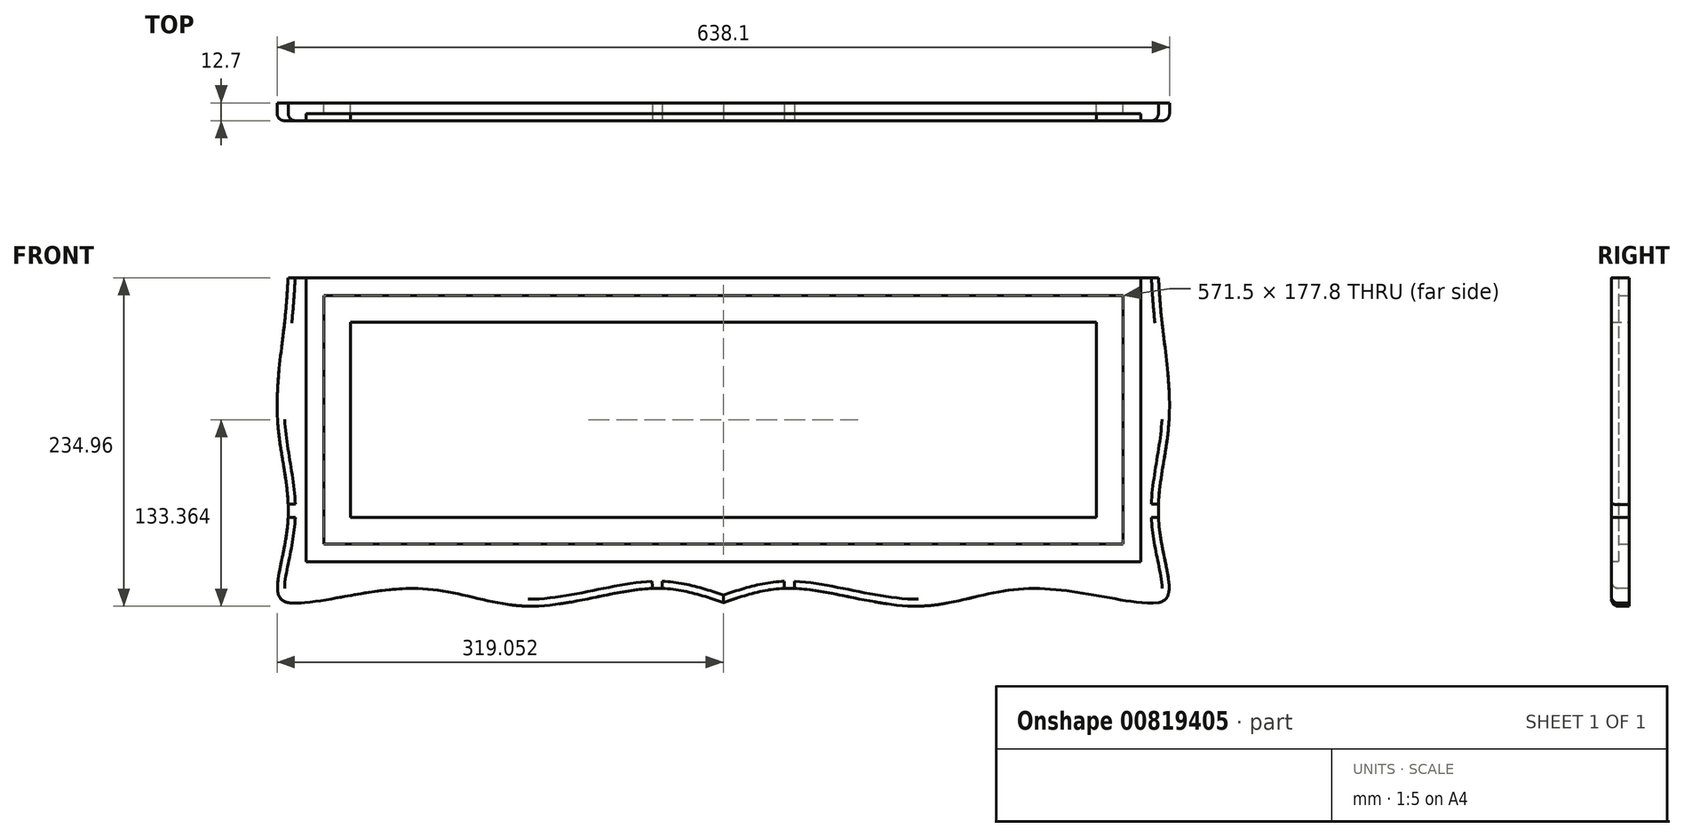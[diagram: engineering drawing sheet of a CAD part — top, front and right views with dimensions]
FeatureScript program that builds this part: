
annotation { "Feature Type Name" : "Feature", "Feature Type Description" : "" }
export const myFeature = defineFeature(function(context is Context, id is Id, definition is map)
    precondition{}
    {
        {
            var Q0;
            Q0=qCreatedBy(makeId("Front.planeOp"),FACE);
            var sketch = newSketch(context, id + "F0", { "sketchPlane" : qUnion([Q0])});
            skLineSegment(sketch, "E0.bottom", {"start": v(-290.57, 108.48) * mm, "end": v(331.73, 108.48) * mm});
            skLineSegment(sketch, "E0.top", {"start": v(-290.57, -113.77) * mm, "end": v(331.73, -113.77) * mm});
            skLineSegment(sketch, "E0.left", {"start": v(-290.57, 108.48) * mm, "end": v(-290.57, -113.77) * mm});
            skLineSegment(sketch, "E0.right", {"start": v(331.73, 108.48) * mm, "end": v(331.73, -113.77) * mm});
            skPoint(sketch, "E1", {"position": v(20.58, 108.48) * mm});
            skLineSegment(sketch, "E2.bottom", {"start": v(-246.12, 76.73) * mm, "end": v(287.28, 76.73) * mm});
            skLineSegment(sketch, "E2.top", {"start": v(-246.12, -62.97) * mm, "end": v(287.28, -62.97) * mm});
            skLineSegment(sketch, "E2.left", {"start": v(-246.12, 76.73) * mm, "end": v(-246.12, -62.97) * mm});
            skLineSegment(sketch, "E2.right", {"start": v(287.28, 76.73) * mm, "end": v(287.28, -62.97) * mm});
            skLineSegment(sketch, "E3.bottom", {"start": v(-265.17, 95.78) * mm, "end": v(306.33, 95.78) * mm});
            skLineSegment(sketch, "E3.top", {"start": v(-265.17, -82.02) * mm, "end": v(306.33, -82.02) * mm});
            skLineSegment(sketch, "E3.left", {"start": v(-265.17, 95.78) * mm, "end": v(-265.17, -82.02) * mm});
            skLineSegment(sketch, "E3.right", {"start": v(306.33, 95.78) * mm, "end": v(306.33, -82.02) * mm});
            skSolve(sketch);
        }
        {
            var Q0;
            Q0=makeQuery(id+"F0.imprint","IMPRINT",FACE,{"disambiguationData":[TD([[makeQuery(id+"F0.imprint","IMPRINT",EDGE,{"derivedFrom":sQuery(id+"F0.wireOp",EDGE,"E0.bottom")}),-1.0]])]});
            var Q1;
            Q1=makeQuery(id+"F0.imprint","IMPRINT",FACE,{"disambiguationData":[TD([[makeQuery(id+"F0.imprint","IMPRINT",EDGE,{"derivedFrom":sQuery(id+"F0.wireOp",EDGE,"E2.bottom")}),-1.0]])]});
            extrude(context, id + "F1", {"entities" : qUnion([Q0, Q1]), "depth" : 12.7 * mm, "offsetDistance" : 25.4 * mm});
        }
        {
            var Q0;
            Q0=makeQuery(id+"F1.opExtrude","CAP_FACE",FACE,{"disambiguationData":[OSD([sQuery(id+"F0.wireOp",EDGE,"E0.bottom"),sQuery(id+"F0.wireOp",EDGE,"E0.top"),sQuery(id+"F0.wireOp",EDGE,"E0.left"),sQuery(id+"F0.wireOp",EDGE,"E0.right")])],"isStart":false});
            var sketch = newSketch(context, id + "F2", { "sketchPlane" : qUnion([Q0])});
            skPoint(sketch, "E4", {"position": v(20.58, 108.48) * mm});
            skSolve(sketch);
        }
        {
            var Q0;
            {var subQ0=sQuery(id+"F0.wireOp",EDGE,"E0.right");var subQ1=sQuery(id+"F0.wireOp",EDGE,"E0.bottom");var subQ2=sQuery(id+"F0.wireOp",EDGE,"E0.left");var subQ3=sQuery(id+"F0.wireOp",EDGE,"E0.top");Q0=makeQuery(id+"FjgwLtvUwF4HY63_1.boolean.opBoolean","SPLIT",FACE,{"disambiguationData":[TD([makeQuery(id+"F1.opExtrude","SWEPT_FACE",FACE,{"disambiguationData":[OSD([subQ1])]})])],"derivedFrom":makeQuery(id+"F1.opExtrude","CAP_FACE",FACE,{"disambiguationData":[OSD([subQ1,subQ3,subQ2,subQ0])],"isStart":false})});}
            var sketch = newSketch(context, id + "F3", { "sketchPlane" : qUnion([Q0])});
            skPoint(sketch, "E5", {"position": v(-290.57, -62.97) * mm});
            skPoint(sketch, "E6", {"position": v(-290.57, 6.88) * mm});
            skPoint(sketch, "E7", {"position": v(-290.57, 76.73) * mm});
            skLineSegment(sketch, "E8", {"start": v(-290.57, 76.73) * mm, "end": v(-293.1, 76.73) * mm});
            skLineSegment(sketch, "E9", {"start": v(-290.57, 6.88) * mm, "end": v(-298.19, 6.88) * mm});
            skLineSegment(sketch, "E10", {"start": v(-290.57, -113.77) * mm, "end": v(-298.19, -113.77) * mm});
            skLineSegment(sketch, "E11", {"start": v(-290.57, -113.77) * mm, "end": v(-290.57, -123.93) * mm});
            skPoint(sketch, "E12", {"position": v(-201.67, -113.77) * mm});
            skPoint(sketch, "E13", {"position": v(20.58, -113.77) * mm});
            skPoint(sketch, "E14", {"position": v(-30.22, -113.77) * mm});
            skPoint(sketch, "E15", {"position": v(-119.12, -113.77) * mm});
            skPoint(sketch, "E16", {"position": v(71.38, -113.77) * mm});
            skPoint(sketch, "E17", {"position": v(160.28, -113.77) * mm});
            skPoint(sketch, "E18", {"position": v(242.83, -113.77) * mm});
            skPoint(sketch, "E19", {"position": v(331.73, -62.97) * mm});
            skPoint(sketch, "E20", {"position": v(331.73, 6.88) * mm});
            skPoint(sketch, "E21", {"position": v(331.73, 76.73) * mm});
            skLineSegment(sketch, "E22", {"start": v(331.73, 76.73) * mm, "end": v(334.27, 76.73) * mm});
            skLineSegment(sketch, "E23", {"start": v(331.73, 6.88) * mm, "end": v(339.35, 6.88) * mm});
            skLineSegment(sketch, "E24", {"start": v(331.73, -113.77) * mm, "end": v(339.35, -113.77) * mm});
            skLineSegment(sketch, "E25", {"start": v(331.73, -113.77) * mm, "end": v(331.73, -123.93) * mm});
            skLineSegment(sketch, "E26", {"start": v(-119.12, -113.77) * mm, "end": v(-119.12, -126.47) * mm});
            skLineSegment(sketch, "E27", {"start": v(20.58, -113.77) * mm, "end": v(20.58, -123.93) * mm});
            skLineSegment(sketch, "E28", {"start": v(160.28, -113.77) * mm, "end": v(160.28, -126.47) * mm});
            skFitSpline(sketch, "E29", {"points": [v(-290.57, 108.48) * mm, v(-293.1, 76.73) * mm, v(-298.19, 6.88) * mm, v(-290.57, -62.97) * mm, v(-298.19, -113.77) * mm, v(-290.57, -123.93) * mm, v(-201.67, -113.77) * mm, v(-119.12, -126.47) * mm, v(-30.22, -113.77) * mm, v(20.58, -123.93) * mm], "startDerivative": vector(-26.2, -341.82) * mm, "endDerivative": vector(438.15, -148.5) * mm});
            skFitSpline(sketch, "E30", {"points": [v(331.73, 108.48) * mm, v(334.27, 76.73) * mm, v(339.35, 6.88) * mm, v(331.73, -62.97) * mm, v(339.35, -113.77) * mm, v(331.73, -123.93) * mm, v(242.83, -113.77) * mm, v(160.28, -126.47) * mm, v(71.38, -113.77) * mm, v(20.58, -123.93) * mm], "startDerivative": vector(26.2, -341.82) * mm, "endDerivative": vector(-438.15, -148.5) * mm});
            skSolve(sketch);
        }
        {
            var Q0;
            {var subQ0=sQuery(id+"F3.wireOp",EDGE,"E27");Q0=makeQuery(id+"F3.imprint","IMPRINT",FACE,{"disambiguationData":[TD([[makeQuery(id+"F3.imprint","IMPRINT",EDGE,{"derivedFrom":subQ0}),-1.0]])]});}
            var Q1;
            {var subQ0=sQuery(id+"F3.wireOp",EDGE,"E27");Q1=makeQuery(id+"F3.imprint","IMPRINT",FACE,{"disambiguationData":[TD([[makeQuery(id+"F3.imprint","IMPRINT",EDGE,{"derivedFrom":subQ0}),1.0]])]});}
            var Q2;
            {var subQ0=sQuery(id+"F3.wireOp",EDGE,"E26");Q2=makeQuery(id+"F3.imprint","IMPRINT",FACE,{"disambiguationData":[TD([[makeQuery(id+"F3.imprint","IMPRINT",EDGE,{"derivedFrom":subQ0}),1.0]])]});}
            var Q3;
            {var subQ0=sQuery(id+"F3.wireOp",EDGE,"E26");Q3=makeQuery(id+"F3.imprint","IMPRINT",FACE,{"disambiguationData":[TD([[makeQuery(id+"F3.imprint","IMPRINT",EDGE,{"derivedFrom":subQ0}),-1.0]])]});}
            var Q4;
            {var subQ0=sQuery(id+"F3.wireOp",EDGE,"E11");Q4=makeQuery(id+"F3.imprint","IMPRINT",FACE,{"disambiguationData":[TD([[makeQuery(id+"F3.imprint","IMPRINT",EDGE,{"derivedFrom":subQ0}),1.0]])]});}
            var Q5;
            {var subQ0=sQuery(id+"F3.wireOp",EDGE,"E10");Q5=makeQuery(id+"F3.imprint","IMPRINT",FACE,{"disambiguationData":[TD([[makeQuery(id+"F3.imprint","IMPRINT",EDGE,{"derivedFrom":subQ0}),1.0]])]});}
            var Q6;
            {var subQ0=sQuery(id+"F3.wireOp",EDGE,"E10");Q6=makeQuery(id+"F3.imprint","IMPRINT",FACE,{"disambiguationData":[TD([[makeQuery(id+"F3.imprint","IMPRINT",EDGE,{"derivedFrom":subQ0}),-1.0]])]});}
            var Q7;
            {var subQ0=sQuery(id+"F3.wireOp",EDGE,"E9");Q7=makeQuery(id+"F3.imprint","IMPRINT",FACE,{"disambiguationData":[TD([[makeQuery(id+"F3.imprint","IMPRINT",EDGE,{"derivedFrom":subQ0}),1.0]])]});}
            var Q8;
            {var subQ0=sQuery(id+"F3.wireOp",EDGE,"E8");Q8=makeQuery(id+"F3.imprint","IMPRINT",FACE,{"disambiguationData":[TD([[makeQuery(id+"F3.imprint","IMPRINT",EDGE,{"derivedFrom":subQ0}),1.0]])]});}
            var Q9;
            {var subQ0=makeQuery(id+"F1.opExtrude","CAP_EDGE",EDGE,{"disambiguationData":[OSD([sQuery(id+"F0.wireOp",EDGE,"E0.bottom")])],"isStart":false});Q9=makeQuery(id+"F3.imprint","IMPRINT",FACE,{"disambiguationData":[TD([[makeQuery(id+"F3.imprint","IMPRINT",EDGE,{"derivedFrom":subQ0}),-1.0]])]});}
            var Q10;
            {var subQ0=sQuery(id+"F3.wireOp",EDGE,"E28");Q10=makeQuery(id+"F3.imprint","IMPRINT",FACE,{"disambiguationData":[TD([[makeQuery(id+"F3.imprint","IMPRINT",EDGE,{"derivedFrom":subQ0}),-1.0]])]});}
            var Q11;
            {var subQ0=sQuery(id+"F3.wireOp",EDGE,"E28");Q11=makeQuery(id+"F3.imprint","IMPRINT",FACE,{"disambiguationData":[TD([[makeQuery(id+"F3.imprint","IMPRINT",EDGE,{"derivedFrom":subQ0}),1.0]])]});}
            var Q12;
            {var subQ0=sQuery(id+"F3.wireOp",EDGE,"E25");Q12=makeQuery(id+"F3.imprint","IMPRINT",FACE,{"disambiguationData":[TD([[makeQuery(id+"F3.imprint","IMPRINT",EDGE,{"derivedFrom":subQ0}),-1.0]])]});}
            var Q13;
            {var subQ0=sQuery(id+"F3.wireOp",EDGE,"E24");Q13=makeQuery(id+"F3.imprint","IMPRINT",FACE,{"disambiguationData":[TD([[makeQuery(id+"F3.imprint","IMPRINT",EDGE,{"derivedFrom":subQ0}),-1.0]])]});}
            var Q14;
            {var subQ0=sQuery(id+"F3.wireOp",EDGE,"E24");Q14=makeQuery(id+"F3.imprint","IMPRINT",FACE,{"disambiguationData":[TD([[makeQuery(id+"F3.imprint","IMPRINT",EDGE,{"derivedFrom":subQ0}),1.0]])]});}
            var Q15;
            {var subQ0=sQuery(id+"F3.wireOp",EDGE,"E23");Q15=makeQuery(id+"F3.imprint","IMPRINT",FACE,{"disambiguationData":[TD([[makeQuery(id+"F3.imprint","IMPRINT",EDGE,{"derivedFrom":subQ0}),-1.0]])]});}
            var Q16;
            {var subQ0=sQuery(id+"F3.wireOp",EDGE,"E22");Q16=makeQuery(id+"F3.imprint","IMPRINT",FACE,{"disambiguationData":[TD([[makeQuery(id+"F3.imprint","IMPRINT",EDGE,{"derivedFrom":subQ0}),-1.0]])]});}
            var Q17;
            {var subQ0=sQuery(id+"F3.wireOp",EDGE,"E22");Q17=makeQuery(id+"F3.imprint","IMPRINT",FACE,{"disambiguationData":[TD([[makeQuery(id+"F3.imprint","IMPRINT",EDGE,{"derivedFrom":subQ0}),1.0]])]});}
            var Q18;
            {var subQ0=sQuery(id+"F3.wireOp",EDGE,"E8");Q18=makeQuery(id+"F3.imprint","IMPRINT",FACE,{"disambiguationData":[TD([[makeQuery(id+"F3.imprint","IMPRINT",EDGE,{"derivedFrom":subQ0}),-1.0]])]});}
            extrude(context, id + "F4", {"entities" : qUnion([Q0, Q1, Q2, Q3, Q4, Q5, Q6, Q7, Q8, Q9, Q10, Q11, Q12, Q13, Q14, Q15, Q16, Q17, Q18]), "operationType" : NewBodyOperationType.ADD, "depth" : -12.7 * mm, "offsetDistance" : 25.4 * mm});
        }
        {
            var Q0;
            {var subQ0=sQuery(id+"F3.wireOp",EDGE,"8007402e-1a4e-4a06-85a5-2af08e553504");var subQ1=sQuery(id+"F0.wireOp",EDGE,"E0.left");var subQ2=sQuery(id+"F0.wireOp",EDGE,"E0.top");var subQ3=sQuery(id+"F0.wireOp",EDGE,"E0.bottom");Q0=makeQuery(id+"F4.boolean.opBoolean","SPLIT",EDGE,{"disambiguationData":[TD([makeQuery(id+"F1.opExtrude","CAP_FACE",FACE,{"disambiguationData":[OSD([subQ3,subQ2,subQ1,sQuery(id+"F0.wireOp",EDGE,"E0.right")])],"isStart":false}),makeQuery(id+"F1.opExtrude","SWEPT_FACE",FACE,{"disambiguationData":[OSD([subQ2])]}),makeQuery(id+"F1.opExtrude","SWEPT_FACE",FACE,{"disambiguationData":[OSD([subQ1])]}),makeQuery(id+"F4.opExtrude","SWEPT_FACE",FACE,{"disambiguationData":[OSD([subQ0])]}),makeQuery(id+"F4.opExtrude","CAP_FACE",FACE,{"disambiguationData":[OSD([subQ3,sQuery(id+"F2.wireOp",EDGE,"fcba4419-a2ee-464f-be9d-58f11bf3418b.sketch_text.stroke-0"),sQuery(id+"F2.wireOp",EDGE,"fcba4419-a2ee-464f-be9d-58f11bf3418b.sketch_text.stroke-1"),sQuery(id+"F2.wireOp",EDGE,"fcba4419-a2ee-464f-be9d-58f11bf3418b.sketch_text.stroke-2"),sQuery(id+"F2.wireOp",EDGE,"fcba4419-a2ee-464f-be9d-58f11bf3418b.sketch_text.stroke-3"),sQuery(id+"F2.wireOp",EDGE,"fcba4419-a2ee-464f-be9d-58f11bf3418b.sketch_text.stroke-4"),sQuery(id+"F2.wireOp",EDGE,"fcba4419-a2ee-464f-be9d-58f11bf3418b.sketch_text.stroke-5"),sQuery(id+"F2.wireOp",EDGE,"fcba4419-a2ee-464f-be9d-58f11bf3418b.sketch_text.stroke-6"),sQuery(id+"F2.wireOp",EDGE,"fcba4419-a2ee-464f-be9d-58f11bf3418b.sketch_text.stroke-7"),sQuery(id+"F2.wireOp",EDGE,"fcba4419-a2ee-464f-be9d-58f11bf3418b.sketch_text.stroke-8"),sQuery(id+"F2.wireOp",EDGE,"fcba4419-a2ee-464f-be9d-58f11bf3418b.sketch_text.stroke-9"),sQuery(id+"F2.wireOp",EDGE,"fcba4419-a2ee-464f-be9d-58f11bf3418b.sketch_text.stroke-10"),sQuery(id+"F2.wireOp",EDGE,"fcba4419-a2ee-464f-be9d-58f11bf3418b.sketch_text.stroke-11"),sQuery(id+"F2.wireOp",EDGE,"fcba4419-a2ee-464f-be9d-58f11bf3418b.sketch_text.stroke-12"),sQuery(id+"F2.wireOp",EDGE,"fcba4419-a2ee-464f-be9d-58f11bf3418b.sketch_text.stroke-13"),sQuery(id+"F2.wireOp",EDGE,"fcba4419-a2ee-464f-be9d-58f11bf3418b.sketch_text.stroke-14"),sQuery(id+"F2.wireOp",EDGE,"fcba4419-a2ee-464f-be9d-58f11bf3418b.sketch_text.stroke-15"),sQuery(id+"F2.wireOp",EDGE,"fcba4419-a2ee-464f-be9d-58f11bf3418b.sketch_text.stroke-16"),sQuery(id+"F2.wireOp",EDGE,"fcba4419-a2ee-464f-be9d-58f11bf3418b.sketch_text.stroke-17"),sQuery(id+"F2.wireOp",EDGE,"fcba4419-a2ee-464f-be9d-58f11bf3418b.sketch_text.stroke-18"),sQuery(id+"F2.wireOp",EDGE,"fcba4419-a2ee-464f-be9d-58f11bf3418b.sketch_text.stroke-19"),sQuery(id+"F2.wireOp",EDGE,"fcba4419-a2ee-464f-be9d-58f11bf3418b.sketch_text.stroke-20"),sQuery(id+"F2.wireOp",EDGE,"fcba4419-a2ee-464f-be9d-58f11bf3418b.sketch_text.stroke-21"),sQuery(id+"F2.wireOp",EDGE,"fcba4419-a2ee-464f-be9d-58f11bf3418b.sketch_text.stroke-22"),sQuery(id+"F2.wireOp",EDGE,"fcba4419-a2ee-464f-be9d-58f11bf3418b.sketch_text.stroke-23"),sQuery(id+"F2.wireOp",EDGE,"fcba4419-a2ee-464f-be9d-58f11bf3418b.sketch_text.stroke-24"),sQuery(id+"F2.wireOp",EDGE,"fcba4419-a2ee-464f-be9d-58f11bf3418b.sketch_text.stroke-25"),sQuery(id+"F2.wireOp",EDGE,"fcba4419-a2ee-464f-be9d-58f11bf3418b.sketch_text.stroke-26"),sQuery(id+"F2.wireOp",EDGE,"fcba4419-a2ee-464f-be9d-58f11bf3418b.sketch_text.stroke-27"),sQuery(id+"F2.wireOp",EDGE,"fcba4419-a2ee-464f-be9d-58f11bf3418b.sketch_text.stroke-28"),sQuery(id+"F2.wireOp",EDGE,"fcba4419-a2ee-464f-be9d-58f11bf3418b.sketch_text.stroke-29"),sQuery(id+"F2.wireOp",EDGE,"fcba4419-a2ee-464f-be9d-58f11bf3418b.sketch_text.stroke-30"),sQuery(id+"F2.wireOp",EDGE,"fcba4419-a2ee-464f-be9d-58f11bf3418b.sketch_text.stroke-31"),sQuery(id+"F2.wireOp",EDGE,"fcba4419-a2ee-464f-be9d-58f11bf3418b.sketch_text.stroke-32"),sQuery(id+"F2.wireOp",EDGE,"fcba4419-a2ee-464f-be9d-58f11bf3418b.sketch_text.stroke-33"),sQuery(id+"F2.wireOp",EDGE,"fcba4419-a2ee-464f-be9d-58f11bf3418b.sketch_text.stroke-34"),sQuery(id+"F2.wireOp",EDGE,"fcba4419-a2ee-464f-be9d-58f11bf3418b.sketch_text.stroke-35"),sQuery(id+"F2.wireOp",EDGE,"fcba4419-a2ee-464f-be9d-58f11bf3418b.sketch_text.stroke-36"),sQuery(id+"F2.wireOp",EDGE,"fcba4419-a2ee-464f-be9d-58f11bf3418b.sketch_text.stroke-37"),sQuery(id+"F2.wireOp",EDGE,"fcba4419-a2ee-464f-be9d-58f11bf3418b.sketch_text.stroke-38"),sQuery(id+"F2.wireOp",EDGE,"fcba4419-a2ee-464f-be9d-58f11bf3418b.sketch_text.stroke-39"),sQuery(id+"F2.wireOp",EDGE,"fcba4419-a2ee-464f-be9d-58f11bf3418b.sketch_text.stroke-40"),sQuery(id+"F2.wireOp",EDGE,"fcba4419-a2ee-464f-be9d-58f11bf3418b.sketch_text.stroke-41"),sQuery(id+"F2.wireOp",EDGE,"fcba4419-a2ee-464f-be9d-58f11bf3418b.sketch_text.stroke-42"),sQuery(id+"F2.wireOp",EDGE,"fcba4419-a2ee-464f-be9d-58f11bf3418b.sketch_text.stroke-43"),sQuery(id+"F2.wireOp",EDGE,"fcba4419-a2ee-464f-be9d-58f11bf3418b.sketch_text.stroke-44"),sQuery(id+"F2.wireOp",EDGE,"fcba4419-a2ee-464f-be9d-58f11bf3418b.sketch_text.stroke-45"),sQuery(id+"F2.wireOp",EDGE,"fcba4419-a2ee-464f-be9d-58f11bf3418b.sketch_text.stroke-46"),sQuery(id+"F2.wireOp",EDGE,"fcba4419-a2ee-464f-be9d-58f11bf3418b.sketch_text.stroke-47"),sQuery(id+"F2.wireOp",EDGE,"fcba4419-a2ee-464f-be9d-58f11bf3418b.sketch_text.stroke-48"),sQuery(id+"F2.wireOp",EDGE,"fcba4419-a2ee-464f-be9d-58f11bf3418b.sketch_text.stroke-49"),sQuery(id+"F2.wireOp",EDGE,"fcba4419-a2ee-464f-be9d-58f11bf3418b.sketch_text.stroke-50"),sQuery(id+"F2.wireOp",EDGE,"fcba4419-a2ee-464f-be9d-58f11bf3418b.sketch_text.stroke-51"),sQuery(id+"F2.wireOp",EDGE,"fcba4419-a2ee-464f-be9d-58f11bf3418b.sketch_text.stroke-52"),sQuery(id+"F2.wireOp",EDGE,"fcba4419-a2ee-464f-be9d-58f11bf3418b.sketch_text.stroke-53"),sQuery(id+"F2.wireOp",EDGE,"fcba4419-a2ee-464f-be9d-58f11bf3418b.sketch_text.stroke-54"),sQuery(id+"F2.wireOp",EDGE,"fcba4419-a2ee-464f-be9d-58f11bf3418b.sketch_text.stroke-55"),sQuery(id+"F2.wireOp",EDGE,"fcba4419-a2ee-464f-be9d-58f11bf3418b.sketch_text.stroke-56"),sQuery(id+"F2.wireOp",EDGE,"fcba4419-a2ee-464f-be9d-58f11bf3418b.sketch_text.stroke-57"),sQuery(id+"F2.wireOp",EDGE,"fcba4419-a2ee-464f-be9d-58f11bf3418b.sketch_text.stroke-58"),sQuery(id+"F2.wireOp",EDGE,"fcba4419-a2ee-464f-be9d-58f11bf3418b.sketch_text.stroke-59"),sQuery(id+"F2.wireOp",EDGE,"fcba4419-a2ee-464f-be9d-58f11bf3418b.sketch_text.stroke-60"),sQuery(id+"F2.wireOp",EDGE,"fcba4419-a2ee-464f-be9d-58f11bf3418b.sketch_text.stroke-61"),sQuery(id+"F2.wireOp",EDGE,"fcba4419-a2ee-464f-be9d-58f11bf3418b.sketch_text.stroke-62"),sQuery(id+"F2.wireOp",EDGE,"fcba4419-a2ee-464f-be9d-58f11bf3418b.sketch_text.stroke-63"),sQuery(id+"F2.wireOp",EDGE,"fcba4419-a2ee-464f-be9d-58f11bf3418b.sketch_text.stroke-64"),sQuery(id+"F2.wireOp",EDGE,"fcba4419-a2ee-464f-be9d-58f11bf3418b.sketch_text.stroke-65"),sQuery(id+"F2.wireOp",EDGE,"fcba4419-a2ee-464f-be9d-58f11bf3418b.sketch_text.stroke-66"),sQuery(id+"F2.wireOp",EDGE,"fcba4419-a2ee-464f-be9d-58f11bf3418b.sketch_text.stroke-67"),sQuery(id+"F2.wireOp",EDGE,"fcba4419-a2ee-464f-be9d-58f11bf3418b.sketch_text.stroke-68"),sQuery(id+"F2.wireOp",EDGE,"fcba4419-a2ee-464f-be9d-58f11bf3418b.sketch_text.stroke-69"),sQuery(id+"F2.wireOp",EDGE,"fcba4419-a2ee-464f-be9d-58f11bf3418b.sketch_text.stroke-70"),sQuery(id+"F2.wireOp",EDGE,"fcba4419-a2ee-464f-be9d-58f11bf3418b.sketch_text.stroke-71"),sQuery(id+"F2.wireOp",EDGE,"fcba4419-a2ee-464f-be9d-58f11bf3418b.sketch_text.stroke-72"),sQuery(id+"F2.wireOp",EDGE,"fcba4419-a2ee-464f-be9d-58f11bf3418b.sketch_text.stroke-73"),sQuery(id+"F2.wireOp",EDGE,"fcba4419-a2ee-464f-be9d-58f11bf3418b.sketch_text.stroke-74"),sQuery(id+"F2.wireOp",EDGE,"fcba4419-a2ee-464f-be9d-58f11bf3418b.sketch_text.stroke-75"),sQuery(id+"F2.wireOp",EDGE,"fcba4419-a2ee-464f-be9d-58f11bf3418b.sketch_text.stroke-76"),sQuery(id+"F2.wireOp",EDGE,"fcba4419-a2ee-464f-be9d-58f11bf3418b.sketch_text.stroke-77"),sQuery(id+"F2.wireOp",EDGE,"fcba4419-a2ee-464f-be9d-58f11bf3418b.sketch_text.stroke-78"),sQuery(id+"F2.wireOp",EDGE,"fcba4419-a2ee-464f-be9d-58f11bf3418b.sketch_text.stroke-79"),sQuery(id+"F2.wireOp",EDGE,"fcba4419-a2ee-464f-be9d-58f11bf3418b.sketch_text.stroke-80"),sQuery(id+"F2.wireOp",EDGE,"fcba4419-a2ee-464f-be9d-58f11bf3418b.sketch_text.stroke-81"),sQuery(id+"F2.wireOp",EDGE,"fcba4419-a2ee-464f-be9d-58f11bf3418b.sketch_text.stroke-82"),sQuery(id+"F2.wireOp",EDGE,"fcba4419-a2ee-464f-be9d-58f11bf3418b.sketch_text.stroke-83"),sQuery(id+"F2.wireOp",EDGE,"fcba4419-a2ee-464f-be9d-58f11bf3418b.sketch_text.stroke-84"),sQuery(id+"F2.wireOp",EDGE,"fcba4419-a2ee-464f-be9d-58f11bf3418b.sketch_text.stroke-85"),sQuery(id+"F2.wireOp",EDGE,"fcba4419-a2ee-464f-be9d-58f11bf3418b.sketch_text.stroke-86"),sQuery(id+"F2.wireOp",EDGE,"fcba4419-a2ee-464f-be9d-58f11bf3418b.sketch_text.stroke-87"),sQuery(id+"F2.wireOp",EDGE,"fcba4419-a2ee-464f-be9d-58f11bf3418b.sketch_text.stroke-88"),sQuery(id+"F2.wireOp",EDGE,"fcba4419-a2ee-464f-be9d-58f11bf3418b.sketch_text.stroke-89"),sQuery(id+"F2.wireOp",EDGE,"fcba4419-a2ee-464f-be9d-58f11bf3418b.sketch_text.stroke-90"),sQuery(id+"F2.wireOp",EDGE,"fcba4419-a2ee-464f-be9d-58f11bf3418b.sketch_text.stroke-91"),sQuery(id+"F2.wireOp",EDGE,"fcba4419-a2ee-464f-be9d-58f11bf3418b.sketch_text.stroke-92"),sQuery(id+"F2.wireOp",EDGE,"fcba4419-a2ee-464f-be9d-58f11bf3418b.sketch_text.stroke-93"),sQuery(id+"F2.wireOp",EDGE,"fcba4419-a2ee-464f-be9d-58f11bf3418b.sketch_text.stroke-94"),sQuery(id+"F2.wireOp",EDGE,"fcba4419-a2ee-464f-be9d-58f11bf3418b.sketch_text.stroke-95"),sQuery(id+"F2.wireOp",EDGE,"fcba4419-a2ee-464f-be9d-58f11bf3418b.sketch_text.stroke-96"),sQuery(id+"F2.wireOp",EDGE,"fcba4419-a2ee-464f-be9d-58f11bf3418b.sketch_text.stroke-97"),sQuery(id+"F2.wireOp",EDGE,"fcba4419-a2ee-464f-be9d-58f11bf3418b.sketch_text.stroke-98"),sQuery(id+"F2.wireOp",EDGE,"fcba4419-a2ee-464f-be9d-58f11bf3418b.sketch_text.stroke-99"),sQuery(id+"F2.wireOp",EDGE,"fcba4419-a2ee-464f-be9d-58f11bf3418b.sketch_text.stroke-100"),sQuery(id+"F2.wireOp",EDGE,"fcba4419-a2ee-464f-be9d-58f11bf3418b.sketch_text.stroke-101"),sQuery(id+"F2.wireOp",EDGE,"fcba4419-a2ee-464f-be9d-58f11bf3418b.sketch_text.stroke-102"),sQuery(id+"F2.wireOp",EDGE,"fcba4419-a2ee-464f-be9d-58f11bf3418b.sketch_text.stroke-103"),sQuery(id+"F2.wireOp",EDGE,"fcba4419-a2ee-464f-be9d-58f11bf3418b.sketch_text.stroke-104"),sQuery(id+"F2.wireOp",EDGE,"fcba4419-a2ee-464f-be9d-58f11bf3418b.sketch_text.stroke-105"),sQuery(id+"F2.wireOp",EDGE,"fcba4419-a2ee-464f-be9d-58f11bf3418b.sketch_text.stroke-106"),sQuery(id+"F2.wireOp",EDGE,"fcba4419-a2ee-464f-be9d-58f11bf3418b.sketch_text.stroke-107"),sQuery(id+"F2.wireOp",EDGE,"fcba4419-a2ee-464f-be9d-58f11bf3418b.sketch_text.stroke-108"),sQuery(id+"F2.wireOp",EDGE,"fcba4419-a2ee-464f-be9d-58f11bf3418b.sketch_text.stroke-109"),sQuery(id+"F2.wireOp",EDGE,"fcba4419-a2ee-464f-be9d-58f11bf3418b.sketch_text.stroke-110"),sQuery(id+"F2.wireOp",EDGE,"fcba4419-a2ee-464f-be9d-58f11bf3418b.sketch_text.stroke-111"),sQuery(id+"F2.wireOp",EDGE,"fcba4419-a2ee-464f-be9d-58f11bf3418b.sketch_text.stroke-112"),sQuery(id+"F2.wireOp",EDGE,"fcba4419-a2ee-464f-be9d-58f11bf3418b.sketch_text.stroke-113"),sQuery(id+"F2.wireOp",EDGE,"fcba4419-a2ee-464f-be9d-58f11bf3418b.sketch_text.stroke-114"),sQuery(id+"F2.wireOp",EDGE,"fcba4419-a2ee-464f-be9d-58f11bf3418b.sketch_text.stroke-115"),sQuery(id+"F2.wireOp",EDGE,"fcba4419-a2ee-464f-be9d-58f11bf3418b.sketch_text.stroke-116"),sQuery(id+"F2.wireOp",EDGE,"fcba4419-a2ee-464f-be9d-58f11bf3418b.sketch_text.stroke-117"),sQuery(id+"F2.wireOp",EDGE,"fcba4419-a2ee-464f-be9d-58f11bf3418b.sketch_text.stroke-118"),sQuery(id+"F2.wireOp",EDGE,"fcba4419-a2ee-464f-be9d-58f11bf3418b.sketch_text.stroke-119"),sQuery(id+"F2.wireOp",EDGE,"fcba4419-a2ee-464f-be9d-58f11bf3418b.sketch_text.stroke-120"),sQuery(id+"F2.wireOp",EDGE,"fcba4419-a2ee-464f-be9d-58f11bf3418b.sketch_text.stroke-121"),sQuery(id+"F2.wireOp",EDGE,"fcba4419-a2ee-464f-be9d-58f11bf3418b.sketch_text.stroke-122"),sQuery(id+"F2.wireOp",EDGE,"fcba4419-a2ee-464f-be9d-58f11bf3418b.sketch_text.stroke-123"),sQuery(id+"F2.wireOp",EDGE,"fcba4419-a2ee-464f-be9d-58f11bf3418b.sketch_text.stroke-124"),sQuery(id+"F2.wireOp",EDGE,"fcba4419-a2ee-464f-be9d-58f11bf3418b.sketch_text.stroke-125"),sQuery(id+"F2.wireOp",EDGE,"fcba4419-a2ee-464f-be9d-58f11bf3418b.sketch_text.stroke-126"),sQuery(id+"F2.wireOp",EDGE,"fcba4419-a2ee-464f-be9d-58f11bf3418b.sketch_text.stroke-127"),sQuery(id+"F2.wireOp",EDGE,"fcba4419-a2ee-464f-be9d-58f11bf3418b.sketch_text.stroke-128"),sQuery(id+"F2.wireOp",EDGE,"fcba4419-a2ee-464f-be9d-58f11bf3418b.sketch_text.stroke-129"),sQuery(id+"F2.wireOp",EDGE,"fcba4419-a2ee-464f-be9d-58f11bf3418b.sketch_text.stroke-130"),sQuery(id+"F2.wireOp",EDGE,"fcba4419-a2ee-464f-be9d-58f11bf3418b.sketch_text.stroke-131"),sQuery(id+"F2.wireOp",EDGE,"fcba4419-a2ee-464f-be9d-58f11bf3418b.sketch_text.stroke-132"),sQuery(id+"F2.wireOp",EDGE,"fcba4419-a2ee-464f-be9d-58f11bf3418b.sketch_text.stroke-133"),sQuery(id+"F2.wireOp",EDGE,"fcba4419-a2ee-464f-be9d-58f11bf3418b.sketch_text.stroke-134"),sQuery(id+"F2.wireOp",EDGE,"fcba4419-a2ee-464f-be9d-58f11bf3418b.sketch_text.stroke-135"),sQuery(id+"F2.wireOp",EDGE,"fcba4419-a2ee-464f-be9d-58f11bf3418b.sketch_text.stroke-136"),sQuery(id+"F2.wireOp",EDGE,"fcba4419-a2ee-464f-be9d-58f11bf3418b.sketch_text.stroke-137"),sQuery(id+"F2.wireOp",EDGE,"fcba4419-a2ee-464f-be9d-58f11bf3418b.sketch_text.stroke-138"),sQuery(id+"F2.wireOp",EDGE,"fcba4419-a2ee-464f-be9d-58f11bf3418b.sketch_text.stroke-139"),sQuery(id+"F2.wireOp",EDGE,"fcba4419-a2ee-464f-be9d-58f11bf3418b.sketch_text.stroke-140"),sQuery(id+"F2.wireOp",EDGE,"fcba4419-a2ee-464f-be9d-58f11bf3418b.sketch_text.stroke-141"),sQuery(id+"F2.wireOp",EDGE,"fcba4419-a2ee-464f-be9d-58f11bf3418b.sketch_text.stroke-142"),sQuery(id+"F2.wireOp",EDGE,"fcba4419-a2ee-464f-be9d-58f11bf3418b.sketch_text.stroke-143"),sQuery(id+"F2.wireOp",EDGE,"fcba4419-a2ee-464f-be9d-58f11bf3418b.sketch_text.stroke-144"),sQuery(id+"F2.wireOp",EDGE,"fcba4419-a2ee-464f-be9d-58f11bf3418b.sketch_text.stroke-145"),sQuery(id+"F2.wireOp",EDGE,"fcba4419-a2ee-464f-be9d-58f11bf3418b.sketch_text.stroke-146"),sQuery(id+"F2.wireOp",EDGE,"fcba4419-a2ee-464f-be9d-58f11bf3418b.sketch_text.stroke-147"),sQuery(id+"F2.wireOp",EDGE,"fcba4419-a2ee-464f-be9d-58f11bf3418b.sketch_text.stroke-148"),sQuery(id+"F2.wireOp",EDGE,"fcba4419-a2ee-464f-be9d-58f11bf3418b.sketch_text.stroke-149"),sQuery(id+"F2.wireOp",EDGE,"fcba4419-a2ee-464f-be9d-58f11bf3418b.sketch_text.stroke-150"),sQuery(id+"F2.wireOp",EDGE,"fcba4419-a2ee-464f-be9d-58f11bf3418b.sketch_text.stroke-151"),sQuery(id+"F2.wireOp",EDGE,"fcba4419-a2ee-464f-be9d-58f11bf3418b.sketch_text.stroke-152"),sQuery(id+"F2.wireOp",EDGE,"fcba4419-a2ee-464f-be9d-58f11bf3418b.sketch_text.stroke-153"),sQuery(id+"F2.wireOp",EDGE,"fcba4419-a2ee-464f-be9d-58f11bf3418b.sketch_text.stroke-154"),sQuery(id+"F2.wireOp",EDGE,"fcba4419-a2ee-464f-be9d-58f11bf3418b.sketch_text.stroke-155"),sQuery(id+"F2.wireOp",EDGE,"fcba4419-a2ee-464f-be9d-58f11bf3418b.sketch_text.stroke-156"),sQuery(id+"F2.wireOp",EDGE,"fcba4419-a2ee-464f-be9d-58f11bf3418b.sketch_text.stroke-157"),sQuery(id+"F2.wireOp",EDGE,"fcba4419-a2ee-464f-be9d-58f11bf3418b.sketch_text.stroke-158"),sQuery(id+"F2.wireOp",EDGE,"fcba4419-a2ee-464f-be9d-58f11bf3418b.sketch_text.stroke-159"),sQuery(id+"F2.wireOp",EDGE,"fcba4419-a2ee-464f-be9d-58f11bf3418b.sketch_text.stroke-160"),sQuery(id+"F2.wireOp",EDGE,"fcba4419-a2ee-464f-be9d-58f11bf3418b.sketch_text.stroke-161"),sQuery(id+"F2.wireOp",EDGE,"fcba4419-a2ee-464f-be9d-58f11bf3418b.sketch_text.stroke-162"),sQuery(id+"F2.wireOp",EDGE,"fcba4419-a2ee-464f-be9d-58f11bf3418b.sketch_text.stroke-163"),sQuery(id+"F2.wireOp",EDGE,"fcba4419-a2ee-464f-be9d-58f11bf3418b.sketch_text.stroke-164"),sQuery(id+"F2.wireOp",EDGE,"fcba4419-a2ee-464f-be9d-58f11bf3418b.sketch_text.stroke-165"),sQuery(id+"F2.wireOp",EDGE,"fcba4419-a2ee-464f-be9d-58f11bf3418b.sketch_text.stroke-166"),sQuery(id+"F2.wireOp",EDGE,"fcba4419-a2ee-464f-be9d-58f11bf3418b.sketch_text.stroke-167"),sQuery(id+"F2.wireOp",EDGE,"fcba4419-a2ee-464f-be9d-58f11bf3418b.sketch_text.stroke-168"),sQuery(id+"F2.wireOp",EDGE,"fcba4419-a2ee-464f-be9d-58f11bf3418b.sketch_text.stroke-169"),sQuery(id+"F2.wireOp",EDGE,"fcba4419-a2ee-464f-be9d-58f11bf3418b.sketch_text.stroke-170"),sQuery(id+"F2.wireOp",EDGE,"fcba4419-a2ee-464f-be9d-58f11bf3418b.sketch_text.stroke-171"),sQuery(id+"F2.wireOp",EDGE,"fcba4419-a2ee-464f-be9d-58f11bf3418b.sketch_text.stroke-172"),sQuery(id+"F2.wireOp",EDGE,"fcba4419-a2ee-464f-be9d-58f11bf3418b.sketch_text.stroke-173"),sQuery(id+"FHMxAyK4CFUKdhS_1.wireOp",EDGE,"1cb9c079-ea9b-4899-8069-e0e3048e911d.sketch_text.stroke-0"),sQuery(id+"FHMxAyK4CFUKdhS_1.wireOp",EDGE,"1cb9c079-ea9b-4899-8069-e0e3048e911d.sketch_text.stroke-1"),sQuery(id+"FHMxAyK4CFUKdhS_1.wireOp",EDGE,"1cb9c079-ea9b-4899-8069-e0e3048e911d.sketch_text.stroke-2"),sQuery(id+"FHMxAyK4CFUKdhS_1.wireOp",EDGE,"1cb9c079-ea9b-4899-8069-e0e3048e911d.sketch_text.stroke-3"),sQuery(id+"FHMxAyK4CFUKdhS_1.wireOp",EDGE,"1cb9c079-ea9b-4899-8069-e0e3048e911d.sketch_text.stroke-4"),sQuery(id+"FHMxAyK4CFUKdhS_1.wireOp",EDGE,"1cb9c079-ea9b-4899-8069-e0e3048e911d.sketch_text.stroke-5"),sQuery(id+"FHMxAyK4CFUKdhS_1.wireOp",EDGE,"1cb9c079-ea9b-4899-8069-e0e3048e911d.sketch_text.stroke-6"),sQuery(id+"FHMxAyK4CFUKdhS_1.wireOp",EDGE,"1cb9c079-ea9b-4899-8069-e0e3048e911d.sketch_text.stroke-7"),sQuery(id+"FHMxAyK4CFUKdhS_1.wireOp",EDGE,"1cb9c079-ea9b-4899-8069-e0e3048e911d.sketch_text.stroke-8"),sQuery(id+"FHMxAyK4CFUKdhS_1.wireOp",EDGE,"1cb9c079-ea9b-4899-8069-e0e3048e911d.sketch_text.stroke-9"),sQuery(id+"FHMxAyK4CFUKdhS_1.wireOp",EDGE,"1cb9c079-ea9b-4899-8069-e0e3048e911d.sketch_text.stroke-10"),sQuery(id+"FHMxAyK4CFUKdhS_1.wireOp",EDGE,"1cb9c079-ea9b-4899-8069-e0e3048e911d.sketch_text.stroke-11"),sQuery(id+"FHMxAyK4CFUKdhS_1.wireOp",EDGE,"1cb9c079-ea9b-4899-8069-e0e3048e911d.sketch_text.stroke-12"),sQuery(id+"FHMxAyK4CFUKdhS_1.wireOp",EDGE,"1cb9c079-ea9b-4899-8069-e0e3048e911d.sketch_text.stroke-13"),sQuery(id+"FHMxAyK4CFUKdhS_1.wireOp",EDGE,"1cb9c079-ea9b-4899-8069-e0e3048e911d.sketch_text.stroke-14"),sQuery(id+"FHMxAyK4CFUKdhS_1.wireOp",EDGE,"1cb9c079-ea9b-4899-8069-e0e3048e911d.sketch_text.stroke-15"),sQuery(id+"FHMxAyK4CFUKdhS_1.wireOp",EDGE,"1cb9c079-ea9b-4899-8069-e0e3048e911d.sketch_text.stroke-16"),sQuery(id+"FHMxAyK4CFUKdhS_1.wireOp",EDGE,"1cb9c079-ea9b-4899-8069-e0e3048e911d.sketch_text.stroke-17"),sQuery(id+"FHMxAyK4CFUKdhS_1.wireOp",EDGE,"1cb9c079-ea9b-4899-8069-e0e3048e911d.sketch_text.stroke-18"),sQuery(id+"FHMxAyK4CFUKdhS_1.wireOp",EDGE,"1cb9c079-ea9b-4899-8069-e0e3048e911d.sketch_text.stroke-19"),sQuery(id+"FHMxAyK4CFUKdhS_1.wireOp",EDGE,"1cb9c079-ea9b-4899-8069-e0e3048e911d.sketch_text.stroke-20"),sQuery(id+"FHMxAyK4CFUKdhS_1.wireOp",EDGE,"1cb9c079-ea9b-4899-8069-e0e3048e911d.sketch_text.stroke-21"),sQuery(id+"FHMxAyK4CFUKdhS_1.wireOp",EDGE,"1cb9c079-ea9b-4899-8069-e0e3048e911d.sketch_text.stroke-22"),sQuery(id+"FHMxAyK4CFUKdhS_1.wireOp",EDGE,"1cb9c079-ea9b-4899-8069-e0e3048e911d.sketch_text.stroke-23"),sQuery(id+"FHMxAyK4CFUKdhS_1.wireOp",EDGE,"1cb9c079-ea9b-4899-8069-e0e3048e911d.sketch_text.stroke-24"),sQuery(id+"FHMxAyK4CFUKdhS_1.wireOp",EDGE,"1cb9c079-ea9b-4899-8069-e0e3048e911d.sketch_text.stroke-25"),sQuery(id+"FHMxAyK4CFUKdhS_1.wireOp",EDGE,"1cb9c079-ea9b-4899-8069-e0e3048e911d.sketch_text.stroke-26"),sQuery(id+"FHMxAyK4CFUKdhS_1.wireOp",EDGE,"1cb9c079-ea9b-4899-8069-e0e3048e911d.sketch_text.stroke-27"),sQuery(id+"FHMxAyK4CFUKdhS_1.wireOp",EDGE,"1cb9c079-ea9b-4899-8069-e0e3048e911d.sketch_text.stroke-28"),sQuery(id+"FHMxAyK4CFUKdhS_1.wireOp",EDGE,"1cb9c079-ea9b-4899-8069-e0e3048e911d.sketch_text.stroke-29"),sQuery(id+"FHMxAyK4CFUKdhS_1.wireOp",EDGE,"1cb9c079-ea9b-4899-8069-e0e3048e911d.sketch_text.stroke-30"),sQuery(id+"FHMxAyK4CFUKdhS_1.wireOp",EDGE,"1cb9c079-ea9b-4899-8069-e0e3048e911d.sketch_text.stroke-31"),sQuery(id+"FHMxAyK4CFUKdhS_1.wireOp",EDGE,"1cb9c079-ea9b-4899-8069-e0e3048e911d.sketch_text.stroke-32"),sQuery(id+"FHMxAyK4CFUKdhS_1.wireOp",EDGE,"1cb9c079-ea9b-4899-8069-e0e3048e911d.sketch_text.stroke-33"),sQuery(id+"FHMxAyK4CFUKdhS_1.wireOp",EDGE,"1cb9c079-ea9b-4899-8069-e0e3048e911d.sketch_text.stroke-34"),sQuery(id+"FHMxAyK4CFUKdhS_1.wireOp",EDGE,"1cb9c079-ea9b-4899-8069-e0e3048e911d.sketch_text.stroke-35"),sQuery(id+"FHMxAyK4CFUKdhS_1.wireOp",EDGE,"1cb9c079-ea9b-4899-8069-e0e3048e911d.sketch_text.stroke-36"),sQuery(id+"FHMxAyK4CFUKdhS_1.wireOp",EDGE,"1cb9c079-ea9b-4899-8069-e0e3048e911d.sketch_text.stroke-37"),sQuery(id+"FHMxAyK4CFUKdhS_1.wireOp",EDGE,"1cb9c079-ea9b-4899-8069-e0e3048e911d.sketch_text.stroke-38"),sQuery(id+"FHMxAyK4CFUKdhS_1.wireOp",EDGE,"1cb9c079-ea9b-4899-8069-e0e3048e911d.sketch_text.stroke-39"),sQuery(id+"FHMxAyK4CFUKdhS_1.wireOp",EDGE,"1cb9c079-ea9b-4899-8069-e0e3048e911d.sketch_text.stroke-40"),sQuery(id+"FHMxAyK4CFUKdhS_1.wireOp",EDGE,"1cb9c079-ea9b-4899-8069-e0e3048e911d.sketch_text.stroke-41"),sQuery(id+"FHMxAyK4CFUKdhS_1.wireOp",EDGE,"1cb9c079-ea9b-4899-8069-e0e3048e911d.sketch_text.stroke-42"),sQuery(id+"FHMxAyK4CFUKdhS_1.wireOp",EDGE,"1cb9c079-ea9b-4899-8069-e0e3048e911d.sketch_text.stroke-43"),sQuery(id+"FHMxAyK4CFUKdhS_1.wireOp",EDGE,"1cb9c079-ea9b-4899-8069-e0e3048e911d.sketch_text.stroke-44"),sQuery(id+"FHMxAyK4CFUKdhS_1.wireOp",EDGE,"1cb9c079-ea9b-4899-8069-e0e3048e911d.sketch_text.stroke-45"),sQuery(id+"FHMxAyK4CFUKdhS_1.wireOp",EDGE,"1cb9c079-ea9b-4899-8069-e0e3048e911d.sketch_text.stroke-46"),sQuery(id+"FHMxAyK4CFUKdhS_1.wireOp",EDGE,"1cb9c079-ea9b-4899-8069-e0e3048e911d.sketch_text.stroke-47"),sQuery(id+"FHMxAyK4CFUKdhS_1.wireOp",EDGE,"1cb9c079-ea9b-4899-8069-e0e3048e911d.sketch_text.stroke-48"),sQuery(id+"FHMxAyK4CFUKdhS_1.wireOp",EDGE,"1cb9c079-ea9b-4899-8069-e0e3048e911d.sketch_text.stroke-49"),sQuery(id+"FHMxAyK4CFUKdhS_1.wireOp",EDGE,"1cb9c079-ea9b-4899-8069-e0e3048e911d.sketch_text.stroke-50"),sQuery(id+"FHMxAyK4CFUKdhS_1.wireOp",EDGE,"1cb9c079-ea9b-4899-8069-e0e3048e911d.sketch_text.stroke-51"),sQuery(id+"FHMxAyK4CFUKdhS_1.wireOp",EDGE,"1cb9c079-ea9b-4899-8069-e0e3048e911d.sketch_text.stroke-52"),sQuery(id+"FHMxAyK4CFUKdhS_1.wireOp",EDGE,"1cb9c079-ea9b-4899-8069-e0e3048e911d.sketch_text.stroke-53"),sQuery(id+"FHMxAyK4CFUKdhS_1.wireOp",EDGE,"1cb9c079-ea9b-4899-8069-e0e3048e911d.sketch_text.stroke-54"),sQuery(id+"FHMxAyK4CFUKdhS_1.wireOp",EDGE,"1cb9c079-ea9b-4899-8069-e0e3048e911d.sketch_text.stroke-55"),sQuery(id+"FHMxAyK4CFUKdhS_1.wireOp",EDGE,"1cb9c079-ea9b-4899-8069-e0e3048e911d.sketch_text.stroke-56"),sQuery(id+"FHMxAyK4CFUKdhS_1.wireOp",EDGE,"1cb9c079-ea9b-4899-8069-e0e3048e911d.sketch_text.stroke-57"),sQuery(id+"FHMxAyK4CFUKdhS_1.wireOp",EDGE,"1cb9c079-ea9b-4899-8069-e0e3048e911d.sketch_text.stroke-58"),sQuery(id+"FHMxAyK4CFUKdhS_1.wireOp",EDGE,"1cb9c079-ea9b-4899-8069-e0e3048e911d.sketch_text.stroke-59"),sQuery(id+"FHMxAyK4CFUKdhS_1.wireOp",EDGE,"1cb9c079-ea9b-4899-8069-e0e3048e911d.sketch_text.stroke-60"),sQuery(id+"FHMxAyK4CFUKdhS_1.wireOp",EDGE,"1cb9c079-ea9b-4899-8069-e0e3048e911d.sketch_text.stroke-61"),sQuery(id+"FHMxAyK4CFUKdhS_1.wireOp",EDGE,"1cb9c079-ea9b-4899-8069-e0e3048e911d.sketch_text.stroke-62"),sQuery(id+"FHMxAyK4CFUKdhS_1.wireOp",EDGE,"1cb9c079-ea9b-4899-8069-e0e3048e911d.sketch_text.stroke-71"),sQuery(id+"FHMxAyK4CFUKdhS_1.wireOp",EDGE,"1cb9c079-ea9b-4899-8069-e0e3048e911d.sketch_text.stroke-72"),sQuery(id+"FHMxAyK4CFUKdhS_1.wireOp",EDGE,"1cb9c079-ea9b-4899-8069-e0e3048e911d.sketch_text.stroke-73"),sQuery(id+"FHMxAyK4CFUKdhS_1.wireOp",EDGE,"1cb9c079-ea9b-4899-8069-e0e3048e911d.sketch_text.stroke-74"),sQuery(id+"FHMxAyK4CFUKdhS_1.wireOp",EDGE,"1cb9c079-ea9b-4899-8069-e0e3048e911d.sketch_text.stroke-75"),sQuery(id+"FHMxAyK4CFUKdhS_1.wireOp",EDGE,"1cb9c079-ea9b-4899-8069-e0e3048e911d.sketch_text.stroke-76"),sQuery(id+"FHMxAyK4CFUKdhS_1.wireOp",EDGE,"1cb9c079-ea9b-4899-8069-e0e3048e911d.sketch_text.stroke-77"),sQuery(id+"FHMxAyK4CFUKdhS_1.wireOp",EDGE,"1cb9c079-ea9b-4899-8069-e0e3048e911d.sketch_text.stroke-78"),sQuery(id+"FHMxAyK4CFUKdhS_1.wireOp",EDGE,"1cb9c079-ea9b-4899-8069-e0e3048e911d.sketch_text.stroke-79"),sQuery(id+"FHMxAyK4CFUKdhS_1.wireOp",EDGE,"1cb9c079-ea9b-4899-8069-e0e3048e911d.sketch_text.stroke-80"),sQuery(id+"FHMxAyK4CFUKdhS_1.wireOp",EDGE,"1cb9c079-ea9b-4899-8069-e0e3048e911d.sketch_text.stroke-81"),sQuery(id+"FHMxAyK4CFUKdhS_1.wireOp",EDGE,"1cb9c079-ea9b-4899-8069-e0e3048e911d.sketch_text.stroke-82"),sQuery(id+"FHMxAyK4CFUKdhS_1.wireOp",EDGE,"1cb9c079-ea9b-4899-8069-e0e3048e911d.sketch_text.stroke-83"),sQuery(id+"FHMxAyK4CFUKdhS_1.wireOp",EDGE,"1cb9c079-ea9b-4899-8069-e0e3048e911d.sketch_text.stroke-84"),sQuery(id+"FHMxAyK4CFUKdhS_1.wireOp",EDGE,"1cb9c079-ea9b-4899-8069-e0e3048e911d.sketch_text.stroke-85"),sQuery(id+"FHMxAyK4CFUKdhS_1.wireOp",EDGE,"1cb9c079-ea9b-4899-8069-e0e3048e911d.sketch_text.stroke-86"),sQuery(id+"FHMxAyK4CFUKdhS_1.wireOp",EDGE,"1cb9c079-ea9b-4899-8069-e0e3048e911d.sketch_text.stroke-87"),sQuery(id+"FHMxAyK4CFUKdhS_1.wireOp",EDGE,"1cb9c079-ea9b-4899-8069-e0e3048e911d.sketch_text.stroke-88"),sQuery(id+"FHMxAyK4CFUKdhS_1.wireOp",EDGE,"1cb9c079-ea9b-4899-8069-e0e3048e911d.sketch_text.stroke-89"),sQuery(id+"FHMxAyK4CFUKdhS_1.wireOp",EDGE,"1cb9c079-ea9b-4899-8069-e0e3048e911d.sketch_text.stroke-90"),sQuery(id+"FHMxAyK4CFUKdhS_1.wireOp",EDGE,"1cb9c079-ea9b-4899-8069-e0e3048e911d.sketch_text.stroke-91"),sQuery(id+"FHMxAyK4CFUKdhS_1.wireOp",EDGE,"1cb9c079-ea9b-4899-8069-e0e3048e911d.sketch_text.stroke-92"),sQuery(id+"FHMxAyK4CFUKdhS_1.wireOp",EDGE,"1cb9c079-ea9b-4899-8069-e0e3048e911d.sketch_text.stroke-93"),sQuery(id+"FHMxAyK4CFUKdhS_1.wireOp",EDGE,"1cb9c079-ea9b-4899-8069-e0e3048e911d.sketch_text.stroke-94"),sQuery(id+"FHMxAyK4CFUKdhS_1.wireOp",EDGE,"1cb9c079-ea9b-4899-8069-e0e3048e911d.sketch_text.stroke-95"),sQuery(id+"FHMxAyK4CFUKdhS_1.wireOp",EDGE,"1cb9c079-ea9b-4899-8069-e0e3048e911d.sketch_text.stroke-96"),sQuery(id+"FHMxAyK4CFUKdhS_1.wireOp",EDGE,"1cb9c079-ea9b-4899-8069-e0e3048e911d.sketch_text.stroke-97"),sQuery(id+"FHMxAyK4CFUKdhS_1.wireOp",EDGE,"1cb9c079-ea9b-4899-8069-e0e3048e911d.sketch_text.stroke-103"),sQuery(id+"FHMxAyK4CFUKdhS_1.wireOp",EDGE,"1cb9c079-ea9b-4899-8069-e0e3048e911d.sketch_text.stroke-104"),sQuery(id+"FHMxAyK4CFUKdhS_1.wireOp",EDGE,"1cb9c079-ea9b-4899-8069-e0e3048e911d.sketch_text.stroke-105"),sQuery(id+"FHMxAyK4CFUKdhS_1.wireOp",EDGE,"1cb9c079-ea9b-4899-8069-e0e3048e911d.sketch_text.stroke-106"),sQuery(id+"FHMxAyK4CFUKdhS_1.wireOp",EDGE,"1cb9c079-ea9b-4899-8069-e0e3048e911d.sketch_text.stroke-107"),sQuery(id+"FHMxAyK4CFUKdhS_1.wireOp",EDGE,"1cb9c079-ea9b-4899-8069-e0e3048e911d.sketch_text.stroke-108"),sQuery(id+"FHMxAyK4CFUKdhS_1.wireOp",EDGE,"1cb9c079-ea9b-4899-8069-e0e3048e911d.sketch_text.stroke-109"),sQuery(id+"FHMxAyK4CFUKdhS_1.wireOp",EDGE,"1cb9c079-ea9b-4899-8069-e0e3048e911d.sketch_text.stroke-110"),sQuery(id+"FHMxAyK4CFUKdhS_1.wireOp",EDGE,"1cb9c079-ea9b-4899-8069-e0e3048e911d.sketch_text.stroke-111"),sQuery(id+"FHMxAyK4CFUKdhS_1.wireOp",EDGE,"1cb9c079-ea9b-4899-8069-e0e3048e911d.sketch_text.stroke-112"),sQuery(id+"FHMxAyK4CFUKdhS_1.wireOp",EDGE,"1cb9c079-ea9b-4899-8069-e0e3048e911d.sketch_text.stroke-113"),sQuery(id+"FHMxAyK4CFUKdhS_1.wireOp",EDGE,"1cb9c079-ea9b-4899-8069-e0e3048e911d.sketch_text.stroke-114"),sQuery(id+"FHMxAyK4CFUKdhS_1.wireOp",EDGE,"1cb9c079-ea9b-4899-8069-e0e3048e911d.sketch_text.stroke-115"),sQuery(id+"FHMxAyK4CFUKdhS_1.wireOp",EDGE,"1cb9c079-ea9b-4899-8069-e0e3048e911d.sketch_text.stroke-116"),sQuery(id+"FHMxAyK4CFUKdhS_1.wireOp",EDGE,"1cb9c079-ea9b-4899-8069-e0e3048e911d.sketch_text.stroke-117"),sQuery(id+"FHMxAyK4CFUKdhS_1.wireOp",EDGE,"1cb9c079-ea9b-4899-8069-e0e3048e911d.sketch_text.stroke-118"),sQuery(id+"FHMxAyK4CFUKdhS_1.wireOp",EDGE,"1cb9c079-ea9b-4899-8069-e0e3048e911d.sketch_text.stroke-119"),sQuery(id+"FHMxAyK4CFUKdhS_1.wireOp",EDGE,"1cb9c079-ea9b-4899-8069-e0e3048e911d.sketch_text.stroke-120"),sQuery(id+"FHMxAyK4CFUKdhS_1.wireOp",EDGE,"1cb9c079-ea9b-4899-8069-e0e3048e911d.sketch_text.stroke-121"),sQuery(id+"FHMxAyK4CFUKdhS_1.wireOp",EDGE,"1cb9c079-ea9b-4899-8069-e0e3048e911d.sketch_text.stroke-122"),sQuery(id+"FHMxAyK4CFUKdhS_1.wireOp",EDGE,"1cb9c079-ea9b-4899-8069-e0e3048e911d.sketch_text.stroke-123"),sQuery(id+"FHMxAyK4CFUKdhS_1.wireOp",EDGE,"1cb9c079-ea9b-4899-8069-e0e3048e911d.sketch_text.stroke-124"),sQuery(id+"FHMxAyK4CFUKdhS_1.wireOp",EDGE,"1cb9c079-ea9b-4899-8069-e0e3048e911d.sketch_text.stroke-125"),sQuery(id+"FHMxAyK4CFUKdhS_1.wireOp",EDGE,"1cb9c079-ea9b-4899-8069-e0e3048e911d.sketch_text.stroke-126"),sQuery(id+"FHMxAyK4CFUKdhS_1.wireOp",EDGE,"1cb9c079-ea9b-4899-8069-e0e3048e911d.sketch_text.stroke-127"),sQuery(id+"FHMxAyK4CFUKdhS_1.wireOp",EDGE,"1cb9c079-ea9b-4899-8069-e0e3048e911d.sketch_text.stroke-128"),sQuery(id+"FHMxAyK4CFUKdhS_1.wireOp",EDGE,"1cb9c079-ea9b-4899-8069-e0e3048e911d.sketch_text.stroke-129"),sQuery(id+"FHMxAyK4CFUKdhS_1.wireOp",EDGE,"1cb9c079-ea9b-4899-8069-e0e3048e911d.sketch_text.stroke-130"),sQuery(id+"FHMxAyK4CFUKdhS_1.wireOp",EDGE,"1cb9c079-ea9b-4899-8069-e0e3048e911d.sketch_text.stroke-131"),sQuery(id+"FHMxAyK4CFUKdhS_1.wireOp",EDGE,"1cb9c079-ea9b-4899-8069-e0e3048e911d.sketch_text.stroke-132"),sQuery(id+"FHMxAyK4CFUKdhS_1.wireOp",EDGE,"1cb9c079-ea9b-4899-8069-e0e3048e911d.sketch_text.stroke-133"),sQuery(id+"FHMxAyK4CFUKdhS_1.wireOp",EDGE,"1cb9c079-ea9b-4899-8069-e0e3048e911d.sketch_text.stroke-134"),sQuery(id+"FHMxAyK4CFUKdhS_1.wireOp",EDGE,"1cb9c079-ea9b-4899-8069-e0e3048e911d.sketch_text.stroke-135"),sQuery(id+"FHMxAyK4CFUKdhS_1.wireOp",EDGE,"1cb9c079-ea9b-4899-8069-e0e3048e911d.sketch_text.stroke-136"),sQuery(id+"FHMxAyK4CFUKdhS_1.wireOp",EDGE,"1cb9c079-ea9b-4899-8069-e0e3048e911d.sketch_text.stroke-137"),sQuery(id+"FHMxAyK4CFUKdhS_1.wireOp",EDGE,"1cb9c079-ea9b-4899-8069-e0e3048e911d.sketch_text.stroke-138"),sQuery(id+"FHMxAyK4CFUKdhS_1.wireOp",EDGE,"1cb9c079-ea9b-4899-8069-e0e3048e911d.sketch_text.stroke-139"),sQuery(id+"FHMxAyK4CFUKdhS_1.wireOp",EDGE,"1cb9c079-ea9b-4899-8069-e0e3048e911d.sketch_text.stroke-140"),sQuery(id+"FHMxAyK4CFUKdhS_1.wireOp",EDGE,"1cb9c079-ea9b-4899-8069-e0e3048e911d.sketch_text.stroke-141"),sQuery(id+"FHMxAyK4CFUKdhS_1.wireOp",EDGE,"1cb9c079-ea9b-4899-8069-e0e3048e911d.sketch_text.stroke-142"),sQuery(id+"FHMxAyK4CFUKdhS_1.wireOp",EDGE,"1cb9c079-ea9b-4899-8069-e0e3048e911d.sketch_text.stroke-143"),sQuery(id+"FHMxAyK4CFUKdhS_1.wireOp",EDGE,"1cb9c079-ea9b-4899-8069-e0e3048e911d.sketch_text.stroke-144"),sQuery(id+"FHMxAyK4CFUKdhS_1.wireOp",EDGE,"1cb9c079-ea9b-4899-8069-e0e3048e911d.sketch_text.stroke-145"),sQuery(id+"FHMxAyK4CFUKdhS_1.wireOp",EDGE,"1cb9c079-ea9b-4899-8069-e0e3048e911d.sketch_text.stroke-146"),sQuery(id+"FHMxAyK4CFUKdhS_1.wireOp",EDGE,"1cb9c079-ea9b-4899-8069-e0e3048e911d.sketch_text.stroke-147"),sQuery(id+"FHMxAyK4CFUKdhS_1.wireOp",EDGE,"1cb9c079-ea9b-4899-8069-e0e3048e911d.sketch_text.stroke-148"),sQuery(id+"FHMxAyK4CFUKdhS_1.wireOp",EDGE,"1cb9c079-ea9b-4899-8069-e0e3048e911d.sketch_text.stroke-149"),sQuery(id+"FHMxAyK4CFUKdhS_1.wireOp",EDGE,"1cb9c079-ea9b-4899-8069-e0e3048e911d.sketch_text.stroke-150"),sQuery(id+"FHMxAyK4CFUKdhS_1.wireOp",EDGE,"1cb9c079-ea9b-4899-8069-e0e3048e911d.sketch_text.stroke-151"),sQuery(id+"FHMxAyK4CFUKdhS_1.wireOp",EDGE,"1cb9c079-ea9b-4899-8069-e0e3048e911d.sketch_text.stroke-152"),sQuery(id+"FHMxAyK4CFUKdhS_1.wireOp",EDGE,"1cb9c079-ea9b-4899-8069-e0e3048e911d.sketch_text.stroke-153"),sQuery(id+"FHMxAyK4CFUKdhS_1.wireOp",EDGE,"1cb9c079-ea9b-4899-8069-e0e3048e911d.sketch_text.stroke-159"),sQuery(id+"FHMxAyK4CFUKdhS_1.wireOp",EDGE,"1cb9c079-ea9b-4899-8069-e0e3048e911d.sketch_text.stroke-160"),sQuery(id+"FHMxAyK4CFUKdhS_1.wireOp",EDGE,"1cb9c079-ea9b-4899-8069-e0e3048e911d.sketch_text.stroke-161"),sQuery(id+"FHMxAyK4CFUKdhS_1.wireOp",EDGE,"1cb9c079-ea9b-4899-8069-e0e3048e911d.sketch_text.stroke-162"),sQuery(id+"FHMxAyK4CFUKdhS_1.wireOp",EDGE,"1cb9c079-ea9b-4899-8069-e0e3048e911d.sketch_text.stroke-163"),sQuery(id+"FHMxAyK4CFUKdhS_1.wireOp",EDGE,"1cb9c079-ea9b-4899-8069-e0e3048e911d.sketch_text.stroke-164"),sQuery(id+"FHMxAyK4CFUKdhS_1.wireOp",EDGE,"1cb9c079-ea9b-4899-8069-e0e3048e911d.sketch_text.stroke-165"),sQuery(id+"FHMxAyK4CFUKdhS_1.wireOp",EDGE,"1cb9c079-ea9b-4899-8069-e0e3048e911d.sketch_text.stroke-166"),sQuery(id+"FHMxAyK4CFUKdhS_1.wireOp",EDGE,"1cb9c079-ea9b-4899-8069-e0e3048e911d.sketch_text.stroke-167"),sQuery(id+"FHMxAyK4CFUKdhS_1.wireOp",EDGE,"1cb9c079-ea9b-4899-8069-e0e3048e911d.sketch_text.stroke-168"),sQuery(id+"FHMxAyK4CFUKdhS_1.wireOp",EDGE,"1cb9c079-ea9b-4899-8069-e0e3048e911d.sketch_text.stroke-169"),sQuery(id+"FHMxAyK4CFUKdhS_1.wireOp",EDGE,"1cb9c079-ea9b-4899-8069-e0e3048e911d.sketch_text.stroke-170"),sQuery(id+"FHMxAyK4CFUKdhS_1.wireOp",EDGE,"1cb9c079-ea9b-4899-8069-e0e3048e911d.sketch_text.stroke-171"),sQuery(id+"FHMxAyK4CFUKdhS_1.wireOp",EDGE,"1cb9c079-ea9b-4899-8069-e0e3048e911d.sketch_text.stroke-172"),sQuery(id+"FHMxAyK4CFUKdhS_1.wireOp",EDGE,"1cb9c079-ea9b-4899-8069-e0e3048e911d.sketch_text.stroke-173"),sQuery(id+"FHMxAyK4CFUKdhS_1.wireOp",EDGE,"1cb9c079-ea9b-4899-8069-e0e3048e911d.sketch_text.stroke-174"),sQuery(id+"FHMxAyK4CFUKdhS_1.wireOp",EDGE,"1cb9c079-ea9b-4899-8069-e0e3048e911d.sketch_text.stroke-175"),sQuery(id+"FHMxAyK4CFUKdhS_1.wireOp",EDGE,"1cb9c079-ea9b-4899-8069-e0e3048e911d.sketch_text.stroke-176"),sQuery(id+"FHMxAyK4CFUKdhS_1.wireOp",EDGE,"1cb9c079-ea9b-4899-8069-e0e3048e911d.sketch_text.stroke-177"),sQuery(id+"FHMxAyK4CFUKdhS_1.wireOp",EDGE,"1cb9c079-ea9b-4899-8069-e0e3048e911d.sketch_text.stroke-178"),sQuery(id+"FHMxAyK4CFUKdhS_1.wireOp",EDGE,"1cb9c079-ea9b-4899-8069-e0e3048e911d.sketch_text.stroke-179"),sQuery(id+"FHMxAyK4CFUKdhS_1.wireOp",EDGE,"1cb9c079-ea9b-4899-8069-e0e3048e911d.sketch_text.stroke-180"),subQ0,sQuery(id+"F3.wireOp",EDGE,"6ee83ff3-586e-4dbe-aaea-af71240543bd")])],"isStart":true})])],"derivedFrom":makeQuery(id+"F4.opExtrude","CAP_EDGE",EDGE,{"disambiguationData":[OSD([subQ0])],"isStart":true})});}
            var Q1;
            Q1=makeQuery(id+"F1.opExtrude","CAP_EDGE",EDGE,{"disambiguationData":[OSD([sQuery(id+"F0.wireOp",EDGE,"E0.left")])],"isStart":false});
            var Q2;
            {var subQ0=sQuery(id+"F0.wireOp",EDGE,"E0.top");var subQ1=sQuery(id+"F0.wireOp",EDGE,"E0.bottom");var subQ2=sQuery(id+"F3.wireOp",EDGE,"8007402e-1a4e-4a06-85a5-2af08e553504");Q2=makeQuery(id+"F4.boolean.opBoolean","SPLIT",EDGE,{"disambiguationData":[TD([makeQuery(id+"F1.opExtrude","CAP_FACE",FACE,{"disambiguationData":[OSD([subQ1,subQ0,sQuery(id+"F0.wireOp",EDGE,"E0.left"),sQuery(id+"F0.wireOp",EDGE,"E0.right")])],"isStart":false}),makeQuery(id+"F1.opExtrude","SWEPT_FACE",FACE,{"disambiguationData":[OSD([subQ0])]}),makeQuery(id+"F4.opExtrude","SWEPT_FACE",FACE,{"disambiguationData":[OSD([subQ2])]}),makeQuery(id+"F4.opExtrude","CAP_FACE",FACE,{"disambiguationData":[OSD([subQ1,sQuery(id+"F2.wireOp",EDGE,"fcba4419-a2ee-464f-be9d-58f11bf3418b.sketch_text.stroke-0"),sQuery(id+"F2.wireOp",EDGE,"fcba4419-a2ee-464f-be9d-58f11bf3418b.sketch_text.stroke-1"),sQuery(id+"F2.wireOp",EDGE,"fcba4419-a2ee-464f-be9d-58f11bf3418b.sketch_text.stroke-2"),sQuery(id+"F2.wireOp",EDGE,"fcba4419-a2ee-464f-be9d-58f11bf3418b.sketch_text.stroke-3"),sQuery(id+"F2.wireOp",EDGE,"fcba4419-a2ee-464f-be9d-58f11bf3418b.sketch_text.stroke-4"),sQuery(id+"F2.wireOp",EDGE,"fcba4419-a2ee-464f-be9d-58f11bf3418b.sketch_text.stroke-5"),sQuery(id+"F2.wireOp",EDGE,"fcba4419-a2ee-464f-be9d-58f11bf3418b.sketch_text.stroke-6"),sQuery(id+"F2.wireOp",EDGE,"fcba4419-a2ee-464f-be9d-58f11bf3418b.sketch_text.stroke-7"),sQuery(id+"F2.wireOp",EDGE,"fcba4419-a2ee-464f-be9d-58f11bf3418b.sketch_text.stroke-8"),sQuery(id+"F2.wireOp",EDGE,"fcba4419-a2ee-464f-be9d-58f11bf3418b.sketch_text.stroke-9"),sQuery(id+"F2.wireOp",EDGE,"fcba4419-a2ee-464f-be9d-58f11bf3418b.sketch_text.stroke-10"),sQuery(id+"F2.wireOp",EDGE,"fcba4419-a2ee-464f-be9d-58f11bf3418b.sketch_text.stroke-11"),sQuery(id+"F2.wireOp",EDGE,"fcba4419-a2ee-464f-be9d-58f11bf3418b.sketch_text.stroke-12"),sQuery(id+"F2.wireOp",EDGE,"fcba4419-a2ee-464f-be9d-58f11bf3418b.sketch_text.stroke-13"),sQuery(id+"F2.wireOp",EDGE,"fcba4419-a2ee-464f-be9d-58f11bf3418b.sketch_text.stroke-14"),sQuery(id+"F2.wireOp",EDGE,"fcba4419-a2ee-464f-be9d-58f11bf3418b.sketch_text.stroke-15"),sQuery(id+"F2.wireOp",EDGE,"fcba4419-a2ee-464f-be9d-58f11bf3418b.sketch_text.stroke-16"),sQuery(id+"F2.wireOp",EDGE,"fcba4419-a2ee-464f-be9d-58f11bf3418b.sketch_text.stroke-17"),sQuery(id+"F2.wireOp",EDGE,"fcba4419-a2ee-464f-be9d-58f11bf3418b.sketch_text.stroke-18"),sQuery(id+"F2.wireOp",EDGE,"fcba4419-a2ee-464f-be9d-58f11bf3418b.sketch_text.stroke-19"),sQuery(id+"F2.wireOp",EDGE,"fcba4419-a2ee-464f-be9d-58f11bf3418b.sketch_text.stroke-20"),sQuery(id+"F2.wireOp",EDGE,"fcba4419-a2ee-464f-be9d-58f11bf3418b.sketch_text.stroke-21"),sQuery(id+"F2.wireOp",EDGE,"fcba4419-a2ee-464f-be9d-58f11bf3418b.sketch_text.stroke-22"),sQuery(id+"F2.wireOp",EDGE,"fcba4419-a2ee-464f-be9d-58f11bf3418b.sketch_text.stroke-23"),sQuery(id+"F2.wireOp",EDGE,"fcba4419-a2ee-464f-be9d-58f11bf3418b.sketch_text.stroke-24"),sQuery(id+"F2.wireOp",EDGE,"fcba4419-a2ee-464f-be9d-58f11bf3418b.sketch_text.stroke-25"),sQuery(id+"F2.wireOp",EDGE,"fcba4419-a2ee-464f-be9d-58f11bf3418b.sketch_text.stroke-26"),sQuery(id+"F2.wireOp",EDGE,"fcba4419-a2ee-464f-be9d-58f11bf3418b.sketch_text.stroke-27"),sQuery(id+"F2.wireOp",EDGE,"fcba4419-a2ee-464f-be9d-58f11bf3418b.sketch_text.stroke-28"),sQuery(id+"F2.wireOp",EDGE,"fcba4419-a2ee-464f-be9d-58f11bf3418b.sketch_text.stroke-29"),sQuery(id+"F2.wireOp",EDGE,"fcba4419-a2ee-464f-be9d-58f11bf3418b.sketch_text.stroke-30"),sQuery(id+"F2.wireOp",EDGE,"fcba4419-a2ee-464f-be9d-58f11bf3418b.sketch_text.stroke-31"),sQuery(id+"F2.wireOp",EDGE,"fcba4419-a2ee-464f-be9d-58f11bf3418b.sketch_text.stroke-32"),sQuery(id+"F2.wireOp",EDGE,"fcba4419-a2ee-464f-be9d-58f11bf3418b.sketch_text.stroke-33"),sQuery(id+"F2.wireOp",EDGE,"fcba4419-a2ee-464f-be9d-58f11bf3418b.sketch_text.stroke-34"),sQuery(id+"F2.wireOp",EDGE,"fcba4419-a2ee-464f-be9d-58f11bf3418b.sketch_text.stroke-35"),sQuery(id+"F2.wireOp",EDGE,"fcba4419-a2ee-464f-be9d-58f11bf3418b.sketch_text.stroke-36"),sQuery(id+"F2.wireOp",EDGE,"fcba4419-a2ee-464f-be9d-58f11bf3418b.sketch_text.stroke-37"),sQuery(id+"F2.wireOp",EDGE,"fcba4419-a2ee-464f-be9d-58f11bf3418b.sketch_text.stroke-38"),sQuery(id+"F2.wireOp",EDGE,"fcba4419-a2ee-464f-be9d-58f11bf3418b.sketch_text.stroke-39"),sQuery(id+"F2.wireOp",EDGE,"fcba4419-a2ee-464f-be9d-58f11bf3418b.sketch_text.stroke-40"),sQuery(id+"F2.wireOp",EDGE,"fcba4419-a2ee-464f-be9d-58f11bf3418b.sketch_text.stroke-41"),sQuery(id+"F2.wireOp",EDGE,"fcba4419-a2ee-464f-be9d-58f11bf3418b.sketch_text.stroke-42"),sQuery(id+"F2.wireOp",EDGE,"fcba4419-a2ee-464f-be9d-58f11bf3418b.sketch_text.stroke-43"),sQuery(id+"F2.wireOp",EDGE,"fcba4419-a2ee-464f-be9d-58f11bf3418b.sketch_text.stroke-44"),sQuery(id+"F2.wireOp",EDGE,"fcba4419-a2ee-464f-be9d-58f11bf3418b.sketch_text.stroke-45"),sQuery(id+"F2.wireOp",EDGE,"fcba4419-a2ee-464f-be9d-58f11bf3418b.sketch_text.stroke-46"),sQuery(id+"F2.wireOp",EDGE,"fcba4419-a2ee-464f-be9d-58f11bf3418b.sketch_text.stroke-47"),sQuery(id+"F2.wireOp",EDGE,"fcba4419-a2ee-464f-be9d-58f11bf3418b.sketch_text.stroke-48"),sQuery(id+"F2.wireOp",EDGE,"fcba4419-a2ee-464f-be9d-58f11bf3418b.sketch_text.stroke-49"),sQuery(id+"F2.wireOp",EDGE,"fcba4419-a2ee-464f-be9d-58f11bf3418b.sketch_text.stroke-50"),sQuery(id+"F2.wireOp",EDGE,"fcba4419-a2ee-464f-be9d-58f11bf3418b.sketch_text.stroke-51"),sQuery(id+"F2.wireOp",EDGE,"fcba4419-a2ee-464f-be9d-58f11bf3418b.sketch_text.stroke-52"),sQuery(id+"F2.wireOp",EDGE,"fcba4419-a2ee-464f-be9d-58f11bf3418b.sketch_text.stroke-53"),sQuery(id+"F2.wireOp",EDGE,"fcba4419-a2ee-464f-be9d-58f11bf3418b.sketch_text.stroke-54"),sQuery(id+"F2.wireOp",EDGE,"fcba4419-a2ee-464f-be9d-58f11bf3418b.sketch_text.stroke-55"),sQuery(id+"F2.wireOp",EDGE,"fcba4419-a2ee-464f-be9d-58f11bf3418b.sketch_text.stroke-56"),sQuery(id+"F2.wireOp",EDGE,"fcba4419-a2ee-464f-be9d-58f11bf3418b.sketch_text.stroke-57"),sQuery(id+"F2.wireOp",EDGE,"fcba4419-a2ee-464f-be9d-58f11bf3418b.sketch_text.stroke-58"),sQuery(id+"F2.wireOp",EDGE,"fcba4419-a2ee-464f-be9d-58f11bf3418b.sketch_text.stroke-59"),sQuery(id+"F2.wireOp",EDGE,"fcba4419-a2ee-464f-be9d-58f11bf3418b.sketch_text.stroke-60"),sQuery(id+"F2.wireOp",EDGE,"fcba4419-a2ee-464f-be9d-58f11bf3418b.sketch_text.stroke-61"),sQuery(id+"F2.wireOp",EDGE,"fcba4419-a2ee-464f-be9d-58f11bf3418b.sketch_text.stroke-62"),sQuery(id+"F2.wireOp",EDGE,"fcba4419-a2ee-464f-be9d-58f11bf3418b.sketch_text.stroke-63"),sQuery(id+"F2.wireOp",EDGE,"fcba4419-a2ee-464f-be9d-58f11bf3418b.sketch_text.stroke-64"),sQuery(id+"F2.wireOp",EDGE,"fcba4419-a2ee-464f-be9d-58f11bf3418b.sketch_text.stroke-65"),sQuery(id+"F2.wireOp",EDGE,"fcba4419-a2ee-464f-be9d-58f11bf3418b.sketch_text.stroke-66"),sQuery(id+"F2.wireOp",EDGE,"fcba4419-a2ee-464f-be9d-58f11bf3418b.sketch_text.stroke-67"),sQuery(id+"F2.wireOp",EDGE,"fcba4419-a2ee-464f-be9d-58f11bf3418b.sketch_text.stroke-68"),sQuery(id+"F2.wireOp",EDGE,"fcba4419-a2ee-464f-be9d-58f11bf3418b.sketch_text.stroke-69"),sQuery(id+"F2.wireOp",EDGE,"fcba4419-a2ee-464f-be9d-58f11bf3418b.sketch_text.stroke-70"),sQuery(id+"F2.wireOp",EDGE,"fcba4419-a2ee-464f-be9d-58f11bf3418b.sketch_text.stroke-71"),sQuery(id+"F2.wireOp",EDGE,"fcba4419-a2ee-464f-be9d-58f11bf3418b.sketch_text.stroke-72"),sQuery(id+"F2.wireOp",EDGE,"fcba4419-a2ee-464f-be9d-58f11bf3418b.sketch_text.stroke-73"),sQuery(id+"F2.wireOp",EDGE,"fcba4419-a2ee-464f-be9d-58f11bf3418b.sketch_text.stroke-74"),sQuery(id+"F2.wireOp",EDGE,"fcba4419-a2ee-464f-be9d-58f11bf3418b.sketch_text.stroke-75"),sQuery(id+"F2.wireOp",EDGE,"fcba4419-a2ee-464f-be9d-58f11bf3418b.sketch_text.stroke-76"),sQuery(id+"F2.wireOp",EDGE,"fcba4419-a2ee-464f-be9d-58f11bf3418b.sketch_text.stroke-77"),sQuery(id+"F2.wireOp",EDGE,"fcba4419-a2ee-464f-be9d-58f11bf3418b.sketch_text.stroke-78"),sQuery(id+"F2.wireOp",EDGE,"fcba4419-a2ee-464f-be9d-58f11bf3418b.sketch_text.stroke-79"),sQuery(id+"F2.wireOp",EDGE,"fcba4419-a2ee-464f-be9d-58f11bf3418b.sketch_text.stroke-80"),sQuery(id+"F2.wireOp",EDGE,"fcba4419-a2ee-464f-be9d-58f11bf3418b.sketch_text.stroke-81"),sQuery(id+"F2.wireOp",EDGE,"fcba4419-a2ee-464f-be9d-58f11bf3418b.sketch_text.stroke-82"),sQuery(id+"F2.wireOp",EDGE,"fcba4419-a2ee-464f-be9d-58f11bf3418b.sketch_text.stroke-83"),sQuery(id+"F2.wireOp",EDGE,"fcba4419-a2ee-464f-be9d-58f11bf3418b.sketch_text.stroke-84"),sQuery(id+"F2.wireOp",EDGE,"fcba4419-a2ee-464f-be9d-58f11bf3418b.sketch_text.stroke-85"),sQuery(id+"F2.wireOp",EDGE,"fcba4419-a2ee-464f-be9d-58f11bf3418b.sketch_text.stroke-86"),sQuery(id+"F2.wireOp",EDGE,"fcba4419-a2ee-464f-be9d-58f11bf3418b.sketch_text.stroke-87"),sQuery(id+"F2.wireOp",EDGE,"fcba4419-a2ee-464f-be9d-58f11bf3418b.sketch_text.stroke-88"),sQuery(id+"F2.wireOp",EDGE,"fcba4419-a2ee-464f-be9d-58f11bf3418b.sketch_text.stroke-89"),sQuery(id+"F2.wireOp",EDGE,"fcba4419-a2ee-464f-be9d-58f11bf3418b.sketch_text.stroke-90"),sQuery(id+"F2.wireOp",EDGE,"fcba4419-a2ee-464f-be9d-58f11bf3418b.sketch_text.stroke-91"),sQuery(id+"F2.wireOp",EDGE,"fcba4419-a2ee-464f-be9d-58f11bf3418b.sketch_text.stroke-92"),sQuery(id+"F2.wireOp",EDGE,"fcba4419-a2ee-464f-be9d-58f11bf3418b.sketch_text.stroke-93"),sQuery(id+"F2.wireOp",EDGE,"fcba4419-a2ee-464f-be9d-58f11bf3418b.sketch_text.stroke-94"),sQuery(id+"F2.wireOp",EDGE,"fcba4419-a2ee-464f-be9d-58f11bf3418b.sketch_text.stroke-95"),sQuery(id+"F2.wireOp",EDGE,"fcba4419-a2ee-464f-be9d-58f11bf3418b.sketch_text.stroke-96"),sQuery(id+"F2.wireOp",EDGE,"fcba4419-a2ee-464f-be9d-58f11bf3418b.sketch_text.stroke-97"),sQuery(id+"F2.wireOp",EDGE,"fcba4419-a2ee-464f-be9d-58f11bf3418b.sketch_text.stroke-98"),sQuery(id+"F2.wireOp",EDGE,"fcba4419-a2ee-464f-be9d-58f11bf3418b.sketch_text.stroke-99"),sQuery(id+"F2.wireOp",EDGE,"fcba4419-a2ee-464f-be9d-58f11bf3418b.sketch_text.stroke-100"),sQuery(id+"F2.wireOp",EDGE,"fcba4419-a2ee-464f-be9d-58f11bf3418b.sketch_text.stroke-101"),sQuery(id+"F2.wireOp",EDGE,"fcba4419-a2ee-464f-be9d-58f11bf3418b.sketch_text.stroke-102"),sQuery(id+"F2.wireOp",EDGE,"fcba4419-a2ee-464f-be9d-58f11bf3418b.sketch_text.stroke-103"),sQuery(id+"F2.wireOp",EDGE,"fcba4419-a2ee-464f-be9d-58f11bf3418b.sketch_text.stroke-104"),sQuery(id+"F2.wireOp",EDGE,"fcba4419-a2ee-464f-be9d-58f11bf3418b.sketch_text.stroke-105"),sQuery(id+"F2.wireOp",EDGE,"fcba4419-a2ee-464f-be9d-58f11bf3418b.sketch_text.stroke-106"),sQuery(id+"F2.wireOp",EDGE,"fcba4419-a2ee-464f-be9d-58f11bf3418b.sketch_text.stroke-107"),sQuery(id+"F2.wireOp",EDGE,"fcba4419-a2ee-464f-be9d-58f11bf3418b.sketch_text.stroke-108"),sQuery(id+"F2.wireOp",EDGE,"fcba4419-a2ee-464f-be9d-58f11bf3418b.sketch_text.stroke-109"),sQuery(id+"F2.wireOp",EDGE,"fcba4419-a2ee-464f-be9d-58f11bf3418b.sketch_text.stroke-110"),sQuery(id+"F2.wireOp",EDGE,"fcba4419-a2ee-464f-be9d-58f11bf3418b.sketch_text.stroke-111"),sQuery(id+"F2.wireOp",EDGE,"fcba4419-a2ee-464f-be9d-58f11bf3418b.sketch_text.stroke-112"),sQuery(id+"F2.wireOp",EDGE,"fcba4419-a2ee-464f-be9d-58f11bf3418b.sketch_text.stroke-113"),sQuery(id+"F2.wireOp",EDGE,"fcba4419-a2ee-464f-be9d-58f11bf3418b.sketch_text.stroke-114"),sQuery(id+"F2.wireOp",EDGE,"fcba4419-a2ee-464f-be9d-58f11bf3418b.sketch_text.stroke-115"),sQuery(id+"F2.wireOp",EDGE,"fcba4419-a2ee-464f-be9d-58f11bf3418b.sketch_text.stroke-116"),sQuery(id+"F2.wireOp",EDGE,"fcba4419-a2ee-464f-be9d-58f11bf3418b.sketch_text.stroke-117"),sQuery(id+"F2.wireOp",EDGE,"fcba4419-a2ee-464f-be9d-58f11bf3418b.sketch_text.stroke-118"),sQuery(id+"F2.wireOp",EDGE,"fcba4419-a2ee-464f-be9d-58f11bf3418b.sketch_text.stroke-119"),sQuery(id+"F2.wireOp",EDGE,"fcba4419-a2ee-464f-be9d-58f11bf3418b.sketch_text.stroke-120"),sQuery(id+"F2.wireOp",EDGE,"fcba4419-a2ee-464f-be9d-58f11bf3418b.sketch_text.stroke-121"),sQuery(id+"F2.wireOp",EDGE,"fcba4419-a2ee-464f-be9d-58f11bf3418b.sketch_text.stroke-122"),sQuery(id+"F2.wireOp",EDGE,"fcba4419-a2ee-464f-be9d-58f11bf3418b.sketch_text.stroke-123"),sQuery(id+"F2.wireOp",EDGE,"fcba4419-a2ee-464f-be9d-58f11bf3418b.sketch_text.stroke-124"),sQuery(id+"F2.wireOp",EDGE,"fcba4419-a2ee-464f-be9d-58f11bf3418b.sketch_text.stroke-125"),sQuery(id+"F2.wireOp",EDGE,"fcba4419-a2ee-464f-be9d-58f11bf3418b.sketch_text.stroke-126"),sQuery(id+"F2.wireOp",EDGE,"fcba4419-a2ee-464f-be9d-58f11bf3418b.sketch_text.stroke-127"),sQuery(id+"F2.wireOp",EDGE,"fcba4419-a2ee-464f-be9d-58f11bf3418b.sketch_text.stroke-128"),sQuery(id+"F2.wireOp",EDGE,"fcba4419-a2ee-464f-be9d-58f11bf3418b.sketch_text.stroke-129"),sQuery(id+"F2.wireOp",EDGE,"fcba4419-a2ee-464f-be9d-58f11bf3418b.sketch_text.stroke-130"),sQuery(id+"F2.wireOp",EDGE,"fcba4419-a2ee-464f-be9d-58f11bf3418b.sketch_text.stroke-131"),sQuery(id+"F2.wireOp",EDGE,"fcba4419-a2ee-464f-be9d-58f11bf3418b.sketch_text.stroke-132"),sQuery(id+"F2.wireOp",EDGE,"fcba4419-a2ee-464f-be9d-58f11bf3418b.sketch_text.stroke-133"),sQuery(id+"F2.wireOp",EDGE,"fcba4419-a2ee-464f-be9d-58f11bf3418b.sketch_text.stroke-134"),sQuery(id+"F2.wireOp",EDGE,"fcba4419-a2ee-464f-be9d-58f11bf3418b.sketch_text.stroke-135"),sQuery(id+"F2.wireOp",EDGE,"fcba4419-a2ee-464f-be9d-58f11bf3418b.sketch_text.stroke-136"),sQuery(id+"F2.wireOp",EDGE,"fcba4419-a2ee-464f-be9d-58f11bf3418b.sketch_text.stroke-137"),sQuery(id+"F2.wireOp",EDGE,"fcba4419-a2ee-464f-be9d-58f11bf3418b.sketch_text.stroke-138"),sQuery(id+"F2.wireOp",EDGE,"fcba4419-a2ee-464f-be9d-58f11bf3418b.sketch_text.stroke-139"),sQuery(id+"F2.wireOp",EDGE,"fcba4419-a2ee-464f-be9d-58f11bf3418b.sketch_text.stroke-140"),sQuery(id+"F2.wireOp",EDGE,"fcba4419-a2ee-464f-be9d-58f11bf3418b.sketch_text.stroke-141"),sQuery(id+"F2.wireOp",EDGE,"fcba4419-a2ee-464f-be9d-58f11bf3418b.sketch_text.stroke-142"),sQuery(id+"F2.wireOp",EDGE,"fcba4419-a2ee-464f-be9d-58f11bf3418b.sketch_text.stroke-143"),sQuery(id+"F2.wireOp",EDGE,"fcba4419-a2ee-464f-be9d-58f11bf3418b.sketch_text.stroke-144"),sQuery(id+"F2.wireOp",EDGE,"fcba4419-a2ee-464f-be9d-58f11bf3418b.sketch_text.stroke-145"),sQuery(id+"F2.wireOp",EDGE,"fcba4419-a2ee-464f-be9d-58f11bf3418b.sketch_text.stroke-146"),sQuery(id+"F2.wireOp",EDGE,"fcba4419-a2ee-464f-be9d-58f11bf3418b.sketch_text.stroke-147"),sQuery(id+"F2.wireOp",EDGE,"fcba4419-a2ee-464f-be9d-58f11bf3418b.sketch_text.stroke-148"),sQuery(id+"F2.wireOp",EDGE,"fcba4419-a2ee-464f-be9d-58f11bf3418b.sketch_text.stroke-149"),sQuery(id+"F2.wireOp",EDGE,"fcba4419-a2ee-464f-be9d-58f11bf3418b.sketch_text.stroke-150"),sQuery(id+"F2.wireOp",EDGE,"fcba4419-a2ee-464f-be9d-58f11bf3418b.sketch_text.stroke-151"),sQuery(id+"F2.wireOp",EDGE,"fcba4419-a2ee-464f-be9d-58f11bf3418b.sketch_text.stroke-152"),sQuery(id+"F2.wireOp",EDGE,"fcba4419-a2ee-464f-be9d-58f11bf3418b.sketch_text.stroke-153"),sQuery(id+"F2.wireOp",EDGE,"fcba4419-a2ee-464f-be9d-58f11bf3418b.sketch_text.stroke-154"),sQuery(id+"F2.wireOp",EDGE,"fcba4419-a2ee-464f-be9d-58f11bf3418b.sketch_text.stroke-155"),sQuery(id+"F2.wireOp",EDGE,"fcba4419-a2ee-464f-be9d-58f11bf3418b.sketch_text.stroke-156"),sQuery(id+"F2.wireOp",EDGE,"fcba4419-a2ee-464f-be9d-58f11bf3418b.sketch_text.stroke-157"),sQuery(id+"F2.wireOp",EDGE,"fcba4419-a2ee-464f-be9d-58f11bf3418b.sketch_text.stroke-158"),sQuery(id+"F2.wireOp",EDGE,"fcba4419-a2ee-464f-be9d-58f11bf3418b.sketch_text.stroke-159"),sQuery(id+"F2.wireOp",EDGE,"fcba4419-a2ee-464f-be9d-58f11bf3418b.sketch_text.stroke-160"),sQuery(id+"F2.wireOp",EDGE,"fcba4419-a2ee-464f-be9d-58f11bf3418b.sketch_text.stroke-161"),sQuery(id+"F2.wireOp",EDGE,"fcba4419-a2ee-464f-be9d-58f11bf3418b.sketch_text.stroke-162"),sQuery(id+"F2.wireOp",EDGE,"fcba4419-a2ee-464f-be9d-58f11bf3418b.sketch_text.stroke-163"),sQuery(id+"F2.wireOp",EDGE,"fcba4419-a2ee-464f-be9d-58f11bf3418b.sketch_text.stroke-164"),sQuery(id+"F2.wireOp",EDGE,"fcba4419-a2ee-464f-be9d-58f11bf3418b.sketch_text.stroke-165"),sQuery(id+"F2.wireOp",EDGE,"fcba4419-a2ee-464f-be9d-58f11bf3418b.sketch_text.stroke-166"),sQuery(id+"F2.wireOp",EDGE,"fcba4419-a2ee-464f-be9d-58f11bf3418b.sketch_text.stroke-167"),sQuery(id+"F2.wireOp",EDGE,"fcba4419-a2ee-464f-be9d-58f11bf3418b.sketch_text.stroke-168"),sQuery(id+"F2.wireOp",EDGE,"fcba4419-a2ee-464f-be9d-58f11bf3418b.sketch_text.stroke-169"),sQuery(id+"F2.wireOp",EDGE,"fcba4419-a2ee-464f-be9d-58f11bf3418b.sketch_text.stroke-170"),sQuery(id+"F2.wireOp",EDGE,"fcba4419-a2ee-464f-be9d-58f11bf3418b.sketch_text.stroke-171"),sQuery(id+"F2.wireOp",EDGE,"fcba4419-a2ee-464f-be9d-58f11bf3418b.sketch_text.stroke-172"),sQuery(id+"F2.wireOp",EDGE,"fcba4419-a2ee-464f-be9d-58f11bf3418b.sketch_text.stroke-173"),sQuery(id+"FHMxAyK4CFUKdhS_1.wireOp",EDGE,"1cb9c079-ea9b-4899-8069-e0e3048e911d.sketch_text.stroke-0"),sQuery(id+"FHMxAyK4CFUKdhS_1.wireOp",EDGE,"1cb9c079-ea9b-4899-8069-e0e3048e911d.sketch_text.stroke-1"),sQuery(id+"FHMxAyK4CFUKdhS_1.wireOp",EDGE,"1cb9c079-ea9b-4899-8069-e0e3048e911d.sketch_text.stroke-2"),sQuery(id+"FHMxAyK4CFUKdhS_1.wireOp",EDGE,"1cb9c079-ea9b-4899-8069-e0e3048e911d.sketch_text.stroke-3"),sQuery(id+"FHMxAyK4CFUKdhS_1.wireOp",EDGE,"1cb9c079-ea9b-4899-8069-e0e3048e911d.sketch_text.stroke-4"),sQuery(id+"FHMxAyK4CFUKdhS_1.wireOp",EDGE,"1cb9c079-ea9b-4899-8069-e0e3048e911d.sketch_text.stroke-5"),sQuery(id+"FHMxAyK4CFUKdhS_1.wireOp",EDGE,"1cb9c079-ea9b-4899-8069-e0e3048e911d.sketch_text.stroke-6"),sQuery(id+"FHMxAyK4CFUKdhS_1.wireOp",EDGE,"1cb9c079-ea9b-4899-8069-e0e3048e911d.sketch_text.stroke-7"),sQuery(id+"FHMxAyK4CFUKdhS_1.wireOp",EDGE,"1cb9c079-ea9b-4899-8069-e0e3048e911d.sketch_text.stroke-8"),sQuery(id+"FHMxAyK4CFUKdhS_1.wireOp",EDGE,"1cb9c079-ea9b-4899-8069-e0e3048e911d.sketch_text.stroke-9"),sQuery(id+"FHMxAyK4CFUKdhS_1.wireOp",EDGE,"1cb9c079-ea9b-4899-8069-e0e3048e911d.sketch_text.stroke-10"),sQuery(id+"FHMxAyK4CFUKdhS_1.wireOp",EDGE,"1cb9c079-ea9b-4899-8069-e0e3048e911d.sketch_text.stroke-11"),sQuery(id+"FHMxAyK4CFUKdhS_1.wireOp",EDGE,"1cb9c079-ea9b-4899-8069-e0e3048e911d.sketch_text.stroke-12"),sQuery(id+"FHMxAyK4CFUKdhS_1.wireOp",EDGE,"1cb9c079-ea9b-4899-8069-e0e3048e911d.sketch_text.stroke-13"),sQuery(id+"FHMxAyK4CFUKdhS_1.wireOp",EDGE,"1cb9c079-ea9b-4899-8069-e0e3048e911d.sketch_text.stroke-14"),sQuery(id+"FHMxAyK4CFUKdhS_1.wireOp",EDGE,"1cb9c079-ea9b-4899-8069-e0e3048e911d.sketch_text.stroke-15"),sQuery(id+"FHMxAyK4CFUKdhS_1.wireOp",EDGE,"1cb9c079-ea9b-4899-8069-e0e3048e911d.sketch_text.stroke-16"),sQuery(id+"FHMxAyK4CFUKdhS_1.wireOp",EDGE,"1cb9c079-ea9b-4899-8069-e0e3048e911d.sketch_text.stroke-17"),sQuery(id+"FHMxAyK4CFUKdhS_1.wireOp",EDGE,"1cb9c079-ea9b-4899-8069-e0e3048e911d.sketch_text.stroke-18"),sQuery(id+"FHMxAyK4CFUKdhS_1.wireOp",EDGE,"1cb9c079-ea9b-4899-8069-e0e3048e911d.sketch_text.stroke-19"),sQuery(id+"FHMxAyK4CFUKdhS_1.wireOp",EDGE,"1cb9c079-ea9b-4899-8069-e0e3048e911d.sketch_text.stroke-20"),sQuery(id+"FHMxAyK4CFUKdhS_1.wireOp",EDGE,"1cb9c079-ea9b-4899-8069-e0e3048e911d.sketch_text.stroke-21"),sQuery(id+"FHMxAyK4CFUKdhS_1.wireOp",EDGE,"1cb9c079-ea9b-4899-8069-e0e3048e911d.sketch_text.stroke-22"),sQuery(id+"FHMxAyK4CFUKdhS_1.wireOp",EDGE,"1cb9c079-ea9b-4899-8069-e0e3048e911d.sketch_text.stroke-23"),sQuery(id+"FHMxAyK4CFUKdhS_1.wireOp",EDGE,"1cb9c079-ea9b-4899-8069-e0e3048e911d.sketch_text.stroke-24"),sQuery(id+"FHMxAyK4CFUKdhS_1.wireOp",EDGE,"1cb9c079-ea9b-4899-8069-e0e3048e911d.sketch_text.stroke-25"),sQuery(id+"FHMxAyK4CFUKdhS_1.wireOp",EDGE,"1cb9c079-ea9b-4899-8069-e0e3048e911d.sketch_text.stroke-26"),sQuery(id+"FHMxAyK4CFUKdhS_1.wireOp",EDGE,"1cb9c079-ea9b-4899-8069-e0e3048e911d.sketch_text.stroke-27"),sQuery(id+"FHMxAyK4CFUKdhS_1.wireOp",EDGE,"1cb9c079-ea9b-4899-8069-e0e3048e911d.sketch_text.stroke-28"),sQuery(id+"FHMxAyK4CFUKdhS_1.wireOp",EDGE,"1cb9c079-ea9b-4899-8069-e0e3048e911d.sketch_text.stroke-29"),sQuery(id+"FHMxAyK4CFUKdhS_1.wireOp",EDGE,"1cb9c079-ea9b-4899-8069-e0e3048e911d.sketch_text.stroke-30"),sQuery(id+"FHMxAyK4CFUKdhS_1.wireOp",EDGE,"1cb9c079-ea9b-4899-8069-e0e3048e911d.sketch_text.stroke-31"),sQuery(id+"FHMxAyK4CFUKdhS_1.wireOp",EDGE,"1cb9c079-ea9b-4899-8069-e0e3048e911d.sketch_text.stroke-32"),sQuery(id+"FHMxAyK4CFUKdhS_1.wireOp",EDGE,"1cb9c079-ea9b-4899-8069-e0e3048e911d.sketch_text.stroke-33"),sQuery(id+"FHMxAyK4CFUKdhS_1.wireOp",EDGE,"1cb9c079-ea9b-4899-8069-e0e3048e911d.sketch_text.stroke-34"),sQuery(id+"FHMxAyK4CFUKdhS_1.wireOp",EDGE,"1cb9c079-ea9b-4899-8069-e0e3048e911d.sketch_text.stroke-35"),sQuery(id+"FHMxAyK4CFUKdhS_1.wireOp",EDGE,"1cb9c079-ea9b-4899-8069-e0e3048e911d.sketch_text.stroke-36"),sQuery(id+"FHMxAyK4CFUKdhS_1.wireOp",EDGE,"1cb9c079-ea9b-4899-8069-e0e3048e911d.sketch_text.stroke-37"),sQuery(id+"FHMxAyK4CFUKdhS_1.wireOp",EDGE,"1cb9c079-ea9b-4899-8069-e0e3048e911d.sketch_text.stroke-38"),sQuery(id+"FHMxAyK4CFUKdhS_1.wireOp",EDGE,"1cb9c079-ea9b-4899-8069-e0e3048e911d.sketch_text.stroke-39"),sQuery(id+"FHMxAyK4CFUKdhS_1.wireOp",EDGE,"1cb9c079-ea9b-4899-8069-e0e3048e911d.sketch_text.stroke-40"),sQuery(id+"FHMxAyK4CFUKdhS_1.wireOp",EDGE,"1cb9c079-ea9b-4899-8069-e0e3048e911d.sketch_text.stroke-41"),sQuery(id+"FHMxAyK4CFUKdhS_1.wireOp",EDGE,"1cb9c079-ea9b-4899-8069-e0e3048e911d.sketch_text.stroke-42"),sQuery(id+"FHMxAyK4CFUKdhS_1.wireOp",EDGE,"1cb9c079-ea9b-4899-8069-e0e3048e911d.sketch_text.stroke-43"),sQuery(id+"FHMxAyK4CFUKdhS_1.wireOp",EDGE,"1cb9c079-ea9b-4899-8069-e0e3048e911d.sketch_text.stroke-44"),sQuery(id+"FHMxAyK4CFUKdhS_1.wireOp",EDGE,"1cb9c079-ea9b-4899-8069-e0e3048e911d.sketch_text.stroke-45"),sQuery(id+"FHMxAyK4CFUKdhS_1.wireOp",EDGE,"1cb9c079-ea9b-4899-8069-e0e3048e911d.sketch_text.stroke-46"),sQuery(id+"FHMxAyK4CFUKdhS_1.wireOp",EDGE,"1cb9c079-ea9b-4899-8069-e0e3048e911d.sketch_text.stroke-47"),sQuery(id+"FHMxAyK4CFUKdhS_1.wireOp",EDGE,"1cb9c079-ea9b-4899-8069-e0e3048e911d.sketch_text.stroke-48"),sQuery(id+"FHMxAyK4CFUKdhS_1.wireOp",EDGE,"1cb9c079-ea9b-4899-8069-e0e3048e911d.sketch_text.stroke-49"),sQuery(id+"FHMxAyK4CFUKdhS_1.wireOp",EDGE,"1cb9c079-ea9b-4899-8069-e0e3048e911d.sketch_text.stroke-50"),sQuery(id+"FHMxAyK4CFUKdhS_1.wireOp",EDGE,"1cb9c079-ea9b-4899-8069-e0e3048e911d.sketch_text.stroke-51"),sQuery(id+"FHMxAyK4CFUKdhS_1.wireOp",EDGE,"1cb9c079-ea9b-4899-8069-e0e3048e911d.sketch_text.stroke-52"),sQuery(id+"FHMxAyK4CFUKdhS_1.wireOp",EDGE,"1cb9c079-ea9b-4899-8069-e0e3048e911d.sketch_text.stroke-53"),sQuery(id+"FHMxAyK4CFUKdhS_1.wireOp",EDGE,"1cb9c079-ea9b-4899-8069-e0e3048e911d.sketch_text.stroke-54"),sQuery(id+"FHMxAyK4CFUKdhS_1.wireOp",EDGE,"1cb9c079-ea9b-4899-8069-e0e3048e911d.sketch_text.stroke-55"),sQuery(id+"FHMxAyK4CFUKdhS_1.wireOp",EDGE,"1cb9c079-ea9b-4899-8069-e0e3048e911d.sketch_text.stroke-56"),sQuery(id+"FHMxAyK4CFUKdhS_1.wireOp",EDGE,"1cb9c079-ea9b-4899-8069-e0e3048e911d.sketch_text.stroke-57"),sQuery(id+"FHMxAyK4CFUKdhS_1.wireOp",EDGE,"1cb9c079-ea9b-4899-8069-e0e3048e911d.sketch_text.stroke-58"),sQuery(id+"FHMxAyK4CFUKdhS_1.wireOp",EDGE,"1cb9c079-ea9b-4899-8069-e0e3048e911d.sketch_text.stroke-59"),sQuery(id+"FHMxAyK4CFUKdhS_1.wireOp",EDGE,"1cb9c079-ea9b-4899-8069-e0e3048e911d.sketch_text.stroke-60"),sQuery(id+"FHMxAyK4CFUKdhS_1.wireOp",EDGE,"1cb9c079-ea9b-4899-8069-e0e3048e911d.sketch_text.stroke-61"),sQuery(id+"FHMxAyK4CFUKdhS_1.wireOp",EDGE,"1cb9c079-ea9b-4899-8069-e0e3048e911d.sketch_text.stroke-62"),sQuery(id+"FHMxAyK4CFUKdhS_1.wireOp",EDGE,"1cb9c079-ea9b-4899-8069-e0e3048e911d.sketch_text.stroke-71"),sQuery(id+"FHMxAyK4CFUKdhS_1.wireOp",EDGE,"1cb9c079-ea9b-4899-8069-e0e3048e911d.sketch_text.stroke-72"),sQuery(id+"FHMxAyK4CFUKdhS_1.wireOp",EDGE,"1cb9c079-ea9b-4899-8069-e0e3048e911d.sketch_text.stroke-73"),sQuery(id+"FHMxAyK4CFUKdhS_1.wireOp",EDGE,"1cb9c079-ea9b-4899-8069-e0e3048e911d.sketch_text.stroke-74"),sQuery(id+"FHMxAyK4CFUKdhS_1.wireOp",EDGE,"1cb9c079-ea9b-4899-8069-e0e3048e911d.sketch_text.stroke-75"),sQuery(id+"FHMxAyK4CFUKdhS_1.wireOp",EDGE,"1cb9c079-ea9b-4899-8069-e0e3048e911d.sketch_text.stroke-76"),sQuery(id+"FHMxAyK4CFUKdhS_1.wireOp",EDGE,"1cb9c079-ea9b-4899-8069-e0e3048e911d.sketch_text.stroke-77"),sQuery(id+"FHMxAyK4CFUKdhS_1.wireOp",EDGE,"1cb9c079-ea9b-4899-8069-e0e3048e911d.sketch_text.stroke-78"),sQuery(id+"FHMxAyK4CFUKdhS_1.wireOp",EDGE,"1cb9c079-ea9b-4899-8069-e0e3048e911d.sketch_text.stroke-79"),sQuery(id+"FHMxAyK4CFUKdhS_1.wireOp",EDGE,"1cb9c079-ea9b-4899-8069-e0e3048e911d.sketch_text.stroke-80"),sQuery(id+"FHMxAyK4CFUKdhS_1.wireOp",EDGE,"1cb9c079-ea9b-4899-8069-e0e3048e911d.sketch_text.stroke-81"),sQuery(id+"FHMxAyK4CFUKdhS_1.wireOp",EDGE,"1cb9c079-ea9b-4899-8069-e0e3048e911d.sketch_text.stroke-82"),sQuery(id+"FHMxAyK4CFUKdhS_1.wireOp",EDGE,"1cb9c079-ea9b-4899-8069-e0e3048e911d.sketch_text.stroke-83"),sQuery(id+"FHMxAyK4CFUKdhS_1.wireOp",EDGE,"1cb9c079-ea9b-4899-8069-e0e3048e911d.sketch_text.stroke-84"),sQuery(id+"FHMxAyK4CFUKdhS_1.wireOp",EDGE,"1cb9c079-ea9b-4899-8069-e0e3048e911d.sketch_text.stroke-85"),sQuery(id+"FHMxAyK4CFUKdhS_1.wireOp",EDGE,"1cb9c079-ea9b-4899-8069-e0e3048e911d.sketch_text.stroke-86"),sQuery(id+"FHMxAyK4CFUKdhS_1.wireOp",EDGE,"1cb9c079-ea9b-4899-8069-e0e3048e911d.sketch_text.stroke-87"),sQuery(id+"FHMxAyK4CFUKdhS_1.wireOp",EDGE,"1cb9c079-ea9b-4899-8069-e0e3048e911d.sketch_text.stroke-88"),sQuery(id+"FHMxAyK4CFUKdhS_1.wireOp",EDGE,"1cb9c079-ea9b-4899-8069-e0e3048e911d.sketch_text.stroke-89"),sQuery(id+"FHMxAyK4CFUKdhS_1.wireOp",EDGE,"1cb9c079-ea9b-4899-8069-e0e3048e911d.sketch_text.stroke-90"),sQuery(id+"FHMxAyK4CFUKdhS_1.wireOp",EDGE,"1cb9c079-ea9b-4899-8069-e0e3048e911d.sketch_text.stroke-91"),sQuery(id+"FHMxAyK4CFUKdhS_1.wireOp",EDGE,"1cb9c079-ea9b-4899-8069-e0e3048e911d.sketch_text.stroke-92"),sQuery(id+"FHMxAyK4CFUKdhS_1.wireOp",EDGE,"1cb9c079-ea9b-4899-8069-e0e3048e911d.sketch_text.stroke-93"),sQuery(id+"FHMxAyK4CFUKdhS_1.wireOp",EDGE,"1cb9c079-ea9b-4899-8069-e0e3048e911d.sketch_text.stroke-94"),sQuery(id+"FHMxAyK4CFUKdhS_1.wireOp",EDGE,"1cb9c079-ea9b-4899-8069-e0e3048e911d.sketch_text.stroke-95"),sQuery(id+"FHMxAyK4CFUKdhS_1.wireOp",EDGE,"1cb9c079-ea9b-4899-8069-e0e3048e911d.sketch_text.stroke-96"),sQuery(id+"FHMxAyK4CFUKdhS_1.wireOp",EDGE,"1cb9c079-ea9b-4899-8069-e0e3048e911d.sketch_text.stroke-97"),sQuery(id+"FHMxAyK4CFUKdhS_1.wireOp",EDGE,"1cb9c079-ea9b-4899-8069-e0e3048e911d.sketch_text.stroke-103"),sQuery(id+"FHMxAyK4CFUKdhS_1.wireOp",EDGE,"1cb9c079-ea9b-4899-8069-e0e3048e911d.sketch_text.stroke-104"),sQuery(id+"FHMxAyK4CFUKdhS_1.wireOp",EDGE,"1cb9c079-ea9b-4899-8069-e0e3048e911d.sketch_text.stroke-105"),sQuery(id+"FHMxAyK4CFUKdhS_1.wireOp",EDGE,"1cb9c079-ea9b-4899-8069-e0e3048e911d.sketch_text.stroke-106"),sQuery(id+"FHMxAyK4CFUKdhS_1.wireOp",EDGE,"1cb9c079-ea9b-4899-8069-e0e3048e911d.sketch_text.stroke-107"),sQuery(id+"FHMxAyK4CFUKdhS_1.wireOp",EDGE,"1cb9c079-ea9b-4899-8069-e0e3048e911d.sketch_text.stroke-108"),sQuery(id+"FHMxAyK4CFUKdhS_1.wireOp",EDGE,"1cb9c079-ea9b-4899-8069-e0e3048e911d.sketch_text.stroke-109"),sQuery(id+"FHMxAyK4CFUKdhS_1.wireOp",EDGE,"1cb9c079-ea9b-4899-8069-e0e3048e911d.sketch_text.stroke-110"),sQuery(id+"FHMxAyK4CFUKdhS_1.wireOp",EDGE,"1cb9c079-ea9b-4899-8069-e0e3048e911d.sketch_text.stroke-111"),sQuery(id+"FHMxAyK4CFUKdhS_1.wireOp",EDGE,"1cb9c079-ea9b-4899-8069-e0e3048e911d.sketch_text.stroke-112"),sQuery(id+"FHMxAyK4CFUKdhS_1.wireOp",EDGE,"1cb9c079-ea9b-4899-8069-e0e3048e911d.sketch_text.stroke-113"),sQuery(id+"FHMxAyK4CFUKdhS_1.wireOp",EDGE,"1cb9c079-ea9b-4899-8069-e0e3048e911d.sketch_text.stroke-114"),sQuery(id+"FHMxAyK4CFUKdhS_1.wireOp",EDGE,"1cb9c079-ea9b-4899-8069-e0e3048e911d.sketch_text.stroke-115"),sQuery(id+"FHMxAyK4CFUKdhS_1.wireOp",EDGE,"1cb9c079-ea9b-4899-8069-e0e3048e911d.sketch_text.stroke-116"),sQuery(id+"FHMxAyK4CFUKdhS_1.wireOp",EDGE,"1cb9c079-ea9b-4899-8069-e0e3048e911d.sketch_text.stroke-117"),sQuery(id+"FHMxAyK4CFUKdhS_1.wireOp",EDGE,"1cb9c079-ea9b-4899-8069-e0e3048e911d.sketch_text.stroke-118"),sQuery(id+"FHMxAyK4CFUKdhS_1.wireOp",EDGE,"1cb9c079-ea9b-4899-8069-e0e3048e911d.sketch_text.stroke-119"),sQuery(id+"FHMxAyK4CFUKdhS_1.wireOp",EDGE,"1cb9c079-ea9b-4899-8069-e0e3048e911d.sketch_text.stroke-120"),sQuery(id+"FHMxAyK4CFUKdhS_1.wireOp",EDGE,"1cb9c079-ea9b-4899-8069-e0e3048e911d.sketch_text.stroke-121"),sQuery(id+"FHMxAyK4CFUKdhS_1.wireOp",EDGE,"1cb9c079-ea9b-4899-8069-e0e3048e911d.sketch_text.stroke-122"),sQuery(id+"FHMxAyK4CFUKdhS_1.wireOp",EDGE,"1cb9c079-ea9b-4899-8069-e0e3048e911d.sketch_text.stroke-123"),sQuery(id+"FHMxAyK4CFUKdhS_1.wireOp",EDGE,"1cb9c079-ea9b-4899-8069-e0e3048e911d.sketch_text.stroke-124"),sQuery(id+"FHMxAyK4CFUKdhS_1.wireOp",EDGE,"1cb9c079-ea9b-4899-8069-e0e3048e911d.sketch_text.stroke-125"),sQuery(id+"FHMxAyK4CFUKdhS_1.wireOp",EDGE,"1cb9c079-ea9b-4899-8069-e0e3048e911d.sketch_text.stroke-126"),sQuery(id+"FHMxAyK4CFUKdhS_1.wireOp",EDGE,"1cb9c079-ea9b-4899-8069-e0e3048e911d.sketch_text.stroke-127"),sQuery(id+"FHMxAyK4CFUKdhS_1.wireOp",EDGE,"1cb9c079-ea9b-4899-8069-e0e3048e911d.sketch_text.stroke-128"),sQuery(id+"FHMxAyK4CFUKdhS_1.wireOp",EDGE,"1cb9c079-ea9b-4899-8069-e0e3048e911d.sketch_text.stroke-129"),sQuery(id+"FHMxAyK4CFUKdhS_1.wireOp",EDGE,"1cb9c079-ea9b-4899-8069-e0e3048e911d.sketch_text.stroke-130"),sQuery(id+"FHMxAyK4CFUKdhS_1.wireOp",EDGE,"1cb9c079-ea9b-4899-8069-e0e3048e911d.sketch_text.stroke-131"),sQuery(id+"FHMxAyK4CFUKdhS_1.wireOp",EDGE,"1cb9c079-ea9b-4899-8069-e0e3048e911d.sketch_text.stroke-132"),sQuery(id+"FHMxAyK4CFUKdhS_1.wireOp",EDGE,"1cb9c079-ea9b-4899-8069-e0e3048e911d.sketch_text.stroke-133"),sQuery(id+"FHMxAyK4CFUKdhS_1.wireOp",EDGE,"1cb9c079-ea9b-4899-8069-e0e3048e911d.sketch_text.stroke-134"),sQuery(id+"FHMxAyK4CFUKdhS_1.wireOp",EDGE,"1cb9c079-ea9b-4899-8069-e0e3048e911d.sketch_text.stroke-135"),sQuery(id+"FHMxAyK4CFUKdhS_1.wireOp",EDGE,"1cb9c079-ea9b-4899-8069-e0e3048e911d.sketch_text.stroke-136"),sQuery(id+"FHMxAyK4CFUKdhS_1.wireOp",EDGE,"1cb9c079-ea9b-4899-8069-e0e3048e911d.sketch_text.stroke-137"),sQuery(id+"FHMxAyK4CFUKdhS_1.wireOp",EDGE,"1cb9c079-ea9b-4899-8069-e0e3048e911d.sketch_text.stroke-138"),sQuery(id+"FHMxAyK4CFUKdhS_1.wireOp",EDGE,"1cb9c079-ea9b-4899-8069-e0e3048e911d.sketch_text.stroke-139"),sQuery(id+"FHMxAyK4CFUKdhS_1.wireOp",EDGE,"1cb9c079-ea9b-4899-8069-e0e3048e911d.sketch_text.stroke-140"),sQuery(id+"FHMxAyK4CFUKdhS_1.wireOp",EDGE,"1cb9c079-ea9b-4899-8069-e0e3048e911d.sketch_text.stroke-141"),sQuery(id+"FHMxAyK4CFUKdhS_1.wireOp",EDGE,"1cb9c079-ea9b-4899-8069-e0e3048e911d.sketch_text.stroke-142"),sQuery(id+"FHMxAyK4CFUKdhS_1.wireOp",EDGE,"1cb9c079-ea9b-4899-8069-e0e3048e911d.sketch_text.stroke-143"),sQuery(id+"FHMxAyK4CFUKdhS_1.wireOp",EDGE,"1cb9c079-ea9b-4899-8069-e0e3048e911d.sketch_text.stroke-144"),sQuery(id+"FHMxAyK4CFUKdhS_1.wireOp",EDGE,"1cb9c079-ea9b-4899-8069-e0e3048e911d.sketch_text.stroke-145"),sQuery(id+"FHMxAyK4CFUKdhS_1.wireOp",EDGE,"1cb9c079-ea9b-4899-8069-e0e3048e911d.sketch_text.stroke-146"),sQuery(id+"FHMxAyK4CFUKdhS_1.wireOp",EDGE,"1cb9c079-ea9b-4899-8069-e0e3048e911d.sketch_text.stroke-147"),sQuery(id+"FHMxAyK4CFUKdhS_1.wireOp",EDGE,"1cb9c079-ea9b-4899-8069-e0e3048e911d.sketch_text.stroke-148"),sQuery(id+"FHMxAyK4CFUKdhS_1.wireOp",EDGE,"1cb9c079-ea9b-4899-8069-e0e3048e911d.sketch_text.stroke-149"),sQuery(id+"FHMxAyK4CFUKdhS_1.wireOp",EDGE,"1cb9c079-ea9b-4899-8069-e0e3048e911d.sketch_text.stroke-150"),sQuery(id+"FHMxAyK4CFUKdhS_1.wireOp",EDGE,"1cb9c079-ea9b-4899-8069-e0e3048e911d.sketch_text.stroke-151"),sQuery(id+"FHMxAyK4CFUKdhS_1.wireOp",EDGE,"1cb9c079-ea9b-4899-8069-e0e3048e911d.sketch_text.stroke-152"),sQuery(id+"FHMxAyK4CFUKdhS_1.wireOp",EDGE,"1cb9c079-ea9b-4899-8069-e0e3048e911d.sketch_text.stroke-153"),sQuery(id+"FHMxAyK4CFUKdhS_1.wireOp",EDGE,"1cb9c079-ea9b-4899-8069-e0e3048e911d.sketch_text.stroke-159"),sQuery(id+"FHMxAyK4CFUKdhS_1.wireOp",EDGE,"1cb9c079-ea9b-4899-8069-e0e3048e911d.sketch_text.stroke-160"),sQuery(id+"FHMxAyK4CFUKdhS_1.wireOp",EDGE,"1cb9c079-ea9b-4899-8069-e0e3048e911d.sketch_text.stroke-161"),sQuery(id+"FHMxAyK4CFUKdhS_1.wireOp",EDGE,"1cb9c079-ea9b-4899-8069-e0e3048e911d.sketch_text.stroke-162"),sQuery(id+"FHMxAyK4CFUKdhS_1.wireOp",EDGE,"1cb9c079-ea9b-4899-8069-e0e3048e911d.sketch_text.stroke-163"),sQuery(id+"FHMxAyK4CFUKdhS_1.wireOp",EDGE,"1cb9c079-ea9b-4899-8069-e0e3048e911d.sketch_text.stroke-164"),sQuery(id+"FHMxAyK4CFUKdhS_1.wireOp",EDGE,"1cb9c079-ea9b-4899-8069-e0e3048e911d.sketch_text.stroke-165"),sQuery(id+"FHMxAyK4CFUKdhS_1.wireOp",EDGE,"1cb9c079-ea9b-4899-8069-e0e3048e911d.sketch_text.stroke-166"),sQuery(id+"FHMxAyK4CFUKdhS_1.wireOp",EDGE,"1cb9c079-ea9b-4899-8069-e0e3048e911d.sketch_text.stroke-167"),sQuery(id+"FHMxAyK4CFUKdhS_1.wireOp",EDGE,"1cb9c079-ea9b-4899-8069-e0e3048e911d.sketch_text.stroke-168"),sQuery(id+"FHMxAyK4CFUKdhS_1.wireOp",EDGE,"1cb9c079-ea9b-4899-8069-e0e3048e911d.sketch_text.stroke-169"),sQuery(id+"FHMxAyK4CFUKdhS_1.wireOp",EDGE,"1cb9c079-ea9b-4899-8069-e0e3048e911d.sketch_text.stroke-170"),sQuery(id+"FHMxAyK4CFUKdhS_1.wireOp",EDGE,"1cb9c079-ea9b-4899-8069-e0e3048e911d.sketch_text.stroke-171"),sQuery(id+"FHMxAyK4CFUKdhS_1.wireOp",EDGE,"1cb9c079-ea9b-4899-8069-e0e3048e911d.sketch_text.stroke-172"),sQuery(id+"FHMxAyK4CFUKdhS_1.wireOp",EDGE,"1cb9c079-ea9b-4899-8069-e0e3048e911d.sketch_text.stroke-173"),sQuery(id+"FHMxAyK4CFUKdhS_1.wireOp",EDGE,"1cb9c079-ea9b-4899-8069-e0e3048e911d.sketch_text.stroke-174"),sQuery(id+"FHMxAyK4CFUKdhS_1.wireOp",EDGE,"1cb9c079-ea9b-4899-8069-e0e3048e911d.sketch_text.stroke-175"),sQuery(id+"FHMxAyK4CFUKdhS_1.wireOp",EDGE,"1cb9c079-ea9b-4899-8069-e0e3048e911d.sketch_text.stroke-176"),sQuery(id+"FHMxAyK4CFUKdhS_1.wireOp",EDGE,"1cb9c079-ea9b-4899-8069-e0e3048e911d.sketch_text.stroke-177"),sQuery(id+"FHMxAyK4CFUKdhS_1.wireOp",EDGE,"1cb9c079-ea9b-4899-8069-e0e3048e911d.sketch_text.stroke-178"),sQuery(id+"FHMxAyK4CFUKdhS_1.wireOp",EDGE,"1cb9c079-ea9b-4899-8069-e0e3048e911d.sketch_text.stroke-179"),sQuery(id+"FHMxAyK4CFUKdhS_1.wireOp",EDGE,"1cb9c079-ea9b-4899-8069-e0e3048e911d.sketch_text.stroke-180"),subQ2,sQuery(id+"F3.wireOp",EDGE,"6ee83ff3-586e-4dbe-aaea-af71240543bd")])],"isStart":true})])],"derivedFrom":makeQuery(id+"F4.opExtrude","CAP_EDGE",EDGE,{"disambiguationData":[OSD([subQ2])],"isStart":true})});}
            var Q3;
            {var subQ0=sQuery(id+"F3.wireOp",EDGE,"8007402e-1a4e-4a06-85a5-2af08e553504");var subQ1=sQuery(id+"F0.wireOp",EDGE,"E0.top");var subQ2=sQuery(id+"F3.wireOp",EDGE,"6ee83ff3-586e-4dbe-aaea-af71240543bd");var subQ3=sQuery(id+"F0.wireOp",EDGE,"E0.bottom");Q3=makeQuery(id+"F4.boolean.opBoolean","SPLIT",EDGE,{"disambiguationData":[TD([makeQuery(id+"F1.opExtrude","CAP_FACE",FACE,{"disambiguationData":[OSD([subQ3,subQ1,sQuery(id+"F0.wireOp",EDGE,"E0.left"),sQuery(id+"F0.wireOp",EDGE,"E0.right")])],"isStart":false}),makeQuery(id+"F1.opExtrude","SWEPT_FACE",FACE,{"disambiguationData":[OSD([subQ1])]}),makeQuery(id+"F4.opExtrude","SWEPT_FACE",FACE,{"disambiguationData":[OSD([subQ0])]}),makeQuery(id+"F4.opExtrude","CAP_FACE",FACE,{"disambiguationData":[OSD([subQ3,sQuery(id+"F2.wireOp",EDGE,"fcba4419-a2ee-464f-be9d-58f11bf3418b.sketch_text.stroke-0"),sQuery(id+"F2.wireOp",EDGE,"fcba4419-a2ee-464f-be9d-58f11bf3418b.sketch_text.stroke-1"),sQuery(id+"F2.wireOp",EDGE,"fcba4419-a2ee-464f-be9d-58f11bf3418b.sketch_text.stroke-2"),sQuery(id+"F2.wireOp",EDGE,"fcba4419-a2ee-464f-be9d-58f11bf3418b.sketch_text.stroke-3"),sQuery(id+"F2.wireOp",EDGE,"fcba4419-a2ee-464f-be9d-58f11bf3418b.sketch_text.stroke-4"),sQuery(id+"F2.wireOp",EDGE,"fcba4419-a2ee-464f-be9d-58f11bf3418b.sketch_text.stroke-5"),sQuery(id+"F2.wireOp",EDGE,"fcba4419-a2ee-464f-be9d-58f11bf3418b.sketch_text.stroke-6"),sQuery(id+"F2.wireOp",EDGE,"fcba4419-a2ee-464f-be9d-58f11bf3418b.sketch_text.stroke-7"),sQuery(id+"F2.wireOp",EDGE,"fcba4419-a2ee-464f-be9d-58f11bf3418b.sketch_text.stroke-8"),sQuery(id+"F2.wireOp",EDGE,"fcba4419-a2ee-464f-be9d-58f11bf3418b.sketch_text.stroke-9"),sQuery(id+"F2.wireOp",EDGE,"fcba4419-a2ee-464f-be9d-58f11bf3418b.sketch_text.stroke-10"),sQuery(id+"F2.wireOp",EDGE,"fcba4419-a2ee-464f-be9d-58f11bf3418b.sketch_text.stroke-11"),sQuery(id+"F2.wireOp",EDGE,"fcba4419-a2ee-464f-be9d-58f11bf3418b.sketch_text.stroke-12"),sQuery(id+"F2.wireOp",EDGE,"fcba4419-a2ee-464f-be9d-58f11bf3418b.sketch_text.stroke-13"),sQuery(id+"F2.wireOp",EDGE,"fcba4419-a2ee-464f-be9d-58f11bf3418b.sketch_text.stroke-14"),sQuery(id+"F2.wireOp",EDGE,"fcba4419-a2ee-464f-be9d-58f11bf3418b.sketch_text.stroke-15"),sQuery(id+"F2.wireOp",EDGE,"fcba4419-a2ee-464f-be9d-58f11bf3418b.sketch_text.stroke-16"),sQuery(id+"F2.wireOp",EDGE,"fcba4419-a2ee-464f-be9d-58f11bf3418b.sketch_text.stroke-17"),sQuery(id+"F2.wireOp",EDGE,"fcba4419-a2ee-464f-be9d-58f11bf3418b.sketch_text.stroke-18"),sQuery(id+"F2.wireOp",EDGE,"fcba4419-a2ee-464f-be9d-58f11bf3418b.sketch_text.stroke-19"),sQuery(id+"F2.wireOp",EDGE,"fcba4419-a2ee-464f-be9d-58f11bf3418b.sketch_text.stroke-20"),sQuery(id+"F2.wireOp",EDGE,"fcba4419-a2ee-464f-be9d-58f11bf3418b.sketch_text.stroke-21"),sQuery(id+"F2.wireOp",EDGE,"fcba4419-a2ee-464f-be9d-58f11bf3418b.sketch_text.stroke-22"),sQuery(id+"F2.wireOp",EDGE,"fcba4419-a2ee-464f-be9d-58f11bf3418b.sketch_text.stroke-23"),sQuery(id+"F2.wireOp",EDGE,"fcba4419-a2ee-464f-be9d-58f11bf3418b.sketch_text.stroke-24"),sQuery(id+"F2.wireOp",EDGE,"fcba4419-a2ee-464f-be9d-58f11bf3418b.sketch_text.stroke-25"),sQuery(id+"F2.wireOp",EDGE,"fcba4419-a2ee-464f-be9d-58f11bf3418b.sketch_text.stroke-26"),sQuery(id+"F2.wireOp",EDGE,"fcba4419-a2ee-464f-be9d-58f11bf3418b.sketch_text.stroke-27"),sQuery(id+"F2.wireOp",EDGE,"fcba4419-a2ee-464f-be9d-58f11bf3418b.sketch_text.stroke-28"),sQuery(id+"F2.wireOp",EDGE,"fcba4419-a2ee-464f-be9d-58f11bf3418b.sketch_text.stroke-29"),sQuery(id+"F2.wireOp",EDGE,"fcba4419-a2ee-464f-be9d-58f11bf3418b.sketch_text.stroke-30"),sQuery(id+"F2.wireOp",EDGE,"fcba4419-a2ee-464f-be9d-58f11bf3418b.sketch_text.stroke-31"),sQuery(id+"F2.wireOp",EDGE,"fcba4419-a2ee-464f-be9d-58f11bf3418b.sketch_text.stroke-32"),sQuery(id+"F2.wireOp",EDGE,"fcba4419-a2ee-464f-be9d-58f11bf3418b.sketch_text.stroke-33"),sQuery(id+"F2.wireOp",EDGE,"fcba4419-a2ee-464f-be9d-58f11bf3418b.sketch_text.stroke-34"),sQuery(id+"F2.wireOp",EDGE,"fcba4419-a2ee-464f-be9d-58f11bf3418b.sketch_text.stroke-35"),sQuery(id+"F2.wireOp",EDGE,"fcba4419-a2ee-464f-be9d-58f11bf3418b.sketch_text.stroke-36"),sQuery(id+"F2.wireOp",EDGE,"fcba4419-a2ee-464f-be9d-58f11bf3418b.sketch_text.stroke-37"),sQuery(id+"F2.wireOp",EDGE,"fcba4419-a2ee-464f-be9d-58f11bf3418b.sketch_text.stroke-38"),sQuery(id+"F2.wireOp",EDGE,"fcba4419-a2ee-464f-be9d-58f11bf3418b.sketch_text.stroke-39"),sQuery(id+"F2.wireOp",EDGE,"fcba4419-a2ee-464f-be9d-58f11bf3418b.sketch_text.stroke-40"),sQuery(id+"F2.wireOp",EDGE,"fcba4419-a2ee-464f-be9d-58f11bf3418b.sketch_text.stroke-41"),sQuery(id+"F2.wireOp",EDGE,"fcba4419-a2ee-464f-be9d-58f11bf3418b.sketch_text.stroke-42"),sQuery(id+"F2.wireOp",EDGE,"fcba4419-a2ee-464f-be9d-58f11bf3418b.sketch_text.stroke-43"),sQuery(id+"F2.wireOp",EDGE,"fcba4419-a2ee-464f-be9d-58f11bf3418b.sketch_text.stroke-44"),sQuery(id+"F2.wireOp",EDGE,"fcba4419-a2ee-464f-be9d-58f11bf3418b.sketch_text.stroke-45"),sQuery(id+"F2.wireOp",EDGE,"fcba4419-a2ee-464f-be9d-58f11bf3418b.sketch_text.stroke-46"),sQuery(id+"F2.wireOp",EDGE,"fcba4419-a2ee-464f-be9d-58f11bf3418b.sketch_text.stroke-47"),sQuery(id+"F2.wireOp",EDGE,"fcba4419-a2ee-464f-be9d-58f11bf3418b.sketch_text.stroke-48"),sQuery(id+"F2.wireOp",EDGE,"fcba4419-a2ee-464f-be9d-58f11bf3418b.sketch_text.stroke-49"),sQuery(id+"F2.wireOp",EDGE,"fcba4419-a2ee-464f-be9d-58f11bf3418b.sketch_text.stroke-50"),sQuery(id+"F2.wireOp",EDGE,"fcba4419-a2ee-464f-be9d-58f11bf3418b.sketch_text.stroke-51"),sQuery(id+"F2.wireOp",EDGE,"fcba4419-a2ee-464f-be9d-58f11bf3418b.sketch_text.stroke-52"),sQuery(id+"F2.wireOp",EDGE,"fcba4419-a2ee-464f-be9d-58f11bf3418b.sketch_text.stroke-53"),sQuery(id+"F2.wireOp",EDGE,"fcba4419-a2ee-464f-be9d-58f11bf3418b.sketch_text.stroke-54"),sQuery(id+"F2.wireOp",EDGE,"fcba4419-a2ee-464f-be9d-58f11bf3418b.sketch_text.stroke-55"),sQuery(id+"F2.wireOp",EDGE,"fcba4419-a2ee-464f-be9d-58f11bf3418b.sketch_text.stroke-56"),sQuery(id+"F2.wireOp",EDGE,"fcba4419-a2ee-464f-be9d-58f11bf3418b.sketch_text.stroke-57"),sQuery(id+"F2.wireOp",EDGE,"fcba4419-a2ee-464f-be9d-58f11bf3418b.sketch_text.stroke-58"),sQuery(id+"F2.wireOp",EDGE,"fcba4419-a2ee-464f-be9d-58f11bf3418b.sketch_text.stroke-59"),sQuery(id+"F2.wireOp",EDGE,"fcba4419-a2ee-464f-be9d-58f11bf3418b.sketch_text.stroke-60"),sQuery(id+"F2.wireOp",EDGE,"fcba4419-a2ee-464f-be9d-58f11bf3418b.sketch_text.stroke-61"),sQuery(id+"F2.wireOp",EDGE,"fcba4419-a2ee-464f-be9d-58f11bf3418b.sketch_text.stroke-62"),sQuery(id+"F2.wireOp",EDGE,"fcba4419-a2ee-464f-be9d-58f11bf3418b.sketch_text.stroke-63"),sQuery(id+"F2.wireOp",EDGE,"fcba4419-a2ee-464f-be9d-58f11bf3418b.sketch_text.stroke-64"),sQuery(id+"F2.wireOp",EDGE,"fcba4419-a2ee-464f-be9d-58f11bf3418b.sketch_text.stroke-65"),sQuery(id+"F2.wireOp",EDGE,"fcba4419-a2ee-464f-be9d-58f11bf3418b.sketch_text.stroke-66"),sQuery(id+"F2.wireOp",EDGE,"fcba4419-a2ee-464f-be9d-58f11bf3418b.sketch_text.stroke-67"),sQuery(id+"F2.wireOp",EDGE,"fcba4419-a2ee-464f-be9d-58f11bf3418b.sketch_text.stroke-68"),sQuery(id+"F2.wireOp",EDGE,"fcba4419-a2ee-464f-be9d-58f11bf3418b.sketch_text.stroke-69"),sQuery(id+"F2.wireOp",EDGE,"fcba4419-a2ee-464f-be9d-58f11bf3418b.sketch_text.stroke-70"),sQuery(id+"F2.wireOp",EDGE,"fcba4419-a2ee-464f-be9d-58f11bf3418b.sketch_text.stroke-71"),sQuery(id+"F2.wireOp",EDGE,"fcba4419-a2ee-464f-be9d-58f11bf3418b.sketch_text.stroke-72"),sQuery(id+"F2.wireOp",EDGE,"fcba4419-a2ee-464f-be9d-58f11bf3418b.sketch_text.stroke-73"),sQuery(id+"F2.wireOp",EDGE,"fcba4419-a2ee-464f-be9d-58f11bf3418b.sketch_text.stroke-74"),sQuery(id+"F2.wireOp",EDGE,"fcba4419-a2ee-464f-be9d-58f11bf3418b.sketch_text.stroke-75"),sQuery(id+"F2.wireOp",EDGE,"fcba4419-a2ee-464f-be9d-58f11bf3418b.sketch_text.stroke-76"),sQuery(id+"F2.wireOp",EDGE,"fcba4419-a2ee-464f-be9d-58f11bf3418b.sketch_text.stroke-77"),sQuery(id+"F2.wireOp",EDGE,"fcba4419-a2ee-464f-be9d-58f11bf3418b.sketch_text.stroke-78"),sQuery(id+"F2.wireOp",EDGE,"fcba4419-a2ee-464f-be9d-58f11bf3418b.sketch_text.stroke-79"),sQuery(id+"F2.wireOp",EDGE,"fcba4419-a2ee-464f-be9d-58f11bf3418b.sketch_text.stroke-80"),sQuery(id+"F2.wireOp",EDGE,"fcba4419-a2ee-464f-be9d-58f11bf3418b.sketch_text.stroke-81"),sQuery(id+"F2.wireOp",EDGE,"fcba4419-a2ee-464f-be9d-58f11bf3418b.sketch_text.stroke-82"),sQuery(id+"F2.wireOp",EDGE,"fcba4419-a2ee-464f-be9d-58f11bf3418b.sketch_text.stroke-83"),sQuery(id+"F2.wireOp",EDGE,"fcba4419-a2ee-464f-be9d-58f11bf3418b.sketch_text.stroke-84"),sQuery(id+"F2.wireOp",EDGE,"fcba4419-a2ee-464f-be9d-58f11bf3418b.sketch_text.stroke-85"),sQuery(id+"F2.wireOp",EDGE,"fcba4419-a2ee-464f-be9d-58f11bf3418b.sketch_text.stroke-86"),sQuery(id+"F2.wireOp",EDGE,"fcba4419-a2ee-464f-be9d-58f11bf3418b.sketch_text.stroke-87"),sQuery(id+"F2.wireOp",EDGE,"fcba4419-a2ee-464f-be9d-58f11bf3418b.sketch_text.stroke-88"),sQuery(id+"F2.wireOp",EDGE,"fcba4419-a2ee-464f-be9d-58f11bf3418b.sketch_text.stroke-89"),sQuery(id+"F2.wireOp",EDGE,"fcba4419-a2ee-464f-be9d-58f11bf3418b.sketch_text.stroke-90"),sQuery(id+"F2.wireOp",EDGE,"fcba4419-a2ee-464f-be9d-58f11bf3418b.sketch_text.stroke-91"),sQuery(id+"F2.wireOp",EDGE,"fcba4419-a2ee-464f-be9d-58f11bf3418b.sketch_text.stroke-92"),sQuery(id+"F2.wireOp",EDGE,"fcba4419-a2ee-464f-be9d-58f11bf3418b.sketch_text.stroke-93"),sQuery(id+"F2.wireOp",EDGE,"fcba4419-a2ee-464f-be9d-58f11bf3418b.sketch_text.stroke-94"),sQuery(id+"F2.wireOp",EDGE,"fcba4419-a2ee-464f-be9d-58f11bf3418b.sketch_text.stroke-95"),sQuery(id+"F2.wireOp",EDGE,"fcba4419-a2ee-464f-be9d-58f11bf3418b.sketch_text.stroke-96"),sQuery(id+"F2.wireOp",EDGE,"fcba4419-a2ee-464f-be9d-58f11bf3418b.sketch_text.stroke-97"),sQuery(id+"F2.wireOp",EDGE,"fcba4419-a2ee-464f-be9d-58f11bf3418b.sketch_text.stroke-98"),sQuery(id+"F2.wireOp",EDGE,"fcba4419-a2ee-464f-be9d-58f11bf3418b.sketch_text.stroke-99"),sQuery(id+"F2.wireOp",EDGE,"fcba4419-a2ee-464f-be9d-58f11bf3418b.sketch_text.stroke-100"),sQuery(id+"F2.wireOp",EDGE,"fcba4419-a2ee-464f-be9d-58f11bf3418b.sketch_text.stroke-101"),sQuery(id+"F2.wireOp",EDGE,"fcba4419-a2ee-464f-be9d-58f11bf3418b.sketch_text.stroke-102"),sQuery(id+"F2.wireOp",EDGE,"fcba4419-a2ee-464f-be9d-58f11bf3418b.sketch_text.stroke-103"),sQuery(id+"F2.wireOp",EDGE,"fcba4419-a2ee-464f-be9d-58f11bf3418b.sketch_text.stroke-104"),sQuery(id+"F2.wireOp",EDGE,"fcba4419-a2ee-464f-be9d-58f11bf3418b.sketch_text.stroke-105"),sQuery(id+"F2.wireOp",EDGE,"fcba4419-a2ee-464f-be9d-58f11bf3418b.sketch_text.stroke-106"),sQuery(id+"F2.wireOp",EDGE,"fcba4419-a2ee-464f-be9d-58f11bf3418b.sketch_text.stroke-107"),sQuery(id+"F2.wireOp",EDGE,"fcba4419-a2ee-464f-be9d-58f11bf3418b.sketch_text.stroke-108"),sQuery(id+"F2.wireOp",EDGE,"fcba4419-a2ee-464f-be9d-58f11bf3418b.sketch_text.stroke-109"),sQuery(id+"F2.wireOp",EDGE,"fcba4419-a2ee-464f-be9d-58f11bf3418b.sketch_text.stroke-110"),sQuery(id+"F2.wireOp",EDGE,"fcba4419-a2ee-464f-be9d-58f11bf3418b.sketch_text.stroke-111"),sQuery(id+"F2.wireOp",EDGE,"fcba4419-a2ee-464f-be9d-58f11bf3418b.sketch_text.stroke-112"),sQuery(id+"F2.wireOp",EDGE,"fcba4419-a2ee-464f-be9d-58f11bf3418b.sketch_text.stroke-113"),sQuery(id+"F2.wireOp",EDGE,"fcba4419-a2ee-464f-be9d-58f11bf3418b.sketch_text.stroke-114"),sQuery(id+"F2.wireOp",EDGE,"fcba4419-a2ee-464f-be9d-58f11bf3418b.sketch_text.stroke-115"),sQuery(id+"F2.wireOp",EDGE,"fcba4419-a2ee-464f-be9d-58f11bf3418b.sketch_text.stroke-116"),sQuery(id+"F2.wireOp",EDGE,"fcba4419-a2ee-464f-be9d-58f11bf3418b.sketch_text.stroke-117"),sQuery(id+"F2.wireOp",EDGE,"fcba4419-a2ee-464f-be9d-58f11bf3418b.sketch_text.stroke-118"),sQuery(id+"F2.wireOp",EDGE,"fcba4419-a2ee-464f-be9d-58f11bf3418b.sketch_text.stroke-119"),sQuery(id+"F2.wireOp",EDGE,"fcba4419-a2ee-464f-be9d-58f11bf3418b.sketch_text.stroke-120"),sQuery(id+"F2.wireOp",EDGE,"fcba4419-a2ee-464f-be9d-58f11bf3418b.sketch_text.stroke-121"),sQuery(id+"F2.wireOp",EDGE,"fcba4419-a2ee-464f-be9d-58f11bf3418b.sketch_text.stroke-122"),sQuery(id+"F2.wireOp",EDGE,"fcba4419-a2ee-464f-be9d-58f11bf3418b.sketch_text.stroke-123"),sQuery(id+"F2.wireOp",EDGE,"fcba4419-a2ee-464f-be9d-58f11bf3418b.sketch_text.stroke-124"),sQuery(id+"F2.wireOp",EDGE,"fcba4419-a2ee-464f-be9d-58f11bf3418b.sketch_text.stroke-125"),sQuery(id+"F2.wireOp",EDGE,"fcba4419-a2ee-464f-be9d-58f11bf3418b.sketch_text.stroke-126"),sQuery(id+"F2.wireOp",EDGE,"fcba4419-a2ee-464f-be9d-58f11bf3418b.sketch_text.stroke-127"),sQuery(id+"F2.wireOp",EDGE,"fcba4419-a2ee-464f-be9d-58f11bf3418b.sketch_text.stroke-128"),sQuery(id+"F2.wireOp",EDGE,"fcba4419-a2ee-464f-be9d-58f11bf3418b.sketch_text.stroke-129"),sQuery(id+"F2.wireOp",EDGE,"fcba4419-a2ee-464f-be9d-58f11bf3418b.sketch_text.stroke-130"),sQuery(id+"F2.wireOp",EDGE,"fcba4419-a2ee-464f-be9d-58f11bf3418b.sketch_text.stroke-131"),sQuery(id+"F2.wireOp",EDGE,"fcba4419-a2ee-464f-be9d-58f11bf3418b.sketch_text.stroke-132"),sQuery(id+"F2.wireOp",EDGE,"fcba4419-a2ee-464f-be9d-58f11bf3418b.sketch_text.stroke-133"),sQuery(id+"F2.wireOp",EDGE,"fcba4419-a2ee-464f-be9d-58f11bf3418b.sketch_text.stroke-134"),sQuery(id+"F2.wireOp",EDGE,"fcba4419-a2ee-464f-be9d-58f11bf3418b.sketch_text.stroke-135"),sQuery(id+"F2.wireOp",EDGE,"fcba4419-a2ee-464f-be9d-58f11bf3418b.sketch_text.stroke-136"),sQuery(id+"F2.wireOp",EDGE,"fcba4419-a2ee-464f-be9d-58f11bf3418b.sketch_text.stroke-137"),sQuery(id+"F2.wireOp",EDGE,"fcba4419-a2ee-464f-be9d-58f11bf3418b.sketch_text.stroke-138"),sQuery(id+"F2.wireOp",EDGE,"fcba4419-a2ee-464f-be9d-58f11bf3418b.sketch_text.stroke-139"),sQuery(id+"F2.wireOp",EDGE,"fcba4419-a2ee-464f-be9d-58f11bf3418b.sketch_text.stroke-140"),sQuery(id+"F2.wireOp",EDGE,"fcba4419-a2ee-464f-be9d-58f11bf3418b.sketch_text.stroke-141"),sQuery(id+"F2.wireOp",EDGE,"fcba4419-a2ee-464f-be9d-58f11bf3418b.sketch_text.stroke-142"),sQuery(id+"F2.wireOp",EDGE,"fcba4419-a2ee-464f-be9d-58f11bf3418b.sketch_text.stroke-143"),sQuery(id+"F2.wireOp",EDGE,"fcba4419-a2ee-464f-be9d-58f11bf3418b.sketch_text.stroke-144"),sQuery(id+"F2.wireOp",EDGE,"fcba4419-a2ee-464f-be9d-58f11bf3418b.sketch_text.stroke-145"),sQuery(id+"F2.wireOp",EDGE,"fcba4419-a2ee-464f-be9d-58f11bf3418b.sketch_text.stroke-146"),sQuery(id+"F2.wireOp",EDGE,"fcba4419-a2ee-464f-be9d-58f11bf3418b.sketch_text.stroke-147"),sQuery(id+"F2.wireOp",EDGE,"fcba4419-a2ee-464f-be9d-58f11bf3418b.sketch_text.stroke-148"),sQuery(id+"F2.wireOp",EDGE,"fcba4419-a2ee-464f-be9d-58f11bf3418b.sketch_text.stroke-149"),sQuery(id+"F2.wireOp",EDGE,"fcba4419-a2ee-464f-be9d-58f11bf3418b.sketch_text.stroke-150"),sQuery(id+"F2.wireOp",EDGE,"fcba4419-a2ee-464f-be9d-58f11bf3418b.sketch_text.stroke-151"),sQuery(id+"F2.wireOp",EDGE,"fcba4419-a2ee-464f-be9d-58f11bf3418b.sketch_text.stroke-152"),sQuery(id+"F2.wireOp",EDGE,"fcba4419-a2ee-464f-be9d-58f11bf3418b.sketch_text.stroke-153"),sQuery(id+"F2.wireOp",EDGE,"fcba4419-a2ee-464f-be9d-58f11bf3418b.sketch_text.stroke-154"),sQuery(id+"F2.wireOp",EDGE,"fcba4419-a2ee-464f-be9d-58f11bf3418b.sketch_text.stroke-155"),sQuery(id+"F2.wireOp",EDGE,"fcba4419-a2ee-464f-be9d-58f11bf3418b.sketch_text.stroke-156"),sQuery(id+"F2.wireOp",EDGE,"fcba4419-a2ee-464f-be9d-58f11bf3418b.sketch_text.stroke-157"),sQuery(id+"F2.wireOp",EDGE,"fcba4419-a2ee-464f-be9d-58f11bf3418b.sketch_text.stroke-158"),sQuery(id+"F2.wireOp",EDGE,"fcba4419-a2ee-464f-be9d-58f11bf3418b.sketch_text.stroke-159"),sQuery(id+"F2.wireOp",EDGE,"fcba4419-a2ee-464f-be9d-58f11bf3418b.sketch_text.stroke-160"),sQuery(id+"F2.wireOp",EDGE,"fcba4419-a2ee-464f-be9d-58f11bf3418b.sketch_text.stroke-161"),sQuery(id+"F2.wireOp",EDGE,"fcba4419-a2ee-464f-be9d-58f11bf3418b.sketch_text.stroke-162"),sQuery(id+"F2.wireOp",EDGE,"fcba4419-a2ee-464f-be9d-58f11bf3418b.sketch_text.stroke-163"),sQuery(id+"F2.wireOp",EDGE,"fcba4419-a2ee-464f-be9d-58f11bf3418b.sketch_text.stroke-164"),sQuery(id+"F2.wireOp",EDGE,"fcba4419-a2ee-464f-be9d-58f11bf3418b.sketch_text.stroke-165"),sQuery(id+"F2.wireOp",EDGE,"fcba4419-a2ee-464f-be9d-58f11bf3418b.sketch_text.stroke-166"),sQuery(id+"F2.wireOp",EDGE,"fcba4419-a2ee-464f-be9d-58f11bf3418b.sketch_text.stroke-167"),sQuery(id+"F2.wireOp",EDGE,"fcba4419-a2ee-464f-be9d-58f11bf3418b.sketch_text.stroke-168"),sQuery(id+"F2.wireOp",EDGE,"fcba4419-a2ee-464f-be9d-58f11bf3418b.sketch_text.stroke-169"),sQuery(id+"F2.wireOp",EDGE,"fcba4419-a2ee-464f-be9d-58f11bf3418b.sketch_text.stroke-170"),sQuery(id+"F2.wireOp",EDGE,"fcba4419-a2ee-464f-be9d-58f11bf3418b.sketch_text.stroke-171"),sQuery(id+"F2.wireOp",EDGE,"fcba4419-a2ee-464f-be9d-58f11bf3418b.sketch_text.stroke-172"),sQuery(id+"F2.wireOp",EDGE,"fcba4419-a2ee-464f-be9d-58f11bf3418b.sketch_text.stroke-173"),sQuery(id+"FHMxAyK4CFUKdhS_1.wireOp",EDGE,"1cb9c079-ea9b-4899-8069-e0e3048e911d.sketch_text.stroke-0"),sQuery(id+"FHMxAyK4CFUKdhS_1.wireOp",EDGE,"1cb9c079-ea9b-4899-8069-e0e3048e911d.sketch_text.stroke-1"),sQuery(id+"FHMxAyK4CFUKdhS_1.wireOp",EDGE,"1cb9c079-ea9b-4899-8069-e0e3048e911d.sketch_text.stroke-2"),sQuery(id+"FHMxAyK4CFUKdhS_1.wireOp",EDGE,"1cb9c079-ea9b-4899-8069-e0e3048e911d.sketch_text.stroke-3"),sQuery(id+"FHMxAyK4CFUKdhS_1.wireOp",EDGE,"1cb9c079-ea9b-4899-8069-e0e3048e911d.sketch_text.stroke-4"),sQuery(id+"FHMxAyK4CFUKdhS_1.wireOp",EDGE,"1cb9c079-ea9b-4899-8069-e0e3048e911d.sketch_text.stroke-5"),sQuery(id+"FHMxAyK4CFUKdhS_1.wireOp",EDGE,"1cb9c079-ea9b-4899-8069-e0e3048e911d.sketch_text.stroke-6"),sQuery(id+"FHMxAyK4CFUKdhS_1.wireOp",EDGE,"1cb9c079-ea9b-4899-8069-e0e3048e911d.sketch_text.stroke-7"),sQuery(id+"FHMxAyK4CFUKdhS_1.wireOp",EDGE,"1cb9c079-ea9b-4899-8069-e0e3048e911d.sketch_text.stroke-8"),sQuery(id+"FHMxAyK4CFUKdhS_1.wireOp",EDGE,"1cb9c079-ea9b-4899-8069-e0e3048e911d.sketch_text.stroke-9"),sQuery(id+"FHMxAyK4CFUKdhS_1.wireOp",EDGE,"1cb9c079-ea9b-4899-8069-e0e3048e911d.sketch_text.stroke-10"),sQuery(id+"FHMxAyK4CFUKdhS_1.wireOp",EDGE,"1cb9c079-ea9b-4899-8069-e0e3048e911d.sketch_text.stroke-11"),sQuery(id+"FHMxAyK4CFUKdhS_1.wireOp",EDGE,"1cb9c079-ea9b-4899-8069-e0e3048e911d.sketch_text.stroke-12"),sQuery(id+"FHMxAyK4CFUKdhS_1.wireOp",EDGE,"1cb9c079-ea9b-4899-8069-e0e3048e911d.sketch_text.stroke-13"),sQuery(id+"FHMxAyK4CFUKdhS_1.wireOp",EDGE,"1cb9c079-ea9b-4899-8069-e0e3048e911d.sketch_text.stroke-14"),sQuery(id+"FHMxAyK4CFUKdhS_1.wireOp",EDGE,"1cb9c079-ea9b-4899-8069-e0e3048e911d.sketch_text.stroke-15"),sQuery(id+"FHMxAyK4CFUKdhS_1.wireOp",EDGE,"1cb9c079-ea9b-4899-8069-e0e3048e911d.sketch_text.stroke-16"),sQuery(id+"FHMxAyK4CFUKdhS_1.wireOp",EDGE,"1cb9c079-ea9b-4899-8069-e0e3048e911d.sketch_text.stroke-17"),sQuery(id+"FHMxAyK4CFUKdhS_1.wireOp",EDGE,"1cb9c079-ea9b-4899-8069-e0e3048e911d.sketch_text.stroke-18"),sQuery(id+"FHMxAyK4CFUKdhS_1.wireOp",EDGE,"1cb9c079-ea9b-4899-8069-e0e3048e911d.sketch_text.stroke-19"),sQuery(id+"FHMxAyK4CFUKdhS_1.wireOp",EDGE,"1cb9c079-ea9b-4899-8069-e0e3048e911d.sketch_text.stroke-20"),sQuery(id+"FHMxAyK4CFUKdhS_1.wireOp",EDGE,"1cb9c079-ea9b-4899-8069-e0e3048e911d.sketch_text.stroke-21"),sQuery(id+"FHMxAyK4CFUKdhS_1.wireOp",EDGE,"1cb9c079-ea9b-4899-8069-e0e3048e911d.sketch_text.stroke-22"),sQuery(id+"FHMxAyK4CFUKdhS_1.wireOp",EDGE,"1cb9c079-ea9b-4899-8069-e0e3048e911d.sketch_text.stroke-23"),sQuery(id+"FHMxAyK4CFUKdhS_1.wireOp",EDGE,"1cb9c079-ea9b-4899-8069-e0e3048e911d.sketch_text.stroke-24"),sQuery(id+"FHMxAyK4CFUKdhS_1.wireOp",EDGE,"1cb9c079-ea9b-4899-8069-e0e3048e911d.sketch_text.stroke-25"),sQuery(id+"FHMxAyK4CFUKdhS_1.wireOp",EDGE,"1cb9c079-ea9b-4899-8069-e0e3048e911d.sketch_text.stroke-26"),sQuery(id+"FHMxAyK4CFUKdhS_1.wireOp",EDGE,"1cb9c079-ea9b-4899-8069-e0e3048e911d.sketch_text.stroke-27"),sQuery(id+"FHMxAyK4CFUKdhS_1.wireOp",EDGE,"1cb9c079-ea9b-4899-8069-e0e3048e911d.sketch_text.stroke-28"),sQuery(id+"FHMxAyK4CFUKdhS_1.wireOp",EDGE,"1cb9c079-ea9b-4899-8069-e0e3048e911d.sketch_text.stroke-29"),sQuery(id+"FHMxAyK4CFUKdhS_1.wireOp",EDGE,"1cb9c079-ea9b-4899-8069-e0e3048e911d.sketch_text.stroke-30"),sQuery(id+"FHMxAyK4CFUKdhS_1.wireOp",EDGE,"1cb9c079-ea9b-4899-8069-e0e3048e911d.sketch_text.stroke-31"),sQuery(id+"FHMxAyK4CFUKdhS_1.wireOp",EDGE,"1cb9c079-ea9b-4899-8069-e0e3048e911d.sketch_text.stroke-32"),sQuery(id+"FHMxAyK4CFUKdhS_1.wireOp",EDGE,"1cb9c079-ea9b-4899-8069-e0e3048e911d.sketch_text.stroke-33"),sQuery(id+"FHMxAyK4CFUKdhS_1.wireOp",EDGE,"1cb9c079-ea9b-4899-8069-e0e3048e911d.sketch_text.stroke-34"),sQuery(id+"FHMxAyK4CFUKdhS_1.wireOp",EDGE,"1cb9c079-ea9b-4899-8069-e0e3048e911d.sketch_text.stroke-35"),sQuery(id+"FHMxAyK4CFUKdhS_1.wireOp",EDGE,"1cb9c079-ea9b-4899-8069-e0e3048e911d.sketch_text.stroke-36"),sQuery(id+"FHMxAyK4CFUKdhS_1.wireOp",EDGE,"1cb9c079-ea9b-4899-8069-e0e3048e911d.sketch_text.stroke-37"),sQuery(id+"FHMxAyK4CFUKdhS_1.wireOp",EDGE,"1cb9c079-ea9b-4899-8069-e0e3048e911d.sketch_text.stroke-38"),sQuery(id+"FHMxAyK4CFUKdhS_1.wireOp",EDGE,"1cb9c079-ea9b-4899-8069-e0e3048e911d.sketch_text.stroke-39"),sQuery(id+"FHMxAyK4CFUKdhS_1.wireOp",EDGE,"1cb9c079-ea9b-4899-8069-e0e3048e911d.sketch_text.stroke-40"),sQuery(id+"FHMxAyK4CFUKdhS_1.wireOp",EDGE,"1cb9c079-ea9b-4899-8069-e0e3048e911d.sketch_text.stroke-41"),sQuery(id+"FHMxAyK4CFUKdhS_1.wireOp",EDGE,"1cb9c079-ea9b-4899-8069-e0e3048e911d.sketch_text.stroke-42"),sQuery(id+"FHMxAyK4CFUKdhS_1.wireOp",EDGE,"1cb9c079-ea9b-4899-8069-e0e3048e911d.sketch_text.stroke-43"),sQuery(id+"FHMxAyK4CFUKdhS_1.wireOp",EDGE,"1cb9c079-ea9b-4899-8069-e0e3048e911d.sketch_text.stroke-44"),sQuery(id+"FHMxAyK4CFUKdhS_1.wireOp",EDGE,"1cb9c079-ea9b-4899-8069-e0e3048e911d.sketch_text.stroke-45"),sQuery(id+"FHMxAyK4CFUKdhS_1.wireOp",EDGE,"1cb9c079-ea9b-4899-8069-e0e3048e911d.sketch_text.stroke-46"),sQuery(id+"FHMxAyK4CFUKdhS_1.wireOp",EDGE,"1cb9c079-ea9b-4899-8069-e0e3048e911d.sketch_text.stroke-47"),sQuery(id+"FHMxAyK4CFUKdhS_1.wireOp",EDGE,"1cb9c079-ea9b-4899-8069-e0e3048e911d.sketch_text.stroke-48"),sQuery(id+"FHMxAyK4CFUKdhS_1.wireOp",EDGE,"1cb9c079-ea9b-4899-8069-e0e3048e911d.sketch_text.stroke-49"),sQuery(id+"FHMxAyK4CFUKdhS_1.wireOp",EDGE,"1cb9c079-ea9b-4899-8069-e0e3048e911d.sketch_text.stroke-50"),sQuery(id+"FHMxAyK4CFUKdhS_1.wireOp",EDGE,"1cb9c079-ea9b-4899-8069-e0e3048e911d.sketch_text.stroke-51"),sQuery(id+"FHMxAyK4CFUKdhS_1.wireOp",EDGE,"1cb9c079-ea9b-4899-8069-e0e3048e911d.sketch_text.stroke-52"),sQuery(id+"FHMxAyK4CFUKdhS_1.wireOp",EDGE,"1cb9c079-ea9b-4899-8069-e0e3048e911d.sketch_text.stroke-53"),sQuery(id+"FHMxAyK4CFUKdhS_1.wireOp",EDGE,"1cb9c079-ea9b-4899-8069-e0e3048e911d.sketch_text.stroke-54"),sQuery(id+"FHMxAyK4CFUKdhS_1.wireOp",EDGE,"1cb9c079-ea9b-4899-8069-e0e3048e911d.sketch_text.stroke-55"),sQuery(id+"FHMxAyK4CFUKdhS_1.wireOp",EDGE,"1cb9c079-ea9b-4899-8069-e0e3048e911d.sketch_text.stroke-56"),sQuery(id+"FHMxAyK4CFUKdhS_1.wireOp",EDGE,"1cb9c079-ea9b-4899-8069-e0e3048e911d.sketch_text.stroke-57"),sQuery(id+"FHMxAyK4CFUKdhS_1.wireOp",EDGE,"1cb9c079-ea9b-4899-8069-e0e3048e911d.sketch_text.stroke-58"),sQuery(id+"FHMxAyK4CFUKdhS_1.wireOp",EDGE,"1cb9c079-ea9b-4899-8069-e0e3048e911d.sketch_text.stroke-59"),sQuery(id+"FHMxAyK4CFUKdhS_1.wireOp",EDGE,"1cb9c079-ea9b-4899-8069-e0e3048e911d.sketch_text.stroke-60"),sQuery(id+"FHMxAyK4CFUKdhS_1.wireOp",EDGE,"1cb9c079-ea9b-4899-8069-e0e3048e911d.sketch_text.stroke-61"),sQuery(id+"FHMxAyK4CFUKdhS_1.wireOp",EDGE,"1cb9c079-ea9b-4899-8069-e0e3048e911d.sketch_text.stroke-62"),sQuery(id+"FHMxAyK4CFUKdhS_1.wireOp",EDGE,"1cb9c079-ea9b-4899-8069-e0e3048e911d.sketch_text.stroke-71"),sQuery(id+"FHMxAyK4CFUKdhS_1.wireOp",EDGE,"1cb9c079-ea9b-4899-8069-e0e3048e911d.sketch_text.stroke-72"),sQuery(id+"FHMxAyK4CFUKdhS_1.wireOp",EDGE,"1cb9c079-ea9b-4899-8069-e0e3048e911d.sketch_text.stroke-73"),sQuery(id+"FHMxAyK4CFUKdhS_1.wireOp",EDGE,"1cb9c079-ea9b-4899-8069-e0e3048e911d.sketch_text.stroke-74"),sQuery(id+"FHMxAyK4CFUKdhS_1.wireOp",EDGE,"1cb9c079-ea9b-4899-8069-e0e3048e911d.sketch_text.stroke-75"),sQuery(id+"FHMxAyK4CFUKdhS_1.wireOp",EDGE,"1cb9c079-ea9b-4899-8069-e0e3048e911d.sketch_text.stroke-76"),sQuery(id+"FHMxAyK4CFUKdhS_1.wireOp",EDGE,"1cb9c079-ea9b-4899-8069-e0e3048e911d.sketch_text.stroke-77"),sQuery(id+"FHMxAyK4CFUKdhS_1.wireOp",EDGE,"1cb9c079-ea9b-4899-8069-e0e3048e911d.sketch_text.stroke-78"),sQuery(id+"FHMxAyK4CFUKdhS_1.wireOp",EDGE,"1cb9c079-ea9b-4899-8069-e0e3048e911d.sketch_text.stroke-79"),sQuery(id+"FHMxAyK4CFUKdhS_1.wireOp",EDGE,"1cb9c079-ea9b-4899-8069-e0e3048e911d.sketch_text.stroke-80"),sQuery(id+"FHMxAyK4CFUKdhS_1.wireOp",EDGE,"1cb9c079-ea9b-4899-8069-e0e3048e911d.sketch_text.stroke-81"),sQuery(id+"FHMxAyK4CFUKdhS_1.wireOp",EDGE,"1cb9c079-ea9b-4899-8069-e0e3048e911d.sketch_text.stroke-82"),sQuery(id+"FHMxAyK4CFUKdhS_1.wireOp",EDGE,"1cb9c079-ea9b-4899-8069-e0e3048e911d.sketch_text.stroke-83"),sQuery(id+"FHMxAyK4CFUKdhS_1.wireOp",EDGE,"1cb9c079-ea9b-4899-8069-e0e3048e911d.sketch_text.stroke-84"),sQuery(id+"FHMxAyK4CFUKdhS_1.wireOp",EDGE,"1cb9c079-ea9b-4899-8069-e0e3048e911d.sketch_text.stroke-85"),sQuery(id+"FHMxAyK4CFUKdhS_1.wireOp",EDGE,"1cb9c079-ea9b-4899-8069-e0e3048e911d.sketch_text.stroke-86"),sQuery(id+"FHMxAyK4CFUKdhS_1.wireOp",EDGE,"1cb9c079-ea9b-4899-8069-e0e3048e911d.sketch_text.stroke-87"),sQuery(id+"FHMxAyK4CFUKdhS_1.wireOp",EDGE,"1cb9c079-ea9b-4899-8069-e0e3048e911d.sketch_text.stroke-88"),sQuery(id+"FHMxAyK4CFUKdhS_1.wireOp",EDGE,"1cb9c079-ea9b-4899-8069-e0e3048e911d.sketch_text.stroke-89"),sQuery(id+"FHMxAyK4CFUKdhS_1.wireOp",EDGE,"1cb9c079-ea9b-4899-8069-e0e3048e911d.sketch_text.stroke-90"),sQuery(id+"FHMxAyK4CFUKdhS_1.wireOp",EDGE,"1cb9c079-ea9b-4899-8069-e0e3048e911d.sketch_text.stroke-91"),sQuery(id+"FHMxAyK4CFUKdhS_1.wireOp",EDGE,"1cb9c079-ea9b-4899-8069-e0e3048e911d.sketch_text.stroke-92"),sQuery(id+"FHMxAyK4CFUKdhS_1.wireOp",EDGE,"1cb9c079-ea9b-4899-8069-e0e3048e911d.sketch_text.stroke-93"),sQuery(id+"FHMxAyK4CFUKdhS_1.wireOp",EDGE,"1cb9c079-ea9b-4899-8069-e0e3048e911d.sketch_text.stroke-94"),sQuery(id+"FHMxAyK4CFUKdhS_1.wireOp",EDGE,"1cb9c079-ea9b-4899-8069-e0e3048e911d.sketch_text.stroke-95"),sQuery(id+"FHMxAyK4CFUKdhS_1.wireOp",EDGE,"1cb9c079-ea9b-4899-8069-e0e3048e911d.sketch_text.stroke-96"),sQuery(id+"FHMxAyK4CFUKdhS_1.wireOp",EDGE,"1cb9c079-ea9b-4899-8069-e0e3048e911d.sketch_text.stroke-97"),sQuery(id+"FHMxAyK4CFUKdhS_1.wireOp",EDGE,"1cb9c079-ea9b-4899-8069-e0e3048e911d.sketch_text.stroke-103"),sQuery(id+"FHMxAyK4CFUKdhS_1.wireOp",EDGE,"1cb9c079-ea9b-4899-8069-e0e3048e911d.sketch_text.stroke-104"),sQuery(id+"FHMxAyK4CFUKdhS_1.wireOp",EDGE,"1cb9c079-ea9b-4899-8069-e0e3048e911d.sketch_text.stroke-105"),sQuery(id+"FHMxAyK4CFUKdhS_1.wireOp",EDGE,"1cb9c079-ea9b-4899-8069-e0e3048e911d.sketch_text.stroke-106"),sQuery(id+"FHMxAyK4CFUKdhS_1.wireOp",EDGE,"1cb9c079-ea9b-4899-8069-e0e3048e911d.sketch_text.stroke-107"),sQuery(id+"FHMxAyK4CFUKdhS_1.wireOp",EDGE,"1cb9c079-ea9b-4899-8069-e0e3048e911d.sketch_text.stroke-108"),sQuery(id+"FHMxAyK4CFUKdhS_1.wireOp",EDGE,"1cb9c079-ea9b-4899-8069-e0e3048e911d.sketch_text.stroke-109"),sQuery(id+"FHMxAyK4CFUKdhS_1.wireOp",EDGE,"1cb9c079-ea9b-4899-8069-e0e3048e911d.sketch_text.stroke-110"),sQuery(id+"FHMxAyK4CFUKdhS_1.wireOp",EDGE,"1cb9c079-ea9b-4899-8069-e0e3048e911d.sketch_text.stroke-111"),sQuery(id+"FHMxAyK4CFUKdhS_1.wireOp",EDGE,"1cb9c079-ea9b-4899-8069-e0e3048e911d.sketch_text.stroke-112"),sQuery(id+"FHMxAyK4CFUKdhS_1.wireOp",EDGE,"1cb9c079-ea9b-4899-8069-e0e3048e911d.sketch_text.stroke-113"),sQuery(id+"FHMxAyK4CFUKdhS_1.wireOp",EDGE,"1cb9c079-ea9b-4899-8069-e0e3048e911d.sketch_text.stroke-114"),sQuery(id+"FHMxAyK4CFUKdhS_1.wireOp",EDGE,"1cb9c079-ea9b-4899-8069-e0e3048e911d.sketch_text.stroke-115"),sQuery(id+"FHMxAyK4CFUKdhS_1.wireOp",EDGE,"1cb9c079-ea9b-4899-8069-e0e3048e911d.sketch_text.stroke-116"),sQuery(id+"FHMxAyK4CFUKdhS_1.wireOp",EDGE,"1cb9c079-ea9b-4899-8069-e0e3048e911d.sketch_text.stroke-117"),sQuery(id+"FHMxAyK4CFUKdhS_1.wireOp",EDGE,"1cb9c079-ea9b-4899-8069-e0e3048e911d.sketch_text.stroke-118"),sQuery(id+"FHMxAyK4CFUKdhS_1.wireOp",EDGE,"1cb9c079-ea9b-4899-8069-e0e3048e911d.sketch_text.stroke-119"),sQuery(id+"FHMxAyK4CFUKdhS_1.wireOp",EDGE,"1cb9c079-ea9b-4899-8069-e0e3048e911d.sketch_text.stroke-120"),sQuery(id+"FHMxAyK4CFUKdhS_1.wireOp",EDGE,"1cb9c079-ea9b-4899-8069-e0e3048e911d.sketch_text.stroke-121"),sQuery(id+"FHMxAyK4CFUKdhS_1.wireOp",EDGE,"1cb9c079-ea9b-4899-8069-e0e3048e911d.sketch_text.stroke-122"),sQuery(id+"FHMxAyK4CFUKdhS_1.wireOp",EDGE,"1cb9c079-ea9b-4899-8069-e0e3048e911d.sketch_text.stroke-123"),sQuery(id+"FHMxAyK4CFUKdhS_1.wireOp",EDGE,"1cb9c079-ea9b-4899-8069-e0e3048e911d.sketch_text.stroke-124"),sQuery(id+"FHMxAyK4CFUKdhS_1.wireOp",EDGE,"1cb9c079-ea9b-4899-8069-e0e3048e911d.sketch_text.stroke-125"),sQuery(id+"FHMxAyK4CFUKdhS_1.wireOp",EDGE,"1cb9c079-ea9b-4899-8069-e0e3048e911d.sketch_text.stroke-126"),sQuery(id+"FHMxAyK4CFUKdhS_1.wireOp",EDGE,"1cb9c079-ea9b-4899-8069-e0e3048e911d.sketch_text.stroke-127"),sQuery(id+"FHMxAyK4CFUKdhS_1.wireOp",EDGE,"1cb9c079-ea9b-4899-8069-e0e3048e911d.sketch_text.stroke-128"),sQuery(id+"FHMxAyK4CFUKdhS_1.wireOp",EDGE,"1cb9c079-ea9b-4899-8069-e0e3048e911d.sketch_text.stroke-129"),sQuery(id+"FHMxAyK4CFUKdhS_1.wireOp",EDGE,"1cb9c079-ea9b-4899-8069-e0e3048e911d.sketch_text.stroke-130"),sQuery(id+"FHMxAyK4CFUKdhS_1.wireOp",EDGE,"1cb9c079-ea9b-4899-8069-e0e3048e911d.sketch_text.stroke-131"),sQuery(id+"FHMxAyK4CFUKdhS_1.wireOp",EDGE,"1cb9c079-ea9b-4899-8069-e0e3048e911d.sketch_text.stroke-132"),sQuery(id+"FHMxAyK4CFUKdhS_1.wireOp",EDGE,"1cb9c079-ea9b-4899-8069-e0e3048e911d.sketch_text.stroke-133"),sQuery(id+"FHMxAyK4CFUKdhS_1.wireOp",EDGE,"1cb9c079-ea9b-4899-8069-e0e3048e911d.sketch_text.stroke-134"),sQuery(id+"FHMxAyK4CFUKdhS_1.wireOp",EDGE,"1cb9c079-ea9b-4899-8069-e0e3048e911d.sketch_text.stroke-135"),sQuery(id+"FHMxAyK4CFUKdhS_1.wireOp",EDGE,"1cb9c079-ea9b-4899-8069-e0e3048e911d.sketch_text.stroke-136"),sQuery(id+"FHMxAyK4CFUKdhS_1.wireOp",EDGE,"1cb9c079-ea9b-4899-8069-e0e3048e911d.sketch_text.stroke-137"),sQuery(id+"FHMxAyK4CFUKdhS_1.wireOp",EDGE,"1cb9c079-ea9b-4899-8069-e0e3048e911d.sketch_text.stroke-138"),sQuery(id+"FHMxAyK4CFUKdhS_1.wireOp",EDGE,"1cb9c079-ea9b-4899-8069-e0e3048e911d.sketch_text.stroke-139"),sQuery(id+"FHMxAyK4CFUKdhS_1.wireOp",EDGE,"1cb9c079-ea9b-4899-8069-e0e3048e911d.sketch_text.stroke-140"),sQuery(id+"FHMxAyK4CFUKdhS_1.wireOp",EDGE,"1cb9c079-ea9b-4899-8069-e0e3048e911d.sketch_text.stroke-141"),sQuery(id+"FHMxAyK4CFUKdhS_1.wireOp",EDGE,"1cb9c079-ea9b-4899-8069-e0e3048e911d.sketch_text.stroke-142"),sQuery(id+"FHMxAyK4CFUKdhS_1.wireOp",EDGE,"1cb9c079-ea9b-4899-8069-e0e3048e911d.sketch_text.stroke-143"),sQuery(id+"FHMxAyK4CFUKdhS_1.wireOp",EDGE,"1cb9c079-ea9b-4899-8069-e0e3048e911d.sketch_text.stroke-144"),sQuery(id+"FHMxAyK4CFUKdhS_1.wireOp",EDGE,"1cb9c079-ea9b-4899-8069-e0e3048e911d.sketch_text.stroke-145"),sQuery(id+"FHMxAyK4CFUKdhS_1.wireOp",EDGE,"1cb9c079-ea9b-4899-8069-e0e3048e911d.sketch_text.stroke-146"),sQuery(id+"FHMxAyK4CFUKdhS_1.wireOp",EDGE,"1cb9c079-ea9b-4899-8069-e0e3048e911d.sketch_text.stroke-147"),sQuery(id+"FHMxAyK4CFUKdhS_1.wireOp",EDGE,"1cb9c079-ea9b-4899-8069-e0e3048e911d.sketch_text.stroke-148"),sQuery(id+"FHMxAyK4CFUKdhS_1.wireOp",EDGE,"1cb9c079-ea9b-4899-8069-e0e3048e911d.sketch_text.stroke-149"),sQuery(id+"FHMxAyK4CFUKdhS_1.wireOp",EDGE,"1cb9c079-ea9b-4899-8069-e0e3048e911d.sketch_text.stroke-150"),sQuery(id+"FHMxAyK4CFUKdhS_1.wireOp",EDGE,"1cb9c079-ea9b-4899-8069-e0e3048e911d.sketch_text.stroke-151"),sQuery(id+"FHMxAyK4CFUKdhS_1.wireOp",EDGE,"1cb9c079-ea9b-4899-8069-e0e3048e911d.sketch_text.stroke-152"),sQuery(id+"FHMxAyK4CFUKdhS_1.wireOp",EDGE,"1cb9c079-ea9b-4899-8069-e0e3048e911d.sketch_text.stroke-153"),sQuery(id+"FHMxAyK4CFUKdhS_1.wireOp",EDGE,"1cb9c079-ea9b-4899-8069-e0e3048e911d.sketch_text.stroke-159"),sQuery(id+"FHMxAyK4CFUKdhS_1.wireOp",EDGE,"1cb9c079-ea9b-4899-8069-e0e3048e911d.sketch_text.stroke-160"),sQuery(id+"FHMxAyK4CFUKdhS_1.wireOp",EDGE,"1cb9c079-ea9b-4899-8069-e0e3048e911d.sketch_text.stroke-161"),sQuery(id+"FHMxAyK4CFUKdhS_1.wireOp",EDGE,"1cb9c079-ea9b-4899-8069-e0e3048e911d.sketch_text.stroke-162"),sQuery(id+"FHMxAyK4CFUKdhS_1.wireOp",EDGE,"1cb9c079-ea9b-4899-8069-e0e3048e911d.sketch_text.stroke-163"),sQuery(id+"FHMxAyK4CFUKdhS_1.wireOp",EDGE,"1cb9c079-ea9b-4899-8069-e0e3048e911d.sketch_text.stroke-164"),sQuery(id+"FHMxAyK4CFUKdhS_1.wireOp",EDGE,"1cb9c079-ea9b-4899-8069-e0e3048e911d.sketch_text.stroke-165"),sQuery(id+"FHMxAyK4CFUKdhS_1.wireOp",EDGE,"1cb9c079-ea9b-4899-8069-e0e3048e911d.sketch_text.stroke-166"),sQuery(id+"FHMxAyK4CFUKdhS_1.wireOp",EDGE,"1cb9c079-ea9b-4899-8069-e0e3048e911d.sketch_text.stroke-167"),sQuery(id+"FHMxAyK4CFUKdhS_1.wireOp",EDGE,"1cb9c079-ea9b-4899-8069-e0e3048e911d.sketch_text.stroke-168"),sQuery(id+"FHMxAyK4CFUKdhS_1.wireOp",EDGE,"1cb9c079-ea9b-4899-8069-e0e3048e911d.sketch_text.stroke-169"),sQuery(id+"FHMxAyK4CFUKdhS_1.wireOp",EDGE,"1cb9c079-ea9b-4899-8069-e0e3048e911d.sketch_text.stroke-170"),sQuery(id+"FHMxAyK4CFUKdhS_1.wireOp",EDGE,"1cb9c079-ea9b-4899-8069-e0e3048e911d.sketch_text.stroke-171"),sQuery(id+"FHMxAyK4CFUKdhS_1.wireOp",EDGE,"1cb9c079-ea9b-4899-8069-e0e3048e911d.sketch_text.stroke-172"),sQuery(id+"FHMxAyK4CFUKdhS_1.wireOp",EDGE,"1cb9c079-ea9b-4899-8069-e0e3048e911d.sketch_text.stroke-173"),sQuery(id+"FHMxAyK4CFUKdhS_1.wireOp",EDGE,"1cb9c079-ea9b-4899-8069-e0e3048e911d.sketch_text.stroke-174"),sQuery(id+"FHMxAyK4CFUKdhS_1.wireOp",EDGE,"1cb9c079-ea9b-4899-8069-e0e3048e911d.sketch_text.stroke-175"),sQuery(id+"FHMxAyK4CFUKdhS_1.wireOp",EDGE,"1cb9c079-ea9b-4899-8069-e0e3048e911d.sketch_text.stroke-176"),sQuery(id+"FHMxAyK4CFUKdhS_1.wireOp",EDGE,"1cb9c079-ea9b-4899-8069-e0e3048e911d.sketch_text.stroke-177"),sQuery(id+"FHMxAyK4CFUKdhS_1.wireOp",EDGE,"1cb9c079-ea9b-4899-8069-e0e3048e911d.sketch_text.stroke-178"),sQuery(id+"FHMxAyK4CFUKdhS_1.wireOp",EDGE,"1cb9c079-ea9b-4899-8069-e0e3048e911d.sketch_text.stroke-179"),sQuery(id+"FHMxAyK4CFUKdhS_1.wireOp",EDGE,"1cb9c079-ea9b-4899-8069-e0e3048e911d.sketch_text.stroke-180"),subQ0,subQ2])],"isStart":true}),makeQuery(id+"F4.opExtrude","SWEPT_FACE",FACE,{"disambiguationData":[OSD([subQ2])]})])],"derivedFrom":makeQuery(id+"F4.opExtrude","CAP_EDGE",EDGE,{"disambiguationData":[OSD([subQ0])],"isStart":true})});}
            var Q4;
            {var subQ0=sQuery(id+"F0.wireOp",EDGE,"E0.top");var subQ1=sQuery(id+"F0.wireOp",EDGE,"E0.bottom");var subQ2=sQuery(id+"F3.wireOp",EDGE,"8007402e-1a4e-4a06-85a5-2af08e553504");Q4=makeQuery(id+"F4.boolean.opBoolean","SPLIT",EDGE,{"disambiguationData":[TD([makeQuery(id+"F1.opExtrude","CAP_FACE",FACE,{"disambiguationData":[OSD([subQ1,subQ0,sQuery(id+"F0.wireOp",EDGE,"E0.left"),sQuery(id+"F0.wireOp",EDGE,"E0.right")])],"isStart":false}),makeQuery(id+"F1.opExtrude","SWEPT_FACE",FACE,{"disambiguationData":[OSD([subQ0])]}),makeQuery(id+"F4.opExtrude","SWEPT_FACE",FACE,{"disambiguationData":[OSD([subQ2])]}),makeQuery(id+"F4.opExtrude","CAP_FACE",FACE,{"disambiguationData":[OSD([subQ1,sQuery(id+"F2.wireOp",EDGE,"fcba4419-a2ee-464f-be9d-58f11bf3418b.sketch_text.stroke-0"),sQuery(id+"F2.wireOp",EDGE,"fcba4419-a2ee-464f-be9d-58f11bf3418b.sketch_text.stroke-1"),sQuery(id+"F2.wireOp",EDGE,"fcba4419-a2ee-464f-be9d-58f11bf3418b.sketch_text.stroke-2"),sQuery(id+"F2.wireOp",EDGE,"fcba4419-a2ee-464f-be9d-58f11bf3418b.sketch_text.stroke-3"),sQuery(id+"F2.wireOp",EDGE,"fcba4419-a2ee-464f-be9d-58f11bf3418b.sketch_text.stroke-4"),sQuery(id+"F2.wireOp",EDGE,"fcba4419-a2ee-464f-be9d-58f11bf3418b.sketch_text.stroke-5"),sQuery(id+"F2.wireOp",EDGE,"fcba4419-a2ee-464f-be9d-58f11bf3418b.sketch_text.stroke-6"),sQuery(id+"F2.wireOp",EDGE,"fcba4419-a2ee-464f-be9d-58f11bf3418b.sketch_text.stroke-7"),sQuery(id+"F2.wireOp",EDGE,"fcba4419-a2ee-464f-be9d-58f11bf3418b.sketch_text.stroke-8"),sQuery(id+"F2.wireOp",EDGE,"fcba4419-a2ee-464f-be9d-58f11bf3418b.sketch_text.stroke-9"),sQuery(id+"F2.wireOp",EDGE,"fcba4419-a2ee-464f-be9d-58f11bf3418b.sketch_text.stroke-10"),sQuery(id+"F2.wireOp",EDGE,"fcba4419-a2ee-464f-be9d-58f11bf3418b.sketch_text.stroke-11"),sQuery(id+"F2.wireOp",EDGE,"fcba4419-a2ee-464f-be9d-58f11bf3418b.sketch_text.stroke-12"),sQuery(id+"F2.wireOp",EDGE,"fcba4419-a2ee-464f-be9d-58f11bf3418b.sketch_text.stroke-13"),sQuery(id+"F2.wireOp",EDGE,"fcba4419-a2ee-464f-be9d-58f11bf3418b.sketch_text.stroke-14"),sQuery(id+"F2.wireOp",EDGE,"fcba4419-a2ee-464f-be9d-58f11bf3418b.sketch_text.stroke-15"),sQuery(id+"F2.wireOp",EDGE,"fcba4419-a2ee-464f-be9d-58f11bf3418b.sketch_text.stroke-16"),sQuery(id+"F2.wireOp",EDGE,"fcba4419-a2ee-464f-be9d-58f11bf3418b.sketch_text.stroke-17"),sQuery(id+"F2.wireOp",EDGE,"fcba4419-a2ee-464f-be9d-58f11bf3418b.sketch_text.stroke-18"),sQuery(id+"F2.wireOp",EDGE,"fcba4419-a2ee-464f-be9d-58f11bf3418b.sketch_text.stroke-19"),sQuery(id+"F2.wireOp",EDGE,"fcba4419-a2ee-464f-be9d-58f11bf3418b.sketch_text.stroke-20"),sQuery(id+"F2.wireOp",EDGE,"fcba4419-a2ee-464f-be9d-58f11bf3418b.sketch_text.stroke-21"),sQuery(id+"F2.wireOp",EDGE,"fcba4419-a2ee-464f-be9d-58f11bf3418b.sketch_text.stroke-22"),sQuery(id+"F2.wireOp",EDGE,"fcba4419-a2ee-464f-be9d-58f11bf3418b.sketch_text.stroke-23"),sQuery(id+"F2.wireOp",EDGE,"fcba4419-a2ee-464f-be9d-58f11bf3418b.sketch_text.stroke-24"),sQuery(id+"F2.wireOp",EDGE,"fcba4419-a2ee-464f-be9d-58f11bf3418b.sketch_text.stroke-25"),sQuery(id+"F2.wireOp",EDGE,"fcba4419-a2ee-464f-be9d-58f11bf3418b.sketch_text.stroke-26"),sQuery(id+"F2.wireOp",EDGE,"fcba4419-a2ee-464f-be9d-58f11bf3418b.sketch_text.stroke-27"),sQuery(id+"F2.wireOp",EDGE,"fcba4419-a2ee-464f-be9d-58f11bf3418b.sketch_text.stroke-28"),sQuery(id+"F2.wireOp",EDGE,"fcba4419-a2ee-464f-be9d-58f11bf3418b.sketch_text.stroke-29"),sQuery(id+"F2.wireOp",EDGE,"fcba4419-a2ee-464f-be9d-58f11bf3418b.sketch_text.stroke-30"),sQuery(id+"F2.wireOp",EDGE,"fcba4419-a2ee-464f-be9d-58f11bf3418b.sketch_text.stroke-31"),sQuery(id+"F2.wireOp",EDGE,"fcba4419-a2ee-464f-be9d-58f11bf3418b.sketch_text.stroke-32"),sQuery(id+"F2.wireOp",EDGE,"fcba4419-a2ee-464f-be9d-58f11bf3418b.sketch_text.stroke-33"),sQuery(id+"F2.wireOp",EDGE,"fcba4419-a2ee-464f-be9d-58f11bf3418b.sketch_text.stroke-34"),sQuery(id+"F2.wireOp",EDGE,"fcba4419-a2ee-464f-be9d-58f11bf3418b.sketch_text.stroke-35"),sQuery(id+"F2.wireOp",EDGE,"fcba4419-a2ee-464f-be9d-58f11bf3418b.sketch_text.stroke-36"),sQuery(id+"F2.wireOp",EDGE,"fcba4419-a2ee-464f-be9d-58f11bf3418b.sketch_text.stroke-37"),sQuery(id+"F2.wireOp",EDGE,"fcba4419-a2ee-464f-be9d-58f11bf3418b.sketch_text.stroke-38"),sQuery(id+"F2.wireOp",EDGE,"fcba4419-a2ee-464f-be9d-58f11bf3418b.sketch_text.stroke-39"),sQuery(id+"F2.wireOp",EDGE,"fcba4419-a2ee-464f-be9d-58f11bf3418b.sketch_text.stroke-40"),sQuery(id+"F2.wireOp",EDGE,"fcba4419-a2ee-464f-be9d-58f11bf3418b.sketch_text.stroke-41"),sQuery(id+"F2.wireOp",EDGE,"fcba4419-a2ee-464f-be9d-58f11bf3418b.sketch_text.stroke-42"),sQuery(id+"F2.wireOp",EDGE,"fcba4419-a2ee-464f-be9d-58f11bf3418b.sketch_text.stroke-43"),sQuery(id+"F2.wireOp",EDGE,"fcba4419-a2ee-464f-be9d-58f11bf3418b.sketch_text.stroke-44"),sQuery(id+"F2.wireOp",EDGE,"fcba4419-a2ee-464f-be9d-58f11bf3418b.sketch_text.stroke-45"),sQuery(id+"F2.wireOp",EDGE,"fcba4419-a2ee-464f-be9d-58f11bf3418b.sketch_text.stroke-46"),sQuery(id+"F2.wireOp",EDGE,"fcba4419-a2ee-464f-be9d-58f11bf3418b.sketch_text.stroke-47"),sQuery(id+"F2.wireOp",EDGE,"fcba4419-a2ee-464f-be9d-58f11bf3418b.sketch_text.stroke-48"),sQuery(id+"F2.wireOp",EDGE,"fcba4419-a2ee-464f-be9d-58f11bf3418b.sketch_text.stroke-49"),sQuery(id+"F2.wireOp",EDGE,"fcba4419-a2ee-464f-be9d-58f11bf3418b.sketch_text.stroke-50"),sQuery(id+"F2.wireOp",EDGE,"fcba4419-a2ee-464f-be9d-58f11bf3418b.sketch_text.stroke-51"),sQuery(id+"F2.wireOp",EDGE,"fcba4419-a2ee-464f-be9d-58f11bf3418b.sketch_text.stroke-52"),sQuery(id+"F2.wireOp",EDGE,"fcba4419-a2ee-464f-be9d-58f11bf3418b.sketch_text.stroke-53"),sQuery(id+"F2.wireOp",EDGE,"fcba4419-a2ee-464f-be9d-58f11bf3418b.sketch_text.stroke-54"),sQuery(id+"F2.wireOp",EDGE,"fcba4419-a2ee-464f-be9d-58f11bf3418b.sketch_text.stroke-55"),sQuery(id+"F2.wireOp",EDGE,"fcba4419-a2ee-464f-be9d-58f11bf3418b.sketch_text.stroke-56"),sQuery(id+"F2.wireOp",EDGE,"fcba4419-a2ee-464f-be9d-58f11bf3418b.sketch_text.stroke-57"),sQuery(id+"F2.wireOp",EDGE,"fcba4419-a2ee-464f-be9d-58f11bf3418b.sketch_text.stroke-58"),sQuery(id+"F2.wireOp",EDGE,"fcba4419-a2ee-464f-be9d-58f11bf3418b.sketch_text.stroke-59"),sQuery(id+"F2.wireOp",EDGE,"fcba4419-a2ee-464f-be9d-58f11bf3418b.sketch_text.stroke-60"),sQuery(id+"F2.wireOp",EDGE,"fcba4419-a2ee-464f-be9d-58f11bf3418b.sketch_text.stroke-61"),sQuery(id+"F2.wireOp",EDGE,"fcba4419-a2ee-464f-be9d-58f11bf3418b.sketch_text.stroke-62"),sQuery(id+"F2.wireOp",EDGE,"fcba4419-a2ee-464f-be9d-58f11bf3418b.sketch_text.stroke-63"),sQuery(id+"F2.wireOp",EDGE,"fcba4419-a2ee-464f-be9d-58f11bf3418b.sketch_text.stroke-64"),sQuery(id+"F2.wireOp",EDGE,"fcba4419-a2ee-464f-be9d-58f11bf3418b.sketch_text.stroke-65"),sQuery(id+"F2.wireOp",EDGE,"fcba4419-a2ee-464f-be9d-58f11bf3418b.sketch_text.stroke-66"),sQuery(id+"F2.wireOp",EDGE,"fcba4419-a2ee-464f-be9d-58f11bf3418b.sketch_text.stroke-67"),sQuery(id+"F2.wireOp",EDGE,"fcba4419-a2ee-464f-be9d-58f11bf3418b.sketch_text.stroke-68"),sQuery(id+"F2.wireOp",EDGE,"fcba4419-a2ee-464f-be9d-58f11bf3418b.sketch_text.stroke-69"),sQuery(id+"F2.wireOp",EDGE,"fcba4419-a2ee-464f-be9d-58f11bf3418b.sketch_text.stroke-70"),sQuery(id+"F2.wireOp",EDGE,"fcba4419-a2ee-464f-be9d-58f11bf3418b.sketch_text.stroke-71"),sQuery(id+"F2.wireOp",EDGE,"fcba4419-a2ee-464f-be9d-58f11bf3418b.sketch_text.stroke-72"),sQuery(id+"F2.wireOp",EDGE,"fcba4419-a2ee-464f-be9d-58f11bf3418b.sketch_text.stroke-73"),sQuery(id+"F2.wireOp",EDGE,"fcba4419-a2ee-464f-be9d-58f11bf3418b.sketch_text.stroke-74"),sQuery(id+"F2.wireOp",EDGE,"fcba4419-a2ee-464f-be9d-58f11bf3418b.sketch_text.stroke-75"),sQuery(id+"F2.wireOp",EDGE,"fcba4419-a2ee-464f-be9d-58f11bf3418b.sketch_text.stroke-76"),sQuery(id+"F2.wireOp",EDGE,"fcba4419-a2ee-464f-be9d-58f11bf3418b.sketch_text.stroke-77"),sQuery(id+"F2.wireOp",EDGE,"fcba4419-a2ee-464f-be9d-58f11bf3418b.sketch_text.stroke-78"),sQuery(id+"F2.wireOp",EDGE,"fcba4419-a2ee-464f-be9d-58f11bf3418b.sketch_text.stroke-79"),sQuery(id+"F2.wireOp",EDGE,"fcba4419-a2ee-464f-be9d-58f11bf3418b.sketch_text.stroke-80"),sQuery(id+"F2.wireOp",EDGE,"fcba4419-a2ee-464f-be9d-58f11bf3418b.sketch_text.stroke-81"),sQuery(id+"F2.wireOp",EDGE,"fcba4419-a2ee-464f-be9d-58f11bf3418b.sketch_text.stroke-82"),sQuery(id+"F2.wireOp",EDGE,"fcba4419-a2ee-464f-be9d-58f11bf3418b.sketch_text.stroke-83"),sQuery(id+"F2.wireOp",EDGE,"fcba4419-a2ee-464f-be9d-58f11bf3418b.sketch_text.stroke-84"),sQuery(id+"F2.wireOp",EDGE,"fcba4419-a2ee-464f-be9d-58f11bf3418b.sketch_text.stroke-85"),sQuery(id+"F2.wireOp",EDGE,"fcba4419-a2ee-464f-be9d-58f11bf3418b.sketch_text.stroke-86"),sQuery(id+"F2.wireOp",EDGE,"fcba4419-a2ee-464f-be9d-58f11bf3418b.sketch_text.stroke-87"),sQuery(id+"F2.wireOp",EDGE,"fcba4419-a2ee-464f-be9d-58f11bf3418b.sketch_text.stroke-88"),sQuery(id+"F2.wireOp",EDGE,"fcba4419-a2ee-464f-be9d-58f11bf3418b.sketch_text.stroke-89"),sQuery(id+"F2.wireOp",EDGE,"fcba4419-a2ee-464f-be9d-58f11bf3418b.sketch_text.stroke-90"),sQuery(id+"F2.wireOp",EDGE,"fcba4419-a2ee-464f-be9d-58f11bf3418b.sketch_text.stroke-91"),sQuery(id+"F2.wireOp",EDGE,"fcba4419-a2ee-464f-be9d-58f11bf3418b.sketch_text.stroke-92"),sQuery(id+"F2.wireOp",EDGE,"fcba4419-a2ee-464f-be9d-58f11bf3418b.sketch_text.stroke-93"),sQuery(id+"F2.wireOp",EDGE,"fcba4419-a2ee-464f-be9d-58f11bf3418b.sketch_text.stroke-94"),sQuery(id+"F2.wireOp",EDGE,"fcba4419-a2ee-464f-be9d-58f11bf3418b.sketch_text.stroke-95"),sQuery(id+"F2.wireOp",EDGE,"fcba4419-a2ee-464f-be9d-58f11bf3418b.sketch_text.stroke-96"),sQuery(id+"F2.wireOp",EDGE,"fcba4419-a2ee-464f-be9d-58f11bf3418b.sketch_text.stroke-97"),sQuery(id+"F2.wireOp",EDGE,"fcba4419-a2ee-464f-be9d-58f11bf3418b.sketch_text.stroke-98"),sQuery(id+"F2.wireOp",EDGE,"fcba4419-a2ee-464f-be9d-58f11bf3418b.sketch_text.stroke-99"),sQuery(id+"F2.wireOp",EDGE,"fcba4419-a2ee-464f-be9d-58f11bf3418b.sketch_text.stroke-100"),sQuery(id+"F2.wireOp",EDGE,"fcba4419-a2ee-464f-be9d-58f11bf3418b.sketch_text.stroke-101"),sQuery(id+"F2.wireOp",EDGE,"fcba4419-a2ee-464f-be9d-58f11bf3418b.sketch_text.stroke-102"),sQuery(id+"F2.wireOp",EDGE,"fcba4419-a2ee-464f-be9d-58f11bf3418b.sketch_text.stroke-103"),sQuery(id+"F2.wireOp",EDGE,"fcba4419-a2ee-464f-be9d-58f11bf3418b.sketch_text.stroke-104"),sQuery(id+"F2.wireOp",EDGE,"fcba4419-a2ee-464f-be9d-58f11bf3418b.sketch_text.stroke-105"),sQuery(id+"F2.wireOp",EDGE,"fcba4419-a2ee-464f-be9d-58f11bf3418b.sketch_text.stroke-106"),sQuery(id+"F2.wireOp",EDGE,"fcba4419-a2ee-464f-be9d-58f11bf3418b.sketch_text.stroke-107"),sQuery(id+"F2.wireOp",EDGE,"fcba4419-a2ee-464f-be9d-58f11bf3418b.sketch_text.stroke-108"),sQuery(id+"F2.wireOp",EDGE,"fcba4419-a2ee-464f-be9d-58f11bf3418b.sketch_text.stroke-109"),sQuery(id+"F2.wireOp",EDGE,"fcba4419-a2ee-464f-be9d-58f11bf3418b.sketch_text.stroke-110"),sQuery(id+"F2.wireOp",EDGE,"fcba4419-a2ee-464f-be9d-58f11bf3418b.sketch_text.stroke-111"),sQuery(id+"F2.wireOp",EDGE,"fcba4419-a2ee-464f-be9d-58f11bf3418b.sketch_text.stroke-112"),sQuery(id+"F2.wireOp",EDGE,"fcba4419-a2ee-464f-be9d-58f11bf3418b.sketch_text.stroke-113"),sQuery(id+"F2.wireOp",EDGE,"fcba4419-a2ee-464f-be9d-58f11bf3418b.sketch_text.stroke-114"),sQuery(id+"F2.wireOp",EDGE,"fcba4419-a2ee-464f-be9d-58f11bf3418b.sketch_text.stroke-115"),sQuery(id+"F2.wireOp",EDGE,"fcba4419-a2ee-464f-be9d-58f11bf3418b.sketch_text.stroke-116"),sQuery(id+"F2.wireOp",EDGE,"fcba4419-a2ee-464f-be9d-58f11bf3418b.sketch_text.stroke-117"),sQuery(id+"F2.wireOp",EDGE,"fcba4419-a2ee-464f-be9d-58f11bf3418b.sketch_text.stroke-118"),sQuery(id+"F2.wireOp",EDGE,"fcba4419-a2ee-464f-be9d-58f11bf3418b.sketch_text.stroke-119"),sQuery(id+"F2.wireOp",EDGE,"fcba4419-a2ee-464f-be9d-58f11bf3418b.sketch_text.stroke-120"),sQuery(id+"F2.wireOp",EDGE,"fcba4419-a2ee-464f-be9d-58f11bf3418b.sketch_text.stroke-121"),sQuery(id+"F2.wireOp",EDGE,"fcba4419-a2ee-464f-be9d-58f11bf3418b.sketch_text.stroke-122"),sQuery(id+"F2.wireOp",EDGE,"fcba4419-a2ee-464f-be9d-58f11bf3418b.sketch_text.stroke-123"),sQuery(id+"F2.wireOp",EDGE,"fcba4419-a2ee-464f-be9d-58f11bf3418b.sketch_text.stroke-124"),sQuery(id+"F2.wireOp",EDGE,"fcba4419-a2ee-464f-be9d-58f11bf3418b.sketch_text.stroke-125"),sQuery(id+"F2.wireOp",EDGE,"fcba4419-a2ee-464f-be9d-58f11bf3418b.sketch_text.stroke-126"),sQuery(id+"F2.wireOp",EDGE,"fcba4419-a2ee-464f-be9d-58f11bf3418b.sketch_text.stroke-127"),sQuery(id+"F2.wireOp",EDGE,"fcba4419-a2ee-464f-be9d-58f11bf3418b.sketch_text.stroke-128"),sQuery(id+"F2.wireOp",EDGE,"fcba4419-a2ee-464f-be9d-58f11bf3418b.sketch_text.stroke-129"),sQuery(id+"F2.wireOp",EDGE,"fcba4419-a2ee-464f-be9d-58f11bf3418b.sketch_text.stroke-130"),sQuery(id+"F2.wireOp",EDGE,"fcba4419-a2ee-464f-be9d-58f11bf3418b.sketch_text.stroke-131"),sQuery(id+"F2.wireOp",EDGE,"fcba4419-a2ee-464f-be9d-58f11bf3418b.sketch_text.stroke-132"),sQuery(id+"F2.wireOp",EDGE,"fcba4419-a2ee-464f-be9d-58f11bf3418b.sketch_text.stroke-133"),sQuery(id+"F2.wireOp",EDGE,"fcba4419-a2ee-464f-be9d-58f11bf3418b.sketch_text.stroke-134"),sQuery(id+"F2.wireOp",EDGE,"fcba4419-a2ee-464f-be9d-58f11bf3418b.sketch_text.stroke-135"),sQuery(id+"F2.wireOp",EDGE,"fcba4419-a2ee-464f-be9d-58f11bf3418b.sketch_text.stroke-136"),sQuery(id+"F2.wireOp",EDGE,"fcba4419-a2ee-464f-be9d-58f11bf3418b.sketch_text.stroke-137"),sQuery(id+"F2.wireOp",EDGE,"fcba4419-a2ee-464f-be9d-58f11bf3418b.sketch_text.stroke-138"),sQuery(id+"F2.wireOp",EDGE,"fcba4419-a2ee-464f-be9d-58f11bf3418b.sketch_text.stroke-139"),sQuery(id+"F2.wireOp",EDGE,"fcba4419-a2ee-464f-be9d-58f11bf3418b.sketch_text.stroke-140"),sQuery(id+"F2.wireOp",EDGE,"fcba4419-a2ee-464f-be9d-58f11bf3418b.sketch_text.stroke-141"),sQuery(id+"F2.wireOp",EDGE,"fcba4419-a2ee-464f-be9d-58f11bf3418b.sketch_text.stroke-142"),sQuery(id+"F2.wireOp",EDGE,"fcba4419-a2ee-464f-be9d-58f11bf3418b.sketch_text.stroke-143"),sQuery(id+"F2.wireOp",EDGE,"fcba4419-a2ee-464f-be9d-58f11bf3418b.sketch_text.stroke-144"),sQuery(id+"F2.wireOp",EDGE,"fcba4419-a2ee-464f-be9d-58f11bf3418b.sketch_text.stroke-145"),sQuery(id+"F2.wireOp",EDGE,"fcba4419-a2ee-464f-be9d-58f11bf3418b.sketch_text.stroke-146"),sQuery(id+"F2.wireOp",EDGE,"fcba4419-a2ee-464f-be9d-58f11bf3418b.sketch_text.stroke-147"),sQuery(id+"F2.wireOp",EDGE,"fcba4419-a2ee-464f-be9d-58f11bf3418b.sketch_text.stroke-148"),sQuery(id+"F2.wireOp",EDGE,"fcba4419-a2ee-464f-be9d-58f11bf3418b.sketch_text.stroke-149"),sQuery(id+"F2.wireOp",EDGE,"fcba4419-a2ee-464f-be9d-58f11bf3418b.sketch_text.stroke-150"),sQuery(id+"F2.wireOp",EDGE,"fcba4419-a2ee-464f-be9d-58f11bf3418b.sketch_text.stroke-151"),sQuery(id+"F2.wireOp",EDGE,"fcba4419-a2ee-464f-be9d-58f11bf3418b.sketch_text.stroke-152"),sQuery(id+"F2.wireOp",EDGE,"fcba4419-a2ee-464f-be9d-58f11bf3418b.sketch_text.stroke-153"),sQuery(id+"F2.wireOp",EDGE,"fcba4419-a2ee-464f-be9d-58f11bf3418b.sketch_text.stroke-154"),sQuery(id+"F2.wireOp",EDGE,"fcba4419-a2ee-464f-be9d-58f11bf3418b.sketch_text.stroke-155"),sQuery(id+"F2.wireOp",EDGE,"fcba4419-a2ee-464f-be9d-58f11bf3418b.sketch_text.stroke-156"),sQuery(id+"F2.wireOp",EDGE,"fcba4419-a2ee-464f-be9d-58f11bf3418b.sketch_text.stroke-157"),sQuery(id+"F2.wireOp",EDGE,"fcba4419-a2ee-464f-be9d-58f11bf3418b.sketch_text.stroke-158"),sQuery(id+"F2.wireOp",EDGE,"fcba4419-a2ee-464f-be9d-58f11bf3418b.sketch_text.stroke-159"),sQuery(id+"F2.wireOp",EDGE,"fcba4419-a2ee-464f-be9d-58f11bf3418b.sketch_text.stroke-160"),sQuery(id+"F2.wireOp",EDGE,"fcba4419-a2ee-464f-be9d-58f11bf3418b.sketch_text.stroke-161"),sQuery(id+"F2.wireOp",EDGE,"fcba4419-a2ee-464f-be9d-58f11bf3418b.sketch_text.stroke-162"),sQuery(id+"F2.wireOp",EDGE,"fcba4419-a2ee-464f-be9d-58f11bf3418b.sketch_text.stroke-163"),sQuery(id+"F2.wireOp",EDGE,"fcba4419-a2ee-464f-be9d-58f11bf3418b.sketch_text.stroke-164"),sQuery(id+"F2.wireOp",EDGE,"fcba4419-a2ee-464f-be9d-58f11bf3418b.sketch_text.stroke-165"),sQuery(id+"F2.wireOp",EDGE,"fcba4419-a2ee-464f-be9d-58f11bf3418b.sketch_text.stroke-166"),sQuery(id+"F2.wireOp",EDGE,"fcba4419-a2ee-464f-be9d-58f11bf3418b.sketch_text.stroke-167"),sQuery(id+"F2.wireOp",EDGE,"fcba4419-a2ee-464f-be9d-58f11bf3418b.sketch_text.stroke-168"),sQuery(id+"F2.wireOp",EDGE,"fcba4419-a2ee-464f-be9d-58f11bf3418b.sketch_text.stroke-169"),sQuery(id+"F2.wireOp",EDGE,"fcba4419-a2ee-464f-be9d-58f11bf3418b.sketch_text.stroke-170"),sQuery(id+"F2.wireOp",EDGE,"fcba4419-a2ee-464f-be9d-58f11bf3418b.sketch_text.stroke-171"),sQuery(id+"F2.wireOp",EDGE,"fcba4419-a2ee-464f-be9d-58f11bf3418b.sketch_text.stroke-172"),sQuery(id+"F2.wireOp",EDGE,"fcba4419-a2ee-464f-be9d-58f11bf3418b.sketch_text.stroke-173"),sQuery(id+"FHMxAyK4CFUKdhS_1.wireOp",EDGE,"1cb9c079-ea9b-4899-8069-e0e3048e911d.sketch_text.stroke-0"),sQuery(id+"FHMxAyK4CFUKdhS_1.wireOp",EDGE,"1cb9c079-ea9b-4899-8069-e0e3048e911d.sketch_text.stroke-1"),sQuery(id+"FHMxAyK4CFUKdhS_1.wireOp",EDGE,"1cb9c079-ea9b-4899-8069-e0e3048e911d.sketch_text.stroke-2"),sQuery(id+"FHMxAyK4CFUKdhS_1.wireOp",EDGE,"1cb9c079-ea9b-4899-8069-e0e3048e911d.sketch_text.stroke-3"),sQuery(id+"FHMxAyK4CFUKdhS_1.wireOp",EDGE,"1cb9c079-ea9b-4899-8069-e0e3048e911d.sketch_text.stroke-4"),sQuery(id+"FHMxAyK4CFUKdhS_1.wireOp",EDGE,"1cb9c079-ea9b-4899-8069-e0e3048e911d.sketch_text.stroke-5"),sQuery(id+"FHMxAyK4CFUKdhS_1.wireOp",EDGE,"1cb9c079-ea9b-4899-8069-e0e3048e911d.sketch_text.stroke-6"),sQuery(id+"FHMxAyK4CFUKdhS_1.wireOp",EDGE,"1cb9c079-ea9b-4899-8069-e0e3048e911d.sketch_text.stroke-7"),sQuery(id+"FHMxAyK4CFUKdhS_1.wireOp",EDGE,"1cb9c079-ea9b-4899-8069-e0e3048e911d.sketch_text.stroke-8"),sQuery(id+"FHMxAyK4CFUKdhS_1.wireOp",EDGE,"1cb9c079-ea9b-4899-8069-e0e3048e911d.sketch_text.stroke-9"),sQuery(id+"FHMxAyK4CFUKdhS_1.wireOp",EDGE,"1cb9c079-ea9b-4899-8069-e0e3048e911d.sketch_text.stroke-10"),sQuery(id+"FHMxAyK4CFUKdhS_1.wireOp",EDGE,"1cb9c079-ea9b-4899-8069-e0e3048e911d.sketch_text.stroke-11"),sQuery(id+"FHMxAyK4CFUKdhS_1.wireOp",EDGE,"1cb9c079-ea9b-4899-8069-e0e3048e911d.sketch_text.stroke-12"),sQuery(id+"FHMxAyK4CFUKdhS_1.wireOp",EDGE,"1cb9c079-ea9b-4899-8069-e0e3048e911d.sketch_text.stroke-13"),sQuery(id+"FHMxAyK4CFUKdhS_1.wireOp",EDGE,"1cb9c079-ea9b-4899-8069-e0e3048e911d.sketch_text.stroke-14"),sQuery(id+"FHMxAyK4CFUKdhS_1.wireOp",EDGE,"1cb9c079-ea9b-4899-8069-e0e3048e911d.sketch_text.stroke-15"),sQuery(id+"FHMxAyK4CFUKdhS_1.wireOp",EDGE,"1cb9c079-ea9b-4899-8069-e0e3048e911d.sketch_text.stroke-16"),sQuery(id+"FHMxAyK4CFUKdhS_1.wireOp",EDGE,"1cb9c079-ea9b-4899-8069-e0e3048e911d.sketch_text.stroke-17"),sQuery(id+"FHMxAyK4CFUKdhS_1.wireOp",EDGE,"1cb9c079-ea9b-4899-8069-e0e3048e911d.sketch_text.stroke-18"),sQuery(id+"FHMxAyK4CFUKdhS_1.wireOp",EDGE,"1cb9c079-ea9b-4899-8069-e0e3048e911d.sketch_text.stroke-19"),sQuery(id+"FHMxAyK4CFUKdhS_1.wireOp",EDGE,"1cb9c079-ea9b-4899-8069-e0e3048e911d.sketch_text.stroke-20"),sQuery(id+"FHMxAyK4CFUKdhS_1.wireOp",EDGE,"1cb9c079-ea9b-4899-8069-e0e3048e911d.sketch_text.stroke-21"),sQuery(id+"FHMxAyK4CFUKdhS_1.wireOp",EDGE,"1cb9c079-ea9b-4899-8069-e0e3048e911d.sketch_text.stroke-22"),sQuery(id+"FHMxAyK4CFUKdhS_1.wireOp",EDGE,"1cb9c079-ea9b-4899-8069-e0e3048e911d.sketch_text.stroke-23"),sQuery(id+"FHMxAyK4CFUKdhS_1.wireOp",EDGE,"1cb9c079-ea9b-4899-8069-e0e3048e911d.sketch_text.stroke-24"),sQuery(id+"FHMxAyK4CFUKdhS_1.wireOp",EDGE,"1cb9c079-ea9b-4899-8069-e0e3048e911d.sketch_text.stroke-25"),sQuery(id+"FHMxAyK4CFUKdhS_1.wireOp",EDGE,"1cb9c079-ea9b-4899-8069-e0e3048e911d.sketch_text.stroke-26"),sQuery(id+"FHMxAyK4CFUKdhS_1.wireOp",EDGE,"1cb9c079-ea9b-4899-8069-e0e3048e911d.sketch_text.stroke-27"),sQuery(id+"FHMxAyK4CFUKdhS_1.wireOp",EDGE,"1cb9c079-ea9b-4899-8069-e0e3048e911d.sketch_text.stroke-28"),sQuery(id+"FHMxAyK4CFUKdhS_1.wireOp",EDGE,"1cb9c079-ea9b-4899-8069-e0e3048e911d.sketch_text.stroke-29"),sQuery(id+"FHMxAyK4CFUKdhS_1.wireOp",EDGE,"1cb9c079-ea9b-4899-8069-e0e3048e911d.sketch_text.stroke-30"),sQuery(id+"FHMxAyK4CFUKdhS_1.wireOp",EDGE,"1cb9c079-ea9b-4899-8069-e0e3048e911d.sketch_text.stroke-31"),sQuery(id+"FHMxAyK4CFUKdhS_1.wireOp",EDGE,"1cb9c079-ea9b-4899-8069-e0e3048e911d.sketch_text.stroke-32"),sQuery(id+"FHMxAyK4CFUKdhS_1.wireOp",EDGE,"1cb9c079-ea9b-4899-8069-e0e3048e911d.sketch_text.stroke-33"),sQuery(id+"FHMxAyK4CFUKdhS_1.wireOp",EDGE,"1cb9c079-ea9b-4899-8069-e0e3048e911d.sketch_text.stroke-34"),sQuery(id+"FHMxAyK4CFUKdhS_1.wireOp",EDGE,"1cb9c079-ea9b-4899-8069-e0e3048e911d.sketch_text.stroke-35"),sQuery(id+"FHMxAyK4CFUKdhS_1.wireOp",EDGE,"1cb9c079-ea9b-4899-8069-e0e3048e911d.sketch_text.stroke-36"),sQuery(id+"FHMxAyK4CFUKdhS_1.wireOp",EDGE,"1cb9c079-ea9b-4899-8069-e0e3048e911d.sketch_text.stroke-37"),sQuery(id+"FHMxAyK4CFUKdhS_1.wireOp",EDGE,"1cb9c079-ea9b-4899-8069-e0e3048e911d.sketch_text.stroke-38"),sQuery(id+"FHMxAyK4CFUKdhS_1.wireOp",EDGE,"1cb9c079-ea9b-4899-8069-e0e3048e911d.sketch_text.stroke-39"),sQuery(id+"FHMxAyK4CFUKdhS_1.wireOp",EDGE,"1cb9c079-ea9b-4899-8069-e0e3048e911d.sketch_text.stroke-40"),sQuery(id+"FHMxAyK4CFUKdhS_1.wireOp",EDGE,"1cb9c079-ea9b-4899-8069-e0e3048e911d.sketch_text.stroke-41"),sQuery(id+"FHMxAyK4CFUKdhS_1.wireOp",EDGE,"1cb9c079-ea9b-4899-8069-e0e3048e911d.sketch_text.stroke-42"),sQuery(id+"FHMxAyK4CFUKdhS_1.wireOp",EDGE,"1cb9c079-ea9b-4899-8069-e0e3048e911d.sketch_text.stroke-43"),sQuery(id+"FHMxAyK4CFUKdhS_1.wireOp",EDGE,"1cb9c079-ea9b-4899-8069-e0e3048e911d.sketch_text.stroke-44"),sQuery(id+"FHMxAyK4CFUKdhS_1.wireOp",EDGE,"1cb9c079-ea9b-4899-8069-e0e3048e911d.sketch_text.stroke-45"),sQuery(id+"FHMxAyK4CFUKdhS_1.wireOp",EDGE,"1cb9c079-ea9b-4899-8069-e0e3048e911d.sketch_text.stroke-46"),sQuery(id+"FHMxAyK4CFUKdhS_1.wireOp",EDGE,"1cb9c079-ea9b-4899-8069-e0e3048e911d.sketch_text.stroke-47"),sQuery(id+"FHMxAyK4CFUKdhS_1.wireOp",EDGE,"1cb9c079-ea9b-4899-8069-e0e3048e911d.sketch_text.stroke-48"),sQuery(id+"FHMxAyK4CFUKdhS_1.wireOp",EDGE,"1cb9c079-ea9b-4899-8069-e0e3048e911d.sketch_text.stroke-49"),sQuery(id+"FHMxAyK4CFUKdhS_1.wireOp",EDGE,"1cb9c079-ea9b-4899-8069-e0e3048e911d.sketch_text.stroke-50"),sQuery(id+"FHMxAyK4CFUKdhS_1.wireOp",EDGE,"1cb9c079-ea9b-4899-8069-e0e3048e911d.sketch_text.stroke-51"),sQuery(id+"FHMxAyK4CFUKdhS_1.wireOp",EDGE,"1cb9c079-ea9b-4899-8069-e0e3048e911d.sketch_text.stroke-52"),sQuery(id+"FHMxAyK4CFUKdhS_1.wireOp",EDGE,"1cb9c079-ea9b-4899-8069-e0e3048e911d.sketch_text.stroke-53"),sQuery(id+"FHMxAyK4CFUKdhS_1.wireOp",EDGE,"1cb9c079-ea9b-4899-8069-e0e3048e911d.sketch_text.stroke-54"),sQuery(id+"FHMxAyK4CFUKdhS_1.wireOp",EDGE,"1cb9c079-ea9b-4899-8069-e0e3048e911d.sketch_text.stroke-55"),sQuery(id+"FHMxAyK4CFUKdhS_1.wireOp",EDGE,"1cb9c079-ea9b-4899-8069-e0e3048e911d.sketch_text.stroke-56"),sQuery(id+"FHMxAyK4CFUKdhS_1.wireOp",EDGE,"1cb9c079-ea9b-4899-8069-e0e3048e911d.sketch_text.stroke-57"),sQuery(id+"FHMxAyK4CFUKdhS_1.wireOp",EDGE,"1cb9c079-ea9b-4899-8069-e0e3048e911d.sketch_text.stroke-58"),sQuery(id+"FHMxAyK4CFUKdhS_1.wireOp",EDGE,"1cb9c079-ea9b-4899-8069-e0e3048e911d.sketch_text.stroke-59"),sQuery(id+"FHMxAyK4CFUKdhS_1.wireOp",EDGE,"1cb9c079-ea9b-4899-8069-e0e3048e911d.sketch_text.stroke-60"),sQuery(id+"FHMxAyK4CFUKdhS_1.wireOp",EDGE,"1cb9c079-ea9b-4899-8069-e0e3048e911d.sketch_text.stroke-61"),sQuery(id+"FHMxAyK4CFUKdhS_1.wireOp",EDGE,"1cb9c079-ea9b-4899-8069-e0e3048e911d.sketch_text.stroke-62"),sQuery(id+"FHMxAyK4CFUKdhS_1.wireOp",EDGE,"1cb9c079-ea9b-4899-8069-e0e3048e911d.sketch_text.stroke-71"),sQuery(id+"FHMxAyK4CFUKdhS_1.wireOp",EDGE,"1cb9c079-ea9b-4899-8069-e0e3048e911d.sketch_text.stroke-72"),sQuery(id+"FHMxAyK4CFUKdhS_1.wireOp",EDGE,"1cb9c079-ea9b-4899-8069-e0e3048e911d.sketch_text.stroke-73"),sQuery(id+"FHMxAyK4CFUKdhS_1.wireOp",EDGE,"1cb9c079-ea9b-4899-8069-e0e3048e911d.sketch_text.stroke-74"),sQuery(id+"FHMxAyK4CFUKdhS_1.wireOp",EDGE,"1cb9c079-ea9b-4899-8069-e0e3048e911d.sketch_text.stroke-75"),sQuery(id+"FHMxAyK4CFUKdhS_1.wireOp",EDGE,"1cb9c079-ea9b-4899-8069-e0e3048e911d.sketch_text.stroke-76"),sQuery(id+"FHMxAyK4CFUKdhS_1.wireOp",EDGE,"1cb9c079-ea9b-4899-8069-e0e3048e911d.sketch_text.stroke-77"),sQuery(id+"FHMxAyK4CFUKdhS_1.wireOp",EDGE,"1cb9c079-ea9b-4899-8069-e0e3048e911d.sketch_text.stroke-78"),sQuery(id+"FHMxAyK4CFUKdhS_1.wireOp",EDGE,"1cb9c079-ea9b-4899-8069-e0e3048e911d.sketch_text.stroke-79"),sQuery(id+"FHMxAyK4CFUKdhS_1.wireOp",EDGE,"1cb9c079-ea9b-4899-8069-e0e3048e911d.sketch_text.stroke-80"),sQuery(id+"FHMxAyK4CFUKdhS_1.wireOp",EDGE,"1cb9c079-ea9b-4899-8069-e0e3048e911d.sketch_text.stroke-81"),sQuery(id+"FHMxAyK4CFUKdhS_1.wireOp",EDGE,"1cb9c079-ea9b-4899-8069-e0e3048e911d.sketch_text.stroke-82"),sQuery(id+"FHMxAyK4CFUKdhS_1.wireOp",EDGE,"1cb9c079-ea9b-4899-8069-e0e3048e911d.sketch_text.stroke-83"),sQuery(id+"FHMxAyK4CFUKdhS_1.wireOp",EDGE,"1cb9c079-ea9b-4899-8069-e0e3048e911d.sketch_text.stroke-84"),sQuery(id+"FHMxAyK4CFUKdhS_1.wireOp",EDGE,"1cb9c079-ea9b-4899-8069-e0e3048e911d.sketch_text.stroke-85"),sQuery(id+"FHMxAyK4CFUKdhS_1.wireOp",EDGE,"1cb9c079-ea9b-4899-8069-e0e3048e911d.sketch_text.stroke-86"),sQuery(id+"FHMxAyK4CFUKdhS_1.wireOp",EDGE,"1cb9c079-ea9b-4899-8069-e0e3048e911d.sketch_text.stroke-87"),sQuery(id+"FHMxAyK4CFUKdhS_1.wireOp",EDGE,"1cb9c079-ea9b-4899-8069-e0e3048e911d.sketch_text.stroke-88"),sQuery(id+"FHMxAyK4CFUKdhS_1.wireOp",EDGE,"1cb9c079-ea9b-4899-8069-e0e3048e911d.sketch_text.stroke-89"),sQuery(id+"FHMxAyK4CFUKdhS_1.wireOp",EDGE,"1cb9c079-ea9b-4899-8069-e0e3048e911d.sketch_text.stroke-90"),sQuery(id+"FHMxAyK4CFUKdhS_1.wireOp",EDGE,"1cb9c079-ea9b-4899-8069-e0e3048e911d.sketch_text.stroke-91"),sQuery(id+"FHMxAyK4CFUKdhS_1.wireOp",EDGE,"1cb9c079-ea9b-4899-8069-e0e3048e911d.sketch_text.stroke-92"),sQuery(id+"FHMxAyK4CFUKdhS_1.wireOp",EDGE,"1cb9c079-ea9b-4899-8069-e0e3048e911d.sketch_text.stroke-93"),sQuery(id+"FHMxAyK4CFUKdhS_1.wireOp",EDGE,"1cb9c079-ea9b-4899-8069-e0e3048e911d.sketch_text.stroke-94"),sQuery(id+"FHMxAyK4CFUKdhS_1.wireOp",EDGE,"1cb9c079-ea9b-4899-8069-e0e3048e911d.sketch_text.stroke-95"),sQuery(id+"FHMxAyK4CFUKdhS_1.wireOp",EDGE,"1cb9c079-ea9b-4899-8069-e0e3048e911d.sketch_text.stroke-96"),sQuery(id+"FHMxAyK4CFUKdhS_1.wireOp",EDGE,"1cb9c079-ea9b-4899-8069-e0e3048e911d.sketch_text.stroke-97"),sQuery(id+"FHMxAyK4CFUKdhS_1.wireOp",EDGE,"1cb9c079-ea9b-4899-8069-e0e3048e911d.sketch_text.stroke-103"),sQuery(id+"FHMxAyK4CFUKdhS_1.wireOp",EDGE,"1cb9c079-ea9b-4899-8069-e0e3048e911d.sketch_text.stroke-104"),sQuery(id+"FHMxAyK4CFUKdhS_1.wireOp",EDGE,"1cb9c079-ea9b-4899-8069-e0e3048e911d.sketch_text.stroke-105"),sQuery(id+"FHMxAyK4CFUKdhS_1.wireOp",EDGE,"1cb9c079-ea9b-4899-8069-e0e3048e911d.sketch_text.stroke-106"),sQuery(id+"FHMxAyK4CFUKdhS_1.wireOp",EDGE,"1cb9c079-ea9b-4899-8069-e0e3048e911d.sketch_text.stroke-107"),sQuery(id+"FHMxAyK4CFUKdhS_1.wireOp",EDGE,"1cb9c079-ea9b-4899-8069-e0e3048e911d.sketch_text.stroke-108"),sQuery(id+"FHMxAyK4CFUKdhS_1.wireOp",EDGE,"1cb9c079-ea9b-4899-8069-e0e3048e911d.sketch_text.stroke-109"),sQuery(id+"FHMxAyK4CFUKdhS_1.wireOp",EDGE,"1cb9c079-ea9b-4899-8069-e0e3048e911d.sketch_text.stroke-110"),sQuery(id+"FHMxAyK4CFUKdhS_1.wireOp",EDGE,"1cb9c079-ea9b-4899-8069-e0e3048e911d.sketch_text.stroke-111"),sQuery(id+"FHMxAyK4CFUKdhS_1.wireOp",EDGE,"1cb9c079-ea9b-4899-8069-e0e3048e911d.sketch_text.stroke-112"),sQuery(id+"FHMxAyK4CFUKdhS_1.wireOp",EDGE,"1cb9c079-ea9b-4899-8069-e0e3048e911d.sketch_text.stroke-113"),sQuery(id+"FHMxAyK4CFUKdhS_1.wireOp",EDGE,"1cb9c079-ea9b-4899-8069-e0e3048e911d.sketch_text.stroke-114"),sQuery(id+"FHMxAyK4CFUKdhS_1.wireOp",EDGE,"1cb9c079-ea9b-4899-8069-e0e3048e911d.sketch_text.stroke-115"),sQuery(id+"FHMxAyK4CFUKdhS_1.wireOp",EDGE,"1cb9c079-ea9b-4899-8069-e0e3048e911d.sketch_text.stroke-116"),sQuery(id+"FHMxAyK4CFUKdhS_1.wireOp",EDGE,"1cb9c079-ea9b-4899-8069-e0e3048e911d.sketch_text.stroke-117"),sQuery(id+"FHMxAyK4CFUKdhS_1.wireOp",EDGE,"1cb9c079-ea9b-4899-8069-e0e3048e911d.sketch_text.stroke-118"),sQuery(id+"FHMxAyK4CFUKdhS_1.wireOp",EDGE,"1cb9c079-ea9b-4899-8069-e0e3048e911d.sketch_text.stroke-119"),sQuery(id+"FHMxAyK4CFUKdhS_1.wireOp",EDGE,"1cb9c079-ea9b-4899-8069-e0e3048e911d.sketch_text.stroke-120"),sQuery(id+"FHMxAyK4CFUKdhS_1.wireOp",EDGE,"1cb9c079-ea9b-4899-8069-e0e3048e911d.sketch_text.stroke-121"),sQuery(id+"FHMxAyK4CFUKdhS_1.wireOp",EDGE,"1cb9c079-ea9b-4899-8069-e0e3048e911d.sketch_text.stroke-122"),sQuery(id+"FHMxAyK4CFUKdhS_1.wireOp",EDGE,"1cb9c079-ea9b-4899-8069-e0e3048e911d.sketch_text.stroke-123"),sQuery(id+"FHMxAyK4CFUKdhS_1.wireOp",EDGE,"1cb9c079-ea9b-4899-8069-e0e3048e911d.sketch_text.stroke-124"),sQuery(id+"FHMxAyK4CFUKdhS_1.wireOp",EDGE,"1cb9c079-ea9b-4899-8069-e0e3048e911d.sketch_text.stroke-125"),sQuery(id+"FHMxAyK4CFUKdhS_1.wireOp",EDGE,"1cb9c079-ea9b-4899-8069-e0e3048e911d.sketch_text.stroke-126"),sQuery(id+"FHMxAyK4CFUKdhS_1.wireOp",EDGE,"1cb9c079-ea9b-4899-8069-e0e3048e911d.sketch_text.stroke-127"),sQuery(id+"FHMxAyK4CFUKdhS_1.wireOp",EDGE,"1cb9c079-ea9b-4899-8069-e0e3048e911d.sketch_text.stroke-128"),sQuery(id+"FHMxAyK4CFUKdhS_1.wireOp",EDGE,"1cb9c079-ea9b-4899-8069-e0e3048e911d.sketch_text.stroke-129"),sQuery(id+"FHMxAyK4CFUKdhS_1.wireOp",EDGE,"1cb9c079-ea9b-4899-8069-e0e3048e911d.sketch_text.stroke-130"),sQuery(id+"FHMxAyK4CFUKdhS_1.wireOp",EDGE,"1cb9c079-ea9b-4899-8069-e0e3048e911d.sketch_text.stroke-131"),sQuery(id+"FHMxAyK4CFUKdhS_1.wireOp",EDGE,"1cb9c079-ea9b-4899-8069-e0e3048e911d.sketch_text.stroke-132"),sQuery(id+"FHMxAyK4CFUKdhS_1.wireOp",EDGE,"1cb9c079-ea9b-4899-8069-e0e3048e911d.sketch_text.stroke-133"),sQuery(id+"FHMxAyK4CFUKdhS_1.wireOp",EDGE,"1cb9c079-ea9b-4899-8069-e0e3048e911d.sketch_text.stroke-134"),sQuery(id+"FHMxAyK4CFUKdhS_1.wireOp",EDGE,"1cb9c079-ea9b-4899-8069-e0e3048e911d.sketch_text.stroke-135"),sQuery(id+"FHMxAyK4CFUKdhS_1.wireOp",EDGE,"1cb9c079-ea9b-4899-8069-e0e3048e911d.sketch_text.stroke-136"),sQuery(id+"FHMxAyK4CFUKdhS_1.wireOp",EDGE,"1cb9c079-ea9b-4899-8069-e0e3048e911d.sketch_text.stroke-137"),sQuery(id+"FHMxAyK4CFUKdhS_1.wireOp",EDGE,"1cb9c079-ea9b-4899-8069-e0e3048e911d.sketch_text.stroke-138"),sQuery(id+"FHMxAyK4CFUKdhS_1.wireOp",EDGE,"1cb9c079-ea9b-4899-8069-e0e3048e911d.sketch_text.stroke-139"),sQuery(id+"FHMxAyK4CFUKdhS_1.wireOp",EDGE,"1cb9c079-ea9b-4899-8069-e0e3048e911d.sketch_text.stroke-140"),sQuery(id+"FHMxAyK4CFUKdhS_1.wireOp",EDGE,"1cb9c079-ea9b-4899-8069-e0e3048e911d.sketch_text.stroke-141"),sQuery(id+"FHMxAyK4CFUKdhS_1.wireOp",EDGE,"1cb9c079-ea9b-4899-8069-e0e3048e911d.sketch_text.stroke-142"),sQuery(id+"FHMxAyK4CFUKdhS_1.wireOp",EDGE,"1cb9c079-ea9b-4899-8069-e0e3048e911d.sketch_text.stroke-143"),sQuery(id+"FHMxAyK4CFUKdhS_1.wireOp",EDGE,"1cb9c079-ea9b-4899-8069-e0e3048e911d.sketch_text.stroke-144"),sQuery(id+"FHMxAyK4CFUKdhS_1.wireOp",EDGE,"1cb9c079-ea9b-4899-8069-e0e3048e911d.sketch_text.stroke-145"),sQuery(id+"FHMxAyK4CFUKdhS_1.wireOp",EDGE,"1cb9c079-ea9b-4899-8069-e0e3048e911d.sketch_text.stroke-146"),sQuery(id+"FHMxAyK4CFUKdhS_1.wireOp",EDGE,"1cb9c079-ea9b-4899-8069-e0e3048e911d.sketch_text.stroke-147"),sQuery(id+"FHMxAyK4CFUKdhS_1.wireOp",EDGE,"1cb9c079-ea9b-4899-8069-e0e3048e911d.sketch_text.stroke-148"),sQuery(id+"FHMxAyK4CFUKdhS_1.wireOp",EDGE,"1cb9c079-ea9b-4899-8069-e0e3048e911d.sketch_text.stroke-149"),sQuery(id+"FHMxAyK4CFUKdhS_1.wireOp",EDGE,"1cb9c079-ea9b-4899-8069-e0e3048e911d.sketch_text.stroke-150"),sQuery(id+"FHMxAyK4CFUKdhS_1.wireOp",EDGE,"1cb9c079-ea9b-4899-8069-e0e3048e911d.sketch_text.stroke-151"),sQuery(id+"FHMxAyK4CFUKdhS_1.wireOp",EDGE,"1cb9c079-ea9b-4899-8069-e0e3048e911d.sketch_text.stroke-152"),sQuery(id+"FHMxAyK4CFUKdhS_1.wireOp",EDGE,"1cb9c079-ea9b-4899-8069-e0e3048e911d.sketch_text.stroke-153"),sQuery(id+"FHMxAyK4CFUKdhS_1.wireOp",EDGE,"1cb9c079-ea9b-4899-8069-e0e3048e911d.sketch_text.stroke-159"),sQuery(id+"FHMxAyK4CFUKdhS_1.wireOp",EDGE,"1cb9c079-ea9b-4899-8069-e0e3048e911d.sketch_text.stroke-160"),sQuery(id+"FHMxAyK4CFUKdhS_1.wireOp",EDGE,"1cb9c079-ea9b-4899-8069-e0e3048e911d.sketch_text.stroke-161"),sQuery(id+"FHMxAyK4CFUKdhS_1.wireOp",EDGE,"1cb9c079-ea9b-4899-8069-e0e3048e911d.sketch_text.stroke-162"),sQuery(id+"FHMxAyK4CFUKdhS_1.wireOp",EDGE,"1cb9c079-ea9b-4899-8069-e0e3048e911d.sketch_text.stroke-163"),sQuery(id+"FHMxAyK4CFUKdhS_1.wireOp",EDGE,"1cb9c079-ea9b-4899-8069-e0e3048e911d.sketch_text.stroke-164"),sQuery(id+"FHMxAyK4CFUKdhS_1.wireOp",EDGE,"1cb9c079-ea9b-4899-8069-e0e3048e911d.sketch_text.stroke-165"),sQuery(id+"FHMxAyK4CFUKdhS_1.wireOp",EDGE,"1cb9c079-ea9b-4899-8069-e0e3048e911d.sketch_text.stroke-166"),sQuery(id+"FHMxAyK4CFUKdhS_1.wireOp",EDGE,"1cb9c079-ea9b-4899-8069-e0e3048e911d.sketch_text.stroke-167"),sQuery(id+"FHMxAyK4CFUKdhS_1.wireOp",EDGE,"1cb9c079-ea9b-4899-8069-e0e3048e911d.sketch_text.stroke-168"),sQuery(id+"FHMxAyK4CFUKdhS_1.wireOp",EDGE,"1cb9c079-ea9b-4899-8069-e0e3048e911d.sketch_text.stroke-169"),sQuery(id+"FHMxAyK4CFUKdhS_1.wireOp",EDGE,"1cb9c079-ea9b-4899-8069-e0e3048e911d.sketch_text.stroke-170"),sQuery(id+"FHMxAyK4CFUKdhS_1.wireOp",EDGE,"1cb9c079-ea9b-4899-8069-e0e3048e911d.sketch_text.stroke-171"),sQuery(id+"FHMxAyK4CFUKdhS_1.wireOp",EDGE,"1cb9c079-ea9b-4899-8069-e0e3048e911d.sketch_text.stroke-172"),sQuery(id+"FHMxAyK4CFUKdhS_1.wireOp",EDGE,"1cb9c079-ea9b-4899-8069-e0e3048e911d.sketch_text.stroke-173"),sQuery(id+"FHMxAyK4CFUKdhS_1.wireOp",EDGE,"1cb9c079-ea9b-4899-8069-e0e3048e911d.sketch_text.stroke-174"),sQuery(id+"FHMxAyK4CFUKdhS_1.wireOp",EDGE,"1cb9c079-ea9b-4899-8069-e0e3048e911d.sketch_text.stroke-175"),sQuery(id+"FHMxAyK4CFUKdhS_1.wireOp",EDGE,"1cb9c079-ea9b-4899-8069-e0e3048e911d.sketch_text.stroke-176"),sQuery(id+"FHMxAyK4CFUKdhS_1.wireOp",EDGE,"1cb9c079-ea9b-4899-8069-e0e3048e911d.sketch_text.stroke-177"),sQuery(id+"FHMxAyK4CFUKdhS_1.wireOp",EDGE,"1cb9c079-ea9b-4899-8069-e0e3048e911d.sketch_text.stroke-178"),sQuery(id+"FHMxAyK4CFUKdhS_1.wireOp",EDGE,"1cb9c079-ea9b-4899-8069-e0e3048e911d.sketch_text.stroke-179"),sQuery(id+"FHMxAyK4CFUKdhS_1.wireOp",EDGE,"1cb9c079-ea9b-4899-8069-e0e3048e911d.sketch_text.stroke-180"),subQ2,sQuery(id+"F3.wireOp",EDGE,"6ee83ff3-586e-4dbe-aaea-af71240543bd")])],"isStart":true})]),OD(1.0)],"derivedFrom":makeQuery(id+"F1.opExtrude","CAP_EDGE",EDGE,{"disambiguationData":[OSD([subQ0])],"isStart":false})});}
            var Q5;
            {var subQ0=sQuery(id+"F0.wireOp",EDGE,"E0.top");var subQ1=sQuery(id+"F0.wireOp",EDGE,"E0.bottom");var subQ2=sQuery(id+"F3.wireOp",EDGE,"8007402e-1a4e-4a06-85a5-2af08e553504");Q5=makeQuery(id+"F4.boolean.opBoolean","SPLIT",EDGE,{"disambiguationData":[TD([makeQuery(id+"F1.opExtrude","CAP_FACE",FACE,{"disambiguationData":[OSD([subQ1,subQ0,sQuery(id+"F0.wireOp",EDGE,"E0.left"),sQuery(id+"F0.wireOp",EDGE,"E0.right")])],"isStart":false}),makeQuery(id+"F1.opExtrude","SWEPT_FACE",FACE,{"disambiguationData":[OSD([subQ0])]}),makeQuery(id+"F4.opExtrude","SWEPT_FACE",FACE,{"disambiguationData":[OSD([subQ2])]}),makeQuery(id+"F4.opExtrude","CAP_FACE",FACE,{"disambiguationData":[OSD([subQ1,sQuery(id+"F2.wireOp",EDGE,"fcba4419-a2ee-464f-be9d-58f11bf3418b.sketch_text.stroke-0"),sQuery(id+"F2.wireOp",EDGE,"fcba4419-a2ee-464f-be9d-58f11bf3418b.sketch_text.stroke-1"),sQuery(id+"F2.wireOp",EDGE,"fcba4419-a2ee-464f-be9d-58f11bf3418b.sketch_text.stroke-2"),sQuery(id+"F2.wireOp",EDGE,"fcba4419-a2ee-464f-be9d-58f11bf3418b.sketch_text.stroke-3"),sQuery(id+"F2.wireOp",EDGE,"fcba4419-a2ee-464f-be9d-58f11bf3418b.sketch_text.stroke-4"),sQuery(id+"F2.wireOp",EDGE,"fcba4419-a2ee-464f-be9d-58f11bf3418b.sketch_text.stroke-5"),sQuery(id+"F2.wireOp",EDGE,"fcba4419-a2ee-464f-be9d-58f11bf3418b.sketch_text.stroke-6"),sQuery(id+"F2.wireOp",EDGE,"fcba4419-a2ee-464f-be9d-58f11bf3418b.sketch_text.stroke-7"),sQuery(id+"F2.wireOp",EDGE,"fcba4419-a2ee-464f-be9d-58f11bf3418b.sketch_text.stroke-8"),sQuery(id+"F2.wireOp",EDGE,"fcba4419-a2ee-464f-be9d-58f11bf3418b.sketch_text.stroke-9"),sQuery(id+"F2.wireOp",EDGE,"fcba4419-a2ee-464f-be9d-58f11bf3418b.sketch_text.stroke-10"),sQuery(id+"F2.wireOp",EDGE,"fcba4419-a2ee-464f-be9d-58f11bf3418b.sketch_text.stroke-11"),sQuery(id+"F2.wireOp",EDGE,"fcba4419-a2ee-464f-be9d-58f11bf3418b.sketch_text.stroke-12"),sQuery(id+"F2.wireOp",EDGE,"fcba4419-a2ee-464f-be9d-58f11bf3418b.sketch_text.stroke-13"),sQuery(id+"F2.wireOp",EDGE,"fcba4419-a2ee-464f-be9d-58f11bf3418b.sketch_text.stroke-14"),sQuery(id+"F2.wireOp",EDGE,"fcba4419-a2ee-464f-be9d-58f11bf3418b.sketch_text.stroke-15"),sQuery(id+"F2.wireOp",EDGE,"fcba4419-a2ee-464f-be9d-58f11bf3418b.sketch_text.stroke-16"),sQuery(id+"F2.wireOp",EDGE,"fcba4419-a2ee-464f-be9d-58f11bf3418b.sketch_text.stroke-17"),sQuery(id+"F2.wireOp",EDGE,"fcba4419-a2ee-464f-be9d-58f11bf3418b.sketch_text.stroke-18"),sQuery(id+"F2.wireOp",EDGE,"fcba4419-a2ee-464f-be9d-58f11bf3418b.sketch_text.stroke-19"),sQuery(id+"F2.wireOp",EDGE,"fcba4419-a2ee-464f-be9d-58f11bf3418b.sketch_text.stroke-20"),sQuery(id+"F2.wireOp",EDGE,"fcba4419-a2ee-464f-be9d-58f11bf3418b.sketch_text.stroke-21"),sQuery(id+"F2.wireOp",EDGE,"fcba4419-a2ee-464f-be9d-58f11bf3418b.sketch_text.stroke-22"),sQuery(id+"F2.wireOp",EDGE,"fcba4419-a2ee-464f-be9d-58f11bf3418b.sketch_text.stroke-23"),sQuery(id+"F2.wireOp",EDGE,"fcba4419-a2ee-464f-be9d-58f11bf3418b.sketch_text.stroke-24"),sQuery(id+"F2.wireOp",EDGE,"fcba4419-a2ee-464f-be9d-58f11bf3418b.sketch_text.stroke-25"),sQuery(id+"F2.wireOp",EDGE,"fcba4419-a2ee-464f-be9d-58f11bf3418b.sketch_text.stroke-26"),sQuery(id+"F2.wireOp",EDGE,"fcba4419-a2ee-464f-be9d-58f11bf3418b.sketch_text.stroke-27"),sQuery(id+"F2.wireOp",EDGE,"fcba4419-a2ee-464f-be9d-58f11bf3418b.sketch_text.stroke-28"),sQuery(id+"F2.wireOp",EDGE,"fcba4419-a2ee-464f-be9d-58f11bf3418b.sketch_text.stroke-29"),sQuery(id+"F2.wireOp",EDGE,"fcba4419-a2ee-464f-be9d-58f11bf3418b.sketch_text.stroke-30"),sQuery(id+"F2.wireOp",EDGE,"fcba4419-a2ee-464f-be9d-58f11bf3418b.sketch_text.stroke-31"),sQuery(id+"F2.wireOp",EDGE,"fcba4419-a2ee-464f-be9d-58f11bf3418b.sketch_text.stroke-32"),sQuery(id+"F2.wireOp",EDGE,"fcba4419-a2ee-464f-be9d-58f11bf3418b.sketch_text.stroke-33"),sQuery(id+"F2.wireOp",EDGE,"fcba4419-a2ee-464f-be9d-58f11bf3418b.sketch_text.stroke-34"),sQuery(id+"F2.wireOp",EDGE,"fcba4419-a2ee-464f-be9d-58f11bf3418b.sketch_text.stroke-35"),sQuery(id+"F2.wireOp",EDGE,"fcba4419-a2ee-464f-be9d-58f11bf3418b.sketch_text.stroke-36"),sQuery(id+"F2.wireOp",EDGE,"fcba4419-a2ee-464f-be9d-58f11bf3418b.sketch_text.stroke-37"),sQuery(id+"F2.wireOp",EDGE,"fcba4419-a2ee-464f-be9d-58f11bf3418b.sketch_text.stroke-38"),sQuery(id+"F2.wireOp",EDGE,"fcba4419-a2ee-464f-be9d-58f11bf3418b.sketch_text.stroke-39"),sQuery(id+"F2.wireOp",EDGE,"fcba4419-a2ee-464f-be9d-58f11bf3418b.sketch_text.stroke-40"),sQuery(id+"F2.wireOp",EDGE,"fcba4419-a2ee-464f-be9d-58f11bf3418b.sketch_text.stroke-41"),sQuery(id+"F2.wireOp",EDGE,"fcba4419-a2ee-464f-be9d-58f11bf3418b.sketch_text.stroke-42"),sQuery(id+"F2.wireOp",EDGE,"fcba4419-a2ee-464f-be9d-58f11bf3418b.sketch_text.stroke-43"),sQuery(id+"F2.wireOp",EDGE,"fcba4419-a2ee-464f-be9d-58f11bf3418b.sketch_text.stroke-44"),sQuery(id+"F2.wireOp",EDGE,"fcba4419-a2ee-464f-be9d-58f11bf3418b.sketch_text.stroke-45"),sQuery(id+"F2.wireOp",EDGE,"fcba4419-a2ee-464f-be9d-58f11bf3418b.sketch_text.stroke-46"),sQuery(id+"F2.wireOp",EDGE,"fcba4419-a2ee-464f-be9d-58f11bf3418b.sketch_text.stroke-47"),sQuery(id+"F2.wireOp",EDGE,"fcba4419-a2ee-464f-be9d-58f11bf3418b.sketch_text.stroke-48"),sQuery(id+"F2.wireOp",EDGE,"fcba4419-a2ee-464f-be9d-58f11bf3418b.sketch_text.stroke-49"),sQuery(id+"F2.wireOp",EDGE,"fcba4419-a2ee-464f-be9d-58f11bf3418b.sketch_text.stroke-50"),sQuery(id+"F2.wireOp",EDGE,"fcba4419-a2ee-464f-be9d-58f11bf3418b.sketch_text.stroke-51"),sQuery(id+"F2.wireOp",EDGE,"fcba4419-a2ee-464f-be9d-58f11bf3418b.sketch_text.stroke-52"),sQuery(id+"F2.wireOp",EDGE,"fcba4419-a2ee-464f-be9d-58f11bf3418b.sketch_text.stroke-53"),sQuery(id+"F2.wireOp",EDGE,"fcba4419-a2ee-464f-be9d-58f11bf3418b.sketch_text.stroke-54"),sQuery(id+"F2.wireOp",EDGE,"fcba4419-a2ee-464f-be9d-58f11bf3418b.sketch_text.stroke-55"),sQuery(id+"F2.wireOp",EDGE,"fcba4419-a2ee-464f-be9d-58f11bf3418b.sketch_text.stroke-56"),sQuery(id+"F2.wireOp",EDGE,"fcba4419-a2ee-464f-be9d-58f11bf3418b.sketch_text.stroke-57"),sQuery(id+"F2.wireOp",EDGE,"fcba4419-a2ee-464f-be9d-58f11bf3418b.sketch_text.stroke-58"),sQuery(id+"F2.wireOp",EDGE,"fcba4419-a2ee-464f-be9d-58f11bf3418b.sketch_text.stroke-59"),sQuery(id+"F2.wireOp",EDGE,"fcba4419-a2ee-464f-be9d-58f11bf3418b.sketch_text.stroke-60"),sQuery(id+"F2.wireOp",EDGE,"fcba4419-a2ee-464f-be9d-58f11bf3418b.sketch_text.stroke-61"),sQuery(id+"F2.wireOp",EDGE,"fcba4419-a2ee-464f-be9d-58f11bf3418b.sketch_text.stroke-62"),sQuery(id+"F2.wireOp",EDGE,"fcba4419-a2ee-464f-be9d-58f11bf3418b.sketch_text.stroke-63"),sQuery(id+"F2.wireOp",EDGE,"fcba4419-a2ee-464f-be9d-58f11bf3418b.sketch_text.stroke-64"),sQuery(id+"F2.wireOp",EDGE,"fcba4419-a2ee-464f-be9d-58f11bf3418b.sketch_text.stroke-65"),sQuery(id+"F2.wireOp",EDGE,"fcba4419-a2ee-464f-be9d-58f11bf3418b.sketch_text.stroke-66"),sQuery(id+"F2.wireOp",EDGE,"fcba4419-a2ee-464f-be9d-58f11bf3418b.sketch_text.stroke-67"),sQuery(id+"F2.wireOp",EDGE,"fcba4419-a2ee-464f-be9d-58f11bf3418b.sketch_text.stroke-68"),sQuery(id+"F2.wireOp",EDGE,"fcba4419-a2ee-464f-be9d-58f11bf3418b.sketch_text.stroke-69"),sQuery(id+"F2.wireOp",EDGE,"fcba4419-a2ee-464f-be9d-58f11bf3418b.sketch_text.stroke-70"),sQuery(id+"F2.wireOp",EDGE,"fcba4419-a2ee-464f-be9d-58f11bf3418b.sketch_text.stroke-71"),sQuery(id+"F2.wireOp",EDGE,"fcba4419-a2ee-464f-be9d-58f11bf3418b.sketch_text.stroke-72"),sQuery(id+"F2.wireOp",EDGE,"fcba4419-a2ee-464f-be9d-58f11bf3418b.sketch_text.stroke-73"),sQuery(id+"F2.wireOp",EDGE,"fcba4419-a2ee-464f-be9d-58f11bf3418b.sketch_text.stroke-74"),sQuery(id+"F2.wireOp",EDGE,"fcba4419-a2ee-464f-be9d-58f11bf3418b.sketch_text.stroke-75"),sQuery(id+"F2.wireOp",EDGE,"fcba4419-a2ee-464f-be9d-58f11bf3418b.sketch_text.stroke-76"),sQuery(id+"F2.wireOp",EDGE,"fcba4419-a2ee-464f-be9d-58f11bf3418b.sketch_text.stroke-77"),sQuery(id+"F2.wireOp",EDGE,"fcba4419-a2ee-464f-be9d-58f11bf3418b.sketch_text.stroke-78"),sQuery(id+"F2.wireOp",EDGE,"fcba4419-a2ee-464f-be9d-58f11bf3418b.sketch_text.stroke-79"),sQuery(id+"F2.wireOp",EDGE,"fcba4419-a2ee-464f-be9d-58f11bf3418b.sketch_text.stroke-80"),sQuery(id+"F2.wireOp",EDGE,"fcba4419-a2ee-464f-be9d-58f11bf3418b.sketch_text.stroke-81"),sQuery(id+"F2.wireOp",EDGE,"fcba4419-a2ee-464f-be9d-58f11bf3418b.sketch_text.stroke-82"),sQuery(id+"F2.wireOp",EDGE,"fcba4419-a2ee-464f-be9d-58f11bf3418b.sketch_text.stroke-83"),sQuery(id+"F2.wireOp",EDGE,"fcba4419-a2ee-464f-be9d-58f11bf3418b.sketch_text.stroke-84"),sQuery(id+"F2.wireOp",EDGE,"fcba4419-a2ee-464f-be9d-58f11bf3418b.sketch_text.stroke-85"),sQuery(id+"F2.wireOp",EDGE,"fcba4419-a2ee-464f-be9d-58f11bf3418b.sketch_text.stroke-86"),sQuery(id+"F2.wireOp",EDGE,"fcba4419-a2ee-464f-be9d-58f11bf3418b.sketch_text.stroke-87"),sQuery(id+"F2.wireOp",EDGE,"fcba4419-a2ee-464f-be9d-58f11bf3418b.sketch_text.stroke-88"),sQuery(id+"F2.wireOp",EDGE,"fcba4419-a2ee-464f-be9d-58f11bf3418b.sketch_text.stroke-89"),sQuery(id+"F2.wireOp",EDGE,"fcba4419-a2ee-464f-be9d-58f11bf3418b.sketch_text.stroke-90"),sQuery(id+"F2.wireOp",EDGE,"fcba4419-a2ee-464f-be9d-58f11bf3418b.sketch_text.stroke-91"),sQuery(id+"F2.wireOp",EDGE,"fcba4419-a2ee-464f-be9d-58f11bf3418b.sketch_text.stroke-92"),sQuery(id+"F2.wireOp",EDGE,"fcba4419-a2ee-464f-be9d-58f11bf3418b.sketch_text.stroke-93"),sQuery(id+"F2.wireOp",EDGE,"fcba4419-a2ee-464f-be9d-58f11bf3418b.sketch_text.stroke-94"),sQuery(id+"F2.wireOp",EDGE,"fcba4419-a2ee-464f-be9d-58f11bf3418b.sketch_text.stroke-95"),sQuery(id+"F2.wireOp",EDGE,"fcba4419-a2ee-464f-be9d-58f11bf3418b.sketch_text.stroke-96"),sQuery(id+"F2.wireOp",EDGE,"fcba4419-a2ee-464f-be9d-58f11bf3418b.sketch_text.stroke-97"),sQuery(id+"F2.wireOp",EDGE,"fcba4419-a2ee-464f-be9d-58f11bf3418b.sketch_text.stroke-98"),sQuery(id+"F2.wireOp",EDGE,"fcba4419-a2ee-464f-be9d-58f11bf3418b.sketch_text.stroke-99"),sQuery(id+"F2.wireOp",EDGE,"fcba4419-a2ee-464f-be9d-58f11bf3418b.sketch_text.stroke-100"),sQuery(id+"F2.wireOp",EDGE,"fcba4419-a2ee-464f-be9d-58f11bf3418b.sketch_text.stroke-101"),sQuery(id+"F2.wireOp",EDGE,"fcba4419-a2ee-464f-be9d-58f11bf3418b.sketch_text.stroke-102"),sQuery(id+"F2.wireOp",EDGE,"fcba4419-a2ee-464f-be9d-58f11bf3418b.sketch_text.stroke-103"),sQuery(id+"F2.wireOp",EDGE,"fcba4419-a2ee-464f-be9d-58f11bf3418b.sketch_text.stroke-104"),sQuery(id+"F2.wireOp",EDGE,"fcba4419-a2ee-464f-be9d-58f11bf3418b.sketch_text.stroke-105"),sQuery(id+"F2.wireOp",EDGE,"fcba4419-a2ee-464f-be9d-58f11bf3418b.sketch_text.stroke-106"),sQuery(id+"F2.wireOp",EDGE,"fcba4419-a2ee-464f-be9d-58f11bf3418b.sketch_text.stroke-107"),sQuery(id+"F2.wireOp",EDGE,"fcba4419-a2ee-464f-be9d-58f11bf3418b.sketch_text.stroke-108"),sQuery(id+"F2.wireOp",EDGE,"fcba4419-a2ee-464f-be9d-58f11bf3418b.sketch_text.stroke-109"),sQuery(id+"F2.wireOp",EDGE,"fcba4419-a2ee-464f-be9d-58f11bf3418b.sketch_text.stroke-110"),sQuery(id+"F2.wireOp",EDGE,"fcba4419-a2ee-464f-be9d-58f11bf3418b.sketch_text.stroke-111"),sQuery(id+"F2.wireOp",EDGE,"fcba4419-a2ee-464f-be9d-58f11bf3418b.sketch_text.stroke-112"),sQuery(id+"F2.wireOp",EDGE,"fcba4419-a2ee-464f-be9d-58f11bf3418b.sketch_text.stroke-113"),sQuery(id+"F2.wireOp",EDGE,"fcba4419-a2ee-464f-be9d-58f11bf3418b.sketch_text.stroke-114"),sQuery(id+"F2.wireOp",EDGE,"fcba4419-a2ee-464f-be9d-58f11bf3418b.sketch_text.stroke-115"),sQuery(id+"F2.wireOp",EDGE,"fcba4419-a2ee-464f-be9d-58f11bf3418b.sketch_text.stroke-116"),sQuery(id+"F2.wireOp",EDGE,"fcba4419-a2ee-464f-be9d-58f11bf3418b.sketch_text.stroke-117"),sQuery(id+"F2.wireOp",EDGE,"fcba4419-a2ee-464f-be9d-58f11bf3418b.sketch_text.stroke-118"),sQuery(id+"F2.wireOp",EDGE,"fcba4419-a2ee-464f-be9d-58f11bf3418b.sketch_text.stroke-119"),sQuery(id+"F2.wireOp",EDGE,"fcba4419-a2ee-464f-be9d-58f11bf3418b.sketch_text.stroke-120"),sQuery(id+"F2.wireOp",EDGE,"fcba4419-a2ee-464f-be9d-58f11bf3418b.sketch_text.stroke-121"),sQuery(id+"F2.wireOp",EDGE,"fcba4419-a2ee-464f-be9d-58f11bf3418b.sketch_text.stroke-122"),sQuery(id+"F2.wireOp",EDGE,"fcba4419-a2ee-464f-be9d-58f11bf3418b.sketch_text.stroke-123"),sQuery(id+"F2.wireOp",EDGE,"fcba4419-a2ee-464f-be9d-58f11bf3418b.sketch_text.stroke-124"),sQuery(id+"F2.wireOp",EDGE,"fcba4419-a2ee-464f-be9d-58f11bf3418b.sketch_text.stroke-125"),sQuery(id+"F2.wireOp",EDGE,"fcba4419-a2ee-464f-be9d-58f11bf3418b.sketch_text.stroke-126"),sQuery(id+"F2.wireOp",EDGE,"fcba4419-a2ee-464f-be9d-58f11bf3418b.sketch_text.stroke-127"),sQuery(id+"F2.wireOp",EDGE,"fcba4419-a2ee-464f-be9d-58f11bf3418b.sketch_text.stroke-128"),sQuery(id+"F2.wireOp",EDGE,"fcba4419-a2ee-464f-be9d-58f11bf3418b.sketch_text.stroke-129"),sQuery(id+"F2.wireOp",EDGE,"fcba4419-a2ee-464f-be9d-58f11bf3418b.sketch_text.stroke-130"),sQuery(id+"F2.wireOp",EDGE,"fcba4419-a2ee-464f-be9d-58f11bf3418b.sketch_text.stroke-131"),sQuery(id+"F2.wireOp",EDGE,"fcba4419-a2ee-464f-be9d-58f11bf3418b.sketch_text.stroke-132"),sQuery(id+"F2.wireOp",EDGE,"fcba4419-a2ee-464f-be9d-58f11bf3418b.sketch_text.stroke-133"),sQuery(id+"F2.wireOp",EDGE,"fcba4419-a2ee-464f-be9d-58f11bf3418b.sketch_text.stroke-134"),sQuery(id+"F2.wireOp",EDGE,"fcba4419-a2ee-464f-be9d-58f11bf3418b.sketch_text.stroke-135"),sQuery(id+"F2.wireOp",EDGE,"fcba4419-a2ee-464f-be9d-58f11bf3418b.sketch_text.stroke-136"),sQuery(id+"F2.wireOp",EDGE,"fcba4419-a2ee-464f-be9d-58f11bf3418b.sketch_text.stroke-137"),sQuery(id+"F2.wireOp",EDGE,"fcba4419-a2ee-464f-be9d-58f11bf3418b.sketch_text.stroke-138"),sQuery(id+"F2.wireOp",EDGE,"fcba4419-a2ee-464f-be9d-58f11bf3418b.sketch_text.stroke-139"),sQuery(id+"F2.wireOp",EDGE,"fcba4419-a2ee-464f-be9d-58f11bf3418b.sketch_text.stroke-140"),sQuery(id+"F2.wireOp",EDGE,"fcba4419-a2ee-464f-be9d-58f11bf3418b.sketch_text.stroke-141"),sQuery(id+"F2.wireOp",EDGE,"fcba4419-a2ee-464f-be9d-58f11bf3418b.sketch_text.stroke-142"),sQuery(id+"F2.wireOp",EDGE,"fcba4419-a2ee-464f-be9d-58f11bf3418b.sketch_text.stroke-143"),sQuery(id+"F2.wireOp",EDGE,"fcba4419-a2ee-464f-be9d-58f11bf3418b.sketch_text.stroke-144"),sQuery(id+"F2.wireOp",EDGE,"fcba4419-a2ee-464f-be9d-58f11bf3418b.sketch_text.stroke-145"),sQuery(id+"F2.wireOp",EDGE,"fcba4419-a2ee-464f-be9d-58f11bf3418b.sketch_text.stroke-146"),sQuery(id+"F2.wireOp",EDGE,"fcba4419-a2ee-464f-be9d-58f11bf3418b.sketch_text.stroke-147"),sQuery(id+"F2.wireOp",EDGE,"fcba4419-a2ee-464f-be9d-58f11bf3418b.sketch_text.stroke-148"),sQuery(id+"F2.wireOp",EDGE,"fcba4419-a2ee-464f-be9d-58f11bf3418b.sketch_text.stroke-149"),sQuery(id+"F2.wireOp",EDGE,"fcba4419-a2ee-464f-be9d-58f11bf3418b.sketch_text.stroke-150"),sQuery(id+"F2.wireOp",EDGE,"fcba4419-a2ee-464f-be9d-58f11bf3418b.sketch_text.stroke-151"),sQuery(id+"F2.wireOp",EDGE,"fcba4419-a2ee-464f-be9d-58f11bf3418b.sketch_text.stroke-152"),sQuery(id+"F2.wireOp",EDGE,"fcba4419-a2ee-464f-be9d-58f11bf3418b.sketch_text.stroke-153"),sQuery(id+"F2.wireOp",EDGE,"fcba4419-a2ee-464f-be9d-58f11bf3418b.sketch_text.stroke-154"),sQuery(id+"F2.wireOp",EDGE,"fcba4419-a2ee-464f-be9d-58f11bf3418b.sketch_text.stroke-155"),sQuery(id+"F2.wireOp",EDGE,"fcba4419-a2ee-464f-be9d-58f11bf3418b.sketch_text.stroke-156"),sQuery(id+"F2.wireOp",EDGE,"fcba4419-a2ee-464f-be9d-58f11bf3418b.sketch_text.stroke-157"),sQuery(id+"F2.wireOp",EDGE,"fcba4419-a2ee-464f-be9d-58f11bf3418b.sketch_text.stroke-158"),sQuery(id+"F2.wireOp",EDGE,"fcba4419-a2ee-464f-be9d-58f11bf3418b.sketch_text.stroke-159"),sQuery(id+"F2.wireOp",EDGE,"fcba4419-a2ee-464f-be9d-58f11bf3418b.sketch_text.stroke-160"),sQuery(id+"F2.wireOp",EDGE,"fcba4419-a2ee-464f-be9d-58f11bf3418b.sketch_text.stroke-161"),sQuery(id+"F2.wireOp",EDGE,"fcba4419-a2ee-464f-be9d-58f11bf3418b.sketch_text.stroke-162"),sQuery(id+"F2.wireOp",EDGE,"fcba4419-a2ee-464f-be9d-58f11bf3418b.sketch_text.stroke-163"),sQuery(id+"F2.wireOp",EDGE,"fcba4419-a2ee-464f-be9d-58f11bf3418b.sketch_text.stroke-164"),sQuery(id+"F2.wireOp",EDGE,"fcba4419-a2ee-464f-be9d-58f11bf3418b.sketch_text.stroke-165"),sQuery(id+"F2.wireOp",EDGE,"fcba4419-a2ee-464f-be9d-58f11bf3418b.sketch_text.stroke-166"),sQuery(id+"F2.wireOp",EDGE,"fcba4419-a2ee-464f-be9d-58f11bf3418b.sketch_text.stroke-167"),sQuery(id+"F2.wireOp",EDGE,"fcba4419-a2ee-464f-be9d-58f11bf3418b.sketch_text.stroke-168"),sQuery(id+"F2.wireOp",EDGE,"fcba4419-a2ee-464f-be9d-58f11bf3418b.sketch_text.stroke-169"),sQuery(id+"F2.wireOp",EDGE,"fcba4419-a2ee-464f-be9d-58f11bf3418b.sketch_text.stroke-170"),sQuery(id+"F2.wireOp",EDGE,"fcba4419-a2ee-464f-be9d-58f11bf3418b.sketch_text.stroke-171"),sQuery(id+"F2.wireOp",EDGE,"fcba4419-a2ee-464f-be9d-58f11bf3418b.sketch_text.stroke-172"),sQuery(id+"F2.wireOp",EDGE,"fcba4419-a2ee-464f-be9d-58f11bf3418b.sketch_text.stroke-173"),sQuery(id+"FHMxAyK4CFUKdhS_1.wireOp",EDGE,"1cb9c079-ea9b-4899-8069-e0e3048e911d.sketch_text.stroke-0"),sQuery(id+"FHMxAyK4CFUKdhS_1.wireOp",EDGE,"1cb9c079-ea9b-4899-8069-e0e3048e911d.sketch_text.stroke-1"),sQuery(id+"FHMxAyK4CFUKdhS_1.wireOp",EDGE,"1cb9c079-ea9b-4899-8069-e0e3048e911d.sketch_text.stroke-2"),sQuery(id+"FHMxAyK4CFUKdhS_1.wireOp",EDGE,"1cb9c079-ea9b-4899-8069-e0e3048e911d.sketch_text.stroke-3"),sQuery(id+"FHMxAyK4CFUKdhS_1.wireOp",EDGE,"1cb9c079-ea9b-4899-8069-e0e3048e911d.sketch_text.stroke-4"),sQuery(id+"FHMxAyK4CFUKdhS_1.wireOp",EDGE,"1cb9c079-ea9b-4899-8069-e0e3048e911d.sketch_text.stroke-5"),sQuery(id+"FHMxAyK4CFUKdhS_1.wireOp",EDGE,"1cb9c079-ea9b-4899-8069-e0e3048e911d.sketch_text.stroke-6"),sQuery(id+"FHMxAyK4CFUKdhS_1.wireOp",EDGE,"1cb9c079-ea9b-4899-8069-e0e3048e911d.sketch_text.stroke-7"),sQuery(id+"FHMxAyK4CFUKdhS_1.wireOp",EDGE,"1cb9c079-ea9b-4899-8069-e0e3048e911d.sketch_text.stroke-8"),sQuery(id+"FHMxAyK4CFUKdhS_1.wireOp",EDGE,"1cb9c079-ea9b-4899-8069-e0e3048e911d.sketch_text.stroke-9"),sQuery(id+"FHMxAyK4CFUKdhS_1.wireOp",EDGE,"1cb9c079-ea9b-4899-8069-e0e3048e911d.sketch_text.stroke-10"),sQuery(id+"FHMxAyK4CFUKdhS_1.wireOp",EDGE,"1cb9c079-ea9b-4899-8069-e0e3048e911d.sketch_text.stroke-11"),sQuery(id+"FHMxAyK4CFUKdhS_1.wireOp",EDGE,"1cb9c079-ea9b-4899-8069-e0e3048e911d.sketch_text.stroke-12"),sQuery(id+"FHMxAyK4CFUKdhS_1.wireOp",EDGE,"1cb9c079-ea9b-4899-8069-e0e3048e911d.sketch_text.stroke-13"),sQuery(id+"FHMxAyK4CFUKdhS_1.wireOp",EDGE,"1cb9c079-ea9b-4899-8069-e0e3048e911d.sketch_text.stroke-14"),sQuery(id+"FHMxAyK4CFUKdhS_1.wireOp",EDGE,"1cb9c079-ea9b-4899-8069-e0e3048e911d.sketch_text.stroke-15"),sQuery(id+"FHMxAyK4CFUKdhS_1.wireOp",EDGE,"1cb9c079-ea9b-4899-8069-e0e3048e911d.sketch_text.stroke-16"),sQuery(id+"FHMxAyK4CFUKdhS_1.wireOp",EDGE,"1cb9c079-ea9b-4899-8069-e0e3048e911d.sketch_text.stroke-17"),sQuery(id+"FHMxAyK4CFUKdhS_1.wireOp",EDGE,"1cb9c079-ea9b-4899-8069-e0e3048e911d.sketch_text.stroke-18"),sQuery(id+"FHMxAyK4CFUKdhS_1.wireOp",EDGE,"1cb9c079-ea9b-4899-8069-e0e3048e911d.sketch_text.stroke-19"),sQuery(id+"FHMxAyK4CFUKdhS_1.wireOp",EDGE,"1cb9c079-ea9b-4899-8069-e0e3048e911d.sketch_text.stroke-20"),sQuery(id+"FHMxAyK4CFUKdhS_1.wireOp",EDGE,"1cb9c079-ea9b-4899-8069-e0e3048e911d.sketch_text.stroke-21"),sQuery(id+"FHMxAyK4CFUKdhS_1.wireOp",EDGE,"1cb9c079-ea9b-4899-8069-e0e3048e911d.sketch_text.stroke-22"),sQuery(id+"FHMxAyK4CFUKdhS_1.wireOp",EDGE,"1cb9c079-ea9b-4899-8069-e0e3048e911d.sketch_text.stroke-23"),sQuery(id+"FHMxAyK4CFUKdhS_1.wireOp",EDGE,"1cb9c079-ea9b-4899-8069-e0e3048e911d.sketch_text.stroke-24"),sQuery(id+"FHMxAyK4CFUKdhS_1.wireOp",EDGE,"1cb9c079-ea9b-4899-8069-e0e3048e911d.sketch_text.stroke-25"),sQuery(id+"FHMxAyK4CFUKdhS_1.wireOp",EDGE,"1cb9c079-ea9b-4899-8069-e0e3048e911d.sketch_text.stroke-26"),sQuery(id+"FHMxAyK4CFUKdhS_1.wireOp",EDGE,"1cb9c079-ea9b-4899-8069-e0e3048e911d.sketch_text.stroke-27"),sQuery(id+"FHMxAyK4CFUKdhS_1.wireOp",EDGE,"1cb9c079-ea9b-4899-8069-e0e3048e911d.sketch_text.stroke-28"),sQuery(id+"FHMxAyK4CFUKdhS_1.wireOp",EDGE,"1cb9c079-ea9b-4899-8069-e0e3048e911d.sketch_text.stroke-29"),sQuery(id+"FHMxAyK4CFUKdhS_1.wireOp",EDGE,"1cb9c079-ea9b-4899-8069-e0e3048e911d.sketch_text.stroke-30"),sQuery(id+"FHMxAyK4CFUKdhS_1.wireOp",EDGE,"1cb9c079-ea9b-4899-8069-e0e3048e911d.sketch_text.stroke-31"),sQuery(id+"FHMxAyK4CFUKdhS_1.wireOp",EDGE,"1cb9c079-ea9b-4899-8069-e0e3048e911d.sketch_text.stroke-32"),sQuery(id+"FHMxAyK4CFUKdhS_1.wireOp",EDGE,"1cb9c079-ea9b-4899-8069-e0e3048e911d.sketch_text.stroke-33"),sQuery(id+"FHMxAyK4CFUKdhS_1.wireOp",EDGE,"1cb9c079-ea9b-4899-8069-e0e3048e911d.sketch_text.stroke-34"),sQuery(id+"FHMxAyK4CFUKdhS_1.wireOp",EDGE,"1cb9c079-ea9b-4899-8069-e0e3048e911d.sketch_text.stroke-35"),sQuery(id+"FHMxAyK4CFUKdhS_1.wireOp",EDGE,"1cb9c079-ea9b-4899-8069-e0e3048e911d.sketch_text.stroke-36"),sQuery(id+"FHMxAyK4CFUKdhS_1.wireOp",EDGE,"1cb9c079-ea9b-4899-8069-e0e3048e911d.sketch_text.stroke-37"),sQuery(id+"FHMxAyK4CFUKdhS_1.wireOp",EDGE,"1cb9c079-ea9b-4899-8069-e0e3048e911d.sketch_text.stroke-38"),sQuery(id+"FHMxAyK4CFUKdhS_1.wireOp",EDGE,"1cb9c079-ea9b-4899-8069-e0e3048e911d.sketch_text.stroke-39"),sQuery(id+"FHMxAyK4CFUKdhS_1.wireOp",EDGE,"1cb9c079-ea9b-4899-8069-e0e3048e911d.sketch_text.stroke-40"),sQuery(id+"FHMxAyK4CFUKdhS_1.wireOp",EDGE,"1cb9c079-ea9b-4899-8069-e0e3048e911d.sketch_text.stroke-41"),sQuery(id+"FHMxAyK4CFUKdhS_1.wireOp",EDGE,"1cb9c079-ea9b-4899-8069-e0e3048e911d.sketch_text.stroke-42"),sQuery(id+"FHMxAyK4CFUKdhS_1.wireOp",EDGE,"1cb9c079-ea9b-4899-8069-e0e3048e911d.sketch_text.stroke-43"),sQuery(id+"FHMxAyK4CFUKdhS_1.wireOp",EDGE,"1cb9c079-ea9b-4899-8069-e0e3048e911d.sketch_text.stroke-44"),sQuery(id+"FHMxAyK4CFUKdhS_1.wireOp",EDGE,"1cb9c079-ea9b-4899-8069-e0e3048e911d.sketch_text.stroke-45"),sQuery(id+"FHMxAyK4CFUKdhS_1.wireOp",EDGE,"1cb9c079-ea9b-4899-8069-e0e3048e911d.sketch_text.stroke-46"),sQuery(id+"FHMxAyK4CFUKdhS_1.wireOp",EDGE,"1cb9c079-ea9b-4899-8069-e0e3048e911d.sketch_text.stroke-47"),sQuery(id+"FHMxAyK4CFUKdhS_1.wireOp",EDGE,"1cb9c079-ea9b-4899-8069-e0e3048e911d.sketch_text.stroke-48"),sQuery(id+"FHMxAyK4CFUKdhS_1.wireOp",EDGE,"1cb9c079-ea9b-4899-8069-e0e3048e911d.sketch_text.stroke-49"),sQuery(id+"FHMxAyK4CFUKdhS_1.wireOp",EDGE,"1cb9c079-ea9b-4899-8069-e0e3048e911d.sketch_text.stroke-50"),sQuery(id+"FHMxAyK4CFUKdhS_1.wireOp",EDGE,"1cb9c079-ea9b-4899-8069-e0e3048e911d.sketch_text.stroke-51"),sQuery(id+"FHMxAyK4CFUKdhS_1.wireOp",EDGE,"1cb9c079-ea9b-4899-8069-e0e3048e911d.sketch_text.stroke-52"),sQuery(id+"FHMxAyK4CFUKdhS_1.wireOp",EDGE,"1cb9c079-ea9b-4899-8069-e0e3048e911d.sketch_text.stroke-53"),sQuery(id+"FHMxAyK4CFUKdhS_1.wireOp",EDGE,"1cb9c079-ea9b-4899-8069-e0e3048e911d.sketch_text.stroke-54"),sQuery(id+"FHMxAyK4CFUKdhS_1.wireOp",EDGE,"1cb9c079-ea9b-4899-8069-e0e3048e911d.sketch_text.stroke-55"),sQuery(id+"FHMxAyK4CFUKdhS_1.wireOp",EDGE,"1cb9c079-ea9b-4899-8069-e0e3048e911d.sketch_text.stroke-56"),sQuery(id+"FHMxAyK4CFUKdhS_1.wireOp",EDGE,"1cb9c079-ea9b-4899-8069-e0e3048e911d.sketch_text.stroke-57"),sQuery(id+"FHMxAyK4CFUKdhS_1.wireOp",EDGE,"1cb9c079-ea9b-4899-8069-e0e3048e911d.sketch_text.stroke-58"),sQuery(id+"FHMxAyK4CFUKdhS_1.wireOp",EDGE,"1cb9c079-ea9b-4899-8069-e0e3048e911d.sketch_text.stroke-59"),sQuery(id+"FHMxAyK4CFUKdhS_1.wireOp",EDGE,"1cb9c079-ea9b-4899-8069-e0e3048e911d.sketch_text.stroke-60"),sQuery(id+"FHMxAyK4CFUKdhS_1.wireOp",EDGE,"1cb9c079-ea9b-4899-8069-e0e3048e911d.sketch_text.stroke-61"),sQuery(id+"FHMxAyK4CFUKdhS_1.wireOp",EDGE,"1cb9c079-ea9b-4899-8069-e0e3048e911d.sketch_text.stroke-62"),sQuery(id+"FHMxAyK4CFUKdhS_1.wireOp",EDGE,"1cb9c079-ea9b-4899-8069-e0e3048e911d.sketch_text.stroke-71"),sQuery(id+"FHMxAyK4CFUKdhS_1.wireOp",EDGE,"1cb9c079-ea9b-4899-8069-e0e3048e911d.sketch_text.stroke-72"),sQuery(id+"FHMxAyK4CFUKdhS_1.wireOp",EDGE,"1cb9c079-ea9b-4899-8069-e0e3048e911d.sketch_text.stroke-73"),sQuery(id+"FHMxAyK4CFUKdhS_1.wireOp",EDGE,"1cb9c079-ea9b-4899-8069-e0e3048e911d.sketch_text.stroke-74"),sQuery(id+"FHMxAyK4CFUKdhS_1.wireOp",EDGE,"1cb9c079-ea9b-4899-8069-e0e3048e911d.sketch_text.stroke-75"),sQuery(id+"FHMxAyK4CFUKdhS_1.wireOp",EDGE,"1cb9c079-ea9b-4899-8069-e0e3048e911d.sketch_text.stroke-76"),sQuery(id+"FHMxAyK4CFUKdhS_1.wireOp",EDGE,"1cb9c079-ea9b-4899-8069-e0e3048e911d.sketch_text.stroke-77"),sQuery(id+"FHMxAyK4CFUKdhS_1.wireOp",EDGE,"1cb9c079-ea9b-4899-8069-e0e3048e911d.sketch_text.stroke-78"),sQuery(id+"FHMxAyK4CFUKdhS_1.wireOp",EDGE,"1cb9c079-ea9b-4899-8069-e0e3048e911d.sketch_text.stroke-79"),sQuery(id+"FHMxAyK4CFUKdhS_1.wireOp",EDGE,"1cb9c079-ea9b-4899-8069-e0e3048e911d.sketch_text.stroke-80"),sQuery(id+"FHMxAyK4CFUKdhS_1.wireOp",EDGE,"1cb9c079-ea9b-4899-8069-e0e3048e911d.sketch_text.stroke-81"),sQuery(id+"FHMxAyK4CFUKdhS_1.wireOp",EDGE,"1cb9c079-ea9b-4899-8069-e0e3048e911d.sketch_text.stroke-82"),sQuery(id+"FHMxAyK4CFUKdhS_1.wireOp",EDGE,"1cb9c079-ea9b-4899-8069-e0e3048e911d.sketch_text.stroke-83"),sQuery(id+"FHMxAyK4CFUKdhS_1.wireOp",EDGE,"1cb9c079-ea9b-4899-8069-e0e3048e911d.sketch_text.stroke-84"),sQuery(id+"FHMxAyK4CFUKdhS_1.wireOp",EDGE,"1cb9c079-ea9b-4899-8069-e0e3048e911d.sketch_text.stroke-85"),sQuery(id+"FHMxAyK4CFUKdhS_1.wireOp",EDGE,"1cb9c079-ea9b-4899-8069-e0e3048e911d.sketch_text.stroke-86"),sQuery(id+"FHMxAyK4CFUKdhS_1.wireOp",EDGE,"1cb9c079-ea9b-4899-8069-e0e3048e911d.sketch_text.stroke-87"),sQuery(id+"FHMxAyK4CFUKdhS_1.wireOp",EDGE,"1cb9c079-ea9b-4899-8069-e0e3048e911d.sketch_text.stroke-88"),sQuery(id+"FHMxAyK4CFUKdhS_1.wireOp",EDGE,"1cb9c079-ea9b-4899-8069-e0e3048e911d.sketch_text.stroke-89"),sQuery(id+"FHMxAyK4CFUKdhS_1.wireOp",EDGE,"1cb9c079-ea9b-4899-8069-e0e3048e911d.sketch_text.stroke-90"),sQuery(id+"FHMxAyK4CFUKdhS_1.wireOp",EDGE,"1cb9c079-ea9b-4899-8069-e0e3048e911d.sketch_text.stroke-91"),sQuery(id+"FHMxAyK4CFUKdhS_1.wireOp",EDGE,"1cb9c079-ea9b-4899-8069-e0e3048e911d.sketch_text.stroke-92"),sQuery(id+"FHMxAyK4CFUKdhS_1.wireOp",EDGE,"1cb9c079-ea9b-4899-8069-e0e3048e911d.sketch_text.stroke-93"),sQuery(id+"FHMxAyK4CFUKdhS_1.wireOp",EDGE,"1cb9c079-ea9b-4899-8069-e0e3048e911d.sketch_text.stroke-94"),sQuery(id+"FHMxAyK4CFUKdhS_1.wireOp",EDGE,"1cb9c079-ea9b-4899-8069-e0e3048e911d.sketch_text.stroke-95"),sQuery(id+"FHMxAyK4CFUKdhS_1.wireOp",EDGE,"1cb9c079-ea9b-4899-8069-e0e3048e911d.sketch_text.stroke-96"),sQuery(id+"FHMxAyK4CFUKdhS_1.wireOp",EDGE,"1cb9c079-ea9b-4899-8069-e0e3048e911d.sketch_text.stroke-97"),sQuery(id+"FHMxAyK4CFUKdhS_1.wireOp",EDGE,"1cb9c079-ea9b-4899-8069-e0e3048e911d.sketch_text.stroke-103"),sQuery(id+"FHMxAyK4CFUKdhS_1.wireOp",EDGE,"1cb9c079-ea9b-4899-8069-e0e3048e911d.sketch_text.stroke-104"),sQuery(id+"FHMxAyK4CFUKdhS_1.wireOp",EDGE,"1cb9c079-ea9b-4899-8069-e0e3048e911d.sketch_text.stroke-105"),sQuery(id+"FHMxAyK4CFUKdhS_1.wireOp",EDGE,"1cb9c079-ea9b-4899-8069-e0e3048e911d.sketch_text.stroke-106"),sQuery(id+"FHMxAyK4CFUKdhS_1.wireOp",EDGE,"1cb9c079-ea9b-4899-8069-e0e3048e911d.sketch_text.stroke-107"),sQuery(id+"FHMxAyK4CFUKdhS_1.wireOp",EDGE,"1cb9c079-ea9b-4899-8069-e0e3048e911d.sketch_text.stroke-108"),sQuery(id+"FHMxAyK4CFUKdhS_1.wireOp",EDGE,"1cb9c079-ea9b-4899-8069-e0e3048e911d.sketch_text.stroke-109"),sQuery(id+"FHMxAyK4CFUKdhS_1.wireOp",EDGE,"1cb9c079-ea9b-4899-8069-e0e3048e911d.sketch_text.stroke-110"),sQuery(id+"FHMxAyK4CFUKdhS_1.wireOp",EDGE,"1cb9c079-ea9b-4899-8069-e0e3048e911d.sketch_text.stroke-111"),sQuery(id+"FHMxAyK4CFUKdhS_1.wireOp",EDGE,"1cb9c079-ea9b-4899-8069-e0e3048e911d.sketch_text.stroke-112"),sQuery(id+"FHMxAyK4CFUKdhS_1.wireOp",EDGE,"1cb9c079-ea9b-4899-8069-e0e3048e911d.sketch_text.stroke-113"),sQuery(id+"FHMxAyK4CFUKdhS_1.wireOp",EDGE,"1cb9c079-ea9b-4899-8069-e0e3048e911d.sketch_text.stroke-114"),sQuery(id+"FHMxAyK4CFUKdhS_1.wireOp",EDGE,"1cb9c079-ea9b-4899-8069-e0e3048e911d.sketch_text.stroke-115"),sQuery(id+"FHMxAyK4CFUKdhS_1.wireOp",EDGE,"1cb9c079-ea9b-4899-8069-e0e3048e911d.sketch_text.stroke-116"),sQuery(id+"FHMxAyK4CFUKdhS_1.wireOp",EDGE,"1cb9c079-ea9b-4899-8069-e0e3048e911d.sketch_text.stroke-117"),sQuery(id+"FHMxAyK4CFUKdhS_1.wireOp",EDGE,"1cb9c079-ea9b-4899-8069-e0e3048e911d.sketch_text.stroke-118"),sQuery(id+"FHMxAyK4CFUKdhS_1.wireOp",EDGE,"1cb9c079-ea9b-4899-8069-e0e3048e911d.sketch_text.stroke-119"),sQuery(id+"FHMxAyK4CFUKdhS_1.wireOp",EDGE,"1cb9c079-ea9b-4899-8069-e0e3048e911d.sketch_text.stroke-120"),sQuery(id+"FHMxAyK4CFUKdhS_1.wireOp",EDGE,"1cb9c079-ea9b-4899-8069-e0e3048e911d.sketch_text.stroke-121"),sQuery(id+"FHMxAyK4CFUKdhS_1.wireOp",EDGE,"1cb9c079-ea9b-4899-8069-e0e3048e911d.sketch_text.stroke-122"),sQuery(id+"FHMxAyK4CFUKdhS_1.wireOp",EDGE,"1cb9c079-ea9b-4899-8069-e0e3048e911d.sketch_text.stroke-123"),sQuery(id+"FHMxAyK4CFUKdhS_1.wireOp",EDGE,"1cb9c079-ea9b-4899-8069-e0e3048e911d.sketch_text.stroke-124"),sQuery(id+"FHMxAyK4CFUKdhS_1.wireOp",EDGE,"1cb9c079-ea9b-4899-8069-e0e3048e911d.sketch_text.stroke-125"),sQuery(id+"FHMxAyK4CFUKdhS_1.wireOp",EDGE,"1cb9c079-ea9b-4899-8069-e0e3048e911d.sketch_text.stroke-126"),sQuery(id+"FHMxAyK4CFUKdhS_1.wireOp",EDGE,"1cb9c079-ea9b-4899-8069-e0e3048e911d.sketch_text.stroke-127"),sQuery(id+"FHMxAyK4CFUKdhS_1.wireOp",EDGE,"1cb9c079-ea9b-4899-8069-e0e3048e911d.sketch_text.stroke-128"),sQuery(id+"FHMxAyK4CFUKdhS_1.wireOp",EDGE,"1cb9c079-ea9b-4899-8069-e0e3048e911d.sketch_text.stroke-129"),sQuery(id+"FHMxAyK4CFUKdhS_1.wireOp",EDGE,"1cb9c079-ea9b-4899-8069-e0e3048e911d.sketch_text.stroke-130"),sQuery(id+"FHMxAyK4CFUKdhS_1.wireOp",EDGE,"1cb9c079-ea9b-4899-8069-e0e3048e911d.sketch_text.stroke-131"),sQuery(id+"FHMxAyK4CFUKdhS_1.wireOp",EDGE,"1cb9c079-ea9b-4899-8069-e0e3048e911d.sketch_text.stroke-132"),sQuery(id+"FHMxAyK4CFUKdhS_1.wireOp",EDGE,"1cb9c079-ea9b-4899-8069-e0e3048e911d.sketch_text.stroke-133"),sQuery(id+"FHMxAyK4CFUKdhS_1.wireOp",EDGE,"1cb9c079-ea9b-4899-8069-e0e3048e911d.sketch_text.stroke-134"),sQuery(id+"FHMxAyK4CFUKdhS_1.wireOp",EDGE,"1cb9c079-ea9b-4899-8069-e0e3048e911d.sketch_text.stroke-135"),sQuery(id+"FHMxAyK4CFUKdhS_1.wireOp",EDGE,"1cb9c079-ea9b-4899-8069-e0e3048e911d.sketch_text.stroke-136"),sQuery(id+"FHMxAyK4CFUKdhS_1.wireOp",EDGE,"1cb9c079-ea9b-4899-8069-e0e3048e911d.sketch_text.stroke-137"),sQuery(id+"FHMxAyK4CFUKdhS_1.wireOp",EDGE,"1cb9c079-ea9b-4899-8069-e0e3048e911d.sketch_text.stroke-138"),sQuery(id+"FHMxAyK4CFUKdhS_1.wireOp",EDGE,"1cb9c079-ea9b-4899-8069-e0e3048e911d.sketch_text.stroke-139"),sQuery(id+"FHMxAyK4CFUKdhS_1.wireOp",EDGE,"1cb9c079-ea9b-4899-8069-e0e3048e911d.sketch_text.stroke-140"),sQuery(id+"FHMxAyK4CFUKdhS_1.wireOp",EDGE,"1cb9c079-ea9b-4899-8069-e0e3048e911d.sketch_text.stroke-141"),sQuery(id+"FHMxAyK4CFUKdhS_1.wireOp",EDGE,"1cb9c079-ea9b-4899-8069-e0e3048e911d.sketch_text.stroke-142"),sQuery(id+"FHMxAyK4CFUKdhS_1.wireOp",EDGE,"1cb9c079-ea9b-4899-8069-e0e3048e911d.sketch_text.stroke-143"),sQuery(id+"FHMxAyK4CFUKdhS_1.wireOp",EDGE,"1cb9c079-ea9b-4899-8069-e0e3048e911d.sketch_text.stroke-144"),sQuery(id+"FHMxAyK4CFUKdhS_1.wireOp",EDGE,"1cb9c079-ea9b-4899-8069-e0e3048e911d.sketch_text.stroke-145"),sQuery(id+"FHMxAyK4CFUKdhS_1.wireOp",EDGE,"1cb9c079-ea9b-4899-8069-e0e3048e911d.sketch_text.stroke-146"),sQuery(id+"FHMxAyK4CFUKdhS_1.wireOp",EDGE,"1cb9c079-ea9b-4899-8069-e0e3048e911d.sketch_text.stroke-147"),sQuery(id+"FHMxAyK4CFUKdhS_1.wireOp",EDGE,"1cb9c079-ea9b-4899-8069-e0e3048e911d.sketch_text.stroke-148"),sQuery(id+"FHMxAyK4CFUKdhS_1.wireOp",EDGE,"1cb9c079-ea9b-4899-8069-e0e3048e911d.sketch_text.stroke-149"),sQuery(id+"FHMxAyK4CFUKdhS_1.wireOp",EDGE,"1cb9c079-ea9b-4899-8069-e0e3048e911d.sketch_text.stroke-150"),sQuery(id+"FHMxAyK4CFUKdhS_1.wireOp",EDGE,"1cb9c079-ea9b-4899-8069-e0e3048e911d.sketch_text.stroke-151"),sQuery(id+"FHMxAyK4CFUKdhS_1.wireOp",EDGE,"1cb9c079-ea9b-4899-8069-e0e3048e911d.sketch_text.stroke-152"),sQuery(id+"FHMxAyK4CFUKdhS_1.wireOp",EDGE,"1cb9c079-ea9b-4899-8069-e0e3048e911d.sketch_text.stroke-153"),sQuery(id+"FHMxAyK4CFUKdhS_1.wireOp",EDGE,"1cb9c079-ea9b-4899-8069-e0e3048e911d.sketch_text.stroke-159"),sQuery(id+"FHMxAyK4CFUKdhS_1.wireOp",EDGE,"1cb9c079-ea9b-4899-8069-e0e3048e911d.sketch_text.stroke-160"),sQuery(id+"FHMxAyK4CFUKdhS_1.wireOp",EDGE,"1cb9c079-ea9b-4899-8069-e0e3048e911d.sketch_text.stroke-161"),sQuery(id+"FHMxAyK4CFUKdhS_1.wireOp",EDGE,"1cb9c079-ea9b-4899-8069-e0e3048e911d.sketch_text.stroke-162"),sQuery(id+"FHMxAyK4CFUKdhS_1.wireOp",EDGE,"1cb9c079-ea9b-4899-8069-e0e3048e911d.sketch_text.stroke-163"),sQuery(id+"FHMxAyK4CFUKdhS_1.wireOp",EDGE,"1cb9c079-ea9b-4899-8069-e0e3048e911d.sketch_text.stroke-164"),sQuery(id+"FHMxAyK4CFUKdhS_1.wireOp",EDGE,"1cb9c079-ea9b-4899-8069-e0e3048e911d.sketch_text.stroke-165"),sQuery(id+"FHMxAyK4CFUKdhS_1.wireOp",EDGE,"1cb9c079-ea9b-4899-8069-e0e3048e911d.sketch_text.stroke-166"),sQuery(id+"FHMxAyK4CFUKdhS_1.wireOp",EDGE,"1cb9c079-ea9b-4899-8069-e0e3048e911d.sketch_text.stroke-167"),sQuery(id+"FHMxAyK4CFUKdhS_1.wireOp",EDGE,"1cb9c079-ea9b-4899-8069-e0e3048e911d.sketch_text.stroke-168"),sQuery(id+"FHMxAyK4CFUKdhS_1.wireOp",EDGE,"1cb9c079-ea9b-4899-8069-e0e3048e911d.sketch_text.stroke-169"),sQuery(id+"FHMxAyK4CFUKdhS_1.wireOp",EDGE,"1cb9c079-ea9b-4899-8069-e0e3048e911d.sketch_text.stroke-170"),sQuery(id+"FHMxAyK4CFUKdhS_1.wireOp",EDGE,"1cb9c079-ea9b-4899-8069-e0e3048e911d.sketch_text.stroke-171"),sQuery(id+"FHMxAyK4CFUKdhS_1.wireOp",EDGE,"1cb9c079-ea9b-4899-8069-e0e3048e911d.sketch_text.stroke-172"),sQuery(id+"FHMxAyK4CFUKdhS_1.wireOp",EDGE,"1cb9c079-ea9b-4899-8069-e0e3048e911d.sketch_text.stroke-173"),sQuery(id+"FHMxAyK4CFUKdhS_1.wireOp",EDGE,"1cb9c079-ea9b-4899-8069-e0e3048e911d.sketch_text.stroke-174"),sQuery(id+"FHMxAyK4CFUKdhS_1.wireOp",EDGE,"1cb9c079-ea9b-4899-8069-e0e3048e911d.sketch_text.stroke-175"),sQuery(id+"FHMxAyK4CFUKdhS_1.wireOp",EDGE,"1cb9c079-ea9b-4899-8069-e0e3048e911d.sketch_text.stroke-176"),sQuery(id+"FHMxAyK4CFUKdhS_1.wireOp",EDGE,"1cb9c079-ea9b-4899-8069-e0e3048e911d.sketch_text.stroke-177"),sQuery(id+"FHMxAyK4CFUKdhS_1.wireOp",EDGE,"1cb9c079-ea9b-4899-8069-e0e3048e911d.sketch_text.stroke-178"),sQuery(id+"FHMxAyK4CFUKdhS_1.wireOp",EDGE,"1cb9c079-ea9b-4899-8069-e0e3048e911d.sketch_text.stroke-179"),sQuery(id+"FHMxAyK4CFUKdhS_1.wireOp",EDGE,"1cb9c079-ea9b-4899-8069-e0e3048e911d.sketch_text.stroke-180"),subQ2,sQuery(id+"F3.wireOp",EDGE,"6ee83ff3-586e-4dbe-aaea-af71240543bd")])],"isStart":true})]),OD(0.0)],"derivedFrom":makeQuery(id+"F1.opExtrude","CAP_EDGE",EDGE,{"disambiguationData":[OSD([subQ0])],"isStart":false})});}
            var Q6;
            {var subQ0=sQuery(id+"F3.wireOp",EDGE,"6ee83ff3-586e-4dbe-aaea-af71240543bd");var subQ1=sQuery(id+"F0.wireOp",EDGE,"E0.bottom");var subQ2=sQuery(id+"F0.wireOp",EDGE,"E0.right");Q6=makeQuery(id+"F4.boolean.opBoolean","SPLIT",EDGE,{"disambiguationData":[TD([makeQuery(id+"F1.opExtrude","SWEPT_FACE",FACE,{"disambiguationData":[OSD([subQ1])]}),makeQuery(id+"F1.opExtrude","CAP_FACE",FACE,{"disambiguationData":[OSD([subQ1,sQuery(id+"F0.wireOp",EDGE,"E0.top"),sQuery(id+"F0.wireOp",EDGE,"E0.left"),subQ2])],"isStart":false}),makeQuery(id+"F1.opExtrude","SWEPT_FACE",FACE,{"disambiguationData":[OSD([subQ2])]}),makeQuery(id+"F4.opExtrude","CAP_FACE",FACE,{"disambiguationData":[OSD([subQ1,sQuery(id+"F2.wireOp",EDGE,"fcba4419-a2ee-464f-be9d-58f11bf3418b.sketch_text.stroke-0"),sQuery(id+"F2.wireOp",EDGE,"fcba4419-a2ee-464f-be9d-58f11bf3418b.sketch_text.stroke-1"),sQuery(id+"F2.wireOp",EDGE,"fcba4419-a2ee-464f-be9d-58f11bf3418b.sketch_text.stroke-2"),sQuery(id+"F2.wireOp",EDGE,"fcba4419-a2ee-464f-be9d-58f11bf3418b.sketch_text.stroke-3"),sQuery(id+"F2.wireOp",EDGE,"fcba4419-a2ee-464f-be9d-58f11bf3418b.sketch_text.stroke-4"),sQuery(id+"F2.wireOp",EDGE,"fcba4419-a2ee-464f-be9d-58f11bf3418b.sketch_text.stroke-5"),sQuery(id+"F2.wireOp",EDGE,"fcba4419-a2ee-464f-be9d-58f11bf3418b.sketch_text.stroke-6"),sQuery(id+"F2.wireOp",EDGE,"fcba4419-a2ee-464f-be9d-58f11bf3418b.sketch_text.stroke-7"),sQuery(id+"F2.wireOp",EDGE,"fcba4419-a2ee-464f-be9d-58f11bf3418b.sketch_text.stroke-8"),sQuery(id+"F2.wireOp",EDGE,"fcba4419-a2ee-464f-be9d-58f11bf3418b.sketch_text.stroke-9"),sQuery(id+"F2.wireOp",EDGE,"fcba4419-a2ee-464f-be9d-58f11bf3418b.sketch_text.stroke-10"),sQuery(id+"F2.wireOp",EDGE,"fcba4419-a2ee-464f-be9d-58f11bf3418b.sketch_text.stroke-11"),sQuery(id+"F2.wireOp",EDGE,"fcba4419-a2ee-464f-be9d-58f11bf3418b.sketch_text.stroke-12"),sQuery(id+"F2.wireOp",EDGE,"fcba4419-a2ee-464f-be9d-58f11bf3418b.sketch_text.stroke-13"),sQuery(id+"F2.wireOp",EDGE,"fcba4419-a2ee-464f-be9d-58f11bf3418b.sketch_text.stroke-14"),sQuery(id+"F2.wireOp",EDGE,"fcba4419-a2ee-464f-be9d-58f11bf3418b.sketch_text.stroke-15"),sQuery(id+"F2.wireOp",EDGE,"fcba4419-a2ee-464f-be9d-58f11bf3418b.sketch_text.stroke-16"),sQuery(id+"F2.wireOp",EDGE,"fcba4419-a2ee-464f-be9d-58f11bf3418b.sketch_text.stroke-17"),sQuery(id+"F2.wireOp",EDGE,"fcba4419-a2ee-464f-be9d-58f11bf3418b.sketch_text.stroke-18"),sQuery(id+"F2.wireOp",EDGE,"fcba4419-a2ee-464f-be9d-58f11bf3418b.sketch_text.stroke-19"),sQuery(id+"F2.wireOp",EDGE,"fcba4419-a2ee-464f-be9d-58f11bf3418b.sketch_text.stroke-20"),sQuery(id+"F2.wireOp",EDGE,"fcba4419-a2ee-464f-be9d-58f11bf3418b.sketch_text.stroke-21"),sQuery(id+"F2.wireOp",EDGE,"fcba4419-a2ee-464f-be9d-58f11bf3418b.sketch_text.stroke-22"),sQuery(id+"F2.wireOp",EDGE,"fcba4419-a2ee-464f-be9d-58f11bf3418b.sketch_text.stroke-23"),sQuery(id+"F2.wireOp",EDGE,"fcba4419-a2ee-464f-be9d-58f11bf3418b.sketch_text.stroke-24"),sQuery(id+"F2.wireOp",EDGE,"fcba4419-a2ee-464f-be9d-58f11bf3418b.sketch_text.stroke-25"),sQuery(id+"F2.wireOp",EDGE,"fcba4419-a2ee-464f-be9d-58f11bf3418b.sketch_text.stroke-26"),sQuery(id+"F2.wireOp",EDGE,"fcba4419-a2ee-464f-be9d-58f11bf3418b.sketch_text.stroke-27"),sQuery(id+"F2.wireOp",EDGE,"fcba4419-a2ee-464f-be9d-58f11bf3418b.sketch_text.stroke-28"),sQuery(id+"F2.wireOp",EDGE,"fcba4419-a2ee-464f-be9d-58f11bf3418b.sketch_text.stroke-29"),sQuery(id+"F2.wireOp",EDGE,"fcba4419-a2ee-464f-be9d-58f11bf3418b.sketch_text.stroke-30"),sQuery(id+"F2.wireOp",EDGE,"fcba4419-a2ee-464f-be9d-58f11bf3418b.sketch_text.stroke-31"),sQuery(id+"F2.wireOp",EDGE,"fcba4419-a2ee-464f-be9d-58f11bf3418b.sketch_text.stroke-32"),sQuery(id+"F2.wireOp",EDGE,"fcba4419-a2ee-464f-be9d-58f11bf3418b.sketch_text.stroke-33"),sQuery(id+"F2.wireOp",EDGE,"fcba4419-a2ee-464f-be9d-58f11bf3418b.sketch_text.stroke-34"),sQuery(id+"F2.wireOp",EDGE,"fcba4419-a2ee-464f-be9d-58f11bf3418b.sketch_text.stroke-35"),sQuery(id+"F2.wireOp",EDGE,"fcba4419-a2ee-464f-be9d-58f11bf3418b.sketch_text.stroke-36"),sQuery(id+"F2.wireOp",EDGE,"fcba4419-a2ee-464f-be9d-58f11bf3418b.sketch_text.stroke-37"),sQuery(id+"F2.wireOp",EDGE,"fcba4419-a2ee-464f-be9d-58f11bf3418b.sketch_text.stroke-38"),sQuery(id+"F2.wireOp",EDGE,"fcba4419-a2ee-464f-be9d-58f11bf3418b.sketch_text.stroke-39"),sQuery(id+"F2.wireOp",EDGE,"fcba4419-a2ee-464f-be9d-58f11bf3418b.sketch_text.stroke-40"),sQuery(id+"F2.wireOp",EDGE,"fcba4419-a2ee-464f-be9d-58f11bf3418b.sketch_text.stroke-41"),sQuery(id+"F2.wireOp",EDGE,"fcba4419-a2ee-464f-be9d-58f11bf3418b.sketch_text.stroke-42"),sQuery(id+"F2.wireOp",EDGE,"fcba4419-a2ee-464f-be9d-58f11bf3418b.sketch_text.stroke-43"),sQuery(id+"F2.wireOp",EDGE,"fcba4419-a2ee-464f-be9d-58f11bf3418b.sketch_text.stroke-44"),sQuery(id+"F2.wireOp",EDGE,"fcba4419-a2ee-464f-be9d-58f11bf3418b.sketch_text.stroke-45"),sQuery(id+"F2.wireOp",EDGE,"fcba4419-a2ee-464f-be9d-58f11bf3418b.sketch_text.stroke-46"),sQuery(id+"F2.wireOp",EDGE,"fcba4419-a2ee-464f-be9d-58f11bf3418b.sketch_text.stroke-47"),sQuery(id+"F2.wireOp",EDGE,"fcba4419-a2ee-464f-be9d-58f11bf3418b.sketch_text.stroke-48"),sQuery(id+"F2.wireOp",EDGE,"fcba4419-a2ee-464f-be9d-58f11bf3418b.sketch_text.stroke-49"),sQuery(id+"F2.wireOp",EDGE,"fcba4419-a2ee-464f-be9d-58f11bf3418b.sketch_text.stroke-50"),sQuery(id+"F2.wireOp",EDGE,"fcba4419-a2ee-464f-be9d-58f11bf3418b.sketch_text.stroke-51"),sQuery(id+"F2.wireOp",EDGE,"fcba4419-a2ee-464f-be9d-58f11bf3418b.sketch_text.stroke-52"),sQuery(id+"F2.wireOp",EDGE,"fcba4419-a2ee-464f-be9d-58f11bf3418b.sketch_text.stroke-53"),sQuery(id+"F2.wireOp",EDGE,"fcba4419-a2ee-464f-be9d-58f11bf3418b.sketch_text.stroke-54"),sQuery(id+"F2.wireOp",EDGE,"fcba4419-a2ee-464f-be9d-58f11bf3418b.sketch_text.stroke-55"),sQuery(id+"F2.wireOp",EDGE,"fcba4419-a2ee-464f-be9d-58f11bf3418b.sketch_text.stroke-56"),sQuery(id+"F2.wireOp",EDGE,"fcba4419-a2ee-464f-be9d-58f11bf3418b.sketch_text.stroke-57"),sQuery(id+"F2.wireOp",EDGE,"fcba4419-a2ee-464f-be9d-58f11bf3418b.sketch_text.stroke-58"),sQuery(id+"F2.wireOp",EDGE,"fcba4419-a2ee-464f-be9d-58f11bf3418b.sketch_text.stroke-59"),sQuery(id+"F2.wireOp",EDGE,"fcba4419-a2ee-464f-be9d-58f11bf3418b.sketch_text.stroke-60"),sQuery(id+"F2.wireOp",EDGE,"fcba4419-a2ee-464f-be9d-58f11bf3418b.sketch_text.stroke-61"),sQuery(id+"F2.wireOp",EDGE,"fcba4419-a2ee-464f-be9d-58f11bf3418b.sketch_text.stroke-62"),sQuery(id+"F2.wireOp",EDGE,"fcba4419-a2ee-464f-be9d-58f11bf3418b.sketch_text.stroke-63"),sQuery(id+"F2.wireOp",EDGE,"fcba4419-a2ee-464f-be9d-58f11bf3418b.sketch_text.stroke-64"),sQuery(id+"F2.wireOp",EDGE,"fcba4419-a2ee-464f-be9d-58f11bf3418b.sketch_text.stroke-65"),sQuery(id+"F2.wireOp",EDGE,"fcba4419-a2ee-464f-be9d-58f11bf3418b.sketch_text.stroke-66"),sQuery(id+"F2.wireOp",EDGE,"fcba4419-a2ee-464f-be9d-58f11bf3418b.sketch_text.stroke-67"),sQuery(id+"F2.wireOp",EDGE,"fcba4419-a2ee-464f-be9d-58f11bf3418b.sketch_text.stroke-68"),sQuery(id+"F2.wireOp",EDGE,"fcba4419-a2ee-464f-be9d-58f11bf3418b.sketch_text.stroke-69"),sQuery(id+"F2.wireOp",EDGE,"fcba4419-a2ee-464f-be9d-58f11bf3418b.sketch_text.stroke-70"),sQuery(id+"F2.wireOp",EDGE,"fcba4419-a2ee-464f-be9d-58f11bf3418b.sketch_text.stroke-71"),sQuery(id+"F2.wireOp",EDGE,"fcba4419-a2ee-464f-be9d-58f11bf3418b.sketch_text.stroke-72"),sQuery(id+"F2.wireOp",EDGE,"fcba4419-a2ee-464f-be9d-58f11bf3418b.sketch_text.stroke-73"),sQuery(id+"F2.wireOp",EDGE,"fcba4419-a2ee-464f-be9d-58f11bf3418b.sketch_text.stroke-74"),sQuery(id+"F2.wireOp",EDGE,"fcba4419-a2ee-464f-be9d-58f11bf3418b.sketch_text.stroke-75"),sQuery(id+"F2.wireOp",EDGE,"fcba4419-a2ee-464f-be9d-58f11bf3418b.sketch_text.stroke-76"),sQuery(id+"F2.wireOp",EDGE,"fcba4419-a2ee-464f-be9d-58f11bf3418b.sketch_text.stroke-77"),sQuery(id+"F2.wireOp",EDGE,"fcba4419-a2ee-464f-be9d-58f11bf3418b.sketch_text.stroke-78"),sQuery(id+"F2.wireOp",EDGE,"fcba4419-a2ee-464f-be9d-58f11bf3418b.sketch_text.stroke-79"),sQuery(id+"F2.wireOp",EDGE,"fcba4419-a2ee-464f-be9d-58f11bf3418b.sketch_text.stroke-80"),sQuery(id+"F2.wireOp",EDGE,"fcba4419-a2ee-464f-be9d-58f11bf3418b.sketch_text.stroke-81"),sQuery(id+"F2.wireOp",EDGE,"fcba4419-a2ee-464f-be9d-58f11bf3418b.sketch_text.stroke-82"),sQuery(id+"F2.wireOp",EDGE,"fcba4419-a2ee-464f-be9d-58f11bf3418b.sketch_text.stroke-83"),sQuery(id+"F2.wireOp",EDGE,"fcba4419-a2ee-464f-be9d-58f11bf3418b.sketch_text.stroke-84"),sQuery(id+"F2.wireOp",EDGE,"fcba4419-a2ee-464f-be9d-58f11bf3418b.sketch_text.stroke-85"),sQuery(id+"F2.wireOp",EDGE,"fcba4419-a2ee-464f-be9d-58f11bf3418b.sketch_text.stroke-86"),sQuery(id+"F2.wireOp",EDGE,"fcba4419-a2ee-464f-be9d-58f11bf3418b.sketch_text.stroke-87"),sQuery(id+"F2.wireOp",EDGE,"fcba4419-a2ee-464f-be9d-58f11bf3418b.sketch_text.stroke-88"),sQuery(id+"F2.wireOp",EDGE,"fcba4419-a2ee-464f-be9d-58f11bf3418b.sketch_text.stroke-89"),sQuery(id+"F2.wireOp",EDGE,"fcba4419-a2ee-464f-be9d-58f11bf3418b.sketch_text.stroke-90"),sQuery(id+"F2.wireOp",EDGE,"fcba4419-a2ee-464f-be9d-58f11bf3418b.sketch_text.stroke-91"),sQuery(id+"F2.wireOp",EDGE,"fcba4419-a2ee-464f-be9d-58f11bf3418b.sketch_text.stroke-92"),sQuery(id+"F2.wireOp",EDGE,"fcba4419-a2ee-464f-be9d-58f11bf3418b.sketch_text.stroke-93"),sQuery(id+"F2.wireOp",EDGE,"fcba4419-a2ee-464f-be9d-58f11bf3418b.sketch_text.stroke-94"),sQuery(id+"F2.wireOp",EDGE,"fcba4419-a2ee-464f-be9d-58f11bf3418b.sketch_text.stroke-95"),sQuery(id+"F2.wireOp",EDGE,"fcba4419-a2ee-464f-be9d-58f11bf3418b.sketch_text.stroke-96"),sQuery(id+"F2.wireOp",EDGE,"fcba4419-a2ee-464f-be9d-58f11bf3418b.sketch_text.stroke-97"),sQuery(id+"F2.wireOp",EDGE,"fcba4419-a2ee-464f-be9d-58f11bf3418b.sketch_text.stroke-98"),sQuery(id+"F2.wireOp",EDGE,"fcba4419-a2ee-464f-be9d-58f11bf3418b.sketch_text.stroke-99"),sQuery(id+"F2.wireOp",EDGE,"fcba4419-a2ee-464f-be9d-58f11bf3418b.sketch_text.stroke-100"),sQuery(id+"F2.wireOp",EDGE,"fcba4419-a2ee-464f-be9d-58f11bf3418b.sketch_text.stroke-101"),sQuery(id+"F2.wireOp",EDGE,"fcba4419-a2ee-464f-be9d-58f11bf3418b.sketch_text.stroke-102"),sQuery(id+"F2.wireOp",EDGE,"fcba4419-a2ee-464f-be9d-58f11bf3418b.sketch_text.stroke-103"),sQuery(id+"F2.wireOp",EDGE,"fcba4419-a2ee-464f-be9d-58f11bf3418b.sketch_text.stroke-104"),sQuery(id+"F2.wireOp",EDGE,"fcba4419-a2ee-464f-be9d-58f11bf3418b.sketch_text.stroke-105"),sQuery(id+"F2.wireOp",EDGE,"fcba4419-a2ee-464f-be9d-58f11bf3418b.sketch_text.stroke-106"),sQuery(id+"F2.wireOp",EDGE,"fcba4419-a2ee-464f-be9d-58f11bf3418b.sketch_text.stroke-107"),sQuery(id+"F2.wireOp",EDGE,"fcba4419-a2ee-464f-be9d-58f11bf3418b.sketch_text.stroke-108"),sQuery(id+"F2.wireOp",EDGE,"fcba4419-a2ee-464f-be9d-58f11bf3418b.sketch_text.stroke-109"),sQuery(id+"F2.wireOp",EDGE,"fcba4419-a2ee-464f-be9d-58f11bf3418b.sketch_text.stroke-110"),sQuery(id+"F2.wireOp",EDGE,"fcba4419-a2ee-464f-be9d-58f11bf3418b.sketch_text.stroke-111"),sQuery(id+"F2.wireOp",EDGE,"fcba4419-a2ee-464f-be9d-58f11bf3418b.sketch_text.stroke-112"),sQuery(id+"F2.wireOp",EDGE,"fcba4419-a2ee-464f-be9d-58f11bf3418b.sketch_text.stroke-113"),sQuery(id+"F2.wireOp",EDGE,"fcba4419-a2ee-464f-be9d-58f11bf3418b.sketch_text.stroke-114"),sQuery(id+"F2.wireOp",EDGE,"fcba4419-a2ee-464f-be9d-58f11bf3418b.sketch_text.stroke-115"),sQuery(id+"F2.wireOp",EDGE,"fcba4419-a2ee-464f-be9d-58f11bf3418b.sketch_text.stroke-116"),sQuery(id+"F2.wireOp",EDGE,"fcba4419-a2ee-464f-be9d-58f11bf3418b.sketch_text.stroke-117"),sQuery(id+"F2.wireOp",EDGE,"fcba4419-a2ee-464f-be9d-58f11bf3418b.sketch_text.stroke-118"),sQuery(id+"F2.wireOp",EDGE,"fcba4419-a2ee-464f-be9d-58f11bf3418b.sketch_text.stroke-119"),sQuery(id+"F2.wireOp",EDGE,"fcba4419-a2ee-464f-be9d-58f11bf3418b.sketch_text.stroke-120"),sQuery(id+"F2.wireOp",EDGE,"fcba4419-a2ee-464f-be9d-58f11bf3418b.sketch_text.stroke-121"),sQuery(id+"F2.wireOp",EDGE,"fcba4419-a2ee-464f-be9d-58f11bf3418b.sketch_text.stroke-122"),sQuery(id+"F2.wireOp",EDGE,"fcba4419-a2ee-464f-be9d-58f11bf3418b.sketch_text.stroke-123"),sQuery(id+"F2.wireOp",EDGE,"fcba4419-a2ee-464f-be9d-58f11bf3418b.sketch_text.stroke-124"),sQuery(id+"F2.wireOp",EDGE,"fcba4419-a2ee-464f-be9d-58f11bf3418b.sketch_text.stroke-125"),sQuery(id+"F2.wireOp",EDGE,"fcba4419-a2ee-464f-be9d-58f11bf3418b.sketch_text.stroke-126"),sQuery(id+"F2.wireOp",EDGE,"fcba4419-a2ee-464f-be9d-58f11bf3418b.sketch_text.stroke-127"),sQuery(id+"F2.wireOp",EDGE,"fcba4419-a2ee-464f-be9d-58f11bf3418b.sketch_text.stroke-128"),sQuery(id+"F2.wireOp",EDGE,"fcba4419-a2ee-464f-be9d-58f11bf3418b.sketch_text.stroke-129"),sQuery(id+"F2.wireOp",EDGE,"fcba4419-a2ee-464f-be9d-58f11bf3418b.sketch_text.stroke-130"),sQuery(id+"F2.wireOp",EDGE,"fcba4419-a2ee-464f-be9d-58f11bf3418b.sketch_text.stroke-131"),sQuery(id+"F2.wireOp",EDGE,"fcba4419-a2ee-464f-be9d-58f11bf3418b.sketch_text.stroke-132"),sQuery(id+"F2.wireOp",EDGE,"fcba4419-a2ee-464f-be9d-58f11bf3418b.sketch_text.stroke-133"),sQuery(id+"F2.wireOp",EDGE,"fcba4419-a2ee-464f-be9d-58f11bf3418b.sketch_text.stroke-134"),sQuery(id+"F2.wireOp",EDGE,"fcba4419-a2ee-464f-be9d-58f11bf3418b.sketch_text.stroke-135"),sQuery(id+"F2.wireOp",EDGE,"fcba4419-a2ee-464f-be9d-58f11bf3418b.sketch_text.stroke-136"),sQuery(id+"F2.wireOp",EDGE,"fcba4419-a2ee-464f-be9d-58f11bf3418b.sketch_text.stroke-137"),sQuery(id+"F2.wireOp",EDGE,"fcba4419-a2ee-464f-be9d-58f11bf3418b.sketch_text.stroke-138"),sQuery(id+"F2.wireOp",EDGE,"fcba4419-a2ee-464f-be9d-58f11bf3418b.sketch_text.stroke-139"),sQuery(id+"F2.wireOp",EDGE,"fcba4419-a2ee-464f-be9d-58f11bf3418b.sketch_text.stroke-140"),sQuery(id+"F2.wireOp",EDGE,"fcba4419-a2ee-464f-be9d-58f11bf3418b.sketch_text.stroke-141"),sQuery(id+"F2.wireOp",EDGE,"fcba4419-a2ee-464f-be9d-58f11bf3418b.sketch_text.stroke-142"),sQuery(id+"F2.wireOp",EDGE,"fcba4419-a2ee-464f-be9d-58f11bf3418b.sketch_text.stroke-143"),sQuery(id+"F2.wireOp",EDGE,"fcba4419-a2ee-464f-be9d-58f11bf3418b.sketch_text.stroke-144"),sQuery(id+"F2.wireOp",EDGE,"fcba4419-a2ee-464f-be9d-58f11bf3418b.sketch_text.stroke-145"),sQuery(id+"F2.wireOp",EDGE,"fcba4419-a2ee-464f-be9d-58f11bf3418b.sketch_text.stroke-146"),sQuery(id+"F2.wireOp",EDGE,"fcba4419-a2ee-464f-be9d-58f11bf3418b.sketch_text.stroke-147"),sQuery(id+"F2.wireOp",EDGE,"fcba4419-a2ee-464f-be9d-58f11bf3418b.sketch_text.stroke-148"),sQuery(id+"F2.wireOp",EDGE,"fcba4419-a2ee-464f-be9d-58f11bf3418b.sketch_text.stroke-149"),sQuery(id+"F2.wireOp",EDGE,"fcba4419-a2ee-464f-be9d-58f11bf3418b.sketch_text.stroke-150"),sQuery(id+"F2.wireOp",EDGE,"fcba4419-a2ee-464f-be9d-58f11bf3418b.sketch_text.stroke-151"),sQuery(id+"F2.wireOp",EDGE,"fcba4419-a2ee-464f-be9d-58f11bf3418b.sketch_text.stroke-152"),sQuery(id+"F2.wireOp",EDGE,"fcba4419-a2ee-464f-be9d-58f11bf3418b.sketch_text.stroke-153"),sQuery(id+"F2.wireOp",EDGE,"fcba4419-a2ee-464f-be9d-58f11bf3418b.sketch_text.stroke-154"),sQuery(id+"F2.wireOp",EDGE,"fcba4419-a2ee-464f-be9d-58f11bf3418b.sketch_text.stroke-155"),sQuery(id+"F2.wireOp",EDGE,"fcba4419-a2ee-464f-be9d-58f11bf3418b.sketch_text.stroke-156"),sQuery(id+"F2.wireOp",EDGE,"fcba4419-a2ee-464f-be9d-58f11bf3418b.sketch_text.stroke-157"),sQuery(id+"F2.wireOp",EDGE,"fcba4419-a2ee-464f-be9d-58f11bf3418b.sketch_text.stroke-158"),sQuery(id+"F2.wireOp",EDGE,"fcba4419-a2ee-464f-be9d-58f11bf3418b.sketch_text.stroke-159"),sQuery(id+"F2.wireOp",EDGE,"fcba4419-a2ee-464f-be9d-58f11bf3418b.sketch_text.stroke-160"),sQuery(id+"F2.wireOp",EDGE,"fcba4419-a2ee-464f-be9d-58f11bf3418b.sketch_text.stroke-161"),sQuery(id+"F2.wireOp",EDGE,"fcba4419-a2ee-464f-be9d-58f11bf3418b.sketch_text.stroke-162"),sQuery(id+"F2.wireOp",EDGE,"fcba4419-a2ee-464f-be9d-58f11bf3418b.sketch_text.stroke-163"),sQuery(id+"F2.wireOp",EDGE,"fcba4419-a2ee-464f-be9d-58f11bf3418b.sketch_text.stroke-164"),sQuery(id+"F2.wireOp",EDGE,"fcba4419-a2ee-464f-be9d-58f11bf3418b.sketch_text.stroke-165"),sQuery(id+"F2.wireOp",EDGE,"fcba4419-a2ee-464f-be9d-58f11bf3418b.sketch_text.stroke-166"),sQuery(id+"F2.wireOp",EDGE,"fcba4419-a2ee-464f-be9d-58f11bf3418b.sketch_text.stroke-167"),sQuery(id+"F2.wireOp",EDGE,"fcba4419-a2ee-464f-be9d-58f11bf3418b.sketch_text.stroke-168"),sQuery(id+"F2.wireOp",EDGE,"fcba4419-a2ee-464f-be9d-58f11bf3418b.sketch_text.stroke-169"),sQuery(id+"F2.wireOp",EDGE,"fcba4419-a2ee-464f-be9d-58f11bf3418b.sketch_text.stroke-170"),sQuery(id+"F2.wireOp",EDGE,"fcba4419-a2ee-464f-be9d-58f11bf3418b.sketch_text.stroke-171"),sQuery(id+"F2.wireOp",EDGE,"fcba4419-a2ee-464f-be9d-58f11bf3418b.sketch_text.stroke-172"),sQuery(id+"F2.wireOp",EDGE,"fcba4419-a2ee-464f-be9d-58f11bf3418b.sketch_text.stroke-173"),sQuery(id+"FHMxAyK4CFUKdhS_1.wireOp",EDGE,"1cb9c079-ea9b-4899-8069-e0e3048e911d.sketch_text.stroke-0"),sQuery(id+"FHMxAyK4CFUKdhS_1.wireOp",EDGE,"1cb9c079-ea9b-4899-8069-e0e3048e911d.sketch_text.stroke-1"),sQuery(id+"FHMxAyK4CFUKdhS_1.wireOp",EDGE,"1cb9c079-ea9b-4899-8069-e0e3048e911d.sketch_text.stroke-2"),sQuery(id+"FHMxAyK4CFUKdhS_1.wireOp",EDGE,"1cb9c079-ea9b-4899-8069-e0e3048e911d.sketch_text.stroke-3"),sQuery(id+"FHMxAyK4CFUKdhS_1.wireOp",EDGE,"1cb9c079-ea9b-4899-8069-e0e3048e911d.sketch_text.stroke-4"),sQuery(id+"FHMxAyK4CFUKdhS_1.wireOp",EDGE,"1cb9c079-ea9b-4899-8069-e0e3048e911d.sketch_text.stroke-5"),sQuery(id+"FHMxAyK4CFUKdhS_1.wireOp",EDGE,"1cb9c079-ea9b-4899-8069-e0e3048e911d.sketch_text.stroke-6"),sQuery(id+"FHMxAyK4CFUKdhS_1.wireOp",EDGE,"1cb9c079-ea9b-4899-8069-e0e3048e911d.sketch_text.stroke-7"),sQuery(id+"FHMxAyK4CFUKdhS_1.wireOp",EDGE,"1cb9c079-ea9b-4899-8069-e0e3048e911d.sketch_text.stroke-8"),sQuery(id+"FHMxAyK4CFUKdhS_1.wireOp",EDGE,"1cb9c079-ea9b-4899-8069-e0e3048e911d.sketch_text.stroke-9"),sQuery(id+"FHMxAyK4CFUKdhS_1.wireOp",EDGE,"1cb9c079-ea9b-4899-8069-e0e3048e911d.sketch_text.stroke-10"),sQuery(id+"FHMxAyK4CFUKdhS_1.wireOp",EDGE,"1cb9c079-ea9b-4899-8069-e0e3048e911d.sketch_text.stroke-11"),sQuery(id+"FHMxAyK4CFUKdhS_1.wireOp",EDGE,"1cb9c079-ea9b-4899-8069-e0e3048e911d.sketch_text.stroke-12"),sQuery(id+"FHMxAyK4CFUKdhS_1.wireOp",EDGE,"1cb9c079-ea9b-4899-8069-e0e3048e911d.sketch_text.stroke-13"),sQuery(id+"FHMxAyK4CFUKdhS_1.wireOp",EDGE,"1cb9c079-ea9b-4899-8069-e0e3048e911d.sketch_text.stroke-14"),sQuery(id+"FHMxAyK4CFUKdhS_1.wireOp",EDGE,"1cb9c079-ea9b-4899-8069-e0e3048e911d.sketch_text.stroke-15"),sQuery(id+"FHMxAyK4CFUKdhS_1.wireOp",EDGE,"1cb9c079-ea9b-4899-8069-e0e3048e911d.sketch_text.stroke-16"),sQuery(id+"FHMxAyK4CFUKdhS_1.wireOp",EDGE,"1cb9c079-ea9b-4899-8069-e0e3048e911d.sketch_text.stroke-17"),sQuery(id+"FHMxAyK4CFUKdhS_1.wireOp",EDGE,"1cb9c079-ea9b-4899-8069-e0e3048e911d.sketch_text.stroke-18"),sQuery(id+"FHMxAyK4CFUKdhS_1.wireOp",EDGE,"1cb9c079-ea9b-4899-8069-e0e3048e911d.sketch_text.stroke-19"),sQuery(id+"FHMxAyK4CFUKdhS_1.wireOp",EDGE,"1cb9c079-ea9b-4899-8069-e0e3048e911d.sketch_text.stroke-20"),sQuery(id+"FHMxAyK4CFUKdhS_1.wireOp",EDGE,"1cb9c079-ea9b-4899-8069-e0e3048e911d.sketch_text.stroke-21"),sQuery(id+"FHMxAyK4CFUKdhS_1.wireOp",EDGE,"1cb9c079-ea9b-4899-8069-e0e3048e911d.sketch_text.stroke-22"),sQuery(id+"FHMxAyK4CFUKdhS_1.wireOp",EDGE,"1cb9c079-ea9b-4899-8069-e0e3048e911d.sketch_text.stroke-23"),sQuery(id+"FHMxAyK4CFUKdhS_1.wireOp",EDGE,"1cb9c079-ea9b-4899-8069-e0e3048e911d.sketch_text.stroke-24"),sQuery(id+"FHMxAyK4CFUKdhS_1.wireOp",EDGE,"1cb9c079-ea9b-4899-8069-e0e3048e911d.sketch_text.stroke-25"),sQuery(id+"FHMxAyK4CFUKdhS_1.wireOp",EDGE,"1cb9c079-ea9b-4899-8069-e0e3048e911d.sketch_text.stroke-26"),sQuery(id+"FHMxAyK4CFUKdhS_1.wireOp",EDGE,"1cb9c079-ea9b-4899-8069-e0e3048e911d.sketch_text.stroke-27"),sQuery(id+"FHMxAyK4CFUKdhS_1.wireOp",EDGE,"1cb9c079-ea9b-4899-8069-e0e3048e911d.sketch_text.stroke-28"),sQuery(id+"FHMxAyK4CFUKdhS_1.wireOp",EDGE,"1cb9c079-ea9b-4899-8069-e0e3048e911d.sketch_text.stroke-29"),sQuery(id+"FHMxAyK4CFUKdhS_1.wireOp",EDGE,"1cb9c079-ea9b-4899-8069-e0e3048e911d.sketch_text.stroke-30"),sQuery(id+"FHMxAyK4CFUKdhS_1.wireOp",EDGE,"1cb9c079-ea9b-4899-8069-e0e3048e911d.sketch_text.stroke-31"),sQuery(id+"FHMxAyK4CFUKdhS_1.wireOp",EDGE,"1cb9c079-ea9b-4899-8069-e0e3048e911d.sketch_text.stroke-32"),sQuery(id+"FHMxAyK4CFUKdhS_1.wireOp",EDGE,"1cb9c079-ea9b-4899-8069-e0e3048e911d.sketch_text.stroke-33"),sQuery(id+"FHMxAyK4CFUKdhS_1.wireOp",EDGE,"1cb9c079-ea9b-4899-8069-e0e3048e911d.sketch_text.stroke-34"),sQuery(id+"FHMxAyK4CFUKdhS_1.wireOp",EDGE,"1cb9c079-ea9b-4899-8069-e0e3048e911d.sketch_text.stroke-35"),sQuery(id+"FHMxAyK4CFUKdhS_1.wireOp",EDGE,"1cb9c079-ea9b-4899-8069-e0e3048e911d.sketch_text.stroke-36"),sQuery(id+"FHMxAyK4CFUKdhS_1.wireOp",EDGE,"1cb9c079-ea9b-4899-8069-e0e3048e911d.sketch_text.stroke-37"),sQuery(id+"FHMxAyK4CFUKdhS_1.wireOp",EDGE,"1cb9c079-ea9b-4899-8069-e0e3048e911d.sketch_text.stroke-38"),sQuery(id+"FHMxAyK4CFUKdhS_1.wireOp",EDGE,"1cb9c079-ea9b-4899-8069-e0e3048e911d.sketch_text.stroke-39"),sQuery(id+"FHMxAyK4CFUKdhS_1.wireOp",EDGE,"1cb9c079-ea9b-4899-8069-e0e3048e911d.sketch_text.stroke-40"),sQuery(id+"FHMxAyK4CFUKdhS_1.wireOp",EDGE,"1cb9c079-ea9b-4899-8069-e0e3048e911d.sketch_text.stroke-41"),sQuery(id+"FHMxAyK4CFUKdhS_1.wireOp",EDGE,"1cb9c079-ea9b-4899-8069-e0e3048e911d.sketch_text.stroke-42"),sQuery(id+"FHMxAyK4CFUKdhS_1.wireOp",EDGE,"1cb9c079-ea9b-4899-8069-e0e3048e911d.sketch_text.stroke-43"),sQuery(id+"FHMxAyK4CFUKdhS_1.wireOp",EDGE,"1cb9c079-ea9b-4899-8069-e0e3048e911d.sketch_text.stroke-44"),sQuery(id+"FHMxAyK4CFUKdhS_1.wireOp",EDGE,"1cb9c079-ea9b-4899-8069-e0e3048e911d.sketch_text.stroke-45"),sQuery(id+"FHMxAyK4CFUKdhS_1.wireOp",EDGE,"1cb9c079-ea9b-4899-8069-e0e3048e911d.sketch_text.stroke-46"),sQuery(id+"FHMxAyK4CFUKdhS_1.wireOp",EDGE,"1cb9c079-ea9b-4899-8069-e0e3048e911d.sketch_text.stroke-47"),sQuery(id+"FHMxAyK4CFUKdhS_1.wireOp",EDGE,"1cb9c079-ea9b-4899-8069-e0e3048e911d.sketch_text.stroke-48"),sQuery(id+"FHMxAyK4CFUKdhS_1.wireOp",EDGE,"1cb9c079-ea9b-4899-8069-e0e3048e911d.sketch_text.stroke-49"),sQuery(id+"FHMxAyK4CFUKdhS_1.wireOp",EDGE,"1cb9c079-ea9b-4899-8069-e0e3048e911d.sketch_text.stroke-50"),sQuery(id+"FHMxAyK4CFUKdhS_1.wireOp",EDGE,"1cb9c079-ea9b-4899-8069-e0e3048e911d.sketch_text.stroke-51"),sQuery(id+"FHMxAyK4CFUKdhS_1.wireOp",EDGE,"1cb9c079-ea9b-4899-8069-e0e3048e911d.sketch_text.stroke-52"),sQuery(id+"FHMxAyK4CFUKdhS_1.wireOp",EDGE,"1cb9c079-ea9b-4899-8069-e0e3048e911d.sketch_text.stroke-53"),sQuery(id+"FHMxAyK4CFUKdhS_1.wireOp",EDGE,"1cb9c079-ea9b-4899-8069-e0e3048e911d.sketch_text.stroke-54"),sQuery(id+"FHMxAyK4CFUKdhS_1.wireOp",EDGE,"1cb9c079-ea9b-4899-8069-e0e3048e911d.sketch_text.stroke-55"),sQuery(id+"FHMxAyK4CFUKdhS_1.wireOp",EDGE,"1cb9c079-ea9b-4899-8069-e0e3048e911d.sketch_text.stroke-56"),sQuery(id+"FHMxAyK4CFUKdhS_1.wireOp",EDGE,"1cb9c079-ea9b-4899-8069-e0e3048e911d.sketch_text.stroke-57"),sQuery(id+"FHMxAyK4CFUKdhS_1.wireOp",EDGE,"1cb9c079-ea9b-4899-8069-e0e3048e911d.sketch_text.stroke-58"),sQuery(id+"FHMxAyK4CFUKdhS_1.wireOp",EDGE,"1cb9c079-ea9b-4899-8069-e0e3048e911d.sketch_text.stroke-59"),sQuery(id+"FHMxAyK4CFUKdhS_1.wireOp",EDGE,"1cb9c079-ea9b-4899-8069-e0e3048e911d.sketch_text.stroke-60"),sQuery(id+"FHMxAyK4CFUKdhS_1.wireOp",EDGE,"1cb9c079-ea9b-4899-8069-e0e3048e911d.sketch_text.stroke-61"),sQuery(id+"FHMxAyK4CFUKdhS_1.wireOp",EDGE,"1cb9c079-ea9b-4899-8069-e0e3048e911d.sketch_text.stroke-62"),sQuery(id+"FHMxAyK4CFUKdhS_1.wireOp",EDGE,"1cb9c079-ea9b-4899-8069-e0e3048e911d.sketch_text.stroke-71"),sQuery(id+"FHMxAyK4CFUKdhS_1.wireOp",EDGE,"1cb9c079-ea9b-4899-8069-e0e3048e911d.sketch_text.stroke-72"),sQuery(id+"FHMxAyK4CFUKdhS_1.wireOp",EDGE,"1cb9c079-ea9b-4899-8069-e0e3048e911d.sketch_text.stroke-73"),sQuery(id+"FHMxAyK4CFUKdhS_1.wireOp",EDGE,"1cb9c079-ea9b-4899-8069-e0e3048e911d.sketch_text.stroke-74"),sQuery(id+"FHMxAyK4CFUKdhS_1.wireOp",EDGE,"1cb9c079-ea9b-4899-8069-e0e3048e911d.sketch_text.stroke-75"),sQuery(id+"FHMxAyK4CFUKdhS_1.wireOp",EDGE,"1cb9c079-ea9b-4899-8069-e0e3048e911d.sketch_text.stroke-76"),sQuery(id+"FHMxAyK4CFUKdhS_1.wireOp",EDGE,"1cb9c079-ea9b-4899-8069-e0e3048e911d.sketch_text.stroke-77"),sQuery(id+"FHMxAyK4CFUKdhS_1.wireOp",EDGE,"1cb9c079-ea9b-4899-8069-e0e3048e911d.sketch_text.stroke-78"),sQuery(id+"FHMxAyK4CFUKdhS_1.wireOp",EDGE,"1cb9c079-ea9b-4899-8069-e0e3048e911d.sketch_text.stroke-79"),sQuery(id+"FHMxAyK4CFUKdhS_1.wireOp",EDGE,"1cb9c079-ea9b-4899-8069-e0e3048e911d.sketch_text.stroke-80"),sQuery(id+"FHMxAyK4CFUKdhS_1.wireOp",EDGE,"1cb9c079-ea9b-4899-8069-e0e3048e911d.sketch_text.stroke-81"),sQuery(id+"FHMxAyK4CFUKdhS_1.wireOp",EDGE,"1cb9c079-ea9b-4899-8069-e0e3048e911d.sketch_text.stroke-82"),sQuery(id+"FHMxAyK4CFUKdhS_1.wireOp",EDGE,"1cb9c079-ea9b-4899-8069-e0e3048e911d.sketch_text.stroke-83"),sQuery(id+"FHMxAyK4CFUKdhS_1.wireOp",EDGE,"1cb9c079-ea9b-4899-8069-e0e3048e911d.sketch_text.stroke-84"),sQuery(id+"FHMxAyK4CFUKdhS_1.wireOp",EDGE,"1cb9c079-ea9b-4899-8069-e0e3048e911d.sketch_text.stroke-85"),sQuery(id+"FHMxAyK4CFUKdhS_1.wireOp",EDGE,"1cb9c079-ea9b-4899-8069-e0e3048e911d.sketch_text.stroke-86"),sQuery(id+"FHMxAyK4CFUKdhS_1.wireOp",EDGE,"1cb9c079-ea9b-4899-8069-e0e3048e911d.sketch_text.stroke-87"),sQuery(id+"FHMxAyK4CFUKdhS_1.wireOp",EDGE,"1cb9c079-ea9b-4899-8069-e0e3048e911d.sketch_text.stroke-88"),sQuery(id+"FHMxAyK4CFUKdhS_1.wireOp",EDGE,"1cb9c079-ea9b-4899-8069-e0e3048e911d.sketch_text.stroke-89"),sQuery(id+"FHMxAyK4CFUKdhS_1.wireOp",EDGE,"1cb9c079-ea9b-4899-8069-e0e3048e911d.sketch_text.stroke-90"),sQuery(id+"FHMxAyK4CFUKdhS_1.wireOp",EDGE,"1cb9c079-ea9b-4899-8069-e0e3048e911d.sketch_text.stroke-91"),sQuery(id+"FHMxAyK4CFUKdhS_1.wireOp",EDGE,"1cb9c079-ea9b-4899-8069-e0e3048e911d.sketch_text.stroke-92"),sQuery(id+"FHMxAyK4CFUKdhS_1.wireOp",EDGE,"1cb9c079-ea9b-4899-8069-e0e3048e911d.sketch_text.stroke-93"),sQuery(id+"FHMxAyK4CFUKdhS_1.wireOp",EDGE,"1cb9c079-ea9b-4899-8069-e0e3048e911d.sketch_text.stroke-94"),sQuery(id+"FHMxAyK4CFUKdhS_1.wireOp",EDGE,"1cb9c079-ea9b-4899-8069-e0e3048e911d.sketch_text.stroke-95"),sQuery(id+"FHMxAyK4CFUKdhS_1.wireOp",EDGE,"1cb9c079-ea9b-4899-8069-e0e3048e911d.sketch_text.stroke-96"),sQuery(id+"FHMxAyK4CFUKdhS_1.wireOp",EDGE,"1cb9c079-ea9b-4899-8069-e0e3048e911d.sketch_text.stroke-97"),sQuery(id+"FHMxAyK4CFUKdhS_1.wireOp",EDGE,"1cb9c079-ea9b-4899-8069-e0e3048e911d.sketch_text.stroke-103"),sQuery(id+"FHMxAyK4CFUKdhS_1.wireOp",EDGE,"1cb9c079-ea9b-4899-8069-e0e3048e911d.sketch_text.stroke-104"),sQuery(id+"FHMxAyK4CFUKdhS_1.wireOp",EDGE,"1cb9c079-ea9b-4899-8069-e0e3048e911d.sketch_text.stroke-105"),sQuery(id+"FHMxAyK4CFUKdhS_1.wireOp",EDGE,"1cb9c079-ea9b-4899-8069-e0e3048e911d.sketch_text.stroke-106"),sQuery(id+"FHMxAyK4CFUKdhS_1.wireOp",EDGE,"1cb9c079-ea9b-4899-8069-e0e3048e911d.sketch_text.stroke-107"),sQuery(id+"FHMxAyK4CFUKdhS_1.wireOp",EDGE,"1cb9c079-ea9b-4899-8069-e0e3048e911d.sketch_text.stroke-108"),sQuery(id+"FHMxAyK4CFUKdhS_1.wireOp",EDGE,"1cb9c079-ea9b-4899-8069-e0e3048e911d.sketch_text.stroke-109"),sQuery(id+"FHMxAyK4CFUKdhS_1.wireOp",EDGE,"1cb9c079-ea9b-4899-8069-e0e3048e911d.sketch_text.stroke-110"),sQuery(id+"FHMxAyK4CFUKdhS_1.wireOp",EDGE,"1cb9c079-ea9b-4899-8069-e0e3048e911d.sketch_text.stroke-111"),sQuery(id+"FHMxAyK4CFUKdhS_1.wireOp",EDGE,"1cb9c079-ea9b-4899-8069-e0e3048e911d.sketch_text.stroke-112"),sQuery(id+"FHMxAyK4CFUKdhS_1.wireOp",EDGE,"1cb9c079-ea9b-4899-8069-e0e3048e911d.sketch_text.stroke-113"),sQuery(id+"FHMxAyK4CFUKdhS_1.wireOp",EDGE,"1cb9c079-ea9b-4899-8069-e0e3048e911d.sketch_text.stroke-114"),sQuery(id+"FHMxAyK4CFUKdhS_1.wireOp",EDGE,"1cb9c079-ea9b-4899-8069-e0e3048e911d.sketch_text.stroke-115"),sQuery(id+"FHMxAyK4CFUKdhS_1.wireOp",EDGE,"1cb9c079-ea9b-4899-8069-e0e3048e911d.sketch_text.stroke-116"),sQuery(id+"FHMxAyK4CFUKdhS_1.wireOp",EDGE,"1cb9c079-ea9b-4899-8069-e0e3048e911d.sketch_text.stroke-117"),sQuery(id+"FHMxAyK4CFUKdhS_1.wireOp",EDGE,"1cb9c079-ea9b-4899-8069-e0e3048e911d.sketch_text.stroke-118"),sQuery(id+"FHMxAyK4CFUKdhS_1.wireOp",EDGE,"1cb9c079-ea9b-4899-8069-e0e3048e911d.sketch_text.stroke-119"),sQuery(id+"FHMxAyK4CFUKdhS_1.wireOp",EDGE,"1cb9c079-ea9b-4899-8069-e0e3048e911d.sketch_text.stroke-120"),sQuery(id+"FHMxAyK4CFUKdhS_1.wireOp",EDGE,"1cb9c079-ea9b-4899-8069-e0e3048e911d.sketch_text.stroke-121"),sQuery(id+"FHMxAyK4CFUKdhS_1.wireOp",EDGE,"1cb9c079-ea9b-4899-8069-e0e3048e911d.sketch_text.stroke-122"),sQuery(id+"FHMxAyK4CFUKdhS_1.wireOp",EDGE,"1cb9c079-ea9b-4899-8069-e0e3048e911d.sketch_text.stroke-123"),sQuery(id+"FHMxAyK4CFUKdhS_1.wireOp",EDGE,"1cb9c079-ea9b-4899-8069-e0e3048e911d.sketch_text.stroke-124"),sQuery(id+"FHMxAyK4CFUKdhS_1.wireOp",EDGE,"1cb9c079-ea9b-4899-8069-e0e3048e911d.sketch_text.stroke-125"),sQuery(id+"FHMxAyK4CFUKdhS_1.wireOp",EDGE,"1cb9c079-ea9b-4899-8069-e0e3048e911d.sketch_text.stroke-126"),sQuery(id+"FHMxAyK4CFUKdhS_1.wireOp",EDGE,"1cb9c079-ea9b-4899-8069-e0e3048e911d.sketch_text.stroke-127"),sQuery(id+"FHMxAyK4CFUKdhS_1.wireOp",EDGE,"1cb9c079-ea9b-4899-8069-e0e3048e911d.sketch_text.stroke-128"),sQuery(id+"FHMxAyK4CFUKdhS_1.wireOp",EDGE,"1cb9c079-ea9b-4899-8069-e0e3048e911d.sketch_text.stroke-129"),sQuery(id+"FHMxAyK4CFUKdhS_1.wireOp",EDGE,"1cb9c079-ea9b-4899-8069-e0e3048e911d.sketch_text.stroke-130"),sQuery(id+"FHMxAyK4CFUKdhS_1.wireOp",EDGE,"1cb9c079-ea9b-4899-8069-e0e3048e911d.sketch_text.stroke-131"),sQuery(id+"FHMxAyK4CFUKdhS_1.wireOp",EDGE,"1cb9c079-ea9b-4899-8069-e0e3048e911d.sketch_text.stroke-132"),sQuery(id+"FHMxAyK4CFUKdhS_1.wireOp",EDGE,"1cb9c079-ea9b-4899-8069-e0e3048e911d.sketch_text.stroke-133"),sQuery(id+"FHMxAyK4CFUKdhS_1.wireOp",EDGE,"1cb9c079-ea9b-4899-8069-e0e3048e911d.sketch_text.stroke-134"),sQuery(id+"FHMxAyK4CFUKdhS_1.wireOp",EDGE,"1cb9c079-ea9b-4899-8069-e0e3048e911d.sketch_text.stroke-135"),sQuery(id+"FHMxAyK4CFUKdhS_1.wireOp",EDGE,"1cb9c079-ea9b-4899-8069-e0e3048e911d.sketch_text.stroke-136"),sQuery(id+"FHMxAyK4CFUKdhS_1.wireOp",EDGE,"1cb9c079-ea9b-4899-8069-e0e3048e911d.sketch_text.stroke-137"),sQuery(id+"FHMxAyK4CFUKdhS_1.wireOp",EDGE,"1cb9c079-ea9b-4899-8069-e0e3048e911d.sketch_text.stroke-138"),sQuery(id+"FHMxAyK4CFUKdhS_1.wireOp",EDGE,"1cb9c079-ea9b-4899-8069-e0e3048e911d.sketch_text.stroke-139"),sQuery(id+"FHMxAyK4CFUKdhS_1.wireOp",EDGE,"1cb9c079-ea9b-4899-8069-e0e3048e911d.sketch_text.stroke-140"),sQuery(id+"FHMxAyK4CFUKdhS_1.wireOp",EDGE,"1cb9c079-ea9b-4899-8069-e0e3048e911d.sketch_text.stroke-141"),sQuery(id+"FHMxAyK4CFUKdhS_1.wireOp",EDGE,"1cb9c079-ea9b-4899-8069-e0e3048e911d.sketch_text.stroke-142"),sQuery(id+"FHMxAyK4CFUKdhS_1.wireOp",EDGE,"1cb9c079-ea9b-4899-8069-e0e3048e911d.sketch_text.stroke-143"),sQuery(id+"FHMxAyK4CFUKdhS_1.wireOp",EDGE,"1cb9c079-ea9b-4899-8069-e0e3048e911d.sketch_text.stroke-144"),sQuery(id+"FHMxAyK4CFUKdhS_1.wireOp",EDGE,"1cb9c079-ea9b-4899-8069-e0e3048e911d.sketch_text.stroke-145"),sQuery(id+"FHMxAyK4CFUKdhS_1.wireOp",EDGE,"1cb9c079-ea9b-4899-8069-e0e3048e911d.sketch_text.stroke-146"),sQuery(id+"FHMxAyK4CFUKdhS_1.wireOp",EDGE,"1cb9c079-ea9b-4899-8069-e0e3048e911d.sketch_text.stroke-147"),sQuery(id+"FHMxAyK4CFUKdhS_1.wireOp",EDGE,"1cb9c079-ea9b-4899-8069-e0e3048e911d.sketch_text.stroke-148"),sQuery(id+"FHMxAyK4CFUKdhS_1.wireOp",EDGE,"1cb9c079-ea9b-4899-8069-e0e3048e911d.sketch_text.stroke-149"),sQuery(id+"FHMxAyK4CFUKdhS_1.wireOp",EDGE,"1cb9c079-ea9b-4899-8069-e0e3048e911d.sketch_text.stroke-150"),sQuery(id+"FHMxAyK4CFUKdhS_1.wireOp",EDGE,"1cb9c079-ea9b-4899-8069-e0e3048e911d.sketch_text.stroke-151"),sQuery(id+"FHMxAyK4CFUKdhS_1.wireOp",EDGE,"1cb9c079-ea9b-4899-8069-e0e3048e911d.sketch_text.stroke-152"),sQuery(id+"FHMxAyK4CFUKdhS_1.wireOp",EDGE,"1cb9c079-ea9b-4899-8069-e0e3048e911d.sketch_text.stroke-153"),sQuery(id+"FHMxAyK4CFUKdhS_1.wireOp",EDGE,"1cb9c079-ea9b-4899-8069-e0e3048e911d.sketch_text.stroke-159"),sQuery(id+"FHMxAyK4CFUKdhS_1.wireOp",EDGE,"1cb9c079-ea9b-4899-8069-e0e3048e911d.sketch_text.stroke-160"),sQuery(id+"FHMxAyK4CFUKdhS_1.wireOp",EDGE,"1cb9c079-ea9b-4899-8069-e0e3048e911d.sketch_text.stroke-161"),sQuery(id+"FHMxAyK4CFUKdhS_1.wireOp",EDGE,"1cb9c079-ea9b-4899-8069-e0e3048e911d.sketch_text.stroke-162"),sQuery(id+"FHMxAyK4CFUKdhS_1.wireOp",EDGE,"1cb9c079-ea9b-4899-8069-e0e3048e911d.sketch_text.stroke-163"),sQuery(id+"FHMxAyK4CFUKdhS_1.wireOp",EDGE,"1cb9c079-ea9b-4899-8069-e0e3048e911d.sketch_text.stroke-164"),sQuery(id+"FHMxAyK4CFUKdhS_1.wireOp",EDGE,"1cb9c079-ea9b-4899-8069-e0e3048e911d.sketch_text.stroke-165"),sQuery(id+"FHMxAyK4CFUKdhS_1.wireOp",EDGE,"1cb9c079-ea9b-4899-8069-e0e3048e911d.sketch_text.stroke-166"),sQuery(id+"FHMxAyK4CFUKdhS_1.wireOp",EDGE,"1cb9c079-ea9b-4899-8069-e0e3048e911d.sketch_text.stroke-167"),sQuery(id+"FHMxAyK4CFUKdhS_1.wireOp",EDGE,"1cb9c079-ea9b-4899-8069-e0e3048e911d.sketch_text.stroke-168"),sQuery(id+"FHMxAyK4CFUKdhS_1.wireOp",EDGE,"1cb9c079-ea9b-4899-8069-e0e3048e911d.sketch_text.stroke-169"),sQuery(id+"FHMxAyK4CFUKdhS_1.wireOp",EDGE,"1cb9c079-ea9b-4899-8069-e0e3048e911d.sketch_text.stroke-170"),sQuery(id+"FHMxAyK4CFUKdhS_1.wireOp",EDGE,"1cb9c079-ea9b-4899-8069-e0e3048e911d.sketch_text.stroke-171"),sQuery(id+"FHMxAyK4CFUKdhS_1.wireOp",EDGE,"1cb9c079-ea9b-4899-8069-e0e3048e911d.sketch_text.stroke-172"),sQuery(id+"FHMxAyK4CFUKdhS_1.wireOp",EDGE,"1cb9c079-ea9b-4899-8069-e0e3048e911d.sketch_text.stroke-173"),sQuery(id+"FHMxAyK4CFUKdhS_1.wireOp",EDGE,"1cb9c079-ea9b-4899-8069-e0e3048e911d.sketch_text.stroke-174"),sQuery(id+"FHMxAyK4CFUKdhS_1.wireOp",EDGE,"1cb9c079-ea9b-4899-8069-e0e3048e911d.sketch_text.stroke-175"),sQuery(id+"FHMxAyK4CFUKdhS_1.wireOp",EDGE,"1cb9c079-ea9b-4899-8069-e0e3048e911d.sketch_text.stroke-176"),sQuery(id+"FHMxAyK4CFUKdhS_1.wireOp",EDGE,"1cb9c079-ea9b-4899-8069-e0e3048e911d.sketch_text.stroke-177"),sQuery(id+"FHMxAyK4CFUKdhS_1.wireOp",EDGE,"1cb9c079-ea9b-4899-8069-e0e3048e911d.sketch_text.stroke-178"),sQuery(id+"FHMxAyK4CFUKdhS_1.wireOp",EDGE,"1cb9c079-ea9b-4899-8069-e0e3048e911d.sketch_text.stroke-179"),sQuery(id+"FHMxAyK4CFUKdhS_1.wireOp",EDGE,"1cb9c079-ea9b-4899-8069-e0e3048e911d.sketch_text.stroke-180"),sQuery(id+"F3.wireOp",EDGE,"8007402e-1a4e-4a06-85a5-2af08e553504"),subQ0])],"isStart":true}),makeQuery(id+"F4.opExtrude","SWEPT_FACE",FACE,{"disambiguationData":[OSD([subQ0])]})])],"derivedFrom":makeQuery(id+"F4.opExtrude","CAP_EDGE",EDGE,{"disambiguationData":[OSD([subQ0])],"isStart":true})});}
            var Q7;
            {var subQ0=sQuery(id+"F0.wireOp",EDGE,"E0.right");var subQ1=sQuery(id+"F0.wireOp",EDGE,"E0.top");var subQ2=sQuery(id+"F3.wireOp",EDGE,"6ee83ff3-586e-4dbe-aaea-af71240543bd");var subQ3=sQuery(id+"F0.wireOp",EDGE,"E0.bottom");Q7=makeQuery(id+"F4.boolean.opBoolean","SPLIT",EDGE,{"disambiguationData":[TD([makeQuery(id+"F1.opExtrude","CAP_FACE",FACE,{"disambiguationData":[OSD([subQ3,subQ1,sQuery(id+"F0.wireOp",EDGE,"E0.left"),subQ0])],"isStart":false}),makeQuery(id+"F1.opExtrude","SWEPT_FACE",FACE,{"disambiguationData":[OSD([subQ1])]}),makeQuery(id+"F1.opExtrude","SWEPT_FACE",FACE,{"disambiguationData":[OSD([subQ0])]}),makeQuery(id+"F4.opExtrude","CAP_FACE",FACE,{"disambiguationData":[OSD([subQ3,sQuery(id+"F2.wireOp",EDGE,"fcba4419-a2ee-464f-be9d-58f11bf3418b.sketch_text.stroke-0"),sQuery(id+"F2.wireOp",EDGE,"fcba4419-a2ee-464f-be9d-58f11bf3418b.sketch_text.stroke-1"),sQuery(id+"F2.wireOp",EDGE,"fcba4419-a2ee-464f-be9d-58f11bf3418b.sketch_text.stroke-2"),sQuery(id+"F2.wireOp",EDGE,"fcba4419-a2ee-464f-be9d-58f11bf3418b.sketch_text.stroke-3"),sQuery(id+"F2.wireOp",EDGE,"fcba4419-a2ee-464f-be9d-58f11bf3418b.sketch_text.stroke-4"),sQuery(id+"F2.wireOp",EDGE,"fcba4419-a2ee-464f-be9d-58f11bf3418b.sketch_text.stroke-5"),sQuery(id+"F2.wireOp",EDGE,"fcba4419-a2ee-464f-be9d-58f11bf3418b.sketch_text.stroke-6"),sQuery(id+"F2.wireOp",EDGE,"fcba4419-a2ee-464f-be9d-58f11bf3418b.sketch_text.stroke-7"),sQuery(id+"F2.wireOp",EDGE,"fcba4419-a2ee-464f-be9d-58f11bf3418b.sketch_text.stroke-8"),sQuery(id+"F2.wireOp",EDGE,"fcba4419-a2ee-464f-be9d-58f11bf3418b.sketch_text.stroke-9"),sQuery(id+"F2.wireOp",EDGE,"fcba4419-a2ee-464f-be9d-58f11bf3418b.sketch_text.stroke-10"),sQuery(id+"F2.wireOp",EDGE,"fcba4419-a2ee-464f-be9d-58f11bf3418b.sketch_text.stroke-11"),sQuery(id+"F2.wireOp",EDGE,"fcba4419-a2ee-464f-be9d-58f11bf3418b.sketch_text.stroke-12"),sQuery(id+"F2.wireOp",EDGE,"fcba4419-a2ee-464f-be9d-58f11bf3418b.sketch_text.stroke-13"),sQuery(id+"F2.wireOp",EDGE,"fcba4419-a2ee-464f-be9d-58f11bf3418b.sketch_text.stroke-14"),sQuery(id+"F2.wireOp",EDGE,"fcba4419-a2ee-464f-be9d-58f11bf3418b.sketch_text.stroke-15"),sQuery(id+"F2.wireOp",EDGE,"fcba4419-a2ee-464f-be9d-58f11bf3418b.sketch_text.stroke-16"),sQuery(id+"F2.wireOp",EDGE,"fcba4419-a2ee-464f-be9d-58f11bf3418b.sketch_text.stroke-17"),sQuery(id+"F2.wireOp",EDGE,"fcba4419-a2ee-464f-be9d-58f11bf3418b.sketch_text.stroke-18"),sQuery(id+"F2.wireOp",EDGE,"fcba4419-a2ee-464f-be9d-58f11bf3418b.sketch_text.stroke-19"),sQuery(id+"F2.wireOp",EDGE,"fcba4419-a2ee-464f-be9d-58f11bf3418b.sketch_text.stroke-20"),sQuery(id+"F2.wireOp",EDGE,"fcba4419-a2ee-464f-be9d-58f11bf3418b.sketch_text.stroke-21"),sQuery(id+"F2.wireOp",EDGE,"fcba4419-a2ee-464f-be9d-58f11bf3418b.sketch_text.stroke-22"),sQuery(id+"F2.wireOp",EDGE,"fcba4419-a2ee-464f-be9d-58f11bf3418b.sketch_text.stroke-23"),sQuery(id+"F2.wireOp",EDGE,"fcba4419-a2ee-464f-be9d-58f11bf3418b.sketch_text.stroke-24"),sQuery(id+"F2.wireOp",EDGE,"fcba4419-a2ee-464f-be9d-58f11bf3418b.sketch_text.stroke-25"),sQuery(id+"F2.wireOp",EDGE,"fcba4419-a2ee-464f-be9d-58f11bf3418b.sketch_text.stroke-26"),sQuery(id+"F2.wireOp",EDGE,"fcba4419-a2ee-464f-be9d-58f11bf3418b.sketch_text.stroke-27"),sQuery(id+"F2.wireOp",EDGE,"fcba4419-a2ee-464f-be9d-58f11bf3418b.sketch_text.stroke-28"),sQuery(id+"F2.wireOp",EDGE,"fcba4419-a2ee-464f-be9d-58f11bf3418b.sketch_text.stroke-29"),sQuery(id+"F2.wireOp",EDGE,"fcba4419-a2ee-464f-be9d-58f11bf3418b.sketch_text.stroke-30"),sQuery(id+"F2.wireOp",EDGE,"fcba4419-a2ee-464f-be9d-58f11bf3418b.sketch_text.stroke-31"),sQuery(id+"F2.wireOp",EDGE,"fcba4419-a2ee-464f-be9d-58f11bf3418b.sketch_text.stroke-32"),sQuery(id+"F2.wireOp",EDGE,"fcba4419-a2ee-464f-be9d-58f11bf3418b.sketch_text.stroke-33"),sQuery(id+"F2.wireOp",EDGE,"fcba4419-a2ee-464f-be9d-58f11bf3418b.sketch_text.stroke-34"),sQuery(id+"F2.wireOp",EDGE,"fcba4419-a2ee-464f-be9d-58f11bf3418b.sketch_text.stroke-35"),sQuery(id+"F2.wireOp",EDGE,"fcba4419-a2ee-464f-be9d-58f11bf3418b.sketch_text.stroke-36"),sQuery(id+"F2.wireOp",EDGE,"fcba4419-a2ee-464f-be9d-58f11bf3418b.sketch_text.stroke-37"),sQuery(id+"F2.wireOp",EDGE,"fcba4419-a2ee-464f-be9d-58f11bf3418b.sketch_text.stroke-38"),sQuery(id+"F2.wireOp",EDGE,"fcba4419-a2ee-464f-be9d-58f11bf3418b.sketch_text.stroke-39"),sQuery(id+"F2.wireOp",EDGE,"fcba4419-a2ee-464f-be9d-58f11bf3418b.sketch_text.stroke-40"),sQuery(id+"F2.wireOp",EDGE,"fcba4419-a2ee-464f-be9d-58f11bf3418b.sketch_text.stroke-41"),sQuery(id+"F2.wireOp",EDGE,"fcba4419-a2ee-464f-be9d-58f11bf3418b.sketch_text.stroke-42"),sQuery(id+"F2.wireOp",EDGE,"fcba4419-a2ee-464f-be9d-58f11bf3418b.sketch_text.stroke-43"),sQuery(id+"F2.wireOp",EDGE,"fcba4419-a2ee-464f-be9d-58f11bf3418b.sketch_text.stroke-44"),sQuery(id+"F2.wireOp",EDGE,"fcba4419-a2ee-464f-be9d-58f11bf3418b.sketch_text.stroke-45"),sQuery(id+"F2.wireOp",EDGE,"fcba4419-a2ee-464f-be9d-58f11bf3418b.sketch_text.stroke-46"),sQuery(id+"F2.wireOp",EDGE,"fcba4419-a2ee-464f-be9d-58f11bf3418b.sketch_text.stroke-47"),sQuery(id+"F2.wireOp",EDGE,"fcba4419-a2ee-464f-be9d-58f11bf3418b.sketch_text.stroke-48"),sQuery(id+"F2.wireOp",EDGE,"fcba4419-a2ee-464f-be9d-58f11bf3418b.sketch_text.stroke-49"),sQuery(id+"F2.wireOp",EDGE,"fcba4419-a2ee-464f-be9d-58f11bf3418b.sketch_text.stroke-50"),sQuery(id+"F2.wireOp",EDGE,"fcba4419-a2ee-464f-be9d-58f11bf3418b.sketch_text.stroke-51"),sQuery(id+"F2.wireOp",EDGE,"fcba4419-a2ee-464f-be9d-58f11bf3418b.sketch_text.stroke-52"),sQuery(id+"F2.wireOp",EDGE,"fcba4419-a2ee-464f-be9d-58f11bf3418b.sketch_text.stroke-53"),sQuery(id+"F2.wireOp",EDGE,"fcba4419-a2ee-464f-be9d-58f11bf3418b.sketch_text.stroke-54"),sQuery(id+"F2.wireOp",EDGE,"fcba4419-a2ee-464f-be9d-58f11bf3418b.sketch_text.stroke-55"),sQuery(id+"F2.wireOp",EDGE,"fcba4419-a2ee-464f-be9d-58f11bf3418b.sketch_text.stroke-56"),sQuery(id+"F2.wireOp",EDGE,"fcba4419-a2ee-464f-be9d-58f11bf3418b.sketch_text.stroke-57"),sQuery(id+"F2.wireOp",EDGE,"fcba4419-a2ee-464f-be9d-58f11bf3418b.sketch_text.stroke-58"),sQuery(id+"F2.wireOp",EDGE,"fcba4419-a2ee-464f-be9d-58f11bf3418b.sketch_text.stroke-59"),sQuery(id+"F2.wireOp",EDGE,"fcba4419-a2ee-464f-be9d-58f11bf3418b.sketch_text.stroke-60"),sQuery(id+"F2.wireOp",EDGE,"fcba4419-a2ee-464f-be9d-58f11bf3418b.sketch_text.stroke-61"),sQuery(id+"F2.wireOp",EDGE,"fcba4419-a2ee-464f-be9d-58f11bf3418b.sketch_text.stroke-62"),sQuery(id+"F2.wireOp",EDGE,"fcba4419-a2ee-464f-be9d-58f11bf3418b.sketch_text.stroke-63"),sQuery(id+"F2.wireOp",EDGE,"fcba4419-a2ee-464f-be9d-58f11bf3418b.sketch_text.stroke-64"),sQuery(id+"F2.wireOp",EDGE,"fcba4419-a2ee-464f-be9d-58f11bf3418b.sketch_text.stroke-65"),sQuery(id+"F2.wireOp",EDGE,"fcba4419-a2ee-464f-be9d-58f11bf3418b.sketch_text.stroke-66"),sQuery(id+"F2.wireOp",EDGE,"fcba4419-a2ee-464f-be9d-58f11bf3418b.sketch_text.stroke-67"),sQuery(id+"F2.wireOp",EDGE,"fcba4419-a2ee-464f-be9d-58f11bf3418b.sketch_text.stroke-68"),sQuery(id+"F2.wireOp",EDGE,"fcba4419-a2ee-464f-be9d-58f11bf3418b.sketch_text.stroke-69"),sQuery(id+"F2.wireOp",EDGE,"fcba4419-a2ee-464f-be9d-58f11bf3418b.sketch_text.stroke-70"),sQuery(id+"F2.wireOp",EDGE,"fcba4419-a2ee-464f-be9d-58f11bf3418b.sketch_text.stroke-71"),sQuery(id+"F2.wireOp",EDGE,"fcba4419-a2ee-464f-be9d-58f11bf3418b.sketch_text.stroke-72"),sQuery(id+"F2.wireOp",EDGE,"fcba4419-a2ee-464f-be9d-58f11bf3418b.sketch_text.stroke-73"),sQuery(id+"F2.wireOp",EDGE,"fcba4419-a2ee-464f-be9d-58f11bf3418b.sketch_text.stroke-74"),sQuery(id+"F2.wireOp",EDGE,"fcba4419-a2ee-464f-be9d-58f11bf3418b.sketch_text.stroke-75"),sQuery(id+"F2.wireOp",EDGE,"fcba4419-a2ee-464f-be9d-58f11bf3418b.sketch_text.stroke-76"),sQuery(id+"F2.wireOp",EDGE,"fcba4419-a2ee-464f-be9d-58f11bf3418b.sketch_text.stroke-77"),sQuery(id+"F2.wireOp",EDGE,"fcba4419-a2ee-464f-be9d-58f11bf3418b.sketch_text.stroke-78"),sQuery(id+"F2.wireOp",EDGE,"fcba4419-a2ee-464f-be9d-58f11bf3418b.sketch_text.stroke-79"),sQuery(id+"F2.wireOp",EDGE,"fcba4419-a2ee-464f-be9d-58f11bf3418b.sketch_text.stroke-80"),sQuery(id+"F2.wireOp",EDGE,"fcba4419-a2ee-464f-be9d-58f11bf3418b.sketch_text.stroke-81"),sQuery(id+"F2.wireOp",EDGE,"fcba4419-a2ee-464f-be9d-58f11bf3418b.sketch_text.stroke-82"),sQuery(id+"F2.wireOp",EDGE,"fcba4419-a2ee-464f-be9d-58f11bf3418b.sketch_text.stroke-83"),sQuery(id+"F2.wireOp",EDGE,"fcba4419-a2ee-464f-be9d-58f11bf3418b.sketch_text.stroke-84"),sQuery(id+"F2.wireOp",EDGE,"fcba4419-a2ee-464f-be9d-58f11bf3418b.sketch_text.stroke-85"),sQuery(id+"F2.wireOp",EDGE,"fcba4419-a2ee-464f-be9d-58f11bf3418b.sketch_text.stroke-86"),sQuery(id+"F2.wireOp",EDGE,"fcba4419-a2ee-464f-be9d-58f11bf3418b.sketch_text.stroke-87"),sQuery(id+"F2.wireOp",EDGE,"fcba4419-a2ee-464f-be9d-58f11bf3418b.sketch_text.stroke-88"),sQuery(id+"F2.wireOp",EDGE,"fcba4419-a2ee-464f-be9d-58f11bf3418b.sketch_text.stroke-89"),sQuery(id+"F2.wireOp",EDGE,"fcba4419-a2ee-464f-be9d-58f11bf3418b.sketch_text.stroke-90"),sQuery(id+"F2.wireOp",EDGE,"fcba4419-a2ee-464f-be9d-58f11bf3418b.sketch_text.stroke-91"),sQuery(id+"F2.wireOp",EDGE,"fcba4419-a2ee-464f-be9d-58f11bf3418b.sketch_text.stroke-92"),sQuery(id+"F2.wireOp",EDGE,"fcba4419-a2ee-464f-be9d-58f11bf3418b.sketch_text.stroke-93"),sQuery(id+"F2.wireOp",EDGE,"fcba4419-a2ee-464f-be9d-58f11bf3418b.sketch_text.stroke-94"),sQuery(id+"F2.wireOp",EDGE,"fcba4419-a2ee-464f-be9d-58f11bf3418b.sketch_text.stroke-95"),sQuery(id+"F2.wireOp",EDGE,"fcba4419-a2ee-464f-be9d-58f11bf3418b.sketch_text.stroke-96"),sQuery(id+"F2.wireOp",EDGE,"fcba4419-a2ee-464f-be9d-58f11bf3418b.sketch_text.stroke-97"),sQuery(id+"F2.wireOp",EDGE,"fcba4419-a2ee-464f-be9d-58f11bf3418b.sketch_text.stroke-98"),sQuery(id+"F2.wireOp",EDGE,"fcba4419-a2ee-464f-be9d-58f11bf3418b.sketch_text.stroke-99"),sQuery(id+"F2.wireOp",EDGE,"fcba4419-a2ee-464f-be9d-58f11bf3418b.sketch_text.stroke-100"),sQuery(id+"F2.wireOp",EDGE,"fcba4419-a2ee-464f-be9d-58f11bf3418b.sketch_text.stroke-101"),sQuery(id+"F2.wireOp",EDGE,"fcba4419-a2ee-464f-be9d-58f11bf3418b.sketch_text.stroke-102"),sQuery(id+"F2.wireOp",EDGE,"fcba4419-a2ee-464f-be9d-58f11bf3418b.sketch_text.stroke-103"),sQuery(id+"F2.wireOp",EDGE,"fcba4419-a2ee-464f-be9d-58f11bf3418b.sketch_text.stroke-104"),sQuery(id+"F2.wireOp",EDGE,"fcba4419-a2ee-464f-be9d-58f11bf3418b.sketch_text.stroke-105"),sQuery(id+"F2.wireOp",EDGE,"fcba4419-a2ee-464f-be9d-58f11bf3418b.sketch_text.stroke-106"),sQuery(id+"F2.wireOp",EDGE,"fcba4419-a2ee-464f-be9d-58f11bf3418b.sketch_text.stroke-107"),sQuery(id+"F2.wireOp",EDGE,"fcba4419-a2ee-464f-be9d-58f11bf3418b.sketch_text.stroke-108"),sQuery(id+"F2.wireOp",EDGE,"fcba4419-a2ee-464f-be9d-58f11bf3418b.sketch_text.stroke-109"),sQuery(id+"F2.wireOp",EDGE,"fcba4419-a2ee-464f-be9d-58f11bf3418b.sketch_text.stroke-110"),sQuery(id+"F2.wireOp",EDGE,"fcba4419-a2ee-464f-be9d-58f11bf3418b.sketch_text.stroke-111"),sQuery(id+"F2.wireOp",EDGE,"fcba4419-a2ee-464f-be9d-58f11bf3418b.sketch_text.stroke-112"),sQuery(id+"F2.wireOp",EDGE,"fcba4419-a2ee-464f-be9d-58f11bf3418b.sketch_text.stroke-113"),sQuery(id+"F2.wireOp",EDGE,"fcba4419-a2ee-464f-be9d-58f11bf3418b.sketch_text.stroke-114"),sQuery(id+"F2.wireOp",EDGE,"fcba4419-a2ee-464f-be9d-58f11bf3418b.sketch_text.stroke-115"),sQuery(id+"F2.wireOp",EDGE,"fcba4419-a2ee-464f-be9d-58f11bf3418b.sketch_text.stroke-116"),sQuery(id+"F2.wireOp",EDGE,"fcba4419-a2ee-464f-be9d-58f11bf3418b.sketch_text.stroke-117"),sQuery(id+"F2.wireOp",EDGE,"fcba4419-a2ee-464f-be9d-58f11bf3418b.sketch_text.stroke-118"),sQuery(id+"F2.wireOp",EDGE,"fcba4419-a2ee-464f-be9d-58f11bf3418b.sketch_text.stroke-119"),sQuery(id+"F2.wireOp",EDGE,"fcba4419-a2ee-464f-be9d-58f11bf3418b.sketch_text.stroke-120"),sQuery(id+"F2.wireOp",EDGE,"fcba4419-a2ee-464f-be9d-58f11bf3418b.sketch_text.stroke-121"),sQuery(id+"F2.wireOp",EDGE,"fcba4419-a2ee-464f-be9d-58f11bf3418b.sketch_text.stroke-122"),sQuery(id+"F2.wireOp",EDGE,"fcba4419-a2ee-464f-be9d-58f11bf3418b.sketch_text.stroke-123"),sQuery(id+"F2.wireOp",EDGE,"fcba4419-a2ee-464f-be9d-58f11bf3418b.sketch_text.stroke-124"),sQuery(id+"F2.wireOp",EDGE,"fcba4419-a2ee-464f-be9d-58f11bf3418b.sketch_text.stroke-125"),sQuery(id+"F2.wireOp",EDGE,"fcba4419-a2ee-464f-be9d-58f11bf3418b.sketch_text.stroke-126"),sQuery(id+"F2.wireOp",EDGE,"fcba4419-a2ee-464f-be9d-58f11bf3418b.sketch_text.stroke-127"),sQuery(id+"F2.wireOp",EDGE,"fcba4419-a2ee-464f-be9d-58f11bf3418b.sketch_text.stroke-128"),sQuery(id+"F2.wireOp",EDGE,"fcba4419-a2ee-464f-be9d-58f11bf3418b.sketch_text.stroke-129"),sQuery(id+"F2.wireOp",EDGE,"fcba4419-a2ee-464f-be9d-58f11bf3418b.sketch_text.stroke-130"),sQuery(id+"F2.wireOp",EDGE,"fcba4419-a2ee-464f-be9d-58f11bf3418b.sketch_text.stroke-131"),sQuery(id+"F2.wireOp",EDGE,"fcba4419-a2ee-464f-be9d-58f11bf3418b.sketch_text.stroke-132"),sQuery(id+"F2.wireOp",EDGE,"fcba4419-a2ee-464f-be9d-58f11bf3418b.sketch_text.stroke-133"),sQuery(id+"F2.wireOp",EDGE,"fcba4419-a2ee-464f-be9d-58f11bf3418b.sketch_text.stroke-134"),sQuery(id+"F2.wireOp",EDGE,"fcba4419-a2ee-464f-be9d-58f11bf3418b.sketch_text.stroke-135"),sQuery(id+"F2.wireOp",EDGE,"fcba4419-a2ee-464f-be9d-58f11bf3418b.sketch_text.stroke-136"),sQuery(id+"F2.wireOp",EDGE,"fcba4419-a2ee-464f-be9d-58f11bf3418b.sketch_text.stroke-137"),sQuery(id+"F2.wireOp",EDGE,"fcba4419-a2ee-464f-be9d-58f11bf3418b.sketch_text.stroke-138"),sQuery(id+"F2.wireOp",EDGE,"fcba4419-a2ee-464f-be9d-58f11bf3418b.sketch_text.stroke-139"),sQuery(id+"F2.wireOp",EDGE,"fcba4419-a2ee-464f-be9d-58f11bf3418b.sketch_text.stroke-140"),sQuery(id+"F2.wireOp",EDGE,"fcba4419-a2ee-464f-be9d-58f11bf3418b.sketch_text.stroke-141"),sQuery(id+"F2.wireOp",EDGE,"fcba4419-a2ee-464f-be9d-58f11bf3418b.sketch_text.stroke-142"),sQuery(id+"F2.wireOp",EDGE,"fcba4419-a2ee-464f-be9d-58f11bf3418b.sketch_text.stroke-143"),sQuery(id+"F2.wireOp",EDGE,"fcba4419-a2ee-464f-be9d-58f11bf3418b.sketch_text.stroke-144"),sQuery(id+"F2.wireOp",EDGE,"fcba4419-a2ee-464f-be9d-58f11bf3418b.sketch_text.stroke-145"),sQuery(id+"F2.wireOp",EDGE,"fcba4419-a2ee-464f-be9d-58f11bf3418b.sketch_text.stroke-146"),sQuery(id+"F2.wireOp",EDGE,"fcba4419-a2ee-464f-be9d-58f11bf3418b.sketch_text.stroke-147"),sQuery(id+"F2.wireOp",EDGE,"fcba4419-a2ee-464f-be9d-58f11bf3418b.sketch_text.stroke-148"),sQuery(id+"F2.wireOp",EDGE,"fcba4419-a2ee-464f-be9d-58f11bf3418b.sketch_text.stroke-149"),sQuery(id+"F2.wireOp",EDGE,"fcba4419-a2ee-464f-be9d-58f11bf3418b.sketch_text.stroke-150"),sQuery(id+"F2.wireOp",EDGE,"fcba4419-a2ee-464f-be9d-58f11bf3418b.sketch_text.stroke-151"),sQuery(id+"F2.wireOp",EDGE,"fcba4419-a2ee-464f-be9d-58f11bf3418b.sketch_text.stroke-152"),sQuery(id+"F2.wireOp",EDGE,"fcba4419-a2ee-464f-be9d-58f11bf3418b.sketch_text.stroke-153"),sQuery(id+"F2.wireOp",EDGE,"fcba4419-a2ee-464f-be9d-58f11bf3418b.sketch_text.stroke-154"),sQuery(id+"F2.wireOp",EDGE,"fcba4419-a2ee-464f-be9d-58f11bf3418b.sketch_text.stroke-155"),sQuery(id+"F2.wireOp",EDGE,"fcba4419-a2ee-464f-be9d-58f11bf3418b.sketch_text.stroke-156"),sQuery(id+"F2.wireOp",EDGE,"fcba4419-a2ee-464f-be9d-58f11bf3418b.sketch_text.stroke-157"),sQuery(id+"F2.wireOp",EDGE,"fcba4419-a2ee-464f-be9d-58f11bf3418b.sketch_text.stroke-158"),sQuery(id+"F2.wireOp",EDGE,"fcba4419-a2ee-464f-be9d-58f11bf3418b.sketch_text.stroke-159"),sQuery(id+"F2.wireOp",EDGE,"fcba4419-a2ee-464f-be9d-58f11bf3418b.sketch_text.stroke-160"),sQuery(id+"F2.wireOp",EDGE,"fcba4419-a2ee-464f-be9d-58f11bf3418b.sketch_text.stroke-161"),sQuery(id+"F2.wireOp",EDGE,"fcba4419-a2ee-464f-be9d-58f11bf3418b.sketch_text.stroke-162"),sQuery(id+"F2.wireOp",EDGE,"fcba4419-a2ee-464f-be9d-58f11bf3418b.sketch_text.stroke-163"),sQuery(id+"F2.wireOp",EDGE,"fcba4419-a2ee-464f-be9d-58f11bf3418b.sketch_text.stroke-164"),sQuery(id+"F2.wireOp",EDGE,"fcba4419-a2ee-464f-be9d-58f11bf3418b.sketch_text.stroke-165"),sQuery(id+"F2.wireOp",EDGE,"fcba4419-a2ee-464f-be9d-58f11bf3418b.sketch_text.stroke-166"),sQuery(id+"F2.wireOp",EDGE,"fcba4419-a2ee-464f-be9d-58f11bf3418b.sketch_text.stroke-167"),sQuery(id+"F2.wireOp",EDGE,"fcba4419-a2ee-464f-be9d-58f11bf3418b.sketch_text.stroke-168"),sQuery(id+"F2.wireOp",EDGE,"fcba4419-a2ee-464f-be9d-58f11bf3418b.sketch_text.stroke-169"),sQuery(id+"F2.wireOp",EDGE,"fcba4419-a2ee-464f-be9d-58f11bf3418b.sketch_text.stroke-170"),sQuery(id+"F2.wireOp",EDGE,"fcba4419-a2ee-464f-be9d-58f11bf3418b.sketch_text.stroke-171"),sQuery(id+"F2.wireOp",EDGE,"fcba4419-a2ee-464f-be9d-58f11bf3418b.sketch_text.stroke-172"),sQuery(id+"F2.wireOp",EDGE,"fcba4419-a2ee-464f-be9d-58f11bf3418b.sketch_text.stroke-173"),sQuery(id+"FHMxAyK4CFUKdhS_1.wireOp",EDGE,"1cb9c079-ea9b-4899-8069-e0e3048e911d.sketch_text.stroke-0"),sQuery(id+"FHMxAyK4CFUKdhS_1.wireOp",EDGE,"1cb9c079-ea9b-4899-8069-e0e3048e911d.sketch_text.stroke-1"),sQuery(id+"FHMxAyK4CFUKdhS_1.wireOp",EDGE,"1cb9c079-ea9b-4899-8069-e0e3048e911d.sketch_text.stroke-2"),sQuery(id+"FHMxAyK4CFUKdhS_1.wireOp",EDGE,"1cb9c079-ea9b-4899-8069-e0e3048e911d.sketch_text.stroke-3"),sQuery(id+"FHMxAyK4CFUKdhS_1.wireOp",EDGE,"1cb9c079-ea9b-4899-8069-e0e3048e911d.sketch_text.stroke-4"),sQuery(id+"FHMxAyK4CFUKdhS_1.wireOp",EDGE,"1cb9c079-ea9b-4899-8069-e0e3048e911d.sketch_text.stroke-5"),sQuery(id+"FHMxAyK4CFUKdhS_1.wireOp",EDGE,"1cb9c079-ea9b-4899-8069-e0e3048e911d.sketch_text.stroke-6"),sQuery(id+"FHMxAyK4CFUKdhS_1.wireOp",EDGE,"1cb9c079-ea9b-4899-8069-e0e3048e911d.sketch_text.stroke-7"),sQuery(id+"FHMxAyK4CFUKdhS_1.wireOp",EDGE,"1cb9c079-ea9b-4899-8069-e0e3048e911d.sketch_text.stroke-8"),sQuery(id+"FHMxAyK4CFUKdhS_1.wireOp",EDGE,"1cb9c079-ea9b-4899-8069-e0e3048e911d.sketch_text.stroke-9"),sQuery(id+"FHMxAyK4CFUKdhS_1.wireOp",EDGE,"1cb9c079-ea9b-4899-8069-e0e3048e911d.sketch_text.stroke-10"),sQuery(id+"FHMxAyK4CFUKdhS_1.wireOp",EDGE,"1cb9c079-ea9b-4899-8069-e0e3048e911d.sketch_text.stroke-11"),sQuery(id+"FHMxAyK4CFUKdhS_1.wireOp",EDGE,"1cb9c079-ea9b-4899-8069-e0e3048e911d.sketch_text.stroke-12"),sQuery(id+"FHMxAyK4CFUKdhS_1.wireOp",EDGE,"1cb9c079-ea9b-4899-8069-e0e3048e911d.sketch_text.stroke-13"),sQuery(id+"FHMxAyK4CFUKdhS_1.wireOp",EDGE,"1cb9c079-ea9b-4899-8069-e0e3048e911d.sketch_text.stroke-14"),sQuery(id+"FHMxAyK4CFUKdhS_1.wireOp",EDGE,"1cb9c079-ea9b-4899-8069-e0e3048e911d.sketch_text.stroke-15"),sQuery(id+"FHMxAyK4CFUKdhS_1.wireOp",EDGE,"1cb9c079-ea9b-4899-8069-e0e3048e911d.sketch_text.stroke-16"),sQuery(id+"FHMxAyK4CFUKdhS_1.wireOp",EDGE,"1cb9c079-ea9b-4899-8069-e0e3048e911d.sketch_text.stroke-17"),sQuery(id+"FHMxAyK4CFUKdhS_1.wireOp",EDGE,"1cb9c079-ea9b-4899-8069-e0e3048e911d.sketch_text.stroke-18"),sQuery(id+"FHMxAyK4CFUKdhS_1.wireOp",EDGE,"1cb9c079-ea9b-4899-8069-e0e3048e911d.sketch_text.stroke-19"),sQuery(id+"FHMxAyK4CFUKdhS_1.wireOp",EDGE,"1cb9c079-ea9b-4899-8069-e0e3048e911d.sketch_text.stroke-20"),sQuery(id+"FHMxAyK4CFUKdhS_1.wireOp",EDGE,"1cb9c079-ea9b-4899-8069-e0e3048e911d.sketch_text.stroke-21"),sQuery(id+"FHMxAyK4CFUKdhS_1.wireOp",EDGE,"1cb9c079-ea9b-4899-8069-e0e3048e911d.sketch_text.stroke-22"),sQuery(id+"FHMxAyK4CFUKdhS_1.wireOp",EDGE,"1cb9c079-ea9b-4899-8069-e0e3048e911d.sketch_text.stroke-23"),sQuery(id+"FHMxAyK4CFUKdhS_1.wireOp",EDGE,"1cb9c079-ea9b-4899-8069-e0e3048e911d.sketch_text.stroke-24"),sQuery(id+"FHMxAyK4CFUKdhS_1.wireOp",EDGE,"1cb9c079-ea9b-4899-8069-e0e3048e911d.sketch_text.stroke-25"),sQuery(id+"FHMxAyK4CFUKdhS_1.wireOp",EDGE,"1cb9c079-ea9b-4899-8069-e0e3048e911d.sketch_text.stroke-26"),sQuery(id+"FHMxAyK4CFUKdhS_1.wireOp",EDGE,"1cb9c079-ea9b-4899-8069-e0e3048e911d.sketch_text.stroke-27"),sQuery(id+"FHMxAyK4CFUKdhS_1.wireOp",EDGE,"1cb9c079-ea9b-4899-8069-e0e3048e911d.sketch_text.stroke-28"),sQuery(id+"FHMxAyK4CFUKdhS_1.wireOp",EDGE,"1cb9c079-ea9b-4899-8069-e0e3048e911d.sketch_text.stroke-29"),sQuery(id+"FHMxAyK4CFUKdhS_1.wireOp",EDGE,"1cb9c079-ea9b-4899-8069-e0e3048e911d.sketch_text.stroke-30"),sQuery(id+"FHMxAyK4CFUKdhS_1.wireOp",EDGE,"1cb9c079-ea9b-4899-8069-e0e3048e911d.sketch_text.stroke-31"),sQuery(id+"FHMxAyK4CFUKdhS_1.wireOp",EDGE,"1cb9c079-ea9b-4899-8069-e0e3048e911d.sketch_text.stroke-32"),sQuery(id+"FHMxAyK4CFUKdhS_1.wireOp",EDGE,"1cb9c079-ea9b-4899-8069-e0e3048e911d.sketch_text.stroke-33"),sQuery(id+"FHMxAyK4CFUKdhS_1.wireOp",EDGE,"1cb9c079-ea9b-4899-8069-e0e3048e911d.sketch_text.stroke-34"),sQuery(id+"FHMxAyK4CFUKdhS_1.wireOp",EDGE,"1cb9c079-ea9b-4899-8069-e0e3048e911d.sketch_text.stroke-35"),sQuery(id+"FHMxAyK4CFUKdhS_1.wireOp",EDGE,"1cb9c079-ea9b-4899-8069-e0e3048e911d.sketch_text.stroke-36"),sQuery(id+"FHMxAyK4CFUKdhS_1.wireOp",EDGE,"1cb9c079-ea9b-4899-8069-e0e3048e911d.sketch_text.stroke-37"),sQuery(id+"FHMxAyK4CFUKdhS_1.wireOp",EDGE,"1cb9c079-ea9b-4899-8069-e0e3048e911d.sketch_text.stroke-38"),sQuery(id+"FHMxAyK4CFUKdhS_1.wireOp",EDGE,"1cb9c079-ea9b-4899-8069-e0e3048e911d.sketch_text.stroke-39"),sQuery(id+"FHMxAyK4CFUKdhS_1.wireOp",EDGE,"1cb9c079-ea9b-4899-8069-e0e3048e911d.sketch_text.stroke-40"),sQuery(id+"FHMxAyK4CFUKdhS_1.wireOp",EDGE,"1cb9c079-ea9b-4899-8069-e0e3048e911d.sketch_text.stroke-41"),sQuery(id+"FHMxAyK4CFUKdhS_1.wireOp",EDGE,"1cb9c079-ea9b-4899-8069-e0e3048e911d.sketch_text.stroke-42"),sQuery(id+"FHMxAyK4CFUKdhS_1.wireOp",EDGE,"1cb9c079-ea9b-4899-8069-e0e3048e911d.sketch_text.stroke-43"),sQuery(id+"FHMxAyK4CFUKdhS_1.wireOp",EDGE,"1cb9c079-ea9b-4899-8069-e0e3048e911d.sketch_text.stroke-44"),sQuery(id+"FHMxAyK4CFUKdhS_1.wireOp",EDGE,"1cb9c079-ea9b-4899-8069-e0e3048e911d.sketch_text.stroke-45"),sQuery(id+"FHMxAyK4CFUKdhS_1.wireOp",EDGE,"1cb9c079-ea9b-4899-8069-e0e3048e911d.sketch_text.stroke-46"),sQuery(id+"FHMxAyK4CFUKdhS_1.wireOp",EDGE,"1cb9c079-ea9b-4899-8069-e0e3048e911d.sketch_text.stroke-47"),sQuery(id+"FHMxAyK4CFUKdhS_1.wireOp",EDGE,"1cb9c079-ea9b-4899-8069-e0e3048e911d.sketch_text.stroke-48"),sQuery(id+"FHMxAyK4CFUKdhS_1.wireOp",EDGE,"1cb9c079-ea9b-4899-8069-e0e3048e911d.sketch_text.stroke-49"),sQuery(id+"FHMxAyK4CFUKdhS_1.wireOp",EDGE,"1cb9c079-ea9b-4899-8069-e0e3048e911d.sketch_text.stroke-50"),sQuery(id+"FHMxAyK4CFUKdhS_1.wireOp",EDGE,"1cb9c079-ea9b-4899-8069-e0e3048e911d.sketch_text.stroke-51"),sQuery(id+"FHMxAyK4CFUKdhS_1.wireOp",EDGE,"1cb9c079-ea9b-4899-8069-e0e3048e911d.sketch_text.stroke-52"),sQuery(id+"FHMxAyK4CFUKdhS_1.wireOp",EDGE,"1cb9c079-ea9b-4899-8069-e0e3048e911d.sketch_text.stroke-53"),sQuery(id+"FHMxAyK4CFUKdhS_1.wireOp",EDGE,"1cb9c079-ea9b-4899-8069-e0e3048e911d.sketch_text.stroke-54"),sQuery(id+"FHMxAyK4CFUKdhS_1.wireOp",EDGE,"1cb9c079-ea9b-4899-8069-e0e3048e911d.sketch_text.stroke-55"),sQuery(id+"FHMxAyK4CFUKdhS_1.wireOp",EDGE,"1cb9c079-ea9b-4899-8069-e0e3048e911d.sketch_text.stroke-56"),sQuery(id+"FHMxAyK4CFUKdhS_1.wireOp",EDGE,"1cb9c079-ea9b-4899-8069-e0e3048e911d.sketch_text.stroke-57"),sQuery(id+"FHMxAyK4CFUKdhS_1.wireOp",EDGE,"1cb9c079-ea9b-4899-8069-e0e3048e911d.sketch_text.stroke-58"),sQuery(id+"FHMxAyK4CFUKdhS_1.wireOp",EDGE,"1cb9c079-ea9b-4899-8069-e0e3048e911d.sketch_text.stroke-59"),sQuery(id+"FHMxAyK4CFUKdhS_1.wireOp",EDGE,"1cb9c079-ea9b-4899-8069-e0e3048e911d.sketch_text.stroke-60"),sQuery(id+"FHMxAyK4CFUKdhS_1.wireOp",EDGE,"1cb9c079-ea9b-4899-8069-e0e3048e911d.sketch_text.stroke-61"),sQuery(id+"FHMxAyK4CFUKdhS_1.wireOp",EDGE,"1cb9c079-ea9b-4899-8069-e0e3048e911d.sketch_text.stroke-62"),sQuery(id+"FHMxAyK4CFUKdhS_1.wireOp",EDGE,"1cb9c079-ea9b-4899-8069-e0e3048e911d.sketch_text.stroke-71"),sQuery(id+"FHMxAyK4CFUKdhS_1.wireOp",EDGE,"1cb9c079-ea9b-4899-8069-e0e3048e911d.sketch_text.stroke-72"),sQuery(id+"FHMxAyK4CFUKdhS_1.wireOp",EDGE,"1cb9c079-ea9b-4899-8069-e0e3048e911d.sketch_text.stroke-73"),sQuery(id+"FHMxAyK4CFUKdhS_1.wireOp",EDGE,"1cb9c079-ea9b-4899-8069-e0e3048e911d.sketch_text.stroke-74"),sQuery(id+"FHMxAyK4CFUKdhS_1.wireOp",EDGE,"1cb9c079-ea9b-4899-8069-e0e3048e911d.sketch_text.stroke-75"),sQuery(id+"FHMxAyK4CFUKdhS_1.wireOp",EDGE,"1cb9c079-ea9b-4899-8069-e0e3048e911d.sketch_text.stroke-76"),sQuery(id+"FHMxAyK4CFUKdhS_1.wireOp",EDGE,"1cb9c079-ea9b-4899-8069-e0e3048e911d.sketch_text.stroke-77"),sQuery(id+"FHMxAyK4CFUKdhS_1.wireOp",EDGE,"1cb9c079-ea9b-4899-8069-e0e3048e911d.sketch_text.stroke-78"),sQuery(id+"FHMxAyK4CFUKdhS_1.wireOp",EDGE,"1cb9c079-ea9b-4899-8069-e0e3048e911d.sketch_text.stroke-79"),sQuery(id+"FHMxAyK4CFUKdhS_1.wireOp",EDGE,"1cb9c079-ea9b-4899-8069-e0e3048e911d.sketch_text.stroke-80"),sQuery(id+"FHMxAyK4CFUKdhS_1.wireOp",EDGE,"1cb9c079-ea9b-4899-8069-e0e3048e911d.sketch_text.stroke-81"),sQuery(id+"FHMxAyK4CFUKdhS_1.wireOp",EDGE,"1cb9c079-ea9b-4899-8069-e0e3048e911d.sketch_text.stroke-82"),sQuery(id+"FHMxAyK4CFUKdhS_1.wireOp",EDGE,"1cb9c079-ea9b-4899-8069-e0e3048e911d.sketch_text.stroke-83"),sQuery(id+"FHMxAyK4CFUKdhS_1.wireOp",EDGE,"1cb9c079-ea9b-4899-8069-e0e3048e911d.sketch_text.stroke-84"),sQuery(id+"FHMxAyK4CFUKdhS_1.wireOp",EDGE,"1cb9c079-ea9b-4899-8069-e0e3048e911d.sketch_text.stroke-85"),sQuery(id+"FHMxAyK4CFUKdhS_1.wireOp",EDGE,"1cb9c079-ea9b-4899-8069-e0e3048e911d.sketch_text.stroke-86"),sQuery(id+"FHMxAyK4CFUKdhS_1.wireOp",EDGE,"1cb9c079-ea9b-4899-8069-e0e3048e911d.sketch_text.stroke-87"),sQuery(id+"FHMxAyK4CFUKdhS_1.wireOp",EDGE,"1cb9c079-ea9b-4899-8069-e0e3048e911d.sketch_text.stroke-88"),sQuery(id+"FHMxAyK4CFUKdhS_1.wireOp",EDGE,"1cb9c079-ea9b-4899-8069-e0e3048e911d.sketch_text.stroke-89"),sQuery(id+"FHMxAyK4CFUKdhS_1.wireOp",EDGE,"1cb9c079-ea9b-4899-8069-e0e3048e911d.sketch_text.stroke-90"),sQuery(id+"FHMxAyK4CFUKdhS_1.wireOp",EDGE,"1cb9c079-ea9b-4899-8069-e0e3048e911d.sketch_text.stroke-91"),sQuery(id+"FHMxAyK4CFUKdhS_1.wireOp",EDGE,"1cb9c079-ea9b-4899-8069-e0e3048e911d.sketch_text.stroke-92"),sQuery(id+"FHMxAyK4CFUKdhS_1.wireOp",EDGE,"1cb9c079-ea9b-4899-8069-e0e3048e911d.sketch_text.stroke-93"),sQuery(id+"FHMxAyK4CFUKdhS_1.wireOp",EDGE,"1cb9c079-ea9b-4899-8069-e0e3048e911d.sketch_text.stroke-94"),sQuery(id+"FHMxAyK4CFUKdhS_1.wireOp",EDGE,"1cb9c079-ea9b-4899-8069-e0e3048e911d.sketch_text.stroke-95"),sQuery(id+"FHMxAyK4CFUKdhS_1.wireOp",EDGE,"1cb9c079-ea9b-4899-8069-e0e3048e911d.sketch_text.stroke-96"),sQuery(id+"FHMxAyK4CFUKdhS_1.wireOp",EDGE,"1cb9c079-ea9b-4899-8069-e0e3048e911d.sketch_text.stroke-97"),sQuery(id+"FHMxAyK4CFUKdhS_1.wireOp",EDGE,"1cb9c079-ea9b-4899-8069-e0e3048e911d.sketch_text.stroke-103"),sQuery(id+"FHMxAyK4CFUKdhS_1.wireOp",EDGE,"1cb9c079-ea9b-4899-8069-e0e3048e911d.sketch_text.stroke-104"),sQuery(id+"FHMxAyK4CFUKdhS_1.wireOp",EDGE,"1cb9c079-ea9b-4899-8069-e0e3048e911d.sketch_text.stroke-105"),sQuery(id+"FHMxAyK4CFUKdhS_1.wireOp",EDGE,"1cb9c079-ea9b-4899-8069-e0e3048e911d.sketch_text.stroke-106"),sQuery(id+"FHMxAyK4CFUKdhS_1.wireOp",EDGE,"1cb9c079-ea9b-4899-8069-e0e3048e911d.sketch_text.stroke-107"),sQuery(id+"FHMxAyK4CFUKdhS_1.wireOp",EDGE,"1cb9c079-ea9b-4899-8069-e0e3048e911d.sketch_text.stroke-108"),sQuery(id+"FHMxAyK4CFUKdhS_1.wireOp",EDGE,"1cb9c079-ea9b-4899-8069-e0e3048e911d.sketch_text.stroke-109"),sQuery(id+"FHMxAyK4CFUKdhS_1.wireOp",EDGE,"1cb9c079-ea9b-4899-8069-e0e3048e911d.sketch_text.stroke-110"),sQuery(id+"FHMxAyK4CFUKdhS_1.wireOp",EDGE,"1cb9c079-ea9b-4899-8069-e0e3048e911d.sketch_text.stroke-111"),sQuery(id+"FHMxAyK4CFUKdhS_1.wireOp",EDGE,"1cb9c079-ea9b-4899-8069-e0e3048e911d.sketch_text.stroke-112"),sQuery(id+"FHMxAyK4CFUKdhS_1.wireOp",EDGE,"1cb9c079-ea9b-4899-8069-e0e3048e911d.sketch_text.stroke-113"),sQuery(id+"FHMxAyK4CFUKdhS_1.wireOp",EDGE,"1cb9c079-ea9b-4899-8069-e0e3048e911d.sketch_text.stroke-114"),sQuery(id+"FHMxAyK4CFUKdhS_1.wireOp",EDGE,"1cb9c079-ea9b-4899-8069-e0e3048e911d.sketch_text.stroke-115"),sQuery(id+"FHMxAyK4CFUKdhS_1.wireOp",EDGE,"1cb9c079-ea9b-4899-8069-e0e3048e911d.sketch_text.stroke-116"),sQuery(id+"FHMxAyK4CFUKdhS_1.wireOp",EDGE,"1cb9c079-ea9b-4899-8069-e0e3048e911d.sketch_text.stroke-117"),sQuery(id+"FHMxAyK4CFUKdhS_1.wireOp",EDGE,"1cb9c079-ea9b-4899-8069-e0e3048e911d.sketch_text.stroke-118"),sQuery(id+"FHMxAyK4CFUKdhS_1.wireOp",EDGE,"1cb9c079-ea9b-4899-8069-e0e3048e911d.sketch_text.stroke-119"),sQuery(id+"FHMxAyK4CFUKdhS_1.wireOp",EDGE,"1cb9c079-ea9b-4899-8069-e0e3048e911d.sketch_text.stroke-120"),sQuery(id+"FHMxAyK4CFUKdhS_1.wireOp",EDGE,"1cb9c079-ea9b-4899-8069-e0e3048e911d.sketch_text.stroke-121"),sQuery(id+"FHMxAyK4CFUKdhS_1.wireOp",EDGE,"1cb9c079-ea9b-4899-8069-e0e3048e911d.sketch_text.stroke-122"),sQuery(id+"FHMxAyK4CFUKdhS_1.wireOp",EDGE,"1cb9c079-ea9b-4899-8069-e0e3048e911d.sketch_text.stroke-123"),sQuery(id+"FHMxAyK4CFUKdhS_1.wireOp",EDGE,"1cb9c079-ea9b-4899-8069-e0e3048e911d.sketch_text.stroke-124"),sQuery(id+"FHMxAyK4CFUKdhS_1.wireOp",EDGE,"1cb9c079-ea9b-4899-8069-e0e3048e911d.sketch_text.stroke-125"),sQuery(id+"FHMxAyK4CFUKdhS_1.wireOp",EDGE,"1cb9c079-ea9b-4899-8069-e0e3048e911d.sketch_text.stroke-126"),sQuery(id+"FHMxAyK4CFUKdhS_1.wireOp",EDGE,"1cb9c079-ea9b-4899-8069-e0e3048e911d.sketch_text.stroke-127"),sQuery(id+"FHMxAyK4CFUKdhS_1.wireOp",EDGE,"1cb9c079-ea9b-4899-8069-e0e3048e911d.sketch_text.stroke-128"),sQuery(id+"FHMxAyK4CFUKdhS_1.wireOp",EDGE,"1cb9c079-ea9b-4899-8069-e0e3048e911d.sketch_text.stroke-129"),sQuery(id+"FHMxAyK4CFUKdhS_1.wireOp",EDGE,"1cb9c079-ea9b-4899-8069-e0e3048e911d.sketch_text.stroke-130"),sQuery(id+"FHMxAyK4CFUKdhS_1.wireOp",EDGE,"1cb9c079-ea9b-4899-8069-e0e3048e911d.sketch_text.stroke-131"),sQuery(id+"FHMxAyK4CFUKdhS_1.wireOp",EDGE,"1cb9c079-ea9b-4899-8069-e0e3048e911d.sketch_text.stroke-132"),sQuery(id+"FHMxAyK4CFUKdhS_1.wireOp",EDGE,"1cb9c079-ea9b-4899-8069-e0e3048e911d.sketch_text.stroke-133"),sQuery(id+"FHMxAyK4CFUKdhS_1.wireOp",EDGE,"1cb9c079-ea9b-4899-8069-e0e3048e911d.sketch_text.stroke-134"),sQuery(id+"FHMxAyK4CFUKdhS_1.wireOp",EDGE,"1cb9c079-ea9b-4899-8069-e0e3048e911d.sketch_text.stroke-135"),sQuery(id+"FHMxAyK4CFUKdhS_1.wireOp",EDGE,"1cb9c079-ea9b-4899-8069-e0e3048e911d.sketch_text.stroke-136"),sQuery(id+"FHMxAyK4CFUKdhS_1.wireOp",EDGE,"1cb9c079-ea9b-4899-8069-e0e3048e911d.sketch_text.stroke-137"),sQuery(id+"FHMxAyK4CFUKdhS_1.wireOp",EDGE,"1cb9c079-ea9b-4899-8069-e0e3048e911d.sketch_text.stroke-138"),sQuery(id+"FHMxAyK4CFUKdhS_1.wireOp",EDGE,"1cb9c079-ea9b-4899-8069-e0e3048e911d.sketch_text.stroke-139"),sQuery(id+"FHMxAyK4CFUKdhS_1.wireOp",EDGE,"1cb9c079-ea9b-4899-8069-e0e3048e911d.sketch_text.stroke-140"),sQuery(id+"FHMxAyK4CFUKdhS_1.wireOp",EDGE,"1cb9c079-ea9b-4899-8069-e0e3048e911d.sketch_text.stroke-141"),sQuery(id+"FHMxAyK4CFUKdhS_1.wireOp",EDGE,"1cb9c079-ea9b-4899-8069-e0e3048e911d.sketch_text.stroke-142"),sQuery(id+"FHMxAyK4CFUKdhS_1.wireOp",EDGE,"1cb9c079-ea9b-4899-8069-e0e3048e911d.sketch_text.stroke-143"),sQuery(id+"FHMxAyK4CFUKdhS_1.wireOp",EDGE,"1cb9c079-ea9b-4899-8069-e0e3048e911d.sketch_text.stroke-144"),sQuery(id+"FHMxAyK4CFUKdhS_1.wireOp",EDGE,"1cb9c079-ea9b-4899-8069-e0e3048e911d.sketch_text.stroke-145"),sQuery(id+"FHMxAyK4CFUKdhS_1.wireOp",EDGE,"1cb9c079-ea9b-4899-8069-e0e3048e911d.sketch_text.stroke-146"),sQuery(id+"FHMxAyK4CFUKdhS_1.wireOp",EDGE,"1cb9c079-ea9b-4899-8069-e0e3048e911d.sketch_text.stroke-147"),sQuery(id+"FHMxAyK4CFUKdhS_1.wireOp",EDGE,"1cb9c079-ea9b-4899-8069-e0e3048e911d.sketch_text.stroke-148"),sQuery(id+"FHMxAyK4CFUKdhS_1.wireOp",EDGE,"1cb9c079-ea9b-4899-8069-e0e3048e911d.sketch_text.stroke-149"),sQuery(id+"FHMxAyK4CFUKdhS_1.wireOp",EDGE,"1cb9c079-ea9b-4899-8069-e0e3048e911d.sketch_text.stroke-150"),sQuery(id+"FHMxAyK4CFUKdhS_1.wireOp",EDGE,"1cb9c079-ea9b-4899-8069-e0e3048e911d.sketch_text.stroke-151"),sQuery(id+"FHMxAyK4CFUKdhS_1.wireOp",EDGE,"1cb9c079-ea9b-4899-8069-e0e3048e911d.sketch_text.stroke-152"),sQuery(id+"FHMxAyK4CFUKdhS_1.wireOp",EDGE,"1cb9c079-ea9b-4899-8069-e0e3048e911d.sketch_text.stroke-153"),sQuery(id+"FHMxAyK4CFUKdhS_1.wireOp",EDGE,"1cb9c079-ea9b-4899-8069-e0e3048e911d.sketch_text.stroke-159"),sQuery(id+"FHMxAyK4CFUKdhS_1.wireOp",EDGE,"1cb9c079-ea9b-4899-8069-e0e3048e911d.sketch_text.stroke-160"),sQuery(id+"FHMxAyK4CFUKdhS_1.wireOp",EDGE,"1cb9c079-ea9b-4899-8069-e0e3048e911d.sketch_text.stroke-161"),sQuery(id+"FHMxAyK4CFUKdhS_1.wireOp",EDGE,"1cb9c079-ea9b-4899-8069-e0e3048e911d.sketch_text.stroke-162"),sQuery(id+"FHMxAyK4CFUKdhS_1.wireOp",EDGE,"1cb9c079-ea9b-4899-8069-e0e3048e911d.sketch_text.stroke-163"),sQuery(id+"FHMxAyK4CFUKdhS_1.wireOp",EDGE,"1cb9c079-ea9b-4899-8069-e0e3048e911d.sketch_text.stroke-164"),sQuery(id+"FHMxAyK4CFUKdhS_1.wireOp",EDGE,"1cb9c079-ea9b-4899-8069-e0e3048e911d.sketch_text.stroke-165"),sQuery(id+"FHMxAyK4CFUKdhS_1.wireOp",EDGE,"1cb9c079-ea9b-4899-8069-e0e3048e911d.sketch_text.stroke-166"),sQuery(id+"FHMxAyK4CFUKdhS_1.wireOp",EDGE,"1cb9c079-ea9b-4899-8069-e0e3048e911d.sketch_text.stroke-167"),sQuery(id+"FHMxAyK4CFUKdhS_1.wireOp",EDGE,"1cb9c079-ea9b-4899-8069-e0e3048e911d.sketch_text.stroke-168"),sQuery(id+"FHMxAyK4CFUKdhS_1.wireOp",EDGE,"1cb9c079-ea9b-4899-8069-e0e3048e911d.sketch_text.stroke-169"),sQuery(id+"FHMxAyK4CFUKdhS_1.wireOp",EDGE,"1cb9c079-ea9b-4899-8069-e0e3048e911d.sketch_text.stroke-170"),sQuery(id+"FHMxAyK4CFUKdhS_1.wireOp",EDGE,"1cb9c079-ea9b-4899-8069-e0e3048e911d.sketch_text.stroke-171"),sQuery(id+"FHMxAyK4CFUKdhS_1.wireOp",EDGE,"1cb9c079-ea9b-4899-8069-e0e3048e911d.sketch_text.stroke-172"),sQuery(id+"FHMxAyK4CFUKdhS_1.wireOp",EDGE,"1cb9c079-ea9b-4899-8069-e0e3048e911d.sketch_text.stroke-173"),sQuery(id+"FHMxAyK4CFUKdhS_1.wireOp",EDGE,"1cb9c079-ea9b-4899-8069-e0e3048e911d.sketch_text.stroke-174"),sQuery(id+"FHMxAyK4CFUKdhS_1.wireOp",EDGE,"1cb9c079-ea9b-4899-8069-e0e3048e911d.sketch_text.stroke-175"),sQuery(id+"FHMxAyK4CFUKdhS_1.wireOp",EDGE,"1cb9c079-ea9b-4899-8069-e0e3048e911d.sketch_text.stroke-176"),sQuery(id+"FHMxAyK4CFUKdhS_1.wireOp",EDGE,"1cb9c079-ea9b-4899-8069-e0e3048e911d.sketch_text.stroke-177"),sQuery(id+"FHMxAyK4CFUKdhS_1.wireOp",EDGE,"1cb9c079-ea9b-4899-8069-e0e3048e911d.sketch_text.stroke-178"),sQuery(id+"FHMxAyK4CFUKdhS_1.wireOp",EDGE,"1cb9c079-ea9b-4899-8069-e0e3048e911d.sketch_text.stroke-179"),sQuery(id+"FHMxAyK4CFUKdhS_1.wireOp",EDGE,"1cb9c079-ea9b-4899-8069-e0e3048e911d.sketch_text.stroke-180"),sQuery(id+"F3.wireOp",EDGE,"8007402e-1a4e-4a06-85a5-2af08e553504"),subQ2])],"isStart":true}),makeQuery(id+"F4.opExtrude","SWEPT_FACE",FACE,{"disambiguationData":[OSD([subQ2])]})])],"derivedFrom":makeQuery(id+"F4.opExtrude","CAP_EDGE",EDGE,{"disambiguationData":[OSD([subQ2])],"isStart":true})});}
            var Q8;
            Q8=makeQuery(id+"F1.opExtrude","CAP_EDGE",EDGE,{"disambiguationData":[OSD([sQuery(id+"F0.wireOp",EDGE,"E0.right")])],"isStart":false});
            var Q9;
            {var subQ0=sQuery(id+"F0.wireOp",EDGE,"E0.top");var subQ1=sQuery(id+"F0.wireOp",EDGE,"E0.bottom");var subQ2=sQuery(id+"F3.wireOp",EDGE,"6ee83ff3-586e-4dbe-aaea-af71240543bd");Q9=makeQuery(id+"F4.boolean.opBoolean","SPLIT",EDGE,{"disambiguationData":[TD([makeQuery(id+"F1.opExtrude","CAP_FACE",FACE,{"disambiguationData":[OSD([subQ1,subQ0,sQuery(id+"F0.wireOp",EDGE,"E0.left"),sQuery(id+"F0.wireOp",EDGE,"E0.right")])],"isStart":false}),makeQuery(id+"F1.opExtrude","SWEPT_FACE",FACE,{"disambiguationData":[OSD([subQ0])]}),makeQuery(id+"F4.opExtrude","CAP_FACE",FACE,{"disambiguationData":[OSD([subQ1,sQuery(id+"F2.wireOp",EDGE,"fcba4419-a2ee-464f-be9d-58f11bf3418b.sketch_text.stroke-0"),sQuery(id+"F2.wireOp",EDGE,"fcba4419-a2ee-464f-be9d-58f11bf3418b.sketch_text.stroke-1"),sQuery(id+"F2.wireOp",EDGE,"fcba4419-a2ee-464f-be9d-58f11bf3418b.sketch_text.stroke-2"),sQuery(id+"F2.wireOp",EDGE,"fcba4419-a2ee-464f-be9d-58f11bf3418b.sketch_text.stroke-3"),sQuery(id+"F2.wireOp",EDGE,"fcba4419-a2ee-464f-be9d-58f11bf3418b.sketch_text.stroke-4"),sQuery(id+"F2.wireOp",EDGE,"fcba4419-a2ee-464f-be9d-58f11bf3418b.sketch_text.stroke-5"),sQuery(id+"F2.wireOp",EDGE,"fcba4419-a2ee-464f-be9d-58f11bf3418b.sketch_text.stroke-6"),sQuery(id+"F2.wireOp",EDGE,"fcba4419-a2ee-464f-be9d-58f11bf3418b.sketch_text.stroke-7"),sQuery(id+"F2.wireOp",EDGE,"fcba4419-a2ee-464f-be9d-58f11bf3418b.sketch_text.stroke-8"),sQuery(id+"F2.wireOp",EDGE,"fcba4419-a2ee-464f-be9d-58f11bf3418b.sketch_text.stroke-9"),sQuery(id+"F2.wireOp",EDGE,"fcba4419-a2ee-464f-be9d-58f11bf3418b.sketch_text.stroke-10"),sQuery(id+"F2.wireOp",EDGE,"fcba4419-a2ee-464f-be9d-58f11bf3418b.sketch_text.stroke-11"),sQuery(id+"F2.wireOp",EDGE,"fcba4419-a2ee-464f-be9d-58f11bf3418b.sketch_text.stroke-12"),sQuery(id+"F2.wireOp",EDGE,"fcba4419-a2ee-464f-be9d-58f11bf3418b.sketch_text.stroke-13"),sQuery(id+"F2.wireOp",EDGE,"fcba4419-a2ee-464f-be9d-58f11bf3418b.sketch_text.stroke-14"),sQuery(id+"F2.wireOp",EDGE,"fcba4419-a2ee-464f-be9d-58f11bf3418b.sketch_text.stroke-15"),sQuery(id+"F2.wireOp",EDGE,"fcba4419-a2ee-464f-be9d-58f11bf3418b.sketch_text.stroke-16"),sQuery(id+"F2.wireOp",EDGE,"fcba4419-a2ee-464f-be9d-58f11bf3418b.sketch_text.stroke-17"),sQuery(id+"F2.wireOp",EDGE,"fcba4419-a2ee-464f-be9d-58f11bf3418b.sketch_text.stroke-18"),sQuery(id+"F2.wireOp",EDGE,"fcba4419-a2ee-464f-be9d-58f11bf3418b.sketch_text.stroke-19"),sQuery(id+"F2.wireOp",EDGE,"fcba4419-a2ee-464f-be9d-58f11bf3418b.sketch_text.stroke-20"),sQuery(id+"F2.wireOp",EDGE,"fcba4419-a2ee-464f-be9d-58f11bf3418b.sketch_text.stroke-21"),sQuery(id+"F2.wireOp",EDGE,"fcba4419-a2ee-464f-be9d-58f11bf3418b.sketch_text.stroke-22"),sQuery(id+"F2.wireOp",EDGE,"fcba4419-a2ee-464f-be9d-58f11bf3418b.sketch_text.stroke-23"),sQuery(id+"F2.wireOp",EDGE,"fcba4419-a2ee-464f-be9d-58f11bf3418b.sketch_text.stroke-24"),sQuery(id+"F2.wireOp",EDGE,"fcba4419-a2ee-464f-be9d-58f11bf3418b.sketch_text.stroke-25"),sQuery(id+"F2.wireOp",EDGE,"fcba4419-a2ee-464f-be9d-58f11bf3418b.sketch_text.stroke-26"),sQuery(id+"F2.wireOp",EDGE,"fcba4419-a2ee-464f-be9d-58f11bf3418b.sketch_text.stroke-27"),sQuery(id+"F2.wireOp",EDGE,"fcba4419-a2ee-464f-be9d-58f11bf3418b.sketch_text.stroke-28"),sQuery(id+"F2.wireOp",EDGE,"fcba4419-a2ee-464f-be9d-58f11bf3418b.sketch_text.stroke-29"),sQuery(id+"F2.wireOp",EDGE,"fcba4419-a2ee-464f-be9d-58f11bf3418b.sketch_text.stroke-30"),sQuery(id+"F2.wireOp",EDGE,"fcba4419-a2ee-464f-be9d-58f11bf3418b.sketch_text.stroke-31"),sQuery(id+"F2.wireOp",EDGE,"fcba4419-a2ee-464f-be9d-58f11bf3418b.sketch_text.stroke-32"),sQuery(id+"F2.wireOp",EDGE,"fcba4419-a2ee-464f-be9d-58f11bf3418b.sketch_text.stroke-33"),sQuery(id+"F2.wireOp",EDGE,"fcba4419-a2ee-464f-be9d-58f11bf3418b.sketch_text.stroke-34"),sQuery(id+"F2.wireOp",EDGE,"fcba4419-a2ee-464f-be9d-58f11bf3418b.sketch_text.stroke-35"),sQuery(id+"F2.wireOp",EDGE,"fcba4419-a2ee-464f-be9d-58f11bf3418b.sketch_text.stroke-36"),sQuery(id+"F2.wireOp",EDGE,"fcba4419-a2ee-464f-be9d-58f11bf3418b.sketch_text.stroke-37"),sQuery(id+"F2.wireOp",EDGE,"fcba4419-a2ee-464f-be9d-58f11bf3418b.sketch_text.stroke-38"),sQuery(id+"F2.wireOp",EDGE,"fcba4419-a2ee-464f-be9d-58f11bf3418b.sketch_text.stroke-39"),sQuery(id+"F2.wireOp",EDGE,"fcba4419-a2ee-464f-be9d-58f11bf3418b.sketch_text.stroke-40"),sQuery(id+"F2.wireOp",EDGE,"fcba4419-a2ee-464f-be9d-58f11bf3418b.sketch_text.stroke-41"),sQuery(id+"F2.wireOp",EDGE,"fcba4419-a2ee-464f-be9d-58f11bf3418b.sketch_text.stroke-42"),sQuery(id+"F2.wireOp",EDGE,"fcba4419-a2ee-464f-be9d-58f11bf3418b.sketch_text.stroke-43"),sQuery(id+"F2.wireOp",EDGE,"fcba4419-a2ee-464f-be9d-58f11bf3418b.sketch_text.stroke-44"),sQuery(id+"F2.wireOp",EDGE,"fcba4419-a2ee-464f-be9d-58f11bf3418b.sketch_text.stroke-45"),sQuery(id+"F2.wireOp",EDGE,"fcba4419-a2ee-464f-be9d-58f11bf3418b.sketch_text.stroke-46"),sQuery(id+"F2.wireOp",EDGE,"fcba4419-a2ee-464f-be9d-58f11bf3418b.sketch_text.stroke-47"),sQuery(id+"F2.wireOp",EDGE,"fcba4419-a2ee-464f-be9d-58f11bf3418b.sketch_text.stroke-48"),sQuery(id+"F2.wireOp",EDGE,"fcba4419-a2ee-464f-be9d-58f11bf3418b.sketch_text.stroke-49"),sQuery(id+"F2.wireOp",EDGE,"fcba4419-a2ee-464f-be9d-58f11bf3418b.sketch_text.stroke-50"),sQuery(id+"F2.wireOp",EDGE,"fcba4419-a2ee-464f-be9d-58f11bf3418b.sketch_text.stroke-51"),sQuery(id+"F2.wireOp",EDGE,"fcba4419-a2ee-464f-be9d-58f11bf3418b.sketch_text.stroke-52"),sQuery(id+"F2.wireOp",EDGE,"fcba4419-a2ee-464f-be9d-58f11bf3418b.sketch_text.stroke-53"),sQuery(id+"F2.wireOp",EDGE,"fcba4419-a2ee-464f-be9d-58f11bf3418b.sketch_text.stroke-54"),sQuery(id+"F2.wireOp",EDGE,"fcba4419-a2ee-464f-be9d-58f11bf3418b.sketch_text.stroke-55"),sQuery(id+"F2.wireOp",EDGE,"fcba4419-a2ee-464f-be9d-58f11bf3418b.sketch_text.stroke-56"),sQuery(id+"F2.wireOp",EDGE,"fcba4419-a2ee-464f-be9d-58f11bf3418b.sketch_text.stroke-57"),sQuery(id+"F2.wireOp",EDGE,"fcba4419-a2ee-464f-be9d-58f11bf3418b.sketch_text.stroke-58"),sQuery(id+"F2.wireOp",EDGE,"fcba4419-a2ee-464f-be9d-58f11bf3418b.sketch_text.stroke-59"),sQuery(id+"F2.wireOp",EDGE,"fcba4419-a2ee-464f-be9d-58f11bf3418b.sketch_text.stroke-60"),sQuery(id+"F2.wireOp",EDGE,"fcba4419-a2ee-464f-be9d-58f11bf3418b.sketch_text.stroke-61"),sQuery(id+"F2.wireOp",EDGE,"fcba4419-a2ee-464f-be9d-58f11bf3418b.sketch_text.stroke-62"),sQuery(id+"F2.wireOp",EDGE,"fcba4419-a2ee-464f-be9d-58f11bf3418b.sketch_text.stroke-63"),sQuery(id+"F2.wireOp",EDGE,"fcba4419-a2ee-464f-be9d-58f11bf3418b.sketch_text.stroke-64"),sQuery(id+"F2.wireOp",EDGE,"fcba4419-a2ee-464f-be9d-58f11bf3418b.sketch_text.stroke-65"),sQuery(id+"F2.wireOp",EDGE,"fcba4419-a2ee-464f-be9d-58f11bf3418b.sketch_text.stroke-66"),sQuery(id+"F2.wireOp",EDGE,"fcba4419-a2ee-464f-be9d-58f11bf3418b.sketch_text.stroke-67"),sQuery(id+"F2.wireOp",EDGE,"fcba4419-a2ee-464f-be9d-58f11bf3418b.sketch_text.stroke-68"),sQuery(id+"F2.wireOp",EDGE,"fcba4419-a2ee-464f-be9d-58f11bf3418b.sketch_text.stroke-69"),sQuery(id+"F2.wireOp",EDGE,"fcba4419-a2ee-464f-be9d-58f11bf3418b.sketch_text.stroke-70"),sQuery(id+"F2.wireOp",EDGE,"fcba4419-a2ee-464f-be9d-58f11bf3418b.sketch_text.stroke-71"),sQuery(id+"F2.wireOp",EDGE,"fcba4419-a2ee-464f-be9d-58f11bf3418b.sketch_text.stroke-72"),sQuery(id+"F2.wireOp",EDGE,"fcba4419-a2ee-464f-be9d-58f11bf3418b.sketch_text.stroke-73"),sQuery(id+"F2.wireOp",EDGE,"fcba4419-a2ee-464f-be9d-58f11bf3418b.sketch_text.stroke-74"),sQuery(id+"F2.wireOp",EDGE,"fcba4419-a2ee-464f-be9d-58f11bf3418b.sketch_text.stroke-75"),sQuery(id+"F2.wireOp",EDGE,"fcba4419-a2ee-464f-be9d-58f11bf3418b.sketch_text.stroke-76"),sQuery(id+"F2.wireOp",EDGE,"fcba4419-a2ee-464f-be9d-58f11bf3418b.sketch_text.stroke-77"),sQuery(id+"F2.wireOp",EDGE,"fcba4419-a2ee-464f-be9d-58f11bf3418b.sketch_text.stroke-78"),sQuery(id+"F2.wireOp",EDGE,"fcba4419-a2ee-464f-be9d-58f11bf3418b.sketch_text.stroke-79"),sQuery(id+"F2.wireOp",EDGE,"fcba4419-a2ee-464f-be9d-58f11bf3418b.sketch_text.stroke-80"),sQuery(id+"F2.wireOp",EDGE,"fcba4419-a2ee-464f-be9d-58f11bf3418b.sketch_text.stroke-81"),sQuery(id+"F2.wireOp",EDGE,"fcba4419-a2ee-464f-be9d-58f11bf3418b.sketch_text.stroke-82"),sQuery(id+"F2.wireOp",EDGE,"fcba4419-a2ee-464f-be9d-58f11bf3418b.sketch_text.stroke-83"),sQuery(id+"F2.wireOp",EDGE,"fcba4419-a2ee-464f-be9d-58f11bf3418b.sketch_text.stroke-84"),sQuery(id+"F2.wireOp",EDGE,"fcba4419-a2ee-464f-be9d-58f11bf3418b.sketch_text.stroke-85"),sQuery(id+"F2.wireOp",EDGE,"fcba4419-a2ee-464f-be9d-58f11bf3418b.sketch_text.stroke-86"),sQuery(id+"F2.wireOp",EDGE,"fcba4419-a2ee-464f-be9d-58f11bf3418b.sketch_text.stroke-87"),sQuery(id+"F2.wireOp",EDGE,"fcba4419-a2ee-464f-be9d-58f11bf3418b.sketch_text.stroke-88"),sQuery(id+"F2.wireOp",EDGE,"fcba4419-a2ee-464f-be9d-58f11bf3418b.sketch_text.stroke-89"),sQuery(id+"F2.wireOp",EDGE,"fcba4419-a2ee-464f-be9d-58f11bf3418b.sketch_text.stroke-90"),sQuery(id+"F2.wireOp",EDGE,"fcba4419-a2ee-464f-be9d-58f11bf3418b.sketch_text.stroke-91"),sQuery(id+"F2.wireOp",EDGE,"fcba4419-a2ee-464f-be9d-58f11bf3418b.sketch_text.stroke-92"),sQuery(id+"F2.wireOp",EDGE,"fcba4419-a2ee-464f-be9d-58f11bf3418b.sketch_text.stroke-93"),sQuery(id+"F2.wireOp",EDGE,"fcba4419-a2ee-464f-be9d-58f11bf3418b.sketch_text.stroke-94"),sQuery(id+"F2.wireOp",EDGE,"fcba4419-a2ee-464f-be9d-58f11bf3418b.sketch_text.stroke-95"),sQuery(id+"F2.wireOp",EDGE,"fcba4419-a2ee-464f-be9d-58f11bf3418b.sketch_text.stroke-96"),sQuery(id+"F2.wireOp",EDGE,"fcba4419-a2ee-464f-be9d-58f11bf3418b.sketch_text.stroke-97"),sQuery(id+"F2.wireOp",EDGE,"fcba4419-a2ee-464f-be9d-58f11bf3418b.sketch_text.stroke-98"),sQuery(id+"F2.wireOp",EDGE,"fcba4419-a2ee-464f-be9d-58f11bf3418b.sketch_text.stroke-99"),sQuery(id+"F2.wireOp",EDGE,"fcba4419-a2ee-464f-be9d-58f11bf3418b.sketch_text.stroke-100"),sQuery(id+"F2.wireOp",EDGE,"fcba4419-a2ee-464f-be9d-58f11bf3418b.sketch_text.stroke-101"),sQuery(id+"F2.wireOp",EDGE,"fcba4419-a2ee-464f-be9d-58f11bf3418b.sketch_text.stroke-102"),sQuery(id+"F2.wireOp",EDGE,"fcba4419-a2ee-464f-be9d-58f11bf3418b.sketch_text.stroke-103"),sQuery(id+"F2.wireOp",EDGE,"fcba4419-a2ee-464f-be9d-58f11bf3418b.sketch_text.stroke-104"),sQuery(id+"F2.wireOp",EDGE,"fcba4419-a2ee-464f-be9d-58f11bf3418b.sketch_text.stroke-105"),sQuery(id+"F2.wireOp",EDGE,"fcba4419-a2ee-464f-be9d-58f11bf3418b.sketch_text.stroke-106"),sQuery(id+"F2.wireOp",EDGE,"fcba4419-a2ee-464f-be9d-58f11bf3418b.sketch_text.stroke-107"),sQuery(id+"F2.wireOp",EDGE,"fcba4419-a2ee-464f-be9d-58f11bf3418b.sketch_text.stroke-108"),sQuery(id+"F2.wireOp",EDGE,"fcba4419-a2ee-464f-be9d-58f11bf3418b.sketch_text.stroke-109"),sQuery(id+"F2.wireOp",EDGE,"fcba4419-a2ee-464f-be9d-58f11bf3418b.sketch_text.stroke-110"),sQuery(id+"F2.wireOp",EDGE,"fcba4419-a2ee-464f-be9d-58f11bf3418b.sketch_text.stroke-111"),sQuery(id+"F2.wireOp",EDGE,"fcba4419-a2ee-464f-be9d-58f11bf3418b.sketch_text.stroke-112"),sQuery(id+"F2.wireOp",EDGE,"fcba4419-a2ee-464f-be9d-58f11bf3418b.sketch_text.stroke-113"),sQuery(id+"F2.wireOp",EDGE,"fcba4419-a2ee-464f-be9d-58f11bf3418b.sketch_text.stroke-114"),sQuery(id+"F2.wireOp",EDGE,"fcba4419-a2ee-464f-be9d-58f11bf3418b.sketch_text.stroke-115"),sQuery(id+"F2.wireOp",EDGE,"fcba4419-a2ee-464f-be9d-58f11bf3418b.sketch_text.stroke-116"),sQuery(id+"F2.wireOp",EDGE,"fcba4419-a2ee-464f-be9d-58f11bf3418b.sketch_text.stroke-117"),sQuery(id+"F2.wireOp",EDGE,"fcba4419-a2ee-464f-be9d-58f11bf3418b.sketch_text.stroke-118"),sQuery(id+"F2.wireOp",EDGE,"fcba4419-a2ee-464f-be9d-58f11bf3418b.sketch_text.stroke-119"),sQuery(id+"F2.wireOp",EDGE,"fcba4419-a2ee-464f-be9d-58f11bf3418b.sketch_text.stroke-120"),sQuery(id+"F2.wireOp",EDGE,"fcba4419-a2ee-464f-be9d-58f11bf3418b.sketch_text.stroke-121"),sQuery(id+"F2.wireOp",EDGE,"fcba4419-a2ee-464f-be9d-58f11bf3418b.sketch_text.stroke-122"),sQuery(id+"F2.wireOp",EDGE,"fcba4419-a2ee-464f-be9d-58f11bf3418b.sketch_text.stroke-123"),sQuery(id+"F2.wireOp",EDGE,"fcba4419-a2ee-464f-be9d-58f11bf3418b.sketch_text.stroke-124"),sQuery(id+"F2.wireOp",EDGE,"fcba4419-a2ee-464f-be9d-58f11bf3418b.sketch_text.stroke-125"),sQuery(id+"F2.wireOp",EDGE,"fcba4419-a2ee-464f-be9d-58f11bf3418b.sketch_text.stroke-126"),sQuery(id+"F2.wireOp",EDGE,"fcba4419-a2ee-464f-be9d-58f11bf3418b.sketch_text.stroke-127"),sQuery(id+"F2.wireOp",EDGE,"fcba4419-a2ee-464f-be9d-58f11bf3418b.sketch_text.stroke-128"),sQuery(id+"F2.wireOp",EDGE,"fcba4419-a2ee-464f-be9d-58f11bf3418b.sketch_text.stroke-129"),sQuery(id+"F2.wireOp",EDGE,"fcba4419-a2ee-464f-be9d-58f11bf3418b.sketch_text.stroke-130"),sQuery(id+"F2.wireOp",EDGE,"fcba4419-a2ee-464f-be9d-58f11bf3418b.sketch_text.stroke-131"),sQuery(id+"F2.wireOp",EDGE,"fcba4419-a2ee-464f-be9d-58f11bf3418b.sketch_text.stroke-132"),sQuery(id+"F2.wireOp",EDGE,"fcba4419-a2ee-464f-be9d-58f11bf3418b.sketch_text.stroke-133"),sQuery(id+"F2.wireOp",EDGE,"fcba4419-a2ee-464f-be9d-58f11bf3418b.sketch_text.stroke-134"),sQuery(id+"F2.wireOp",EDGE,"fcba4419-a2ee-464f-be9d-58f11bf3418b.sketch_text.stroke-135"),sQuery(id+"F2.wireOp",EDGE,"fcba4419-a2ee-464f-be9d-58f11bf3418b.sketch_text.stroke-136"),sQuery(id+"F2.wireOp",EDGE,"fcba4419-a2ee-464f-be9d-58f11bf3418b.sketch_text.stroke-137"),sQuery(id+"F2.wireOp",EDGE,"fcba4419-a2ee-464f-be9d-58f11bf3418b.sketch_text.stroke-138"),sQuery(id+"F2.wireOp",EDGE,"fcba4419-a2ee-464f-be9d-58f11bf3418b.sketch_text.stroke-139"),sQuery(id+"F2.wireOp",EDGE,"fcba4419-a2ee-464f-be9d-58f11bf3418b.sketch_text.stroke-140"),sQuery(id+"F2.wireOp",EDGE,"fcba4419-a2ee-464f-be9d-58f11bf3418b.sketch_text.stroke-141"),sQuery(id+"F2.wireOp",EDGE,"fcba4419-a2ee-464f-be9d-58f11bf3418b.sketch_text.stroke-142"),sQuery(id+"F2.wireOp",EDGE,"fcba4419-a2ee-464f-be9d-58f11bf3418b.sketch_text.stroke-143"),sQuery(id+"F2.wireOp",EDGE,"fcba4419-a2ee-464f-be9d-58f11bf3418b.sketch_text.stroke-144"),sQuery(id+"F2.wireOp",EDGE,"fcba4419-a2ee-464f-be9d-58f11bf3418b.sketch_text.stroke-145"),sQuery(id+"F2.wireOp",EDGE,"fcba4419-a2ee-464f-be9d-58f11bf3418b.sketch_text.stroke-146"),sQuery(id+"F2.wireOp",EDGE,"fcba4419-a2ee-464f-be9d-58f11bf3418b.sketch_text.stroke-147"),sQuery(id+"F2.wireOp",EDGE,"fcba4419-a2ee-464f-be9d-58f11bf3418b.sketch_text.stroke-148"),sQuery(id+"F2.wireOp",EDGE,"fcba4419-a2ee-464f-be9d-58f11bf3418b.sketch_text.stroke-149"),sQuery(id+"F2.wireOp",EDGE,"fcba4419-a2ee-464f-be9d-58f11bf3418b.sketch_text.stroke-150"),sQuery(id+"F2.wireOp",EDGE,"fcba4419-a2ee-464f-be9d-58f11bf3418b.sketch_text.stroke-151"),sQuery(id+"F2.wireOp",EDGE,"fcba4419-a2ee-464f-be9d-58f11bf3418b.sketch_text.stroke-152"),sQuery(id+"F2.wireOp",EDGE,"fcba4419-a2ee-464f-be9d-58f11bf3418b.sketch_text.stroke-153"),sQuery(id+"F2.wireOp",EDGE,"fcba4419-a2ee-464f-be9d-58f11bf3418b.sketch_text.stroke-154"),sQuery(id+"F2.wireOp",EDGE,"fcba4419-a2ee-464f-be9d-58f11bf3418b.sketch_text.stroke-155"),sQuery(id+"F2.wireOp",EDGE,"fcba4419-a2ee-464f-be9d-58f11bf3418b.sketch_text.stroke-156"),sQuery(id+"F2.wireOp",EDGE,"fcba4419-a2ee-464f-be9d-58f11bf3418b.sketch_text.stroke-157"),sQuery(id+"F2.wireOp",EDGE,"fcba4419-a2ee-464f-be9d-58f11bf3418b.sketch_text.stroke-158"),sQuery(id+"F2.wireOp",EDGE,"fcba4419-a2ee-464f-be9d-58f11bf3418b.sketch_text.stroke-159"),sQuery(id+"F2.wireOp",EDGE,"fcba4419-a2ee-464f-be9d-58f11bf3418b.sketch_text.stroke-160"),sQuery(id+"F2.wireOp",EDGE,"fcba4419-a2ee-464f-be9d-58f11bf3418b.sketch_text.stroke-161"),sQuery(id+"F2.wireOp",EDGE,"fcba4419-a2ee-464f-be9d-58f11bf3418b.sketch_text.stroke-162"),sQuery(id+"F2.wireOp",EDGE,"fcba4419-a2ee-464f-be9d-58f11bf3418b.sketch_text.stroke-163"),sQuery(id+"F2.wireOp",EDGE,"fcba4419-a2ee-464f-be9d-58f11bf3418b.sketch_text.stroke-164"),sQuery(id+"F2.wireOp",EDGE,"fcba4419-a2ee-464f-be9d-58f11bf3418b.sketch_text.stroke-165"),sQuery(id+"F2.wireOp",EDGE,"fcba4419-a2ee-464f-be9d-58f11bf3418b.sketch_text.stroke-166"),sQuery(id+"F2.wireOp",EDGE,"fcba4419-a2ee-464f-be9d-58f11bf3418b.sketch_text.stroke-167"),sQuery(id+"F2.wireOp",EDGE,"fcba4419-a2ee-464f-be9d-58f11bf3418b.sketch_text.stroke-168"),sQuery(id+"F2.wireOp",EDGE,"fcba4419-a2ee-464f-be9d-58f11bf3418b.sketch_text.stroke-169"),sQuery(id+"F2.wireOp",EDGE,"fcba4419-a2ee-464f-be9d-58f11bf3418b.sketch_text.stroke-170"),sQuery(id+"F2.wireOp",EDGE,"fcba4419-a2ee-464f-be9d-58f11bf3418b.sketch_text.stroke-171"),sQuery(id+"F2.wireOp",EDGE,"fcba4419-a2ee-464f-be9d-58f11bf3418b.sketch_text.stroke-172"),sQuery(id+"F2.wireOp",EDGE,"fcba4419-a2ee-464f-be9d-58f11bf3418b.sketch_text.stroke-173"),sQuery(id+"FHMxAyK4CFUKdhS_1.wireOp",EDGE,"1cb9c079-ea9b-4899-8069-e0e3048e911d.sketch_text.stroke-0"),sQuery(id+"FHMxAyK4CFUKdhS_1.wireOp",EDGE,"1cb9c079-ea9b-4899-8069-e0e3048e911d.sketch_text.stroke-1"),sQuery(id+"FHMxAyK4CFUKdhS_1.wireOp",EDGE,"1cb9c079-ea9b-4899-8069-e0e3048e911d.sketch_text.stroke-2"),sQuery(id+"FHMxAyK4CFUKdhS_1.wireOp",EDGE,"1cb9c079-ea9b-4899-8069-e0e3048e911d.sketch_text.stroke-3"),sQuery(id+"FHMxAyK4CFUKdhS_1.wireOp",EDGE,"1cb9c079-ea9b-4899-8069-e0e3048e911d.sketch_text.stroke-4"),sQuery(id+"FHMxAyK4CFUKdhS_1.wireOp",EDGE,"1cb9c079-ea9b-4899-8069-e0e3048e911d.sketch_text.stroke-5"),sQuery(id+"FHMxAyK4CFUKdhS_1.wireOp",EDGE,"1cb9c079-ea9b-4899-8069-e0e3048e911d.sketch_text.stroke-6"),sQuery(id+"FHMxAyK4CFUKdhS_1.wireOp",EDGE,"1cb9c079-ea9b-4899-8069-e0e3048e911d.sketch_text.stroke-7"),sQuery(id+"FHMxAyK4CFUKdhS_1.wireOp",EDGE,"1cb9c079-ea9b-4899-8069-e0e3048e911d.sketch_text.stroke-8"),sQuery(id+"FHMxAyK4CFUKdhS_1.wireOp",EDGE,"1cb9c079-ea9b-4899-8069-e0e3048e911d.sketch_text.stroke-9"),sQuery(id+"FHMxAyK4CFUKdhS_1.wireOp",EDGE,"1cb9c079-ea9b-4899-8069-e0e3048e911d.sketch_text.stroke-10"),sQuery(id+"FHMxAyK4CFUKdhS_1.wireOp",EDGE,"1cb9c079-ea9b-4899-8069-e0e3048e911d.sketch_text.stroke-11"),sQuery(id+"FHMxAyK4CFUKdhS_1.wireOp",EDGE,"1cb9c079-ea9b-4899-8069-e0e3048e911d.sketch_text.stroke-12"),sQuery(id+"FHMxAyK4CFUKdhS_1.wireOp",EDGE,"1cb9c079-ea9b-4899-8069-e0e3048e911d.sketch_text.stroke-13"),sQuery(id+"FHMxAyK4CFUKdhS_1.wireOp",EDGE,"1cb9c079-ea9b-4899-8069-e0e3048e911d.sketch_text.stroke-14"),sQuery(id+"FHMxAyK4CFUKdhS_1.wireOp",EDGE,"1cb9c079-ea9b-4899-8069-e0e3048e911d.sketch_text.stroke-15"),sQuery(id+"FHMxAyK4CFUKdhS_1.wireOp",EDGE,"1cb9c079-ea9b-4899-8069-e0e3048e911d.sketch_text.stroke-16"),sQuery(id+"FHMxAyK4CFUKdhS_1.wireOp",EDGE,"1cb9c079-ea9b-4899-8069-e0e3048e911d.sketch_text.stroke-17"),sQuery(id+"FHMxAyK4CFUKdhS_1.wireOp",EDGE,"1cb9c079-ea9b-4899-8069-e0e3048e911d.sketch_text.stroke-18"),sQuery(id+"FHMxAyK4CFUKdhS_1.wireOp",EDGE,"1cb9c079-ea9b-4899-8069-e0e3048e911d.sketch_text.stroke-19"),sQuery(id+"FHMxAyK4CFUKdhS_1.wireOp",EDGE,"1cb9c079-ea9b-4899-8069-e0e3048e911d.sketch_text.stroke-20"),sQuery(id+"FHMxAyK4CFUKdhS_1.wireOp",EDGE,"1cb9c079-ea9b-4899-8069-e0e3048e911d.sketch_text.stroke-21"),sQuery(id+"FHMxAyK4CFUKdhS_1.wireOp",EDGE,"1cb9c079-ea9b-4899-8069-e0e3048e911d.sketch_text.stroke-22"),sQuery(id+"FHMxAyK4CFUKdhS_1.wireOp",EDGE,"1cb9c079-ea9b-4899-8069-e0e3048e911d.sketch_text.stroke-23"),sQuery(id+"FHMxAyK4CFUKdhS_1.wireOp",EDGE,"1cb9c079-ea9b-4899-8069-e0e3048e911d.sketch_text.stroke-24"),sQuery(id+"FHMxAyK4CFUKdhS_1.wireOp",EDGE,"1cb9c079-ea9b-4899-8069-e0e3048e911d.sketch_text.stroke-25"),sQuery(id+"FHMxAyK4CFUKdhS_1.wireOp",EDGE,"1cb9c079-ea9b-4899-8069-e0e3048e911d.sketch_text.stroke-26"),sQuery(id+"FHMxAyK4CFUKdhS_1.wireOp",EDGE,"1cb9c079-ea9b-4899-8069-e0e3048e911d.sketch_text.stroke-27"),sQuery(id+"FHMxAyK4CFUKdhS_1.wireOp",EDGE,"1cb9c079-ea9b-4899-8069-e0e3048e911d.sketch_text.stroke-28"),sQuery(id+"FHMxAyK4CFUKdhS_1.wireOp",EDGE,"1cb9c079-ea9b-4899-8069-e0e3048e911d.sketch_text.stroke-29"),sQuery(id+"FHMxAyK4CFUKdhS_1.wireOp",EDGE,"1cb9c079-ea9b-4899-8069-e0e3048e911d.sketch_text.stroke-30"),sQuery(id+"FHMxAyK4CFUKdhS_1.wireOp",EDGE,"1cb9c079-ea9b-4899-8069-e0e3048e911d.sketch_text.stroke-31"),sQuery(id+"FHMxAyK4CFUKdhS_1.wireOp",EDGE,"1cb9c079-ea9b-4899-8069-e0e3048e911d.sketch_text.stroke-32"),sQuery(id+"FHMxAyK4CFUKdhS_1.wireOp",EDGE,"1cb9c079-ea9b-4899-8069-e0e3048e911d.sketch_text.stroke-33"),sQuery(id+"FHMxAyK4CFUKdhS_1.wireOp",EDGE,"1cb9c079-ea9b-4899-8069-e0e3048e911d.sketch_text.stroke-34"),sQuery(id+"FHMxAyK4CFUKdhS_1.wireOp",EDGE,"1cb9c079-ea9b-4899-8069-e0e3048e911d.sketch_text.stroke-35"),sQuery(id+"FHMxAyK4CFUKdhS_1.wireOp",EDGE,"1cb9c079-ea9b-4899-8069-e0e3048e911d.sketch_text.stroke-36"),sQuery(id+"FHMxAyK4CFUKdhS_1.wireOp",EDGE,"1cb9c079-ea9b-4899-8069-e0e3048e911d.sketch_text.stroke-37"),sQuery(id+"FHMxAyK4CFUKdhS_1.wireOp",EDGE,"1cb9c079-ea9b-4899-8069-e0e3048e911d.sketch_text.stroke-38"),sQuery(id+"FHMxAyK4CFUKdhS_1.wireOp",EDGE,"1cb9c079-ea9b-4899-8069-e0e3048e911d.sketch_text.stroke-39"),sQuery(id+"FHMxAyK4CFUKdhS_1.wireOp",EDGE,"1cb9c079-ea9b-4899-8069-e0e3048e911d.sketch_text.stroke-40"),sQuery(id+"FHMxAyK4CFUKdhS_1.wireOp",EDGE,"1cb9c079-ea9b-4899-8069-e0e3048e911d.sketch_text.stroke-41"),sQuery(id+"FHMxAyK4CFUKdhS_1.wireOp",EDGE,"1cb9c079-ea9b-4899-8069-e0e3048e911d.sketch_text.stroke-42"),sQuery(id+"FHMxAyK4CFUKdhS_1.wireOp",EDGE,"1cb9c079-ea9b-4899-8069-e0e3048e911d.sketch_text.stroke-43"),sQuery(id+"FHMxAyK4CFUKdhS_1.wireOp",EDGE,"1cb9c079-ea9b-4899-8069-e0e3048e911d.sketch_text.stroke-44"),sQuery(id+"FHMxAyK4CFUKdhS_1.wireOp",EDGE,"1cb9c079-ea9b-4899-8069-e0e3048e911d.sketch_text.stroke-45"),sQuery(id+"FHMxAyK4CFUKdhS_1.wireOp",EDGE,"1cb9c079-ea9b-4899-8069-e0e3048e911d.sketch_text.stroke-46"),sQuery(id+"FHMxAyK4CFUKdhS_1.wireOp",EDGE,"1cb9c079-ea9b-4899-8069-e0e3048e911d.sketch_text.stroke-47"),sQuery(id+"FHMxAyK4CFUKdhS_1.wireOp",EDGE,"1cb9c079-ea9b-4899-8069-e0e3048e911d.sketch_text.stroke-48"),sQuery(id+"FHMxAyK4CFUKdhS_1.wireOp",EDGE,"1cb9c079-ea9b-4899-8069-e0e3048e911d.sketch_text.stroke-49"),sQuery(id+"FHMxAyK4CFUKdhS_1.wireOp",EDGE,"1cb9c079-ea9b-4899-8069-e0e3048e911d.sketch_text.stroke-50"),sQuery(id+"FHMxAyK4CFUKdhS_1.wireOp",EDGE,"1cb9c079-ea9b-4899-8069-e0e3048e911d.sketch_text.stroke-51"),sQuery(id+"FHMxAyK4CFUKdhS_1.wireOp",EDGE,"1cb9c079-ea9b-4899-8069-e0e3048e911d.sketch_text.stroke-52"),sQuery(id+"FHMxAyK4CFUKdhS_1.wireOp",EDGE,"1cb9c079-ea9b-4899-8069-e0e3048e911d.sketch_text.stroke-53"),sQuery(id+"FHMxAyK4CFUKdhS_1.wireOp",EDGE,"1cb9c079-ea9b-4899-8069-e0e3048e911d.sketch_text.stroke-54"),sQuery(id+"FHMxAyK4CFUKdhS_1.wireOp",EDGE,"1cb9c079-ea9b-4899-8069-e0e3048e911d.sketch_text.stroke-55"),sQuery(id+"FHMxAyK4CFUKdhS_1.wireOp",EDGE,"1cb9c079-ea9b-4899-8069-e0e3048e911d.sketch_text.stroke-56"),sQuery(id+"FHMxAyK4CFUKdhS_1.wireOp",EDGE,"1cb9c079-ea9b-4899-8069-e0e3048e911d.sketch_text.stroke-57"),sQuery(id+"FHMxAyK4CFUKdhS_1.wireOp",EDGE,"1cb9c079-ea9b-4899-8069-e0e3048e911d.sketch_text.stroke-58"),sQuery(id+"FHMxAyK4CFUKdhS_1.wireOp",EDGE,"1cb9c079-ea9b-4899-8069-e0e3048e911d.sketch_text.stroke-59"),sQuery(id+"FHMxAyK4CFUKdhS_1.wireOp",EDGE,"1cb9c079-ea9b-4899-8069-e0e3048e911d.sketch_text.stroke-60"),sQuery(id+"FHMxAyK4CFUKdhS_1.wireOp",EDGE,"1cb9c079-ea9b-4899-8069-e0e3048e911d.sketch_text.stroke-61"),sQuery(id+"FHMxAyK4CFUKdhS_1.wireOp",EDGE,"1cb9c079-ea9b-4899-8069-e0e3048e911d.sketch_text.stroke-62"),sQuery(id+"FHMxAyK4CFUKdhS_1.wireOp",EDGE,"1cb9c079-ea9b-4899-8069-e0e3048e911d.sketch_text.stroke-71"),sQuery(id+"FHMxAyK4CFUKdhS_1.wireOp",EDGE,"1cb9c079-ea9b-4899-8069-e0e3048e911d.sketch_text.stroke-72"),sQuery(id+"FHMxAyK4CFUKdhS_1.wireOp",EDGE,"1cb9c079-ea9b-4899-8069-e0e3048e911d.sketch_text.stroke-73"),sQuery(id+"FHMxAyK4CFUKdhS_1.wireOp",EDGE,"1cb9c079-ea9b-4899-8069-e0e3048e911d.sketch_text.stroke-74"),sQuery(id+"FHMxAyK4CFUKdhS_1.wireOp",EDGE,"1cb9c079-ea9b-4899-8069-e0e3048e911d.sketch_text.stroke-75"),sQuery(id+"FHMxAyK4CFUKdhS_1.wireOp",EDGE,"1cb9c079-ea9b-4899-8069-e0e3048e911d.sketch_text.stroke-76"),sQuery(id+"FHMxAyK4CFUKdhS_1.wireOp",EDGE,"1cb9c079-ea9b-4899-8069-e0e3048e911d.sketch_text.stroke-77"),sQuery(id+"FHMxAyK4CFUKdhS_1.wireOp",EDGE,"1cb9c079-ea9b-4899-8069-e0e3048e911d.sketch_text.stroke-78"),sQuery(id+"FHMxAyK4CFUKdhS_1.wireOp",EDGE,"1cb9c079-ea9b-4899-8069-e0e3048e911d.sketch_text.stroke-79"),sQuery(id+"FHMxAyK4CFUKdhS_1.wireOp",EDGE,"1cb9c079-ea9b-4899-8069-e0e3048e911d.sketch_text.stroke-80"),sQuery(id+"FHMxAyK4CFUKdhS_1.wireOp",EDGE,"1cb9c079-ea9b-4899-8069-e0e3048e911d.sketch_text.stroke-81"),sQuery(id+"FHMxAyK4CFUKdhS_1.wireOp",EDGE,"1cb9c079-ea9b-4899-8069-e0e3048e911d.sketch_text.stroke-82"),sQuery(id+"FHMxAyK4CFUKdhS_1.wireOp",EDGE,"1cb9c079-ea9b-4899-8069-e0e3048e911d.sketch_text.stroke-83"),sQuery(id+"FHMxAyK4CFUKdhS_1.wireOp",EDGE,"1cb9c079-ea9b-4899-8069-e0e3048e911d.sketch_text.stroke-84"),sQuery(id+"FHMxAyK4CFUKdhS_1.wireOp",EDGE,"1cb9c079-ea9b-4899-8069-e0e3048e911d.sketch_text.stroke-85"),sQuery(id+"FHMxAyK4CFUKdhS_1.wireOp",EDGE,"1cb9c079-ea9b-4899-8069-e0e3048e911d.sketch_text.stroke-86"),sQuery(id+"FHMxAyK4CFUKdhS_1.wireOp",EDGE,"1cb9c079-ea9b-4899-8069-e0e3048e911d.sketch_text.stroke-87"),sQuery(id+"FHMxAyK4CFUKdhS_1.wireOp",EDGE,"1cb9c079-ea9b-4899-8069-e0e3048e911d.sketch_text.stroke-88"),sQuery(id+"FHMxAyK4CFUKdhS_1.wireOp",EDGE,"1cb9c079-ea9b-4899-8069-e0e3048e911d.sketch_text.stroke-89"),sQuery(id+"FHMxAyK4CFUKdhS_1.wireOp",EDGE,"1cb9c079-ea9b-4899-8069-e0e3048e911d.sketch_text.stroke-90"),sQuery(id+"FHMxAyK4CFUKdhS_1.wireOp",EDGE,"1cb9c079-ea9b-4899-8069-e0e3048e911d.sketch_text.stroke-91"),sQuery(id+"FHMxAyK4CFUKdhS_1.wireOp",EDGE,"1cb9c079-ea9b-4899-8069-e0e3048e911d.sketch_text.stroke-92"),sQuery(id+"FHMxAyK4CFUKdhS_1.wireOp",EDGE,"1cb9c079-ea9b-4899-8069-e0e3048e911d.sketch_text.stroke-93"),sQuery(id+"FHMxAyK4CFUKdhS_1.wireOp",EDGE,"1cb9c079-ea9b-4899-8069-e0e3048e911d.sketch_text.stroke-94"),sQuery(id+"FHMxAyK4CFUKdhS_1.wireOp",EDGE,"1cb9c079-ea9b-4899-8069-e0e3048e911d.sketch_text.stroke-95"),sQuery(id+"FHMxAyK4CFUKdhS_1.wireOp",EDGE,"1cb9c079-ea9b-4899-8069-e0e3048e911d.sketch_text.stroke-96"),sQuery(id+"FHMxAyK4CFUKdhS_1.wireOp",EDGE,"1cb9c079-ea9b-4899-8069-e0e3048e911d.sketch_text.stroke-97"),sQuery(id+"FHMxAyK4CFUKdhS_1.wireOp",EDGE,"1cb9c079-ea9b-4899-8069-e0e3048e911d.sketch_text.stroke-103"),sQuery(id+"FHMxAyK4CFUKdhS_1.wireOp",EDGE,"1cb9c079-ea9b-4899-8069-e0e3048e911d.sketch_text.stroke-104"),sQuery(id+"FHMxAyK4CFUKdhS_1.wireOp",EDGE,"1cb9c079-ea9b-4899-8069-e0e3048e911d.sketch_text.stroke-105"),sQuery(id+"FHMxAyK4CFUKdhS_1.wireOp",EDGE,"1cb9c079-ea9b-4899-8069-e0e3048e911d.sketch_text.stroke-106"),sQuery(id+"FHMxAyK4CFUKdhS_1.wireOp",EDGE,"1cb9c079-ea9b-4899-8069-e0e3048e911d.sketch_text.stroke-107"),sQuery(id+"FHMxAyK4CFUKdhS_1.wireOp",EDGE,"1cb9c079-ea9b-4899-8069-e0e3048e911d.sketch_text.stroke-108"),sQuery(id+"FHMxAyK4CFUKdhS_1.wireOp",EDGE,"1cb9c079-ea9b-4899-8069-e0e3048e911d.sketch_text.stroke-109"),sQuery(id+"FHMxAyK4CFUKdhS_1.wireOp",EDGE,"1cb9c079-ea9b-4899-8069-e0e3048e911d.sketch_text.stroke-110"),sQuery(id+"FHMxAyK4CFUKdhS_1.wireOp",EDGE,"1cb9c079-ea9b-4899-8069-e0e3048e911d.sketch_text.stroke-111"),sQuery(id+"FHMxAyK4CFUKdhS_1.wireOp",EDGE,"1cb9c079-ea9b-4899-8069-e0e3048e911d.sketch_text.stroke-112"),sQuery(id+"FHMxAyK4CFUKdhS_1.wireOp",EDGE,"1cb9c079-ea9b-4899-8069-e0e3048e911d.sketch_text.stroke-113"),sQuery(id+"FHMxAyK4CFUKdhS_1.wireOp",EDGE,"1cb9c079-ea9b-4899-8069-e0e3048e911d.sketch_text.stroke-114"),sQuery(id+"FHMxAyK4CFUKdhS_1.wireOp",EDGE,"1cb9c079-ea9b-4899-8069-e0e3048e911d.sketch_text.stroke-115"),sQuery(id+"FHMxAyK4CFUKdhS_1.wireOp",EDGE,"1cb9c079-ea9b-4899-8069-e0e3048e911d.sketch_text.stroke-116"),sQuery(id+"FHMxAyK4CFUKdhS_1.wireOp",EDGE,"1cb9c079-ea9b-4899-8069-e0e3048e911d.sketch_text.stroke-117"),sQuery(id+"FHMxAyK4CFUKdhS_1.wireOp",EDGE,"1cb9c079-ea9b-4899-8069-e0e3048e911d.sketch_text.stroke-118"),sQuery(id+"FHMxAyK4CFUKdhS_1.wireOp",EDGE,"1cb9c079-ea9b-4899-8069-e0e3048e911d.sketch_text.stroke-119"),sQuery(id+"FHMxAyK4CFUKdhS_1.wireOp",EDGE,"1cb9c079-ea9b-4899-8069-e0e3048e911d.sketch_text.stroke-120"),sQuery(id+"FHMxAyK4CFUKdhS_1.wireOp",EDGE,"1cb9c079-ea9b-4899-8069-e0e3048e911d.sketch_text.stroke-121"),sQuery(id+"FHMxAyK4CFUKdhS_1.wireOp",EDGE,"1cb9c079-ea9b-4899-8069-e0e3048e911d.sketch_text.stroke-122"),sQuery(id+"FHMxAyK4CFUKdhS_1.wireOp",EDGE,"1cb9c079-ea9b-4899-8069-e0e3048e911d.sketch_text.stroke-123"),sQuery(id+"FHMxAyK4CFUKdhS_1.wireOp",EDGE,"1cb9c079-ea9b-4899-8069-e0e3048e911d.sketch_text.stroke-124"),sQuery(id+"FHMxAyK4CFUKdhS_1.wireOp",EDGE,"1cb9c079-ea9b-4899-8069-e0e3048e911d.sketch_text.stroke-125"),sQuery(id+"FHMxAyK4CFUKdhS_1.wireOp",EDGE,"1cb9c079-ea9b-4899-8069-e0e3048e911d.sketch_text.stroke-126"),sQuery(id+"FHMxAyK4CFUKdhS_1.wireOp",EDGE,"1cb9c079-ea9b-4899-8069-e0e3048e911d.sketch_text.stroke-127"),sQuery(id+"FHMxAyK4CFUKdhS_1.wireOp",EDGE,"1cb9c079-ea9b-4899-8069-e0e3048e911d.sketch_text.stroke-128"),sQuery(id+"FHMxAyK4CFUKdhS_1.wireOp",EDGE,"1cb9c079-ea9b-4899-8069-e0e3048e911d.sketch_text.stroke-129"),sQuery(id+"FHMxAyK4CFUKdhS_1.wireOp",EDGE,"1cb9c079-ea9b-4899-8069-e0e3048e911d.sketch_text.stroke-130"),sQuery(id+"FHMxAyK4CFUKdhS_1.wireOp",EDGE,"1cb9c079-ea9b-4899-8069-e0e3048e911d.sketch_text.stroke-131"),sQuery(id+"FHMxAyK4CFUKdhS_1.wireOp",EDGE,"1cb9c079-ea9b-4899-8069-e0e3048e911d.sketch_text.stroke-132"),sQuery(id+"FHMxAyK4CFUKdhS_1.wireOp",EDGE,"1cb9c079-ea9b-4899-8069-e0e3048e911d.sketch_text.stroke-133"),sQuery(id+"FHMxAyK4CFUKdhS_1.wireOp",EDGE,"1cb9c079-ea9b-4899-8069-e0e3048e911d.sketch_text.stroke-134"),sQuery(id+"FHMxAyK4CFUKdhS_1.wireOp",EDGE,"1cb9c079-ea9b-4899-8069-e0e3048e911d.sketch_text.stroke-135"),sQuery(id+"FHMxAyK4CFUKdhS_1.wireOp",EDGE,"1cb9c079-ea9b-4899-8069-e0e3048e911d.sketch_text.stroke-136"),sQuery(id+"FHMxAyK4CFUKdhS_1.wireOp",EDGE,"1cb9c079-ea9b-4899-8069-e0e3048e911d.sketch_text.stroke-137"),sQuery(id+"FHMxAyK4CFUKdhS_1.wireOp",EDGE,"1cb9c079-ea9b-4899-8069-e0e3048e911d.sketch_text.stroke-138"),sQuery(id+"FHMxAyK4CFUKdhS_1.wireOp",EDGE,"1cb9c079-ea9b-4899-8069-e0e3048e911d.sketch_text.stroke-139"),sQuery(id+"FHMxAyK4CFUKdhS_1.wireOp",EDGE,"1cb9c079-ea9b-4899-8069-e0e3048e911d.sketch_text.stroke-140"),sQuery(id+"FHMxAyK4CFUKdhS_1.wireOp",EDGE,"1cb9c079-ea9b-4899-8069-e0e3048e911d.sketch_text.stroke-141"),sQuery(id+"FHMxAyK4CFUKdhS_1.wireOp",EDGE,"1cb9c079-ea9b-4899-8069-e0e3048e911d.sketch_text.stroke-142"),sQuery(id+"FHMxAyK4CFUKdhS_1.wireOp",EDGE,"1cb9c079-ea9b-4899-8069-e0e3048e911d.sketch_text.stroke-143"),sQuery(id+"FHMxAyK4CFUKdhS_1.wireOp",EDGE,"1cb9c079-ea9b-4899-8069-e0e3048e911d.sketch_text.stroke-144"),sQuery(id+"FHMxAyK4CFUKdhS_1.wireOp",EDGE,"1cb9c079-ea9b-4899-8069-e0e3048e911d.sketch_text.stroke-145"),sQuery(id+"FHMxAyK4CFUKdhS_1.wireOp",EDGE,"1cb9c079-ea9b-4899-8069-e0e3048e911d.sketch_text.stroke-146"),sQuery(id+"FHMxAyK4CFUKdhS_1.wireOp",EDGE,"1cb9c079-ea9b-4899-8069-e0e3048e911d.sketch_text.stroke-147"),sQuery(id+"FHMxAyK4CFUKdhS_1.wireOp",EDGE,"1cb9c079-ea9b-4899-8069-e0e3048e911d.sketch_text.stroke-148"),sQuery(id+"FHMxAyK4CFUKdhS_1.wireOp",EDGE,"1cb9c079-ea9b-4899-8069-e0e3048e911d.sketch_text.stroke-149"),sQuery(id+"FHMxAyK4CFUKdhS_1.wireOp",EDGE,"1cb9c079-ea9b-4899-8069-e0e3048e911d.sketch_text.stroke-150"),sQuery(id+"FHMxAyK4CFUKdhS_1.wireOp",EDGE,"1cb9c079-ea9b-4899-8069-e0e3048e911d.sketch_text.stroke-151"),sQuery(id+"FHMxAyK4CFUKdhS_1.wireOp",EDGE,"1cb9c079-ea9b-4899-8069-e0e3048e911d.sketch_text.stroke-152"),sQuery(id+"FHMxAyK4CFUKdhS_1.wireOp",EDGE,"1cb9c079-ea9b-4899-8069-e0e3048e911d.sketch_text.stroke-153"),sQuery(id+"FHMxAyK4CFUKdhS_1.wireOp",EDGE,"1cb9c079-ea9b-4899-8069-e0e3048e911d.sketch_text.stroke-159"),sQuery(id+"FHMxAyK4CFUKdhS_1.wireOp",EDGE,"1cb9c079-ea9b-4899-8069-e0e3048e911d.sketch_text.stroke-160"),sQuery(id+"FHMxAyK4CFUKdhS_1.wireOp",EDGE,"1cb9c079-ea9b-4899-8069-e0e3048e911d.sketch_text.stroke-161"),sQuery(id+"FHMxAyK4CFUKdhS_1.wireOp",EDGE,"1cb9c079-ea9b-4899-8069-e0e3048e911d.sketch_text.stroke-162"),sQuery(id+"FHMxAyK4CFUKdhS_1.wireOp",EDGE,"1cb9c079-ea9b-4899-8069-e0e3048e911d.sketch_text.stroke-163"),sQuery(id+"FHMxAyK4CFUKdhS_1.wireOp",EDGE,"1cb9c079-ea9b-4899-8069-e0e3048e911d.sketch_text.stroke-164"),sQuery(id+"FHMxAyK4CFUKdhS_1.wireOp",EDGE,"1cb9c079-ea9b-4899-8069-e0e3048e911d.sketch_text.stroke-165"),sQuery(id+"FHMxAyK4CFUKdhS_1.wireOp",EDGE,"1cb9c079-ea9b-4899-8069-e0e3048e911d.sketch_text.stroke-166"),sQuery(id+"FHMxAyK4CFUKdhS_1.wireOp",EDGE,"1cb9c079-ea9b-4899-8069-e0e3048e911d.sketch_text.stroke-167"),sQuery(id+"FHMxAyK4CFUKdhS_1.wireOp",EDGE,"1cb9c079-ea9b-4899-8069-e0e3048e911d.sketch_text.stroke-168"),sQuery(id+"FHMxAyK4CFUKdhS_1.wireOp",EDGE,"1cb9c079-ea9b-4899-8069-e0e3048e911d.sketch_text.stroke-169"),sQuery(id+"FHMxAyK4CFUKdhS_1.wireOp",EDGE,"1cb9c079-ea9b-4899-8069-e0e3048e911d.sketch_text.stroke-170"),sQuery(id+"FHMxAyK4CFUKdhS_1.wireOp",EDGE,"1cb9c079-ea9b-4899-8069-e0e3048e911d.sketch_text.stroke-171"),sQuery(id+"FHMxAyK4CFUKdhS_1.wireOp",EDGE,"1cb9c079-ea9b-4899-8069-e0e3048e911d.sketch_text.stroke-172"),sQuery(id+"FHMxAyK4CFUKdhS_1.wireOp",EDGE,"1cb9c079-ea9b-4899-8069-e0e3048e911d.sketch_text.stroke-173"),sQuery(id+"FHMxAyK4CFUKdhS_1.wireOp",EDGE,"1cb9c079-ea9b-4899-8069-e0e3048e911d.sketch_text.stroke-174"),sQuery(id+"FHMxAyK4CFUKdhS_1.wireOp",EDGE,"1cb9c079-ea9b-4899-8069-e0e3048e911d.sketch_text.stroke-175"),sQuery(id+"FHMxAyK4CFUKdhS_1.wireOp",EDGE,"1cb9c079-ea9b-4899-8069-e0e3048e911d.sketch_text.stroke-176"),sQuery(id+"FHMxAyK4CFUKdhS_1.wireOp",EDGE,"1cb9c079-ea9b-4899-8069-e0e3048e911d.sketch_text.stroke-177"),sQuery(id+"FHMxAyK4CFUKdhS_1.wireOp",EDGE,"1cb9c079-ea9b-4899-8069-e0e3048e911d.sketch_text.stroke-178"),sQuery(id+"FHMxAyK4CFUKdhS_1.wireOp",EDGE,"1cb9c079-ea9b-4899-8069-e0e3048e911d.sketch_text.stroke-179"),sQuery(id+"FHMxAyK4CFUKdhS_1.wireOp",EDGE,"1cb9c079-ea9b-4899-8069-e0e3048e911d.sketch_text.stroke-180"),sQuery(id+"F3.wireOp",EDGE,"8007402e-1a4e-4a06-85a5-2af08e553504"),subQ2])],"isStart":true}),makeQuery(id+"F4.opExtrude","SWEPT_FACE",FACE,{"disambiguationData":[OSD([subQ2])]})])],"derivedFrom":makeQuery(id+"F4.opExtrude","CAP_EDGE",EDGE,{"disambiguationData":[OSD([subQ2])],"isStart":true})});}
            var Q10;
            {var subQ0=sQuery(id+"F3.wireOp",EDGE,"8007402e-1a4e-4a06-85a5-2af08e553504");var subQ1=sQuery(id+"F0.wireOp",EDGE,"E0.top");var subQ2=sQuery(id+"F3.wireOp",EDGE,"6ee83ff3-586e-4dbe-aaea-af71240543bd");var subQ3=sQuery(id+"F0.wireOp",EDGE,"E0.bottom");Q10=makeQuery(id+"F4.boolean.opBoolean","SPLIT",EDGE,{"disambiguationData":[TD([makeQuery(id+"F1.opExtrude","CAP_FACE",FACE,{"disambiguationData":[OSD([subQ3,subQ1,sQuery(id+"F0.wireOp",EDGE,"E0.left"),sQuery(id+"F0.wireOp",EDGE,"E0.right")])],"isStart":false}),makeQuery(id+"F1.opExtrude","SWEPT_FACE",FACE,{"disambiguationData":[OSD([subQ1])]}),makeQuery(id+"F4.opExtrude","SWEPT_FACE",FACE,{"disambiguationData":[OSD([subQ0])]}),makeQuery(id+"F4.opExtrude","CAP_FACE",FACE,{"disambiguationData":[OSD([subQ3,sQuery(id+"F2.wireOp",EDGE,"fcba4419-a2ee-464f-be9d-58f11bf3418b.sketch_text.stroke-0"),sQuery(id+"F2.wireOp",EDGE,"fcba4419-a2ee-464f-be9d-58f11bf3418b.sketch_text.stroke-1"),sQuery(id+"F2.wireOp",EDGE,"fcba4419-a2ee-464f-be9d-58f11bf3418b.sketch_text.stroke-2"),sQuery(id+"F2.wireOp",EDGE,"fcba4419-a2ee-464f-be9d-58f11bf3418b.sketch_text.stroke-3"),sQuery(id+"F2.wireOp",EDGE,"fcba4419-a2ee-464f-be9d-58f11bf3418b.sketch_text.stroke-4"),sQuery(id+"F2.wireOp",EDGE,"fcba4419-a2ee-464f-be9d-58f11bf3418b.sketch_text.stroke-5"),sQuery(id+"F2.wireOp",EDGE,"fcba4419-a2ee-464f-be9d-58f11bf3418b.sketch_text.stroke-6"),sQuery(id+"F2.wireOp",EDGE,"fcba4419-a2ee-464f-be9d-58f11bf3418b.sketch_text.stroke-7"),sQuery(id+"F2.wireOp",EDGE,"fcba4419-a2ee-464f-be9d-58f11bf3418b.sketch_text.stroke-8"),sQuery(id+"F2.wireOp",EDGE,"fcba4419-a2ee-464f-be9d-58f11bf3418b.sketch_text.stroke-9"),sQuery(id+"F2.wireOp",EDGE,"fcba4419-a2ee-464f-be9d-58f11bf3418b.sketch_text.stroke-10"),sQuery(id+"F2.wireOp",EDGE,"fcba4419-a2ee-464f-be9d-58f11bf3418b.sketch_text.stroke-11"),sQuery(id+"F2.wireOp",EDGE,"fcba4419-a2ee-464f-be9d-58f11bf3418b.sketch_text.stroke-12"),sQuery(id+"F2.wireOp",EDGE,"fcba4419-a2ee-464f-be9d-58f11bf3418b.sketch_text.stroke-13"),sQuery(id+"F2.wireOp",EDGE,"fcba4419-a2ee-464f-be9d-58f11bf3418b.sketch_text.stroke-14"),sQuery(id+"F2.wireOp",EDGE,"fcba4419-a2ee-464f-be9d-58f11bf3418b.sketch_text.stroke-15"),sQuery(id+"F2.wireOp",EDGE,"fcba4419-a2ee-464f-be9d-58f11bf3418b.sketch_text.stroke-16"),sQuery(id+"F2.wireOp",EDGE,"fcba4419-a2ee-464f-be9d-58f11bf3418b.sketch_text.stroke-17"),sQuery(id+"F2.wireOp",EDGE,"fcba4419-a2ee-464f-be9d-58f11bf3418b.sketch_text.stroke-18"),sQuery(id+"F2.wireOp",EDGE,"fcba4419-a2ee-464f-be9d-58f11bf3418b.sketch_text.stroke-19"),sQuery(id+"F2.wireOp",EDGE,"fcba4419-a2ee-464f-be9d-58f11bf3418b.sketch_text.stroke-20"),sQuery(id+"F2.wireOp",EDGE,"fcba4419-a2ee-464f-be9d-58f11bf3418b.sketch_text.stroke-21"),sQuery(id+"F2.wireOp",EDGE,"fcba4419-a2ee-464f-be9d-58f11bf3418b.sketch_text.stroke-22"),sQuery(id+"F2.wireOp",EDGE,"fcba4419-a2ee-464f-be9d-58f11bf3418b.sketch_text.stroke-23"),sQuery(id+"F2.wireOp",EDGE,"fcba4419-a2ee-464f-be9d-58f11bf3418b.sketch_text.stroke-24"),sQuery(id+"F2.wireOp",EDGE,"fcba4419-a2ee-464f-be9d-58f11bf3418b.sketch_text.stroke-25"),sQuery(id+"F2.wireOp",EDGE,"fcba4419-a2ee-464f-be9d-58f11bf3418b.sketch_text.stroke-26"),sQuery(id+"F2.wireOp",EDGE,"fcba4419-a2ee-464f-be9d-58f11bf3418b.sketch_text.stroke-27"),sQuery(id+"F2.wireOp",EDGE,"fcba4419-a2ee-464f-be9d-58f11bf3418b.sketch_text.stroke-28"),sQuery(id+"F2.wireOp",EDGE,"fcba4419-a2ee-464f-be9d-58f11bf3418b.sketch_text.stroke-29"),sQuery(id+"F2.wireOp",EDGE,"fcba4419-a2ee-464f-be9d-58f11bf3418b.sketch_text.stroke-30"),sQuery(id+"F2.wireOp",EDGE,"fcba4419-a2ee-464f-be9d-58f11bf3418b.sketch_text.stroke-31"),sQuery(id+"F2.wireOp",EDGE,"fcba4419-a2ee-464f-be9d-58f11bf3418b.sketch_text.stroke-32"),sQuery(id+"F2.wireOp",EDGE,"fcba4419-a2ee-464f-be9d-58f11bf3418b.sketch_text.stroke-33"),sQuery(id+"F2.wireOp",EDGE,"fcba4419-a2ee-464f-be9d-58f11bf3418b.sketch_text.stroke-34"),sQuery(id+"F2.wireOp",EDGE,"fcba4419-a2ee-464f-be9d-58f11bf3418b.sketch_text.stroke-35"),sQuery(id+"F2.wireOp",EDGE,"fcba4419-a2ee-464f-be9d-58f11bf3418b.sketch_text.stroke-36"),sQuery(id+"F2.wireOp",EDGE,"fcba4419-a2ee-464f-be9d-58f11bf3418b.sketch_text.stroke-37"),sQuery(id+"F2.wireOp",EDGE,"fcba4419-a2ee-464f-be9d-58f11bf3418b.sketch_text.stroke-38"),sQuery(id+"F2.wireOp",EDGE,"fcba4419-a2ee-464f-be9d-58f11bf3418b.sketch_text.stroke-39"),sQuery(id+"F2.wireOp",EDGE,"fcba4419-a2ee-464f-be9d-58f11bf3418b.sketch_text.stroke-40"),sQuery(id+"F2.wireOp",EDGE,"fcba4419-a2ee-464f-be9d-58f11bf3418b.sketch_text.stroke-41"),sQuery(id+"F2.wireOp",EDGE,"fcba4419-a2ee-464f-be9d-58f11bf3418b.sketch_text.stroke-42"),sQuery(id+"F2.wireOp",EDGE,"fcba4419-a2ee-464f-be9d-58f11bf3418b.sketch_text.stroke-43"),sQuery(id+"F2.wireOp",EDGE,"fcba4419-a2ee-464f-be9d-58f11bf3418b.sketch_text.stroke-44"),sQuery(id+"F2.wireOp",EDGE,"fcba4419-a2ee-464f-be9d-58f11bf3418b.sketch_text.stroke-45"),sQuery(id+"F2.wireOp",EDGE,"fcba4419-a2ee-464f-be9d-58f11bf3418b.sketch_text.stroke-46"),sQuery(id+"F2.wireOp",EDGE,"fcba4419-a2ee-464f-be9d-58f11bf3418b.sketch_text.stroke-47"),sQuery(id+"F2.wireOp",EDGE,"fcba4419-a2ee-464f-be9d-58f11bf3418b.sketch_text.stroke-48"),sQuery(id+"F2.wireOp",EDGE,"fcba4419-a2ee-464f-be9d-58f11bf3418b.sketch_text.stroke-49"),sQuery(id+"F2.wireOp",EDGE,"fcba4419-a2ee-464f-be9d-58f11bf3418b.sketch_text.stroke-50"),sQuery(id+"F2.wireOp",EDGE,"fcba4419-a2ee-464f-be9d-58f11bf3418b.sketch_text.stroke-51"),sQuery(id+"F2.wireOp",EDGE,"fcba4419-a2ee-464f-be9d-58f11bf3418b.sketch_text.stroke-52"),sQuery(id+"F2.wireOp",EDGE,"fcba4419-a2ee-464f-be9d-58f11bf3418b.sketch_text.stroke-53"),sQuery(id+"F2.wireOp",EDGE,"fcba4419-a2ee-464f-be9d-58f11bf3418b.sketch_text.stroke-54"),sQuery(id+"F2.wireOp",EDGE,"fcba4419-a2ee-464f-be9d-58f11bf3418b.sketch_text.stroke-55"),sQuery(id+"F2.wireOp",EDGE,"fcba4419-a2ee-464f-be9d-58f11bf3418b.sketch_text.stroke-56"),sQuery(id+"F2.wireOp",EDGE,"fcba4419-a2ee-464f-be9d-58f11bf3418b.sketch_text.stroke-57"),sQuery(id+"F2.wireOp",EDGE,"fcba4419-a2ee-464f-be9d-58f11bf3418b.sketch_text.stroke-58"),sQuery(id+"F2.wireOp",EDGE,"fcba4419-a2ee-464f-be9d-58f11bf3418b.sketch_text.stroke-59"),sQuery(id+"F2.wireOp",EDGE,"fcba4419-a2ee-464f-be9d-58f11bf3418b.sketch_text.stroke-60"),sQuery(id+"F2.wireOp",EDGE,"fcba4419-a2ee-464f-be9d-58f11bf3418b.sketch_text.stroke-61"),sQuery(id+"F2.wireOp",EDGE,"fcba4419-a2ee-464f-be9d-58f11bf3418b.sketch_text.stroke-62"),sQuery(id+"F2.wireOp",EDGE,"fcba4419-a2ee-464f-be9d-58f11bf3418b.sketch_text.stroke-63"),sQuery(id+"F2.wireOp",EDGE,"fcba4419-a2ee-464f-be9d-58f11bf3418b.sketch_text.stroke-64"),sQuery(id+"F2.wireOp",EDGE,"fcba4419-a2ee-464f-be9d-58f11bf3418b.sketch_text.stroke-65"),sQuery(id+"F2.wireOp",EDGE,"fcba4419-a2ee-464f-be9d-58f11bf3418b.sketch_text.stroke-66"),sQuery(id+"F2.wireOp",EDGE,"fcba4419-a2ee-464f-be9d-58f11bf3418b.sketch_text.stroke-67"),sQuery(id+"F2.wireOp",EDGE,"fcba4419-a2ee-464f-be9d-58f11bf3418b.sketch_text.stroke-68"),sQuery(id+"F2.wireOp",EDGE,"fcba4419-a2ee-464f-be9d-58f11bf3418b.sketch_text.stroke-69"),sQuery(id+"F2.wireOp",EDGE,"fcba4419-a2ee-464f-be9d-58f11bf3418b.sketch_text.stroke-70"),sQuery(id+"F2.wireOp",EDGE,"fcba4419-a2ee-464f-be9d-58f11bf3418b.sketch_text.stroke-71"),sQuery(id+"F2.wireOp",EDGE,"fcba4419-a2ee-464f-be9d-58f11bf3418b.sketch_text.stroke-72"),sQuery(id+"F2.wireOp",EDGE,"fcba4419-a2ee-464f-be9d-58f11bf3418b.sketch_text.stroke-73"),sQuery(id+"F2.wireOp",EDGE,"fcba4419-a2ee-464f-be9d-58f11bf3418b.sketch_text.stroke-74"),sQuery(id+"F2.wireOp",EDGE,"fcba4419-a2ee-464f-be9d-58f11bf3418b.sketch_text.stroke-75"),sQuery(id+"F2.wireOp",EDGE,"fcba4419-a2ee-464f-be9d-58f11bf3418b.sketch_text.stroke-76"),sQuery(id+"F2.wireOp",EDGE,"fcba4419-a2ee-464f-be9d-58f11bf3418b.sketch_text.stroke-77"),sQuery(id+"F2.wireOp",EDGE,"fcba4419-a2ee-464f-be9d-58f11bf3418b.sketch_text.stroke-78"),sQuery(id+"F2.wireOp",EDGE,"fcba4419-a2ee-464f-be9d-58f11bf3418b.sketch_text.stroke-79"),sQuery(id+"F2.wireOp",EDGE,"fcba4419-a2ee-464f-be9d-58f11bf3418b.sketch_text.stroke-80"),sQuery(id+"F2.wireOp",EDGE,"fcba4419-a2ee-464f-be9d-58f11bf3418b.sketch_text.stroke-81"),sQuery(id+"F2.wireOp",EDGE,"fcba4419-a2ee-464f-be9d-58f11bf3418b.sketch_text.stroke-82"),sQuery(id+"F2.wireOp",EDGE,"fcba4419-a2ee-464f-be9d-58f11bf3418b.sketch_text.stroke-83"),sQuery(id+"F2.wireOp",EDGE,"fcba4419-a2ee-464f-be9d-58f11bf3418b.sketch_text.stroke-84"),sQuery(id+"F2.wireOp",EDGE,"fcba4419-a2ee-464f-be9d-58f11bf3418b.sketch_text.stroke-85"),sQuery(id+"F2.wireOp",EDGE,"fcba4419-a2ee-464f-be9d-58f11bf3418b.sketch_text.stroke-86"),sQuery(id+"F2.wireOp",EDGE,"fcba4419-a2ee-464f-be9d-58f11bf3418b.sketch_text.stroke-87"),sQuery(id+"F2.wireOp",EDGE,"fcba4419-a2ee-464f-be9d-58f11bf3418b.sketch_text.stroke-88"),sQuery(id+"F2.wireOp",EDGE,"fcba4419-a2ee-464f-be9d-58f11bf3418b.sketch_text.stroke-89"),sQuery(id+"F2.wireOp",EDGE,"fcba4419-a2ee-464f-be9d-58f11bf3418b.sketch_text.stroke-90"),sQuery(id+"F2.wireOp",EDGE,"fcba4419-a2ee-464f-be9d-58f11bf3418b.sketch_text.stroke-91"),sQuery(id+"F2.wireOp",EDGE,"fcba4419-a2ee-464f-be9d-58f11bf3418b.sketch_text.stroke-92"),sQuery(id+"F2.wireOp",EDGE,"fcba4419-a2ee-464f-be9d-58f11bf3418b.sketch_text.stroke-93"),sQuery(id+"F2.wireOp",EDGE,"fcba4419-a2ee-464f-be9d-58f11bf3418b.sketch_text.stroke-94"),sQuery(id+"F2.wireOp",EDGE,"fcba4419-a2ee-464f-be9d-58f11bf3418b.sketch_text.stroke-95"),sQuery(id+"F2.wireOp",EDGE,"fcba4419-a2ee-464f-be9d-58f11bf3418b.sketch_text.stroke-96"),sQuery(id+"F2.wireOp",EDGE,"fcba4419-a2ee-464f-be9d-58f11bf3418b.sketch_text.stroke-97"),sQuery(id+"F2.wireOp",EDGE,"fcba4419-a2ee-464f-be9d-58f11bf3418b.sketch_text.stroke-98"),sQuery(id+"F2.wireOp",EDGE,"fcba4419-a2ee-464f-be9d-58f11bf3418b.sketch_text.stroke-99"),sQuery(id+"F2.wireOp",EDGE,"fcba4419-a2ee-464f-be9d-58f11bf3418b.sketch_text.stroke-100"),sQuery(id+"F2.wireOp",EDGE,"fcba4419-a2ee-464f-be9d-58f11bf3418b.sketch_text.stroke-101"),sQuery(id+"F2.wireOp",EDGE,"fcba4419-a2ee-464f-be9d-58f11bf3418b.sketch_text.stroke-102"),sQuery(id+"F2.wireOp",EDGE,"fcba4419-a2ee-464f-be9d-58f11bf3418b.sketch_text.stroke-103"),sQuery(id+"F2.wireOp",EDGE,"fcba4419-a2ee-464f-be9d-58f11bf3418b.sketch_text.stroke-104"),sQuery(id+"F2.wireOp",EDGE,"fcba4419-a2ee-464f-be9d-58f11bf3418b.sketch_text.stroke-105"),sQuery(id+"F2.wireOp",EDGE,"fcba4419-a2ee-464f-be9d-58f11bf3418b.sketch_text.stroke-106"),sQuery(id+"F2.wireOp",EDGE,"fcba4419-a2ee-464f-be9d-58f11bf3418b.sketch_text.stroke-107"),sQuery(id+"F2.wireOp",EDGE,"fcba4419-a2ee-464f-be9d-58f11bf3418b.sketch_text.stroke-108"),sQuery(id+"F2.wireOp",EDGE,"fcba4419-a2ee-464f-be9d-58f11bf3418b.sketch_text.stroke-109"),sQuery(id+"F2.wireOp",EDGE,"fcba4419-a2ee-464f-be9d-58f11bf3418b.sketch_text.stroke-110"),sQuery(id+"F2.wireOp",EDGE,"fcba4419-a2ee-464f-be9d-58f11bf3418b.sketch_text.stroke-111"),sQuery(id+"F2.wireOp",EDGE,"fcba4419-a2ee-464f-be9d-58f11bf3418b.sketch_text.stroke-112"),sQuery(id+"F2.wireOp",EDGE,"fcba4419-a2ee-464f-be9d-58f11bf3418b.sketch_text.stroke-113"),sQuery(id+"F2.wireOp",EDGE,"fcba4419-a2ee-464f-be9d-58f11bf3418b.sketch_text.stroke-114"),sQuery(id+"F2.wireOp",EDGE,"fcba4419-a2ee-464f-be9d-58f11bf3418b.sketch_text.stroke-115"),sQuery(id+"F2.wireOp",EDGE,"fcba4419-a2ee-464f-be9d-58f11bf3418b.sketch_text.stroke-116"),sQuery(id+"F2.wireOp",EDGE,"fcba4419-a2ee-464f-be9d-58f11bf3418b.sketch_text.stroke-117"),sQuery(id+"F2.wireOp",EDGE,"fcba4419-a2ee-464f-be9d-58f11bf3418b.sketch_text.stroke-118"),sQuery(id+"F2.wireOp",EDGE,"fcba4419-a2ee-464f-be9d-58f11bf3418b.sketch_text.stroke-119"),sQuery(id+"F2.wireOp",EDGE,"fcba4419-a2ee-464f-be9d-58f11bf3418b.sketch_text.stroke-120"),sQuery(id+"F2.wireOp",EDGE,"fcba4419-a2ee-464f-be9d-58f11bf3418b.sketch_text.stroke-121"),sQuery(id+"F2.wireOp",EDGE,"fcba4419-a2ee-464f-be9d-58f11bf3418b.sketch_text.stroke-122"),sQuery(id+"F2.wireOp",EDGE,"fcba4419-a2ee-464f-be9d-58f11bf3418b.sketch_text.stroke-123"),sQuery(id+"F2.wireOp",EDGE,"fcba4419-a2ee-464f-be9d-58f11bf3418b.sketch_text.stroke-124"),sQuery(id+"F2.wireOp",EDGE,"fcba4419-a2ee-464f-be9d-58f11bf3418b.sketch_text.stroke-125"),sQuery(id+"F2.wireOp",EDGE,"fcba4419-a2ee-464f-be9d-58f11bf3418b.sketch_text.stroke-126"),sQuery(id+"F2.wireOp",EDGE,"fcba4419-a2ee-464f-be9d-58f11bf3418b.sketch_text.stroke-127"),sQuery(id+"F2.wireOp",EDGE,"fcba4419-a2ee-464f-be9d-58f11bf3418b.sketch_text.stroke-128"),sQuery(id+"F2.wireOp",EDGE,"fcba4419-a2ee-464f-be9d-58f11bf3418b.sketch_text.stroke-129"),sQuery(id+"F2.wireOp",EDGE,"fcba4419-a2ee-464f-be9d-58f11bf3418b.sketch_text.stroke-130"),sQuery(id+"F2.wireOp",EDGE,"fcba4419-a2ee-464f-be9d-58f11bf3418b.sketch_text.stroke-131"),sQuery(id+"F2.wireOp",EDGE,"fcba4419-a2ee-464f-be9d-58f11bf3418b.sketch_text.stroke-132"),sQuery(id+"F2.wireOp",EDGE,"fcba4419-a2ee-464f-be9d-58f11bf3418b.sketch_text.stroke-133"),sQuery(id+"F2.wireOp",EDGE,"fcba4419-a2ee-464f-be9d-58f11bf3418b.sketch_text.stroke-134"),sQuery(id+"F2.wireOp",EDGE,"fcba4419-a2ee-464f-be9d-58f11bf3418b.sketch_text.stroke-135"),sQuery(id+"F2.wireOp",EDGE,"fcba4419-a2ee-464f-be9d-58f11bf3418b.sketch_text.stroke-136"),sQuery(id+"F2.wireOp",EDGE,"fcba4419-a2ee-464f-be9d-58f11bf3418b.sketch_text.stroke-137"),sQuery(id+"F2.wireOp",EDGE,"fcba4419-a2ee-464f-be9d-58f11bf3418b.sketch_text.stroke-138"),sQuery(id+"F2.wireOp",EDGE,"fcba4419-a2ee-464f-be9d-58f11bf3418b.sketch_text.stroke-139"),sQuery(id+"F2.wireOp",EDGE,"fcba4419-a2ee-464f-be9d-58f11bf3418b.sketch_text.stroke-140"),sQuery(id+"F2.wireOp",EDGE,"fcba4419-a2ee-464f-be9d-58f11bf3418b.sketch_text.stroke-141"),sQuery(id+"F2.wireOp",EDGE,"fcba4419-a2ee-464f-be9d-58f11bf3418b.sketch_text.stroke-142"),sQuery(id+"F2.wireOp",EDGE,"fcba4419-a2ee-464f-be9d-58f11bf3418b.sketch_text.stroke-143"),sQuery(id+"F2.wireOp",EDGE,"fcba4419-a2ee-464f-be9d-58f11bf3418b.sketch_text.stroke-144"),sQuery(id+"F2.wireOp",EDGE,"fcba4419-a2ee-464f-be9d-58f11bf3418b.sketch_text.stroke-145"),sQuery(id+"F2.wireOp",EDGE,"fcba4419-a2ee-464f-be9d-58f11bf3418b.sketch_text.stroke-146"),sQuery(id+"F2.wireOp",EDGE,"fcba4419-a2ee-464f-be9d-58f11bf3418b.sketch_text.stroke-147"),sQuery(id+"F2.wireOp",EDGE,"fcba4419-a2ee-464f-be9d-58f11bf3418b.sketch_text.stroke-148"),sQuery(id+"F2.wireOp",EDGE,"fcba4419-a2ee-464f-be9d-58f11bf3418b.sketch_text.stroke-149"),sQuery(id+"F2.wireOp",EDGE,"fcba4419-a2ee-464f-be9d-58f11bf3418b.sketch_text.stroke-150"),sQuery(id+"F2.wireOp",EDGE,"fcba4419-a2ee-464f-be9d-58f11bf3418b.sketch_text.stroke-151"),sQuery(id+"F2.wireOp",EDGE,"fcba4419-a2ee-464f-be9d-58f11bf3418b.sketch_text.stroke-152"),sQuery(id+"F2.wireOp",EDGE,"fcba4419-a2ee-464f-be9d-58f11bf3418b.sketch_text.stroke-153"),sQuery(id+"F2.wireOp",EDGE,"fcba4419-a2ee-464f-be9d-58f11bf3418b.sketch_text.stroke-154"),sQuery(id+"F2.wireOp",EDGE,"fcba4419-a2ee-464f-be9d-58f11bf3418b.sketch_text.stroke-155"),sQuery(id+"F2.wireOp",EDGE,"fcba4419-a2ee-464f-be9d-58f11bf3418b.sketch_text.stroke-156"),sQuery(id+"F2.wireOp",EDGE,"fcba4419-a2ee-464f-be9d-58f11bf3418b.sketch_text.stroke-157"),sQuery(id+"F2.wireOp",EDGE,"fcba4419-a2ee-464f-be9d-58f11bf3418b.sketch_text.stroke-158"),sQuery(id+"F2.wireOp",EDGE,"fcba4419-a2ee-464f-be9d-58f11bf3418b.sketch_text.stroke-159"),sQuery(id+"F2.wireOp",EDGE,"fcba4419-a2ee-464f-be9d-58f11bf3418b.sketch_text.stroke-160"),sQuery(id+"F2.wireOp",EDGE,"fcba4419-a2ee-464f-be9d-58f11bf3418b.sketch_text.stroke-161"),sQuery(id+"F2.wireOp",EDGE,"fcba4419-a2ee-464f-be9d-58f11bf3418b.sketch_text.stroke-162"),sQuery(id+"F2.wireOp",EDGE,"fcba4419-a2ee-464f-be9d-58f11bf3418b.sketch_text.stroke-163"),sQuery(id+"F2.wireOp",EDGE,"fcba4419-a2ee-464f-be9d-58f11bf3418b.sketch_text.stroke-164"),sQuery(id+"F2.wireOp",EDGE,"fcba4419-a2ee-464f-be9d-58f11bf3418b.sketch_text.stroke-165"),sQuery(id+"F2.wireOp",EDGE,"fcba4419-a2ee-464f-be9d-58f11bf3418b.sketch_text.stroke-166"),sQuery(id+"F2.wireOp",EDGE,"fcba4419-a2ee-464f-be9d-58f11bf3418b.sketch_text.stroke-167"),sQuery(id+"F2.wireOp",EDGE,"fcba4419-a2ee-464f-be9d-58f11bf3418b.sketch_text.stroke-168"),sQuery(id+"F2.wireOp",EDGE,"fcba4419-a2ee-464f-be9d-58f11bf3418b.sketch_text.stroke-169"),sQuery(id+"F2.wireOp",EDGE,"fcba4419-a2ee-464f-be9d-58f11bf3418b.sketch_text.stroke-170"),sQuery(id+"F2.wireOp",EDGE,"fcba4419-a2ee-464f-be9d-58f11bf3418b.sketch_text.stroke-171"),sQuery(id+"F2.wireOp",EDGE,"fcba4419-a2ee-464f-be9d-58f11bf3418b.sketch_text.stroke-172"),sQuery(id+"F2.wireOp",EDGE,"fcba4419-a2ee-464f-be9d-58f11bf3418b.sketch_text.stroke-173"),sQuery(id+"FHMxAyK4CFUKdhS_1.wireOp",EDGE,"1cb9c079-ea9b-4899-8069-e0e3048e911d.sketch_text.stroke-0"),sQuery(id+"FHMxAyK4CFUKdhS_1.wireOp",EDGE,"1cb9c079-ea9b-4899-8069-e0e3048e911d.sketch_text.stroke-1"),sQuery(id+"FHMxAyK4CFUKdhS_1.wireOp",EDGE,"1cb9c079-ea9b-4899-8069-e0e3048e911d.sketch_text.stroke-2"),sQuery(id+"FHMxAyK4CFUKdhS_1.wireOp",EDGE,"1cb9c079-ea9b-4899-8069-e0e3048e911d.sketch_text.stroke-3"),sQuery(id+"FHMxAyK4CFUKdhS_1.wireOp",EDGE,"1cb9c079-ea9b-4899-8069-e0e3048e911d.sketch_text.stroke-4"),sQuery(id+"FHMxAyK4CFUKdhS_1.wireOp",EDGE,"1cb9c079-ea9b-4899-8069-e0e3048e911d.sketch_text.stroke-5"),sQuery(id+"FHMxAyK4CFUKdhS_1.wireOp",EDGE,"1cb9c079-ea9b-4899-8069-e0e3048e911d.sketch_text.stroke-6"),sQuery(id+"FHMxAyK4CFUKdhS_1.wireOp",EDGE,"1cb9c079-ea9b-4899-8069-e0e3048e911d.sketch_text.stroke-7"),sQuery(id+"FHMxAyK4CFUKdhS_1.wireOp",EDGE,"1cb9c079-ea9b-4899-8069-e0e3048e911d.sketch_text.stroke-8"),sQuery(id+"FHMxAyK4CFUKdhS_1.wireOp",EDGE,"1cb9c079-ea9b-4899-8069-e0e3048e911d.sketch_text.stroke-9"),sQuery(id+"FHMxAyK4CFUKdhS_1.wireOp",EDGE,"1cb9c079-ea9b-4899-8069-e0e3048e911d.sketch_text.stroke-10"),sQuery(id+"FHMxAyK4CFUKdhS_1.wireOp",EDGE,"1cb9c079-ea9b-4899-8069-e0e3048e911d.sketch_text.stroke-11"),sQuery(id+"FHMxAyK4CFUKdhS_1.wireOp",EDGE,"1cb9c079-ea9b-4899-8069-e0e3048e911d.sketch_text.stroke-12"),sQuery(id+"FHMxAyK4CFUKdhS_1.wireOp",EDGE,"1cb9c079-ea9b-4899-8069-e0e3048e911d.sketch_text.stroke-13"),sQuery(id+"FHMxAyK4CFUKdhS_1.wireOp",EDGE,"1cb9c079-ea9b-4899-8069-e0e3048e911d.sketch_text.stroke-14"),sQuery(id+"FHMxAyK4CFUKdhS_1.wireOp",EDGE,"1cb9c079-ea9b-4899-8069-e0e3048e911d.sketch_text.stroke-15"),sQuery(id+"FHMxAyK4CFUKdhS_1.wireOp",EDGE,"1cb9c079-ea9b-4899-8069-e0e3048e911d.sketch_text.stroke-16"),sQuery(id+"FHMxAyK4CFUKdhS_1.wireOp",EDGE,"1cb9c079-ea9b-4899-8069-e0e3048e911d.sketch_text.stroke-17"),sQuery(id+"FHMxAyK4CFUKdhS_1.wireOp",EDGE,"1cb9c079-ea9b-4899-8069-e0e3048e911d.sketch_text.stroke-18"),sQuery(id+"FHMxAyK4CFUKdhS_1.wireOp",EDGE,"1cb9c079-ea9b-4899-8069-e0e3048e911d.sketch_text.stroke-19"),sQuery(id+"FHMxAyK4CFUKdhS_1.wireOp",EDGE,"1cb9c079-ea9b-4899-8069-e0e3048e911d.sketch_text.stroke-20"),sQuery(id+"FHMxAyK4CFUKdhS_1.wireOp",EDGE,"1cb9c079-ea9b-4899-8069-e0e3048e911d.sketch_text.stroke-21"),sQuery(id+"FHMxAyK4CFUKdhS_1.wireOp",EDGE,"1cb9c079-ea9b-4899-8069-e0e3048e911d.sketch_text.stroke-22"),sQuery(id+"FHMxAyK4CFUKdhS_1.wireOp",EDGE,"1cb9c079-ea9b-4899-8069-e0e3048e911d.sketch_text.stroke-23"),sQuery(id+"FHMxAyK4CFUKdhS_1.wireOp",EDGE,"1cb9c079-ea9b-4899-8069-e0e3048e911d.sketch_text.stroke-24"),sQuery(id+"FHMxAyK4CFUKdhS_1.wireOp",EDGE,"1cb9c079-ea9b-4899-8069-e0e3048e911d.sketch_text.stroke-25"),sQuery(id+"FHMxAyK4CFUKdhS_1.wireOp",EDGE,"1cb9c079-ea9b-4899-8069-e0e3048e911d.sketch_text.stroke-26"),sQuery(id+"FHMxAyK4CFUKdhS_1.wireOp",EDGE,"1cb9c079-ea9b-4899-8069-e0e3048e911d.sketch_text.stroke-27"),sQuery(id+"FHMxAyK4CFUKdhS_1.wireOp",EDGE,"1cb9c079-ea9b-4899-8069-e0e3048e911d.sketch_text.stroke-28"),sQuery(id+"FHMxAyK4CFUKdhS_1.wireOp",EDGE,"1cb9c079-ea9b-4899-8069-e0e3048e911d.sketch_text.stroke-29"),sQuery(id+"FHMxAyK4CFUKdhS_1.wireOp",EDGE,"1cb9c079-ea9b-4899-8069-e0e3048e911d.sketch_text.stroke-30"),sQuery(id+"FHMxAyK4CFUKdhS_1.wireOp",EDGE,"1cb9c079-ea9b-4899-8069-e0e3048e911d.sketch_text.stroke-31"),sQuery(id+"FHMxAyK4CFUKdhS_1.wireOp",EDGE,"1cb9c079-ea9b-4899-8069-e0e3048e911d.sketch_text.stroke-32"),sQuery(id+"FHMxAyK4CFUKdhS_1.wireOp",EDGE,"1cb9c079-ea9b-4899-8069-e0e3048e911d.sketch_text.stroke-33"),sQuery(id+"FHMxAyK4CFUKdhS_1.wireOp",EDGE,"1cb9c079-ea9b-4899-8069-e0e3048e911d.sketch_text.stroke-34"),sQuery(id+"FHMxAyK4CFUKdhS_1.wireOp",EDGE,"1cb9c079-ea9b-4899-8069-e0e3048e911d.sketch_text.stroke-35"),sQuery(id+"FHMxAyK4CFUKdhS_1.wireOp",EDGE,"1cb9c079-ea9b-4899-8069-e0e3048e911d.sketch_text.stroke-36"),sQuery(id+"FHMxAyK4CFUKdhS_1.wireOp",EDGE,"1cb9c079-ea9b-4899-8069-e0e3048e911d.sketch_text.stroke-37"),sQuery(id+"FHMxAyK4CFUKdhS_1.wireOp",EDGE,"1cb9c079-ea9b-4899-8069-e0e3048e911d.sketch_text.stroke-38"),sQuery(id+"FHMxAyK4CFUKdhS_1.wireOp",EDGE,"1cb9c079-ea9b-4899-8069-e0e3048e911d.sketch_text.stroke-39"),sQuery(id+"FHMxAyK4CFUKdhS_1.wireOp",EDGE,"1cb9c079-ea9b-4899-8069-e0e3048e911d.sketch_text.stroke-40"),sQuery(id+"FHMxAyK4CFUKdhS_1.wireOp",EDGE,"1cb9c079-ea9b-4899-8069-e0e3048e911d.sketch_text.stroke-41"),sQuery(id+"FHMxAyK4CFUKdhS_1.wireOp",EDGE,"1cb9c079-ea9b-4899-8069-e0e3048e911d.sketch_text.stroke-42"),sQuery(id+"FHMxAyK4CFUKdhS_1.wireOp",EDGE,"1cb9c079-ea9b-4899-8069-e0e3048e911d.sketch_text.stroke-43"),sQuery(id+"FHMxAyK4CFUKdhS_1.wireOp",EDGE,"1cb9c079-ea9b-4899-8069-e0e3048e911d.sketch_text.stroke-44"),sQuery(id+"FHMxAyK4CFUKdhS_1.wireOp",EDGE,"1cb9c079-ea9b-4899-8069-e0e3048e911d.sketch_text.stroke-45"),sQuery(id+"FHMxAyK4CFUKdhS_1.wireOp",EDGE,"1cb9c079-ea9b-4899-8069-e0e3048e911d.sketch_text.stroke-46"),sQuery(id+"FHMxAyK4CFUKdhS_1.wireOp",EDGE,"1cb9c079-ea9b-4899-8069-e0e3048e911d.sketch_text.stroke-47"),sQuery(id+"FHMxAyK4CFUKdhS_1.wireOp",EDGE,"1cb9c079-ea9b-4899-8069-e0e3048e911d.sketch_text.stroke-48"),sQuery(id+"FHMxAyK4CFUKdhS_1.wireOp",EDGE,"1cb9c079-ea9b-4899-8069-e0e3048e911d.sketch_text.stroke-49"),sQuery(id+"FHMxAyK4CFUKdhS_1.wireOp",EDGE,"1cb9c079-ea9b-4899-8069-e0e3048e911d.sketch_text.stroke-50"),sQuery(id+"FHMxAyK4CFUKdhS_1.wireOp",EDGE,"1cb9c079-ea9b-4899-8069-e0e3048e911d.sketch_text.stroke-51"),sQuery(id+"FHMxAyK4CFUKdhS_1.wireOp",EDGE,"1cb9c079-ea9b-4899-8069-e0e3048e911d.sketch_text.stroke-52"),sQuery(id+"FHMxAyK4CFUKdhS_1.wireOp",EDGE,"1cb9c079-ea9b-4899-8069-e0e3048e911d.sketch_text.stroke-53"),sQuery(id+"FHMxAyK4CFUKdhS_1.wireOp",EDGE,"1cb9c079-ea9b-4899-8069-e0e3048e911d.sketch_text.stroke-54"),sQuery(id+"FHMxAyK4CFUKdhS_1.wireOp",EDGE,"1cb9c079-ea9b-4899-8069-e0e3048e911d.sketch_text.stroke-55"),sQuery(id+"FHMxAyK4CFUKdhS_1.wireOp",EDGE,"1cb9c079-ea9b-4899-8069-e0e3048e911d.sketch_text.stroke-56"),sQuery(id+"FHMxAyK4CFUKdhS_1.wireOp",EDGE,"1cb9c079-ea9b-4899-8069-e0e3048e911d.sketch_text.stroke-57"),sQuery(id+"FHMxAyK4CFUKdhS_1.wireOp",EDGE,"1cb9c079-ea9b-4899-8069-e0e3048e911d.sketch_text.stroke-58"),sQuery(id+"FHMxAyK4CFUKdhS_1.wireOp",EDGE,"1cb9c079-ea9b-4899-8069-e0e3048e911d.sketch_text.stroke-59"),sQuery(id+"FHMxAyK4CFUKdhS_1.wireOp",EDGE,"1cb9c079-ea9b-4899-8069-e0e3048e911d.sketch_text.stroke-60"),sQuery(id+"FHMxAyK4CFUKdhS_1.wireOp",EDGE,"1cb9c079-ea9b-4899-8069-e0e3048e911d.sketch_text.stroke-61"),sQuery(id+"FHMxAyK4CFUKdhS_1.wireOp",EDGE,"1cb9c079-ea9b-4899-8069-e0e3048e911d.sketch_text.stroke-62"),sQuery(id+"FHMxAyK4CFUKdhS_1.wireOp",EDGE,"1cb9c079-ea9b-4899-8069-e0e3048e911d.sketch_text.stroke-71"),sQuery(id+"FHMxAyK4CFUKdhS_1.wireOp",EDGE,"1cb9c079-ea9b-4899-8069-e0e3048e911d.sketch_text.stroke-72"),sQuery(id+"FHMxAyK4CFUKdhS_1.wireOp",EDGE,"1cb9c079-ea9b-4899-8069-e0e3048e911d.sketch_text.stroke-73"),sQuery(id+"FHMxAyK4CFUKdhS_1.wireOp",EDGE,"1cb9c079-ea9b-4899-8069-e0e3048e911d.sketch_text.stroke-74"),sQuery(id+"FHMxAyK4CFUKdhS_1.wireOp",EDGE,"1cb9c079-ea9b-4899-8069-e0e3048e911d.sketch_text.stroke-75"),sQuery(id+"FHMxAyK4CFUKdhS_1.wireOp",EDGE,"1cb9c079-ea9b-4899-8069-e0e3048e911d.sketch_text.stroke-76"),sQuery(id+"FHMxAyK4CFUKdhS_1.wireOp",EDGE,"1cb9c079-ea9b-4899-8069-e0e3048e911d.sketch_text.stroke-77"),sQuery(id+"FHMxAyK4CFUKdhS_1.wireOp",EDGE,"1cb9c079-ea9b-4899-8069-e0e3048e911d.sketch_text.stroke-78"),sQuery(id+"FHMxAyK4CFUKdhS_1.wireOp",EDGE,"1cb9c079-ea9b-4899-8069-e0e3048e911d.sketch_text.stroke-79"),sQuery(id+"FHMxAyK4CFUKdhS_1.wireOp",EDGE,"1cb9c079-ea9b-4899-8069-e0e3048e911d.sketch_text.stroke-80"),sQuery(id+"FHMxAyK4CFUKdhS_1.wireOp",EDGE,"1cb9c079-ea9b-4899-8069-e0e3048e911d.sketch_text.stroke-81"),sQuery(id+"FHMxAyK4CFUKdhS_1.wireOp",EDGE,"1cb9c079-ea9b-4899-8069-e0e3048e911d.sketch_text.stroke-82"),sQuery(id+"FHMxAyK4CFUKdhS_1.wireOp",EDGE,"1cb9c079-ea9b-4899-8069-e0e3048e911d.sketch_text.stroke-83"),sQuery(id+"FHMxAyK4CFUKdhS_1.wireOp",EDGE,"1cb9c079-ea9b-4899-8069-e0e3048e911d.sketch_text.stroke-84"),sQuery(id+"FHMxAyK4CFUKdhS_1.wireOp",EDGE,"1cb9c079-ea9b-4899-8069-e0e3048e911d.sketch_text.stroke-85"),sQuery(id+"FHMxAyK4CFUKdhS_1.wireOp",EDGE,"1cb9c079-ea9b-4899-8069-e0e3048e911d.sketch_text.stroke-86"),sQuery(id+"FHMxAyK4CFUKdhS_1.wireOp",EDGE,"1cb9c079-ea9b-4899-8069-e0e3048e911d.sketch_text.stroke-87"),sQuery(id+"FHMxAyK4CFUKdhS_1.wireOp",EDGE,"1cb9c079-ea9b-4899-8069-e0e3048e911d.sketch_text.stroke-88"),sQuery(id+"FHMxAyK4CFUKdhS_1.wireOp",EDGE,"1cb9c079-ea9b-4899-8069-e0e3048e911d.sketch_text.stroke-89"),sQuery(id+"FHMxAyK4CFUKdhS_1.wireOp",EDGE,"1cb9c079-ea9b-4899-8069-e0e3048e911d.sketch_text.stroke-90"),sQuery(id+"FHMxAyK4CFUKdhS_1.wireOp",EDGE,"1cb9c079-ea9b-4899-8069-e0e3048e911d.sketch_text.stroke-91"),sQuery(id+"FHMxAyK4CFUKdhS_1.wireOp",EDGE,"1cb9c079-ea9b-4899-8069-e0e3048e911d.sketch_text.stroke-92"),sQuery(id+"FHMxAyK4CFUKdhS_1.wireOp",EDGE,"1cb9c079-ea9b-4899-8069-e0e3048e911d.sketch_text.stroke-93"),sQuery(id+"FHMxAyK4CFUKdhS_1.wireOp",EDGE,"1cb9c079-ea9b-4899-8069-e0e3048e911d.sketch_text.stroke-94"),sQuery(id+"FHMxAyK4CFUKdhS_1.wireOp",EDGE,"1cb9c079-ea9b-4899-8069-e0e3048e911d.sketch_text.stroke-95"),sQuery(id+"FHMxAyK4CFUKdhS_1.wireOp",EDGE,"1cb9c079-ea9b-4899-8069-e0e3048e911d.sketch_text.stroke-96"),sQuery(id+"FHMxAyK4CFUKdhS_1.wireOp",EDGE,"1cb9c079-ea9b-4899-8069-e0e3048e911d.sketch_text.stroke-97"),sQuery(id+"FHMxAyK4CFUKdhS_1.wireOp",EDGE,"1cb9c079-ea9b-4899-8069-e0e3048e911d.sketch_text.stroke-103"),sQuery(id+"FHMxAyK4CFUKdhS_1.wireOp",EDGE,"1cb9c079-ea9b-4899-8069-e0e3048e911d.sketch_text.stroke-104"),sQuery(id+"FHMxAyK4CFUKdhS_1.wireOp",EDGE,"1cb9c079-ea9b-4899-8069-e0e3048e911d.sketch_text.stroke-105"),sQuery(id+"FHMxAyK4CFUKdhS_1.wireOp",EDGE,"1cb9c079-ea9b-4899-8069-e0e3048e911d.sketch_text.stroke-106"),sQuery(id+"FHMxAyK4CFUKdhS_1.wireOp",EDGE,"1cb9c079-ea9b-4899-8069-e0e3048e911d.sketch_text.stroke-107"),sQuery(id+"FHMxAyK4CFUKdhS_1.wireOp",EDGE,"1cb9c079-ea9b-4899-8069-e0e3048e911d.sketch_text.stroke-108"),sQuery(id+"FHMxAyK4CFUKdhS_1.wireOp",EDGE,"1cb9c079-ea9b-4899-8069-e0e3048e911d.sketch_text.stroke-109"),sQuery(id+"FHMxAyK4CFUKdhS_1.wireOp",EDGE,"1cb9c079-ea9b-4899-8069-e0e3048e911d.sketch_text.stroke-110"),sQuery(id+"FHMxAyK4CFUKdhS_1.wireOp",EDGE,"1cb9c079-ea9b-4899-8069-e0e3048e911d.sketch_text.stroke-111"),sQuery(id+"FHMxAyK4CFUKdhS_1.wireOp",EDGE,"1cb9c079-ea9b-4899-8069-e0e3048e911d.sketch_text.stroke-112"),sQuery(id+"FHMxAyK4CFUKdhS_1.wireOp",EDGE,"1cb9c079-ea9b-4899-8069-e0e3048e911d.sketch_text.stroke-113"),sQuery(id+"FHMxAyK4CFUKdhS_1.wireOp",EDGE,"1cb9c079-ea9b-4899-8069-e0e3048e911d.sketch_text.stroke-114"),sQuery(id+"FHMxAyK4CFUKdhS_1.wireOp",EDGE,"1cb9c079-ea9b-4899-8069-e0e3048e911d.sketch_text.stroke-115"),sQuery(id+"FHMxAyK4CFUKdhS_1.wireOp",EDGE,"1cb9c079-ea9b-4899-8069-e0e3048e911d.sketch_text.stroke-116"),sQuery(id+"FHMxAyK4CFUKdhS_1.wireOp",EDGE,"1cb9c079-ea9b-4899-8069-e0e3048e911d.sketch_text.stroke-117"),sQuery(id+"FHMxAyK4CFUKdhS_1.wireOp",EDGE,"1cb9c079-ea9b-4899-8069-e0e3048e911d.sketch_text.stroke-118"),sQuery(id+"FHMxAyK4CFUKdhS_1.wireOp",EDGE,"1cb9c079-ea9b-4899-8069-e0e3048e911d.sketch_text.stroke-119"),sQuery(id+"FHMxAyK4CFUKdhS_1.wireOp",EDGE,"1cb9c079-ea9b-4899-8069-e0e3048e911d.sketch_text.stroke-120"),sQuery(id+"FHMxAyK4CFUKdhS_1.wireOp",EDGE,"1cb9c079-ea9b-4899-8069-e0e3048e911d.sketch_text.stroke-121"),sQuery(id+"FHMxAyK4CFUKdhS_1.wireOp",EDGE,"1cb9c079-ea9b-4899-8069-e0e3048e911d.sketch_text.stroke-122"),sQuery(id+"FHMxAyK4CFUKdhS_1.wireOp",EDGE,"1cb9c079-ea9b-4899-8069-e0e3048e911d.sketch_text.stroke-123"),sQuery(id+"FHMxAyK4CFUKdhS_1.wireOp",EDGE,"1cb9c079-ea9b-4899-8069-e0e3048e911d.sketch_text.stroke-124"),sQuery(id+"FHMxAyK4CFUKdhS_1.wireOp",EDGE,"1cb9c079-ea9b-4899-8069-e0e3048e911d.sketch_text.stroke-125"),sQuery(id+"FHMxAyK4CFUKdhS_1.wireOp",EDGE,"1cb9c079-ea9b-4899-8069-e0e3048e911d.sketch_text.stroke-126"),sQuery(id+"FHMxAyK4CFUKdhS_1.wireOp",EDGE,"1cb9c079-ea9b-4899-8069-e0e3048e911d.sketch_text.stroke-127"),sQuery(id+"FHMxAyK4CFUKdhS_1.wireOp",EDGE,"1cb9c079-ea9b-4899-8069-e0e3048e911d.sketch_text.stroke-128"),sQuery(id+"FHMxAyK4CFUKdhS_1.wireOp",EDGE,"1cb9c079-ea9b-4899-8069-e0e3048e911d.sketch_text.stroke-129"),sQuery(id+"FHMxAyK4CFUKdhS_1.wireOp",EDGE,"1cb9c079-ea9b-4899-8069-e0e3048e911d.sketch_text.stroke-130"),sQuery(id+"FHMxAyK4CFUKdhS_1.wireOp",EDGE,"1cb9c079-ea9b-4899-8069-e0e3048e911d.sketch_text.stroke-131"),sQuery(id+"FHMxAyK4CFUKdhS_1.wireOp",EDGE,"1cb9c079-ea9b-4899-8069-e0e3048e911d.sketch_text.stroke-132"),sQuery(id+"FHMxAyK4CFUKdhS_1.wireOp",EDGE,"1cb9c079-ea9b-4899-8069-e0e3048e911d.sketch_text.stroke-133"),sQuery(id+"FHMxAyK4CFUKdhS_1.wireOp",EDGE,"1cb9c079-ea9b-4899-8069-e0e3048e911d.sketch_text.stroke-134"),sQuery(id+"FHMxAyK4CFUKdhS_1.wireOp",EDGE,"1cb9c079-ea9b-4899-8069-e0e3048e911d.sketch_text.stroke-135"),sQuery(id+"FHMxAyK4CFUKdhS_1.wireOp",EDGE,"1cb9c079-ea9b-4899-8069-e0e3048e911d.sketch_text.stroke-136"),sQuery(id+"FHMxAyK4CFUKdhS_1.wireOp",EDGE,"1cb9c079-ea9b-4899-8069-e0e3048e911d.sketch_text.stroke-137"),sQuery(id+"FHMxAyK4CFUKdhS_1.wireOp",EDGE,"1cb9c079-ea9b-4899-8069-e0e3048e911d.sketch_text.stroke-138"),sQuery(id+"FHMxAyK4CFUKdhS_1.wireOp",EDGE,"1cb9c079-ea9b-4899-8069-e0e3048e911d.sketch_text.stroke-139"),sQuery(id+"FHMxAyK4CFUKdhS_1.wireOp",EDGE,"1cb9c079-ea9b-4899-8069-e0e3048e911d.sketch_text.stroke-140"),sQuery(id+"FHMxAyK4CFUKdhS_1.wireOp",EDGE,"1cb9c079-ea9b-4899-8069-e0e3048e911d.sketch_text.stroke-141"),sQuery(id+"FHMxAyK4CFUKdhS_1.wireOp",EDGE,"1cb9c079-ea9b-4899-8069-e0e3048e911d.sketch_text.stroke-142"),sQuery(id+"FHMxAyK4CFUKdhS_1.wireOp",EDGE,"1cb9c079-ea9b-4899-8069-e0e3048e911d.sketch_text.stroke-143"),sQuery(id+"FHMxAyK4CFUKdhS_1.wireOp",EDGE,"1cb9c079-ea9b-4899-8069-e0e3048e911d.sketch_text.stroke-144"),sQuery(id+"FHMxAyK4CFUKdhS_1.wireOp",EDGE,"1cb9c079-ea9b-4899-8069-e0e3048e911d.sketch_text.stroke-145"),sQuery(id+"FHMxAyK4CFUKdhS_1.wireOp",EDGE,"1cb9c079-ea9b-4899-8069-e0e3048e911d.sketch_text.stroke-146"),sQuery(id+"FHMxAyK4CFUKdhS_1.wireOp",EDGE,"1cb9c079-ea9b-4899-8069-e0e3048e911d.sketch_text.stroke-147"),sQuery(id+"FHMxAyK4CFUKdhS_1.wireOp",EDGE,"1cb9c079-ea9b-4899-8069-e0e3048e911d.sketch_text.stroke-148"),sQuery(id+"FHMxAyK4CFUKdhS_1.wireOp",EDGE,"1cb9c079-ea9b-4899-8069-e0e3048e911d.sketch_text.stroke-149"),sQuery(id+"FHMxAyK4CFUKdhS_1.wireOp",EDGE,"1cb9c079-ea9b-4899-8069-e0e3048e911d.sketch_text.stroke-150"),sQuery(id+"FHMxAyK4CFUKdhS_1.wireOp",EDGE,"1cb9c079-ea9b-4899-8069-e0e3048e911d.sketch_text.stroke-151"),sQuery(id+"FHMxAyK4CFUKdhS_1.wireOp",EDGE,"1cb9c079-ea9b-4899-8069-e0e3048e911d.sketch_text.stroke-152"),sQuery(id+"FHMxAyK4CFUKdhS_1.wireOp",EDGE,"1cb9c079-ea9b-4899-8069-e0e3048e911d.sketch_text.stroke-153"),sQuery(id+"FHMxAyK4CFUKdhS_1.wireOp",EDGE,"1cb9c079-ea9b-4899-8069-e0e3048e911d.sketch_text.stroke-159"),sQuery(id+"FHMxAyK4CFUKdhS_1.wireOp",EDGE,"1cb9c079-ea9b-4899-8069-e0e3048e911d.sketch_text.stroke-160"),sQuery(id+"FHMxAyK4CFUKdhS_1.wireOp",EDGE,"1cb9c079-ea9b-4899-8069-e0e3048e911d.sketch_text.stroke-161"),sQuery(id+"FHMxAyK4CFUKdhS_1.wireOp",EDGE,"1cb9c079-ea9b-4899-8069-e0e3048e911d.sketch_text.stroke-162"),sQuery(id+"FHMxAyK4CFUKdhS_1.wireOp",EDGE,"1cb9c079-ea9b-4899-8069-e0e3048e911d.sketch_text.stroke-163"),sQuery(id+"FHMxAyK4CFUKdhS_1.wireOp",EDGE,"1cb9c079-ea9b-4899-8069-e0e3048e911d.sketch_text.stroke-164"),sQuery(id+"FHMxAyK4CFUKdhS_1.wireOp",EDGE,"1cb9c079-ea9b-4899-8069-e0e3048e911d.sketch_text.stroke-165"),sQuery(id+"FHMxAyK4CFUKdhS_1.wireOp",EDGE,"1cb9c079-ea9b-4899-8069-e0e3048e911d.sketch_text.stroke-166"),sQuery(id+"FHMxAyK4CFUKdhS_1.wireOp",EDGE,"1cb9c079-ea9b-4899-8069-e0e3048e911d.sketch_text.stroke-167"),sQuery(id+"FHMxAyK4CFUKdhS_1.wireOp",EDGE,"1cb9c079-ea9b-4899-8069-e0e3048e911d.sketch_text.stroke-168"),sQuery(id+"FHMxAyK4CFUKdhS_1.wireOp",EDGE,"1cb9c079-ea9b-4899-8069-e0e3048e911d.sketch_text.stroke-169"),sQuery(id+"FHMxAyK4CFUKdhS_1.wireOp",EDGE,"1cb9c079-ea9b-4899-8069-e0e3048e911d.sketch_text.stroke-170"),sQuery(id+"FHMxAyK4CFUKdhS_1.wireOp",EDGE,"1cb9c079-ea9b-4899-8069-e0e3048e911d.sketch_text.stroke-171"),sQuery(id+"FHMxAyK4CFUKdhS_1.wireOp",EDGE,"1cb9c079-ea9b-4899-8069-e0e3048e911d.sketch_text.stroke-172"),sQuery(id+"FHMxAyK4CFUKdhS_1.wireOp",EDGE,"1cb9c079-ea9b-4899-8069-e0e3048e911d.sketch_text.stroke-173"),sQuery(id+"FHMxAyK4CFUKdhS_1.wireOp",EDGE,"1cb9c079-ea9b-4899-8069-e0e3048e911d.sketch_text.stroke-174"),sQuery(id+"FHMxAyK4CFUKdhS_1.wireOp",EDGE,"1cb9c079-ea9b-4899-8069-e0e3048e911d.sketch_text.stroke-175"),sQuery(id+"FHMxAyK4CFUKdhS_1.wireOp",EDGE,"1cb9c079-ea9b-4899-8069-e0e3048e911d.sketch_text.stroke-176"),sQuery(id+"FHMxAyK4CFUKdhS_1.wireOp",EDGE,"1cb9c079-ea9b-4899-8069-e0e3048e911d.sketch_text.stroke-177"),sQuery(id+"FHMxAyK4CFUKdhS_1.wireOp",EDGE,"1cb9c079-ea9b-4899-8069-e0e3048e911d.sketch_text.stroke-178"),sQuery(id+"FHMxAyK4CFUKdhS_1.wireOp",EDGE,"1cb9c079-ea9b-4899-8069-e0e3048e911d.sketch_text.stroke-179"),sQuery(id+"FHMxAyK4CFUKdhS_1.wireOp",EDGE,"1cb9c079-ea9b-4899-8069-e0e3048e911d.sketch_text.stroke-180"),subQ0,subQ2])],"isStart":true}),makeQuery(id+"F4.opExtrude","SWEPT_FACE",FACE,{"disambiguationData":[OSD([subQ2])]})])],"derivedFrom":makeQuery(id+"F4.opExtrude","CAP_EDGE",EDGE,{"disambiguationData":[OSD([subQ2])],"isStart":true})});}
            var Q11;
            {var subQ0=sQuery(id+"F0.wireOp",EDGE,"E0.top");var subQ1=sQuery(id+"F0.wireOp",EDGE,"E0.bottom");var subQ2=sQuery(id+"F3.wireOp",EDGE,"6ee83ff3-586e-4dbe-aaea-af71240543bd");Q11=makeQuery(id+"F4.boolean.opBoolean","SPLIT",EDGE,{"disambiguationData":[TD([makeQuery(id+"F1.opExtrude","CAP_FACE",FACE,{"disambiguationData":[OSD([subQ1,subQ0,sQuery(id+"F0.wireOp",EDGE,"E0.left"),sQuery(id+"F0.wireOp",EDGE,"E0.right")])],"isStart":false}),makeQuery(id+"F1.opExtrude","SWEPT_FACE",FACE,{"disambiguationData":[OSD([subQ0])]}),makeQuery(id+"F4.opExtrude","CAP_FACE",FACE,{"disambiguationData":[OSD([subQ1,sQuery(id+"F2.wireOp",EDGE,"fcba4419-a2ee-464f-be9d-58f11bf3418b.sketch_text.stroke-0"),sQuery(id+"F2.wireOp",EDGE,"fcba4419-a2ee-464f-be9d-58f11bf3418b.sketch_text.stroke-1"),sQuery(id+"F2.wireOp",EDGE,"fcba4419-a2ee-464f-be9d-58f11bf3418b.sketch_text.stroke-2"),sQuery(id+"F2.wireOp",EDGE,"fcba4419-a2ee-464f-be9d-58f11bf3418b.sketch_text.stroke-3"),sQuery(id+"F2.wireOp",EDGE,"fcba4419-a2ee-464f-be9d-58f11bf3418b.sketch_text.stroke-4"),sQuery(id+"F2.wireOp",EDGE,"fcba4419-a2ee-464f-be9d-58f11bf3418b.sketch_text.stroke-5"),sQuery(id+"F2.wireOp",EDGE,"fcba4419-a2ee-464f-be9d-58f11bf3418b.sketch_text.stroke-6"),sQuery(id+"F2.wireOp",EDGE,"fcba4419-a2ee-464f-be9d-58f11bf3418b.sketch_text.stroke-7"),sQuery(id+"F2.wireOp",EDGE,"fcba4419-a2ee-464f-be9d-58f11bf3418b.sketch_text.stroke-8"),sQuery(id+"F2.wireOp",EDGE,"fcba4419-a2ee-464f-be9d-58f11bf3418b.sketch_text.stroke-9"),sQuery(id+"F2.wireOp",EDGE,"fcba4419-a2ee-464f-be9d-58f11bf3418b.sketch_text.stroke-10"),sQuery(id+"F2.wireOp",EDGE,"fcba4419-a2ee-464f-be9d-58f11bf3418b.sketch_text.stroke-11"),sQuery(id+"F2.wireOp",EDGE,"fcba4419-a2ee-464f-be9d-58f11bf3418b.sketch_text.stroke-12"),sQuery(id+"F2.wireOp",EDGE,"fcba4419-a2ee-464f-be9d-58f11bf3418b.sketch_text.stroke-13"),sQuery(id+"F2.wireOp",EDGE,"fcba4419-a2ee-464f-be9d-58f11bf3418b.sketch_text.stroke-14"),sQuery(id+"F2.wireOp",EDGE,"fcba4419-a2ee-464f-be9d-58f11bf3418b.sketch_text.stroke-15"),sQuery(id+"F2.wireOp",EDGE,"fcba4419-a2ee-464f-be9d-58f11bf3418b.sketch_text.stroke-16"),sQuery(id+"F2.wireOp",EDGE,"fcba4419-a2ee-464f-be9d-58f11bf3418b.sketch_text.stroke-17"),sQuery(id+"F2.wireOp",EDGE,"fcba4419-a2ee-464f-be9d-58f11bf3418b.sketch_text.stroke-18"),sQuery(id+"F2.wireOp",EDGE,"fcba4419-a2ee-464f-be9d-58f11bf3418b.sketch_text.stroke-19"),sQuery(id+"F2.wireOp",EDGE,"fcba4419-a2ee-464f-be9d-58f11bf3418b.sketch_text.stroke-20"),sQuery(id+"F2.wireOp",EDGE,"fcba4419-a2ee-464f-be9d-58f11bf3418b.sketch_text.stroke-21"),sQuery(id+"F2.wireOp",EDGE,"fcba4419-a2ee-464f-be9d-58f11bf3418b.sketch_text.stroke-22"),sQuery(id+"F2.wireOp",EDGE,"fcba4419-a2ee-464f-be9d-58f11bf3418b.sketch_text.stroke-23"),sQuery(id+"F2.wireOp",EDGE,"fcba4419-a2ee-464f-be9d-58f11bf3418b.sketch_text.stroke-24"),sQuery(id+"F2.wireOp",EDGE,"fcba4419-a2ee-464f-be9d-58f11bf3418b.sketch_text.stroke-25"),sQuery(id+"F2.wireOp",EDGE,"fcba4419-a2ee-464f-be9d-58f11bf3418b.sketch_text.stroke-26"),sQuery(id+"F2.wireOp",EDGE,"fcba4419-a2ee-464f-be9d-58f11bf3418b.sketch_text.stroke-27"),sQuery(id+"F2.wireOp",EDGE,"fcba4419-a2ee-464f-be9d-58f11bf3418b.sketch_text.stroke-28"),sQuery(id+"F2.wireOp",EDGE,"fcba4419-a2ee-464f-be9d-58f11bf3418b.sketch_text.stroke-29"),sQuery(id+"F2.wireOp",EDGE,"fcba4419-a2ee-464f-be9d-58f11bf3418b.sketch_text.stroke-30"),sQuery(id+"F2.wireOp",EDGE,"fcba4419-a2ee-464f-be9d-58f11bf3418b.sketch_text.stroke-31"),sQuery(id+"F2.wireOp",EDGE,"fcba4419-a2ee-464f-be9d-58f11bf3418b.sketch_text.stroke-32"),sQuery(id+"F2.wireOp",EDGE,"fcba4419-a2ee-464f-be9d-58f11bf3418b.sketch_text.stroke-33"),sQuery(id+"F2.wireOp",EDGE,"fcba4419-a2ee-464f-be9d-58f11bf3418b.sketch_text.stroke-34"),sQuery(id+"F2.wireOp",EDGE,"fcba4419-a2ee-464f-be9d-58f11bf3418b.sketch_text.stroke-35"),sQuery(id+"F2.wireOp",EDGE,"fcba4419-a2ee-464f-be9d-58f11bf3418b.sketch_text.stroke-36"),sQuery(id+"F2.wireOp",EDGE,"fcba4419-a2ee-464f-be9d-58f11bf3418b.sketch_text.stroke-37"),sQuery(id+"F2.wireOp",EDGE,"fcba4419-a2ee-464f-be9d-58f11bf3418b.sketch_text.stroke-38"),sQuery(id+"F2.wireOp",EDGE,"fcba4419-a2ee-464f-be9d-58f11bf3418b.sketch_text.stroke-39"),sQuery(id+"F2.wireOp",EDGE,"fcba4419-a2ee-464f-be9d-58f11bf3418b.sketch_text.stroke-40"),sQuery(id+"F2.wireOp",EDGE,"fcba4419-a2ee-464f-be9d-58f11bf3418b.sketch_text.stroke-41"),sQuery(id+"F2.wireOp",EDGE,"fcba4419-a2ee-464f-be9d-58f11bf3418b.sketch_text.stroke-42"),sQuery(id+"F2.wireOp",EDGE,"fcba4419-a2ee-464f-be9d-58f11bf3418b.sketch_text.stroke-43"),sQuery(id+"F2.wireOp",EDGE,"fcba4419-a2ee-464f-be9d-58f11bf3418b.sketch_text.stroke-44"),sQuery(id+"F2.wireOp",EDGE,"fcba4419-a2ee-464f-be9d-58f11bf3418b.sketch_text.stroke-45"),sQuery(id+"F2.wireOp",EDGE,"fcba4419-a2ee-464f-be9d-58f11bf3418b.sketch_text.stroke-46"),sQuery(id+"F2.wireOp",EDGE,"fcba4419-a2ee-464f-be9d-58f11bf3418b.sketch_text.stroke-47"),sQuery(id+"F2.wireOp",EDGE,"fcba4419-a2ee-464f-be9d-58f11bf3418b.sketch_text.stroke-48"),sQuery(id+"F2.wireOp",EDGE,"fcba4419-a2ee-464f-be9d-58f11bf3418b.sketch_text.stroke-49"),sQuery(id+"F2.wireOp",EDGE,"fcba4419-a2ee-464f-be9d-58f11bf3418b.sketch_text.stroke-50"),sQuery(id+"F2.wireOp",EDGE,"fcba4419-a2ee-464f-be9d-58f11bf3418b.sketch_text.stroke-51"),sQuery(id+"F2.wireOp",EDGE,"fcba4419-a2ee-464f-be9d-58f11bf3418b.sketch_text.stroke-52"),sQuery(id+"F2.wireOp",EDGE,"fcba4419-a2ee-464f-be9d-58f11bf3418b.sketch_text.stroke-53"),sQuery(id+"F2.wireOp",EDGE,"fcba4419-a2ee-464f-be9d-58f11bf3418b.sketch_text.stroke-54"),sQuery(id+"F2.wireOp",EDGE,"fcba4419-a2ee-464f-be9d-58f11bf3418b.sketch_text.stroke-55"),sQuery(id+"F2.wireOp",EDGE,"fcba4419-a2ee-464f-be9d-58f11bf3418b.sketch_text.stroke-56"),sQuery(id+"F2.wireOp",EDGE,"fcba4419-a2ee-464f-be9d-58f11bf3418b.sketch_text.stroke-57"),sQuery(id+"F2.wireOp",EDGE,"fcba4419-a2ee-464f-be9d-58f11bf3418b.sketch_text.stroke-58"),sQuery(id+"F2.wireOp",EDGE,"fcba4419-a2ee-464f-be9d-58f11bf3418b.sketch_text.stroke-59"),sQuery(id+"F2.wireOp",EDGE,"fcba4419-a2ee-464f-be9d-58f11bf3418b.sketch_text.stroke-60"),sQuery(id+"F2.wireOp",EDGE,"fcba4419-a2ee-464f-be9d-58f11bf3418b.sketch_text.stroke-61"),sQuery(id+"F2.wireOp",EDGE,"fcba4419-a2ee-464f-be9d-58f11bf3418b.sketch_text.stroke-62"),sQuery(id+"F2.wireOp",EDGE,"fcba4419-a2ee-464f-be9d-58f11bf3418b.sketch_text.stroke-63"),sQuery(id+"F2.wireOp",EDGE,"fcba4419-a2ee-464f-be9d-58f11bf3418b.sketch_text.stroke-64"),sQuery(id+"F2.wireOp",EDGE,"fcba4419-a2ee-464f-be9d-58f11bf3418b.sketch_text.stroke-65"),sQuery(id+"F2.wireOp",EDGE,"fcba4419-a2ee-464f-be9d-58f11bf3418b.sketch_text.stroke-66"),sQuery(id+"F2.wireOp",EDGE,"fcba4419-a2ee-464f-be9d-58f11bf3418b.sketch_text.stroke-67"),sQuery(id+"F2.wireOp",EDGE,"fcba4419-a2ee-464f-be9d-58f11bf3418b.sketch_text.stroke-68"),sQuery(id+"F2.wireOp",EDGE,"fcba4419-a2ee-464f-be9d-58f11bf3418b.sketch_text.stroke-69"),sQuery(id+"F2.wireOp",EDGE,"fcba4419-a2ee-464f-be9d-58f11bf3418b.sketch_text.stroke-70"),sQuery(id+"F2.wireOp",EDGE,"fcba4419-a2ee-464f-be9d-58f11bf3418b.sketch_text.stroke-71"),sQuery(id+"F2.wireOp",EDGE,"fcba4419-a2ee-464f-be9d-58f11bf3418b.sketch_text.stroke-72"),sQuery(id+"F2.wireOp",EDGE,"fcba4419-a2ee-464f-be9d-58f11bf3418b.sketch_text.stroke-73"),sQuery(id+"F2.wireOp",EDGE,"fcba4419-a2ee-464f-be9d-58f11bf3418b.sketch_text.stroke-74"),sQuery(id+"F2.wireOp",EDGE,"fcba4419-a2ee-464f-be9d-58f11bf3418b.sketch_text.stroke-75"),sQuery(id+"F2.wireOp",EDGE,"fcba4419-a2ee-464f-be9d-58f11bf3418b.sketch_text.stroke-76"),sQuery(id+"F2.wireOp",EDGE,"fcba4419-a2ee-464f-be9d-58f11bf3418b.sketch_text.stroke-77"),sQuery(id+"F2.wireOp",EDGE,"fcba4419-a2ee-464f-be9d-58f11bf3418b.sketch_text.stroke-78"),sQuery(id+"F2.wireOp",EDGE,"fcba4419-a2ee-464f-be9d-58f11bf3418b.sketch_text.stroke-79"),sQuery(id+"F2.wireOp",EDGE,"fcba4419-a2ee-464f-be9d-58f11bf3418b.sketch_text.stroke-80"),sQuery(id+"F2.wireOp",EDGE,"fcba4419-a2ee-464f-be9d-58f11bf3418b.sketch_text.stroke-81"),sQuery(id+"F2.wireOp",EDGE,"fcba4419-a2ee-464f-be9d-58f11bf3418b.sketch_text.stroke-82"),sQuery(id+"F2.wireOp",EDGE,"fcba4419-a2ee-464f-be9d-58f11bf3418b.sketch_text.stroke-83"),sQuery(id+"F2.wireOp",EDGE,"fcba4419-a2ee-464f-be9d-58f11bf3418b.sketch_text.stroke-84"),sQuery(id+"F2.wireOp",EDGE,"fcba4419-a2ee-464f-be9d-58f11bf3418b.sketch_text.stroke-85"),sQuery(id+"F2.wireOp",EDGE,"fcba4419-a2ee-464f-be9d-58f11bf3418b.sketch_text.stroke-86"),sQuery(id+"F2.wireOp",EDGE,"fcba4419-a2ee-464f-be9d-58f11bf3418b.sketch_text.stroke-87"),sQuery(id+"F2.wireOp",EDGE,"fcba4419-a2ee-464f-be9d-58f11bf3418b.sketch_text.stroke-88"),sQuery(id+"F2.wireOp",EDGE,"fcba4419-a2ee-464f-be9d-58f11bf3418b.sketch_text.stroke-89"),sQuery(id+"F2.wireOp",EDGE,"fcba4419-a2ee-464f-be9d-58f11bf3418b.sketch_text.stroke-90"),sQuery(id+"F2.wireOp",EDGE,"fcba4419-a2ee-464f-be9d-58f11bf3418b.sketch_text.stroke-91"),sQuery(id+"F2.wireOp",EDGE,"fcba4419-a2ee-464f-be9d-58f11bf3418b.sketch_text.stroke-92"),sQuery(id+"F2.wireOp",EDGE,"fcba4419-a2ee-464f-be9d-58f11bf3418b.sketch_text.stroke-93"),sQuery(id+"F2.wireOp",EDGE,"fcba4419-a2ee-464f-be9d-58f11bf3418b.sketch_text.stroke-94"),sQuery(id+"F2.wireOp",EDGE,"fcba4419-a2ee-464f-be9d-58f11bf3418b.sketch_text.stroke-95"),sQuery(id+"F2.wireOp",EDGE,"fcba4419-a2ee-464f-be9d-58f11bf3418b.sketch_text.stroke-96"),sQuery(id+"F2.wireOp",EDGE,"fcba4419-a2ee-464f-be9d-58f11bf3418b.sketch_text.stroke-97"),sQuery(id+"F2.wireOp",EDGE,"fcba4419-a2ee-464f-be9d-58f11bf3418b.sketch_text.stroke-98"),sQuery(id+"F2.wireOp",EDGE,"fcba4419-a2ee-464f-be9d-58f11bf3418b.sketch_text.stroke-99"),sQuery(id+"F2.wireOp",EDGE,"fcba4419-a2ee-464f-be9d-58f11bf3418b.sketch_text.stroke-100"),sQuery(id+"F2.wireOp",EDGE,"fcba4419-a2ee-464f-be9d-58f11bf3418b.sketch_text.stroke-101"),sQuery(id+"F2.wireOp",EDGE,"fcba4419-a2ee-464f-be9d-58f11bf3418b.sketch_text.stroke-102"),sQuery(id+"F2.wireOp",EDGE,"fcba4419-a2ee-464f-be9d-58f11bf3418b.sketch_text.stroke-103"),sQuery(id+"F2.wireOp",EDGE,"fcba4419-a2ee-464f-be9d-58f11bf3418b.sketch_text.stroke-104"),sQuery(id+"F2.wireOp",EDGE,"fcba4419-a2ee-464f-be9d-58f11bf3418b.sketch_text.stroke-105"),sQuery(id+"F2.wireOp",EDGE,"fcba4419-a2ee-464f-be9d-58f11bf3418b.sketch_text.stroke-106"),sQuery(id+"F2.wireOp",EDGE,"fcba4419-a2ee-464f-be9d-58f11bf3418b.sketch_text.stroke-107"),sQuery(id+"F2.wireOp",EDGE,"fcba4419-a2ee-464f-be9d-58f11bf3418b.sketch_text.stroke-108"),sQuery(id+"F2.wireOp",EDGE,"fcba4419-a2ee-464f-be9d-58f11bf3418b.sketch_text.stroke-109"),sQuery(id+"F2.wireOp",EDGE,"fcba4419-a2ee-464f-be9d-58f11bf3418b.sketch_text.stroke-110"),sQuery(id+"F2.wireOp",EDGE,"fcba4419-a2ee-464f-be9d-58f11bf3418b.sketch_text.stroke-111"),sQuery(id+"F2.wireOp",EDGE,"fcba4419-a2ee-464f-be9d-58f11bf3418b.sketch_text.stroke-112"),sQuery(id+"F2.wireOp",EDGE,"fcba4419-a2ee-464f-be9d-58f11bf3418b.sketch_text.stroke-113"),sQuery(id+"F2.wireOp",EDGE,"fcba4419-a2ee-464f-be9d-58f11bf3418b.sketch_text.stroke-114"),sQuery(id+"F2.wireOp",EDGE,"fcba4419-a2ee-464f-be9d-58f11bf3418b.sketch_text.stroke-115"),sQuery(id+"F2.wireOp",EDGE,"fcba4419-a2ee-464f-be9d-58f11bf3418b.sketch_text.stroke-116"),sQuery(id+"F2.wireOp",EDGE,"fcba4419-a2ee-464f-be9d-58f11bf3418b.sketch_text.stroke-117"),sQuery(id+"F2.wireOp",EDGE,"fcba4419-a2ee-464f-be9d-58f11bf3418b.sketch_text.stroke-118"),sQuery(id+"F2.wireOp",EDGE,"fcba4419-a2ee-464f-be9d-58f11bf3418b.sketch_text.stroke-119"),sQuery(id+"F2.wireOp",EDGE,"fcba4419-a2ee-464f-be9d-58f11bf3418b.sketch_text.stroke-120"),sQuery(id+"F2.wireOp",EDGE,"fcba4419-a2ee-464f-be9d-58f11bf3418b.sketch_text.stroke-121"),sQuery(id+"F2.wireOp",EDGE,"fcba4419-a2ee-464f-be9d-58f11bf3418b.sketch_text.stroke-122"),sQuery(id+"F2.wireOp",EDGE,"fcba4419-a2ee-464f-be9d-58f11bf3418b.sketch_text.stroke-123"),sQuery(id+"F2.wireOp",EDGE,"fcba4419-a2ee-464f-be9d-58f11bf3418b.sketch_text.stroke-124"),sQuery(id+"F2.wireOp",EDGE,"fcba4419-a2ee-464f-be9d-58f11bf3418b.sketch_text.stroke-125"),sQuery(id+"F2.wireOp",EDGE,"fcba4419-a2ee-464f-be9d-58f11bf3418b.sketch_text.stroke-126"),sQuery(id+"F2.wireOp",EDGE,"fcba4419-a2ee-464f-be9d-58f11bf3418b.sketch_text.stroke-127"),sQuery(id+"F2.wireOp",EDGE,"fcba4419-a2ee-464f-be9d-58f11bf3418b.sketch_text.stroke-128"),sQuery(id+"F2.wireOp",EDGE,"fcba4419-a2ee-464f-be9d-58f11bf3418b.sketch_text.stroke-129"),sQuery(id+"F2.wireOp",EDGE,"fcba4419-a2ee-464f-be9d-58f11bf3418b.sketch_text.stroke-130"),sQuery(id+"F2.wireOp",EDGE,"fcba4419-a2ee-464f-be9d-58f11bf3418b.sketch_text.stroke-131"),sQuery(id+"F2.wireOp",EDGE,"fcba4419-a2ee-464f-be9d-58f11bf3418b.sketch_text.stroke-132"),sQuery(id+"F2.wireOp",EDGE,"fcba4419-a2ee-464f-be9d-58f11bf3418b.sketch_text.stroke-133"),sQuery(id+"F2.wireOp",EDGE,"fcba4419-a2ee-464f-be9d-58f11bf3418b.sketch_text.stroke-134"),sQuery(id+"F2.wireOp",EDGE,"fcba4419-a2ee-464f-be9d-58f11bf3418b.sketch_text.stroke-135"),sQuery(id+"F2.wireOp",EDGE,"fcba4419-a2ee-464f-be9d-58f11bf3418b.sketch_text.stroke-136"),sQuery(id+"F2.wireOp",EDGE,"fcba4419-a2ee-464f-be9d-58f11bf3418b.sketch_text.stroke-137"),sQuery(id+"F2.wireOp",EDGE,"fcba4419-a2ee-464f-be9d-58f11bf3418b.sketch_text.stroke-138"),sQuery(id+"F2.wireOp",EDGE,"fcba4419-a2ee-464f-be9d-58f11bf3418b.sketch_text.stroke-139"),sQuery(id+"F2.wireOp",EDGE,"fcba4419-a2ee-464f-be9d-58f11bf3418b.sketch_text.stroke-140"),sQuery(id+"F2.wireOp",EDGE,"fcba4419-a2ee-464f-be9d-58f11bf3418b.sketch_text.stroke-141"),sQuery(id+"F2.wireOp",EDGE,"fcba4419-a2ee-464f-be9d-58f11bf3418b.sketch_text.stroke-142"),sQuery(id+"F2.wireOp",EDGE,"fcba4419-a2ee-464f-be9d-58f11bf3418b.sketch_text.stroke-143"),sQuery(id+"F2.wireOp",EDGE,"fcba4419-a2ee-464f-be9d-58f11bf3418b.sketch_text.stroke-144"),sQuery(id+"F2.wireOp",EDGE,"fcba4419-a2ee-464f-be9d-58f11bf3418b.sketch_text.stroke-145"),sQuery(id+"F2.wireOp",EDGE,"fcba4419-a2ee-464f-be9d-58f11bf3418b.sketch_text.stroke-146"),sQuery(id+"F2.wireOp",EDGE,"fcba4419-a2ee-464f-be9d-58f11bf3418b.sketch_text.stroke-147"),sQuery(id+"F2.wireOp",EDGE,"fcba4419-a2ee-464f-be9d-58f11bf3418b.sketch_text.stroke-148"),sQuery(id+"F2.wireOp",EDGE,"fcba4419-a2ee-464f-be9d-58f11bf3418b.sketch_text.stroke-149"),sQuery(id+"F2.wireOp",EDGE,"fcba4419-a2ee-464f-be9d-58f11bf3418b.sketch_text.stroke-150"),sQuery(id+"F2.wireOp",EDGE,"fcba4419-a2ee-464f-be9d-58f11bf3418b.sketch_text.stroke-151"),sQuery(id+"F2.wireOp",EDGE,"fcba4419-a2ee-464f-be9d-58f11bf3418b.sketch_text.stroke-152"),sQuery(id+"F2.wireOp",EDGE,"fcba4419-a2ee-464f-be9d-58f11bf3418b.sketch_text.stroke-153"),sQuery(id+"F2.wireOp",EDGE,"fcba4419-a2ee-464f-be9d-58f11bf3418b.sketch_text.stroke-154"),sQuery(id+"F2.wireOp",EDGE,"fcba4419-a2ee-464f-be9d-58f11bf3418b.sketch_text.stroke-155"),sQuery(id+"F2.wireOp",EDGE,"fcba4419-a2ee-464f-be9d-58f11bf3418b.sketch_text.stroke-156"),sQuery(id+"F2.wireOp",EDGE,"fcba4419-a2ee-464f-be9d-58f11bf3418b.sketch_text.stroke-157"),sQuery(id+"F2.wireOp",EDGE,"fcba4419-a2ee-464f-be9d-58f11bf3418b.sketch_text.stroke-158"),sQuery(id+"F2.wireOp",EDGE,"fcba4419-a2ee-464f-be9d-58f11bf3418b.sketch_text.stroke-159"),sQuery(id+"F2.wireOp",EDGE,"fcba4419-a2ee-464f-be9d-58f11bf3418b.sketch_text.stroke-160"),sQuery(id+"F2.wireOp",EDGE,"fcba4419-a2ee-464f-be9d-58f11bf3418b.sketch_text.stroke-161"),sQuery(id+"F2.wireOp",EDGE,"fcba4419-a2ee-464f-be9d-58f11bf3418b.sketch_text.stroke-162"),sQuery(id+"F2.wireOp",EDGE,"fcba4419-a2ee-464f-be9d-58f11bf3418b.sketch_text.stroke-163"),sQuery(id+"F2.wireOp",EDGE,"fcba4419-a2ee-464f-be9d-58f11bf3418b.sketch_text.stroke-164"),sQuery(id+"F2.wireOp",EDGE,"fcba4419-a2ee-464f-be9d-58f11bf3418b.sketch_text.stroke-165"),sQuery(id+"F2.wireOp",EDGE,"fcba4419-a2ee-464f-be9d-58f11bf3418b.sketch_text.stroke-166"),sQuery(id+"F2.wireOp",EDGE,"fcba4419-a2ee-464f-be9d-58f11bf3418b.sketch_text.stroke-167"),sQuery(id+"F2.wireOp",EDGE,"fcba4419-a2ee-464f-be9d-58f11bf3418b.sketch_text.stroke-168"),sQuery(id+"F2.wireOp",EDGE,"fcba4419-a2ee-464f-be9d-58f11bf3418b.sketch_text.stroke-169"),sQuery(id+"F2.wireOp",EDGE,"fcba4419-a2ee-464f-be9d-58f11bf3418b.sketch_text.stroke-170"),sQuery(id+"F2.wireOp",EDGE,"fcba4419-a2ee-464f-be9d-58f11bf3418b.sketch_text.stroke-171"),sQuery(id+"F2.wireOp",EDGE,"fcba4419-a2ee-464f-be9d-58f11bf3418b.sketch_text.stroke-172"),sQuery(id+"F2.wireOp",EDGE,"fcba4419-a2ee-464f-be9d-58f11bf3418b.sketch_text.stroke-173"),sQuery(id+"FHMxAyK4CFUKdhS_1.wireOp",EDGE,"1cb9c079-ea9b-4899-8069-e0e3048e911d.sketch_text.stroke-0"),sQuery(id+"FHMxAyK4CFUKdhS_1.wireOp",EDGE,"1cb9c079-ea9b-4899-8069-e0e3048e911d.sketch_text.stroke-1"),sQuery(id+"FHMxAyK4CFUKdhS_1.wireOp",EDGE,"1cb9c079-ea9b-4899-8069-e0e3048e911d.sketch_text.stroke-2"),sQuery(id+"FHMxAyK4CFUKdhS_1.wireOp",EDGE,"1cb9c079-ea9b-4899-8069-e0e3048e911d.sketch_text.stroke-3"),sQuery(id+"FHMxAyK4CFUKdhS_1.wireOp",EDGE,"1cb9c079-ea9b-4899-8069-e0e3048e911d.sketch_text.stroke-4"),sQuery(id+"FHMxAyK4CFUKdhS_1.wireOp",EDGE,"1cb9c079-ea9b-4899-8069-e0e3048e911d.sketch_text.stroke-5"),sQuery(id+"FHMxAyK4CFUKdhS_1.wireOp",EDGE,"1cb9c079-ea9b-4899-8069-e0e3048e911d.sketch_text.stroke-6"),sQuery(id+"FHMxAyK4CFUKdhS_1.wireOp",EDGE,"1cb9c079-ea9b-4899-8069-e0e3048e911d.sketch_text.stroke-7"),sQuery(id+"FHMxAyK4CFUKdhS_1.wireOp",EDGE,"1cb9c079-ea9b-4899-8069-e0e3048e911d.sketch_text.stroke-8"),sQuery(id+"FHMxAyK4CFUKdhS_1.wireOp",EDGE,"1cb9c079-ea9b-4899-8069-e0e3048e911d.sketch_text.stroke-9"),sQuery(id+"FHMxAyK4CFUKdhS_1.wireOp",EDGE,"1cb9c079-ea9b-4899-8069-e0e3048e911d.sketch_text.stroke-10"),sQuery(id+"FHMxAyK4CFUKdhS_1.wireOp",EDGE,"1cb9c079-ea9b-4899-8069-e0e3048e911d.sketch_text.stroke-11"),sQuery(id+"FHMxAyK4CFUKdhS_1.wireOp",EDGE,"1cb9c079-ea9b-4899-8069-e0e3048e911d.sketch_text.stroke-12"),sQuery(id+"FHMxAyK4CFUKdhS_1.wireOp",EDGE,"1cb9c079-ea9b-4899-8069-e0e3048e911d.sketch_text.stroke-13"),sQuery(id+"FHMxAyK4CFUKdhS_1.wireOp",EDGE,"1cb9c079-ea9b-4899-8069-e0e3048e911d.sketch_text.stroke-14"),sQuery(id+"FHMxAyK4CFUKdhS_1.wireOp",EDGE,"1cb9c079-ea9b-4899-8069-e0e3048e911d.sketch_text.stroke-15"),sQuery(id+"FHMxAyK4CFUKdhS_1.wireOp",EDGE,"1cb9c079-ea9b-4899-8069-e0e3048e911d.sketch_text.stroke-16"),sQuery(id+"FHMxAyK4CFUKdhS_1.wireOp",EDGE,"1cb9c079-ea9b-4899-8069-e0e3048e911d.sketch_text.stroke-17"),sQuery(id+"FHMxAyK4CFUKdhS_1.wireOp",EDGE,"1cb9c079-ea9b-4899-8069-e0e3048e911d.sketch_text.stroke-18"),sQuery(id+"FHMxAyK4CFUKdhS_1.wireOp",EDGE,"1cb9c079-ea9b-4899-8069-e0e3048e911d.sketch_text.stroke-19"),sQuery(id+"FHMxAyK4CFUKdhS_1.wireOp",EDGE,"1cb9c079-ea9b-4899-8069-e0e3048e911d.sketch_text.stroke-20"),sQuery(id+"FHMxAyK4CFUKdhS_1.wireOp",EDGE,"1cb9c079-ea9b-4899-8069-e0e3048e911d.sketch_text.stroke-21"),sQuery(id+"FHMxAyK4CFUKdhS_1.wireOp",EDGE,"1cb9c079-ea9b-4899-8069-e0e3048e911d.sketch_text.stroke-22"),sQuery(id+"FHMxAyK4CFUKdhS_1.wireOp",EDGE,"1cb9c079-ea9b-4899-8069-e0e3048e911d.sketch_text.stroke-23"),sQuery(id+"FHMxAyK4CFUKdhS_1.wireOp",EDGE,"1cb9c079-ea9b-4899-8069-e0e3048e911d.sketch_text.stroke-24"),sQuery(id+"FHMxAyK4CFUKdhS_1.wireOp",EDGE,"1cb9c079-ea9b-4899-8069-e0e3048e911d.sketch_text.stroke-25"),sQuery(id+"FHMxAyK4CFUKdhS_1.wireOp",EDGE,"1cb9c079-ea9b-4899-8069-e0e3048e911d.sketch_text.stroke-26"),sQuery(id+"FHMxAyK4CFUKdhS_1.wireOp",EDGE,"1cb9c079-ea9b-4899-8069-e0e3048e911d.sketch_text.stroke-27"),sQuery(id+"FHMxAyK4CFUKdhS_1.wireOp",EDGE,"1cb9c079-ea9b-4899-8069-e0e3048e911d.sketch_text.stroke-28"),sQuery(id+"FHMxAyK4CFUKdhS_1.wireOp",EDGE,"1cb9c079-ea9b-4899-8069-e0e3048e911d.sketch_text.stroke-29"),sQuery(id+"FHMxAyK4CFUKdhS_1.wireOp",EDGE,"1cb9c079-ea9b-4899-8069-e0e3048e911d.sketch_text.stroke-30"),sQuery(id+"FHMxAyK4CFUKdhS_1.wireOp",EDGE,"1cb9c079-ea9b-4899-8069-e0e3048e911d.sketch_text.stroke-31"),sQuery(id+"FHMxAyK4CFUKdhS_1.wireOp",EDGE,"1cb9c079-ea9b-4899-8069-e0e3048e911d.sketch_text.stroke-32"),sQuery(id+"FHMxAyK4CFUKdhS_1.wireOp",EDGE,"1cb9c079-ea9b-4899-8069-e0e3048e911d.sketch_text.stroke-33"),sQuery(id+"FHMxAyK4CFUKdhS_1.wireOp",EDGE,"1cb9c079-ea9b-4899-8069-e0e3048e911d.sketch_text.stroke-34"),sQuery(id+"FHMxAyK4CFUKdhS_1.wireOp",EDGE,"1cb9c079-ea9b-4899-8069-e0e3048e911d.sketch_text.stroke-35"),sQuery(id+"FHMxAyK4CFUKdhS_1.wireOp",EDGE,"1cb9c079-ea9b-4899-8069-e0e3048e911d.sketch_text.stroke-36"),sQuery(id+"FHMxAyK4CFUKdhS_1.wireOp",EDGE,"1cb9c079-ea9b-4899-8069-e0e3048e911d.sketch_text.stroke-37"),sQuery(id+"FHMxAyK4CFUKdhS_1.wireOp",EDGE,"1cb9c079-ea9b-4899-8069-e0e3048e911d.sketch_text.stroke-38"),sQuery(id+"FHMxAyK4CFUKdhS_1.wireOp",EDGE,"1cb9c079-ea9b-4899-8069-e0e3048e911d.sketch_text.stroke-39"),sQuery(id+"FHMxAyK4CFUKdhS_1.wireOp",EDGE,"1cb9c079-ea9b-4899-8069-e0e3048e911d.sketch_text.stroke-40"),sQuery(id+"FHMxAyK4CFUKdhS_1.wireOp",EDGE,"1cb9c079-ea9b-4899-8069-e0e3048e911d.sketch_text.stroke-41"),sQuery(id+"FHMxAyK4CFUKdhS_1.wireOp",EDGE,"1cb9c079-ea9b-4899-8069-e0e3048e911d.sketch_text.stroke-42"),sQuery(id+"FHMxAyK4CFUKdhS_1.wireOp",EDGE,"1cb9c079-ea9b-4899-8069-e0e3048e911d.sketch_text.stroke-43"),sQuery(id+"FHMxAyK4CFUKdhS_1.wireOp",EDGE,"1cb9c079-ea9b-4899-8069-e0e3048e911d.sketch_text.stroke-44"),sQuery(id+"FHMxAyK4CFUKdhS_1.wireOp",EDGE,"1cb9c079-ea9b-4899-8069-e0e3048e911d.sketch_text.stroke-45"),sQuery(id+"FHMxAyK4CFUKdhS_1.wireOp",EDGE,"1cb9c079-ea9b-4899-8069-e0e3048e911d.sketch_text.stroke-46"),sQuery(id+"FHMxAyK4CFUKdhS_1.wireOp",EDGE,"1cb9c079-ea9b-4899-8069-e0e3048e911d.sketch_text.stroke-47"),sQuery(id+"FHMxAyK4CFUKdhS_1.wireOp",EDGE,"1cb9c079-ea9b-4899-8069-e0e3048e911d.sketch_text.stroke-48"),sQuery(id+"FHMxAyK4CFUKdhS_1.wireOp",EDGE,"1cb9c079-ea9b-4899-8069-e0e3048e911d.sketch_text.stroke-49"),sQuery(id+"FHMxAyK4CFUKdhS_1.wireOp",EDGE,"1cb9c079-ea9b-4899-8069-e0e3048e911d.sketch_text.stroke-50"),sQuery(id+"FHMxAyK4CFUKdhS_1.wireOp",EDGE,"1cb9c079-ea9b-4899-8069-e0e3048e911d.sketch_text.stroke-51"),sQuery(id+"FHMxAyK4CFUKdhS_1.wireOp",EDGE,"1cb9c079-ea9b-4899-8069-e0e3048e911d.sketch_text.stroke-52"),sQuery(id+"FHMxAyK4CFUKdhS_1.wireOp",EDGE,"1cb9c079-ea9b-4899-8069-e0e3048e911d.sketch_text.stroke-53"),sQuery(id+"FHMxAyK4CFUKdhS_1.wireOp",EDGE,"1cb9c079-ea9b-4899-8069-e0e3048e911d.sketch_text.stroke-54"),sQuery(id+"FHMxAyK4CFUKdhS_1.wireOp",EDGE,"1cb9c079-ea9b-4899-8069-e0e3048e911d.sketch_text.stroke-55"),sQuery(id+"FHMxAyK4CFUKdhS_1.wireOp",EDGE,"1cb9c079-ea9b-4899-8069-e0e3048e911d.sketch_text.stroke-56"),sQuery(id+"FHMxAyK4CFUKdhS_1.wireOp",EDGE,"1cb9c079-ea9b-4899-8069-e0e3048e911d.sketch_text.stroke-57"),sQuery(id+"FHMxAyK4CFUKdhS_1.wireOp",EDGE,"1cb9c079-ea9b-4899-8069-e0e3048e911d.sketch_text.stroke-58"),sQuery(id+"FHMxAyK4CFUKdhS_1.wireOp",EDGE,"1cb9c079-ea9b-4899-8069-e0e3048e911d.sketch_text.stroke-59"),sQuery(id+"FHMxAyK4CFUKdhS_1.wireOp",EDGE,"1cb9c079-ea9b-4899-8069-e0e3048e911d.sketch_text.stroke-60"),sQuery(id+"FHMxAyK4CFUKdhS_1.wireOp",EDGE,"1cb9c079-ea9b-4899-8069-e0e3048e911d.sketch_text.stroke-61"),sQuery(id+"FHMxAyK4CFUKdhS_1.wireOp",EDGE,"1cb9c079-ea9b-4899-8069-e0e3048e911d.sketch_text.stroke-62"),sQuery(id+"FHMxAyK4CFUKdhS_1.wireOp",EDGE,"1cb9c079-ea9b-4899-8069-e0e3048e911d.sketch_text.stroke-71"),sQuery(id+"FHMxAyK4CFUKdhS_1.wireOp",EDGE,"1cb9c079-ea9b-4899-8069-e0e3048e911d.sketch_text.stroke-72"),sQuery(id+"FHMxAyK4CFUKdhS_1.wireOp",EDGE,"1cb9c079-ea9b-4899-8069-e0e3048e911d.sketch_text.stroke-73"),sQuery(id+"FHMxAyK4CFUKdhS_1.wireOp",EDGE,"1cb9c079-ea9b-4899-8069-e0e3048e911d.sketch_text.stroke-74"),sQuery(id+"FHMxAyK4CFUKdhS_1.wireOp",EDGE,"1cb9c079-ea9b-4899-8069-e0e3048e911d.sketch_text.stroke-75"),sQuery(id+"FHMxAyK4CFUKdhS_1.wireOp",EDGE,"1cb9c079-ea9b-4899-8069-e0e3048e911d.sketch_text.stroke-76"),sQuery(id+"FHMxAyK4CFUKdhS_1.wireOp",EDGE,"1cb9c079-ea9b-4899-8069-e0e3048e911d.sketch_text.stroke-77"),sQuery(id+"FHMxAyK4CFUKdhS_1.wireOp",EDGE,"1cb9c079-ea9b-4899-8069-e0e3048e911d.sketch_text.stroke-78"),sQuery(id+"FHMxAyK4CFUKdhS_1.wireOp",EDGE,"1cb9c079-ea9b-4899-8069-e0e3048e911d.sketch_text.stroke-79"),sQuery(id+"FHMxAyK4CFUKdhS_1.wireOp",EDGE,"1cb9c079-ea9b-4899-8069-e0e3048e911d.sketch_text.stroke-80"),sQuery(id+"FHMxAyK4CFUKdhS_1.wireOp",EDGE,"1cb9c079-ea9b-4899-8069-e0e3048e911d.sketch_text.stroke-81"),sQuery(id+"FHMxAyK4CFUKdhS_1.wireOp",EDGE,"1cb9c079-ea9b-4899-8069-e0e3048e911d.sketch_text.stroke-82"),sQuery(id+"FHMxAyK4CFUKdhS_1.wireOp",EDGE,"1cb9c079-ea9b-4899-8069-e0e3048e911d.sketch_text.stroke-83"),sQuery(id+"FHMxAyK4CFUKdhS_1.wireOp",EDGE,"1cb9c079-ea9b-4899-8069-e0e3048e911d.sketch_text.stroke-84"),sQuery(id+"FHMxAyK4CFUKdhS_1.wireOp",EDGE,"1cb9c079-ea9b-4899-8069-e0e3048e911d.sketch_text.stroke-85"),sQuery(id+"FHMxAyK4CFUKdhS_1.wireOp",EDGE,"1cb9c079-ea9b-4899-8069-e0e3048e911d.sketch_text.stroke-86"),sQuery(id+"FHMxAyK4CFUKdhS_1.wireOp",EDGE,"1cb9c079-ea9b-4899-8069-e0e3048e911d.sketch_text.stroke-87"),sQuery(id+"FHMxAyK4CFUKdhS_1.wireOp",EDGE,"1cb9c079-ea9b-4899-8069-e0e3048e911d.sketch_text.stroke-88"),sQuery(id+"FHMxAyK4CFUKdhS_1.wireOp",EDGE,"1cb9c079-ea9b-4899-8069-e0e3048e911d.sketch_text.stroke-89"),sQuery(id+"FHMxAyK4CFUKdhS_1.wireOp",EDGE,"1cb9c079-ea9b-4899-8069-e0e3048e911d.sketch_text.stroke-90"),sQuery(id+"FHMxAyK4CFUKdhS_1.wireOp",EDGE,"1cb9c079-ea9b-4899-8069-e0e3048e911d.sketch_text.stroke-91"),sQuery(id+"FHMxAyK4CFUKdhS_1.wireOp",EDGE,"1cb9c079-ea9b-4899-8069-e0e3048e911d.sketch_text.stroke-92"),sQuery(id+"FHMxAyK4CFUKdhS_1.wireOp",EDGE,"1cb9c079-ea9b-4899-8069-e0e3048e911d.sketch_text.stroke-93"),sQuery(id+"FHMxAyK4CFUKdhS_1.wireOp",EDGE,"1cb9c079-ea9b-4899-8069-e0e3048e911d.sketch_text.stroke-94"),sQuery(id+"FHMxAyK4CFUKdhS_1.wireOp",EDGE,"1cb9c079-ea9b-4899-8069-e0e3048e911d.sketch_text.stroke-95"),sQuery(id+"FHMxAyK4CFUKdhS_1.wireOp",EDGE,"1cb9c079-ea9b-4899-8069-e0e3048e911d.sketch_text.stroke-96"),sQuery(id+"FHMxAyK4CFUKdhS_1.wireOp",EDGE,"1cb9c079-ea9b-4899-8069-e0e3048e911d.sketch_text.stroke-97"),sQuery(id+"FHMxAyK4CFUKdhS_1.wireOp",EDGE,"1cb9c079-ea9b-4899-8069-e0e3048e911d.sketch_text.stroke-103"),sQuery(id+"FHMxAyK4CFUKdhS_1.wireOp",EDGE,"1cb9c079-ea9b-4899-8069-e0e3048e911d.sketch_text.stroke-104"),sQuery(id+"FHMxAyK4CFUKdhS_1.wireOp",EDGE,"1cb9c079-ea9b-4899-8069-e0e3048e911d.sketch_text.stroke-105"),sQuery(id+"FHMxAyK4CFUKdhS_1.wireOp",EDGE,"1cb9c079-ea9b-4899-8069-e0e3048e911d.sketch_text.stroke-106"),sQuery(id+"FHMxAyK4CFUKdhS_1.wireOp",EDGE,"1cb9c079-ea9b-4899-8069-e0e3048e911d.sketch_text.stroke-107"),sQuery(id+"FHMxAyK4CFUKdhS_1.wireOp",EDGE,"1cb9c079-ea9b-4899-8069-e0e3048e911d.sketch_text.stroke-108"),sQuery(id+"FHMxAyK4CFUKdhS_1.wireOp",EDGE,"1cb9c079-ea9b-4899-8069-e0e3048e911d.sketch_text.stroke-109"),sQuery(id+"FHMxAyK4CFUKdhS_1.wireOp",EDGE,"1cb9c079-ea9b-4899-8069-e0e3048e911d.sketch_text.stroke-110"),sQuery(id+"FHMxAyK4CFUKdhS_1.wireOp",EDGE,"1cb9c079-ea9b-4899-8069-e0e3048e911d.sketch_text.stroke-111"),sQuery(id+"FHMxAyK4CFUKdhS_1.wireOp",EDGE,"1cb9c079-ea9b-4899-8069-e0e3048e911d.sketch_text.stroke-112"),sQuery(id+"FHMxAyK4CFUKdhS_1.wireOp",EDGE,"1cb9c079-ea9b-4899-8069-e0e3048e911d.sketch_text.stroke-113"),sQuery(id+"FHMxAyK4CFUKdhS_1.wireOp",EDGE,"1cb9c079-ea9b-4899-8069-e0e3048e911d.sketch_text.stroke-114"),sQuery(id+"FHMxAyK4CFUKdhS_1.wireOp",EDGE,"1cb9c079-ea9b-4899-8069-e0e3048e911d.sketch_text.stroke-115"),sQuery(id+"FHMxAyK4CFUKdhS_1.wireOp",EDGE,"1cb9c079-ea9b-4899-8069-e0e3048e911d.sketch_text.stroke-116"),sQuery(id+"FHMxAyK4CFUKdhS_1.wireOp",EDGE,"1cb9c079-ea9b-4899-8069-e0e3048e911d.sketch_text.stroke-117"),sQuery(id+"FHMxAyK4CFUKdhS_1.wireOp",EDGE,"1cb9c079-ea9b-4899-8069-e0e3048e911d.sketch_text.stroke-118"),sQuery(id+"FHMxAyK4CFUKdhS_1.wireOp",EDGE,"1cb9c079-ea9b-4899-8069-e0e3048e911d.sketch_text.stroke-119"),sQuery(id+"FHMxAyK4CFUKdhS_1.wireOp",EDGE,"1cb9c079-ea9b-4899-8069-e0e3048e911d.sketch_text.stroke-120"),sQuery(id+"FHMxAyK4CFUKdhS_1.wireOp",EDGE,"1cb9c079-ea9b-4899-8069-e0e3048e911d.sketch_text.stroke-121"),sQuery(id+"FHMxAyK4CFUKdhS_1.wireOp",EDGE,"1cb9c079-ea9b-4899-8069-e0e3048e911d.sketch_text.stroke-122"),sQuery(id+"FHMxAyK4CFUKdhS_1.wireOp",EDGE,"1cb9c079-ea9b-4899-8069-e0e3048e911d.sketch_text.stroke-123"),sQuery(id+"FHMxAyK4CFUKdhS_1.wireOp",EDGE,"1cb9c079-ea9b-4899-8069-e0e3048e911d.sketch_text.stroke-124"),sQuery(id+"FHMxAyK4CFUKdhS_1.wireOp",EDGE,"1cb9c079-ea9b-4899-8069-e0e3048e911d.sketch_text.stroke-125"),sQuery(id+"FHMxAyK4CFUKdhS_1.wireOp",EDGE,"1cb9c079-ea9b-4899-8069-e0e3048e911d.sketch_text.stroke-126"),sQuery(id+"FHMxAyK4CFUKdhS_1.wireOp",EDGE,"1cb9c079-ea9b-4899-8069-e0e3048e911d.sketch_text.stroke-127"),sQuery(id+"FHMxAyK4CFUKdhS_1.wireOp",EDGE,"1cb9c079-ea9b-4899-8069-e0e3048e911d.sketch_text.stroke-128"),sQuery(id+"FHMxAyK4CFUKdhS_1.wireOp",EDGE,"1cb9c079-ea9b-4899-8069-e0e3048e911d.sketch_text.stroke-129"),sQuery(id+"FHMxAyK4CFUKdhS_1.wireOp",EDGE,"1cb9c079-ea9b-4899-8069-e0e3048e911d.sketch_text.stroke-130"),sQuery(id+"FHMxAyK4CFUKdhS_1.wireOp",EDGE,"1cb9c079-ea9b-4899-8069-e0e3048e911d.sketch_text.stroke-131"),sQuery(id+"FHMxAyK4CFUKdhS_1.wireOp",EDGE,"1cb9c079-ea9b-4899-8069-e0e3048e911d.sketch_text.stroke-132"),sQuery(id+"FHMxAyK4CFUKdhS_1.wireOp",EDGE,"1cb9c079-ea9b-4899-8069-e0e3048e911d.sketch_text.stroke-133"),sQuery(id+"FHMxAyK4CFUKdhS_1.wireOp",EDGE,"1cb9c079-ea9b-4899-8069-e0e3048e911d.sketch_text.stroke-134"),sQuery(id+"FHMxAyK4CFUKdhS_1.wireOp",EDGE,"1cb9c079-ea9b-4899-8069-e0e3048e911d.sketch_text.stroke-135"),sQuery(id+"FHMxAyK4CFUKdhS_1.wireOp",EDGE,"1cb9c079-ea9b-4899-8069-e0e3048e911d.sketch_text.stroke-136"),sQuery(id+"FHMxAyK4CFUKdhS_1.wireOp",EDGE,"1cb9c079-ea9b-4899-8069-e0e3048e911d.sketch_text.stroke-137"),sQuery(id+"FHMxAyK4CFUKdhS_1.wireOp",EDGE,"1cb9c079-ea9b-4899-8069-e0e3048e911d.sketch_text.stroke-138"),sQuery(id+"FHMxAyK4CFUKdhS_1.wireOp",EDGE,"1cb9c079-ea9b-4899-8069-e0e3048e911d.sketch_text.stroke-139"),sQuery(id+"FHMxAyK4CFUKdhS_1.wireOp",EDGE,"1cb9c079-ea9b-4899-8069-e0e3048e911d.sketch_text.stroke-140"),sQuery(id+"FHMxAyK4CFUKdhS_1.wireOp",EDGE,"1cb9c079-ea9b-4899-8069-e0e3048e911d.sketch_text.stroke-141"),sQuery(id+"FHMxAyK4CFUKdhS_1.wireOp",EDGE,"1cb9c079-ea9b-4899-8069-e0e3048e911d.sketch_text.stroke-142"),sQuery(id+"FHMxAyK4CFUKdhS_1.wireOp",EDGE,"1cb9c079-ea9b-4899-8069-e0e3048e911d.sketch_text.stroke-143"),sQuery(id+"FHMxAyK4CFUKdhS_1.wireOp",EDGE,"1cb9c079-ea9b-4899-8069-e0e3048e911d.sketch_text.stroke-144"),sQuery(id+"FHMxAyK4CFUKdhS_1.wireOp",EDGE,"1cb9c079-ea9b-4899-8069-e0e3048e911d.sketch_text.stroke-145"),sQuery(id+"FHMxAyK4CFUKdhS_1.wireOp",EDGE,"1cb9c079-ea9b-4899-8069-e0e3048e911d.sketch_text.stroke-146"),sQuery(id+"FHMxAyK4CFUKdhS_1.wireOp",EDGE,"1cb9c079-ea9b-4899-8069-e0e3048e911d.sketch_text.stroke-147"),sQuery(id+"FHMxAyK4CFUKdhS_1.wireOp",EDGE,"1cb9c079-ea9b-4899-8069-e0e3048e911d.sketch_text.stroke-148"),sQuery(id+"FHMxAyK4CFUKdhS_1.wireOp",EDGE,"1cb9c079-ea9b-4899-8069-e0e3048e911d.sketch_text.stroke-149"),sQuery(id+"FHMxAyK4CFUKdhS_1.wireOp",EDGE,"1cb9c079-ea9b-4899-8069-e0e3048e911d.sketch_text.stroke-150"),sQuery(id+"FHMxAyK4CFUKdhS_1.wireOp",EDGE,"1cb9c079-ea9b-4899-8069-e0e3048e911d.sketch_text.stroke-151"),sQuery(id+"FHMxAyK4CFUKdhS_1.wireOp",EDGE,"1cb9c079-ea9b-4899-8069-e0e3048e911d.sketch_text.stroke-152"),sQuery(id+"FHMxAyK4CFUKdhS_1.wireOp",EDGE,"1cb9c079-ea9b-4899-8069-e0e3048e911d.sketch_text.stroke-153"),sQuery(id+"FHMxAyK4CFUKdhS_1.wireOp",EDGE,"1cb9c079-ea9b-4899-8069-e0e3048e911d.sketch_text.stroke-159"),sQuery(id+"FHMxAyK4CFUKdhS_1.wireOp",EDGE,"1cb9c079-ea9b-4899-8069-e0e3048e911d.sketch_text.stroke-160"),sQuery(id+"FHMxAyK4CFUKdhS_1.wireOp",EDGE,"1cb9c079-ea9b-4899-8069-e0e3048e911d.sketch_text.stroke-161"),sQuery(id+"FHMxAyK4CFUKdhS_1.wireOp",EDGE,"1cb9c079-ea9b-4899-8069-e0e3048e911d.sketch_text.stroke-162"),sQuery(id+"FHMxAyK4CFUKdhS_1.wireOp",EDGE,"1cb9c079-ea9b-4899-8069-e0e3048e911d.sketch_text.stroke-163"),sQuery(id+"FHMxAyK4CFUKdhS_1.wireOp",EDGE,"1cb9c079-ea9b-4899-8069-e0e3048e911d.sketch_text.stroke-164"),sQuery(id+"FHMxAyK4CFUKdhS_1.wireOp",EDGE,"1cb9c079-ea9b-4899-8069-e0e3048e911d.sketch_text.stroke-165"),sQuery(id+"FHMxAyK4CFUKdhS_1.wireOp",EDGE,"1cb9c079-ea9b-4899-8069-e0e3048e911d.sketch_text.stroke-166"),sQuery(id+"FHMxAyK4CFUKdhS_1.wireOp",EDGE,"1cb9c079-ea9b-4899-8069-e0e3048e911d.sketch_text.stroke-167"),sQuery(id+"FHMxAyK4CFUKdhS_1.wireOp",EDGE,"1cb9c079-ea9b-4899-8069-e0e3048e911d.sketch_text.stroke-168"),sQuery(id+"FHMxAyK4CFUKdhS_1.wireOp",EDGE,"1cb9c079-ea9b-4899-8069-e0e3048e911d.sketch_text.stroke-169"),sQuery(id+"FHMxAyK4CFUKdhS_1.wireOp",EDGE,"1cb9c079-ea9b-4899-8069-e0e3048e911d.sketch_text.stroke-170"),sQuery(id+"FHMxAyK4CFUKdhS_1.wireOp",EDGE,"1cb9c079-ea9b-4899-8069-e0e3048e911d.sketch_text.stroke-171"),sQuery(id+"FHMxAyK4CFUKdhS_1.wireOp",EDGE,"1cb9c079-ea9b-4899-8069-e0e3048e911d.sketch_text.stroke-172"),sQuery(id+"FHMxAyK4CFUKdhS_1.wireOp",EDGE,"1cb9c079-ea9b-4899-8069-e0e3048e911d.sketch_text.stroke-173"),sQuery(id+"FHMxAyK4CFUKdhS_1.wireOp",EDGE,"1cb9c079-ea9b-4899-8069-e0e3048e911d.sketch_text.stroke-174"),sQuery(id+"FHMxAyK4CFUKdhS_1.wireOp",EDGE,"1cb9c079-ea9b-4899-8069-e0e3048e911d.sketch_text.stroke-175"),sQuery(id+"FHMxAyK4CFUKdhS_1.wireOp",EDGE,"1cb9c079-ea9b-4899-8069-e0e3048e911d.sketch_text.stroke-176"),sQuery(id+"FHMxAyK4CFUKdhS_1.wireOp",EDGE,"1cb9c079-ea9b-4899-8069-e0e3048e911d.sketch_text.stroke-177"),sQuery(id+"FHMxAyK4CFUKdhS_1.wireOp",EDGE,"1cb9c079-ea9b-4899-8069-e0e3048e911d.sketch_text.stroke-178"),sQuery(id+"FHMxAyK4CFUKdhS_1.wireOp",EDGE,"1cb9c079-ea9b-4899-8069-e0e3048e911d.sketch_text.stroke-179"),sQuery(id+"FHMxAyK4CFUKdhS_1.wireOp",EDGE,"1cb9c079-ea9b-4899-8069-e0e3048e911d.sketch_text.stroke-180"),sQuery(id+"F3.wireOp",EDGE,"8007402e-1a4e-4a06-85a5-2af08e553504"),subQ2])],"isStart":true}),makeQuery(id+"F4.opExtrude","SWEPT_FACE",FACE,{"disambiguationData":[OSD([subQ2])]})]),OD(0.0)],"derivedFrom":makeQuery(id+"F1.opExtrude","CAP_EDGE",EDGE,{"disambiguationData":[OSD([subQ0])],"isStart":false})});}
            var Q12;
            {var subQ0=sQuery(id+"F0.wireOp",EDGE,"E0.top");var subQ1=sQuery(id+"F0.wireOp",EDGE,"E0.bottom");var subQ2=sQuery(id+"F3.wireOp",EDGE,"6ee83ff3-586e-4dbe-aaea-af71240543bd");Q12=makeQuery(id+"F4.boolean.opBoolean","SPLIT",EDGE,{"disambiguationData":[TD([makeQuery(id+"F1.opExtrude","CAP_FACE",FACE,{"disambiguationData":[OSD([subQ1,subQ0,sQuery(id+"F0.wireOp",EDGE,"E0.left"),sQuery(id+"F0.wireOp",EDGE,"E0.right")])],"isStart":false}),makeQuery(id+"F1.opExtrude","SWEPT_FACE",FACE,{"disambiguationData":[OSD([subQ0])]}),makeQuery(id+"F4.opExtrude","CAP_FACE",FACE,{"disambiguationData":[OSD([subQ1,sQuery(id+"F2.wireOp",EDGE,"fcba4419-a2ee-464f-be9d-58f11bf3418b.sketch_text.stroke-0"),sQuery(id+"F2.wireOp",EDGE,"fcba4419-a2ee-464f-be9d-58f11bf3418b.sketch_text.stroke-1"),sQuery(id+"F2.wireOp",EDGE,"fcba4419-a2ee-464f-be9d-58f11bf3418b.sketch_text.stroke-2"),sQuery(id+"F2.wireOp",EDGE,"fcba4419-a2ee-464f-be9d-58f11bf3418b.sketch_text.stroke-3"),sQuery(id+"F2.wireOp",EDGE,"fcba4419-a2ee-464f-be9d-58f11bf3418b.sketch_text.stroke-4"),sQuery(id+"F2.wireOp",EDGE,"fcba4419-a2ee-464f-be9d-58f11bf3418b.sketch_text.stroke-5"),sQuery(id+"F2.wireOp",EDGE,"fcba4419-a2ee-464f-be9d-58f11bf3418b.sketch_text.stroke-6"),sQuery(id+"F2.wireOp",EDGE,"fcba4419-a2ee-464f-be9d-58f11bf3418b.sketch_text.stroke-7"),sQuery(id+"F2.wireOp",EDGE,"fcba4419-a2ee-464f-be9d-58f11bf3418b.sketch_text.stroke-8"),sQuery(id+"F2.wireOp",EDGE,"fcba4419-a2ee-464f-be9d-58f11bf3418b.sketch_text.stroke-9"),sQuery(id+"F2.wireOp",EDGE,"fcba4419-a2ee-464f-be9d-58f11bf3418b.sketch_text.stroke-10"),sQuery(id+"F2.wireOp",EDGE,"fcba4419-a2ee-464f-be9d-58f11bf3418b.sketch_text.stroke-11"),sQuery(id+"F2.wireOp",EDGE,"fcba4419-a2ee-464f-be9d-58f11bf3418b.sketch_text.stroke-12"),sQuery(id+"F2.wireOp",EDGE,"fcba4419-a2ee-464f-be9d-58f11bf3418b.sketch_text.stroke-13"),sQuery(id+"F2.wireOp",EDGE,"fcba4419-a2ee-464f-be9d-58f11bf3418b.sketch_text.stroke-14"),sQuery(id+"F2.wireOp",EDGE,"fcba4419-a2ee-464f-be9d-58f11bf3418b.sketch_text.stroke-15"),sQuery(id+"F2.wireOp",EDGE,"fcba4419-a2ee-464f-be9d-58f11bf3418b.sketch_text.stroke-16"),sQuery(id+"F2.wireOp",EDGE,"fcba4419-a2ee-464f-be9d-58f11bf3418b.sketch_text.stroke-17"),sQuery(id+"F2.wireOp",EDGE,"fcba4419-a2ee-464f-be9d-58f11bf3418b.sketch_text.stroke-18"),sQuery(id+"F2.wireOp",EDGE,"fcba4419-a2ee-464f-be9d-58f11bf3418b.sketch_text.stroke-19"),sQuery(id+"F2.wireOp",EDGE,"fcba4419-a2ee-464f-be9d-58f11bf3418b.sketch_text.stroke-20"),sQuery(id+"F2.wireOp",EDGE,"fcba4419-a2ee-464f-be9d-58f11bf3418b.sketch_text.stroke-21"),sQuery(id+"F2.wireOp",EDGE,"fcba4419-a2ee-464f-be9d-58f11bf3418b.sketch_text.stroke-22"),sQuery(id+"F2.wireOp",EDGE,"fcba4419-a2ee-464f-be9d-58f11bf3418b.sketch_text.stroke-23"),sQuery(id+"F2.wireOp",EDGE,"fcba4419-a2ee-464f-be9d-58f11bf3418b.sketch_text.stroke-24"),sQuery(id+"F2.wireOp",EDGE,"fcba4419-a2ee-464f-be9d-58f11bf3418b.sketch_text.stroke-25"),sQuery(id+"F2.wireOp",EDGE,"fcba4419-a2ee-464f-be9d-58f11bf3418b.sketch_text.stroke-26"),sQuery(id+"F2.wireOp",EDGE,"fcba4419-a2ee-464f-be9d-58f11bf3418b.sketch_text.stroke-27"),sQuery(id+"F2.wireOp",EDGE,"fcba4419-a2ee-464f-be9d-58f11bf3418b.sketch_text.stroke-28"),sQuery(id+"F2.wireOp",EDGE,"fcba4419-a2ee-464f-be9d-58f11bf3418b.sketch_text.stroke-29"),sQuery(id+"F2.wireOp",EDGE,"fcba4419-a2ee-464f-be9d-58f11bf3418b.sketch_text.stroke-30"),sQuery(id+"F2.wireOp",EDGE,"fcba4419-a2ee-464f-be9d-58f11bf3418b.sketch_text.stroke-31"),sQuery(id+"F2.wireOp",EDGE,"fcba4419-a2ee-464f-be9d-58f11bf3418b.sketch_text.stroke-32"),sQuery(id+"F2.wireOp",EDGE,"fcba4419-a2ee-464f-be9d-58f11bf3418b.sketch_text.stroke-33"),sQuery(id+"F2.wireOp",EDGE,"fcba4419-a2ee-464f-be9d-58f11bf3418b.sketch_text.stroke-34"),sQuery(id+"F2.wireOp",EDGE,"fcba4419-a2ee-464f-be9d-58f11bf3418b.sketch_text.stroke-35"),sQuery(id+"F2.wireOp",EDGE,"fcba4419-a2ee-464f-be9d-58f11bf3418b.sketch_text.stroke-36"),sQuery(id+"F2.wireOp",EDGE,"fcba4419-a2ee-464f-be9d-58f11bf3418b.sketch_text.stroke-37"),sQuery(id+"F2.wireOp",EDGE,"fcba4419-a2ee-464f-be9d-58f11bf3418b.sketch_text.stroke-38"),sQuery(id+"F2.wireOp",EDGE,"fcba4419-a2ee-464f-be9d-58f11bf3418b.sketch_text.stroke-39"),sQuery(id+"F2.wireOp",EDGE,"fcba4419-a2ee-464f-be9d-58f11bf3418b.sketch_text.stroke-40"),sQuery(id+"F2.wireOp",EDGE,"fcba4419-a2ee-464f-be9d-58f11bf3418b.sketch_text.stroke-41"),sQuery(id+"F2.wireOp",EDGE,"fcba4419-a2ee-464f-be9d-58f11bf3418b.sketch_text.stroke-42"),sQuery(id+"F2.wireOp",EDGE,"fcba4419-a2ee-464f-be9d-58f11bf3418b.sketch_text.stroke-43"),sQuery(id+"F2.wireOp",EDGE,"fcba4419-a2ee-464f-be9d-58f11bf3418b.sketch_text.stroke-44"),sQuery(id+"F2.wireOp",EDGE,"fcba4419-a2ee-464f-be9d-58f11bf3418b.sketch_text.stroke-45"),sQuery(id+"F2.wireOp",EDGE,"fcba4419-a2ee-464f-be9d-58f11bf3418b.sketch_text.stroke-46"),sQuery(id+"F2.wireOp",EDGE,"fcba4419-a2ee-464f-be9d-58f11bf3418b.sketch_text.stroke-47"),sQuery(id+"F2.wireOp",EDGE,"fcba4419-a2ee-464f-be9d-58f11bf3418b.sketch_text.stroke-48"),sQuery(id+"F2.wireOp",EDGE,"fcba4419-a2ee-464f-be9d-58f11bf3418b.sketch_text.stroke-49"),sQuery(id+"F2.wireOp",EDGE,"fcba4419-a2ee-464f-be9d-58f11bf3418b.sketch_text.stroke-50"),sQuery(id+"F2.wireOp",EDGE,"fcba4419-a2ee-464f-be9d-58f11bf3418b.sketch_text.stroke-51"),sQuery(id+"F2.wireOp",EDGE,"fcba4419-a2ee-464f-be9d-58f11bf3418b.sketch_text.stroke-52"),sQuery(id+"F2.wireOp",EDGE,"fcba4419-a2ee-464f-be9d-58f11bf3418b.sketch_text.stroke-53"),sQuery(id+"F2.wireOp",EDGE,"fcba4419-a2ee-464f-be9d-58f11bf3418b.sketch_text.stroke-54"),sQuery(id+"F2.wireOp",EDGE,"fcba4419-a2ee-464f-be9d-58f11bf3418b.sketch_text.stroke-55"),sQuery(id+"F2.wireOp",EDGE,"fcba4419-a2ee-464f-be9d-58f11bf3418b.sketch_text.stroke-56"),sQuery(id+"F2.wireOp",EDGE,"fcba4419-a2ee-464f-be9d-58f11bf3418b.sketch_text.stroke-57"),sQuery(id+"F2.wireOp",EDGE,"fcba4419-a2ee-464f-be9d-58f11bf3418b.sketch_text.stroke-58"),sQuery(id+"F2.wireOp",EDGE,"fcba4419-a2ee-464f-be9d-58f11bf3418b.sketch_text.stroke-59"),sQuery(id+"F2.wireOp",EDGE,"fcba4419-a2ee-464f-be9d-58f11bf3418b.sketch_text.stroke-60"),sQuery(id+"F2.wireOp",EDGE,"fcba4419-a2ee-464f-be9d-58f11bf3418b.sketch_text.stroke-61"),sQuery(id+"F2.wireOp",EDGE,"fcba4419-a2ee-464f-be9d-58f11bf3418b.sketch_text.stroke-62"),sQuery(id+"F2.wireOp",EDGE,"fcba4419-a2ee-464f-be9d-58f11bf3418b.sketch_text.stroke-63"),sQuery(id+"F2.wireOp",EDGE,"fcba4419-a2ee-464f-be9d-58f11bf3418b.sketch_text.stroke-64"),sQuery(id+"F2.wireOp",EDGE,"fcba4419-a2ee-464f-be9d-58f11bf3418b.sketch_text.stroke-65"),sQuery(id+"F2.wireOp",EDGE,"fcba4419-a2ee-464f-be9d-58f11bf3418b.sketch_text.stroke-66"),sQuery(id+"F2.wireOp",EDGE,"fcba4419-a2ee-464f-be9d-58f11bf3418b.sketch_text.stroke-67"),sQuery(id+"F2.wireOp",EDGE,"fcba4419-a2ee-464f-be9d-58f11bf3418b.sketch_text.stroke-68"),sQuery(id+"F2.wireOp",EDGE,"fcba4419-a2ee-464f-be9d-58f11bf3418b.sketch_text.stroke-69"),sQuery(id+"F2.wireOp",EDGE,"fcba4419-a2ee-464f-be9d-58f11bf3418b.sketch_text.stroke-70"),sQuery(id+"F2.wireOp",EDGE,"fcba4419-a2ee-464f-be9d-58f11bf3418b.sketch_text.stroke-71"),sQuery(id+"F2.wireOp",EDGE,"fcba4419-a2ee-464f-be9d-58f11bf3418b.sketch_text.stroke-72"),sQuery(id+"F2.wireOp",EDGE,"fcba4419-a2ee-464f-be9d-58f11bf3418b.sketch_text.stroke-73"),sQuery(id+"F2.wireOp",EDGE,"fcba4419-a2ee-464f-be9d-58f11bf3418b.sketch_text.stroke-74"),sQuery(id+"F2.wireOp",EDGE,"fcba4419-a2ee-464f-be9d-58f11bf3418b.sketch_text.stroke-75"),sQuery(id+"F2.wireOp",EDGE,"fcba4419-a2ee-464f-be9d-58f11bf3418b.sketch_text.stroke-76"),sQuery(id+"F2.wireOp",EDGE,"fcba4419-a2ee-464f-be9d-58f11bf3418b.sketch_text.stroke-77"),sQuery(id+"F2.wireOp",EDGE,"fcba4419-a2ee-464f-be9d-58f11bf3418b.sketch_text.stroke-78"),sQuery(id+"F2.wireOp",EDGE,"fcba4419-a2ee-464f-be9d-58f11bf3418b.sketch_text.stroke-79"),sQuery(id+"F2.wireOp",EDGE,"fcba4419-a2ee-464f-be9d-58f11bf3418b.sketch_text.stroke-80"),sQuery(id+"F2.wireOp",EDGE,"fcba4419-a2ee-464f-be9d-58f11bf3418b.sketch_text.stroke-81"),sQuery(id+"F2.wireOp",EDGE,"fcba4419-a2ee-464f-be9d-58f11bf3418b.sketch_text.stroke-82"),sQuery(id+"F2.wireOp",EDGE,"fcba4419-a2ee-464f-be9d-58f11bf3418b.sketch_text.stroke-83"),sQuery(id+"F2.wireOp",EDGE,"fcba4419-a2ee-464f-be9d-58f11bf3418b.sketch_text.stroke-84"),sQuery(id+"F2.wireOp",EDGE,"fcba4419-a2ee-464f-be9d-58f11bf3418b.sketch_text.stroke-85"),sQuery(id+"F2.wireOp",EDGE,"fcba4419-a2ee-464f-be9d-58f11bf3418b.sketch_text.stroke-86"),sQuery(id+"F2.wireOp",EDGE,"fcba4419-a2ee-464f-be9d-58f11bf3418b.sketch_text.stroke-87"),sQuery(id+"F2.wireOp",EDGE,"fcba4419-a2ee-464f-be9d-58f11bf3418b.sketch_text.stroke-88"),sQuery(id+"F2.wireOp",EDGE,"fcba4419-a2ee-464f-be9d-58f11bf3418b.sketch_text.stroke-89"),sQuery(id+"F2.wireOp",EDGE,"fcba4419-a2ee-464f-be9d-58f11bf3418b.sketch_text.stroke-90"),sQuery(id+"F2.wireOp",EDGE,"fcba4419-a2ee-464f-be9d-58f11bf3418b.sketch_text.stroke-91"),sQuery(id+"F2.wireOp",EDGE,"fcba4419-a2ee-464f-be9d-58f11bf3418b.sketch_text.stroke-92"),sQuery(id+"F2.wireOp",EDGE,"fcba4419-a2ee-464f-be9d-58f11bf3418b.sketch_text.stroke-93"),sQuery(id+"F2.wireOp",EDGE,"fcba4419-a2ee-464f-be9d-58f11bf3418b.sketch_text.stroke-94"),sQuery(id+"F2.wireOp",EDGE,"fcba4419-a2ee-464f-be9d-58f11bf3418b.sketch_text.stroke-95"),sQuery(id+"F2.wireOp",EDGE,"fcba4419-a2ee-464f-be9d-58f11bf3418b.sketch_text.stroke-96"),sQuery(id+"F2.wireOp",EDGE,"fcba4419-a2ee-464f-be9d-58f11bf3418b.sketch_text.stroke-97"),sQuery(id+"F2.wireOp",EDGE,"fcba4419-a2ee-464f-be9d-58f11bf3418b.sketch_text.stroke-98"),sQuery(id+"F2.wireOp",EDGE,"fcba4419-a2ee-464f-be9d-58f11bf3418b.sketch_text.stroke-99"),sQuery(id+"F2.wireOp",EDGE,"fcba4419-a2ee-464f-be9d-58f11bf3418b.sketch_text.stroke-100"),sQuery(id+"F2.wireOp",EDGE,"fcba4419-a2ee-464f-be9d-58f11bf3418b.sketch_text.stroke-101"),sQuery(id+"F2.wireOp",EDGE,"fcba4419-a2ee-464f-be9d-58f11bf3418b.sketch_text.stroke-102"),sQuery(id+"F2.wireOp",EDGE,"fcba4419-a2ee-464f-be9d-58f11bf3418b.sketch_text.stroke-103"),sQuery(id+"F2.wireOp",EDGE,"fcba4419-a2ee-464f-be9d-58f11bf3418b.sketch_text.stroke-104"),sQuery(id+"F2.wireOp",EDGE,"fcba4419-a2ee-464f-be9d-58f11bf3418b.sketch_text.stroke-105"),sQuery(id+"F2.wireOp",EDGE,"fcba4419-a2ee-464f-be9d-58f11bf3418b.sketch_text.stroke-106"),sQuery(id+"F2.wireOp",EDGE,"fcba4419-a2ee-464f-be9d-58f11bf3418b.sketch_text.stroke-107"),sQuery(id+"F2.wireOp",EDGE,"fcba4419-a2ee-464f-be9d-58f11bf3418b.sketch_text.stroke-108"),sQuery(id+"F2.wireOp",EDGE,"fcba4419-a2ee-464f-be9d-58f11bf3418b.sketch_text.stroke-109"),sQuery(id+"F2.wireOp",EDGE,"fcba4419-a2ee-464f-be9d-58f11bf3418b.sketch_text.stroke-110"),sQuery(id+"F2.wireOp",EDGE,"fcba4419-a2ee-464f-be9d-58f11bf3418b.sketch_text.stroke-111"),sQuery(id+"F2.wireOp",EDGE,"fcba4419-a2ee-464f-be9d-58f11bf3418b.sketch_text.stroke-112"),sQuery(id+"F2.wireOp",EDGE,"fcba4419-a2ee-464f-be9d-58f11bf3418b.sketch_text.stroke-113"),sQuery(id+"F2.wireOp",EDGE,"fcba4419-a2ee-464f-be9d-58f11bf3418b.sketch_text.stroke-114"),sQuery(id+"F2.wireOp",EDGE,"fcba4419-a2ee-464f-be9d-58f11bf3418b.sketch_text.stroke-115"),sQuery(id+"F2.wireOp",EDGE,"fcba4419-a2ee-464f-be9d-58f11bf3418b.sketch_text.stroke-116"),sQuery(id+"F2.wireOp",EDGE,"fcba4419-a2ee-464f-be9d-58f11bf3418b.sketch_text.stroke-117"),sQuery(id+"F2.wireOp",EDGE,"fcba4419-a2ee-464f-be9d-58f11bf3418b.sketch_text.stroke-118"),sQuery(id+"F2.wireOp",EDGE,"fcba4419-a2ee-464f-be9d-58f11bf3418b.sketch_text.stroke-119"),sQuery(id+"F2.wireOp",EDGE,"fcba4419-a2ee-464f-be9d-58f11bf3418b.sketch_text.stroke-120"),sQuery(id+"F2.wireOp",EDGE,"fcba4419-a2ee-464f-be9d-58f11bf3418b.sketch_text.stroke-121"),sQuery(id+"F2.wireOp",EDGE,"fcba4419-a2ee-464f-be9d-58f11bf3418b.sketch_text.stroke-122"),sQuery(id+"F2.wireOp",EDGE,"fcba4419-a2ee-464f-be9d-58f11bf3418b.sketch_text.stroke-123"),sQuery(id+"F2.wireOp",EDGE,"fcba4419-a2ee-464f-be9d-58f11bf3418b.sketch_text.stroke-124"),sQuery(id+"F2.wireOp",EDGE,"fcba4419-a2ee-464f-be9d-58f11bf3418b.sketch_text.stroke-125"),sQuery(id+"F2.wireOp",EDGE,"fcba4419-a2ee-464f-be9d-58f11bf3418b.sketch_text.stroke-126"),sQuery(id+"F2.wireOp",EDGE,"fcba4419-a2ee-464f-be9d-58f11bf3418b.sketch_text.stroke-127"),sQuery(id+"F2.wireOp",EDGE,"fcba4419-a2ee-464f-be9d-58f11bf3418b.sketch_text.stroke-128"),sQuery(id+"F2.wireOp",EDGE,"fcba4419-a2ee-464f-be9d-58f11bf3418b.sketch_text.stroke-129"),sQuery(id+"F2.wireOp",EDGE,"fcba4419-a2ee-464f-be9d-58f11bf3418b.sketch_text.stroke-130"),sQuery(id+"F2.wireOp",EDGE,"fcba4419-a2ee-464f-be9d-58f11bf3418b.sketch_text.stroke-131"),sQuery(id+"F2.wireOp",EDGE,"fcba4419-a2ee-464f-be9d-58f11bf3418b.sketch_text.stroke-132"),sQuery(id+"F2.wireOp",EDGE,"fcba4419-a2ee-464f-be9d-58f11bf3418b.sketch_text.stroke-133"),sQuery(id+"F2.wireOp",EDGE,"fcba4419-a2ee-464f-be9d-58f11bf3418b.sketch_text.stroke-134"),sQuery(id+"F2.wireOp",EDGE,"fcba4419-a2ee-464f-be9d-58f11bf3418b.sketch_text.stroke-135"),sQuery(id+"F2.wireOp",EDGE,"fcba4419-a2ee-464f-be9d-58f11bf3418b.sketch_text.stroke-136"),sQuery(id+"F2.wireOp",EDGE,"fcba4419-a2ee-464f-be9d-58f11bf3418b.sketch_text.stroke-137"),sQuery(id+"F2.wireOp",EDGE,"fcba4419-a2ee-464f-be9d-58f11bf3418b.sketch_text.stroke-138"),sQuery(id+"F2.wireOp",EDGE,"fcba4419-a2ee-464f-be9d-58f11bf3418b.sketch_text.stroke-139"),sQuery(id+"F2.wireOp",EDGE,"fcba4419-a2ee-464f-be9d-58f11bf3418b.sketch_text.stroke-140"),sQuery(id+"F2.wireOp",EDGE,"fcba4419-a2ee-464f-be9d-58f11bf3418b.sketch_text.stroke-141"),sQuery(id+"F2.wireOp",EDGE,"fcba4419-a2ee-464f-be9d-58f11bf3418b.sketch_text.stroke-142"),sQuery(id+"F2.wireOp",EDGE,"fcba4419-a2ee-464f-be9d-58f11bf3418b.sketch_text.stroke-143"),sQuery(id+"F2.wireOp",EDGE,"fcba4419-a2ee-464f-be9d-58f11bf3418b.sketch_text.stroke-144"),sQuery(id+"F2.wireOp",EDGE,"fcba4419-a2ee-464f-be9d-58f11bf3418b.sketch_text.stroke-145"),sQuery(id+"F2.wireOp",EDGE,"fcba4419-a2ee-464f-be9d-58f11bf3418b.sketch_text.stroke-146"),sQuery(id+"F2.wireOp",EDGE,"fcba4419-a2ee-464f-be9d-58f11bf3418b.sketch_text.stroke-147"),sQuery(id+"F2.wireOp",EDGE,"fcba4419-a2ee-464f-be9d-58f11bf3418b.sketch_text.stroke-148"),sQuery(id+"F2.wireOp",EDGE,"fcba4419-a2ee-464f-be9d-58f11bf3418b.sketch_text.stroke-149"),sQuery(id+"F2.wireOp",EDGE,"fcba4419-a2ee-464f-be9d-58f11bf3418b.sketch_text.stroke-150"),sQuery(id+"F2.wireOp",EDGE,"fcba4419-a2ee-464f-be9d-58f11bf3418b.sketch_text.stroke-151"),sQuery(id+"F2.wireOp",EDGE,"fcba4419-a2ee-464f-be9d-58f11bf3418b.sketch_text.stroke-152"),sQuery(id+"F2.wireOp",EDGE,"fcba4419-a2ee-464f-be9d-58f11bf3418b.sketch_text.stroke-153"),sQuery(id+"F2.wireOp",EDGE,"fcba4419-a2ee-464f-be9d-58f11bf3418b.sketch_text.stroke-154"),sQuery(id+"F2.wireOp",EDGE,"fcba4419-a2ee-464f-be9d-58f11bf3418b.sketch_text.stroke-155"),sQuery(id+"F2.wireOp",EDGE,"fcba4419-a2ee-464f-be9d-58f11bf3418b.sketch_text.stroke-156"),sQuery(id+"F2.wireOp",EDGE,"fcba4419-a2ee-464f-be9d-58f11bf3418b.sketch_text.stroke-157"),sQuery(id+"F2.wireOp",EDGE,"fcba4419-a2ee-464f-be9d-58f11bf3418b.sketch_text.stroke-158"),sQuery(id+"F2.wireOp",EDGE,"fcba4419-a2ee-464f-be9d-58f11bf3418b.sketch_text.stroke-159"),sQuery(id+"F2.wireOp",EDGE,"fcba4419-a2ee-464f-be9d-58f11bf3418b.sketch_text.stroke-160"),sQuery(id+"F2.wireOp",EDGE,"fcba4419-a2ee-464f-be9d-58f11bf3418b.sketch_text.stroke-161"),sQuery(id+"F2.wireOp",EDGE,"fcba4419-a2ee-464f-be9d-58f11bf3418b.sketch_text.stroke-162"),sQuery(id+"F2.wireOp",EDGE,"fcba4419-a2ee-464f-be9d-58f11bf3418b.sketch_text.stroke-163"),sQuery(id+"F2.wireOp",EDGE,"fcba4419-a2ee-464f-be9d-58f11bf3418b.sketch_text.stroke-164"),sQuery(id+"F2.wireOp",EDGE,"fcba4419-a2ee-464f-be9d-58f11bf3418b.sketch_text.stroke-165"),sQuery(id+"F2.wireOp",EDGE,"fcba4419-a2ee-464f-be9d-58f11bf3418b.sketch_text.stroke-166"),sQuery(id+"F2.wireOp",EDGE,"fcba4419-a2ee-464f-be9d-58f11bf3418b.sketch_text.stroke-167"),sQuery(id+"F2.wireOp",EDGE,"fcba4419-a2ee-464f-be9d-58f11bf3418b.sketch_text.stroke-168"),sQuery(id+"F2.wireOp",EDGE,"fcba4419-a2ee-464f-be9d-58f11bf3418b.sketch_text.stroke-169"),sQuery(id+"F2.wireOp",EDGE,"fcba4419-a2ee-464f-be9d-58f11bf3418b.sketch_text.stroke-170"),sQuery(id+"F2.wireOp",EDGE,"fcba4419-a2ee-464f-be9d-58f11bf3418b.sketch_text.stroke-171"),sQuery(id+"F2.wireOp",EDGE,"fcba4419-a2ee-464f-be9d-58f11bf3418b.sketch_text.stroke-172"),sQuery(id+"F2.wireOp",EDGE,"fcba4419-a2ee-464f-be9d-58f11bf3418b.sketch_text.stroke-173"),sQuery(id+"FHMxAyK4CFUKdhS_1.wireOp",EDGE,"1cb9c079-ea9b-4899-8069-e0e3048e911d.sketch_text.stroke-0"),sQuery(id+"FHMxAyK4CFUKdhS_1.wireOp",EDGE,"1cb9c079-ea9b-4899-8069-e0e3048e911d.sketch_text.stroke-1"),sQuery(id+"FHMxAyK4CFUKdhS_1.wireOp",EDGE,"1cb9c079-ea9b-4899-8069-e0e3048e911d.sketch_text.stroke-2"),sQuery(id+"FHMxAyK4CFUKdhS_1.wireOp",EDGE,"1cb9c079-ea9b-4899-8069-e0e3048e911d.sketch_text.stroke-3"),sQuery(id+"FHMxAyK4CFUKdhS_1.wireOp",EDGE,"1cb9c079-ea9b-4899-8069-e0e3048e911d.sketch_text.stroke-4"),sQuery(id+"FHMxAyK4CFUKdhS_1.wireOp",EDGE,"1cb9c079-ea9b-4899-8069-e0e3048e911d.sketch_text.stroke-5"),sQuery(id+"FHMxAyK4CFUKdhS_1.wireOp",EDGE,"1cb9c079-ea9b-4899-8069-e0e3048e911d.sketch_text.stroke-6"),sQuery(id+"FHMxAyK4CFUKdhS_1.wireOp",EDGE,"1cb9c079-ea9b-4899-8069-e0e3048e911d.sketch_text.stroke-7"),sQuery(id+"FHMxAyK4CFUKdhS_1.wireOp",EDGE,"1cb9c079-ea9b-4899-8069-e0e3048e911d.sketch_text.stroke-8"),sQuery(id+"FHMxAyK4CFUKdhS_1.wireOp",EDGE,"1cb9c079-ea9b-4899-8069-e0e3048e911d.sketch_text.stroke-9"),sQuery(id+"FHMxAyK4CFUKdhS_1.wireOp",EDGE,"1cb9c079-ea9b-4899-8069-e0e3048e911d.sketch_text.stroke-10"),sQuery(id+"FHMxAyK4CFUKdhS_1.wireOp",EDGE,"1cb9c079-ea9b-4899-8069-e0e3048e911d.sketch_text.stroke-11"),sQuery(id+"FHMxAyK4CFUKdhS_1.wireOp",EDGE,"1cb9c079-ea9b-4899-8069-e0e3048e911d.sketch_text.stroke-12"),sQuery(id+"FHMxAyK4CFUKdhS_1.wireOp",EDGE,"1cb9c079-ea9b-4899-8069-e0e3048e911d.sketch_text.stroke-13"),sQuery(id+"FHMxAyK4CFUKdhS_1.wireOp",EDGE,"1cb9c079-ea9b-4899-8069-e0e3048e911d.sketch_text.stroke-14"),sQuery(id+"FHMxAyK4CFUKdhS_1.wireOp",EDGE,"1cb9c079-ea9b-4899-8069-e0e3048e911d.sketch_text.stroke-15"),sQuery(id+"FHMxAyK4CFUKdhS_1.wireOp",EDGE,"1cb9c079-ea9b-4899-8069-e0e3048e911d.sketch_text.stroke-16"),sQuery(id+"FHMxAyK4CFUKdhS_1.wireOp",EDGE,"1cb9c079-ea9b-4899-8069-e0e3048e911d.sketch_text.stroke-17"),sQuery(id+"FHMxAyK4CFUKdhS_1.wireOp",EDGE,"1cb9c079-ea9b-4899-8069-e0e3048e911d.sketch_text.stroke-18"),sQuery(id+"FHMxAyK4CFUKdhS_1.wireOp",EDGE,"1cb9c079-ea9b-4899-8069-e0e3048e911d.sketch_text.stroke-19"),sQuery(id+"FHMxAyK4CFUKdhS_1.wireOp",EDGE,"1cb9c079-ea9b-4899-8069-e0e3048e911d.sketch_text.stroke-20"),sQuery(id+"FHMxAyK4CFUKdhS_1.wireOp",EDGE,"1cb9c079-ea9b-4899-8069-e0e3048e911d.sketch_text.stroke-21"),sQuery(id+"FHMxAyK4CFUKdhS_1.wireOp",EDGE,"1cb9c079-ea9b-4899-8069-e0e3048e911d.sketch_text.stroke-22"),sQuery(id+"FHMxAyK4CFUKdhS_1.wireOp",EDGE,"1cb9c079-ea9b-4899-8069-e0e3048e911d.sketch_text.stroke-23"),sQuery(id+"FHMxAyK4CFUKdhS_1.wireOp",EDGE,"1cb9c079-ea9b-4899-8069-e0e3048e911d.sketch_text.stroke-24"),sQuery(id+"FHMxAyK4CFUKdhS_1.wireOp",EDGE,"1cb9c079-ea9b-4899-8069-e0e3048e911d.sketch_text.stroke-25"),sQuery(id+"FHMxAyK4CFUKdhS_1.wireOp",EDGE,"1cb9c079-ea9b-4899-8069-e0e3048e911d.sketch_text.stroke-26"),sQuery(id+"FHMxAyK4CFUKdhS_1.wireOp",EDGE,"1cb9c079-ea9b-4899-8069-e0e3048e911d.sketch_text.stroke-27"),sQuery(id+"FHMxAyK4CFUKdhS_1.wireOp",EDGE,"1cb9c079-ea9b-4899-8069-e0e3048e911d.sketch_text.stroke-28"),sQuery(id+"FHMxAyK4CFUKdhS_1.wireOp",EDGE,"1cb9c079-ea9b-4899-8069-e0e3048e911d.sketch_text.stroke-29"),sQuery(id+"FHMxAyK4CFUKdhS_1.wireOp",EDGE,"1cb9c079-ea9b-4899-8069-e0e3048e911d.sketch_text.stroke-30"),sQuery(id+"FHMxAyK4CFUKdhS_1.wireOp",EDGE,"1cb9c079-ea9b-4899-8069-e0e3048e911d.sketch_text.stroke-31"),sQuery(id+"FHMxAyK4CFUKdhS_1.wireOp",EDGE,"1cb9c079-ea9b-4899-8069-e0e3048e911d.sketch_text.stroke-32"),sQuery(id+"FHMxAyK4CFUKdhS_1.wireOp",EDGE,"1cb9c079-ea9b-4899-8069-e0e3048e911d.sketch_text.stroke-33"),sQuery(id+"FHMxAyK4CFUKdhS_1.wireOp",EDGE,"1cb9c079-ea9b-4899-8069-e0e3048e911d.sketch_text.stroke-34"),sQuery(id+"FHMxAyK4CFUKdhS_1.wireOp",EDGE,"1cb9c079-ea9b-4899-8069-e0e3048e911d.sketch_text.stroke-35"),sQuery(id+"FHMxAyK4CFUKdhS_1.wireOp",EDGE,"1cb9c079-ea9b-4899-8069-e0e3048e911d.sketch_text.stroke-36"),sQuery(id+"FHMxAyK4CFUKdhS_1.wireOp",EDGE,"1cb9c079-ea9b-4899-8069-e0e3048e911d.sketch_text.stroke-37"),sQuery(id+"FHMxAyK4CFUKdhS_1.wireOp",EDGE,"1cb9c079-ea9b-4899-8069-e0e3048e911d.sketch_text.stroke-38"),sQuery(id+"FHMxAyK4CFUKdhS_1.wireOp",EDGE,"1cb9c079-ea9b-4899-8069-e0e3048e911d.sketch_text.stroke-39"),sQuery(id+"FHMxAyK4CFUKdhS_1.wireOp",EDGE,"1cb9c079-ea9b-4899-8069-e0e3048e911d.sketch_text.stroke-40"),sQuery(id+"FHMxAyK4CFUKdhS_1.wireOp",EDGE,"1cb9c079-ea9b-4899-8069-e0e3048e911d.sketch_text.stroke-41"),sQuery(id+"FHMxAyK4CFUKdhS_1.wireOp",EDGE,"1cb9c079-ea9b-4899-8069-e0e3048e911d.sketch_text.stroke-42"),sQuery(id+"FHMxAyK4CFUKdhS_1.wireOp",EDGE,"1cb9c079-ea9b-4899-8069-e0e3048e911d.sketch_text.stroke-43"),sQuery(id+"FHMxAyK4CFUKdhS_1.wireOp",EDGE,"1cb9c079-ea9b-4899-8069-e0e3048e911d.sketch_text.stroke-44"),sQuery(id+"FHMxAyK4CFUKdhS_1.wireOp",EDGE,"1cb9c079-ea9b-4899-8069-e0e3048e911d.sketch_text.stroke-45"),sQuery(id+"FHMxAyK4CFUKdhS_1.wireOp",EDGE,"1cb9c079-ea9b-4899-8069-e0e3048e911d.sketch_text.stroke-46"),sQuery(id+"FHMxAyK4CFUKdhS_1.wireOp",EDGE,"1cb9c079-ea9b-4899-8069-e0e3048e911d.sketch_text.stroke-47"),sQuery(id+"FHMxAyK4CFUKdhS_1.wireOp",EDGE,"1cb9c079-ea9b-4899-8069-e0e3048e911d.sketch_text.stroke-48"),sQuery(id+"FHMxAyK4CFUKdhS_1.wireOp",EDGE,"1cb9c079-ea9b-4899-8069-e0e3048e911d.sketch_text.stroke-49"),sQuery(id+"FHMxAyK4CFUKdhS_1.wireOp",EDGE,"1cb9c079-ea9b-4899-8069-e0e3048e911d.sketch_text.stroke-50"),sQuery(id+"FHMxAyK4CFUKdhS_1.wireOp",EDGE,"1cb9c079-ea9b-4899-8069-e0e3048e911d.sketch_text.stroke-51"),sQuery(id+"FHMxAyK4CFUKdhS_1.wireOp",EDGE,"1cb9c079-ea9b-4899-8069-e0e3048e911d.sketch_text.stroke-52"),sQuery(id+"FHMxAyK4CFUKdhS_1.wireOp",EDGE,"1cb9c079-ea9b-4899-8069-e0e3048e911d.sketch_text.stroke-53"),sQuery(id+"FHMxAyK4CFUKdhS_1.wireOp",EDGE,"1cb9c079-ea9b-4899-8069-e0e3048e911d.sketch_text.stroke-54"),sQuery(id+"FHMxAyK4CFUKdhS_1.wireOp",EDGE,"1cb9c079-ea9b-4899-8069-e0e3048e911d.sketch_text.stroke-55"),sQuery(id+"FHMxAyK4CFUKdhS_1.wireOp",EDGE,"1cb9c079-ea9b-4899-8069-e0e3048e911d.sketch_text.stroke-56"),sQuery(id+"FHMxAyK4CFUKdhS_1.wireOp",EDGE,"1cb9c079-ea9b-4899-8069-e0e3048e911d.sketch_text.stroke-57"),sQuery(id+"FHMxAyK4CFUKdhS_1.wireOp",EDGE,"1cb9c079-ea9b-4899-8069-e0e3048e911d.sketch_text.stroke-58"),sQuery(id+"FHMxAyK4CFUKdhS_1.wireOp",EDGE,"1cb9c079-ea9b-4899-8069-e0e3048e911d.sketch_text.stroke-59"),sQuery(id+"FHMxAyK4CFUKdhS_1.wireOp",EDGE,"1cb9c079-ea9b-4899-8069-e0e3048e911d.sketch_text.stroke-60"),sQuery(id+"FHMxAyK4CFUKdhS_1.wireOp",EDGE,"1cb9c079-ea9b-4899-8069-e0e3048e911d.sketch_text.stroke-61"),sQuery(id+"FHMxAyK4CFUKdhS_1.wireOp",EDGE,"1cb9c079-ea9b-4899-8069-e0e3048e911d.sketch_text.stroke-62"),sQuery(id+"FHMxAyK4CFUKdhS_1.wireOp",EDGE,"1cb9c079-ea9b-4899-8069-e0e3048e911d.sketch_text.stroke-71"),sQuery(id+"FHMxAyK4CFUKdhS_1.wireOp",EDGE,"1cb9c079-ea9b-4899-8069-e0e3048e911d.sketch_text.stroke-72"),sQuery(id+"FHMxAyK4CFUKdhS_1.wireOp",EDGE,"1cb9c079-ea9b-4899-8069-e0e3048e911d.sketch_text.stroke-73"),sQuery(id+"FHMxAyK4CFUKdhS_1.wireOp",EDGE,"1cb9c079-ea9b-4899-8069-e0e3048e911d.sketch_text.stroke-74"),sQuery(id+"FHMxAyK4CFUKdhS_1.wireOp",EDGE,"1cb9c079-ea9b-4899-8069-e0e3048e911d.sketch_text.stroke-75"),sQuery(id+"FHMxAyK4CFUKdhS_1.wireOp",EDGE,"1cb9c079-ea9b-4899-8069-e0e3048e911d.sketch_text.stroke-76"),sQuery(id+"FHMxAyK4CFUKdhS_1.wireOp",EDGE,"1cb9c079-ea9b-4899-8069-e0e3048e911d.sketch_text.stroke-77"),sQuery(id+"FHMxAyK4CFUKdhS_1.wireOp",EDGE,"1cb9c079-ea9b-4899-8069-e0e3048e911d.sketch_text.stroke-78"),sQuery(id+"FHMxAyK4CFUKdhS_1.wireOp",EDGE,"1cb9c079-ea9b-4899-8069-e0e3048e911d.sketch_text.stroke-79"),sQuery(id+"FHMxAyK4CFUKdhS_1.wireOp",EDGE,"1cb9c079-ea9b-4899-8069-e0e3048e911d.sketch_text.stroke-80"),sQuery(id+"FHMxAyK4CFUKdhS_1.wireOp",EDGE,"1cb9c079-ea9b-4899-8069-e0e3048e911d.sketch_text.stroke-81"),sQuery(id+"FHMxAyK4CFUKdhS_1.wireOp",EDGE,"1cb9c079-ea9b-4899-8069-e0e3048e911d.sketch_text.stroke-82"),sQuery(id+"FHMxAyK4CFUKdhS_1.wireOp",EDGE,"1cb9c079-ea9b-4899-8069-e0e3048e911d.sketch_text.stroke-83"),sQuery(id+"FHMxAyK4CFUKdhS_1.wireOp",EDGE,"1cb9c079-ea9b-4899-8069-e0e3048e911d.sketch_text.stroke-84"),sQuery(id+"FHMxAyK4CFUKdhS_1.wireOp",EDGE,"1cb9c079-ea9b-4899-8069-e0e3048e911d.sketch_text.stroke-85"),sQuery(id+"FHMxAyK4CFUKdhS_1.wireOp",EDGE,"1cb9c079-ea9b-4899-8069-e0e3048e911d.sketch_text.stroke-86"),sQuery(id+"FHMxAyK4CFUKdhS_1.wireOp",EDGE,"1cb9c079-ea9b-4899-8069-e0e3048e911d.sketch_text.stroke-87"),sQuery(id+"FHMxAyK4CFUKdhS_1.wireOp",EDGE,"1cb9c079-ea9b-4899-8069-e0e3048e911d.sketch_text.stroke-88"),sQuery(id+"FHMxAyK4CFUKdhS_1.wireOp",EDGE,"1cb9c079-ea9b-4899-8069-e0e3048e911d.sketch_text.stroke-89"),sQuery(id+"FHMxAyK4CFUKdhS_1.wireOp",EDGE,"1cb9c079-ea9b-4899-8069-e0e3048e911d.sketch_text.stroke-90"),sQuery(id+"FHMxAyK4CFUKdhS_1.wireOp",EDGE,"1cb9c079-ea9b-4899-8069-e0e3048e911d.sketch_text.stroke-91"),sQuery(id+"FHMxAyK4CFUKdhS_1.wireOp",EDGE,"1cb9c079-ea9b-4899-8069-e0e3048e911d.sketch_text.stroke-92"),sQuery(id+"FHMxAyK4CFUKdhS_1.wireOp",EDGE,"1cb9c079-ea9b-4899-8069-e0e3048e911d.sketch_text.stroke-93"),sQuery(id+"FHMxAyK4CFUKdhS_1.wireOp",EDGE,"1cb9c079-ea9b-4899-8069-e0e3048e911d.sketch_text.stroke-94"),sQuery(id+"FHMxAyK4CFUKdhS_1.wireOp",EDGE,"1cb9c079-ea9b-4899-8069-e0e3048e911d.sketch_text.stroke-95"),sQuery(id+"FHMxAyK4CFUKdhS_1.wireOp",EDGE,"1cb9c079-ea9b-4899-8069-e0e3048e911d.sketch_text.stroke-96"),sQuery(id+"FHMxAyK4CFUKdhS_1.wireOp",EDGE,"1cb9c079-ea9b-4899-8069-e0e3048e911d.sketch_text.stroke-97"),sQuery(id+"FHMxAyK4CFUKdhS_1.wireOp",EDGE,"1cb9c079-ea9b-4899-8069-e0e3048e911d.sketch_text.stroke-103"),sQuery(id+"FHMxAyK4CFUKdhS_1.wireOp",EDGE,"1cb9c079-ea9b-4899-8069-e0e3048e911d.sketch_text.stroke-104"),sQuery(id+"FHMxAyK4CFUKdhS_1.wireOp",EDGE,"1cb9c079-ea9b-4899-8069-e0e3048e911d.sketch_text.stroke-105"),sQuery(id+"FHMxAyK4CFUKdhS_1.wireOp",EDGE,"1cb9c079-ea9b-4899-8069-e0e3048e911d.sketch_text.stroke-106"),sQuery(id+"FHMxAyK4CFUKdhS_1.wireOp",EDGE,"1cb9c079-ea9b-4899-8069-e0e3048e911d.sketch_text.stroke-107"),sQuery(id+"FHMxAyK4CFUKdhS_1.wireOp",EDGE,"1cb9c079-ea9b-4899-8069-e0e3048e911d.sketch_text.stroke-108"),sQuery(id+"FHMxAyK4CFUKdhS_1.wireOp",EDGE,"1cb9c079-ea9b-4899-8069-e0e3048e911d.sketch_text.stroke-109"),sQuery(id+"FHMxAyK4CFUKdhS_1.wireOp",EDGE,"1cb9c079-ea9b-4899-8069-e0e3048e911d.sketch_text.stroke-110"),sQuery(id+"FHMxAyK4CFUKdhS_1.wireOp",EDGE,"1cb9c079-ea9b-4899-8069-e0e3048e911d.sketch_text.stroke-111"),sQuery(id+"FHMxAyK4CFUKdhS_1.wireOp",EDGE,"1cb9c079-ea9b-4899-8069-e0e3048e911d.sketch_text.stroke-112"),sQuery(id+"FHMxAyK4CFUKdhS_1.wireOp",EDGE,"1cb9c079-ea9b-4899-8069-e0e3048e911d.sketch_text.stroke-113"),sQuery(id+"FHMxAyK4CFUKdhS_1.wireOp",EDGE,"1cb9c079-ea9b-4899-8069-e0e3048e911d.sketch_text.stroke-114"),sQuery(id+"FHMxAyK4CFUKdhS_1.wireOp",EDGE,"1cb9c079-ea9b-4899-8069-e0e3048e911d.sketch_text.stroke-115"),sQuery(id+"FHMxAyK4CFUKdhS_1.wireOp",EDGE,"1cb9c079-ea9b-4899-8069-e0e3048e911d.sketch_text.stroke-116"),sQuery(id+"FHMxAyK4CFUKdhS_1.wireOp",EDGE,"1cb9c079-ea9b-4899-8069-e0e3048e911d.sketch_text.stroke-117"),sQuery(id+"FHMxAyK4CFUKdhS_1.wireOp",EDGE,"1cb9c079-ea9b-4899-8069-e0e3048e911d.sketch_text.stroke-118"),sQuery(id+"FHMxAyK4CFUKdhS_1.wireOp",EDGE,"1cb9c079-ea9b-4899-8069-e0e3048e911d.sketch_text.stroke-119"),sQuery(id+"FHMxAyK4CFUKdhS_1.wireOp",EDGE,"1cb9c079-ea9b-4899-8069-e0e3048e911d.sketch_text.stroke-120"),sQuery(id+"FHMxAyK4CFUKdhS_1.wireOp",EDGE,"1cb9c079-ea9b-4899-8069-e0e3048e911d.sketch_text.stroke-121"),sQuery(id+"FHMxAyK4CFUKdhS_1.wireOp",EDGE,"1cb9c079-ea9b-4899-8069-e0e3048e911d.sketch_text.stroke-122"),sQuery(id+"FHMxAyK4CFUKdhS_1.wireOp",EDGE,"1cb9c079-ea9b-4899-8069-e0e3048e911d.sketch_text.stroke-123"),sQuery(id+"FHMxAyK4CFUKdhS_1.wireOp",EDGE,"1cb9c079-ea9b-4899-8069-e0e3048e911d.sketch_text.stroke-124"),sQuery(id+"FHMxAyK4CFUKdhS_1.wireOp",EDGE,"1cb9c079-ea9b-4899-8069-e0e3048e911d.sketch_text.stroke-125"),sQuery(id+"FHMxAyK4CFUKdhS_1.wireOp",EDGE,"1cb9c079-ea9b-4899-8069-e0e3048e911d.sketch_text.stroke-126"),sQuery(id+"FHMxAyK4CFUKdhS_1.wireOp",EDGE,"1cb9c079-ea9b-4899-8069-e0e3048e911d.sketch_text.stroke-127"),sQuery(id+"FHMxAyK4CFUKdhS_1.wireOp",EDGE,"1cb9c079-ea9b-4899-8069-e0e3048e911d.sketch_text.stroke-128"),sQuery(id+"FHMxAyK4CFUKdhS_1.wireOp",EDGE,"1cb9c079-ea9b-4899-8069-e0e3048e911d.sketch_text.stroke-129"),sQuery(id+"FHMxAyK4CFUKdhS_1.wireOp",EDGE,"1cb9c079-ea9b-4899-8069-e0e3048e911d.sketch_text.stroke-130"),sQuery(id+"FHMxAyK4CFUKdhS_1.wireOp",EDGE,"1cb9c079-ea9b-4899-8069-e0e3048e911d.sketch_text.stroke-131"),sQuery(id+"FHMxAyK4CFUKdhS_1.wireOp",EDGE,"1cb9c079-ea9b-4899-8069-e0e3048e911d.sketch_text.stroke-132"),sQuery(id+"FHMxAyK4CFUKdhS_1.wireOp",EDGE,"1cb9c079-ea9b-4899-8069-e0e3048e911d.sketch_text.stroke-133"),sQuery(id+"FHMxAyK4CFUKdhS_1.wireOp",EDGE,"1cb9c079-ea9b-4899-8069-e0e3048e911d.sketch_text.stroke-134"),sQuery(id+"FHMxAyK4CFUKdhS_1.wireOp",EDGE,"1cb9c079-ea9b-4899-8069-e0e3048e911d.sketch_text.stroke-135"),sQuery(id+"FHMxAyK4CFUKdhS_1.wireOp",EDGE,"1cb9c079-ea9b-4899-8069-e0e3048e911d.sketch_text.stroke-136"),sQuery(id+"FHMxAyK4CFUKdhS_1.wireOp",EDGE,"1cb9c079-ea9b-4899-8069-e0e3048e911d.sketch_text.stroke-137"),sQuery(id+"FHMxAyK4CFUKdhS_1.wireOp",EDGE,"1cb9c079-ea9b-4899-8069-e0e3048e911d.sketch_text.stroke-138"),sQuery(id+"FHMxAyK4CFUKdhS_1.wireOp",EDGE,"1cb9c079-ea9b-4899-8069-e0e3048e911d.sketch_text.stroke-139"),sQuery(id+"FHMxAyK4CFUKdhS_1.wireOp",EDGE,"1cb9c079-ea9b-4899-8069-e0e3048e911d.sketch_text.stroke-140"),sQuery(id+"FHMxAyK4CFUKdhS_1.wireOp",EDGE,"1cb9c079-ea9b-4899-8069-e0e3048e911d.sketch_text.stroke-141"),sQuery(id+"FHMxAyK4CFUKdhS_1.wireOp",EDGE,"1cb9c079-ea9b-4899-8069-e0e3048e911d.sketch_text.stroke-142"),sQuery(id+"FHMxAyK4CFUKdhS_1.wireOp",EDGE,"1cb9c079-ea9b-4899-8069-e0e3048e911d.sketch_text.stroke-143"),sQuery(id+"FHMxAyK4CFUKdhS_1.wireOp",EDGE,"1cb9c079-ea9b-4899-8069-e0e3048e911d.sketch_text.stroke-144"),sQuery(id+"FHMxAyK4CFUKdhS_1.wireOp",EDGE,"1cb9c079-ea9b-4899-8069-e0e3048e911d.sketch_text.stroke-145"),sQuery(id+"FHMxAyK4CFUKdhS_1.wireOp",EDGE,"1cb9c079-ea9b-4899-8069-e0e3048e911d.sketch_text.stroke-146"),sQuery(id+"FHMxAyK4CFUKdhS_1.wireOp",EDGE,"1cb9c079-ea9b-4899-8069-e0e3048e911d.sketch_text.stroke-147"),sQuery(id+"FHMxAyK4CFUKdhS_1.wireOp",EDGE,"1cb9c079-ea9b-4899-8069-e0e3048e911d.sketch_text.stroke-148"),sQuery(id+"FHMxAyK4CFUKdhS_1.wireOp",EDGE,"1cb9c079-ea9b-4899-8069-e0e3048e911d.sketch_text.stroke-149"),sQuery(id+"FHMxAyK4CFUKdhS_1.wireOp",EDGE,"1cb9c079-ea9b-4899-8069-e0e3048e911d.sketch_text.stroke-150"),sQuery(id+"FHMxAyK4CFUKdhS_1.wireOp",EDGE,"1cb9c079-ea9b-4899-8069-e0e3048e911d.sketch_text.stroke-151"),sQuery(id+"FHMxAyK4CFUKdhS_1.wireOp",EDGE,"1cb9c079-ea9b-4899-8069-e0e3048e911d.sketch_text.stroke-152"),sQuery(id+"FHMxAyK4CFUKdhS_1.wireOp",EDGE,"1cb9c079-ea9b-4899-8069-e0e3048e911d.sketch_text.stroke-153"),sQuery(id+"FHMxAyK4CFUKdhS_1.wireOp",EDGE,"1cb9c079-ea9b-4899-8069-e0e3048e911d.sketch_text.stroke-159"),sQuery(id+"FHMxAyK4CFUKdhS_1.wireOp",EDGE,"1cb9c079-ea9b-4899-8069-e0e3048e911d.sketch_text.stroke-160"),sQuery(id+"FHMxAyK4CFUKdhS_1.wireOp",EDGE,"1cb9c079-ea9b-4899-8069-e0e3048e911d.sketch_text.stroke-161"),sQuery(id+"FHMxAyK4CFUKdhS_1.wireOp",EDGE,"1cb9c079-ea9b-4899-8069-e0e3048e911d.sketch_text.stroke-162"),sQuery(id+"FHMxAyK4CFUKdhS_1.wireOp",EDGE,"1cb9c079-ea9b-4899-8069-e0e3048e911d.sketch_text.stroke-163"),sQuery(id+"FHMxAyK4CFUKdhS_1.wireOp",EDGE,"1cb9c079-ea9b-4899-8069-e0e3048e911d.sketch_text.stroke-164"),sQuery(id+"FHMxAyK4CFUKdhS_1.wireOp",EDGE,"1cb9c079-ea9b-4899-8069-e0e3048e911d.sketch_text.stroke-165"),sQuery(id+"FHMxAyK4CFUKdhS_1.wireOp",EDGE,"1cb9c079-ea9b-4899-8069-e0e3048e911d.sketch_text.stroke-166"),sQuery(id+"FHMxAyK4CFUKdhS_1.wireOp",EDGE,"1cb9c079-ea9b-4899-8069-e0e3048e911d.sketch_text.stroke-167"),sQuery(id+"FHMxAyK4CFUKdhS_1.wireOp",EDGE,"1cb9c079-ea9b-4899-8069-e0e3048e911d.sketch_text.stroke-168"),sQuery(id+"FHMxAyK4CFUKdhS_1.wireOp",EDGE,"1cb9c079-ea9b-4899-8069-e0e3048e911d.sketch_text.stroke-169"),sQuery(id+"FHMxAyK4CFUKdhS_1.wireOp",EDGE,"1cb9c079-ea9b-4899-8069-e0e3048e911d.sketch_text.stroke-170"),sQuery(id+"FHMxAyK4CFUKdhS_1.wireOp",EDGE,"1cb9c079-ea9b-4899-8069-e0e3048e911d.sketch_text.stroke-171"),sQuery(id+"FHMxAyK4CFUKdhS_1.wireOp",EDGE,"1cb9c079-ea9b-4899-8069-e0e3048e911d.sketch_text.stroke-172"),sQuery(id+"FHMxAyK4CFUKdhS_1.wireOp",EDGE,"1cb9c079-ea9b-4899-8069-e0e3048e911d.sketch_text.stroke-173"),sQuery(id+"FHMxAyK4CFUKdhS_1.wireOp",EDGE,"1cb9c079-ea9b-4899-8069-e0e3048e911d.sketch_text.stroke-174"),sQuery(id+"FHMxAyK4CFUKdhS_1.wireOp",EDGE,"1cb9c079-ea9b-4899-8069-e0e3048e911d.sketch_text.stroke-175"),sQuery(id+"FHMxAyK4CFUKdhS_1.wireOp",EDGE,"1cb9c079-ea9b-4899-8069-e0e3048e911d.sketch_text.stroke-176"),sQuery(id+"FHMxAyK4CFUKdhS_1.wireOp",EDGE,"1cb9c079-ea9b-4899-8069-e0e3048e911d.sketch_text.stroke-177"),sQuery(id+"FHMxAyK4CFUKdhS_1.wireOp",EDGE,"1cb9c079-ea9b-4899-8069-e0e3048e911d.sketch_text.stroke-178"),sQuery(id+"FHMxAyK4CFUKdhS_1.wireOp",EDGE,"1cb9c079-ea9b-4899-8069-e0e3048e911d.sketch_text.stroke-179"),sQuery(id+"FHMxAyK4CFUKdhS_1.wireOp",EDGE,"1cb9c079-ea9b-4899-8069-e0e3048e911d.sketch_text.stroke-180"),sQuery(id+"F3.wireOp",EDGE,"8007402e-1a4e-4a06-85a5-2af08e553504"),subQ2])],"isStart":true}),makeQuery(id+"F4.opExtrude","SWEPT_FACE",FACE,{"disambiguationData":[OSD([subQ2])]})]),OD(1.0)],"derivedFrom":makeQuery(id+"F1.opExtrude","CAP_EDGE",EDGE,{"disambiguationData":[OSD([subQ0])],"isStart":false})});}
            var Q13;
            {var subQ0=sQuery(id+"F0.wireOp",EDGE,"E0.top");var subQ1=sQuery(id+"F0.wireOp",EDGE,"E0.bottom");var subQ2=sQuery(id+"F3.wireOp",EDGE,"727ac2c1-f511-4829-95a7-a443ef16a4cd");Q13=makeQuery(id+"F4.boolean.opBoolean","SPLIT",EDGE,{"disambiguationData":[TD([makeQuery(id+"F1.opExtrude","CAP_FACE",FACE,{"disambiguationData":[OSD([subQ1,subQ0,sQuery(id+"F0.wireOp",EDGE,"E0.left"),sQuery(id+"F0.wireOp",EDGE,"E0.right")])],"isStart":false}),makeQuery(id+"F1.opExtrude","SWEPT_FACE",FACE,{"disambiguationData":[OSD([subQ0])]}),makeQuery(id+"F4.opExtrude","CAP_FACE",FACE,{"disambiguationData":[OSD([subQ1,sQuery(id+"F2.wireOp",EDGE,"fcba4419-a2ee-464f-be9d-58f11bf3418b.sketch_text.stroke-0"),sQuery(id+"F2.wireOp",EDGE,"fcba4419-a2ee-464f-be9d-58f11bf3418b.sketch_text.stroke-1"),sQuery(id+"F2.wireOp",EDGE,"fcba4419-a2ee-464f-be9d-58f11bf3418b.sketch_text.stroke-2"),sQuery(id+"F2.wireOp",EDGE,"fcba4419-a2ee-464f-be9d-58f11bf3418b.sketch_text.stroke-3"),sQuery(id+"F2.wireOp",EDGE,"fcba4419-a2ee-464f-be9d-58f11bf3418b.sketch_text.stroke-4"),sQuery(id+"F2.wireOp",EDGE,"fcba4419-a2ee-464f-be9d-58f11bf3418b.sketch_text.stroke-5"),sQuery(id+"F2.wireOp",EDGE,"fcba4419-a2ee-464f-be9d-58f11bf3418b.sketch_text.stroke-6"),sQuery(id+"F2.wireOp",EDGE,"fcba4419-a2ee-464f-be9d-58f11bf3418b.sketch_text.stroke-7"),sQuery(id+"F2.wireOp",EDGE,"fcba4419-a2ee-464f-be9d-58f11bf3418b.sketch_text.stroke-8"),sQuery(id+"F2.wireOp",EDGE,"fcba4419-a2ee-464f-be9d-58f11bf3418b.sketch_text.stroke-9"),sQuery(id+"F2.wireOp",EDGE,"fcba4419-a2ee-464f-be9d-58f11bf3418b.sketch_text.stroke-10"),sQuery(id+"F2.wireOp",EDGE,"fcba4419-a2ee-464f-be9d-58f11bf3418b.sketch_text.stroke-11"),sQuery(id+"F2.wireOp",EDGE,"fcba4419-a2ee-464f-be9d-58f11bf3418b.sketch_text.stroke-12"),sQuery(id+"F2.wireOp",EDGE,"fcba4419-a2ee-464f-be9d-58f11bf3418b.sketch_text.stroke-13"),sQuery(id+"F2.wireOp",EDGE,"fcba4419-a2ee-464f-be9d-58f11bf3418b.sketch_text.stroke-14"),sQuery(id+"F2.wireOp",EDGE,"fcba4419-a2ee-464f-be9d-58f11bf3418b.sketch_text.stroke-15"),sQuery(id+"F2.wireOp",EDGE,"fcba4419-a2ee-464f-be9d-58f11bf3418b.sketch_text.stroke-16"),sQuery(id+"F2.wireOp",EDGE,"fcba4419-a2ee-464f-be9d-58f11bf3418b.sketch_text.stroke-17"),sQuery(id+"F2.wireOp",EDGE,"fcba4419-a2ee-464f-be9d-58f11bf3418b.sketch_text.stroke-18"),sQuery(id+"F2.wireOp",EDGE,"fcba4419-a2ee-464f-be9d-58f11bf3418b.sketch_text.stroke-19"),sQuery(id+"F2.wireOp",EDGE,"fcba4419-a2ee-464f-be9d-58f11bf3418b.sketch_text.stroke-20"),sQuery(id+"F2.wireOp",EDGE,"fcba4419-a2ee-464f-be9d-58f11bf3418b.sketch_text.stroke-21"),sQuery(id+"F2.wireOp",EDGE,"fcba4419-a2ee-464f-be9d-58f11bf3418b.sketch_text.stroke-22"),sQuery(id+"F2.wireOp",EDGE,"fcba4419-a2ee-464f-be9d-58f11bf3418b.sketch_text.stroke-23"),sQuery(id+"F2.wireOp",EDGE,"fcba4419-a2ee-464f-be9d-58f11bf3418b.sketch_text.stroke-24"),sQuery(id+"F2.wireOp",EDGE,"fcba4419-a2ee-464f-be9d-58f11bf3418b.sketch_text.stroke-25"),sQuery(id+"F2.wireOp",EDGE,"fcba4419-a2ee-464f-be9d-58f11bf3418b.sketch_text.stroke-26"),sQuery(id+"F2.wireOp",EDGE,"fcba4419-a2ee-464f-be9d-58f11bf3418b.sketch_text.stroke-27"),sQuery(id+"F2.wireOp",EDGE,"fcba4419-a2ee-464f-be9d-58f11bf3418b.sketch_text.stroke-28"),sQuery(id+"F2.wireOp",EDGE,"fcba4419-a2ee-464f-be9d-58f11bf3418b.sketch_text.stroke-29"),sQuery(id+"F2.wireOp",EDGE,"fcba4419-a2ee-464f-be9d-58f11bf3418b.sketch_text.stroke-30"),sQuery(id+"F2.wireOp",EDGE,"fcba4419-a2ee-464f-be9d-58f11bf3418b.sketch_text.stroke-31"),sQuery(id+"F2.wireOp",EDGE,"fcba4419-a2ee-464f-be9d-58f11bf3418b.sketch_text.stroke-32"),sQuery(id+"F2.wireOp",EDGE,"fcba4419-a2ee-464f-be9d-58f11bf3418b.sketch_text.stroke-33"),sQuery(id+"F2.wireOp",EDGE,"fcba4419-a2ee-464f-be9d-58f11bf3418b.sketch_text.stroke-34"),sQuery(id+"F2.wireOp",EDGE,"fcba4419-a2ee-464f-be9d-58f11bf3418b.sketch_text.stroke-35"),sQuery(id+"F2.wireOp",EDGE,"fcba4419-a2ee-464f-be9d-58f11bf3418b.sketch_text.stroke-36"),sQuery(id+"F2.wireOp",EDGE,"fcba4419-a2ee-464f-be9d-58f11bf3418b.sketch_text.stroke-37"),sQuery(id+"F2.wireOp",EDGE,"fcba4419-a2ee-464f-be9d-58f11bf3418b.sketch_text.stroke-38"),sQuery(id+"F2.wireOp",EDGE,"fcba4419-a2ee-464f-be9d-58f11bf3418b.sketch_text.stroke-39"),sQuery(id+"F2.wireOp",EDGE,"fcba4419-a2ee-464f-be9d-58f11bf3418b.sketch_text.stroke-40"),sQuery(id+"F2.wireOp",EDGE,"fcba4419-a2ee-464f-be9d-58f11bf3418b.sketch_text.stroke-41"),sQuery(id+"F2.wireOp",EDGE,"fcba4419-a2ee-464f-be9d-58f11bf3418b.sketch_text.stroke-42"),sQuery(id+"F2.wireOp",EDGE,"fcba4419-a2ee-464f-be9d-58f11bf3418b.sketch_text.stroke-43"),sQuery(id+"F2.wireOp",EDGE,"fcba4419-a2ee-464f-be9d-58f11bf3418b.sketch_text.stroke-44"),sQuery(id+"F2.wireOp",EDGE,"fcba4419-a2ee-464f-be9d-58f11bf3418b.sketch_text.stroke-45"),sQuery(id+"F2.wireOp",EDGE,"fcba4419-a2ee-464f-be9d-58f11bf3418b.sketch_text.stroke-46"),sQuery(id+"F2.wireOp",EDGE,"fcba4419-a2ee-464f-be9d-58f11bf3418b.sketch_text.stroke-47"),sQuery(id+"F2.wireOp",EDGE,"fcba4419-a2ee-464f-be9d-58f11bf3418b.sketch_text.stroke-48"),sQuery(id+"F2.wireOp",EDGE,"fcba4419-a2ee-464f-be9d-58f11bf3418b.sketch_text.stroke-49"),sQuery(id+"F2.wireOp",EDGE,"fcba4419-a2ee-464f-be9d-58f11bf3418b.sketch_text.stroke-50"),sQuery(id+"F2.wireOp",EDGE,"fcba4419-a2ee-464f-be9d-58f11bf3418b.sketch_text.stroke-51"),sQuery(id+"F2.wireOp",EDGE,"fcba4419-a2ee-464f-be9d-58f11bf3418b.sketch_text.stroke-52"),sQuery(id+"F2.wireOp",EDGE,"fcba4419-a2ee-464f-be9d-58f11bf3418b.sketch_text.stroke-53"),sQuery(id+"F2.wireOp",EDGE,"fcba4419-a2ee-464f-be9d-58f11bf3418b.sketch_text.stroke-54"),sQuery(id+"F2.wireOp",EDGE,"fcba4419-a2ee-464f-be9d-58f11bf3418b.sketch_text.stroke-55"),sQuery(id+"F2.wireOp",EDGE,"fcba4419-a2ee-464f-be9d-58f11bf3418b.sketch_text.stroke-56"),sQuery(id+"F2.wireOp",EDGE,"fcba4419-a2ee-464f-be9d-58f11bf3418b.sketch_text.stroke-57"),sQuery(id+"F2.wireOp",EDGE,"fcba4419-a2ee-464f-be9d-58f11bf3418b.sketch_text.stroke-58"),sQuery(id+"F2.wireOp",EDGE,"fcba4419-a2ee-464f-be9d-58f11bf3418b.sketch_text.stroke-59"),sQuery(id+"F2.wireOp",EDGE,"fcba4419-a2ee-464f-be9d-58f11bf3418b.sketch_text.stroke-60"),sQuery(id+"F2.wireOp",EDGE,"fcba4419-a2ee-464f-be9d-58f11bf3418b.sketch_text.stroke-61"),sQuery(id+"F2.wireOp",EDGE,"fcba4419-a2ee-464f-be9d-58f11bf3418b.sketch_text.stroke-62"),sQuery(id+"F2.wireOp",EDGE,"fcba4419-a2ee-464f-be9d-58f11bf3418b.sketch_text.stroke-63"),sQuery(id+"F2.wireOp",EDGE,"fcba4419-a2ee-464f-be9d-58f11bf3418b.sketch_text.stroke-64"),sQuery(id+"F2.wireOp",EDGE,"fcba4419-a2ee-464f-be9d-58f11bf3418b.sketch_text.stroke-65"),sQuery(id+"F2.wireOp",EDGE,"fcba4419-a2ee-464f-be9d-58f11bf3418b.sketch_text.stroke-66"),sQuery(id+"F2.wireOp",EDGE,"fcba4419-a2ee-464f-be9d-58f11bf3418b.sketch_text.stroke-67"),sQuery(id+"F2.wireOp",EDGE,"fcba4419-a2ee-464f-be9d-58f11bf3418b.sketch_text.stroke-68"),sQuery(id+"F2.wireOp",EDGE,"fcba4419-a2ee-464f-be9d-58f11bf3418b.sketch_text.stroke-69"),sQuery(id+"F2.wireOp",EDGE,"fcba4419-a2ee-464f-be9d-58f11bf3418b.sketch_text.stroke-70"),sQuery(id+"F2.wireOp",EDGE,"fcba4419-a2ee-464f-be9d-58f11bf3418b.sketch_text.stroke-71"),sQuery(id+"F2.wireOp",EDGE,"fcba4419-a2ee-464f-be9d-58f11bf3418b.sketch_text.stroke-72"),sQuery(id+"F2.wireOp",EDGE,"fcba4419-a2ee-464f-be9d-58f11bf3418b.sketch_text.stroke-73"),sQuery(id+"F2.wireOp",EDGE,"fcba4419-a2ee-464f-be9d-58f11bf3418b.sketch_text.stroke-74"),sQuery(id+"F2.wireOp",EDGE,"fcba4419-a2ee-464f-be9d-58f11bf3418b.sketch_text.stroke-75"),sQuery(id+"F2.wireOp",EDGE,"fcba4419-a2ee-464f-be9d-58f11bf3418b.sketch_text.stroke-76"),sQuery(id+"F2.wireOp",EDGE,"fcba4419-a2ee-464f-be9d-58f11bf3418b.sketch_text.stroke-77"),sQuery(id+"F2.wireOp",EDGE,"fcba4419-a2ee-464f-be9d-58f11bf3418b.sketch_text.stroke-78"),sQuery(id+"F2.wireOp",EDGE,"fcba4419-a2ee-464f-be9d-58f11bf3418b.sketch_text.stroke-79"),sQuery(id+"F2.wireOp",EDGE,"fcba4419-a2ee-464f-be9d-58f11bf3418b.sketch_text.stroke-80"),sQuery(id+"F2.wireOp",EDGE,"fcba4419-a2ee-464f-be9d-58f11bf3418b.sketch_text.stroke-81"),sQuery(id+"F2.wireOp",EDGE,"fcba4419-a2ee-464f-be9d-58f11bf3418b.sketch_text.stroke-82"),sQuery(id+"F2.wireOp",EDGE,"fcba4419-a2ee-464f-be9d-58f11bf3418b.sketch_text.stroke-83"),sQuery(id+"F2.wireOp",EDGE,"fcba4419-a2ee-464f-be9d-58f11bf3418b.sketch_text.stroke-84"),sQuery(id+"F2.wireOp",EDGE,"fcba4419-a2ee-464f-be9d-58f11bf3418b.sketch_text.stroke-85"),sQuery(id+"F2.wireOp",EDGE,"fcba4419-a2ee-464f-be9d-58f11bf3418b.sketch_text.stroke-86"),sQuery(id+"F2.wireOp",EDGE,"fcba4419-a2ee-464f-be9d-58f11bf3418b.sketch_text.stroke-87"),sQuery(id+"F2.wireOp",EDGE,"fcba4419-a2ee-464f-be9d-58f11bf3418b.sketch_text.stroke-88"),sQuery(id+"F2.wireOp",EDGE,"fcba4419-a2ee-464f-be9d-58f11bf3418b.sketch_text.stroke-89"),sQuery(id+"F2.wireOp",EDGE,"fcba4419-a2ee-464f-be9d-58f11bf3418b.sketch_text.stroke-90"),sQuery(id+"F2.wireOp",EDGE,"fcba4419-a2ee-464f-be9d-58f11bf3418b.sketch_text.stroke-91"),sQuery(id+"F2.wireOp",EDGE,"fcba4419-a2ee-464f-be9d-58f11bf3418b.sketch_text.stroke-92"),sQuery(id+"F2.wireOp",EDGE,"fcba4419-a2ee-464f-be9d-58f11bf3418b.sketch_text.stroke-93"),sQuery(id+"F2.wireOp",EDGE,"fcba4419-a2ee-464f-be9d-58f11bf3418b.sketch_text.stroke-94"),sQuery(id+"F2.wireOp",EDGE,"fcba4419-a2ee-464f-be9d-58f11bf3418b.sketch_text.stroke-95"),sQuery(id+"F2.wireOp",EDGE,"fcba4419-a2ee-464f-be9d-58f11bf3418b.sketch_text.stroke-96"),sQuery(id+"F2.wireOp",EDGE,"fcba4419-a2ee-464f-be9d-58f11bf3418b.sketch_text.stroke-97"),sQuery(id+"F2.wireOp",EDGE,"fcba4419-a2ee-464f-be9d-58f11bf3418b.sketch_text.stroke-98"),sQuery(id+"F2.wireOp",EDGE,"fcba4419-a2ee-464f-be9d-58f11bf3418b.sketch_text.stroke-99"),sQuery(id+"F2.wireOp",EDGE,"fcba4419-a2ee-464f-be9d-58f11bf3418b.sketch_text.stroke-100"),sQuery(id+"F2.wireOp",EDGE,"fcba4419-a2ee-464f-be9d-58f11bf3418b.sketch_text.stroke-101"),sQuery(id+"F2.wireOp",EDGE,"fcba4419-a2ee-464f-be9d-58f11bf3418b.sketch_text.stroke-102"),sQuery(id+"F2.wireOp",EDGE,"fcba4419-a2ee-464f-be9d-58f11bf3418b.sketch_text.stroke-103"),sQuery(id+"F2.wireOp",EDGE,"fcba4419-a2ee-464f-be9d-58f11bf3418b.sketch_text.stroke-104"),sQuery(id+"F2.wireOp",EDGE,"fcba4419-a2ee-464f-be9d-58f11bf3418b.sketch_text.stroke-105"),sQuery(id+"F2.wireOp",EDGE,"fcba4419-a2ee-464f-be9d-58f11bf3418b.sketch_text.stroke-106"),sQuery(id+"F2.wireOp",EDGE,"fcba4419-a2ee-464f-be9d-58f11bf3418b.sketch_text.stroke-107"),sQuery(id+"F2.wireOp",EDGE,"fcba4419-a2ee-464f-be9d-58f11bf3418b.sketch_text.stroke-108"),sQuery(id+"F2.wireOp",EDGE,"fcba4419-a2ee-464f-be9d-58f11bf3418b.sketch_text.stroke-109"),sQuery(id+"F2.wireOp",EDGE,"fcba4419-a2ee-464f-be9d-58f11bf3418b.sketch_text.stroke-110"),sQuery(id+"F2.wireOp",EDGE,"fcba4419-a2ee-464f-be9d-58f11bf3418b.sketch_text.stroke-111"),sQuery(id+"F2.wireOp",EDGE,"fcba4419-a2ee-464f-be9d-58f11bf3418b.sketch_text.stroke-112"),sQuery(id+"F2.wireOp",EDGE,"fcba4419-a2ee-464f-be9d-58f11bf3418b.sketch_text.stroke-113"),sQuery(id+"F2.wireOp",EDGE,"fcba4419-a2ee-464f-be9d-58f11bf3418b.sketch_text.stroke-114"),sQuery(id+"F2.wireOp",EDGE,"fcba4419-a2ee-464f-be9d-58f11bf3418b.sketch_text.stroke-115"),sQuery(id+"F2.wireOp",EDGE,"fcba4419-a2ee-464f-be9d-58f11bf3418b.sketch_text.stroke-116"),sQuery(id+"F2.wireOp",EDGE,"fcba4419-a2ee-464f-be9d-58f11bf3418b.sketch_text.stroke-117"),sQuery(id+"F2.wireOp",EDGE,"fcba4419-a2ee-464f-be9d-58f11bf3418b.sketch_text.stroke-118"),sQuery(id+"F2.wireOp",EDGE,"fcba4419-a2ee-464f-be9d-58f11bf3418b.sketch_text.stroke-119"),sQuery(id+"F2.wireOp",EDGE,"fcba4419-a2ee-464f-be9d-58f11bf3418b.sketch_text.stroke-120"),sQuery(id+"F2.wireOp",EDGE,"fcba4419-a2ee-464f-be9d-58f11bf3418b.sketch_text.stroke-121"),sQuery(id+"F2.wireOp",EDGE,"fcba4419-a2ee-464f-be9d-58f11bf3418b.sketch_text.stroke-122"),sQuery(id+"F2.wireOp",EDGE,"fcba4419-a2ee-464f-be9d-58f11bf3418b.sketch_text.stroke-123"),sQuery(id+"F2.wireOp",EDGE,"fcba4419-a2ee-464f-be9d-58f11bf3418b.sketch_text.stroke-124"),sQuery(id+"F2.wireOp",EDGE,"fcba4419-a2ee-464f-be9d-58f11bf3418b.sketch_text.stroke-125"),sQuery(id+"F2.wireOp",EDGE,"fcba4419-a2ee-464f-be9d-58f11bf3418b.sketch_text.stroke-126"),sQuery(id+"F2.wireOp",EDGE,"fcba4419-a2ee-464f-be9d-58f11bf3418b.sketch_text.stroke-127"),sQuery(id+"F2.wireOp",EDGE,"fcba4419-a2ee-464f-be9d-58f11bf3418b.sketch_text.stroke-128"),sQuery(id+"F2.wireOp",EDGE,"fcba4419-a2ee-464f-be9d-58f11bf3418b.sketch_text.stroke-129"),sQuery(id+"F2.wireOp",EDGE,"fcba4419-a2ee-464f-be9d-58f11bf3418b.sketch_text.stroke-130"),sQuery(id+"F2.wireOp",EDGE,"fcba4419-a2ee-464f-be9d-58f11bf3418b.sketch_text.stroke-131"),sQuery(id+"F2.wireOp",EDGE,"fcba4419-a2ee-464f-be9d-58f11bf3418b.sketch_text.stroke-132"),sQuery(id+"F2.wireOp",EDGE,"fcba4419-a2ee-464f-be9d-58f11bf3418b.sketch_text.stroke-133"),sQuery(id+"F2.wireOp",EDGE,"fcba4419-a2ee-464f-be9d-58f11bf3418b.sketch_text.stroke-134"),sQuery(id+"F2.wireOp",EDGE,"fcba4419-a2ee-464f-be9d-58f11bf3418b.sketch_text.stroke-135"),sQuery(id+"F2.wireOp",EDGE,"fcba4419-a2ee-464f-be9d-58f11bf3418b.sketch_text.stroke-136"),sQuery(id+"F2.wireOp",EDGE,"fcba4419-a2ee-464f-be9d-58f11bf3418b.sketch_text.stroke-137"),sQuery(id+"F2.wireOp",EDGE,"fcba4419-a2ee-464f-be9d-58f11bf3418b.sketch_text.stroke-138"),sQuery(id+"F2.wireOp",EDGE,"fcba4419-a2ee-464f-be9d-58f11bf3418b.sketch_text.stroke-139"),sQuery(id+"F2.wireOp",EDGE,"fcba4419-a2ee-464f-be9d-58f11bf3418b.sketch_text.stroke-140"),sQuery(id+"F2.wireOp",EDGE,"fcba4419-a2ee-464f-be9d-58f11bf3418b.sketch_text.stroke-141"),sQuery(id+"F2.wireOp",EDGE,"fcba4419-a2ee-464f-be9d-58f11bf3418b.sketch_text.stroke-142"),sQuery(id+"F2.wireOp",EDGE,"fcba4419-a2ee-464f-be9d-58f11bf3418b.sketch_text.stroke-143"),sQuery(id+"F2.wireOp",EDGE,"fcba4419-a2ee-464f-be9d-58f11bf3418b.sketch_text.stroke-144"),sQuery(id+"F2.wireOp",EDGE,"fcba4419-a2ee-464f-be9d-58f11bf3418b.sketch_text.stroke-145"),sQuery(id+"F2.wireOp",EDGE,"fcba4419-a2ee-464f-be9d-58f11bf3418b.sketch_text.stroke-146"),sQuery(id+"F2.wireOp",EDGE,"fcba4419-a2ee-464f-be9d-58f11bf3418b.sketch_text.stroke-147"),sQuery(id+"F2.wireOp",EDGE,"fcba4419-a2ee-464f-be9d-58f11bf3418b.sketch_text.stroke-148"),sQuery(id+"F2.wireOp",EDGE,"fcba4419-a2ee-464f-be9d-58f11bf3418b.sketch_text.stroke-149"),sQuery(id+"F2.wireOp",EDGE,"fcba4419-a2ee-464f-be9d-58f11bf3418b.sketch_text.stroke-150"),sQuery(id+"F2.wireOp",EDGE,"fcba4419-a2ee-464f-be9d-58f11bf3418b.sketch_text.stroke-151"),sQuery(id+"F2.wireOp",EDGE,"fcba4419-a2ee-464f-be9d-58f11bf3418b.sketch_text.stroke-152"),sQuery(id+"F2.wireOp",EDGE,"fcba4419-a2ee-464f-be9d-58f11bf3418b.sketch_text.stroke-153"),sQuery(id+"F2.wireOp",EDGE,"fcba4419-a2ee-464f-be9d-58f11bf3418b.sketch_text.stroke-154"),sQuery(id+"F2.wireOp",EDGE,"fcba4419-a2ee-464f-be9d-58f11bf3418b.sketch_text.stroke-155"),sQuery(id+"F2.wireOp",EDGE,"fcba4419-a2ee-464f-be9d-58f11bf3418b.sketch_text.stroke-156"),sQuery(id+"F2.wireOp",EDGE,"fcba4419-a2ee-464f-be9d-58f11bf3418b.sketch_text.stroke-157"),sQuery(id+"F2.wireOp",EDGE,"fcba4419-a2ee-464f-be9d-58f11bf3418b.sketch_text.stroke-158"),sQuery(id+"F2.wireOp",EDGE,"fcba4419-a2ee-464f-be9d-58f11bf3418b.sketch_text.stroke-159"),sQuery(id+"F2.wireOp",EDGE,"fcba4419-a2ee-464f-be9d-58f11bf3418b.sketch_text.stroke-160"),sQuery(id+"F2.wireOp",EDGE,"fcba4419-a2ee-464f-be9d-58f11bf3418b.sketch_text.stroke-161"),sQuery(id+"F2.wireOp",EDGE,"fcba4419-a2ee-464f-be9d-58f11bf3418b.sketch_text.stroke-162"),sQuery(id+"F2.wireOp",EDGE,"fcba4419-a2ee-464f-be9d-58f11bf3418b.sketch_text.stroke-163"),sQuery(id+"F2.wireOp",EDGE,"fcba4419-a2ee-464f-be9d-58f11bf3418b.sketch_text.stroke-164"),sQuery(id+"F2.wireOp",EDGE,"fcba4419-a2ee-464f-be9d-58f11bf3418b.sketch_text.stroke-165"),sQuery(id+"F2.wireOp",EDGE,"fcba4419-a2ee-464f-be9d-58f11bf3418b.sketch_text.stroke-166"),sQuery(id+"F2.wireOp",EDGE,"fcba4419-a2ee-464f-be9d-58f11bf3418b.sketch_text.stroke-167"),sQuery(id+"F2.wireOp",EDGE,"fcba4419-a2ee-464f-be9d-58f11bf3418b.sketch_text.stroke-168"),sQuery(id+"F2.wireOp",EDGE,"fcba4419-a2ee-464f-be9d-58f11bf3418b.sketch_text.stroke-169"),sQuery(id+"F2.wireOp",EDGE,"fcba4419-a2ee-464f-be9d-58f11bf3418b.sketch_text.stroke-170"),sQuery(id+"F2.wireOp",EDGE,"fcba4419-a2ee-464f-be9d-58f11bf3418b.sketch_text.stroke-171"),sQuery(id+"F2.wireOp",EDGE,"fcba4419-a2ee-464f-be9d-58f11bf3418b.sketch_text.stroke-172"),sQuery(id+"F2.wireOp",EDGE,"fcba4419-a2ee-464f-be9d-58f11bf3418b.sketch_text.stroke-173"),sQuery(id+"FHMxAyK4CFUKdhS_1.wireOp",EDGE,"1cb9c079-ea9b-4899-8069-e0e3048e911d.sketch_text.stroke-0"),sQuery(id+"FHMxAyK4CFUKdhS_1.wireOp",EDGE,"1cb9c079-ea9b-4899-8069-e0e3048e911d.sketch_text.stroke-1"),sQuery(id+"FHMxAyK4CFUKdhS_1.wireOp",EDGE,"1cb9c079-ea9b-4899-8069-e0e3048e911d.sketch_text.stroke-2"),sQuery(id+"FHMxAyK4CFUKdhS_1.wireOp",EDGE,"1cb9c079-ea9b-4899-8069-e0e3048e911d.sketch_text.stroke-3"),sQuery(id+"FHMxAyK4CFUKdhS_1.wireOp",EDGE,"1cb9c079-ea9b-4899-8069-e0e3048e911d.sketch_text.stroke-4"),sQuery(id+"FHMxAyK4CFUKdhS_1.wireOp",EDGE,"1cb9c079-ea9b-4899-8069-e0e3048e911d.sketch_text.stroke-5"),sQuery(id+"FHMxAyK4CFUKdhS_1.wireOp",EDGE,"1cb9c079-ea9b-4899-8069-e0e3048e911d.sketch_text.stroke-6"),sQuery(id+"FHMxAyK4CFUKdhS_1.wireOp",EDGE,"1cb9c079-ea9b-4899-8069-e0e3048e911d.sketch_text.stroke-7"),sQuery(id+"FHMxAyK4CFUKdhS_1.wireOp",EDGE,"1cb9c079-ea9b-4899-8069-e0e3048e911d.sketch_text.stroke-8"),sQuery(id+"FHMxAyK4CFUKdhS_1.wireOp",EDGE,"1cb9c079-ea9b-4899-8069-e0e3048e911d.sketch_text.stroke-9"),sQuery(id+"FHMxAyK4CFUKdhS_1.wireOp",EDGE,"1cb9c079-ea9b-4899-8069-e0e3048e911d.sketch_text.stroke-10"),sQuery(id+"FHMxAyK4CFUKdhS_1.wireOp",EDGE,"1cb9c079-ea9b-4899-8069-e0e3048e911d.sketch_text.stroke-11"),sQuery(id+"FHMxAyK4CFUKdhS_1.wireOp",EDGE,"1cb9c079-ea9b-4899-8069-e0e3048e911d.sketch_text.stroke-12"),sQuery(id+"FHMxAyK4CFUKdhS_1.wireOp",EDGE,"1cb9c079-ea9b-4899-8069-e0e3048e911d.sketch_text.stroke-13"),sQuery(id+"FHMxAyK4CFUKdhS_1.wireOp",EDGE,"1cb9c079-ea9b-4899-8069-e0e3048e911d.sketch_text.stroke-14"),sQuery(id+"FHMxAyK4CFUKdhS_1.wireOp",EDGE,"1cb9c079-ea9b-4899-8069-e0e3048e911d.sketch_text.stroke-15"),sQuery(id+"FHMxAyK4CFUKdhS_1.wireOp",EDGE,"1cb9c079-ea9b-4899-8069-e0e3048e911d.sketch_text.stroke-16"),sQuery(id+"FHMxAyK4CFUKdhS_1.wireOp",EDGE,"1cb9c079-ea9b-4899-8069-e0e3048e911d.sketch_text.stroke-17"),sQuery(id+"FHMxAyK4CFUKdhS_1.wireOp",EDGE,"1cb9c079-ea9b-4899-8069-e0e3048e911d.sketch_text.stroke-18"),sQuery(id+"FHMxAyK4CFUKdhS_1.wireOp",EDGE,"1cb9c079-ea9b-4899-8069-e0e3048e911d.sketch_text.stroke-19"),sQuery(id+"FHMxAyK4CFUKdhS_1.wireOp",EDGE,"1cb9c079-ea9b-4899-8069-e0e3048e911d.sketch_text.stroke-20"),sQuery(id+"FHMxAyK4CFUKdhS_1.wireOp",EDGE,"1cb9c079-ea9b-4899-8069-e0e3048e911d.sketch_text.stroke-21"),sQuery(id+"FHMxAyK4CFUKdhS_1.wireOp",EDGE,"1cb9c079-ea9b-4899-8069-e0e3048e911d.sketch_text.stroke-22"),sQuery(id+"FHMxAyK4CFUKdhS_1.wireOp",EDGE,"1cb9c079-ea9b-4899-8069-e0e3048e911d.sketch_text.stroke-23"),sQuery(id+"FHMxAyK4CFUKdhS_1.wireOp",EDGE,"1cb9c079-ea9b-4899-8069-e0e3048e911d.sketch_text.stroke-24"),sQuery(id+"FHMxAyK4CFUKdhS_1.wireOp",EDGE,"1cb9c079-ea9b-4899-8069-e0e3048e911d.sketch_text.stroke-25"),sQuery(id+"FHMxAyK4CFUKdhS_1.wireOp",EDGE,"1cb9c079-ea9b-4899-8069-e0e3048e911d.sketch_text.stroke-26"),sQuery(id+"FHMxAyK4CFUKdhS_1.wireOp",EDGE,"1cb9c079-ea9b-4899-8069-e0e3048e911d.sketch_text.stroke-27"),sQuery(id+"FHMxAyK4CFUKdhS_1.wireOp",EDGE,"1cb9c079-ea9b-4899-8069-e0e3048e911d.sketch_text.stroke-28"),sQuery(id+"FHMxAyK4CFUKdhS_1.wireOp",EDGE,"1cb9c079-ea9b-4899-8069-e0e3048e911d.sketch_text.stroke-29"),sQuery(id+"FHMxAyK4CFUKdhS_1.wireOp",EDGE,"1cb9c079-ea9b-4899-8069-e0e3048e911d.sketch_text.stroke-30"),sQuery(id+"FHMxAyK4CFUKdhS_1.wireOp",EDGE,"1cb9c079-ea9b-4899-8069-e0e3048e911d.sketch_text.stroke-31"),sQuery(id+"FHMxAyK4CFUKdhS_1.wireOp",EDGE,"1cb9c079-ea9b-4899-8069-e0e3048e911d.sketch_text.stroke-32"),sQuery(id+"FHMxAyK4CFUKdhS_1.wireOp",EDGE,"1cb9c079-ea9b-4899-8069-e0e3048e911d.sketch_text.stroke-33"),sQuery(id+"FHMxAyK4CFUKdhS_1.wireOp",EDGE,"1cb9c079-ea9b-4899-8069-e0e3048e911d.sketch_text.stroke-34"),sQuery(id+"FHMxAyK4CFUKdhS_1.wireOp",EDGE,"1cb9c079-ea9b-4899-8069-e0e3048e911d.sketch_text.stroke-35"),sQuery(id+"FHMxAyK4CFUKdhS_1.wireOp",EDGE,"1cb9c079-ea9b-4899-8069-e0e3048e911d.sketch_text.stroke-36"),sQuery(id+"FHMxAyK4CFUKdhS_1.wireOp",EDGE,"1cb9c079-ea9b-4899-8069-e0e3048e911d.sketch_text.stroke-37"),sQuery(id+"FHMxAyK4CFUKdhS_1.wireOp",EDGE,"1cb9c079-ea9b-4899-8069-e0e3048e911d.sketch_text.stroke-38"),sQuery(id+"FHMxAyK4CFUKdhS_1.wireOp",EDGE,"1cb9c079-ea9b-4899-8069-e0e3048e911d.sketch_text.stroke-39"),sQuery(id+"FHMxAyK4CFUKdhS_1.wireOp",EDGE,"1cb9c079-ea9b-4899-8069-e0e3048e911d.sketch_text.stroke-40"),sQuery(id+"FHMxAyK4CFUKdhS_1.wireOp",EDGE,"1cb9c079-ea9b-4899-8069-e0e3048e911d.sketch_text.stroke-41"),sQuery(id+"FHMxAyK4CFUKdhS_1.wireOp",EDGE,"1cb9c079-ea9b-4899-8069-e0e3048e911d.sketch_text.stroke-42"),sQuery(id+"FHMxAyK4CFUKdhS_1.wireOp",EDGE,"1cb9c079-ea9b-4899-8069-e0e3048e911d.sketch_text.stroke-43"),sQuery(id+"FHMxAyK4CFUKdhS_1.wireOp",EDGE,"1cb9c079-ea9b-4899-8069-e0e3048e911d.sketch_text.stroke-44"),sQuery(id+"FHMxAyK4CFUKdhS_1.wireOp",EDGE,"1cb9c079-ea9b-4899-8069-e0e3048e911d.sketch_text.stroke-45"),sQuery(id+"FHMxAyK4CFUKdhS_1.wireOp",EDGE,"1cb9c079-ea9b-4899-8069-e0e3048e911d.sketch_text.stroke-46"),sQuery(id+"FHMxAyK4CFUKdhS_1.wireOp",EDGE,"1cb9c079-ea9b-4899-8069-e0e3048e911d.sketch_text.stroke-47"),sQuery(id+"FHMxAyK4CFUKdhS_1.wireOp",EDGE,"1cb9c079-ea9b-4899-8069-e0e3048e911d.sketch_text.stroke-48"),sQuery(id+"FHMxAyK4CFUKdhS_1.wireOp",EDGE,"1cb9c079-ea9b-4899-8069-e0e3048e911d.sketch_text.stroke-49"),sQuery(id+"FHMxAyK4CFUKdhS_1.wireOp",EDGE,"1cb9c079-ea9b-4899-8069-e0e3048e911d.sketch_text.stroke-50"),sQuery(id+"FHMxAyK4CFUKdhS_1.wireOp",EDGE,"1cb9c079-ea9b-4899-8069-e0e3048e911d.sketch_text.stroke-51"),sQuery(id+"FHMxAyK4CFUKdhS_1.wireOp",EDGE,"1cb9c079-ea9b-4899-8069-e0e3048e911d.sketch_text.stroke-52"),sQuery(id+"FHMxAyK4CFUKdhS_1.wireOp",EDGE,"1cb9c079-ea9b-4899-8069-e0e3048e911d.sketch_text.stroke-53"),sQuery(id+"FHMxAyK4CFUKdhS_1.wireOp",EDGE,"1cb9c079-ea9b-4899-8069-e0e3048e911d.sketch_text.stroke-54"),sQuery(id+"FHMxAyK4CFUKdhS_1.wireOp",EDGE,"1cb9c079-ea9b-4899-8069-e0e3048e911d.sketch_text.stroke-55"),sQuery(id+"FHMxAyK4CFUKdhS_1.wireOp",EDGE,"1cb9c079-ea9b-4899-8069-e0e3048e911d.sketch_text.stroke-56"),sQuery(id+"FHMxAyK4CFUKdhS_1.wireOp",EDGE,"1cb9c079-ea9b-4899-8069-e0e3048e911d.sketch_text.stroke-57"),sQuery(id+"FHMxAyK4CFUKdhS_1.wireOp",EDGE,"1cb9c079-ea9b-4899-8069-e0e3048e911d.sketch_text.stroke-58"),sQuery(id+"FHMxAyK4CFUKdhS_1.wireOp",EDGE,"1cb9c079-ea9b-4899-8069-e0e3048e911d.sketch_text.stroke-59"),sQuery(id+"FHMxAyK4CFUKdhS_1.wireOp",EDGE,"1cb9c079-ea9b-4899-8069-e0e3048e911d.sketch_text.stroke-60"),sQuery(id+"FHMxAyK4CFUKdhS_1.wireOp",EDGE,"1cb9c079-ea9b-4899-8069-e0e3048e911d.sketch_text.stroke-61"),sQuery(id+"FHMxAyK4CFUKdhS_1.wireOp",EDGE,"1cb9c079-ea9b-4899-8069-e0e3048e911d.sketch_text.stroke-62"),sQuery(id+"FHMxAyK4CFUKdhS_1.wireOp",EDGE,"1cb9c079-ea9b-4899-8069-e0e3048e911d.sketch_text.stroke-71"),sQuery(id+"FHMxAyK4CFUKdhS_1.wireOp",EDGE,"1cb9c079-ea9b-4899-8069-e0e3048e911d.sketch_text.stroke-72"),sQuery(id+"FHMxAyK4CFUKdhS_1.wireOp",EDGE,"1cb9c079-ea9b-4899-8069-e0e3048e911d.sketch_text.stroke-73"),sQuery(id+"FHMxAyK4CFUKdhS_1.wireOp",EDGE,"1cb9c079-ea9b-4899-8069-e0e3048e911d.sketch_text.stroke-74"),sQuery(id+"FHMxAyK4CFUKdhS_1.wireOp",EDGE,"1cb9c079-ea9b-4899-8069-e0e3048e911d.sketch_text.stroke-75"),sQuery(id+"FHMxAyK4CFUKdhS_1.wireOp",EDGE,"1cb9c079-ea9b-4899-8069-e0e3048e911d.sketch_text.stroke-76"),sQuery(id+"FHMxAyK4CFUKdhS_1.wireOp",EDGE,"1cb9c079-ea9b-4899-8069-e0e3048e911d.sketch_text.stroke-77"),sQuery(id+"FHMxAyK4CFUKdhS_1.wireOp",EDGE,"1cb9c079-ea9b-4899-8069-e0e3048e911d.sketch_text.stroke-78"),sQuery(id+"FHMxAyK4CFUKdhS_1.wireOp",EDGE,"1cb9c079-ea9b-4899-8069-e0e3048e911d.sketch_text.stroke-79"),sQuery(id+"FHMxAyK4CFUKdhS_1.wireOp",EDGE,"1cb9c079-ea9b-4899-8069-e0e3048e911d.sketch_text.stroke-80"),sQuery(id+"FHMxAyK4CFUKdhS_1.wireOp",EDGE,"1cb9c079-ea9b-4899-8069-e0e3048e911d.sketch_text.stroke-81"),sQuery(id+"FHMxAyK4CFUKdhS_1.wireOp",EDGE,"1cb9c079-ea9b-4899-8069-e0e3048e911d.sketch_text.stroke-82"),sQuery(id+"FHMxAyK4CFUKdhS_1.wireOp",EDGE,"1cb9c079-ea9b-4899-8069-e0e3048e911d.sketch_text.stroke-83"),sQuery(id+"FHMxAyK4CFUKdhS_1.wireOp",EDGE,"1cb9c079-ea9b-4899-8069-e0e3048e911d.sketch_text.stroke-84"),sQuery(id+"FHMxAyK4CFUKdhS_1.wireOp",EDGE,"1cb9c079-ea9b-4899-8069-e0e3048e911d.sketch_text.stroke-85"),sQuery(id+"FHMxAyK4CFUKdhS_1.wireOp",EDGE,"1cb9c079-ea9b-4899-8069-e0e3048e911d.sketch_text.stroke-86"),sQuery(id+"FHMxAyK4CFUKdhS_1.wireOp",EDGE,"1cb9c079-ea9b-4899-8069-e0e3048e911d.sketch_text.stroke-87"),sQuery(id+"FHMxAyK4CFUKdhS_1.wireOp",EDGE,"1cb9c079-ea9b-4899-8069-e0e3048e911d.sketch_text.stroke-88"),sQuery(id+"FHMxAyK4CFUKdhS_1.wireOp",EDGE,"1cb9c079-ea9b-4899-8069-e0e3048e911d.sketch_text.stroke-89"),sQuery(id+"FHMxAyK4CFUKdhS_1.wireOp",EDGE,"1cb9c079-ea9b-4899-8069-e0e3048e911d.sketch_text.stroke-90"),sQuery(id+"FHMxAyK4CFUKdhS_1.wireOp",EDGE,"1cb9c079-ea9b-4899-8069-e0e3048e911d.sketch_text.stroke-91"),sQuery(id+"FHMxAyK4CFUKdhS_1.wireOp",EDGE,"1cb9c079-ea9b-4899-8069-e0e3048e911d.sketch_text.stroke-92"),sQuery(id+"FHMxAyK4CFUKdhS_1.wireOp",EDGE,"1cb9c079-ea9b-4899-8069-e0e3048e911d.sketch_text.stroke-93"),sQuery(id+"FHMxAyK4CFUKdhS_1.wireOp",EDGE,"1cb9c079-ea9b-4899-8069-e0e3048e911d.sketch_text.stroke-94"),sQuery(id+"FHMxAyK4CFUKdhS_1.wireOp",EDGE,"1cb9c079-ea9b-4899-8069-e0e3048e911d.sketch_text.stroke-95"),sQuery(id+"FHMxAyK4CFUKdhS_1.wireOp",EDGE,"1cb9c079-ea9b-4899-8069-e0e3048e911d.sketch_text.stroke-96"),sQuery(id+"FHMxAyK4CFUKdhS_1.wireOp",EDGE,"1cb9c079-ea9b-4899-8069-e0e3048e911d.sketch_text.stroke-97"),sQuery(id+"FHMxAyK4CFUKdhS_1.wireOp",EDGE,"1cb9c079-ea9b-4899-8069-e0e3048e911d.sketch_text.stroke-103"),sQuery(id+"FHMxAyK4CFUKdhS_1.wireOp",EDGE,"1cb9c079-ea9b-4899-8069-e0e3048e911d.sketch_text.stroke-104"),sQuery(id+"FHMxAyK4CFUKdhS_1.wireOp",EDGE,"1cb9c079-ea9b-4899-8069-e0e3048e911d.sketch_text.stroke-105"),sQuery(id+"FHMxAyK4CFUKdhS_1.wireOp",EDGE,"1cb9c079-ea9b-4899-8069-e0e3048e911d.sketch_text.stroke-106"),sQuery(id+"FHMxAyK4CFUKdhS_1.wireOp",EDGE,"1cb9c079-ea9b-4899-8069-e0e3048e911d.sketch_text.stroke-107"),sQuery(id+"FHMxAyK4CFUKdhS_1.wireOp",EDGE,"1cb9c079-ea9b-4899-8069-e0e3048e911d.sketch_text.stroke-108"),sQuery(id+"FHMxAyK4CFUKdhS_1.wireOp",EDGE,"1cb9c079-ea9b-4899-8069-e0e3048e911d.sketch_text.stroke-109"),sQuery(id+"FHMxAyK4CFUKdhS_1.wireOp",EDGE,"1cb9c079-ea9b-4899-8069-e0e3048e911d.sketch_text.stroke-110"),sQuery(id+"FHMxAyK4CFUKdhS_1.wireOp",EDGE,"1cb9c079-ea9b-4899-8069-e0e3048e911d.sketch_text.stroke-111"),sQuery(id+"FHMxAyK4CFUKdhS_1.wireOp",EDGE,"1cb9c079-ea9b-4899-8069-e0e3048e911d.sketch_text.stroke-112"),sQuery(id+"FHMxAyK4CFUKdhS_1.wireOp",EDGE,"1cb9c079-ea9b-4899-8069-e0e3048e911d.sketch_text.stroke-113"),sQuery(id+"FHMxAyK4CFUKdhS_1.wireOp",EDGE,"1cb9c079-ea9b-4899-8069-e0e3048e911d.sketch_text.stroke-114"),sQuery(id+"FHMxAyK4CFUKdhS_1.wireOp",EDGE,"1cb9c079-ea9b-4899-8069-e0e3048e911d.sketch_text.stroke-115"),sQuery(id+"FHMxAyK4CFUKdhS_1.wireOp",EDGE,"1cb9c079-ea9b-4899-8069-e0e3048e911d.sketch_text.stroke-116"),sQuery(id+"FHMxAyK4CFUKdhS_1.wireOp",EDGE,"1cb9c079-ea9b-4899-8069-e0e3048e911d.sketch_text.stroke-117"),sQuery(id+"FHMxAyK4CFUKdhS_1.wireOp",EDGE,"1cb9c079-ea9b-4899-8069-e0e3048e911d.sketch_text.stroke-118"),sQuery(id+"FHMxAyK4CFUKdhS_1.wireOp",EDGE,"1cb9c079-ea9b-4899-8069-e0e3048e911d.sketch_text.stroke-119"),sQuery(id+"FHMxAyK4CFUKdhS_1.wireOp",EDGE,"1cb9c079-ea9b-4899-8069-e0e3048e911d.sketch_text.stroke-120"),sQuery(id+"FHMxAyK4CFUKdhS_1.wireOp",EDGE,"1cb9c079-ea9b-4899-8069-e0e3048e911d.sketch_text.stroke-121"),sQuery(id+"FHMxAyK4CFUKdhS_1.wireOp",EDGE,"1cb9c079-ea9b-4899-8069-e0e3048e911d.sketch_text.stroke-122"),sQuery(id+"FHMxAyK4CFUKdhS_1.wireOp",EDGE,"1cb9c079-ea9b-4899-8069-e0e3048e911d.sketch_text.stroke-123"),sQuery(id+"FHMxAyK4CFUKdhS_1.wireOp",EDGE,"1cb9c079-ea9b-4899-8069-e0e3048e911d.sketch_text.stroke-124"),sQuery(id+"FHMxAyK4CFUKdhS_1.wireOp",EDGE,"1cb9c079-ea9b-4899-8069-e0e3048e911d.sketch_text.stroke-125"),sQuery(id+"FHMxAyK4CFUKdhS_1.wireOp",EDGE,"1cb9c079-ea9b-4899-8069-e0e3048e911d.sketch_text.stroke-126"),sQuery(id+"FHMxAyK4CFUKdhS_1.wireOp",EDGE,"1cb9c079-ea9b-4899-8069-e0e3048e911d.sketch_text.stroke-127"),sQuery(id+"FHMxAyK4CFUKdhS_1.wireOp",EDGE,"1cb9c079-ea9b-4899-8069-e0e3048e911d.sketch_text.stroke-128"),sQuery(id+"FHMxAyK4CFUKdhS_1.wireOp",EDGE,"1cb9c079-ea9b-4899-8069-e0e3048e911d.sketch_text.stroke-129"),sQuery(id+"FHMxAyK4CFUKdhS_1.wireOp",EDGE,"1cb9c079-ea9b-4899-8069-e0e3048e911d.sketch_text.stroke-130"),sQuery(id+"FHMxAyK4CFUKdhS_1.wireOp",EDGE,"1cb9c079-ea9b-4899-8069-e0e3048e911d.sketch_text.stroke-131"),sQuery(id+"FHMxAyK4CFUKdhS_1.wireOp",EDGE,"1cb9c079-ea9b-4899-8069-e0e3048e911d.sketch_text.stroke-132"),sQuery(id+"FHMxAyK4CFUKdhS_1.wireOp",EDGE,"1cb9c079-ea9b-4899-8069-e0e3048e911d.sketch_text.stroke-133"),sQuery(id+"FHMxAyK4CFUKdhS_1.wireOp",EDGE,"1cb9c079-ea9b-4899-8069-e0e3048e911d.sketch_text.stroke-134"),sQuery(id+"FHMxAyK4CFUKdhS_1.wireOp",EDGE,"1cb9c079-ea9b-4899-8069-e0e3048e911d.sketch_text.stroke-135"),sQuery(id+"FHMxAyK4CFUKdhS_1.wireOp",EDGE,"1cb9c079-ea9b-4899-8069-e0e3048e911d.sketch_text.stroke-136"),sQuery(id+"FHMxAyK4CFUKdhS_1.wireOp",EDGE,"1cb9c079-ea9b-4899-8069-e0e3048e911d.sketch_text.stroke-137"),sQuery(id+"FHMxAyK4CFUKdhS_1.wireOp",EDGE,"1cb9c079-ea9b-4899-8069-e0e3048e911d.sketch_text.stroke-138"),sQuery(id+"FHMxAyK4CFUKdhS_1.wireOp",EDGE,"1cb9c079-ea9b-4899-8069-e0e3048e911d.sketch_text.stroke-139"),sQuery(id+"FHMxAyK4CFUKdhS_1.wireOp",EDGE,"1cb9c079-ea9b-4899-8069-e0e3048e911d.sketch_text.stroke-140"),sQuery(id+"FHMxAyK4CFUKdhS_1.wireOp",EDGE,"1cb9c079-ea9b-4899-8069-e0e3048e911d.sketch_text.stroke-141"),sQuery(id+"FHMxAyK4CFUKdhS_1.wireOp",EDGE,"1cb9c079-ea9b-4899-8069-e0e3048e911d.sketch_text.stroke-142"),sQuery(id+"FHMxAyK4CFUKdhS_1.wireOp",EDGE,"1cb9c079-ea9b-4899-8069-e0e3048e911d.sketch_text.stroke-143"),sQuery(id+"FHMxAyK4CFUKdhS_1.wireOp",EDGE,"1cb9c079-ea9b-4899-8069-e0e3048e911d.sketch_text.stroke-144"),sQuery(id+"FHMxAyK4CFUKdhS_1.wireOp",EDGE,"1cb9c079-ea9b-4899-8069-e0e3048e911d.sketch_text.stroke-145"),sQuery(id+"FHMxAyK4CFUKdhS_1.wireOp",EDGE,"1cb9c079-ea9b-4899-8069-e0e3048e911d.sketch_text.stroke-146"),sQuery(id+"FHMxAyK4CFUKdhS_1.wireOp",EDGE,"1cb9c079-ea9b-4899-8069-e0e3048e911d.sketch_text.stroke-147"),sQuery(id+"FHMxAyK4CFUKdhS_1.wireOp",EDGE,"1cb9c079-ea9b-4899-8069-e0e3048e911d.sketch_text.stroke-148"),sQuery(id+"FHMxAyK4CFUKdhS_1.wireOp",EDGE,"1cb9c079-ea9b-4899-8069-e0e3048e911d.sketch_text.stroke-149"),sQuery(id+"FHMxAyK4CFUKdhS_1.wireOp",EDGE,"1cb9c079-ea9b-4899-8069-e0e3048e911d.sketch_text.stroke-150"),sQuery(id+"FHMxAyK4CFUKdhS_1.wireOp",EDGE,"1cb9c079-ea9b-4899-8069-e0e3048e911d.sketch_text.stroke-151"),sQuery(id+"FHMxAyK4CFUKdhS_1.wireOp",EDGE,"1cb9c079-ea9b-4899-8069-e0e3048e911d.sketch_text.stroke-152"),sQuery(id+"FHMxAyK4CFUKdhS_1.wireOp",EDGE,"1cb9c079-ea9b-4899-8069-e0e3048e911d.sketch_text.stroke-153"),sQuery(id+"FHMxAyK4CFUKdhS_1.wireOp",EDGE,"1cb9c079-ea9b-4899-8069-e0e3048e911d.sketch_text.stroke-159"),sQuery(id+"FHMxAyK4CFUKdhS_1.wireOp",EDGE,"1cb9c079-ea9b-4899-8069-e0e3048e911d.sketch_text.stroke-160"),sQuery(id+"FHMxAyK4CFUKdhS_1.wireOp",EDGE,"1cb9c079-ea9b-4899-8069-e0e3048e911d.sketch_text.stroke-161"),sQuery(id+"FHMxAyK4CFUKdhS_1.wireOp",EDGE,"1cb9c079-ea9b-4899-8069-e0e3048e911d.sketch_text.stroke-162"),sQuery(id+"FHMxAyK4CFUKdhS_1.wireOp",EDGE,"1cb9c079-ea9b-4899-8069-e0e3048e911d.sketch_text.stroke-163"),sQuery(id+"FHMxAyK4CFUKdhS_1.wireOp",EDGE,"1cb9c079-ea9b-4899-8069-e0e3048e911d.sketch_text.stroke-164"),sQuery(id+"FHMxAyK4CFUKdhS_1.wireOp",EDGE,"1cb9c079-ea9b-4899-8069-e0e3048e911d.sketch_text.stroke-165"),sQuery(id+"FHMxAyK4CFUKdhS_1.wireOp",EDGE,"1cb9c079-ea9b-4899-8069-e0e3048e911d.sketch_text.stroke-166"),sQuery(id+"FHMxAyK4CFUKdhS_1.wireOp",EDGE,"1cb9c079-ea9b-4899-8069-e0e3048e911d.sketch_text.stroke-167"),sQuery(id+"FHMxAyK4CFUKdhS_1.wireOp",EDGE,"1cb9c079-ea9b-4899-8069-e0e3048e911d.sketch_text.stroke-168"),sQuery(id+"FHMxAyK4CFUKdhS_1.wireOp",EDGE,"1cb9c079-ea9b-4899-8069-e0e3048e911d.sketch_text.stroke-169"),sQuery(id+"FHMxAyK4CFUKdhS_1.wireOp",EDGE,"1cb9c079-ea9b-4899-8069-e0e3048e911d.sketch_text.stroke-170"),sQuery(id+"FHMxAyK4CFUKdhS_1.wireOp",EDGE,"1cb9c079-ea9b-4899-8069-e0e3048e911d.sketch_text.stroke-171"),sQuery(id+"FHMxAyK4CFUKdhS_1.wireOp",EDGE,"1cb9c079-ea9b-4899-8069-e0e3048e911d.sketch_text.stroke-172"),sQuery(id+"FHMxAyK4CFUKdhS_1.wireOp",EDGE,"1cb9c079-ea9b-4899-8069-e0e3048e911d.sketch_text.stroke-173"),sQuery(id+"FHMxAyK4CFUKdhS_1.wireOp",EDGE,"1cb9c079-ea9b-4899-8069-e0e3048e911d.sketch_text.stroke-174"),sQuery(id+"FHMxAyK4CFUKdhS_1.wireOp",EDGE,"1cb9c079-ea9b-4899-8069-e0e3048e911d.sketch_text.stroke-175"),sQuery(id+"FHMxAyK4CFUKdhS_1.wireOp",EDGE,"1cb9c079-ea9b-4899-8069-e0e3048e911d.sketch_text.stroke-176"),sQuery(id+"FHMxAyK4CFUKdhS_1.wireOp",EDGE,"1cb9c079-ea9b-4899-8069-e0e3048e911d.sketch_text.stroke-177"),sQuery(id+"FHMxAyK4CFUKdhS_1.wireOp",EDGE,"1cb9c079-ea9b-4899-8069-e0e3048e911d.sketch_text.stroke-178"),sQuery(id+"FHMxAyK4CFUKdhS_1.wireOp",EDGE,"1cb9c079-ea9b-4899-8069-e0e3048e911d.sketch_text.stroke-179"),sQuery(id+"FHMxAyK4CFUKdhS_1.wireOp",EDGE,"1cb9c079-ea9b-4899-8069-e0e3048e911d.sketch_text.stroke-180"),sQuery(id+"F3.wireOp",EDGE,"8007402e-1a4e-4a06-85a5-2af08e553504"),subQ2])],"isStart":true}),makeQuery(id+"F4.opExtrude","SWEPT_FACE",FACE,{"disambiguationData":[OSD([subQ2])]})])],"derivedFrom":makeQuery(id+"F4.opExtrude","CAP_EDGE",EDGE,{"disambiguationData":[OSD([subQ2])],"isStart":true})});}
            var Q14;
            {var subQ0=sQuery(id+"F0.wireOp",EDGE,"E0.top");var subQ1=sQuery(id+"F0.wireOp",EDGE,"E0.bottom");var subQ2=sQuery(id+"F3.wireOp",EDGE,"727ac2c1-f511-4829-95a7-a443ef16a4cd");Q14=makeQuery(id+"F4.boolean.opBoolean","SPLIT",EDGE,{"disambiguationData":[TD([makeQuery(id+"F1.opExtrude","CAP_FACE",FACE,{"disambiguationData":[OSD([subQ1,subQ0,sQuery(id+"F0.wireOp",EDGE,"E0.left"),sQuery(id+"F0.wireOp",EDGE,"E0.right")])],"isStart":false}),makeQuery(id+"F1.opExtrude","SWEPT_FACE",FACE,{"disambiguationData":[OSD([subQ0])]}),makeQuery(id+"F4.opExtrude","CAP_FACE",FACE,{"disambiguationData":[OSD([subQ1,sQuery(id+"F2.wireOp",EDGE,"fcba4419-a2ee-464f-be9d-58f11bf3418b.sketch_text.stroke-0"),sQuery(id+"F2.wireOp",EDGE,"fcba4419-a2ee-464f-be9d-58f11bf3418b.sketch_text.stroke-1"),sQuery(id+"F2.wireOp",EDGE,"fcba4419-a2ee-464f-be9d-58f11bf3418b.sketch_text.stroke-2"),sQuery(id+"F2.wireOp",EDGE,"fcba4419-a2ee-464f-be9d-58f11bf3418b.sketch_text.stroke-3"),sQuery(id+"F2.wireOp",EDGE,"fcba4419-a2ee-464f-be9d-58f11bf3418b.sketch_text.stroke-4"),sQuery(id+"F2.wireOp",EDGE,"fcba4419-a2ee-464f-be9d-58f11bf3418b.sketch_text.stroke-5"),sQuery(id+"F2.wireOp",EDGE,"fcba4419-a2ee-464f-be9d-58f11bf3418b.sketch_text.stroke-6"),sQuery(id+"F2.wireOp",EDGE,"fcba4419-a2ee-464f-be9d-58f11bf3418b.sketch_text.stroke-7"),sQuery(id+"F2.wireOp",EDGE,"fcba4419-a2ee-464f-be9d-58f11bf3418b.sketch_text.stroke-8"),sQuery(id+"F2.wireOp",EDGE,"fcba4419-a2ee-464f-be9d-58f11bf3418b.sketch_text.stroke-9"),sQuery(id+"F2.wireOp",EDGE,"fcba4419-a2ee-464f-be9d-58f11bf3418b.sketch_text.stroke-10"),sQuery(id+"F2.wireOp",EDGE,"fcba4419-a2ee-464f-be9d-58f11bf3418b.sketch_text.stroke-11"),sQuery(id+"F2.wireOp",EDGE,"fcba4419-a2ee-464f-be9d-58f11bf3418b.sketch_text.stroke-12"),sQuery(id+"F2.wireOp",EDGE,"fcba4419-a2ee-464f-be9d-58f11bf3418b.sketch_text.stroke-13"),sQuery(id+"F2.wireOp",EDGE,"fcba4419-a2ee-464f-be9d-58f11bf3418b.sketch_text.stroke-14"),sQuery(id+"F2.wireOp",EDGE,"fcba4419-a2ee-464f-be9d-58f11bf3418b.sketch_text.stroke-15"),sQuery(id+"F2.wireOp",EDGE,"fcba4419-a2ee-464f-be9d-58f11bf3418b.sketch_text.stroke-16"),sQuery(id+"F2.wireOp",EDGE,"fcba4419-a2ee-464f-be9d-58f11bf3418b.sketch_text.stroke-17"),sQuery(id+"F2.wireOp",EDGE,"fcba4419-a2ee-464f-be9d-58f11bf3418b.sketch_text.stroke-18"),sQuery(id+"F2.wireOp",EDGE,"fcba4419-a2ee-464f-be9d-58f11bf3418b.sketch_text.stroke-19"),sQuery(id+"F2.wireOp",EDGE,"fcba4419-a2ee-464f-be9d-58f11bf3418b.sketch_text.stroke-20"),sQuery(id+"F2.wireOp",EDGE,"fcba4419-a2ee-464f-be9d-58f11bf3418b.sketch_text.stroke-21"),sQuery(id+"F2.wireOp",EDGE,"fcba4419-a2ee-464f-be9d-58f11bf3418b.sketch_text.stroke-22"),sQuery(id+"F2.wireOp",EDGE,"fcba4419-a2ee-464f-be9d-58f11bf3418b.sketch_text.stroke-23"),sQuery(id+"F2.wireOp",EDGE,"fcba4419-a2ee-464f-be9d-58f11bf3418b.sketch_text.stroke-24"),sQuery(id+"F2.wireOp",EDGE,"fcba4419-a2ee-464f-be9d-58f11bf3418b.sketch_text.stroke-25"),sQuery(id+"F2.wireOp",EDGE,"fcba4419-a2ee-464f-be9d-58f11bf3418b.sketch_text.stroke-26"),sQuery(id+"F2.wireOp",EDGE,"fcba4419-a2ee-464f-be9d-58f11bf3418b.sketch_text.stroke-27"),sQuery(id+"F2.wireOp",EDGE,"fcba4419-a2ee-464f-be9d-58f11bf3418b.sketch_text.stroke-28"),sQuery(id+"F2.wireOp",EDGE,"fcba4419-a2ee-464f-be9d-58f11bf3418b.sketch_text.stroke-29"),sQuery(id+"F2.wireOp",EDGE,"fcba4419-a2ee-464f-be9d-58f11bf3418b.sketch_text.stroke-30"),sQuery(id+"F2.wireOp",EDGE,"fcba4419-a2ee-464f-be9d-58f11bf3418b.sketch_text.stroke-31"),sQuery(id+"F2.wireOp",EDGE,"fcba4419-a2ee-464f-be9d-58f11bf3418b.sketch_text.stroke-32"),sQuery(id+"F2.wireOp",EDGE,"fcba4419-a2ee-464f-be9d-58f11bf3418b.sketch_text.stroke-33"),sQuery(id+"F2.wireOp",EDGE,"fcba4419-a2ee-464f-be9d-58f11bf3418b.sketch_text.stroke-34"),sQuery(id+"F2.wireOp",EDGE,"fcba4419-a2ee-464f-be9d-58f11bf3418b.sketch_text.stroke-35"),sQuery(id+"F2.wireOp",EDGE,"fcba4419-a2ee-464f-be9d-58f11bf3418b.sketch_text.stroke-36"),sQuery(id+"F2.wireOp",EDGE,"fcba4419-a2ee-464f-be9d-58f11bf3418b.sketch_text.stroke-37"),sQuery(id+"F2.wireOp",EDGE,"fcba4419-a2ee-464f-be9d-58f11bf3418b.sketch_text.stroke-38"),sQuery(id+"F2.wireOp",EDGE,"fcba4419-a2ee-464f-be9d-58f11bf3418b.sketch_text.stroke-39"),sQuery(id+"F2.wireOp",EDGE,"fcba4419-a2ee-464f-be9d-58f11bf3418b.sketch_text.stroke-40"),sQuery(id+"F2.wireOp",EDGE,"fcba4419-a2ee-464f-be9d-58f11bf3418b.sketch_text.stroke-41"),sQuery(id+"F2.wireOp",EDGE,"fcba4419-a2ee-464f-be9d-58f11bf3418b.sketch_text.stroke-42"),sQuery(id+"F2.wireOp",EDGE,"fcba4419-a2ee-464f-be9d-58f11bf3418b.sketch_text.stroke-43"),sQuery(id+"F2.wireOp",EDGE,"fcba4419-a2ee-464f-be9d-58f11bf3418b.sketch_text.stroke-44"),sQuery(id+"F2.wireOp",EDGE,"fcba4419-a2ee-464f-be9d-58f11bf3418b.sketch_text.stroke-45"),sQuery(id+"F2.wireOp",EDGE,"fcba4419-a2ee-464f-be9d-58f11bf3418b.sketch_text.stroke-46"),sQuery(id+"F2.wireOp",EDGE,"fcba4419-a2ee-464f-be9d-58f11bf3418b.sketch_text.stroke-47"),sQuery(id+"F2.wireOp",EDGE,"fcba4419-a2ee-464f-be9d-58f11bf3418b.sketch_text.stroke-48"),sQuery(id+"F2.wireOp",EDGE,"fcba4419-a2ee-464f-be9d-58f11bf3418b.sketch_text.stroke-49"),sQuery(id+"F2.wireOp",EDGE,"fcba4419-a2ee-464f-be9d-58f11bf3418b.sketch_text.stroke-50"),sQuery(id+"F2.wireOp",EDGE,"fcba4419-a2ee-464f-be9d-58f11bf3418b.sketch_text.stroke-51"),sQuery(id+"F2.wireOp",EDGE,"fcba4419-a2ee-464f-be9d-58f11bf3418b.sketch_text.stroke-52"),sQuery(id+"F2.wireOp",EDGE,"fcba4419-a2ee-464f-be9d-58f11bf3418b.sketch_text.stroke-53"),sQuery(id+"F2.wireOp",EDGE,"fcba4419-a2ee-464f-be9d-58f11bf3418b.sketch_text.stroke-54"),sQuery(id+"F2.wireOp",EDGE,"fcba4419-a2ee-464f-be9d-58f11bf3418b.sketch_text.stroke-55"),sQuery(id+"F2.wireOp",EDGE,"fcba4419-a2ee-464f-be9d-58f11bf3418b.sketch_text.stroke-56"),sQuery(id+"F2.wireOp",EDGE,"fcba4419-a2ee-464f-be9d-58f11bf3418b.sketch_text.stroke-57"),sQuery(id+"F2.wireOp",EDGE,"fcba4419-a2ee-464f-be9d-58f11bf3418b.sketch_text.stroke-58"),sQuery(id+"F2.wireOp",EDGE,"fcba4419-a2ee-464f-be9d-58f11bf3418b.sketch_text.stroke-59"),sQuery(id+"F2.wireOp",EDGE,"fcba4419-a2ee-464f-be9d-58f11bf3418b.sketch_text.stroke-60"),sQuery(id+"F2.wireOp",EDGE,"fcba4419-a2ee-464f-be9d-58f11bf3418b.sketch_text.stroke-61"),sQuery(id+"F2.wireOp",EDGE,"fcba4419-a2ee-464f-be9d-58f11bf3418b.sketch_text.stroke-62"),sQuery(id+"F2.wireOp",EDGE,"fcba4419-a2ee-464f-be9d-58f11bf3418b.sketch_text.stroke-63"),sQuery(id+"F2.wireOp",EDGE,"fcba4419-a2ee-464f-be9d-58f11bf3418b.sketch_text.stroke-64"),sQuery(id+"F2.wireOp",EDGE,"fcba4419-a2ee-464f-be9d-58f11bf3418b.sketch_text.stroke-65"),sQuery(id+"F2.wireOp",EDGE,"fcba4419-a2ee-464f-be9d-58f11bf3418b.sketch_text.stroke-66"),sQuery(id+"F2.wireOp",EDGE,"fcba4419-a2ee-464f-be9d-58f11bf3418b.sketch_text.stroke-67"),sQuery(id+"F2.wireOp",EDGE,"fcba4419-a2ee-464f-be9d-58f11bf3418b.sketch_text.stroke-68"),sQuery(id+"F2.wireOp",EDGE,"fcba4419-a2ee-464f-be9d-58f11bf3418b.sketch_text.stroke-69"),sQuery(id+"F2.wireOp",EDGE,"fcba4419-a2ee-464f-be9d-58f11bf3418b.sketch_text.stroke-70"),sQuery(id+"F2.wireOp",EDGE,"fcba4419-a2ee-464f-be9d-58f11bf3418b.sketch_text.stroke-71"),sQuery(id+"F2.wireOp",EDGE,"fcba4419-a2ee-464f-be9d-58f11bf3418b.sketch_text.stroke-72"),sQuery(id+"F2.wireOp",EDGE,"fcba4419-a2ee-464f-be9d-58f11bf3418b.sketch_text.stroke-73"),sQuery(id+"F2.wireOp",EDGE,"fcba4419-a2ee-464f-be9d-58f11bf3418b.sketch_text.stroke-74"),sQuery(id+"F2.wireOp",EDGE,"fcba4419-a2ee-464f-be9d-58f11bf3418b.sketch_text.stroke-75"),sQuery(id+"F2.wireOp",EDGE,"fcba4419-a2ee-464f-be9d-58f11bf3418b.sketch_text.stroke-76"),sQuery(id+"F2.wireOp",EDGE,"fcba4419-a2ee-464f-be9d-58f11bf3418b.sketch_text.stroke-77"),sQuery(id+"F2.wireOp",EDGE,"fcba4419-a2ee-464f-be9d-58f11bf3418b.sketch_text.stroke-78"),sQuery(id+"F2.wireOp",EDGE,"fcba4419-a2ee-464f-be9d-58f11bf3418b.sketch_text.stroke-79"),sQuery(id+"F2.wireOp",EDGE,"fcba4419-a2ee-464f-be9d-58f11bf3418b.sketch_text.stroke-80"),sQuery(id+"F2.wireOp",EDGE,"fcba4419-a2ee-464f-be9d-58f11bf3418b.sketch_text.stroke-81"),sQuery(id+"F2.wireOp",EDGE,"fcba4419-a2ee-464f-be9d-58f11bf3418b.sketch_text.stroke-82"),sQuery(id+"F2.wireOp",EDGE,"fcba4419-a2ee-464f-be9d-58f11bf3418b.sketch_text.stroke-83"),sQuery(id+"F2.wireOp",EDGE,"fcba4419-a2ee-464f-be9d-58f11bf3418b.sketch_text.stroke-84"),sQuery(id+"F2.wireOp",EDGE,"fcba4419-a2ee-464f-be9d-58f11bf3418b.sketch_text.stroke-85"),sQuery(id+"F2.wireOp",EDGE,"fcba4419-a2ee-464f-be9d-58f11bf3418b.sketch_text.stroke-86"),sQuery(id+"F2.wireOp",EDGE,"fcba4419-a2ee-464f-be9d-58f11bf3418b.sketch_text.stroke-87"),sQuery(id+"F2.wireOp",EDGE,"fcba4419-a2ee-464f-be9d-58f11bf3418b.sketch_text.stroke-88"),sQuery(id+"F2.wireOp",EDGE,"fcba4419-a2ee-464f-be9d-58f11bf3418b.sketch_text.stroke-89"),sQuery(id+"F2.wireOp",EDGE,"fcba4419-a2ee-464f-be9d-58f11bf3418b.sketch_text.stroke-90"),sQuery(id+"F2.wireOp",EDGE,"fcba4419-a2ee-464f-be9d-58f11bf3418b.sketch_text.stroke-91"),sQuery(id+"F2.wireOp",EDGE,"fcba4419-a2ee-464f-be9d-58f11bf3418b.sketch_text.stroke-92"),sQuery(id+"F2.wireOp",EDGE,"fcba4419-a2ee-464f-be9d-58f11bf3418b.sketch_text.stroke-93"),sQuery(id+"F2.wireOp",EDGE,"fcba4419-a2ee-464f-be9d-58f11bf3418b.sketch_text.stroke-94"),sQuery(id+"F2.wireOp",EDGE,"fcba4419-a2ee-464f-be9d-58f11bf3418b.sketch_text.stroke-95"),sQuery(id+"F2.wireOp",EDGE,"fcba4419-a2ee-464f-be9d-58f11bf3418b.sketch_text.stroke-96"),sQuery(id+"F2.wireOp",EDGE,"fcba4419-a2ee-464f-be9d-58f11bf3418b.sketch_text.stroke-97"),sQuery(id+"F2.wireOp",EDGE,"fcba4419-a2ee-464f-be9d-58f11bf3418b.sketch_text.stroke-98"),sQuery(id+"F2.wireOp",EDGE,"fcba4419-a2ee-464f-be9d-58f11bf3418b.sketch_text.stroke-99"),sQuery(id+"F2.wireOp",EDGE,"fcba4419-a2ee-464f-be9d-58f11bf3418b.sketch_text.stroke-100"),sQuery(id+"F2.wireOp",EDGE,"fcba4419-a2ee-464f-be9d-58f11bf3418b.sketch_text.stroke-101"),sQuery(id+"F2.wireOp",EDGE,"fcba4419-a2ee-464f-be9d-58f11bf3418b.sketch_text.stroke-102"),sQuery(id+"F2.wireOp",EDGE,"fcba4419-a2ee-464f-be9d-58f11bf3418b.sketch_text.stroke-103"),sQuery(id+"F2.wireOp",EDGE,"fcba4419-a2ee-464f-be9d-58f11bf3418b.sketch_text.stroke-104"),sQuery(id+"F2.wireOp",EDGE,"fcba4419-a2ee-464f-be9d-58f11bf3418b.sketch_text.stroke-105"),sQuery(id+"F2.wireOp",EDGE,"fcba4419-a2ee-464f-be9d-58f11bf3418b.sketch_text.stroke-106"),sQuery(id+"F2.wireOp",EDGE,"fcba4419-a2ee-464f-be9d-58f11bf3418b.sketch_text.stroke-107"),sQuery(id+"F2.wireOp",EDGE,"fcba4419-a2ee-464f-be9d-58f11bf3418b.sketch_text.stroke-108"),sQuery(id+"F2.wireOp",EDGE,"fcba4419-a2ee-464f-be9d-58f11bf3418b.sketch_text.stroke-109"),sQuery(id+"F2.wireOp",EDGE,"fcba4419-a2ee-464f-be9d-58f11bf3418b.sketch_text.stroke-110"),sQuery(id+"F2.wireOp",EDGE,"fcba4419-a2ee-464f-be9d-58f11bf3418b.sketch_text.stroke-111"),sQuery(id+"F2.wireOp",EDGE,"fcba4419-a2ee-464f-be9d-58f11bf3418b.sketch_text.stroke-112"),sQuery(id+"F2.wireOp",EDGE,"fcba4419-a2ee-464f-be9d-58f11bf3418b.sketch_text.stroke-113"),sQuery(id+"F2.wireOp",EDGE,"fcba4419-a2ee-464f-be9d-58f11bf3418b.sketch_text.stroke-114"),sQuery(id+"F2.wireOp",EDGE,"fcba4419-a2ee-464f-be9d-58f11bf3418b.sketch_text.stroke-115"),sQuery(id+"F2.wireOp",EDGE,"fcba4419-a2ee-464f-be9d-58f11bf3418b.sketch_text.stroke-116"),sQuery(id+"F2.wireOp",EDGE,"fcba4419-a2ee-464f-be9d-58f11bf3418b.sketch_text.stroke-117"),sQuery(id+"F2.wireOp",EDGE,"fcba4419-a2ee-464f-be9d-58f11bf3418b.sketch_text.stroke-118"),sQuery(id+"F2.wireOp",EDGE,"fcba4419-a2ee-464f-be9d-58f11bf3418b.sketch_text.stroke-119"),sQuery(id+"F2.wireOp",EDGE,"fcba4419-a2ee-464f-be9d-58f11bf3418b.sketch_text.stroke-120"),sQuery(id+"F2.wireOp",EDGE,"fcba4419-a2ee-464f-be9d-58f11bf3418b.sketch_text.stroke-121"),sQuery(id+"F2.wireOp",EDGE,"fcba4419-a2ee-464f-be9d-58f11bf3418b.sketch_text.stroke-122"),sQuery(id+"F2.wireOp",EDGE,"fcba4419-a2ee-464f-be9d-58f11bf3418b.sketch_text.stroke-123"),sQuery(id+"F2.wireOp",EDGE,"fcba4419-a2ee-464f-be9d-58f11bf3418b.sketch_text.stroke-124"),sQuery(id+"F2.wireOp",EDGE,"fcba4419-a2ee-464f-be9d-58f11bf3418b.sketch_text.stroke-125"),sQuery(id+"F2.wireOp",EDGE,"fcba4419-a2ee-464f-be9d-58f11bf3418b.sketch_text.stroke-126"),sQuery(id+"F2.wireOp",EDGE,"fcba4419-a2ee-464f-be9d-58f11bf3418b.sketch_text.stroke-127"),sQuery(id+"F2.wireOp",EDGE,"fcba4419-a2ee-464f-be9d-58f11bf3418b.sketch_text.stroke-128"),sQuery(id+"F2.wireOp",EDGE,"fcba4419-a2ee-464f-be9d-58f11bf3418b.sketch_text.stroke-129"),sQuery(id+"F2.wireOp",EDGE,"fcba4419-a2ee-464f-be9d-58f11bf3418b.sketch_text.stroke-130"),sQuery(id+"F2.wireOp",EDGE,"fcba4419-a2ee-464f-be9d-58f11bf3418b.sketch_text.stroke-131"),sQuery(id+"F2.wireOp",EDGE,"fcba4419-a2ee-464f-be9d-58f11bf3418b.sketch_text.stroke-132"),sQuery(id+"F2.wireOp",EDGE,"fcba4419-a2ee-464f-be9d-58f11bf3418b.sketch_text.stroke-133"),sQuery(id+"F2.wireOp",EDGE,"fcba4419-a2ee-464f-be9d-58f11bf3418b.sketch_text.stroke-134"),sQuery(id+"F2.wireOp",EDGE,"fcba4419-a2ee-464f-be9d-58f11bf3418b.sketch_text.stroke-135"),sQuery(id+"F2.wireOp",EDGE,"fcba4419-a2ee-464f-be9d-58f11bf3418b.sketch_text.stroke-136"),sQuery(id+"F2.wireOp",EDGE,"fcba4419-a2ee-464f-be9d-58f11bf3418b.sketch_text.stroke-137"),sQuery(id+"F2.wireOp",EDGE,"fcba4419-a2ee-464f-be9d-58f11bf3418b.sketch_text.stroke-138"),sQuery(id+"F2.wireOp",EDGE,"fcba4419-a2ee-464f-be9d-58f11bf3418b.sketch_text.stroke-139"),sQuery(id+"F2.wireOp",EDGE,"fcba4419-a2ee-464f-be9d-58f11bf3418b.sketch_text.stroke-140"),sQuery(id+"F2.wireOp",EDGE,"fcba4419-a2ee-464f-be9d-58f11bf3418b.sketch_text.stroke-141"),sQuery(id+"F2.wireOp",EDGE,"fcba4419-a2ee-464f-be9d-58f11bf3418b.sketch_text.stroke-142"),sQuery(id+"F2.wireOp",EDGE,"fcba4419-a2ee-464f-be9d-58f11bf3418b.sketch_text.stroke-143"),sQuery(id+"F2.wireOp",EDGE,"fcba4419-a2ee-464f-be9d-58f11bf3418b.sketch_text.stroke-144"),sQuery(id+"F2.wireOp",EDGE,"fcba4419-a2ee-464f-be9d-58f11bf3418b.sketch_text.stroke-145"),sQuery(id+"F2.wireOp",EDGE,"fcba4419-a2ee-464f-be9d-58f11bf3418b.sketch_text.stroke-146"),sQuery(id+"F2.wireOp",EDGE,"fcba4419-a2ee-464f-be9d-58f11bf3418b.sketch_text.stroke-147"),sQuery(id+"F2.wireOp",EDGE,"fcba4419-a2ee-464f-be9d-58f11bf3418b.sketch_text.stroke-148"),sQuery(id+"F2.wireOp",EDGE,"fcba4419-a2ee-464f-be9d-58f11bf3418b.sketch_text.stroke-149"),sQuery(id+"F2.wireOp",EDGE,"fcba4419-a2ee-464f-be9d-58f11bf3418b.sketch_text.stroke-150"),sQuery(id+"F2.wireOp",EDGE,"fcba4419-a2ee-464f-be9d-58f11bf3418b.sketch_text.stroke-151"),sQuery(id+"F2.wireOp",EDGE,"fcba4419-a2ee-464f-be9d-58f11bf3418b.sketch_text.stroke-152"),sQuery(id+"F2.wireOp",EDGE,"fcba4419-a2ee-464f-be9d-58f11bf3418b.sketch_text.stroke-153"),sQuery(id+"F2.wireOp",EDGE,"fcba4419-a2ee-464f-be9d-58f11bf3418b.sketch_text.stroke-154"),sQuery(id+"F2.wireOp",EDGE,"fcba4419-a2ee-464f-be9d-58f11bf3418b.sketch_text.stroke-155"),sQuery(id+"F2.wireOp",EDGE,"fcba4419-a2ee-464f-be9d-58f11bf3418b.sketch_text.stroke-156"),sQuery(id+"F2.wireOp",EDGE,"fcba4419-a2ee-464f-be9d-58f11bf3418b.sketch_text.stroke-157"),sQuery(id+"F2.wireOp",EDGE,"fcba4419-a2ee-464f-be9d-58f11bf3418b.sketch_text.stroke-158"),sQuery(id+"F2.wireOp",EDGE,"fcba4419-a2ee-464f-be9d-58f11bf3418b.sketch_text.stroke-159"),sQuery(id+"F2.wireOp",EDGE,"fcba4419-a2ee-464f-be9d-58f11bf3418b.sketch_text.stroke-160"),sQuery(id+"F2.wireOp",EDGE,"fcba4419-a2ee-464f-be9d-58f11bf3418b.sketch_text.stroke-161"),sQuery(id+"F2.wireOp",EDGE,"fcba4419-a2ee-464f-be9d-58f11bf3418b.sketch_text.stroke-162"),sQuery(id+"F2.wireOp",EDGE,"fcba4419-a2ee-464f-be9d-58f11bf3418b.sketch_text.stroke-163"),sQuery(id+"F2.wireOp",EDGE,"fcba4419-a2ee-464f-be9d-58f11bf3418b.sketch_text.stroke-164"),sQuery(id+"F2.wireOp",EDGE,"fcba4419-a2ee-464f-be9d-58f11bf3418b.sketch_text.stroke-165"),sQuery(id+"F2.wireOp",EDGE,"fcba4419-a2ee-464f-be9d-58f11bf3418b.sketch_text.stroke-166"),sQuery(id+"F2.wireOp",EDGE,"fcba4419-a2ee-464f-be9d-58f11bf3418b.sketch_text.stroke-167"),sQuery(id+"F2.wireOp",EDGE,"fcba4419-a2ee-464f-be9d-58f11bf3418b.sketch_text.stroke-168"),sQuery(id+"F2.wireOp",EDGE,"fcba4419-a2ee-464f-be9d-58f11bf3418b.sketch_text.stroke-169"),sQuery(id+"F2.wireOp",EDGE,"fcba4419-a2ee-464f-be9d-58f11bf3418b.sketch_text.stroke-170"),sQuery(id+"F2.wireOp",EDGE,"fcba4419-a2ee-464f-be9d-58f11bf3418b.sketch_text.stroke-171"),sQuery(id+"F2.wireOp",EDGE,"fcba4419-a2ee-464f-be9d-58f11bf3418b.sketch_text.stroke-172"),sQuery(id+"F2.wireOp",EDGE,"fcba4419-a2ee-464f-be9d-58f11bf3418b.sketch_text.stroke-173"),sQuery(id+"FHMxAyK4CFUKdhS_1.wireOp",EDGE,"1cb9c079-ea9b-4899-8069-e0e3048e911d.sketch_text.stroke-0"),sQuery(id+"FHMxAyK4CFUKdhS_1.wireOp",EDGE,"1cb9c079-ea9b-4899-8069-e0e3048e911d.sketch_text.stroke-1"),sQuery(id+"FHMxAyK4CFUKdhS_1.wireOp",EDGE,"1cb9c079-ea9b-4899-8069-e0e3048e911d.sketch_text.stroke-2"),sQuery(id+"FHMxAyK4CFUKdhS_1.wireOp",EDGE,"1cb9c079-ea9b-4899-8069-e0e3048e911d.sketch_text.stroke-3"),sQuery(id+"FHMxAyK4CFUKdhS_1.wireOp",EDGE,"1cb9c079-ea9b-4899-8069-e0e3048e911d.sketch_text.stroke-4"),sQuery(id+"FHMxAyK4CFUKdhS_1.wireOp",EDGE,"1cb9c079-ea9b-4899-8069-e0e3048e911d.sketch_text.stroke-5"),sQuery(id+"FHMxAyK4CFUKdhS_1.wireOp",EDGE,"1cb9c079-ea9b-4899-8069-e0e3048e911d.sketch_text.stroke-6"),sQuery(id+"FHMxAyK4CFUKdhS_1.wireOp",EDGE,"1cb9c079-ea9b-4899-8069-e0e3048e911d.sketch_text.stroke-7"),sQuery(id+"FHMxAyK4CFUKdhS_1.wireOp",EDGE,"1cb9c079-ea9b-4899-8069-e0e3048e911d.sketch_text.stroke-8"),sQuery(id+"FHMxAyK4CFUKdhS_1.wireOp",EDGE,"1cb9c079-ea9b-4899-8069-e0e3048e911d.sketch_text.stroke-9"),sQuery(id+"FHMxAyK4CFUKdhS_1.wireOp",EDGE,"1cb9c079-ea9b-4899-8069-e0e3048e911d.sketch_text.stroke-10"),sQuery(id+"FHMxAyK4CFUKdhS_1.wireOp",EDGE,"1cb9c079-ea9b-4899-8069-e0e3048e911d.sketch_text.stroke-11"),sQuery(id+"FHMxAyK4CFUKdhS_1.wireOp",EDGE,"1cb9c079-ea9b-4899-8069-e0e3048e911d.sketch_text.stroke-12"),sQuery(id+"FHMxAyK4CFUKdhS_1.wireOp",EDGE,"1cb9c079-ea9b-4899-8069-e0e3048e911d.sketch_text.stroke-13"),sQuery(id+"FHMxAyK4CFUKdhS_1.wireOp",EDGE,"1cb9c079-ea9b-4899-8069-e0e3048e911d.sketch_text.stroke-14"),sQuery(id+"FHMxAyK4CFUKdhS_1.wireOp",EDGE,"1cb9c079-ea9b-4899-8069-e0e3048e911d.sketch_text.stroke-15"),sQuery(id+"FHMxAyK4CFUKdhS_1.wireOp",EDGE,"1cb9c079-ea9b-4899-8069-e0e3048e911d.sketch_text.stroke-16"),sQuery(id+"FHMxAyK4CFUKdhS_1.wireOp",EDGE,"1cb9c079-ea9b-4899-8069-e0e3048e911d.sketch_text.stroke-17"),sQuery(id+"FHMxAyK4CFUKdhS_1.wireOp",EDGE,"1cb9c079-ea9b-4899-8069-e0e3048e911d.sketch_text.stroke-18"),sQuery(id+"FHMxAyK4CFUKdhS_1.wireOp",EDGE,"1cb9c079-ea9b-4899-8069-e0e3048e911d.sketch_text.stroke-19"),sQuery(id+"FHMxAyK4CFUKdhS_1.wireOp",EDGE,"1cb9c079-ea9b-4899-8069-e0e3048e911d.sketch_text.stroke-20"),sQuery(id+"FHMxAyK4CFUKdhS_1.wireOp",EDGE,"1cb9c079-ea9b-4899-8069-e0e3048e911d.sketch_text.stroke-21"),sQuery(id+"FHMxAyK4CFUKdhS_1.wireOp",EDGE,"1cb9c079-ea9b-4899-8069-e0e3048e911d.sketch_text.stroke-22"),sQuery(id+"FHMxAyK4CFUKdhS_1.wireOp",EDGE,"1cb9c079-ea9b-4899-8069-e0e3048e911d.sketch_text.stroke-23"),sQuery(id+"FHMxAyK4CFUKdhS_1.wireOp",EDGE,"1cb9c079-ea9b-4899-8069-e0e3048e911d.sketch_text.stroke-24"),sQuery(id+"FHMxAyK4CFUKdhS_1.wireOp",EDGE,"1cb9c079-ea9b-4899-8069-e0e3048e911d.sketch_text.stroke-25"),sQuery(id+"FHMxAyK4CFUKdhS_1.wireOp",EDGE,"1cb9c079-ea9b-4899-8069-e0e3048e911d.sketch_text.stroke-26"),sQuery(id+"FHMxAyK4CFUKdhS_1.wireOp",EDGE,"1cb9c079-ea9b-4899-8069-e0e3048e911d.sketch_text.stroke-27"),sQuery(id+"FHMxAyK4CFUKdhS_1.wireOp",EDGE,"1cb9c079-ea9b-4899-8069-e0e3048e911d.sketch_text.stroke-28"),sQuery(id+"FHMxAyK4CFUKdhS_1.wireOp",EDGE,"1cb9c079-ea9b-4899-8069-e0e3048e911d.sketch_text.stroke-29"),sQuery(id+"FHMxAyK4CFUKdhS_1.wireOp",EDGE,"1cb9c079-ea9b-4899-8069-e0e3048e911d.sketch_text.stroke-30"),sQuery(id+"FHMxAyK4CFUKdhS_1.wireOp",EDGE,"1cb9c079-ea9b-4899-8069-e0e3048e911d.sketch_text.stroke-31"),sQuery(id+"FHMxAyK4CFUKdhS_1.wireOp",EDGE,"1cb9c079-ea9b-4899-8069-e0e3048e911d.sketch_text.stroke-32"),sQuery(id+"FHMxAyK4CFUKdhS_1.wireOp",EDGE,"1cb9c079-ea9b-4899-8069-e0e3048e911d.sketch_text.stroke-33"),sQuery(id+"FHMxAyK4CFUKdhS_1.wireOp",EDGE,"1cb9c079-ea9b-4899-8069-e0e3048e911d.sketch_text.stroke-34"),sQuery(id+"FHMxAyK4CFUKdhS_1.wireOp",EDGE,"1cb9c079-ea9b-4899-8069-e0e3048e911d.sketch_text.stroke-35"),sQuery(id+"FHMxAyK4CFUKdhS_1.wireOp",EDGE,"1cb9c079-ea9b-4899-8069-e0e3048e911d.sketch_text.stroke-36"),sQuery(id+"FHMxAyK4CFUKdhS_1.wireOp",EDGE,"1cb9c079-ea9b-4899-8069-e0e3048e911d.sketch_text.stroke-37"),sQuery(id+"FHMxAyK4CFUKdhS_1.wireOp",EDGE,"1cb9c079-ea9b-4899-8069-e0e3048e911d.sketch_text.stroke-38"),sQuery(id+"FHMxAyK4CFUKdhS_1.wireOp",EDGE,"1cb9c079-ea9b-4899-8069-e0e3048e911d.sketch_text.stroke-39"),sQuery(id+"FHMxAyK4CFUKdhS_1.wireOp",EDGE,"1cb9c079-ea9b-4899-8069-e0e3048e911d.sketch_text.stroke-40"),sQuery(id+"FHMxAyK4CFUKdhS_1.wireOp",EDGE,"1cb9c079-ea9b-4899-8069-e0e3048e911d.sketch_text.stroke-41"),sQuery(id+"FHMxAyK4CFUKdhS_1.wireOp",EDGE,"1cb9c079-ea9b-4899-8069-e0e3048e911d.sketch_text.stroke-42"),sQuery(id+"FHMxAyK4CFUKdhS_1.wireOp",EDGE,"1cb9c079-ea9b-4899-8069-e0e3048e911d.sketch_text.stroke-43"),sQuery(id+"FHMxAyK4CFUKdhS_1.wireOp",EDGE,"1cb9c079-ea9b-4899-8069-e0e3048e911d.sketch_text.stroke-44"),sQuery(id+"FHMxAyK4CFUKdhS_1.wireOp",EDGE,"1cb9c079-ea9b-4899-8069-e0e3048e911d.sketch_text.stroke-45"),sQuery(id+"FHMxAyK4CFUKdhS_1.wireOp",EDGE,"1cb9c079-ea9b-4899-8069-e0e3048e911d.sketch_text.stroke-46"),sQuery(id+"FHMxAyK4CFUKdhS_1.wireOp",EDGE,"1cb9c079-ea9b-4899-8069-e0e3048e911d.sketch_text.stroke-47"),sQuery(id+"FHMxAyK4CFUKdhS_1.wireOp",EDGE,"1cb9c079-ea9b-4899-8069-e0e3048e911d.sketch_text.stroke-48"),sQuery(id+"FHMxAyK4CFUKdhS_1.wireOp",EDGE,"1cb9c079-ea9b-4899-8069-e0e3048e911d.sketch_text.stroke-49"),sQuery(id+"FHMxAyK4CFUKdhS_1.wireOp",EDGE,"1cb9c079-ea9b-4899-8069-e0e3048e911d.sketch_text.stroke-50"),sQuery(id+"FHMxAyK4CFUKdhS_1.wireOp",EDGE,"1cb9c079-ea9b-4899-8069-e0e3048e911d.sketch_text.stroke-51"),sQuery(id+"FHMxAyK4CFUKdhS_1.wireOp",EDGE,"1cb9c079-ea9b-4899-8069-e0e3048e911d.sketch_text.stroke-52"),sQuery(id+"FHMxAyK4CFUKdhS_1.wireOp",EDGE,"1cb9c079-ea9b-4899-8069-e0e3048e911d.sketch_text.stroke-53"),sQuery(id+"FHMxAyK4CFUKdhS_1.wireOp",EDGE,"1cb9c079-ea9b-4899-8069-e0e3048e911d.sketch_text.stroke-54"),sQuery(id+"FHMxAyK4CFUKdhS_1.wireOp",EDGE,"1cb9c079-ea9b-4899-8069-e0e3048e911d.sketch_text.stroke-55"),sQuery(id+"FHMxAyK4CFUKdhS_1.wireOp",EDGE,"1cb9c079-ea9b-4899-8069-e0e3048e911d.sketch_text.stroke-56"),sQuery(id+"FHMxAyK4CFUKdhS_1.wireOp",EDGE,"1cb9c079-ea9b-4899-8069-e0e3048e911d.sketch_text.stroke-57"),sQuery(id+"FHMxAyK4CFUKdhS_1.wireOp",EDGE,"1cb9c079-ea9b-4899-8069-e0e3048e911d.sketch_text.stroke-58"),sQuery(id+"FHMxAyK4CFUKdhS_1.wireOp",EDGE,"1cb9c079-ea9b-4899-8069-e0e3048e911d.sketch_text.stroke-59"),sQuery(id+"FHMxAyK4CFUKdhS_1.wireOp",EDGE,"1cb9c079-ea9b-4899-8069-e0e3048e911d.sketch_text.stroke-60"),sQuery(id+"FHMxAyK4CFUKdhS_1.wireOp",EDGE,"1cb9c079-ea9b-4899-8069-e0e3048e911d.sketch_text.stroke-61"),sQuery(id+"FHMxAyK4CFUKdhS_1.wireOp",EDGE,"1cb9c079-ea9b-4899-8069-e0e3048e911d.sketch_text.stroke-62"),sQuery(id+"FHMxAyK4CFUKdhS_1.wireOp",EDGE,"1cb9c079-ea9b-4899-8069-e0e3048e911d.sketch_text.stroke-71"),sQuery(id+"FHMxAyK4CFUKdhS_1.wireOp",EDGE,"1cb9c079-ea9b-4899-8069-e0e3048e911d.sketch_text.stroke-72"),sQuery(id+"FHMxAyK4CFUKdhS_1.wireOp",EDGE,"1cb9c079-ea9b-4899-8069-e0e3048e911d.sketch_text.stroke-73"),sQuery(id+"FHMxAyK4CFUKdhS_1.wireOp",EDGE,"1cb9c079-ea9b-4899-8069-e0e3048e911d.sketch_text.stroke-74"),sQuery(id+"FHMxAyK4CFUKdhS_1.wireOp",EDGE,"1cb9c079-ea9b-4899-8069-e0e3048e911d.sketch_text.stroke-75"),sQuery(id+"FHMxAyK4CFUKdhS_1.wireOp",EDGE,"1cb9c079-ea9b-4899-8069-e0e3048e911d.sketch_text.stroke-76"),sQuery(id+"FHMxAyK4CFUKdhS_1.wireOp",EDGE,"1cb9c079-ea9b-4899-8069-e0e3048e911d.sketch_text.stroke-77"),sQuery(id+"FHMxAyK4CFUKdhS_1.wireOp",EDGE,"1cb9c079-ea9b-4899-8069-e0e3048e911d.sketch_text.stroke-78"),sQuery(id+"FHMxAyK4CFUKdhS_1.wireOp",EDGE,"1cb9c079-ea9b-4899-8069-e0e3048e911d.sketch_text.stroke-79"),sQuery(id+"FHMxAyK4CFUKdhS_1.wireOp",EDGE,"1cb9c079-ea9b-4899-8069-e0e3048e911d.sketch_text.stroke-80"),sQuery(id+"FHMxAyK4CFUKdhS_1.wireOp",EDGE,"1cb9c079-ea9b-4899-8069-e0e3048e911d.sketch_text.stroke-81"),sQuery(id+"FHMxAyK4CFUKdhS_1.wireOp",EDGE,"1cb9c079-ea9b-4899-8069-e0e3048e911d.sketch_text.stroke-82"),sQuery(id+"FHMxAyK4CFUKdhS_1.wireOp",EDGE,"1cb9c079-ea9b-4899-8069-e0e3048e911d.sketch_text.stroke-83"),sQuery(id+"FHMxAyK4CFUKdhS_1.wireOp",EDGE,"1cb9c079-ea9b-4899-8069-e0e3048e911d.sketch_text.stroke-84"),sQuery(id+"FHMxAyK4CFUKdhS_1.wireOp",EDGE,"1cb9c079-ea9b-4899-8069-e0e3048e911d.sketch_text.stroke-85"),sQuery(id+"FHMxAyK4CFUKdhS_1.wireOp",EDGE,"1cb9c079-ea9b-4899-8069-e0e3048e911d.sketch_text.stroke-86"),sQuery(id+"FHMxAyK4CFUKdhS_1.wireOp",EDGE,"1cb9c079-ea9b-4899-8069-e0e3048e911d.sketch_text.stroke-87"),sQuery(id+"FHMxAyK4CFUKdhS_1.wireOp",EDGE,"1cb9c079-ea9b-4899-8069-e0e3048e911d.sketch_text.stroke-88"),sQuery(id+"FHMxAyK4CFUKdhS_1.wireOp",EDGE,"1cb9c079-ea9b-4899-8069-e0e3048e911d.sketch_text.stroke-89"),sQuery(id+"FHMxAyK4CFUKdhS_1.wireOp",EDGE,"1cb9c079-ea9b-4899-8069-e0e3048e911d.sketch_text.stroke-90"),sQuery(id+"FHMxAyK4CFUKdhS_1.wireOp",EDGE,"1cb9c079-ea9b-4899-8069-e0e3048e911d.sketch_text.stroke-91"),sQuery(id+"FHMxAyK4CFUKdhS_1.wireOp",EDGE,"1cb9c079-ea9b-4899-8069-e0e3048e911d.sketch_text.stroke-92"),sQuery(id+"FHMxAyK4CFUKdhS_1.wireOp",EDGE,"1cb9c079-ea9b-4899-8069-e0e3048e911d.sketch_text.stroke-93"),sQuery(id+"FHMxAyK4CFUKdhS_1.wireOp",EDGE,"1cb9c079-ea9b-4899-8069-e0e3048e911d.sketch_text.stroke-94"),sQuery(id+"FHMxAyK4CFUKdhS_1.wireOp",EDGE,"1cb9c079-ea9b-4899-8069-e0e3048e911d.sketch_text.stroke-95"),sQuery(id+"FHMxAyK4CFUKdhS_1.wireOp",EDGE,"1cb9c079-ea9b-4899-8069-e0e3048e911d.sketch_text.stroke-96"),sQuery(id+"FHMxAyK4CFUKdhS_1.wireOp",EDGE,"1cb9c079-ea9b-4899-8069-e0e3048e911d.sketch_text.stroke-97"),sQuery(id+"FHMxAyK4CFUKdhS_1.wireOp",EDGE,"1cb9c079-ea9b-4899-8069-e0e3048e911d.sketch_text.stroke-103"),sQuery(id+"FHMxAyK4CFUKdhS_1.wireOp",EDGE,"1cb9c079-ea9b-4899-8069-e0e3048e911d.sketch_text.stroke-104"),sQuery(id+"FHMxAyK4CFUKdhS_1.wireOp",EDGE,"1cb9c079-ea9b-4899-8069-e0e3048e911d.sketch_text.stroke-105"),sQuery(id+"FHMxAyK4CFUKdhS_1.wireOp",EDGE,"1cb9c079-ea9b-4899-8069-e0e3048e911d.sketch_text.stroke-106"),sQuery(id+"FHMxAyK4CFUKdhS_1.wireOp",EDGE,"1cb9c079-ea9b-4899-8069-e0e3048e911d.sketch_text.stroke-107"),sQuery(id+"FHMxAyK4CFUKdhS_1.wireOp",EDGE,"1cb9c079-ea9b-4899-8069-e0e3048e911d.sketch_text.stroke-108"),sQuery(id+"FHMxAyK4CFUKdhS_1.wireOp",EDGE,"1cb9c079-ea9b-4899-8069-e0e3048e911d.sketch_text.stroke-109"),sQuery(id+"FHMxAyK4CFUKdhS_1.wireOp",EDGE,"1cb9c079-ea9b-4899-8069-e0e3048e911d.sketch_text.stroke-110"),sQuery(id+"FHMxAyK4CFUKdhS_1.wireOp",EDGE,"1cb9c079-ea9b-4899-8069-e0e3048e911d.sketch_text.stroke-111"),sQuery(id+"FHMxAyK4CFUKdhS_1.wireOp",EDGE,"1cb9c079-ea9b-4899-8069-e0e3048e911d.sketch_text.stroke-112"),sQuery(id+"FHMxAyK4CFUKdhS_1.wireOp",EDGE,"1cb9c079-ea9b-4899-8069-e0e3048e911d.sketch_text.stroke-113"),sQuery(id+"FHMxAyK4CFUKdhS_1.wireOp",EDGE,"1cb9c079-ea9b-4899-8069-e0e3048e911d.sketch_text.stroke-114"),sQuery(id+"FHMxAyK4CFUKdhS_1.wireOp",EDGE,"1cb9c079-ea9b-4899-8069-e0e3048e911d.sketch_text.stroke-115"),sQuery(id+"FHMxAyK4CFUKdhS_1.wireOp",EDGE,"1cb9c079-ea9b-4899-8069-e0e3048e911d.sketch_text.stroke-116"),sQuery(id+"FHMxAyK4CFUKdhS_1.wireOp",EDGE,"1cb9c079-ea9b-4899-8069-e0e3048e911d.sketch_text.stroke-117"),sQuery(id+"FHMxAyK4CFUKdhS_1.wireOp",EDGE,"1cb9c079-ea9b-4899-8069-e0e3048e911d.sketch_text.stroke-118"),sQuery(id+"FHMxAyK4CFUKdhS_1.wireOp",EDGE,"1cb9c079-ea9b-4899-8069-e0e3048e911d.sketch_text.stroke-119"),sQuery(id+"FHMxAyK4CFUKdhS_1.wireOp",EDGE,"1cb9c079-ea9b-4899-8069-e0e3048e911d.sketch_text.stroke-120"),sQuery(id+"FHMxAyK4CFUKdhS_1.wireOp",EDGE,"1cb9c079-ea9b-4899-8069-e0e3048e911d.sketch_text.stroke-121"),sQuery(id+"FHMxAyK4CFUKdhS_1.wireOp",EDGE,"1cb9c079-ea9b-4899-8069-e0e3048e911d.sketch_text.stroke-122"),sQuery(id+"FHMxAyK4CFUKdhS_1.wireOp",EDGE,"1cb9c079-ea9b-4899-8069-e0e3048e911d.sketch_text.stroke-123"),sQuery(id+"FHMxAyK4CFUKdhS_1.wireOp",EDGE,"1cb9c079-ea9b-4899-8069-e0e3048e911d.sketch_text.stroke-124"),sQuery(id+"FHMxAyK4CFUKdhS_1.wireOp",EDGE,"1cb9c079-ea9b-4899-8069-e0e3048e911d.sketch_text.stroke-125"),sQuery(id+"FHMxAyK4CFUKdhS_1.wireOp",EDGE,"1cb9c079-ea9b-4899-8069-e0e3048e911d.sketch_text.stroke-126"),sQuery(id+"FHMxAyK4CFUKdhS_1.wireOp",EDGE,"1cb9c079-ea9b-4899-8069-e0e3048e911d.sketch_text.stroke-127"),sQuery(id+"FHMxAyK4CFUKdhS_1.wireOp",EDGE,"1cb9c079-ea9b-4899-8069-e0e3048e911d.sketch_text.stroke-128"),sQuery(id+"FHMxAyK4CFUKdhS_1.wireOp",EDGE,"1cb9c079-ea9b-4899-8069-e0e3048e911d.sketch_text.stroke-129"),sQuery(id+"FHMxAyK4CFUKdhS_1.wireOp",EDGE,"1cb9c079-ea9b-4899-8069-e0e3048e911d.sketch_text.stroke-130"),sQuery(id+"FHMxAyK4CFUKdhS_1.wireOp",EDGE,"1cb9c079-ea9b-4899-8069-e0e3048e911d.sketch_text.stroke-131"),sQuery(id+"FHMxAyK4CFUKdhS_1.wireOp",EDGE,"1cb9c079-ea9b-4899-8069-e0e3048e911d.sketch_text.stroke-132"),sQuery(id+"FHMxAyK4CFUKdhS_1.wireOp",EDGE,"1cb9c079-ea9b-4899-8069-e0e3048e911d.sketch_text.stroke-133"),sQuery(id+"FHMxAyK4CFUKdhS_1.wireOp",EDGE,"1cb9c079-ea9b-4899-8069-e0e3048e911d.sketch_text.stroke-134"),sQuery(id+"FHMxAyK4CFUKdhS_1.wireOp",EDGE,"1cb9c079-ea9b-4899-8069-e0e3048e911d.sketch_text.stroke-135"),sQuery(id+"FHMxAyK4CFUKdhS_1.wireOp",EDGE,"1cb9c079-ea9b-4899-8069-e0e3048e911d.sketch_text.stroke-136"),sQuery(id+"FHMxAyK4CFUKdhS_1.wireOp",EDGE,"1cb9c079-ea9b-4899-8069-e0e3048e911d.sketch_text.stroke-137"),sQuery(id+"FHMxAyK4CFUKdhS_1.wireOp",EDGE,"1cb9c079-ea9b-4899-8069-e0e3048e911d.sketch_text.stroke-138"),sQuery(id+"FHMxAyK4CFUKdhS_1.wireOp",EDGE,"1cb9c079-ea9b-4899-8069-e0e3048e911d.sketch_text.stroke-139"),sQuery(id+"FHMxAyK4CFUKdhS_1.wireOp",EDGE,"1cb9c079-ea9b-4899-8069-e0e3048e911d.sketch_text.stroke-140"),sQuery(id+"FHMxAyK4CFUKdhS_1.wireOp",EDGE,"1cb9c079-ea9b-4899-8069-e0e3048e911d.sketch_text.stroke-141"),sQuery(id+"FHMxAyK4CFUKdhS_1.wireOp",EDGE,"1cb9c079-ea9b-4899-8069-e0e3048e911d.sketch_text.stroke-142"),sQuery(id+"FHMxAyK4CFUKdhS_1.wireOp",EDGE,"1cb9c079-ea9b-4899-8069-e0e3048e911d.sketch_text.stroke-143"),sQuery(id+"FHMxAyK4CFUKdhS_1.wireOp",EDGE,"1cb9c079-ea9b-4899-8069-e0e3048e911d.sketch_text.stroke-144"),sQuery(id+"FHMxAyK4CFUKdhS_1.wireOp",EDGE,"1cb9c079-ea9b-4899-8069-e0e3048e911d.sketch_text.stroke-145"),sQuery(id+"FHMxAyK4CFUKdhS_1.wireOp",EDGE,"1cb9c079-ea9b-4899-8069-e0e3048e911d.sketch_text.stroke-146"),sQuery(id+"FHMxAyK4CFUKdhS_1.wireOp",EDGE,"1cb9c079-ea9b-4899-8069-e0e3048e911d.sketch_text.stroke-147"),sQuery(id+"FHMxAyK4CFUKdhS_1.wireOp",EDGE,"1cb9c079-ea9b-4899-8069-e0e3048e911d.sketch_text.stroke-148"),sQuery(id+"FHMxAyK4CFUKdhS_1.wireOp",EDGE,"1cb9c079-ea9b-4899-8069-e0e3048e911d.sketch_text.stroke-149"),sQuery(id+"FHMxAyK4CFUKdhS_1.wireOp",EDGE,"1cb9c079-ea9b-4899-8069-e0e3048e911d.sketch_text.stroke-150"),sQuery(id+"FHMxAyK4CFUKdhS_1.wireOp",EDGE,"1cb9c079-ea9b-4899-8069-e0e3048e911d.sketch_text.stroke-151"),sQuery(id+"FHMxAyK4CFUKdhS_1.wireOp",EDGE,"1cb9c079-ea9b-4899-8069-e0e3048e911d.sketch_text.stroke-152"),sQuery(id+"FHMxAyK4CFUKdhS_1.wireOp",EDGE,"1cb9c079-ea9b-4899-8069-e0e3048e911d.sketch_text.stroke-153"),sQuery(id+"FHMxAyK4CFUKdhS_1.wireOp",EDGE,"1cb9c079-ea9b-4899-8069-e0e3048e911d.sketch_text.stroke-159"),sQuery(id+"FHMxAyK4CFUKdhS_1.wireOp",EDGE,"1cb9c079-ea9b-4899-8069-e0e3048e911d.sketch_text.stroke-160"),sQuery(id+"FHMxAyK4CFUKdhS_1.wireOp",EDGE,"1cb9c079-ea9b-4899-8069-e0e3048e911d.sketch_text.stroke-161"),sQuery(id+"FHMxAyK4CFUKdhS_1.wireOp",EDGE,"1cb9c079-ea9b-4899-8069-e0e3048e911d.sketch_text.stroke-162"),sQuery(id+"FHMxAyK4CFUKdhS_1.wireOp",EDGE,"1cb9c079-ea9b-4899-8069-e0e3048e911d.sketch_text.stroke-163"),sQuery(id+"FHMxAyK4CFUKdhS_1.wireOp",EDGE,"1cb9c079-ea9b-4899-8069-e0e3048e911d.sketch_text.stroke-164"),sQuery(id+"FHMxAyK4CFUKdhS_1.wireOp",EDGE,"1cb9c079-ea9b-4899-8069-e0e3048e911d.sketch_text.stroke-165"),sQuery(id+"FHMxAyK4CFUKdhS_1.wireOp",EDGE,"1cb9c079-ea9b-4899-8069-e0e3048e911d.sketch_text.stroke-166"),sQuery(id+"FHMxAyK4CFUKdhS_1.wireOp",EDGE,"1cb9c079-ea9b-4899-8069-e0e3048e911d.sketch_text.stroke-167"),sQuery(id+"FHMxAyK4CFUKdhS_1.wireOp",EDGE,"1cb9c079-ea9b-4899-8069-e0e3048e911d.sketch_text.stroke-168"),sQuery(id+"FHMxAyK4CFUKdhS_1.wireOp",EDGE,"1cb9c079-ea9b-4899-8069-e0e3048e911d.sketch_text.stroke-169"),sQuery(id+"FHMxAyK4CFUKdhS_1.wireOp",EDGE,"1cb9c079-ea9b-4899-8069-e0e3048e911d.sketch_text.stroke-170"),sQuery(id+"FHMxAyK4CFUKdhS_1.wireOp",EDGE,"1cb9c079-ea9b-4899-8069-e0e3048e911d.sketch_text.stroke-171"),sQuery(id+"FHMxAyK4CFUKdhS_1.wireOp",EDGE,"1cb9c079-ea9b-4899-8069-e0e3048e911d.sketch_text.stroke-172"),sQuery(id+"FHMxAyK4CFUKdhS_1.wireOp",EDGE,"1cb9c079-ea9b-4899-8069-e0e3048e911d.sketch_text.stroke-173"),sQuery(id+"FHMxAyK4CFUKdhS_1.wireOp",EDGE,"1cb9c079-ea9b-4899-8069-e0e3048e911d.sketch_text.stroke-174"),sQuery(id+"FHMxAyK4CFUKdhS_1.wireOp",EDGE,"1cb9c079-ea9b-4899-8069-e0e3048e911d.sketch_text.stroke-175"),sQuery(id+"FHMxAyK4CFUKdhS_1.wireOp",EDGE,"1cb9c079-ea9b-4899-8069-e0e3048e911d.sketch_text.stroke-176"),sQuery(id+"FHMxAyK4CFUKdhS_1.wireOp",EDGE,"1cb9c079-ea9b-4899-8069-e0e3048e911d.sketch_text.stroke-177"),sQuery(id+"FHMxAyK4CFUKdhS_1.wireOp",EDGE,"1cb9c079-ea9b-4899-8069-e0e3048e911d.sketch_text.stroke-178"),sQuery(id+"FHMxAyK4CFUKdhS_1.wireOp",EDGE,"1cb9c079-ea9b-4899-8069-e0e3048e911d.sketch_text.stroke-179"),sQuery(id+"FHMxAyK4CFUKdhS_1.wireOp",EDGE,"1cb9c079-ea9b-4899-8069-e0e3048e911d.sketch_text.stroke-180"),sQuery(id+"F3.wireOp",EDGE,"8007402e-1a4e-4a06-85a5-2af08e553504"),subQ2])],"isStart":true}),makeQuery(id+"F4.opExtrude","SWEPT_FACE",FACE,{"disambiguationData":[OSD([subQ2])]})]),OD(1.0)],"derivedFrom":makeQuery(id+"F1.opExtrude","CAP_EDGE",EDGE,{"disambiguationData":[OSD([subQ0])],"isStart":false})});}
            var Q15;
            {var subQ0=sQuery(id+"F3.wireOp",EDGE,"8007402e-1a4e-4a06-85a5-2af08e553504");var subQ1=sQuery(id+"F0.wireOp",EDGE,"E0.top");var subQ2=sQuery(id+"F3.wireOp",EDGE,"727ac2c1-f511-4829-95a7-a443ef16a4cd");var subQ3=sQuery(id+"F0.wireOp",EDGE,"E0.bottom");Q15=makeQuery(id+"F4.boolean.opBoolean","SPLIT",EDGE,{"disambiguationData":[TD([makeQuery(id+"F1.opExtrude","CAP_FACE",FACE,{"disambiguationData":[OSD([subQ3,subQ1,sQuery(id+"F0.wireOp",EDGE,"E0.left"),sQuery(id+"F0.wireOp",EDGE,"E0.right")])],"isStart":false}),makeQuery(id+"F1.opExtrude","SWEPT_FACE",FACE,{"disambiguationData":[OSD([subQ1])]}),makeQuery(id+"F4.opExtrude","SWEPT_FACE",FACE,{"disambiguationData":[OSD([subQ0])]}),makeQuery(id+"F4.opExtrude","CAP_FACE",FACE,{"disambiguationData":[OSD([subQ3,sQuery(id+"F2.wireOp",EDGE,"fcba4419-a2ee-464f-be9d-58f11bf3418b.sketch_text.stroke-0"),sQuery(id+"F2.wireOp",EDGE,"fcba4419-a2ee-464f-be9d-58f11bf3418b.sketch_text.stroke-1"),sQuery(id+"F2.wireOp",EDGE,"fcba4419-a2ee-464f-be9d-58f11bf3418b.sketch_text.stroke-2"),sQuery(id+"F2.wireOp",EDGE,"fcba4419-a2ee-464f-be9d-58f11bf3418b.sketch_text.stroke-3"),sQuery(id+"F2.wireOp",EDGE,"fcba4419-a2ee-464f-be9d-58f11bf3418b.sketch_text.stroke-4"),sQuery(id+"F2.wireOp",EDGE,"fcba4419-a2ee-464f-be9d-58f11bf3418b.sketch_text.stroke-5"),sQuery(id+"F2.wireOp",EDGE,"fcba4419-a2ee-464f-be9d-58f11bf3418b.sketch_text.stroke-6"),sQuery(id+"F2.wireOp",EDGE,"fcba4419-a2ee-464f-be9d-58f11bf3418b.sketch_text.stroke-7"),sQuery(id+"F2.wireOp",EDGE,"fcba4419-a2ee-464f-be9d-58f11bf3418b.sketch_text.stroke-8"),sQuery(id+"F2.wireOp",EDGE,"fcba4419-a2ee-464f-be9d-58f11bf3418b.sketch_text.stroke-9"),sQuery(id+"F2.wireOp",EDGE,"fcba4419-a2ee-464f-be9d-58f11bf3418b.sketch_text.stroke-10"),sQuery(id+"F2.wireOp",EDGE,"fcba4419-a2ee-464f-be9d-58f11bf3418b.sketch_text.stroke-11"),sQuery(id+"F2.wireOp",EDGE,"fcba4419-a2ee-464f-be9d-58f11bf3418b.sketch_text.stroke-12"),sQuery(id+"F2.wireOp",EDGE,"fcba4419-a2ee-464f-be9d-58f11bf3418b.sketch_text.stroke-13"),sQuery(id+"F2.wireOp",EDGE,"fcba4419-a2ee-464f-be9d-58f11bf3418b.sketch_text.stroke-14"),sQuery(id+"F2.wireOp",EDGE,"fcba4419-a2ee-464f-be9d-58f11bf3418b.sketch_text.stroke-15"),sQuery(id+"F2.wireOp",EDGE,"fcba4419-a2ee-464f-be9d-58f11bf3418b.sketch_text.stroke-16"),sQuery(id+"F2.wireOp",EDGE,"fcba4419-a2ee-464f-be9d-58f11bf3418b.sketch_text.stroke-17"),sQuery(id+"F2.wireOp",EDGE,"fcba4419-a2ee-464f-be9d-58f11bf3418b.sketch_text.stroke-18"),sQuery(id+"F2.wireOp",EDGE,"fcba4419-a2ee-464f-be9d-58f11bf3418b.sketch_text.stroke-19"),sQuery(id+"F2.wireOp",EDGE,"fcba4419-a2ee-464f-be9d-58f11bf3418b.sketch_text.stroke-20"),sQuery(id+"F2.wireOp",EDGE,"fcba4419-a2ee-464f-be9d-58f11bf3418b.sketch_text.stroke-21"),sQuery(id+"F2.wireOp",EDGE,"fcba4419-a2ee-464f-be9d-58f11bf3418b.sketch_text.stroke-22"),sQuery(id+"F2.wireOp",EDGE,"fcba4419-a2ee-464f-be9d-58f11bf3418b.sketch_text.stroke-23"),sQuery(id+"F2.wireOp",EDGE,"fcba4419-a2ee-464f-be9d-58f11bf3418b.sketch_text.stroke-24"),sQuery(id+"F2.wireOp",EDGE,"fcba4419-a2ee-464f-be9d-58f11bf3418b.sketch_text.stroke-25"),sQuery(id+"F2.wireOp",EDGE,"fcba4419-a2ee-464f-be9d-58f11bf3418b.sketch_text.stroke-26"),sQuery(id+"F2.wireOp",EDGE,"fcba4419-a2ee-464f-be9d-58f11bf3418b.sketch_text.stroke-27"),sQuery(id+"F2.wireOp",EDGE,"fcba4419-a2ee-464f-be9d-58f11bf3418b.sketch_text.stroke-28"),sQuery(id+"F2.wireOp",EDGE,"fcba4419-a2ee-464f-be9d-58f11bf3418b.sketch_text.stroke-29"),sQuery(id+"F2.wireOp",EDGE,"fcba4419-a2ee-464f-be9d-58f11bf3418b.sketch_text.stroke-30"),sQuery(id+"F2.wireOp",EDGE,"fcba4419-a2ee-464f-be9d-58f11bf3418b.sketch_text.stroke-31"),sQuery(id+"F2.wireOp",EDGE,"fcba4419-a2ee-464f-be9d-58f11bf3418b.sketch_text.stroke-32"),sQuery(id+"F2.wireOp",EDGE,"fcba4419-a2ee-464f-be9d-58f11bf3418b.sketch_text.stroke-33"),sQuery(id+"F2.wireOp",EDGE,"fcba4419-a2ee-464f-be9d-58f11bf3418b.sketch_text.stroke-34"),sQuery(id+"F2.wireOp",EDGE,"fcba4419-a2ee-464f-be9d-58f11bf3418b.sketch_text.stroke-35"),sQuery(id+"F2.wireOp",EDGE,"fcba4419-a2ee-464f-be9d-58f11bf3418b.sketch_text.stroke-36"),sQuery(id+"F2.wireOp",EDGE,"fcba4419-a2ee-464f-be9d-58f11bf3418b.sketch_text.stroke-37"),sQuery(id+"F2.wireOp",EDGE,"fcba4419-a2ee-464f-be9d-58f11bf3418b.sketch_text.stroke-38"),sQuery(id+"F2.wireOp",EDGE,"fcba4419-a2ee-464f-be9d-58f11bf3418b.sketch_text.stroke-39"),sQuery(id+"F2.wireOp",EDGE,"fcba4419-a2ee-464f-be9d-58f11bf3418b.sketch_text.stroke-40"),sQuery(id+"F2.wireOp",EDGE,"fcba4419-a2ee-464f-be9d-58f11bf3418b.sketch_text.stroke-41"),sQuery(id+"F2.wireOp",EDGE,"fcba4419-a2ee-464f-be9d-58f11bf3418b.sketch_text.stroke-42"),sQuery(id+"F2.wireOp",EDGE,"fcba4419-a2ee-464f-be9d-58f11bf3418b.sketch_text.stroke-43"),sQuery(id+"F2.wireOp",EDGE,"fcba4419-a2ee-464f-be9d-58f11bf3418b.sketch_text.stroke-44"),sQuery(id+"F2.wireOp",EDGE,"fcba4419-a2ee-464f-be9d-58f11bf3418b.sketch_text.stroke-45"),sQuery(id+"F2.wireOp",EDGE,"fcba4419-a2ee-464f-be9d-58f11bf3418b.sketch_text.stroke-46"),sQuery(id+"F2.wireOp",EDGE,"fcba4419-a2ee-464f-be9d-58f11bf3418b.sketch_text.stroke-47"),sQuery(id+"F2.wireOp",EDGE,"fcba4419-a2ee-464f-be9d-58f11bf3418b.sketch_text.stroke-48"),sQuery(id+"F2.wireOp",EDGE,"fcba4419-a2ee-464f-be9d-58f11bf3418b.sketch_text.stroke-49"),sQuery(id+"F2.wireOp",EDGE,"fcba4419-a2ee-464f-be9d-58f11bf3418b.sketch_text.stroke-50"),sQuery(id+"F2.wireOp",EDGE,"fcba4419-a2ee-464f-be9d-58f11bf3418b.sketch_text.stroke-51"),sQuery(id+"F2.wireOp",EDGE,"fcba4419-a2ee-464f-be9d-58f11bf3418b.sketch_text.stroke-52"),sQuery(id+"F2.wireOp",EDGE,"fcba4419-a2ee-464f-be9d-58f11bf3418b.sketch_text.stroke-53"),sQuery(id+"F2.wireOp",EDGE,"fcba4419-a2ee-464f-be9d-58f11bf3418b.sketch_text.stroke-54"),sQuery(id+"F2.wireOp",EDGE,"fcba4419-a2ee-464f-be9d-58f11bf3418b.sketch_text.stroke-55"),sQuery(id+"F2.wireOp",EDGE,"fcba4419-a2ee-464f-be9d-58f11bf3418b.sketch_text.stroke-56"),sQuery(id+"F2.wireOp",EDGE,"fcba4419-a2ee-464f-be9d-58f11bf3418b.sketch_text.stroke-57"),sQuery(id+"F2.wireOp",EDGE,"fcba4419-a2ee-464f-be9d-58f11bf3418b.sketch_text.stroke-58"),sQuery(id+"F2.wireOp",EDGE,"fcba4419-a2ee-464f-be9d-58f11bf3418b.sketch_text.stroke-59"),sQuery(id+"F2.wireOp",EDGE,"fcba4419-a2ee-464f-be9d-58f11bf3418b.sketch_text.stroke-60"),sQuery(id+"F2.wireOp",EDGE,"fcba4419-a2ee-464f-be9d-58f11bf3418b.sketch_text.stroke-61"),sQuery(id+"F2.wireOp",EDGE,"fcba4419-a2ee-464f-be9d-58f11bf3418b.sketch_text.stroke-62"),sQuery(id+"F2.wireOp",EDGE,"fcba4419-a2ee-464f-be9d-58f11bf3418b.sketch_text.stroke-63"),sQuery(id+"F2.wireOp",EDGE,"fcba4419-a2ee-464f-be9d-58f11bf3418b.sketch_text.stroke-64"),sQuery(id+"F2.wireOp",EDGE,"fcba4419-a2ee-464f-be9d-58f11bf3418b.sketch_text.stroke-65"),sQuery(id+"F2.wireOp",EDGE,"fcba4419-a2ee-464f-be9d-58f11bf3418b.sketch_text.stroke-66"),sQuery(id+"F2.wireOp",EDGE,"fcba4419-a2ee-464f-be9d-58f11bf3418b.sketch_text.stroke-67"),sQuery(id+"F2.wireOp",EDGE,"fcba4419-a2ee-464f-be9d-58f11bf3418b.sketch_text.stroke-68"),sQuery(id+"F2.wireOp",EDGE,"fcba4419-a2ee-464f-be9d-58f11bf3418b.sketch_text.stroke-69"),sQuery(id+"F2.wireOp",EDGE,"fcba4419-a2ee-464f-be9d-58f11bf3418b.sketch_text.stroke-70"),sQuery(id+"F2.wireOp",EDGE,"fcba4419-a2ee-464f-be9d-58f11bf3418b.sketch_text.stroke-71"),sQuery(id+"F2.wireOp",EDGE,"fcba4419-a2ee-464f-be9d-58f11bf3418b.sketch_text.stroke-72"),sQuery(id+"F2.wireOp",EDGE,"fcba4419-a2ee-464f-be9d-58f11bf3418b.sketch_text.stroke-73"),sQuery(id+"F2.wireOp",EDGE,"fcba4419-a2ee-464f-be9d-58f11bf3418b.sketch_text.stroke-74"),sQuery(id+"F2.wireOp",EDGE,"fcba4419-a2ee-464f-be9d-58f11bf3418b.sketch_text.stroke-75"),sQuery(id+"F2.wireOp",EDGE,"fcba4419-a2ee-464f-be9d-58f11bf3418b.sketch_text.stroke-76"),sQuery(id+"F2.wireOp",EDGE,"fcba4419-a2ee-464f-be9d-58f11bf3418b.sketch_text.stroke-77"),sQuery(id+"F2.wireOp",EDGE,"fcba4419-a2ee-464f-be9d-58f11bf3418b.sketch_text.stroke-78"),sQuery(id+"F2.wireOp",EDGE,"fcba4419-a2ee-464f-be9d-58f11bf3418b.sketch_text.stroke-79"),sQuery(id+"F2.wireOp",EDGE,"fcba4419-a2ee-464f-be9d-58f11bf3418b.sketch_text.stroke-80"),sQuery(id+"F2.wireOp",EDGE,"fcba4419-a2ee-464f-be9d-58f11bf3418b.sketch_text.stroke-81"),sQuery(id+"F2.wireOp",EDGE,"fcba4419-a2ee-464f-be9d-58f11bf3418b.sketch_text.stroke-82"),sQuery(id+"F2.wireOp",EDGE,"fcba4419-a2ee-464f-be9d-58f11bf3418b.sketch_text.stroke-83"),sQuery(id+"F2.wireOp",EDGE,"fcba4419-a2ee-464f-be9d-58f11bf3418b.sketch_text.stroke-84"),sQuery(id+"F2.wireOp",EDGE,"fcba4419-a2ee-464f-be9d-58f11bf3418b.sketch_text.stroke-85"),sQuery(id+"F2.wireOp",EDGE,"fcba4419-a2ee-464f-be9d-58f11bf3418b.sketch_text.stroke-86"),sQuery(id+"F2.wireOp",EDGE,"fcba4419-a2ee-464f-be9d-58f11bf3418b.sketch_text.stroke-87"),sQuery(id+"F2.wireOp",EDGE,"fcba4419-a2ee-464f-be9d-58f11bf3418b.sketch_text.stroke-88"),sQuery(id+"F2.wireOp",EDGE,"fcba4419-a2ee-464f-be9d-58f11bf3418b.sketch_text.stroke-89"),sQuery(id+"F2.wireOp",EDGE,"fcba4419-a2ee-464f-be9d-58f11bf3418b.sketch_text.stroke-90"),sQuery(id+"F2.wireOp",EDGE,"fcba4419-a2ee-464f-be9d-58f11bf3418b.sketch_text.stroke-91"),sQuery(id+"F2.wireOp",EDGE,"fcba4419-a2ee-464f-be9d-58f11bf3418b.sketch_text.stroke-92"),sQuery(id+"F2.wireOp",EDGE,"fcba4419-a2ee-464f-be9d-58f11bf3418b.sketch_text.stroke-93"),sQuery(id+"F2.wireOp",EDGE,"fcba4419-a2ee-464f-be9d-58f11bf3418b.sketch_text.stroke-94"),sQuery(id+"F2.wireOp",EDGE,"fcba4419-a2ee-464f-be9d-58f11bf3418b.sketch_text.stroke-95"),sQuery(id+"F2.wireOp",EDGE,"fcba4419-a2ee-464f-be9d-58f11bf3418b.sketch_text.stroke-96"),sQuery(id+"F2.wireOp",EDGE,"fcba4419-a2ee-464f-be9d-58f11bf3418b.sketch_text.stroke-97"),sQuery(id+"F2.wireOp",EDGE,"fcba4419-a2ee-464f-be9d-58f11bf3418b.sketch_text.stroke-98"),sQuery(id+"F2.wireOp",EDGE,"fcba4419-a2ee-464f-be9d-58f11bf3418b.sketch_text.stroke-99"),sQuery(id+"F2.wireOp",EDGE,"fcba4419-a2ee-464f-be9d-58f11bf3418b.sketch_text.stroke-100"),sQuery(id+"F2.wireOp",EDGE,"fcba4419-a2ee-464f-be9d-58f11bf3418b.sketch_text.stroke-101"),sQuery(id+"F2.wireOp",EDGE,"fcba4419-a2ee-464f-be9d-58f11bf3418b.sketch_text.stroke-102"),sQuery(id+"F2.wireOp",EDGE,"fcba4419-a2ee-464f-be9d-58f11bf3418b.sketch_text.stroke-103"),sQuery(id+"F2.wireOp",EDGE,"fcba4419-a2ee-464f-be9d-58f11bf3418b.sketch_text.stroke-104"),sQuery(id+"F2.wireOp",EDGE,"fcba4419-a2ee-464f-be9d-58f11bf3418b.sketch_text.stroke-105"),sQuery(id+"F2.wireOp",EDGE,"fcba4419-a2ee-464f-be9d-58f11bf3418b.sketch_text.stroke-106"),sQuery(id+"F2.wireOp",EDGE,"fcba4419-a2ee-464f-be9d-58f11bf3418b.sketch_text.stroke-107"),sQuery(id+"F2.wireOp",EDGE,"fcba4419-a2ee-464f-be9d-58f11bf3418b.sketch_text.stroke-108"),sQuery(id+"F2.wireOp",EDGE,"fcba4419-a2ee-464f-be9d-58f11bf3418b.sketch_text.stroke-109"),sQuery(id+"F2.wireOp",EDGE,"fcba4419-a2ee-464f-be9d-58f11bf3418b.sketch_text.stroke-110"),sQuery(id+"F2.wireOp",EDGE,"fcba4419-a2ee-464f-be9d-58f11bf3418b.sketch_text.stroke-111"),sQuery(id+"F2.wireOp",EDGE,"fcba4419-a2ee-464f-be9d-58f11bf3418b.sketch_text.stroke-112"),sQuery(id+"F2.wireOp",EDGE,"fcba4419-a2ee-464f-be9d-58f11bf3418b.sketch_text.stroke-113"),sQuery(id+"F2.wireOp",EDGE,"fcba4419-a2ee-464f-be9d-58f11bf3418b.sketch_text.stroke-114"),sQuery(id+"F2.wireOp",EDGE,"fcba4419-a2ee-464f-be9d-58f11bf3418b.sketch_text.stroke-115"),sQuery(id+"F2.wireOp",EDGE,"fcba4419-a2ee-464f-be9d-58f11bf3418b.sketch_text.stroke-116"),sQuery(id+"F2.wireOp",EDGE,"fcba4419-a2ee-464f-be9d-58f11bf3418b.sketch_text.stroke-117"),sQuery(id+"F2.wireOp",EDGE,"fcba4419-a2ee-464f-be9d-58f11bf3418b.sketch_text.stroke-118"),sQuery(id+"F2.wireOp",EDGE,"fcba4419-a2ee-464f-be9d-58f11bf3418b.sketch_text.stroke-119"),sQuery(id+"F2.wireOp",EDGE,"fcba4419-a2ee-464f-be9d-58f11bf3418b.sketch_text.stroke-120"),sQuery(id+"F2.wireOp",EDGE,"fcba4419-a2ee-464f-be9d-58f11bf3418b.sketch_text.stroke-121"),sQuery(id+"F2.wireOp",EDGE,"fcba4419-a2ee-464f-be9d-58f11bf3418b.sketch_text.stroke-122"),sQuery(id+"F2.wireOp",EDGE,"fcba4419-a2ee-464f-be9d-58f11bf3418b.sketch_text.stroke-123"),sQuery(id+"F2.wireOp",EDGE,"fcba4419-a2ee-464f-be9d-58f11bf3418b.sketch_text.stroke-124"),sQuery(id+"F2.wireOp",EDGE,"fcba4419-a2ee-464f-be9d-58f11bf3418b.sketch_text.stroke-125"),sQuery(id+"F2.wireOp",EDGE,"fcba4419-a2ee-464f-be9d-58f11bf3418b.sketch_text.stroke-126"),sQuery(id+"F2.wireOp",EDGE,"fcba4419-a2ee-464f-be9d-58f11bf3418b.sketch_text.stroke-127"),sQuery(id+"F2.wireOp",EDGE,"fcba4419-a2ee-464f-be9d-58f11bf3418b.sketch_text.stroke-128"),sQuery(id+"F2.wireOp",EDGE,"fcba4419-a2ee-464f-be9d-58f11bf3418b.sketch_text.stroke-129"),sQuery(id+"F2.wireOp",EDGE,"fcba4419-a2ee-464f-be9d-58f11bf3418b.sketch_text.stroke-130"),sQuery(id+"F2.wireOp",EDGE,"fcba4419-a2ee-464f-be9d-58f11bf3418b.sketch_text.stroke-131"),sQuery(id+"F2.wireOp",EDGE,"fcba4419-a2ee-464f-be9d-58f11bf3418b.sketch_text.stroke-132"),sQuery(id+"F2.wireOp",EDGE,"fcba4419-a2ee-464f-be9d-58f11bf3418b.sketch_text.stroke-133"),sQuery(id+"F2.wireOp",EDGE,"fcba4419-a2ee-464f-be9d-58f11bf3418b.sketch_text.stroke-134"),sQuery(id+"F2.wireOp",EDGE,"fcba4419-a2ee-464f-be9d-58f11bf3418b.sketch_text.stroke-135"),sQuery(id+"F2.wireOp",EDGE,"fcba4419-a2ee-464f-be9d-58f11bf3418b.sketch_text.stroke-136"),sQuery(id+"F2.wireOp",EDGE,"fcba4419-a2ee-464f-be9d-58f11bf3418b.sketch_text.stroke-137"),sQuery(id+"F2.wireOp",EDGE,"fcba4419-a2ee-464f-be9d-58f11bf3418b.sketch_text.stroke-138"),sQuery(id+"F2.wireOp",EDGE,"fcba4419-a2ee-464f-be9d-58f11bf3418b.sketch_text.stroke-139"),sQuery(id+"F2.wireOp",EDGE,"fcba4419-a2ee-464f-be9d-58f11bf3418b.sketch_text.stroke-140"),sQuery(id+"F2.wireOp",EDGE,"fcba4419-a2ee-464f-be9d-58f11bf3418b.sketch_text.stroke-141"),sQuery(id+"F2.wireOp",EDGE,"fcba4419-a2ee-464f-be9d-58f11bf3418b.sketch_text.stroke-142"),sQuery(id+"F2.wireOp",EDGE,"fcba4419-a2ee-464f-be9d-58f11bf3418b.sketch_text.stroke-143"),sQuery(id+"F2.wireOp",EDGE,"fcba4419-a2ee-464f-be9d-58f11bf3418b.sketch_text.stroke-144"),sQuery(id+"F2.wireOp",EDGE,"fcba4419-a2ee-464f-be9d-58f11bf3418b.sketch_text.stroke-145"),sQuery(id+"F2.wireOp",EDGE,"fcba4419-a2ee-464f-be9d-58f11bf3418b.sketch_text.stroke-146"),sQuery(id+"F2.wireOp",EDGE,"fcba4419-a2ee-464f-be9d-58f11bf3418b.sketch_text.stroke-147"),sQuery(id+"F2.wireOp",EDGE,"fcba4419-a2ee-464f-be9d-58f11bf3418b.sketch_text.stroke-148"),sQuery(id+"F2.wireOp",EDGE,"fcba4419-a2ee-464f-be9d-58f11bf3418b.sketch_text.stroke-149"),sQuery(id+"F2.wireOp",EDGE,"fcba4419-a2ee-464f-be9d-58f11bf3418b.sketch_text.stroke-150"),sQuery(id+"F2.wireOp",EDGE,"fcba4419-a2ee-464f-be9d-58f11bf3418b.sketch_text.stroke-151"),sQuery(id+"F2.wireOp",EDGE,"fcba4419-a2ee-464f-be9d-58f11bf3418b.sketch_text.stroke-152"),sQuery(id+"F2.wireOp",EDGE,"fcba4419-a2ee-464f-be9d-58f11bf3418b.sketch_text.stroke-153"),sQuery(id+"F2.wireOp",EDGE,"fcba4419-a2ee-464f-be9d-58f11bf3418b.sketch_text.stroke-154"),sQuery(id+"F2.wireOp",EDGE,"fcba4419-a2ee-464f-be9d-58f11bf3418b.sketch_text.stroke-155"),sQuery(id+"F2.wireOp",EDGE,"fcba4419-a2ee-464f-be9d-58f11bf3418b.sketch_text.stroke-156"),sQuery(id+"F2.wireOp",EDGE,"fcba4419-a2ee-464f-be9d-58f11bf3418b.sketch_text.stroke-157"),sQuery(id+"F2.wireOp",EDGE,"fcba4419-a2ee-464f-be9d-58f11bf3418b.sketch_text.stroke-158"),sQuery(id+"F2.wireOp",EDGE,"fcba4419-a2ee-464f-be9d-58f11bf3418b.sketch_text.stroke-159"),sQuery(id+"F2.wireOp",EDGE,"fcba4419-a2ee-464f-be9d-58f11bf3418b.sketch_text.stroke-160"),sQuery(id+"F2.wireOp",EDGE,"fcba4419-a2ee-464f-be9d-58f11bf3418b.sketch_text.stroke-161"),sQuery(id+"F2.wireOp",EDGE,"fcba4419-a2ee-464f-be9d-58f11bf3418b.sketch_text.stroke-162"),sQuery(id+"F2.wireOp",EDGE,"fcba4419-a2ee-464f-be9d-58f11bf3418b.sketch_text.stroke-163"),sQuery(id+"F2.wireOp",EDGE,"fcba4419-a2ee-464f-be9d-58f11bf3418b.sketch_text.stroke-164"),sQuery(id+"F2.wireOp",EDGE,"fcba4419-a2ee-464f-be9d-58f11bf3418b.sketch_text.stroke-165"),sQuery(id+"F2.wireOp",EDGE,"fcba4419-a2ee-464f-be9d-58f11bf3418b.sketch_text.stroke-166"),sQuery(id+"F2.wireOp",EDGE,"fcba4419-a2ee-464f-be9d-58f11bf3418b.sketch_text.stroke-167"),sQuery(id+"F2.wireOp",EDGE,"fcba4419-a2ee-464f-be9d-58f11bf3418b.sketch_text.stroke-168"),sQuery(id+"F2.wireOp",EDGE,"fcba4419-a2ee-464f-be9d-58f11bf3418b.sketch_text.stroke-169"),sQuery(id+"F2.wireOp",EDGE,"fcba4419-a2ee-464f-be9d-58f11bf3418b.sketch_text.stroke-170"),sQuery(id+"F2.wireOp",EDGE,"fcba4419-a2ee-464f-be9d-58f11bf3418b.sketch_text.stroke-171"),sQuery(id+"F2.wireOp",EDGE,"fcba4419-a2ee-464f-be9d-58f11bf3418b.sketch_text.stroke-172"),sQuery(id+"F2.wireOp",EDGE,"fcba4419-a2ee-464f-be9d-58f11bf3418b.sketch_text.stroke-173"),sQuery(id+"FHMxAyK4CFUKdhS_1.wireOp",EDGE,"1cb9c079-ea9b-4899-8069-e0e3048e911d.sketch_text.stroke-0"),sQuery(id+"FHMxAyK4CFUKdhS_1.wireOp",EDGE,"1cb9c079-ea9b-4899-8069-e0e3048e911d.sketch_text.stroke-1"),sQuery(id+"FHMxAyK4CFUKdhS_1.wireOp",EDGE,"1cb9c079-ea9b-4899-8069-e0e3048e911d.sketch_text.stroke-2"),sQuery(id+"FHMxAyK4CFUKdhS_1.wireOp",EDGE,"1cb9c079-ea9b-4899-8069-e0e3048e911d.sketch_text.stroke-3"),sQuery(id+"FHMxAyK4CFUKdhS_1.wireOp",EDGE,"1cb9c079-ea9b-4899-8069-e0e3048e911d.sketch_text.stroke-4"),sQuery(id+"FHMxAyK4CFUKdhS_1.wireOp",EDGE,"1cb9c079-ea9b-4899-8069-e0e3048e911d.sketch_text.stroke-5"),sQuery(id+"FHMxAyK4CFUKdhS_1.wireOp",EDGE,"1cb9c079-ea9b-4899-8069-e0e3048e911d.sketch_text.stroke-6"),sQuery(id+"FHMxAyK4CFUKdhS_1.wireOp",EDGE,"1cb9c079-ea9b-4899-8069-e0e3048e911d.sketch_text.stroke-7"),sQuery(id+"FHMxAyK4CFUKdhS_1.wireOp",EDGE,"1cb9c079-ea9b-4899-8069-e0e3048e911d.sketch_text.stroke-8"),sQuery(id+"FHMxAyK4CFUKdhS_1.wireOp",EDGE,"1cb9c079-ea9b-4899-8069-e0e3048e911d.sketch_text.stroke-9"),sQuery(id+"FHMxAyK4CFUKdhS_1.wireOp",EDGE,"1cb9c079-ea9b-4899-8069-e0e3048e911d.sketch_text.stroke-10"),sQuery(id+"FHMxAyK4CFUKdhS_1.wireOp",EDGE,"1cb9c079-ea9b-4899-8069-e0e3048e911d.sketch_text.stroke-11"),sQuery(id+"FHMxAyK4CFUKdhS_1.wireOp",EDGE,"1cb9c079-ea9b-4899-8069-e0e3048e911d.sketch_text.stroke-12"),sQuery(id+"FHMxAyK4CFUKdhS_1.wireOp",EDGE,"1cb9c079-ea9b-4899-8069-e0e3048e911d.sketch_text.stroke-13"),sQuery(id+"FHMxAyK4CFUKdhS_1.wireOp",EDGE,"1cb9c079-ea9b-4899-8069-e0e3048e911d.sketch_text.stroke-14"),sQuery(id+"FHMxAyK4CFUKdhS_1.wireOp",EDGE,"1cb9c079-ea9b-4899-8069-e0e3048e911d.sketch_text.stroke-15"),sQuery(id+"FHMxAyK4CFUKdhS_1.wireOp",EDGE,"1cb9c079-ea9b-4899-8069-e0e3048e911d.sketch_text.stroke-16"),sQuery(id+"FHMxAyK4CFUKdhS_1.wireOp",EDGE,"1cb9c079-ea9b-4899-8069-e0e3048e911d.sketch_text.stroke-17"),sQuery(id+"FHMxAyK4CFUKdhS_1.wireOp",EDGE,"1cb9c079-ea9b-4899-8069-e0e3048e911d.sketch_text.stroke-18"),sQuery(id+"FHMxAyK4CFUKdhS_1.wireOp",EDGE,"1cb9c079-ea9b-4899-8069-e0e3048e911d.sketch_text.stroke-19"),sQuery(id+"FHMxAyK4CFUKdhS_1.wireOp",EDGE,"1cb9c079-ea9b-4899-8069-e0e3048e911d.sketch_text.stroke-20"),sQuery(id+"FHMxAyK4CFUKdhS_1.wireOp",EDGE,"1cb9c079-ea9b-4899-8069-e0e3048e911d.sketch_text.stroke-21"),sQuery(id+"FHMxAyK4CFUKdhS_1.wireOp",EDGE,"1cb9c079-ea9b-4899-8069-e0e3048e911d.sketch_text.stroke-22"),sQuery(id+"FHMxAyK4CFUKdhS_1.wireOp",EDGE,"1cb9c079-ea9b-4899-8069-e0e3048e911d.sketch_text.stroke-23"),sQuery(id+"FHMxAyK4CFUKdhS_1.wireOp",EDGE,"1cb9c079-ea9b-4899-8069-e0e3048e911d.sketch_text.stroke-24"),sQuery(id+"FHMxAyK4CFUKdhS_1.wireOp",EDGE,"1cb9c079-ea9b-4899-8069-e0e3048e911d.sketch_text.stroke-25"),sQuery(id+"FHMxAyK4CFUKdhS_1.wireOp",EDGE,"1cb9c079-ea9b-4899-8069-e0e3048e911d.sketch_text.stroke-26"),sQuery(id+"FHMxAyK4CFUKdhS_1.wireOp",EDGE,"1cb9c079-ea9b-4899-8069-e0e3048e911d.sketch_text.stroke-27"),sQuery(id+"FHMxAyK4CFUKdhS_1.wireOp",EDGE,"1cb9c079-ea9b-4899-8069-e0e3048e911d.sketch_text.stroke-28"),sQuery(id+"FHMxAyK4CFUKdhS_1.wireOp",EDGE,"1cb9c079-ea9b-4899-8069-e0e3048e911d.sketch_text.stroke-29"),sQuery(id+"FHMxAyK4CFUKdhS_1.wireOp",EDGE,"1cb9c079-ea9b-4899-8069-e0e3048e911d.sketch_text.stroke-30"),sQuery(id+"FHMxAyK4CFUKdhS_1.wireOp",EDGE,"1cb9c079-ea9b-4899-8069-e0e3048e911d.sketch_text.stroke-31"),sQuery(id+"FHMxAyK4CFUKdhS_1.wireOp",EDGE,"1cb9c079-ea9b-4899-8069-e0e3048e911d.sketch_text.stroke-32"),sQuery(id+"FHMxAyK4CFUKdhS_1.wireOp",EDGE,"1cb9c079-ea9b-4899-8069-e0e3048e911d.sketch_text.stroke-33"),sQuery(id+"FHMxAyK4CFUKdhS_1.wireOp",EDGE,"1cb9c079-ea9b-4899-8069-e0e3048e911d.sketch_text.stroke-34"),sQuery(id+"FHMxAyK4CFUKdhS_1.wireOp",EDGE,"1cb9c079-ea9b-4899-8069-e0e3048e911d.sketch_text.stroke-35"),sQuery(id+"FHMxAyK4CFUKdhS_1.wireOp",EDGE,"1cb9c079-ea9b-4899-8069-e0e3048e911d.sketch_text.stroke-36"),sQuery(id+"FHMxAyK4CFUKdhS_1.wireOp",EDGE,"1cb9c079-ea9b-4899-8069-e0e3048e911d.sketch_text.stroke-37"),sQuery(id+"FHMxAyK4CFUKdhS_1.wireOp",EDGE,"1cb9c079-ea9b-4899-8069-e0e3048e911d.sketch_text.stroke-38"),sQuery(id+"FHMxAyK4CFUKdhS_1.wireOp",EDGE,"1cb9c079-ea9b-4899-8069-e0e3048e911d.sketch_text.stroke-39"),sQuery(id+"FHMxAyK4CFUKdhS_1.wireOp",EDGE,"1cb9c079-ea9b-4899-8069-e0e3048e911d.sketch_text.stroke-40"),sQuery(id+"FHMxAyK4CFUKdhS_1.wireOp",EDGE,"1cb9c079-ea9b-4899-8069-e0e3048e911d.sketch_text.stroke-41"),sQuery(id+"FHMxAyK4CFUKdhS_1.wireOp",EDGE,"1cb9c079-ea9b-4899-8069-e0e3048e911d.sketch_text.stroke-42"),sQuery(id+"FHMxAyK4CFUKdhS_1.wireOp",EDGE,"1cb9c079-ea9b-4899-8069-e0e3048e911d.sketch_text.stroke-43"),sQuery(id+"FHMxAyK4CFUKdhS_1.wireOp",EDGE,"1cb9c079-ea9b-4899-8069-e0e3048e911d.sketch_text.stroke-44"),sQuery(id+"FHMxAyK4CFUKdhS_1.wireOp",EDGE,"1cb9c079-ea9b-4899-8069-e0e3048e911d.sketch_text.stroke-45"),sQuery(id+"FHMxAyK4CFUKdhS_1.wireOp",EDGE,"1cb9c079-ea9b-4899-8069-e0e3048e911d.sketch_text.stroke-46"),sQuery(id+"FHMxAyK4CFUKdhS_1.wireOp",EDGE,"1cb9c079-ea9b-4899-8069-e0e3048e911d.sketch_text.stroke-47"),sQuery(id+"FHMxAyK4CFUKdhS_1.wireOp",EDGE,"1cb9c079-ea9b-4899-8069-e0e3048e911d.sketch_text.stroke-48"),sQuery(id+"FHMxAyK4CFUKdhS_1.wireOp",EDGE,"1cb9c079-ea9b-4899-8069-e0e3048e911d.sketch_text.stroke-49"),sQuery(id+"FHMxAyK4CFUKdhS_1.wireOp",EDGE,"1cb9c079-ea9b-4899-8069-e0e3048e911d.sketch_text.stroke-50"),sQuery(id+"FHMxAyK4CFUKdhS_1.wireOp",EDGE,"1cb9c079-ea9b-4899-8069-e0e3048e911d.sketch_text.stroke-51"),sQuery(id+"FHMxAyK4CFUKdhS_1.wireOp",EDGE,"1cb9c079-ea9b-4899-8069-e0e3048e911d.sketch_text.stroke-52"),sQuery(id+"FHMxAyK4CFUKdhS_1.wireOp",EDGE,"1cb9c079-ea9b-4899-8069-e0e3048e911d.sketch_text.stroke-53"),sQuery(id+"FHMxAyK4CFUKdhS_1.wireOp",EDGE,"1cb9c079-ea9b-4899-8069-e0e3048e911d.sketch_text.stroke-54"),sQuery(id+"FHMxAyK4CFUKdhS_1.wireOp",EDGE,"1cb9c079-ea9b-4899-8069-e0e3048e911d.sketch_text.stroke-55"),sQuery(id+"FHMxAyK4CFUKdhS_1.wireOp",EDGE,"1cb9c079-ea9b-4899-8069-e0e3048e911d.sketch_text.stroke-56"),sQuery(id+"FHMxAyK4CFUKdhS_1.wireOp",EDGE,"1cb9c079-ea9b-4899-8069-e0e3048e911d.sketch_text.stroke-57"),sQuery(id+"FHMxAyK4CFUKdhS_1.wireOp",EDGE,"1cb9c079-ea9b-4899-8069-e0e3048e911d.sketch_text.stroke-58"),sQuery(id+"FHMxAyK4CFUKdhS_1.wireOp",EDGE,"1cb9c079-ea9b-4899-8069-e0e3048e911d.sketch_text.stroke-59"),sQuery(id+"FHMxAyK4CFUKdhS_1.wireOp",EDGE,"1cb9c079-ea9b-4899-8069-e0e3048e911d.sketch_text.stroke-60"),sQuery(id+"FHMxAyK4CFUKdhS_1.wireOp",EDGE,"1cb9c079-ea9b-4899-8069-e0e3048e911d.sketch_text.stroke-61"),sQuery(id+"FHMxAyK4CFUKdhS_1.wireOp",EDGE,"1cb9c079-ea9b-4899-8069-e0e3048e911d.sketch_text.stroke-62"),sQuery(id+"FHMxAyK4CFUKdhS_1.wireOp",EDGE,"1cb9c079-ea9b-4899-8069-e0e3048e911d.sketch_text.stroke-71"),sQuery(id+"FHMxAyK4CFUKdhS_1.wireOp",EDGE,"1cb9c079-ea9b-4899-8069-e0e3048e911d.sketch_text.stroke-72"),sQuery(id+"FHMxAyK4CFUKdhS_1.wireOp",EDGE,"1cb9c079-ea9b-4899-8069-e0e3048e911d.sketch_text.stroke-73"),sQuery(id+"FHMxAyK4CFUKdhS_1.wireOp",EDGE,"1cb9c079-ea9b-4899-8069-e0e3048e911d.sketch_text.stroke-74"),sQuery(id+"FHMxAyK4CFUKdhS_1.wireOp",EDGE,"1cb9c079-ea9b-4899-8069-e0e3048e911d.sketch_text.stroke-75"),sQuery(id+"FHMxAyK4CFUKdhS_1.wireOp",EDGE,"1cb9c079-ea9b-4899-8069-e0e3048e911d.sketch_text.stroke-76"),sQuery(id+"FHMxAyK4CFUKdhS_1.wireOp",EDGE,"1cb9c079-ea9b-4899-8069-e0e3048e911d.sketch_text.stroke-77"),sQuery(id+"FHMxAyK4CFUKdhS_1.wireOp",EDGE,"1cb9c079-ea9b-4899-8069-e0e3048e911d.sketch_text.stroke-78"),sQuery(id+"FHMxAyK4CFUKdhS_1.wireOp",EDGE,"1cb9c079-ea9b-4899-8069-e0e3048e911d.sketch_text.stroke-79"),sQuery(id+"FHMxAyK4CFUKdhS_1.wireOp",EDGE,"1cb9c079-ea9b-4899-8069-e0e3048e911d.sketch_text.stroke-80"),sQuery(id+"FHMxAyK4CFUKdhS_1.wireOp",EDGE,"1cb9c079-ea9b-4899-8069-e0e3048e911d.sketch_text.stroke-81"),sQuery(id+"FHMxAyK4CFUKdhS_1.wireOp",EDGE,"1cb9c079-ea9b-4899-8069-e0e3048e911d.sketch_text.stroke-82"),sQuery(id+"FHMxAyK4CFUKdhS_1.wireOp",EDGE,"1cb9c079-ea9b-4899-8069-e0e3048e911d.sketch_text.stroke-83"),sQuery(id+"FHMxAyK4CFUKdhS_1.wireOp",EDGE,"1cb9c079-ea9b-4899-8069-e0e3048e911d.sketch_text.stroke-84"),sQuery(id+"FHMxAyK4CFUKdhS_1.wireOp",EDGE,"1cb9c079-ea9b-4899-8069-e0e3048e911d.sketch_text.stroke-85"),sQuery(id+"FHMxAyK4CFUKdhS_1.wireOp",EDGE,"1cb9c079-ea9b-4899-8069-e0e3048e911d.sketch_text.stroke-86"),sQuery(id+"FHMxAyK4CFUKdhS_1.wireOp",EDGE,"1cb9c079-ea9b-4899-8069-e0e3048e911d.sketch_text.stroke-87"),sQuery(id+"FHMxAyK4CFUKdhS_1.wireOp",EDGE,"1cb9c079-ea9b-4899-8069-e0e3048e911d.sketch_text.stroke-88"),sQuery(id+"FHMxAyK4CFUKdhS_1.wireOp",EDGE,"1cb9c079-ea9b-4899-8069-e0e3048e911d.sketch_text.stroke-89"),sQuery(id+"FHMxAyK4CFUKdhS_1.wireOp",EDGE,"1cb9c079-ea9b-4899-8069-e0e3048e911d.sketch_text.stroke-90"),sQuery(id+"FHMxAyK4CFUKdhS_1.wireOp",EDGE,"1cb9c079-ea9b-4899-8069-e0e3048e911d.sketch_text.stroke-91"),sQuery(id+"FHMxAyK4CFUKdhS_1.wireOp",EDGE,"1cb9c079-ea9b-4899-8069-e0e3048e911d.sketch_text.stroke-92"),sQuery(id+"FHMxAyK4CFUKdhS_1.wireOp",EDGE,"1cb9c079-ea9b-4899-8069-e0e3048e911d.sketch_text.stroke-93"),sQuery(id+"FHMxAyK4CFUKdhS_1.wireOp",EDGE,"1cb9c079-ea9b-4899-8069-e0e3048e911d.sketch_text.stroke-94"),sQuery(id+"FHMxAyK4CFUKdhS_1.wireOp",EDGE,"1cb9c079-ea9b-4899-8069-e0e3048e911d.sketch_text.stroke-95"),sQuery(id+"FHMxAyK4CFUKdhS_1.wireOp",EDGE,"1cb9c079-ea9b-4899-8069-e0e3048e911d.sketch_text.stroke-96"),sQuery(id+"FHMxAyK4CFUKdhS_1.wireOp",EDGE,"1cb9c079-ea9b-4899-8069-e0e3048e911d.sketch_text.stroke-97"),sQuery(id+"FHMxAyK4CFUKdhS_1.wireOp",EDGE,"1cb9c079-ea9b-4899-8069-e0e3048e911d.sketch_text.stroke-103"),sQuery(id+"FHMxAyK4CFUKdhS_1.wireOp",EDGE,"1cb9c079-ea9b-4899-8069-e0e3048e911d.sketch_text.stroke-104"),sQuery(id+"FHMxAyK4CFUKdhS_1.wireOp",EDGE,"1cb9c079-ea9b-4899-8069-e0e3048e911d.sketch_text.stroke-105"),sQuery(id+"FHMxAyK4CFUKdhS_1.wireOp",EDGE,"1cb9c079-ea9b-4899-8069-e0e3048e911d.sketch_text.stroke-106"),sQuery(id+"FHMxAyK4CFUKdhS_1.wireOp",EDGE,"1cb9c079-ea9b-4899-8069-e0e3048e911d.sketch_text.stroke-107"),sQuery(id+"FHMxAyK4CFUKdhS_1.wireOp",EDGE,"1cb9c079-ea9b-4899-8069-e0e3048e911d.sketch_text.stroke-108"),sQuery(id+"FHMxAyK4CFUKdhS_1.wireOp",EDGE,"1cb9c079-ea9b-4899-8069-e0e3048e911d.sketch_text.stroke-109"),sQuery(id+"FHMxAyK4CFUKdhS_1.wireOp",EDGE,"1cb9c079-ea9b-4899-8069-e0e3048e911d.sketch_text.stroke-110"),sQuery(id+"FHMxAyK4CFUKdhS_1.wireOp",EDGE,"1cb9c079-ea9b-4899-8069-e0e3048e911d.sketch_text.stroke-111"),sQuery(id+"FHMxAyK4CFUKdhS_1.wireOp",EDGE,"1cb9c079-ea9b-4899-8069-e0e3048e911d.sketch_text.stroke-112"),sQuery(id+"FHMxAyK4CFUKdhS_1.wireOp",EDGE,"1cb9c079-ea9b-4899-8069-e0e3048e911d.sketch_text.stroke-113"),sQuery(id+"FHMxAyK4CFUKdhS_1.wireOp",EDGE,"1cb9c079-ea9b-4899-8069-e0e3048e911d.sketch_text.stroke-114"),sQuery(id+"FHMxAyK4CFUKdhS_1.wireOp",EDGE,"1cb9c079-ea9b-4899-8069-e0e3048e911d.sketch_text.stroke-115"),sQuery(id+"FHMxAyK4CFUKdhS_1.wireOp",EDGE,"1cb9c079-ea9b-4899-8069-e0e3048e911d.sketch_text.stroke-116"),sQuery(id+"FHMxAyK4CFUKdhS_1.wireOp",EDGE,"1cb9c079-ea9b-4899-8069-e0e3048e911d.sketch_text.stroke-117"),sQuery(id+"FHMxAyK4CFUKdhS_1.wireOp",EDGE,"1cb9c079-ea9b-4899-8069-e0e3048e911d.sketch_text.stroke-118"),sQuery(id+"FHMxAyK4CFUKdhS_1.wireOp",EDGE,"1cb9c079-ea9b-4899-8069-e0e3048e911d.sketch_text.stroke-119"),sQuery(id+"FHMxAyK4CFUKdhS_1.wireOp",EDGE,"1cb9c079-ea9b-4899-8069-e0e3048e911d.sketch_text.stroke-120"),sQuery(id+"FHMxAyK4CFUKdhS_1.wireOp",EDGE,"1cb9c079-ea9b-4899-8069-e0e3048e911d.sketch_text.stroke-121"),sQuery(id+"FHMxAyK4CFUKdhS_1.wireOp",EDGE,"1cb9c079-ea9b-4899-8069-e0e3048e911d.sketch_text.stroke-122"),sQuery(id+"FHMxAyK4CFUKdhS_1.wireOp",EDGE,"1cb9c079-ea9b-4899-8069-e0e3048e911d.sketch_text.stroke-123"),sQuery(id+"FHMxAyK4CFUKdhS_1.wireOp",EDGE,"1cb9c079-ea9b-4899-8069-e0e3048e911d.sketch_text.stroke-124"),sQuery(id+"FHMxAyK4CFUKdhS_1.wireOp",EDGE,"1cb9c079-ea9b-4899-8069-e0e3048e911d.sketch_text.stroke-125"),sQuery(id+"FHMxAyK4CFUKdhS_1.wireOp",EDGE,"1cb9c079-ea9b-4899-8069-e0e3048e911d.sketch_text.stroke-126"),sQuery(id+"FHMxAyK4CFUKdhS_1.wireOp",EDGE,"1cb9c079-ea9b-4899-8069-e0e3048e911d.sketch_text.stroke-127"),sQuery(id+"FHMxAyK4CFUKdhS_1.wireOp",EDGE,"1cb9c079-ea9b-4899-8069-e0e3048e911d.sketch_text.stroke-128"),sQuery(id+"FHMxAyK4CFUKdhS_1.wireOp",EDGE,"1cb9c079-ea9b-4899-8069-e0e3048e911d.sketch_text.stroke-129"),sQuery(id+"FHMxAyK4CFUKdhS_1.wireOp",EDGE,"1cb9c079-ea9b-4899-8069-e0e3048e911d.sketch_text.stroke-130"),sQuery(id+"FHMxAyK4CFUKdhS_1.wireOp",EDGE,"1cb9c079-ea9b-4899-8069-e0e3048e911d.sketch_text.stroke-131"),sQuery(id+"FHMxAyK4CFUKdhS_1.wireOp",EDGE,"1cb9c079-ea9b-4899-8069-e0e3048e911d.sketch_text.stroke-132"),sQuery(id+"FHMxAyK4CFUKdhS_1.wireOp",EDGE,"1cb9c079-ea9b-4899-8069-e0e3048e911d.sketch_text.stroke-133"),sQuery(id+"FHMxAyK4CFUKdhS_1.wireOp",EDGE,"1cb9c079-ea9b-4899-8069-e0e3048e911d.sketch_text.stroke-134"),sQuery(id+"FHMxAyK4CFUKdhS_1.wireOp",EDGE,"1cb9c079-ea9b-4899-8069-e0e3048e911d.sketch_text.stroke-135"),sQuery(id+"FHMxAyK4CFUKdhS_1.wireOp",EDGE,"1cb9c079-ea9b-4899-8069-e0e3048e911d.sketch_text.stroke-136"),sQuery(id+"FHMxAyK4CFUKdhS_1.wireOp",EDGE,"1cb9c079-ea9b-4899-8069-e0e3048e911d.sketch_text.stroke-137"),sQuery(id+"FHMxAyK4CFUKdhS_1.wireOp",EDGE,"1cb9c079-ea9b-4899-8069-e0e3048e911d.sketch_text.stroke-138"),sQuery(id+"FHMxAyK4CFUKdhS_1.wireOp",EDGE,"1cb9c079-ea9b-4899-8069-e0e3048e911d.sketch_text.stroke-139"),sQuery(id+"FHMxAyK4CFUKdhS_1.wireOp",EDGE,"1cb9c079-ea9b-4899-8069-e0e3048e911d.sketch_text.stroke-140"),sQuery(id+"FHMxAyK4CFUKdhS_1.wireOp",EDGE,"1cb9c079-ea9b-4899-8069-e0e3048e911d.sketch_text.stroke-141"),sQuery(id+"FHMxAyK4CFUKdhS_1.wireOp",EDGE,"1cb9c079-ea9b-4899-8069-e0e3048e911d.sketch_text.stroke-142"),sQuery(id+"FHMxAyK4CFUKdhS_1.wireOp",EDGE,"1cb9c079-ea9b-4899-8069-e0e3048e911d.sketch_text.stroke-143"),sQuery(id+"FHMxAyK4CFUKdhS_1.wireOp",EDGE,"1cb9c079-ea9b-4899-8069-e0e3048e911d.sketch_text.stroke-144"),sQuery(id+"FHMxAyK4CFUKdhS_1.wireOp",EDGE,"1cb9c079-ea9b-4899-8069-e0e3048e911d.sketch_text.stroke-145"),sQuery(id+"FHMxAyK4CFUKdhS_1.wireOp",EDGE,"1cb9c079-ea9b-4899-8069-e0e3048e911d.sketch_text.stroke-146"),sQuery(id+"FHMxAyK4CFUKdhS_1.wireOp",EDGE,"1cb9c079-ea9b-4899-8069-e0e3048e911d.sketch_text.stroke-147"),sQuery(id+"FHMxAyK4CFUKdhS_1.wireOp",EDGE,"1cb9c079-ea9b-4899-8069-e0e3048e911d.sketch_text.stroke-148"),sQuery(id+"FHMxAyK4CFUKdhS_1.wireOp",EDGE,"1cb9c079-ea9b-4899-8069-e0e3048e911d.sketch_text.stroke-149"),sQuery(id+"FHMxAyK4CFUKdhS_1.wireOp",EDGE,"1cb9c079-ea9b-4899-8069-e0e3048e911d.sketch_text.stroke-150"),sQuery(id+"FHMxAyK4CFUKdhS_1.wireOp",EDGE,"1cb9c079-ea9b-4899-8069-e0e3048e911d.sketch_text.stroke-151"),sQuery(id+"FHMxAyK4CFUKdhS_1.wireOp",EDGE,"1cb9c079-ea9b-4899-8069-e0e3048e911d.sketch_text.stroke-152"),sQuery(id+"FHMxAyK4CFUKdhS_1.wireOp",EDGE,"1cb9c079-ea9b-4899-8069-e0e3048e911d.sketch_text.stroke-153"),sQuery(id+"FHMxAyK4CFUKdhS_1.wireOp",EDGE,"1cb9c079-ea9b-4899-8069-e0e3048e911d.sketch_text.stroke-159"),sQuery(id+"FHMxAyK4CFUKdhS_1.wireOp",EDGE,"1cb9c079-ea9b-4899-8069-e0e3048e911d.sketch_text.stroke-160"),sQuery(id+"FHMxAyK4CFUKdhS_1.wireOp",EDGE,"1cb9c079-ea9b-4899-8069-e0e3048e911d.sketch_text.stroke-161"),sQuery(id+"FHMxAyK4CFUKdhS_1.wireOp",EDGE,"1cb9c079-ea9b-4899-8069-e0e3048e911d.sketch_text.stroke-162"),sQuery(id+"FHMxAyK4CFUKdhS_1.wireOp",EDGE,"1cb9c079-ea9b-4899-8069-e0e3048e911d.sketch_text.stroke-163"),sQuery(id+"FHMxAyK4CFUKdhS_1.wireOp",EDGE,"1cb9c079-ea9b-4899-8069-e0e3048e911d.sketch_text.stroke-164"),sQuery(id+"FHMxAyK4CFUKdhS_1.wireOp",EDGE,"1cb9c079-ea9b-4899-8069-e0e3048e911d.sketch_text.stroke-165"),sQuery(id+"FHMxAyK4CFUKdhS_1.wireOp",EDGE,"1cb9c079-ea9b-4899-8069-e0e3048e911d.sketch_text.stroke-166"),sQuery(id+"FHMxAyK4CFUKdhS_1.wireOp",EDGE,"1cb9c079-ea9b-4899-8069-e0e3048e911d.sketch_text.stroke-167"),sQuery(id+"FHMxAyK4CFUKdhS_1.wireOp",EDGE,"1cb9c079-ea9b-4899-8069-e0e3048e911d.sketch_text.stroke-168"),sQuery(id+"FHMxAyK4CFUKdhS_1.wireOp",EDGE,"1cb9c079-ea9b-4899-8069-e0e3048e911d.sketch_text.stroke-169"),sQuery(id+"FHMxAyK4CFUKdhS_1.wireOp",EDGE,"1cb9c079-ea9b-4899-8069-e0e3048e911d.sketch_text.stroke-170"),sQuery(id+"FHMxAyK4CFUKdhS_1.wireOp",EDGE,"1cb9c079-ea9b-4899-8069-e0e3048e911d.sketch_text.stroke-171"),sQuery(id+"FHMxAyK4CFUKdhS_1.wireOp",EDGE,"1cb9c079-ea9b-4899-8069-e0e3048e911d.sketch_text.stroke-172"),sQuery(id+"FHMxAyK4CFUKdhS_1.wireOp",EDGE,"1cb9c079-ea9b-4899-8069-e0e3048e911d.sketch_text.stroke-173"),sQuery(id+"FHMxAyK4CFUKdhS_1.wireOp",EDGE,"1cb9c079-ea9b-4899-8069-e0e3048e911d.sketch_text.stroke-174"),sQuery(id+"FHMxAyK4CFUKdhS_1.wireOp",EDGE,"1cb9c079-ea9b-4899-8069-e0e3048e911d.sketch_text.stroke-175"),sQuery(id+"FHMxAyK4CFUKdhS_1.wireOp",EDGE,"1cb9c079-ea9b-4899-8069-e0e3048e911d.sketch_text.stroke-176"),sQuery(id+"FHMxAyK4CFUKdhS_1.wireOp",EDGE,"1cb9c079-ea9b-4899-8069-e0e3048e911d.sketch_text.stroke-177"),sQuery(id+"FHMxAyK4CFUKdhS_1.wireOp",EDGE,"1cb9c079-ea9b-4899-8069-e0e3048e911d.sketch_text.stroke-178"),sQuery(id+"FHMxAyK4CFUKdhS_1.wireOp",EDGE,"1cb9c079-ea9b-4899-8069-e0e3048e911d.sketch_text.stroke-179"),sQuery(id+"FHMxAyK4CFUKdhS_1.wireOp",EDGE,"1cb9c079-ea9b-4899-8069-e0e3048e911d.sketch_text.stroke-180"),subQ0,subQ2])],"isStart":true}),makeQuery(id+"F4.opExtrude","SWEPT_FACE",FACE,{"disambiguationData":[OSD([subQ2])]})])],"derivedFrom":makeQuery(id+"F4.opExtrude","CAP_EDGE",EDGE,{"disambiguationData":[OSD([subQ2])],"isStart":true})});}
            var Q16;
            {var subQ0=sQuery(id+"F0.wireOp",EDGE,"E0.top");var subQ1=sQuery(id+"F0.wireOp",EDGE,"E0.bottom");var subQ2=sQuery(id+"F3.wireOp",EDGE,"727ac2c1-f511-4829-95a7-a443ef16a4cd");Q16=makeQuery(id+"F4.boolean.opBoolean","SPLIT",EDGE,{"disambiguationData":[TD([makeQuery(id+"F1.opExtrude","CAP_FACE",FACE,{"disambiguationData":[OSD([subQ1,subQ0,sQuery(id+"F0.wireOp",EDGE,"E0.left"),sQuery(id+"F0.wireOp",EDGE,"E0.right")])],"isStart":false}),makeQuery(id+"F1.opExtrude","SWEPT_FACE",FACE,{"disambiguationData":[OSD([subQ0])]}),makeQuery(id+"F4.opExtrude","CAP_FACE",FACE,{"disambiguationData":[OSD([subQ1,sQuery(id+"F2.wireOp",EDGE,"fcba4419-a2ee-464f-be9d-58f11bf3418b.sketch_text.stroke-0"),sQuery(id+"F2.wireOp",EDGE,"fcba4419-a2ee-464f-be9d-58f11bf3418b.sketch_text.stroke-1"),sQuery(id+"F2.wireOp",EDGE,"fcba4419-a2ee-464f-be9d-58f11bf3418b.sketch_text.stroke-2"),sQuery(id+"F2.wireOp",EDGE,"fcba4419-a2ee-464f-be9d-58f11bf3418b.sketch_text.stroke-3"),sQuery(id+"F2.wireOp",EDGE,"fcba4419-a2ee-464f-be9d-58f11bf3418b.sketch_text.stroke-4"),sQuery(id+"F2.wireOp",EDGE,"fcba4419-a2ee-464f-be9d-58f11bf3418b.sketch_text.stroke-5"),sQuery(id+"F2.wireOp",EDGE,"fcba4419-a2ee-464f-be9d-58f11bf3418b.sketch_text.stroke-6"),sQuery(id+"F2.wireOp",EDGE,"fcba4419-a2ee-464f-be9d-58f11bf3418b.sketch_text.stroke-7"),sQuery(id+"F2.wireOp",EDGE,"fcba4419-a2ee-464f-be9d-58f11bf3418b.sketch_text.stroke-8"),sQuery(id+"F2.wireOp",EDGE,"fcba4419-a2ee-464f-be9d-58f11bf3418b.sketch_text.stroke-9"),sQuery(id+"F2.wireOp",EDGE,"fcba4419-a2ee-464f-be9d-58f11bf3418b.sketch_text.stroke-10"),sQuery(id+"F2.wireOp",EDGE,"fcba4419-a2ee-464f-be9d-58f11bf3418b.sketch_text.stroke-11"),sQuery(id+"F2.wireOp",EDGE,"fcba4419-a2ee-464f-be9d-58f11bf3418b.sketch_text.stroke-12"),sQuery(id+"F2.wireOp",EDGE,"fcba4419-a2ee-464f-be9d-58f11bf3418b.sketch_text.stroke-13"),sQuery(id+"F2.wireOp",EDGE,"fcba4419-a2ee-464f-be9d-58f11bf3418b.sketch_text.stroke-14"),sQuery(id+"F2.wireOp",EDGE,"fcba4419-a2ee-464f-be9d-58f11bf3418b.sketch_text.stroke-15"),sQuery(id+"F2.wireOp",EDGE,"fcba4419-a2ee-464f-be9d-58f11bf3418b.sketch_text.stroke-16"),sQuery(id+"F2.wireOp",EDGE,"fcba4419-a2ee-464f-be9d-58f11bf3418b.sketch_text.stroke-17"),sQuery(id+"F2.wireOp",EDGE,"fcba4419-a2ee-464f-be9d-58f11bf3418b.sketch_text.stroke-18"),sQuery(id+"F2.wireOp",EDGE,"fcba4419-a2ee-464f-be9d-58f11bf3418b.sketch_text.stroke-19"),sQuery(id+"F2.wireOp",EDGE,"fcba4419-a2ee-464f-be9d-58f11bf3418b.sketch_text.stroke-20"),sQuery(id+"F2.wireOp",EDGE,"fcba4419-a2ee-464f-be9d-58f11bf3418b.sketch_text.stroke-21"),sQuery(id+"F2.wireOp",EDGE,"fcba4419-a2ee-464f-be9d-58f11bf3418b.sketch_text.stroke-22"),sQuery(id+"F2.wireOp",EDGE,"fcba4419-a2ee-464f-be9d-58f11bf3418b.sketch_text.stroke-23"),sQuery(id+"F2.wireOp",EDGE,"fcba4419-a2ee-464f-be9d-58f11bf3418b.sketch_text.stroke-24"),sQuery(id+"F2.wireOp",EDGE,"fcba4419-a2ee-464f-be9d-58f11bf3418b.sketch_text.stroke-25"),sQuery(id+"F2.wireOp",EDGE,"fcba4419-a2ee-464f-be9d-58f11bf3418b.sketch_text.stroke-26"),sQuery(id+"F2.wireOp",EDGE,"fcba4419-a2ee-464f-be9d-58f11bf3418b.sketch_text.stroke-27"),sQuery(id+"F2.wireOp",EDGE,"fcba4419-a2ee-464f-be9d-58f11bf3418b.sketch_text.stroke-28"),sQuery(id+"F2.wireOp",EDGE,"fcba4419-a2ee-464f-be9d-58f11bf3418b.sketch_text.stroke-29"),sQuery(id+"F2.wireOp",EDGE,"fcba4419-a2ee-464f-be9d-58f11bf3418b.sketch_text.stroke-30"),sQuery(id+"F2.wireOp",EDGE,"fcba4419-a2ee-464f-be9d-58f11bf3418b.sketch_text.stroke-31"),sQuery(id+"F2.wireOp",EDGE,"fcba4419-a2ee-464f-be9d-58f11bf3418b.sketch_text.stroke-32"),sQuery(id+"F2.wireOp",EDGE,"fcba4419-a2ee-464f-be9d-58f11bf3418b.sketch_text.stroke-33"),sQuery(id+"F2.wireOp",EDGE,"fcba4419-a2ee-464f-be9d-58f11bf3418b.sketch_text.stroke-34"),sQuery(id+"F2.wireOp",EDGE,"fcba4419-a2ee-464f-be9d-58f11bf3418b.sketch_text.stroke-35"),sQuery(id+"F2.wireOp",EDGE,"fcba4419-a2ee-464f-be9d-58f11bf3418b.sketch_text.stroke-36"),sQuery(id+"F2.wireOp",EDGE,"fcba4419-a2ee-464f-be9d-58f11bf3418b.sketch_text.stroke-37"),sQuery(id+"F2.wireOp",EDGE,"fcba4419-a2ee-464f-be9d-58f11bf3418b.sketch_text.stroke-38"),sQuery(id+"F2.wireOp",EDGE,"fcba4419-a2ee-464f-be9d-58f11bf3418b.sketch_text.stroke-39"),sQuery(id+"F2.wireOp",EDGE,"fcba4419-a2ee-464f-be9d-58f11bf3418b.sketch_text.stroke-40"),sQuery(id+"F2.wireOp",EDGE,"fcba4419-a2ee-464f-be9d-58f11bf3418b.sketch_text.stroke-41"),sQuery(id+"F2.wireOp",EDGE,"fcba4419-a2ee-464f-be9d-58f11bf3418b.sketch_text.stroke-42"),sQuery(id+"F2.wireOp",EDGE,"fcba4419-a2ee-464f-be9d-58f11bf3418b.sketch_text.stroke-43"),sQuery(id+"F2.wireOp",EDGE,"fcba4419-a2ee-464f-be9d-58f11bf3418b.sketch_text.stroke-44"),sQuery(id+"F2.wireOp",EDGE,"fcba4419-a2ee-464f-be9d-58f11bf3418b.sketch_text.stroke-45"),sQuery(id+"F2.wireOp",EDGE,"fcba4419-a2ee-464f-be9d-58f11bf3418b.sketch_text.stroke-46"),sQuery(id+"F2.wireOp",EDGE,"fcba4419-a2ee-464f-be9d-58f11bf3418b.sketch_text.stroke-47"),sQuery(id+"F2.wireOp",EDGE,"fcba4419-a2ee-464f-be9d-58f11bf3418b.sketch_text.stroke-48"),sQuery(id+"F2.wireOp",EDGE,"fcba4419-a2ee-464f-be9d-58f11bf3418b.sketch_text.stroke-49"),sQuery(id+"F2.wireOp",EDGE,"fcba4419-a2ee-464f-be9d-58f11bf3418b.sketch_text.stroke-50"),sQuery(id+"F2.wireOp",EDGE,"fcba4419-a2ee-464f-be9d-58f11bf3418b.sketch_text.stroke-51"),sQuery(id+"F2.wireOp",EDGE,"fcba4419-a2ee-464f-be9d-58f11bf3418b.sketch_text.stroke-52"),sQuery(id+"F2.wireOp",EDGE,"fcba4419-a2ee-464f-be9d-58f11bf3418b.sketch_text.stroke-53"),sQuery(id+"F2.wireOp",EDGE,"fcba4419-a2ee-464f-be9d-58f11bf3418b.sketch_text.stroke-54"),sQuery(id+"F2.wireOp",EDGE,"fcba4419-a2ee-464f-be9d-58f11bf3418b.sketch_text.stroke-55"),sQuery(id+"F2.wireOp",EDGE,"fcba4419-a2ee-464f-be9d-58f11bf3418b.sketch_text.stroke-56"),sQuery(id+"F2.wireOp",EDGE,"fcba4419-a2ee-464f-be9d-58f11bf3418b.sketch_text.stroke-57"),sQuery(id+"F2.wireOp",EDGE,"fcba4419-a2ee-464f-be9d-58f11bf3418b.sketch_text.stroke-58"),sQuery(id+"F2.wireOp",EDGE,"fcba4419-a2ee-464f-be9d-58f11bf3418b.sketch_text.stroke-59"),sQuery(id+"F2.wireOp",EDGE,"fcba4419-a2ee-464f-be9d-58f11bf3418b.sketch_text.stroke-60"),sQuery(id+"F2.wireOp",EDGE,"fcba4419-a2ee-464f-be9d-58f11bf3418b.sketch_text.stroke-61"),sQuery(id+"F2.wireOp",EDGE,"fcba4419-a2ee-464f-be9d-58f11bf3418b.sketch_text.stroke-62"),sQuery(id+"F2.wireOp",EDGE,"fcba4419-a2ee-464f-be9d-58f11bf3418b.sketch_text.stroke-63"),sQuery(id+"F2.wireOp",EDGE,"fcba4419-a2ee-464f-be9d-58f11bf3418b.sketch_text.stroke-64"),sQuery(id+"F2.wireOp",EDGE,"fcba4419-a2ee-464f-be9d-58f11bf3418b.sketch_text.stroke-65"),sQuery(id+"F2.wireOp",EDGE,"fcba4419-a2ee-464f-be9d-58f11bf3418b.sketch_text.stroke-66"),sQuery(id+"F2.wireOp",EDGE,"fcba4419-a2ee-464f-be9d-58f11bf3418b.sketch_text.stroke-67"),sQuery(id+"F2.wireOp",EDGE,"fcba4419-a2ee-464f-be9d-58f11bf3418b.sketch_text.stroke-68"),sQuery(id+"F2.wireOp",EDGE,"fcba4419-a2ee-464f-be9d-58f11bf3418b.sketch_text.stroke-69"),sQuery(id+"F2.wireOp",EDGE,"fcba4419-a2ee-464f-be9d-58f11bf3418b.sketch_text.stroke-70"),sQuery(id+"F2.wireOp",EDGE,"fcba4419-a2ee-464f-be9d-58f11bf3418b.sketch_text.stroke-71"),sQuery(id+"F2.wireOp",EDGE,"fcba4419-a2ee-464f-be9d-58f11bf3418b.sketch_text.stroke-72"),sQuery(id+"F2.wireOp",EDGE,"fcba4419-a2ee-464f-be9d-58f11bf3418b.sketch_text.stroke-73"),sQuery(id+"F2.wireOp",EDGE,"fcba4419-a2ee-464f-be9d-58f11bf3418b.sketch_text.stroke-74"),sQuery(id+"F2.wireOp",EDGE,"fcba4419-a2ee-464f-be9d-58f11bf3418b.sketch_text.stroke-75"),sQuery(id+"F2.wireOp",EDGE,"fcba4419-a2ee-464f-be9d-58f11bf3418b.sketch_text.stroke-76"),sQuery(id+"F2.wireOp",EDGE,"fcba4419-a2ee-464f-be9d-58f11bf3418b.sketch_text.stroke-77"),sQuery(id+"F2.wireOp",EDGE,"fcba4419-a2ee-464f-be9d-58f11bf3418b.sketch_text.stroke-78"),sQuery(id+"F2.wireOp",EDGE,"fcba4419-a2ee-464f-be9d-58f11bf3418b.sketch_text.stroke-79"),sQuery(id+"F2.wireOp",EDGE,"fcba4419-a2ee-464f-be9d-58f11bf3418b.sketch_text.stroke-80"),sQuery(id+"F2.wireOp",EDGE,"fcba4419-a2ee-464f-be9d-58f11bf3418b.sketch_text.stroke-81"),sQuery(id+"F2.wireOp",EDGE,"fcba4419-a2ee-464f-be9d-58f11bf3418b.sketch_text.stroke-82"),sQuery(id+"F2.wireOp",EDGE,"fcba4419-a2ee-464f-be9d-58f11bf3418b.sketch_text.stroke-83"),sQuery(id+"F2.wireOp",EDGE,"fcba4419-a2ee-464f-be9d-58f11bf3418b.sketch_text.stroke-84"),sQuery(id+"F2.wireOp",EDGE,"fcba4419-a2ee-464f-be9d-58f11bf3418b.sketch_text.stroke-85"),sQuery(id+"F2.wireOp",EDGE,"fcba4419-a2ee-464f-be9d-58f11bf3418b.sketch_text.stroke-86"),sQuery(id+"F2.wireOp",EDGE,"fcba4419-a2ee-464f-be9d-58f11bf3418b.sketch_text.stroke-87"),sQuery(id+"F2.wireOp",EDGE,"fcba4419-a2ee-464f-be9d-58f11bf3418b.sketch_text.stroke-88"),sQuery(id+"F2.wireOp",EDGE,"fcba4419-a2ee-464f-be9d-58f11bf3418b.sketch_text.stroke-89"),sQuery(id+"F2.wireOp",EDGE,"fcba4419-a2ee-464f-be9d-58f11bf3418b.sketch_text.stroke-90"),sQuery(id+"F2.wireOp",EDGE,"fcba4419-a2ee-464f-be9d-58f11bf3418b.sketch_text.stroke-91"),sQuery(id+"F2.wireOp",EDGE,"fcba4419-a2ee-464f-be9d-58f11bf3418b.sketch_text.stroke-92"),sQuery(id+"F2.wireOp",EDGE,"fcba4419-a2ee-464f-be9d-58f11bf3418b.sketch_text.stroke-93"),sQuery(id+"F2.wireOp",EDGE,"fcba4419-a2ee-464f-be9d-58f11bf3418b.sketch_text.stroke-94"),sQuery(id+"F2.wireOp",EDGE,"fcba4419-a2ee-464f-be9d-58f11bf3418b.sketch_text.stroke-95"),sQuery(id+"F2.wireOp",EDGE,"fcba4419-a2ee-464f-be9d-58f11bf3418b.sketch_text.stroke-96"),sQuery(id+"F2.wireOp",EDGE,"fcba4419-a2ee-464f-be9d-58f11bf3418b.sketch_text.stroke-97"),sQuery(id+"F2.wireOp",EDGE,"fcba4419-a2ee-464f-be9d-58f11bf3418b.sketch_text.stroke-98"),sQuery(id+"F2.wireOp",EDGE,"fcba4419-a2ee-464f-be9d-58f11bf3418b.sketch_text.stroke-99"),sQuery(id+"F2.wireOp",EDGE,"fcba4419-a2ee-464f-be9d-58f11bf3418b.sketch_text.stroke-100"),sQuery(id+"F2.wireOp",EDGE,"fcba4419-a2ee-464f-be9d-58f11bf3418b.sketch_text.stroke-101"),sQuery(id+"F2.wireOp",EDGE,"fcba4419-a2ee-464f-be9d-58f11bf3418b.sketch_text.stroke-102"),sQuery(id+"F2.wireOp",EDGE,"fcba4419-a2ee-464f-be9d-58f11bf3418b.sketch_text.stroke-103"),sQuery(id+"F2.wireOp",EDGE,"fcba4419-a2ee-464f-be9d-58f11bf3418b.sketch_text.stroke-104"),sQuery(id+"F2.wireOp",EDGE,"fcba4419-a2ee-464f-be9d-58f11bf3418b.sketch_text.stroke-105"),sQuery(id+"F2.wireOp",EDGE,"fcba4419-a2ee-464f-be9d-58f11bf3418b.sketch_text.stroke-106"),sQuery(id+"F2.wireOp",EDGE,"fcba4419-a2ee-464f-be9d-58f11bf3418b.sketch_text.stroke-107"),sQuery(id+"F2.wireOp",EDGE,"fcba4419-a2ee-464f-be9d-58f11bf3418b.sketch_text.stroke-108"),sQuery(id+"F2.wireOp",EDGE,"fcba4419-a2ee-464f-be9d-58f11bf3418b.sketch_text.stroke-109"),sQuery(id+"F2.wireOp",EDGE,"fcba4419-a2ee-464f-be9d-58f11bf3418b.sketch_text.stroke-110"),sQuery(id+"F2.wireOp",EDGE,"fcba4419-a2ee-464f-be9d-58f11bf3418b.sketch_text.stroke-111"),sQuery(id+"F2.wireOp",EDGE,"fcba4419-a2ee-464f-be9d-58f11bf3418b.sketch_text.stroke-112"),sQuery(id+"F2.wireOp",EDGE,"fcba4419-a2ee-464f-be9d-58f11bf3418b.sketch_text.stroke-113"),sQuery(id+"F2.wireOp",EDGE,"fcba4419-a2ee-464f-be9d-58f11bf3418b.sketch_text.stroke-114"),sQuery(id+"F2.wireOp",EDGE,"fcba4419-a2ee-464f-be9d-58f11bf3418b.sketch_text.stroke-115"),sQuery(id+"F2.wireOp",EDGE,"fcba4419-a2ee-464f-be9d-58f11bf3418b.sketch_text.stroke-116"),sQuery(id+"F2.wireOp",EDGE,"fcba4419-a2ee-464f-be9d-58f11bf3418b.sketch_text.stroke-117"),sQuery(id+"F2.wireOp",EDGE,"fcba4419-a2ee-464f-be9d-58f11bf3418b.sketch_text.stroke-118"),sQuery(id+"F2.wireOp",EDGE,"fcba4419-a2ee-464f-be9d-58f11bf3418b.sketch_text.stroke-119"),sQuery(id+"F2.wireOp",EDGE,"fcba4419-a2ee-464f-be9d-58f11bf3418b.sketch_text.stroke-120"),sQuery(id+"F2.wireOp",EDGE,"fcba4419-a2ee-464f-be9d-58f11bf3418b.sketch_text.stroke-121"),sQuery(id+"F2.wireOp",EDGE,"fcba4419-a2ee-464f-be9d-58f11bf3418b.sketch_text.stroke-122"),sQuery(id+"F2.wireOp",EDGE,"fcba4419-a2ee-464f-be9d-58f11bf3418b.sketch_text.stroke-123"),sQuery(id+"F2.wireOp",EDGE,"fcba4419-a2ee-464f-be9d-58f11bf3418b.sketch_text.stroke-124"),sQuery(id+"F2.wireOp",EDGE,"fcba4419-a2ee-464f-be9d-58f11bf3418b.sketch_text.stroke-125"),sQuery(id+"F2.wireOp",EDGE,"fcba4419-a2ee-464f-be9d-58f11bf3418b.sketch_text.stroke-126"),sQuery(id+"F2.wireOp",EDGE,"fcba4419-a2ee-464f-be9d-58f11bf3418b.sketch_text.stroke-127"),sQuery(id+"F2.wireOp",EDGE,"fcba4419-a2ee-464f-be9d-58f11bf3418b.sketch_text.stroke-128"),sQuery(id+"F2.wireOp",EDGE,"fcba4419-a2ee-464f-be9d-58f11bf3418b.sketch_text.stroke-129"),sQuery(id+"F2.wireOp",EDGE,"fcba4419-a2ee-464f-be9d-58f11bf3418b.sketch_text.stroke-130"),sQuery(id+"F2.wireOp",EDGE,"fcba4419-a2ee-464f-be9d-58f11bf3418b.sketch_text.stroke-131"),sQuery(id+"F2.wireOp",EDGE,"fcba4419-a2ee-464f-be9d-58f11bf3418b.sketch_text.stroke-132"),sQuery(id+"F2.wireOp",EDGE,"fcba4419-a2ee-464f-be9d-58f11bf3418b.sketch_text.stroke-133"),sQuery(id+"F2.wireOp",EDGE,"fcba4419-a2ee-464f-be9d-58f11bf3418b.sketch_text.stroke-134"),sQuery(id+"F2.wireOp",EDGE,"fcba4419-a2ee-464f-be9d-58f11bf3418b.sketch_text.stroke-135"),sQuery(id+"F2.wireOp",EDGE,"fcba4419-a2ee-464f-be9d-58f11bf3418b.sketch_text.stroke-136"),sQuery(id+"F2.wireOp",EDGE,"fcba4419-a2ee-464f-be9d-58f11bf3418b.sketch_text.stroke-137"),sQuery(id+"F2.wireOp",EDGE,"fcba4419-a2ee-464f-be9d-58f11bf3418b.sketch_text.stroke-138"),sQuery(id+"F2.wireOp",EDGE,"fcba4419-a2ee-464f-be9d-58f11bf3418b.sketch_text.stroke-139"),sQuery(id+"F2.wireOp",EDGE,"fcba4419-a2ee-464f-be9d-58f11bf3418b.sketch_text.stroke-140"),sQuery(id+"F2.wireOp",EDGE,"fcba4419-a2ee-464f-be9d-58f11bf3418b.sketch_text.stroke-141"),sQuery(id+"F2.wireOp",EDGE,"fcba4419-a2ee-464f-be9d-58f11bf3418b.sketch_text.stroke-142"),sQuery(id+"F2.wireOp",EDGE,"fcba4419-a2ee-464f-be9d-58f11bf3418b.sketch_text.stroke-143"),sQuery(id+"F2.wireOp",EDGE,"fcba4419-a2ee-464f-be9d-58f11bf3418b.sketch_text.stroke-144"),sQuery(id+"F2.wireOp",EDGE,"fcba4419-a2ee-464f-be9d-58f11bf3418b.sketch_text.stroke-145"),sQuery(id+"F2.wireOp",EDGE,"fcba4419-a2ee-464f-be9d-58f11bf3418b.sketch_text.stroke-146"),sQuery(id+"F2.wireOp",EDGE,"fcba4419-a2ee-464f-be9d-58f11bf3418b.sketch_text.stroke-147"),sQuery(id+"F2.wireOp",EDGE,"fcba4419-a2ee-464f-be9d-58f11bf3418b.sketch_text.stroke-148"),sQuery(id+"F2.wireOp",EDGE,"fcba4419-a2ee-464f-be9d-58f11bf3418b.sketch_text.stroke-149"),sQuery(id+"F2.wireOp",EDGE,"fcba4419-a2ee-464f-be9d-58f11bf3418b.sketch_text.stroke-150"),sQuery(id+"F2.wireOp",EDGE,"fcba4419-a2ee-464f-be9d-58f11bf3418b.sketch_text.stroke-151"),sQuery(id+"F2.wireOp",EDGE,"fcba4419-a2ee-464f-be9d-58f11bf3418b.sketch_text.stroke-152"),sQuery(id+"F2.wireOp",EDGE,"fcba4419-a2ee-464f-be9d-58f11bf3418b.sketch_text.stroke-153"),sQuery(id+"F2.wireOp",EDGE,"fcba4419-a2ee-464f-be9d-58f11bf3418b.sketch_text.stroke-154"),sQuery(id+"F2.wireOp",EDGE,"fcba4419-a2ee-464f-be9d-58f11bf3418b.sketch_text.stroke-155"),sQuery(id+"F2.wireOp",EDGE,"fcba4419-a2ee-464f-be9d-58f11bf3418b.sketch_text.stroke-156"),sQuery(id+"F2.wireOp",EDGE,"fcba4419-a2ee-464f-be9d-58f11bf3418b.sketch_text.stroke-157"),sQuery(id+"F2.wireOp",EDGE,"fcba4419-a2ee-464f-be9d-58f11bf3418b.sketch_text.stroke-158"),sQuery(id+"F2.wireOp",EDGE,"fcba4419-a2ee-464f-be9d-58f11bf3418b.sketch_text.stroke-159"),sQuery(id+"F2.wireOp",EDGE,"fcba4419-a2ee-464f-be9d-58f11bf3418b.sketch_text.stroke-160"),sQuery(id+"F2.wireOp",EDGE,"fcba4419-a2ee-464f-be9d-58f11bf3418b.sketch_text.stroke-161"),sQuery(id+"F2.wireOp",EDGE,"fcba4419-a2ee-464f-be9d-58f11bf3418b.sketch_text.stroke-162"),sQuery(id+"F2.wireOp",EDGE,"fcba4419-a2ee-464f-be9d-58f11bf3418b.sketch_text.stroke-163"),sQuery(id+"F2.wireOp",EDGE,"fcba4419-a2ee-464f-be9d-58f11bf3418b.sketch_text.stroke-164"),sQuery(id+"F2.wireOp",EDGE,"fcba4419-a2ee-464f-be9d-58f11bf3418b.sketch_text.stroke-165"),sQuery(id+"F2.wireOp",EDGE,"fcba4419-a2ee-464f-be9d-58f11bf3418b.sketch_text.stroke-166"),sQuery(id+"F2.wireOp",EDGE,"fcba4419-a2ee-464f-be9d-58f11bf3418b.sketch_text.stroke-167"),sQuery(id+"F2.wireOp",EDGE,"fcba4419-a2ee-464f-be9d-58f11bf3418b.sketch_text.stroke-168"),sQuery(id+"F2.wireOp",EDGE,"fcba4419-a2ee-464f-be9d-58f11bf3418b.sketch_text.stroke-169"),sQuery(id+"F2.wireOp",EDGE,"fcba4419-a2ee-464f-be9d-58f11bf3418b.sketch_text.stroke-170"),sQuery(id+"F2.wireOp",EDGE,"fcba4419-a2ee-464f-be9d-58f11bf3418b.sketch_text.stroke-171"),sQuery(id+"F2.wireOp",EDGE,"fcba4419-a2ee-464f-be9d-58f11bf3418b.sketch_text.stroke-172"),sQuery(id+"F2.wireOp",EDGE,"fcba4419-a2ee-464f-be9d-58f11bf3418b.sketch_text.stroke-173"),sQuery(id+"FHMxAyK4CFUKdhS_1.wireOp",EDGE,"1cb9c079-ea9b-4899-8069-e0e3048e911d.sketch_text.stroke-0"),sQuery(id+"FHMxAyK4CFUKdhS_1.wireOp",EDGE,"1cb9c079-ea9b-4899-8069-e0e3048e911d.sketch_text.stroke-1"),sQuery(id+"FHMxAyK4CFUKdhS_1.wireOp",EDGE,"1cb9c079-ea9b-4899-8069-e0e3048e911d.sketch_text.stroke-2"),sQuery(id+"FHMxAyK4CFUKdhS_1.wireOp",EDGE,"1cb9c079-ea9b-4899-8069-e0e3048e911d.sketch_text.stroke-3"),sQuery(id+"FHMxAyK4CFUKdhS_1.wireOp",EDGE,"1cb9c079-ea9b-4899-8069-e0e3048e911d.sketch_text.stroke-4"),sQuery(id+"FHMxAyK4CFUKdhS_1.wireOp",EDGE,"1cb9c079-ea9b-4899-8069-e0e3048e911d.sketch_text.stroke-5"),sQuery(id+"FHMxAyK4CFUKdhS_1.wireOp",EDGE,"1cb9c079-ea9b-4899-8069-e0e3048e911d.sketch_text.stroke-6"),sQuery(id+"FHMxAyK4CFUKdhS_1.wireOp",EDGE,"1cb9c079-ea9b-4899-8069-e0e3048e911d.sketch_text.stroke-7"),sQuery(id+"FHMxAyK4CFUKdhS_1.wireOp",EDGE,"1cb9c079-ea9b-4899-8069-e0e3048e911d.sketch_text.stroke-8"),sQuery(id+"FHMxAyK4CFUKdhS_1.wireOp",EDGE,"1cb9c079-ea9b-4899-8069-e0e3048e911d.sketch_text.stroke-9"),sQuery(id+"FHMxAyK4CFUKdhS_1.wireOp",EDGE,"1cb9c079-ea9b-4899-8069-e0e3048e911d.sketch_text.stroke-10"),sQuery(id+"FHMxAyK4CFUKdhS_1.wireOp",EDGE,"1cb9c079-ea9b-4899-8069-e0e3048e911d.sketch_text.stroke-11"),sQuery(id+"FHMxAyK4CFUKdhS_1.wireOp",EDGE,"1cb9c079-ea9b-4899-8069-e0e3048e911d.sketch_text.stroke-12"),sQuery(id+"FHMxAyK4CFUKdhS_1.wireOp",EDGE,"1cb9c079-ea9b-4899-8069-e0e3048e911d.sketch_text.stroke-13"),sQuery(id+"FHMxAyK4CFUKdhS_1.wireOp",EDGE,"1cb9c079-ea9b-4899-8069-e0e3048e911d.sketch_text.stroke-14"),sQuery(id+"FHMxAyK4CFUKdhS_1.wireOp",EDGE,"1cb9c079-ea9b-4899-8069-e0e3048e911d.sketch_text.stroke-15"),sQuery(id+"FHMxAyK4CFUKdhS_1.wireOp",EDGE,"1cb9c079-ea9b-4899-8069-e0e3048e911d.sketch_text.stroke-16"),sQuery(id+"FHMxAyK4CFUKdhS_1.wireOp",EDGE,"1cb9c079-ea9b-4899-8069-e0e3048e911d.sketch_text.stroke-17"),sQuery(id+"FHMxAyK4CFUKdhS_1.wireOp",EDGE,"1cb9c079-ea9b-4899-8069-e0e3048e911d.sketch_text.stroke-18"),sQuery(id+"FHMxAyK4CFUKdhS_1.wireOp",EDGE,"1cb9c079-ea9b-4899-8069-e0e3048e911d.sketch_text.stroke-19"),sQuery(id+"FHMxAyK4CFUKdhS_1.wireOp",EDGE,"1cb9c079-ea9b-4899-8069-e0e3048e911d.sketch_text.stroke-20"),sQuery(id+"FHMxAyK4CFUKdhS_1.wireOp",EDGE,"1cb9c079-ea9b-4899-8069-e0e3048e911d.sketch_text.stroke-21"),sQuery(id+"FHMxAyK4CFUKdhS_1.wireOp",EDGE,"1cb9c079-ea9b-4899-8069-e0e3048e911d.sketch_text.stroke-22"),sQuery(id+"FHMxAyK4CFUKdhS_1.wireOp",EDGE,"1cb9c079-ea9b-4899-8069-e0e3048e911d.sketch_text.stroke-23"),sQuery(id+"FHMxAyK4CFUKdhS_1.wireOp",EDGE,"1cb9c079-ea9b-4899-8069-e0e3048e911d.sketch_text.stroke-24"),sQuery(id+"FHMxAyK4CFUKdhS_1.wireOp",EDGE,"1cb9c079-ea9b-4899-8069-e0e3048e911d.sketch_text.stroke-25"),sQuery(id+"FHMxAyK4CFUKdhS_1.wireOp",EDGE,"1cb9c079-ea9b-4899-8069-e0e3048e911d.sketch_text.stroke-26"),sQuery(id+"FHMxAyK4CFUKdhS_1.wireOp",EDGE,"1cb9c079-ea9b-4899-8069-e0e3048e911d.sketch_text.stroke-27"),sQuery(id+"FHMxAyK4CFUKdhS_1.wireOp",EDGE,"1cb9c079-ea9b-4899-8069-e0e3048e911d.sketch_text.stroke-28"),sQuery(id+"FHMxAyK4CFUKdhS_1.wireOp",EDGE,"1cb9c079-ea9b-4899-8069-e0e3048e911d.sketch_text.stroke-29"),sQuery(id+"FHMxAyK4CFUKdhS_1.wireOp",EDGE,"1cb9c079-ea9b-4899-8069-e0e3048e911d.sketch_text.stroke-30"),sQuery(id+"FHMxAyK4CFUKdhS_1.wireOp",EDGE,"1cb9c079-ea9b-4899-8069-e0e3048e911d.sketch_text.stroke-31"),sQuery(id+"FHMxAyK4CFUKdhS_1.wireOp",EDGE,"1cb9c079-ea9b-4899-8069-e0e3048e911d.sketch_text.stroke-32"),sQuery(id+"FHMxAyK4CFUKdhS_1.wireOp",EDGE,"1cb9c079-ea9b-4899-8069-e0e3048e911d.sketch_text.stroke-33"),sQuery(id+"FHMxAyK4CFUKdhS_1.wireOp",EDGE,"1cb9c079-ea9b-4899-8069-e0e3048e911d.sketch_text.stroke-34"),sQuery(id+"FHMxAyK4CFUKdhS_1.wireOp",EDGE,"1cb9c079-ea9b-4899-8069-e0e3048e911d.sketch_text.stroke-35"),sQuery(id+"FHMxAyK4CFUKdhS_1.wireOp",EDGE,"1cb9c079-ea9b-4899-8069-e0e3048e911d.sketch_text.stroke-36"),sQuery(id+"FHMxAyK4CFUKdhS_1.wireOp",EDGE,"1cb9c079-ea9b-4899-8069-e0e3048e911d.sketch_text.stroke-37"),sQuery(id+"FHMxAyK4CFUKdhS_1.wireOp",EDGE,"1cb9c079-ea9b-4899-8069-e0e3048e911d.sketch_text.stroke-38"),sQuery(id+"FHMxAyK4CFUKdhS_1.wireOp",EDGE,"1cb9c079-ea9b-4899-8069-e0e3048e911d.sketch_text.stroke-39"),sQuery(id+"FHMxAyK4CFUKdhS_1.wireOp",EDGE,"1cb9c079-ea9b-4899-8069-e0e3048e911d.sketch_text.stroke-40"),sQuery(id+"FHMxAyK4CFUKdhS_1.wireOp",EDGE,"1cb9c079-ea9b-4899-8069-e0e3048e911d.sketch_text.stroke-41"),sQuery(id+"FHMxAyK4CFUKdhS_1.wireOp",EDGE,"1cb9c079-ea9b-4899-8069-e0e3048e911d.sketch_text.stroke-42"),sQuery(id+"FHMxAyK4CFUKdhS_1.wireOp",EDGE,"1cb9c079-ea9b-4899-8069-e0e3048e911d.sketch_text.stroke-43"),sQuery(id+"FHMxAyK4CFUKdhS_1.wireOp",EDGE,"1cb9c079-ea9b-4899-8069-e0e3048e911d.sketch_text.stroke-44"),sQuery(id+"FHMxAyK4CFUKdhS_1.wireOp",EDGE,"1cb9c079-ea9b-4899-8069-e0e3048e911d.sketch_text.stroke-45"),sQuery(id+"FHMxAyK4CFUKdhS_1.wireOp",EDGE,"1cb9c079-ea9b-4899-8069-e0e3048e911d.sketch_text.stroke-46"),sQuery(id+"FHMxAyK4CFUKdhS_1.wireOp",EDGE,"1cb9c079-ea9b-4899-8069-e0e3048e911d.sketch_text.stroke-47"),sQuery(id+"FHMxAyK4CFUKdhS_1.wireOp",EDGE,"1cb9c079-ea9b-4899-8069-e0e3048e911d.sketch_text.stroke-48"),sQuery(id+"FHMxAyK4CFUKdhS_1.wireOp",EDGE,"1cb9c079-ea9b-4899-8069-e0e3048e911d.sketch_text.stroke-49"),sQuery(id+"FHMxAyK4CFUKdhS_1.wireOp",EDGE,"1cb9c079-ea9b-4899-8069-e0e3048e911d.sketch_text.stroke-50"),sQuery(id+"FHMxAyK4CFUKdhS_1.wireOp",EDGE,"1cb9c079-ea9b-4899-8069-e0e3048e911d.sketch_text.stroke-51"),sQuery(id+"FHMxAyK4CFUKdhS_1.wireOp",EDGE,"1cb9c079-ea9b-4899-8069-e0e3048e911d.sketch_text.stroke-52"),sQuery(id+"FHMxAyK4CFUKdhS_1.wireOp",EDGE,"1cb9c079-ea9b-4899-8069-e0e3048e911d.sketch_text.stroke-53"),sQuery(id+"FHMxAyK4CFUKdhS_1.wireOp",EDGE,"1cb9c079-ea9b-4899-8069-e0e3048e911d.sketch_text.stroke-54"),sQuery(id+"FHMxAyK4CFUKdhS_1.wireOp",EDGE,"1cb9c079-ea9b-4899-8069-e0e3048e911d.sketch_text.stroke-55"),sQuery(id+"FHMxAyK4CFUKdhS_1.wireOp",EDGE,"1cb9c079-ea9b-4899-8069-e0e3048e911d.sketch_text.stroke-56"),sQuery(id+"FHMxAyK4CFUKdhS_1.wireOp",EDGE,"1cb9c079-ea9b-4899-8069-e0e3048e911d.sketch_text.stroke-57"),sQuery(id+"FHMxAyK4CFUKdhS_1.wireOp",EDGE,"1cb9c079-ea9b-4899-8069-e0e3048e911d.sketch_text.stroke-58"),sQuery(id+"FHMxAyK4CFUKdhS_1.wireOp",EDGE,"1cb9c079-ea9b-4899-8069-e0e3048e911d.sketch_text.stroke-59"),sQuery(id+"FHMxAyK4CFUKdhS_1.wireOp",EDGE,"1cb9c079-ea9b-4899-8069-e0e3048e911d.sketch_text.stroke-60"),sQuery(id+"FHMxAyK4CFUKdhS_1.wireOp",EDGE,"1cb9c079-ea9b-4899-8069-e0e3048e911d.sketch_text.stroke-61"),sQuery(id+"FHMxAyK4CFUKdhS_1.wireOp",EDGE,"1cb9c079-ea9b-4899-8069-e0e3048e911d.sketch_text.stroke-62"),sQuery(id+"FHMxAyK4CFUKdhS_1.wireOp",EDGE,"1cb9c079-ea9b-4899-8069-e0e3048e911d.sketch_text.stroke-71"),sQuery(id+"FHMxAyK4CFUKdhS_1.wireOp",EDGE,"1cb9c079-ea9b-4899-8069-e0e3048e911d.sketch_text.stroke-72"),sQuery(id+"FHMxAyK4CFUKdhS_1.wireOp",EDGE,"1cb9c079-ea9b-4899-8069-e0e3048e911d.sketch_text.stroke-73"),sQuery(id+"FHMxAyK4CFUKdhS_1.wireOp",EDGE,"1cb9c079-ea9b-4899-8069-e0e3048e911d.sketch_text.stroke-74"),sQuery(id+"FHMxAyK4CFUKdhS_1.wireOp",EDGE,"1cb9c079-ea9b-4899-8069-e0e3048e911d.sketch_text.stroke-75"),sQuery(id+"FHMxAyK4CFUKdhS_1.wireOp",EDGE,"1cb9c079-ea9b-4899-8069-e0e3048e911d.sketch_text.stroke-76"),sQuery(id+"FHMxAyK4CFUKdhS_1.wireOp",EDGE,"1cb9c079-ea9b-4899-8069-e0e3048e911d.sketch_text.stroke-77"),sQuery(id+"FHMxAyK4CFUKdhS_1.wireOp",EDGE,"1cb9c079-ea9b-4899-8069-e0e3048e911d.sketch_text.stroke-78"),sQuery(id+"FHMxAyK4CFUKdhS_1.wireOp",EDGE,"1cb9c079-ea9b-4899-8069-e0e3048e911d.sketch_text.stroke-79"),sQuery(id+"FHMxAyK4CFUKdhS_1.wireOp",EDGE,"1cb9c079-ea9b-4899-8069-e0e3048e911d.sketch_text.stroke-80"),sQuery(id+"FHMxAyK4CFUKdhS_1.wireOp",EDGE,"1cb9c079-ea9b-4899-8069-e0e3048e911d.sketch_text.stroke-81"),sQuery(id+"FHMxAyK4CFUKdhS_1.wireOp",EDGE,"1cb9c079-ea9b-4899-8069-e0e3048e911d.sketch_text.stroke-82"),sQuery(id+"FHMxAyK4CFUKdhS_1.wireOp",EDGE,"1cb9c079-ea9b-4899-8069-e0e3048e911d.sketch_text.stroke-83"),sQuery(id+"FHMxAyK4CFUKdhS_1.wireOp",EDGE,"1cb9c079-ea9b-4899-8069-e0e3048e911d.sketch_text.stroke-84"),sQuery(id+"FHMxAyK4CFUKdhS_1.wireOp",EDGE,"1cb9c079-ea9b-4899-8069-e0e3048e911d.sketch_text.stroke-85"),sQuery(id+"FHMxAyK4CFUKdhS_1.wireOp",EDGE,"1cb9c079-ea9b-4899-8069-e0e3048e911d.sketch_text.stroke-86"),sQuery(id+"FHMxAyK4CFUKdhS_1.wireOp",EDGE,"1cb9c079-ea9b-4899-8069-e0e3048e911d.sketch_text.stroke-87"),sQuery(id+"FHMxAyK4CFUKdhS_1.wireOp",EDGE,"1cb9c079-ea9b-4899-8069-e0e3048e911d.sketch_text.stroke-88"),sQuery(id+"FHMxAyK4CFUKdhS_1.wireOp",EDGE,"1cb9c079-ea9b-4899-8069-e0e3048e911d.sketch_text.stroke-89"),sQuery(id+"FHMxAyK4CFUKdhS_1.wireOp",EDGE,"1cb9c079-ea9b-4899-8069-e0e3048e911d.sketch_text.stroke-90"),sQuery(id+"FHMxAyK4CFUKdhS_1.wireOp",EDGE,"1cb9c079-ea9b-4899-8069-e0e3048e911d.sketch_text.stroke-91"),sQuery(id+"FHMxAyK4CFUKdhS_1.wireOp",EDGE,"1cb9c079-ea9b-4899-8069-e0e3048e911d.sketch_text.stroke-92"),sQuery(id+"FHMxAyK4CFUKdhS_1.wireOp",EDGE,"1cb9c079-ea9b-4899-8069-e0e3048e911d.sketch_text.stroke-93"),sQuery(id+"FHMxAyK4CFUKdhS_1.wireOp",EDGE,"1cb9c079-ea9b-4899-8069-e0e3048e911d.sketch_text.stroke-94"),sQuery(id+"FHMxAyK4CFUKdhS_1.wireOp",EDGE,"1cb9c079-ea9b-4899-8069-e0e3048e911d.sketch_text.stroke-95"),sQuery(id+"FHMxAyK4CFUKdhS_1.wireOp",EDGE,"1cb9c079-ea9b-4899-8069-e0e3048e911d.sketch_text.stroke-96"),sQuery(id+"FHMxAyK4CFUKdhS_1.wireOp",EDGE,"1cb9c079-ea9b-4899-8069-e0e3048e911d.sketch_text.stroke-97"),sQuery(id+"FHMxAyK4CFUKdhS_1.wireOp",EDGE,"1cb9c079-ea9b-4899-8069-e0e3048e911d.sketch_text.stroke-103"),sQuery(id+"FHMxAyK4CFUKdhS_1.wireOp",EDGE,"1cb9c079-ea9b-4899-8069-e0e3048e911d.sketch_text.stroke-104"),sQuery(id+"FHMxAyK4CFUKdhS_1.wireOp",EDGE,"1cb9c079-ea9b-4899-8069-e0e3048e911d.sketch_text.stroke-105"),sQuery(id+"FHMxAyK4CFUKdhS_1.wireOp",EDGE,"1cb9c079-ea9b-4899-8069-e0e3048e911d.sketch_text.stroke-106"),sQuery(id+"FHMxAyK4CFUKdhS_1.wireOp",EDGE,"1cb9c079-ea9b-4899-8069-e0e3048e911d.sketch_text.stroke-107"),sQuery(id+"FHMxAyK4CFUKdhS_1.wireOp",EDGE,"1cb9c079-ea9b-4899-8069-e0e3048e911d.sketch_text.stroke-108"),sQuery(id+"FHMxAyK4CFUKdhS_1.wireOp",EDGE,"1cb9c079-ea9b-4899-8069-e0e3048e911d.sketch_text.stroke-109"),sQuery(id+"FHMxAyK4CFUKdhS_1.wireOp",EDGE,"1cb9c079-ea9b-4899-8069-e0e3048e911d.sketch_text.stroke-110"),sQuery(id+"FHMxAyK4CFUKdhS_1.wireOp",EDGE,"1cb9c079-ea9b-4899-8069-e0e3048e911d.sketch_text.stroke-111"),sQuery(id+"FHMxAyK4CFUKdhS_1.wireOp",EDGE,"1cb9c079-ea9b-4899-8069-e0e3048e911d.sketch_text.stroke-112"),sQuery(id+"FHMxAyK4CFUKdhS_1.wireOp",EDGE,"1cb9c079-ea9b-4899-8069-e0e3048e911d.sketch_text.stroke-113"),sQuery(id+"FHMxAyK4CFUKdhS_1.wireOp",EDGE,"1cb9c079-ea9b-4899-8069-e0e3048e911d.sketch_text.stroke-114"),sQuery(id+"FHMxAyK4CFUKdhS_1.wireOp",EDGE,"1cb9c079-ea9b-4899-8069-e0e3048e911d.sketch_text.stroke-115"),sQuery(id+"FHMxAyK4CFUKdhS_1.wireOp",EDGE,"1cb9c079-ea9b-4899-8069-e0e3048e911d.sketch_text.stroke-116"),sQuery(id+"FHMxAyK4CFUKdhS_1.wireOp",EDGE,"1cb9c079-ea9b-4899-8069-e0e3048e911d.sketch_text.stroke-117"),sQuery(id+"FHMxAyK4CFUKdhS_1.wireOp",EDGE,"1cb9c079-ea9b-4899-8069-e0e3048e911d.sketch_text.stroke-118"),sQuery(id+"FHMxAyK4CFUKdhS_1.wireOp",EDGE,"1cb9c079-ea9b-4899-8069-e0e3048e911d.sketch_text.stroke-119"),sQuery(id+"FHMxAyK4CFUKdhS_1.wireOp",EDGE,"1cb9c079-ea9b-4899-8069-e0e3048e911d.sketch_text.stroke-120"),sQuery(id+"FHMxAyK4CFUKdhS_1.wireOp",EDGE,"1cb9c079-ea9b-4899-8069-e0e3048e911d.sketch_text.stroke-121"),sQuery(id+"FHMxAyK4CFUKdhS_1.wireOp",EDGE,"1cb9c079-ea9b-4899-8069-e0e3048e911d.sketch_text.stroke-122"),sQuery(id+"FHMxAyK4CFUKdhS_1.wireOp",EDGE,"1cb9c079-ea9b-4899-8069-e0e3048e911d.sketch_text.stroke-123"),sQuery(id+"FHMxAyK4CFUKdhS_1.wireOp",EDGE,"1cb9c079-ea9b-4899-8069-e0e3048e911d.sketch_text.stroke-124"),sQuery(id+"FHMxAyK4CFUKdhS_1.wireOp",EDGE,"1cb9c079-ea9b-4899-8069-e0e3048e911d.sketch_text.stroke-125"),sQuery(id+"FHMxAyK4CFUKdhS_1.wireOp",EDGE,"1cb9c079-ea9b-4899-8069-e0e3048e911d.sketch_text.stroke-126"),sQuery(id+"FHMxAyK4CFUKdhS_1.wireOp",EDGE,"1cb9c079-ea9b-4899-8069-e0e3048e911d.sketch_text.stroke-127"),sQuery(id+"FHMxAyK4CFUKdhS_1.wireOp",EDGE,"1cb9c079-ea9b-4899-8069-e0e3048e911d.sketch_text.stroke-128"),sQuery(id+"FHMxAyK4CFUKdhS_1.wireOp",EDGE,"1cb9c079-ea9b-4899-8069-e0e3048e911d.sketch_text.stroke-129"),sQuery(id+"FHMxAyK4CFUKdhS_1.wireOp",EDGE,"1cb9c079-ea9b-4899-8069-e0e3048e911d.sketch_text.stroke-130"),sQuery(id+"FHMxAyK4CFUKdhS_1.wireOp",EDGE,"1cb9c079-ea9b-4899-8069-e0e3048e911d.sketch_text.stroke-131"),sQuery(id+"FHMxAyK4CFUKdhS_1.wireOp",EDGE,"1cb9c079-ea9b-4899-8069-e0e3048e911d.sketch_text.stroke-132"),sQuery(id+"FHMxAyK4CFUKdhS_1.wireOp",EDGE,"1cb9c079-ea9b-4899-8069-e0e3048e911d.sketch_text.stroke-133"),sQuery(id+"FHMxAyK4CFUKdhS_1.wireOp",EDGE,"1cb9c079-ea9b-4899-8069-e0e3048e911d.sketch_text.stroke-134"),sQuery(id+"FHMxAyK4CFUKdhS_1.wireOp",EDGE,"1cb9c079-ea9b-4899-8069-e0e3048e911d.sketch_text.stroke-135"),sQuery(id+"FHMxAyK4CFUKdhS_1.wireOp",EDGE,"1cb9c079-ea9b-4899-8069-e0e3048e911d.sketch_text.stroke-136"),sQuery(id+"FHMxAyK4CFUKdhS_1.wireOp",EDGE,"1cb9c079-ea9b-4899-8069-e0e3048e911d.sketch_text.stroke-137"),sQuery(id+"FHMxAyK4CFUKdhS_1.wireOp",EDGE,"1cb9c079-ea9b-4899-8069-e0e3048e911d.sketch_text.stroke-138"),sQuery(id+"FHMxAyK4CFUKdhS_1.wireOp",EDGE,"1cb9c079-ea9b-4899-8069-e0e3048e911d.sketch_text.stroke-139"),sQuery(id+"FHMxAyK4CFUKdhS_1.wireOp",EDGE,"1cb9c079-ea9b-4899-8069-e0e3048e911d.sketch_text.stroke-140"),sQuery(id+"FHMxAyK4CFUKdhS_1.wireOp",EDGE,"1cb9c079-ea9b-4899-8069-e0e3048e911d.sketch_text.stroke-141"),sQuery(id+"FHMxAyK4CFUKdhS_1.wireOp",EDGE,"1cb9c079-ea9b-4899-8069-e0e3048e911d.sketch_text.stroke-142"),sQuery(id+"FHMxAyK4CFUKdhS_1.wireOp",EDGE,"1cb9c079-ea9b-4899-8069-e0e3048e911d.sketch_text.stroke-143"),sQuery(id+"FHMxAyK4CFUKdhS_1.wireOp",EDGE,"1cb9c079-ea9b-4899-8069-e0e3048e911d.sketch_text.stroke-144"),sQuery(id+"FHMxAyK4CFUKdhS_1.wireOp",EDGE,"1cb9c079-ea9b-4899-8069-e0e3048e911d.sketch_text.stroke-145"),sQuery(id+"FHMxAyK4CFUKdhS_1.wireOp",EDGE,"1cb9c079-ea9b-4899-8069-e0e3048e911d.sketch_text.stroke-146"),sQuery(id+"FHMxAyK4CFUKdhS_1.wireOp",EDGE,"1cb9c079-ea9b-4899-8069-e0e3048e911d.sketch_text.stroke-147"),sQuery(id+"FHMxAyK4CFUKdhS_1.wireOp",EDGE,"1cb9c079-ea9b-4899-8069-e0e3048e911d.sketch_text.stroke-148"),sQuery(id+"FHMxAyK4CFUKdhS_1.wireOp",EDGE,"1cb9c079-ea9b-4899-8069-e0e3048e911d.sketch_text.stroke-149"),sQuery(id+"FHMxAyK4CFUKdhS_1.wireOp",EDGE,"1cb9c079-ea9b-4899-8069-e0e3048e911d.sketch_text.stroke-150"),sQuery(id+"FHMxAyK4CFUKdhS_1.wireOp",EDGE,"1cb9c079-ea9b-4899-8069-e0e3048e911d.sketch_text.stroke-151"),sQuery(id+"FHMxAyK4CFUKdhS_1.wireOp",EDGE,"1cb9c079-ea9b-4899-8069-e0e3048e911d.sketch_text.stroke-152"),sQuery(id+"FHMxAyK4CFUKdhS_1.wireOp",EDGE,"1cb9c079-ea9b-4899-8069-e0e3048e911d.sketch_text.stroke-153"),sQuery(id+"FHMxAyK4CFUKdhS_1.wireOp",EDGE,"1cb9c079-ea9b-4899-8069-e0e3048e911d.sketch_text.stroke-159"),sQuery(id+"FHMxAyK4CFUKdhS_1.wireOp",EDGE,"1cb9c079-ea9b-4899-8069-e0e3048e911d.sketch_text.stroke-160"),sQuery(id+"FHMxAyK4CFUKdhS_1.wireOp",EDGE,"1cb9c079-ea9b-4899-8069-e0e3048e911d.sketch_text.stroke-161"),sQuery(id+"FHMxAyK4CFUKdhS_1.wireOp",EDGE,"1cb9c079-ea9b-4899-8069-e0e3048e911d.sketch_text.stroke-162"),sQuery(id+"FHMxAyK4CFUKdhS_1.wireOp",EDGE,"1cb9c079-ea9b-4899-8069-e0e3048e911d.sketch_text.stroke-163"),sQuery(id+"FHMxAyK4CFUKdhS_1.wireOp",EDGE,"1cb9c079-ea9b-4899-8069-e0e3048e911d.sketch_text.stroke-164"),sQuery(id+"FHMxAyK4CFUKdhS_1.wireOp",EDGE,"1cb9c079-ea9b-4899-8069-e0e3048e911d.sketch_text.stroke-165"),sQuery(id+"FHMxAyK4CFUKdhS_1.wireOp",EDGE,"1cb9c079-ea9b-4899-8069-e0e3048e911d.sketch_text.stroke-166"),sQuery(id+"FHMxAyK4CFUKdhS_1.wireOp",EDGE,"1cb9c079-ea9b-4899-8069-e0e3048e911d.sketch_text.stroke-167"),sQuery(id+"FHMxAyK4CFUKdhS_1.wireOp",EDGE,"1cb9c079-ea9b-4899-8069-e0e3048e911d.sketch_text.stroke-168"),sQuery(id+"FHMxAyK4CFUKdhS_1.wireOp",EDGE,"1cb9c079-ea9b-4899-8069-e0e3048e911d.sketch_text.stroke-169"),sQuery(id+"FHMxAyK4CFUKdhS_1.wireOp",EDGE,"1cb9c079-ea9b-4899-8069-e0e3048e911d.sketch_text.stroke-170"),sQuery(id+"FHMxAyK4CFUKdhS_1.wireOp",EDGE,"1cb9c079-ea9b-4899-8069-e0e3048e911d.sketch_text.stroke-171"),sQuery(id+"FHMxAyK4CFUKdhS_1.wireOp",EDGE,"1cb9c079-ea9b-4899-8069-e0e3048e911d.sketch_text.stroke-172"),sQuery(id+"FHMxAyK4CFUKdhS_1.wireOp",EDGE,"1cb9c079-ea9b-4899-8069-e0e3048e911d.sketch_text.stroke-173"),sQuery(id+"FHMxAyK4CFUKdhS_1.wireOp",EDGE,"1cb9c079-ea9b-4899-8069-e0e3048e911d.sketch_text.stroke-174"),sQuery(id+"FHMxAyK4CFUKdhS_1.wireOp",EDGE,"1cb9c079-ea9b-4899-8069-e0e3048e911d.sketch_text.stroke-175"),sQuery(id+"FHMxAyK4CFUKdhS_1.wireOp",EDGE,"1cb9c079-ea9b-4899-8069-e0e3048e911d.sketch_text.stroke-176"),sQuery(id+"FHMxAyK4CFUKdhS_1.wireOp",EDGE,"1cb9c079-ea9b-4899-8069-e0e3048e911d.sketch_text.stroke-177"),sQuery(id+"FHMxAyK4CFUKdhS_1.wireOp",EDGE,"1cb9c079-ea9b-4899-8069-e0e3048e911d.sketch_text.stroke-178"),sQuery(id+"FHMxAyK4CFUKdhS_1.wireOp",EDGE,"1cb9c079-ea9b-4899-8069-e0e3048e911d.sketch_text.stroke-179"),sQuery(id+"FHMxAyK4CFUKdhS_1.wireOp",EDGE,"1cb9c079-ea9b-4899-8069-e0e3048e911d.sketch_text.stroke-180"),sQuery(id+"F3.wireOp",EDGE,"8007402e-1a4e-4a06-85a5-2af08e553504"),subQ2])],"isStart":true}),makeQuery(id+"F4.opExtrude","SWEPT_FACE",FACE,{"disambiguationData":[OSD([subQ2])]})]),OD(0.0)],"derivedFrom":makeQuery(id+"F1.opExtrude","CAP_EDGE",EDGE,{"disambiguationData":[OSD([subQ0])],"isStart":false})});}
            var Q17;
            {var subQ0=sQuery(id+"F0.wireOp",EDGE,"E0.top");var subQ1=sQuery(id+"F0.wireOp",EDGE,"E0.bottom");var subQ2=sQuery(id+"F3.wireOp",EDGE,"1a034e28-a7c2-419d-97de-c33d70a47301");Q17=makeQuery(id+"F4.boolean.opBoolean","SPLIT",EDGE,{"disambiguationData":[TD([makeQuery(id+"F1.opExtrude","CAP_FACE",FACE,{"disambiguationData":[OSD([subQ1,subQ0,sQuery(id+"F0.wireOp",EDGE,"E0.left"),sQuery(id+"F0.wireOp",EDGE,"E0.right")])],"isStart":false}),makeQuery(id+"F1.opExtrude","SWEPT_FACE",FACE,{"disambiguationData":[OSD([subQ0])]}),makeQuery(id+"F4.opExtrude","CAP_FACE",FACE,{"disambiguationData":[OSD([subQ1,sQuery(id+"F2.wireOp",EDGE,"fcba4419-a2ee-464f-be9d-58f11bf3418b.sketch_text.stroke-0"),sQuery(id+"F2.wireOp",EDGE,"fcba4419-a2ee-464f-be9d-58f11bf3418b.sketch_text.stroke-1"),sQuery(id+"F2.wireOp",EDGE,"fcba4419-a2ee-464f-be9d-58f11bf3418b.sketch_text.stroke-2"),sQuery(id+"F2.wireOp",EDGE,"fcba4419-a2ee-464f-be9d-58f11bf3418b.sketch_text.stroke-3"),sQuery(id+"F2.wireOp",EDGE,"fcba4419-a2ee-464f-be9d-58f11bf3418b.sketch_text.stroke-4"),sQuery(id+"F2.wireOp",EDGE,"fcba4419-a2ee-464f-be9d-58f11bf3418b.sketch_text.stroke-5"),sQuery(id+"F2.wireOp",EDGE,"fcba4419-a2ee-464f-be9d-58f11bf3418b.sketch_text.stroke-6"),sQuery(id+"F2.wireOp",EDGE,"fcba4419-a2ee-464f-be9d-58f11bf3418b.sketch_text.stroke-7"),sQuery(id+"F2.wireOp",EDGE,"fcba4419-a2ee-464f-be9d-58f11bf3418b.sketch_text.stroke-8"),sQuery(id+"F2.wireOp",EDGE,"fcba4419-a2ee-464f-be9d-58f11bf3418b.sketch_text.stroke-9"),sQuery(id+"F2.wireOp",EDGE,"fcba4419-a2ee-464f-be9d-58f11bf3418b.sketch_text.stroke-10"),sQuery(id+"F2.wireOp",EDGE,"fcba4419-a2ee-464f-be9d-58f11bf3418b.sketch_text.stroke-11"),sQuery(id+"F2.wireOp",EDGE,"fcba4419-a2ee-464f-be9d-58f11bf3418b.sketch_text.stroke-12"),sQuery(id+"F2.wireOp",EDGE,"fcba4419-a2ee-464f-be9d-58f11bf3418b.sketch_text.stroke-13"),sQuery(id+"F2.wireOp",EDGE,"fcba4419-a2ee-464f-be9d-58f11bf3418b.sketch_text.stroke-14"),sQuery(id+"F2.wireOp",EDGE,"fcba4419-a2ee-464f-be9d-58f11bf3418b.sketch_text.stroke-15"),sQuery(id+"F2.wireOp",EDGE,"fcba4419-a2ee-464f-be9d-58f11bf3418b.sketch_text.stroke-16"),sQuery(id+"F2.wireOp",EDGE,"fcba4419-a2ee-464f-be9d-58f11bf3418b.sketch_text.stroke-17"),sQuery(id+"F2.wireOp",EDGE,"fcba4419-a2ee-464f-be9d-58f11bf3418b.sketch_text.stroke-18"),sQuery(id+"F2.wireOp",EDGE,"fcba4419-a2ee-464f-be9d-58f11bf3418b.sketch_text.stroke-19"),sQuery(id+"F2.wireOp",EDGE,"fcba4419-a2ee-464f-be9d-58f11bf3418b.sketch_text.stroke-20"),sQuery(id+"F2.wireOp",EDGE,"fcba4419-a2ee-464f-be9d-58f11bf3418b.sketch_text.stroke-21"),sQuery(id+"F2.wireOp",EDGE,"fcba4419-a2ee-464f-be9d-58f11bf3418b.sketch_text.stroke-22"),sQuery(id+"F2.wireOp",EDGE,"fcba4419-a2ee-464f-be9d-58f11bf3418b.sketch_text.stroke-23"),sQuery(id+"F2.wireOp",EDGE,"fcba4419-a2ee-464f-be9d-58f11bf3418b.sketch_text.stroke-24"),sQuery(id+"F2.wireOp",EDGE,"fcba4419-a2ee-464f-be9d-58f11bf3418b.sketch_text.stroke-25"),sQuery(id+"F2.wireOp",EDGE,"fcba4419-a2ee-464f-be9d-58f11bf3418b.sketch_text.stroke-26"),sQuery(id+"F2.wireOp",EDGE,"fcba4419-a2ee-464f-be9d-58f11bf3418b.sketch_text.stroke-27"),sQuery(id+"F2.wireOp",EDGE,"fcba4419-a2ee-464f-be9d-58f11bf3418b.sketch_text.stroke-28"),sQuery(id+"F2.wireOp",EDGE,"fcba4419-a2ee-464f-be9d-58f11bf3418b.sketch_text.stroke-29"),sQuery(id+"F2.wireOp",EDGE,"fcba4419-a2ee-464f-be9d-58f11bf3418b.sketch_text.stroke-30"),sQuery(id+"F2.wireOp",EDGE,"fcba4419-a2ee-464f-be9d-58f11bf3418b.sketch_text.stroke-31"),sQuery(id+"F2.wireOp",EDGE,"fcba4419-a2ee-464f-be9d-58f11bf3418b.sketch_text.stroke-32"),sQuery(id+"F2.wireOp",EDGE,"fcba4419-a2ee-464f-be9d-58f11bf3418b.sketch_text.stroke-33"),sQuery(id+"F2.wireOp",EDGE,"fcba4419-a2ee-464f-be9d-58f11bf3418b.sketch_text.stroke-34"),sQuery(id+"F2.wireOp",EDGE,"fcba4419-a2ee-464f-be9d-58f11bf3418b.sketch_text.stroke-35"),sQuery(id+"F2.wireOp",EDGE,"fcba4419-a2ee-464f-be9d-58f11bf3418b.sketch_text.stroke-36"),sQuery(id+"F2.wireOp",EDGE,"fcba4419-a2ee-464f-be9d-58f11bf3418b.sketch_text.stroke-37"),sQuery(id+"F2.wireOp",EDGE,"fcba4419-a2ee-464f-be9d-58f11bf3418b.sketch_text.stroke-38"),sQuery(id+"F2.wireOp",EDGE,"fcba4419-a2ee-464f-be9d-58f11bf3418b.sketch_text.stroke-39"),sQuery(id+"F2.wireOp",EDGE,"fcba4419-a2ee-464f-be9d-58f11bf3418b.sketch_text.stroke-40"),sQuery(id+"F2.wireOp",EDGE,"fcba4419-a2ee-464f-be9d-58f11bf3418b.sketch_text.stroke-41"),sQuery(id+"F2.wireOp",EDGE,"fcba4419-a2ee-464f-be9d-58f11bf3418b.sketch_text.stroke-42"),sQuery(id+"F2.wireOp",EDGE,"fcba4419-a2ee-464f-be9d-58f11bf3418b.sketch_text.stroke-43"),sQuery(id+"F2.wireOp",EDGE,"fcba4419-a2ee-464f-be9d-58f11bf3418b.sketch_text.stroke-44"),sQuery(id+"F2.wireOp",EDGE,"fcba4419-a2ee-464f-be9d-58f11bf3418b.sketch_text.stroke-45"),sQuery(id+"F2.wireOp",EDGE,"fcba4419-a2ee-464f-be9d-58f11bf3418b.sketch_text.stroke-46"),sQuery(id+"F2.wireOp",EDGE,"fcba4419-a2ee-464f-be9d-58f11bf3418b.sketch_text.stroke-47"),sQuery(id+"F2.wireOp",EDGE,"fcba4419-a2ee-464f-be9d-58f11bf3418b.sketch_text.stroke-48"),sQuery(id+"F2.wireOp",EDGE,"fcba4419-a2ee-464f-be9d-58f11bf3418b.sketch_text.stroke-49"),sQuery(id+"F2.wireOp",EDGE,"fcba4419-a2ee-464f-be9d-58f11bf3418b.sketch_text.stroke-50"),sQuery(id+"F2.wireOp",EDGE,"fcba4419-a2ee-464f-be9d-58f11bf3418b.sketch_text.stroke-51"),sQuery(id+"F2.wireOp",EDGE,"fcba4419-a2ee-464f-be9d-58f11bf3418b.sketch_text.stroke-52"),sQuery(id+"F2.wireOp",EDGE,"fcba4419-a2ee-464f-be9d-58f11bf3418b.sketch_text.stroke-53"),sQuery(id+"F2.wireOp",EDGE,"fcba4419-a2ee-464f-be9d-58f11bf3418b.sketch_text.stroke-54"),sQuery(id+"F2.wireOp",EDGE,"fcba4419-a2ee-464f-be9d-58f11bf3418b.sketch_text.stroke-55"),sQuery(id+"F2.wireOp",EDGE,"fcba4419-a2ee-464f-be9d-58f11bf3418b.sketch_text.stroke-56"),sQuery(id+"F2.wireOp",EDGE,"fcba4419-a2ee-464f-be9d-58f11bf3418b.sketch_text.stroke-57"),sQuery(id+"F2.wireOp",EDGE,"fcba4419-a2ee-464f-be9d-58f11bf3418b.sketch_text.stroke-58"),sQuery(id+"F2.wireOp",EDGE,"fcba4419-a2ee-464f-be9d-58f11bf3418b.sketch_text.stroke-59"),sQuery(id+"F2.wireOp",EDGE,"fcba4419-a2ee-464f-be9d-58f11bf3418b.sketch_text.stroke-60"),sQuery(id+"F2.wireOp",EDGE,"fcba4419-a2ee-464f-be9d-58f11bf3418b.sketch_text.stroke-61"),sQuery(id+"F2.wireOp",EDGE,"fcba4419-a2ee-464f-be9d-58f11bf3418b.sketch_text.stroke-62"),sQuery(id+"F2.wireOp",EDGE,"fcba4419-a2ee-464f-be9d-58f11bf3418b.sketch_text.stroke-63"),sQuery(id+"F2.wireOp",EDGE,"fcba4419-a2ee-464f-be9d-58f11bf3418b.sketch_text.stroke-64"),sQuery(id+"F2.wireOp",EDGE,"fcba4419-a2ee-464f-be9d-58f11bf3418b.sketch_text.stroke-65"),sQuery(id+"F2.wireOp",EDGE,"fcba4419-a2ee-464f-be9d-58f11bf3418b.sketch_text.stroke-66"),sQuery(id+"F2.wireOp",EDGE,"fcba4419-a2ee-464f-be9d-58f11bf3418b.sketch_text.stroke-67"),sQuery(id+"F2.wireOp",EDGE,"fcba4419-a2ee-464f-be9d-58f11bf3418b.sketch_text.stroke-68"),sQuery(id+"F2.wireOp",EDGE,"fcba4419-a2ee-464f-be9d-58f11bf3418b.sketch_text.stroke-69"),sQuery(id+"F2.wireOp",EDGE,"fcba4419-a2ee-464f-be9d-58f11bf3418b.sketch_text.stroke-70"),sQuery(id+"F2.wireOp",EDGE,"fcba4419-a2ee-464f-be9d-58f11bf3418b.sketch_text.stroke-71"),sQuery(id+"F2.wireOp",EDGE,"fcba4419-a2ee-464f-be9d-58f11bf3418b.sketch_text.stroke-72"),sQuery(id+"F2.wireOp",EDGE,"fcba4419-a2ee-464f-be9d-58f11bf3418b.sketch_text.stroke-73"),sQuery(id+"F2.wireOp",EDGE,"fcba4419-a2ee-464f-be9d-58f11bf3418b.sketch_text.stroke-74"),sQuery(id+"F2.wireOp",EDGE,"fcba4419-a2ee-464f-be9d-58f11bf3418b.sketch_text.stroke-75"),sQuery(id+"F2.wireOp",EDGE,"fcba4419-a2ee-464f-be9d-58f11bf3418b.sketch_text.stroke-76"),sQuery(id+"F2.wireOp",EDGE,"fcba4419-a2ee-464f-be9d-58f11bf3418b.sketch_text.stroke-77"),sQuery(id+"F2.wireOp",EDGE,"fcba4419-a2ee-464f-be9d-58f11bf3418b.sketch_text.stroke-78"),sQuery(id+"F2.wireOp",EDGE,"fcba4419-a2ee-464f-be9d-58f11bf3418b.sketch_text.stroke-79"),sQuery(id+"F2.wireOp",EDGE,"fcba4419-a2ee-464f-be9d-58f11bf3418b.sketch_text.stroke-80"),sQuery(id+"F2.wireOp",EDGE,"fcba4419-a2ee-464f-be9d-58f11bf3418b.sketch_text.stroke-81"),sQuery(id+"F2.wireOp",EDGE,"fcba4419-a2ee-464f-be9d-58f11bf3418b.sketch_text.stroke-82"),sQuery(id+"F2.wireOp",EDGE,"fcba4419-a2ee-464f-be9d-58f11bf3418b.sketch_text.stroke-83"),sQuery(id+"F2.wireOp",EDGE,"fcba4419-a2ee-464f-be9d-58f11bf3418b.sketch_text.stroke-84"),sQuery(id+"F2.wireOp",EDGE,"fcba4419-a2ee-464f-be9d-58f11bf3418b.sketch_text.stroke-85"),sQuery(id+"F2.wireOp",EDGE,"fcba4419-a2ee-464f-be9d-58f11bf3418b.sketch_text.stroke-86"),sQuery(id+"F2.wireOp",EDGE,"fcba4419-a2ee-464f-be9d-58f11bf3418b.sketch_text.stroke-87"),sQuery(id+"F2.wireOp",EDGE,"fcba4419-a2ee-464f-be9d-58f11bf3418b.sketch_text.stroke-88"),sQuery(id+"F2.wireOp",EDGE,"fcba4419-a2ee-464f-be9d-58f11bf3418b.sketch_text.stroke-89"),sQuery(id+"F2.wireOp",EDGE,"fcba4419-a2ee-464f-be9d-58f11bf3418b.sketch_text.stroke-90"),sQuery(id+"F2.wireOp",EDGE,"fcba4419-a2ee-464f-be9d-58f11bf3418b.sketch_text.stroke-91"),sQuery(id+"F2.wireOp",EDGE,"fcba4419-a2ee-464f-be9d-58f11bf3418b.sketch_text.stroke-92"),sQuery(id+"F2.wireOp",EDGE,"fcba4419-a2ee-464f-be9d-58f11bf3418b.sketch_text.stroke-93"),sQuery(id+"F2.wireOp",EDGE,"fcba4419-a2ee-464f-be9d-58f11bf3418b.sketch_text.stroke-94"),sQuery(id+"F2.wireOp",EDGE,"fcba4419-a2ee-464f-be9d-58f11bf3418b.sketch_text.stroke-95"),sQuery(id+"F2.wireOp",EDGE,"fcba4419-a2ee-464f-be9d-58f11bf3418b.sketch_text.stroke-96"),sQuery(id+"F2.wireOp",EDGE,"fcba4419-a2ee-464f-be9d-58f11bf3418b.sketch_text.stroke-97"),sQuery(id+"F2.wireOp",EDGE,"fcba4419-a2ee-464f-be9d-58f11bf3418b.sketch_text.stroke-98"),sQuery(id+"F2.wireOp",EDGE,"fcba4419-a2ee-464f-be9d-58f11bf3418b.sketch_text.stroke-99"),sQuery(id+"F2.wireOp",EDGE,"fcba4419-a2ee-464f-be9d-58f11bf3418b.sketch_text.stroke-100"),sQuery(id+"F2.wireOp",EDGE,"fcba4419-a2ee-464f-be9d-58f11bf3418b.sketch_text.stroke-101"),sQuery(id+"F2.wireOp",EDGE,"fcba4419-a2ee-464f-be9d-58f11bf3418b.sketch_text.stroke-102"),sQuery(id+"F2.wireOp",EDGE,"fcba4419-a2ee-464f-be9d-58f11bf3418b.sketch_text.stroke-103"),sQuery(id+"F2.wireOp",EDGE,"fcba4419-a2ee-464f-be9d-58f11bf3418b.sketch_text.stroke-104"),sQuery(id+"F2.wireOp",EDGE,"fcba4419-a2ee-464f-be9d-58f11bf3418b.sketch_text.stroke-105"),sQuery(id+"F2.wireOp",EDGE,"fcba4419-a2ee-464f-be9d-58f11bf3418b.sketch_text.stroke-106"),sQuery(id+"F2.wireOp",EDGE,"fcba4419-a2ee-464f-be9d-58f11bf3418b.sketch_text.stroke-107"),sQuery(id+"F2.wireOp",EDGE,"fcba4419-a2ee-464f-be9d-58f11bf3418b.sketch_text.stroke-108"),sQuery(id+"F2.wireOp",EDGE,"fcba4419-a2ee-464f-be9d-58f11bf3418b.sketch_text.stroke-109"),sQuery(id+"F2.wireOp",EDGE,"fcba4419-a2ee-464f-be9d-58f11bf3418b.sketch_text.stroke-110"),sQuery(id+"F2.wireOp",EDGE,"fcba4419-a2ee-464f-be9d-58f11bf3418b.sketch_text.stroke-111"),sQuery(id+"F2.wireOp",EDGE,"fcba4419-a2ee-464f-be9d-58f11bf3418b.sketch_text.stroke-112"),sQuery(id+"F2.wireOp",EDGE,"fcba4419-a2ee-464f-be9d-58f11bf3418b.sketch_text.stroke-113"),sQuery(id+"F2.wireOp",EDGE,"fcba4419-a2ee-464f-be9d-58f11bf3418b.sketch_text.stroke-114"),sQuery(id+"F2.wireOp",EDGE,"fcba4419-a2ee-464f-be9d-58f11bf3418b.sketch_text.stroke-115"),sQuery(id+"F2.wireOp",EDGE,"fcba4419-a2ee-464f-be9d-58f11bf3418b.sketch_text.stroke-116"),sQuery(id+"F2.wireOp",EDGE,"fcba4419-a2ee-464f-be9d-58f11bf3418b.sketch_text.stroke-117"),sQuery(id+"F2.wireOp",EDGE,"fcba4419-a2ee-464f-be9d-58f11bf3418b.sketch_text.stroke-118"),sQuery(id+"F2.wireOp",EDGE,"fcba4419-a2ee-464f-be9d-58f11bf3418b.sketch_text.stroke-119"),sQuery(id+"F2.wireOp",EDGE,"fcba4419-a2ee-464f-be9d-58f11bf3418b.sketch_text.stroke-120"),sQuery(id+"F2.wireOp",EDGE,"fcba4419-a2ee-464f-be9d-58f11bf3418b.sketch_text.stroke-121"),sQuery(id+"F2.wireOp",EDGE,"fcba4419-a2ee-464f-be9d-58f11bf3418b.sketch_text.stroke-122"),sQuery(id+"F2.wireOp",EDGE,"fcba4419-a2ee-464f-be9d-58f11bf3418b.sketch_text.stroke-123"),sQuery(id+"F2.wireOp",EDGE,"fcba4419-a2ee-464f-be9d-58f11bf3418b.sketch_text.stroke-124"),sQuery(id+"F2.wireOp",EDGE,"fcba4419-a2ee-464f-be9d-58f11bf3418b.sketch_text.stroke-125"),sQuery(id+"F2.wireOp",EDGE,"fcba4419-a2ee-464f-be9d-58f11bf3418b.sketch_text.stroke-126"),sQuery(id+"F2.wireOp",EDGE,"fcba4419-a2ee-464f-be9d-58f11bf3418b.sketch_text.stroke-127"),sQuery(id+"F2.wireOp",EDGE,"fcba4419-a2ee-464f-be9d-58f11bf3418b.sketch_text.stroke-128"),sQuery(id+"F2.wireOp",EDGE,"fcba4419-a2ee-464f-be9d-58f11bf3418b.sketch_text.stroke-129"),sQuery(id+"F2.wireOp",EDGE,"fcba4419-a2ee-464f-be9d-58f11bf3418b.sketch_text.stroke-130"),sQuery(id+"F2.wireOp",EDGE,"fcba4419-a2ee-464f-be9d-58f11bf3418b.sketch_text.stroke-131"),sQuery(id+"F2.wireOp",EDGE,"fcba4419-a2ee-464f-be9d-58f11bf3418b.sketch_text.stroke-132"),sQuery(id+"F2.wireOp",EDGE,"fcba4419-a2ee-464f-be9d-58f11bf3418b.sketch_text.stroke-133"),sQuery(id+"F2.wireOp",EDGE,"fcba4419-a2ee-464f-be9d-58f11bf3418b.sketch_text.stroke-134"),sQuery(id+"F2.wireOp",EDGE,"fcba4419-a2ee-464f-be9d-58f11bf3418b.sketch_text.stroke-135"),sQuery(id+"F2.wireOp",EDGE,"fcba4419-a2ee-464f-be9d-58f11bf3418b.sketch_text.stroke-136"),sQuery(id+"F2.wireOp",EDGE,"fcba4419-a2ee-464f-be9d-58f11bf3418b.sketch_text.stroke-137"),sQuery(id+"F2.wireOp",EDGE,"fcba4419-a2ee-464f-be9d-58f11bf3418b.sketch_text.stroke-138"),sQuery(id+"F2.wireOp",EDGE,"fcba4419-a2ee-464f-be9d-58f11bf3418b.sketch_text.stroke-139"),sQuery(id+"F2.wireOp",EDGE,"fcba4419-a2ee-464f-be9d-58f11bf3418b.sketch_text.stroke-140"),sQuery(id+"F2.wireOp",EDGE,"fcba4419-a2ee-464f-be9d-58f11bf3418b.sketch_text.stroke-141"),sQuery(id+"F2.wireOp",EDGE,"fcba4419-a2ee-464f-be9d-58f11bf3418b.sketch_text.stroke-142"),sQuery(id+"F2.wireOp",EDGE,"fcba4419-a2ee-464f-be9d-58f11bf3418b.sketch_text.stroke-143"),sQuery(id+"F2.wireOp",EDGE,"fcba4419-a2ee-464f-be9d-58f11bf3418b.sketch_text.stroke-144"),sQuery(id+"F2.wireOp",EDGE,"fcba4419-a2ee-464f-be9d-58f11bf3418b.sketch_text.stroke-145"),sQuery(id+"F2.wireOp",EDGE,"fcba4419-a2ee-464f-be9d-58f11bf3418b.sketch_text.stroke-146"),sQuery(id+"F2.wireOp",EDGE,"fcba4419-a2ee-464f-be9d-58f11bf3418b.sketch_text.stroke-147"),sQuery(id+"F2.wireOp",EDGE,"fcba4419-a2ee-464f-be9d-58f11bf3418b.sketch_text.stroke-148"),sQuery(id+"F2.wireOp",EDGE,"fcba4419-a2ee-464f-be9d-58f11bf3418b.sketch_text.stroke-149"),sQuery(id+"F2.wireOp",EDGE,"fcba4419-a2ee-464f-be9d-58f11bf3418b.sketch_text.stroke-150"),sQuery(id+"F2.wireOp",EDGE,"fcba4419-a2ee-464f-be9d-58f11bf3418b.sketch_text.stroke-151"),sQuery(id+"F2.wireOp",EDGE,"fcba4419-a2ee-464f-be9d-58f11bf3418b.sketch_text.stroke-152"),sQuery(id+"F2.wireOp",EDGE,"fcba4419-a2ee-464f-be9d-58f11bf3418b.sketch_text.stroke-153"),sQuery(id+"F2.wireOp",EDGE,"fcba4419-a2ee-464f-be9d-58f11bf3418b.sketch_text.stroke-154"),sQuery(id+"F2.wireOp",EDGE,"fcba4419-a2ee-464f-be9d-58f11bf3418b.sketch_text.stroke-155"),sQuery(id+"F2.wireOp",EDGE,"fcba4419-a2ee-464f-be9d-58f11bf3418b.sketch_text.stroke-156"),sQuery(id+"F2.wireOp",EDGE,"fcba4419-a2ee-464f-be9d-58f11bf3418b.sketch_text.stroke-157"),sQuery(id+"F2.wireOp",EDGE,"fcba4419-a2ee-464f-be9d-58f11bf3418b.sketch_text.stroke-158"),sQuery(id+"F2.wireOp",EDGE,"fcba4419-a2ee-464f-be9d-58f11bf3418b.sketch_text.stroke-159"),sQuery(id+"F2.wireOp",EDGE,"fcba4419-a2ee-464f-be9d-58f11bf3418b.sketch_text.stroke-160"),sQuery(id+"F2.wireOp",EDGE,"fcba4419-a2ee-464f-be9d-58f11bf3418b.sketch_text.stroke-161"),sQuery(id+"F2.wireOp",EDGE,"fcba4419-a2ee-464f-be9d-58f11bf3418b.sketch_text.stroke-162"),sQuery(id+"F2.wireOp",EDGE,"fcba4419-a2ee-464f-be9d-58f11bf3418b.sketch_text.stroke-163"),sQuery(id+"F2.wireOp",EDGE,"fcba4419-a2ee-464f-be9d-58f11bf3418b.sketch_text.stroke-164"),sQuery(id+"F2.wireOp",EDGE,"fcba4419-a2ee-464f-be9d-58f11bf3418b.sketch_text.stroke-165"),sQuery(id+"F2.wireOp",EDGE,"fcba4419-a2ee-464f-be9d-58f11bf3418b.sketch_text.stroke-166"),sQuery(id+"F2.wireOp",EDGE,"fcba4419-a2ee-464f-be9d-58f11bf3418b.sketch_text.stroke-167"),sQuery(id+"F2.wireOp",EDGE,"fcba4419-a2ee-464f-be9d-58f11bf3418b.sketch_text.stroke-168"),sQuery(id+"F2.wireOp",EDGE,"fcba4419-a2ee-464f-be9d-58f11bf3418b.sketch_text.stroke-169"),sQuery(id+"F2.wireOp",EDGE,"fcba4419-a2ee-464f-be9d-58f11bf3418b.sketch_text.stroke-170"),sQuery(id+"F2.wireOp",EDGE,"fcba4419-a2ee-464f-be9d-58f11bf3418b.sketch_text.stroke-171"),sQuery(id+"F2.wireOp",EDGE,"fcba4419-a2ee-464f-be9d-58f11bf3418b.sketch_text.stroke-172"),sQuery(id+"F2.wireOp",EDGE,"fcba4419-a2ee-464f-be9d-58f11bf3418b.sketch_text.stroke-173"),sQuery(id+"FHMxAyK4CFUKdhS_1.wireOp",EDGE,"1cb9c079-ea9b-4899-8069-e0e3048e911d.sketch_text.stroke-0"),sQuery(id+"FHMxAyK4CFUKdhS_1.wireOp",EDGE,"1cb9c079-ea9b-4899-8069-e0e3048e911d.sketch_text.stroke-1"),sQuery(id+"FHMxAyK4CFUKdhS_1.wireOp",EDGE,"1cb9c079-ea9b-4899-8069-e0e3048e911d.sketch_text.stroke-2"),sQuery(id+"FHMxAyK4CFUKdhS_1.wireOp",EDGE,"1cb9c079-ea9b-4899-8069-e0e3048e911d.sketch_text.stroke-3"),sQuery(id+"FHMxAyK4CFUKdhS_1.wireOp",EDGE,"1cb9c079-ea9b-4899-8069-e0e3048e911d.sketch_text.stroke-4"),sQuery(id+"FHMxAyK4CFUKdhS_1.wireOp",EDGE,"1cb9c079-ea9b-4899-8069-e0e3048e911d.sketch_text.stroke-5"),sQuery(id+"FHMxAyK4CFUKdhS_1.wireOp",EDGE,"1cb9c079-ea9b-4899-8069-e0e3048e911d.sketch_text.stroke-6"),sQuery(id+"FHMxAyK4CFUKdhS_1.wireOp",EDGE,"1cb9c079-ea9b-4899-8069-e0e3048e911d.sketch_text.stroke-7"),sQuery(id+"FHMxAyK4CFUKdhS_1.wireOp",EDGE,"1cb9c079-ea9b-4899-8069-e0e3048e911d.sketch_text.stroke-8"),sQuery(id+"FHMxAyK4CFUKdhS_1.wireOp",EDGE,"1cb9c079-ea9b-4899-8069-e0e3048e911d.sketch_text.stroke-9"),sQuery(id+"FHMxAyK4CFUKdhS_1.wireOp",EDGE,"1cb9c079-ea9b-4899-8069-e0e3048e911d.sketch_text.stroke-10"),sQuery(id+"FHMxAyK4CFUKdhS_1.wireOp",EDGE,"1cb9c079-ea9b-4899-8069-e0e3048e911d.sketch_text.stroke-11"),sQuery(id+"FHMxAyK4CFUKdhS_1.wireOp",EDGE,"1cb9c079-ea9b-4899-8069-e0e3048e911d.sketch_text.stroke-12"),sQuery(id+"FHMxAyK4CFUKdhS_1.wireOp",EDGE,"1cb9c079-ea9b-4899-8069-e0e3048e911d.sketch_text.stroke-13"),sQuery(id+"FHMxAyK4CFUKdhS_1.wireOp",EDGE,"1cb9c079-ea9b-4899-8069-e0e3048e911d.sketch_text.stroke-14"),sQuery(id+"FHMxAyK4CFUKdhS_1.wireOp",EDGE,"1cb9c079-ea9b-4899-8069-e0e3048e911d.sketch_text.stroke-15"),sQuery(id+"FHMxAyK4CFUKdhS_1.wireOp",EDGE,"1cb9c079-ea9b-4899-8069-e0e3048e911d.sketch_text.stroke-16"),sQuery(id+"FHMxAyK4CFUKdhS_1.wireOp",EDGE,"1cb9c079-ea9b-4899-8069-e0e3048e911d.sketch_text.stroke-17"),sQuery(id+"FHMxAyK4CFUKdhS_1.wireOp",EDGE,"1cb9c079-ea9b-4899-8069-e0e3048e911d.sketch_text.stroke-18"),sQuery(id+"FHMxAyK4CFUKdhS_1.wireOp",EDGE,"1cb9c079-ea9b-4899-8069-e0e3048e911d.sketch_text.stroke-19"),sQuery(id+"FHMxAyK4CFUKdhS_1.wireOp",EDGE,"1cb9c079-ea9b-4899-8069-e0e3048e911d.sketch_text.stroke-20"),sQuery(id+"FHMxAyK4CFUKdhS_1.wireOp",EDGE,"1cb9c079-ea9b-4899-8069-e0e3048e911d.sketch_text.stroke-21"),sQuery(id+"FHMxAyK4CFUKdhS_1.wireOp",EDGE,"1cb9c079-ea9b-4899-8069-e0e3048e911d.sketch_text.stroke-22"),sQuery(id+"FHMxAyK4CFUKdhS_1.wireOp",EDGE,"1cb9c079-ea9b-4899-8069-e0e3048e911d.sketch_text.stroke-23"),sQuery(id+"FHMxAyK4CFUKdhS_1.wireOp",EDGE,"1cb9c079-ea9b-4899-8069-e0e3048e911d.sketch_text.stroke-24"),sQuery(id+"FHMxAyK4CFUKdhS_1.wireOp",EDGE,"1cb9c079-ea9b-4899-8069-e0e3048e911d.sketch_text.stroke-25"),sQuery(id+"FHMxAyK4CFUKdhS_1.wireOp",EDGE,"1cb9c079-ea9b-4899-8069-e0e3048e911d.sketch_text.stroke-26"),sQuery(id+"FHMxAyK4CFUKdhS_1.wireOp",EDGE,"1cb9c079-ea9b-4899-8069-e0e3048e911d.sketch_text.stroke-27"),sQuery(id+"FHMxAyK4CFUKdhS_1.wireOp",EDGE,"1cb9c079-ea9b-4899-8069-e0e3048e911d.sketch_text.stroke-28"),sQuery(id+"FHMxAyK4CFUKdhS_1.wireOp",EDGE,"1cb9c079-ea9b-4899-8069-e0e3048e911d.sketch_text.stroke-29"),sQuery(id+"FHMxAyK4CFUKdhS_1.wireOp",EDGE,"1cb9c079-ea9b-4899-8069-e0e3048e911d.sketch_text.stroke-30"),sQuery(id+"FHMxAyK4CFUKdhS_1.wireOp",EDGE,"1cb9c079-ea9b-4899-8069-e0e3048e911d.sketch_text.stroke-31"),sQuery(id+"FHMxAyK4CFUKdhS_1.wireOp",EDGE,"1cb9c079-ea9b-4899-8069-e0e3048e911d.sketch_text.stroke-32"),sQuery(id+"FHMxAyK4CFUKdhS_1.wireOp",EDGE,"1cb9c079-ea9b-4899-8069-e0e3048e911d.sketch_text.stroke-33"),sQuery(id+"FHMxAyK4CFUKdhS_1.wireOp",EDGE,"1cb9c079-ea9b-4899-8069-e0e3048e911d.sketch_text.stroke-34"),sQuery(id+"FHMxAyK4CFUKdhS_1.wireOp",EDGE,"1cb9c079-ea9b-4899-8069-e0e3048e911d.sketch_text.stroke-35"),sQuery(id+"FHMxAyK4CFUKdhS_1.wireOp",EDGE,"1cb9c079-ea9b-4899-8069-e0e3048e911d.sketch_text.stroke-36"),sQuery(id+"FHMxAyK4CFUKdhS_1.wireOp",EDGE,"1cb9c079-ea9b-4899-8069-e0e3048e911d.sketch_text.stroke-37"),sQuery(id+"FHMxAyK4CFUKdhS_1.wireOp",EDGE,"1cb9c079-ea9b-4899-8069-e0e3048e911d.sketch_text.stroke-38"),sQuery(id+"FHMxAyK4CFUKdhS_1.wireOp",EDGE,"1cb9c079-ea9b-4899-8069-e0e3048e911d.sketch_text.stroke-39"),sQuery(id+"FHMxAyK4CFUKdhS_1.wireOp",EDGE,"1cb9c079-ea9b-4899-8069-e0e3048e911d.sketch_text.stroke-40"),sQuery(id+"FHMxAyK4CFUKdhS_1.wireOp",EDGE,"1cb9c079-ea9b-4899-8069-e0e3048e911d.sketch_text.stroke-41"),sQuery(id+"FHMxAyK4CFUKdhS_1.wireOp",EDGE,"1cb9c079-ea9b-4899-8069-e0e3048e911d.sketch_text.stroke-42"),sQuery(id+"FHMxAyK4CFUKdhS_1.wireOp",EDGE,"1cb9c079-ea9b-4899-8069-e0e3048e911d.sketch_text.stroke-43"),sQuery(id+"FHMxAyK4CFUKdhS_1.wireOp",EDGE,"1cb9c079-ea9b-4899-8069-e0e3048e911d.sketch_text.stroke-44"),sQuery(id+"FHMxAyK4CFUKdhS_1.wireOp",EDGE,"1cb9c079-ea9b-4899-8069-e0e3048e911d.sketch_text.stroke-45"),sQuery(id+"FHMxAyK4CFUKdhS_1.wireOp",EDGE,"1cb9c079-ea9b-4899-8069-e0e3048e911d.sketch_text.stroke-46"),sQuery(id+"FHMxAyK4CFUKdhS_1.wireOp",EDGE,"1cb9c079-ea9b-4899-8069-e0e3048e911d.sketch_text.stroke-47"),sQuery(id+"FHMxAyK4CFUKdhS_1.wireOp",EDGE,"1cb9c079-ea9b-4899-8069-e0e3048e911d.sketch_text.stroke-48"),sQuery(id+"FHMxAyK4CFUKdhS_1.wireOp",EDGE,"1cb9c079-ea9b-4899-8069-e0e3048e911d.sketch_text.stroke-49"),sQuery(id+"FHMxAyK4CFUKdhS_1.wireOp",EDGE,"1cb9c079-ea9b-4899-8069-e0e3048e911d.sketch_text.stroke-50"),sQuery(id+"FHMxAyK4CFUKdhS_1.wireOp",EDGE,"1cb9c079-ea9b-4899-8069-e0e3048e911d.sketch_text.stroke-51"),sQuery(id+"FHMxAyK4CFUKdhS_1.wireOp",EDGE,"1cb9c079-ea9b-4899-8069-e0e3048e911d.sketch_text.stroke-52"),sQuery(id+"FHMxAyK4CFUKdhS_1.wireOp",EDGE,"1cb9c079-ea9b-4899-8069-e0e3048e911d.sketch_text.stroke-53"),sQuery(id+"FHMxAyK4CFUKdhS_1.wireOp",EDGE,"1cb9c079-ea9b-4899-8069-e0e3048e911d.sketch_text.stroke-54"),sQuery(id+"FHMxAyK4CFUKdhS_1.wireOp",EDGE,"1cb9c079-ea9b-4899-8069-e0e3048e911d.sketch_text.stroke-55"),sQuery(id+"FHMxAyK4CFUKdhS_1.wireOp",EDGE,"1cb9c079-ea9b-4899-8069-e0e3048e911d.sketch_text.stroke-56"),sQuery(id+"FHMxAyK4CFUKdhS_1.wireOp",EDGE,"1cb9c079-ea9b-4899-8069-e0e3048e911d.sketch_text.stroke-57"),sQuery(id+"FHMxAyK4CFUKdhS_1.wireOp",EDGE,"1cb9c079-ea9b-4899-8069-e0e3048e911d.sketch_text.stroke-58"),sQuery(id+"FHMxAyK4CFUKdhS_1.wireOp",EDGE,"1cb9c079-ea9b-4899-8069-e0e3048e911d.sketch_text.stroke-59"),sQuery(id+"FHMxAyK4CFUKdhS_1.wireOp",EDGE,"1cb9c079-ea9b-4899-8069-e0e3048e911d.sketch_text.stroke-60"),sQuery(id+"FHMxAyK4CFUKdhS_1.wireOp",EDGE,"1cb9c079-ea9b-4899-8069-e0e3048e911d.sketch_text.stroke-61"),sQuery(id+"FHMxAyK4CFUKdhS_1.wireOp",EDGE,"1cb9c079-ea9b-4899-8069-e0e3048e911d.sketch_text.stroke-62"),sQuery(id+"FHMxAyK4CFUKdhS_1.wireOp",EDGE,"1cb9c079-ea9b-4899-8069-e0e3048e911d.sketch_text.stroke-71"),sQuery(id+"FHMxAyK4CFUKdhS_1.wireOp",EDGE,"1cb9c079-ea9b-4899-8069-e0e3048e911d.sketch_text.stroke-72"),sQuery(id+"FHMxAyK4CFUKdhS_1.wireOp",EDGE,"1cb9c079-ea9b-4899-8069-e0e3048e911d.sketch_text.stroke-73"),sQuery(id+"FHMxAyK4CFUKdhS_1.wireOp",EDGE,"1cb9c079-ea9b-4899-8069-e0e3048e911d.sketch_text.stroke-74"),sQuery(id+"FHMxAyK4CFUKdhS_1.wireOp",EDGE,"1cb9c079-ea9b-4899-8069-e0e3048e911d.sketch_text.stroke-75"),sQuery(id+"FHMxAyK4CFUKdhS_1.wireOp",EDGE,"1cb9c079-ea9b-4899-8069-e0e3048e911d.sketch_text.stroke-76"),sQuery(id+"FHMxAyK4CFUKdhS_1.wireOp",EDGE,"1cb9c079-ea9b-4899-8069-e0e3048e911d.sketch_text.stroke-77"),sQuery(id+"FHMxAyK4CFUKdhS_1.wireOp",EDGE,"1cb9c079-ea9b-4899-8069-e0e3048e911d.sketch_text.stroke-78"),sQuery(id+"FHMxAyK4CFUKdhS_1.wireOp",EDGE,"1cb9c079-ea9b-4899-8069-e0e3048e911d.sketch_text.stroke-79"),sQuery(id+"FHMxAyK4CFUKdhS_1.wireOp",EDGE,"1cb9c079-ea9b-4899-8069-e0e3048e911d.sketch_text.stroke-80"),sQuery(id+"FHMxAyK4CFUKdhS_1.wireOp",EDGE,"1cb9c079-ea9b-4899-8069-e0e3048e911d.sketch_text.stroke-81"),sQuery(id+"FHMxAyK4CFUKdhS_1.wireOp",EDGE,"1cb9c079-ea9b-4899-8069-e0e3048e911d.sketch_text.stroke-82"),sQuery(id+"FHMxAyK4CFUKdhS_1.wireOp",EDGE,"1cb9c079-ea9b-4899-8069-e0e3048e911d.sketch_text.stroke-83"),sQuery(id+"FHMxAyK4CFUKdhS_1.wireOp",EDGE,"1cb9c079-ea9b-4899-8069-e0e3048e911d.sketch_text.stroke-84"),sQuery(id+"FHMxAyK4CFUKdhS_1.wireOp",EDGE,"1cb9c079-ea9b-4899-8069-e0e3048e911d.sketch_text.stroke-85"),sQuery(id+"FHMxAyK4CFUKdhS_1.wireOp",EDGE,"1cb9c079-ea9b-4899-8069-e0e3048e911d.sketch_text.stroke-86"),sQuery(id+"FHMxAyK4CFUKdhS_1.wireOp",EDGE,"1cb9c079-ea9b-4899-8069-e0e3048e911d.sketch_text.stroke-87"),sQuery(id+"FHMxAyK4CFUKdhS_1.wireOp",EDGE,"1cb9c079-ea9b-4899-8069-e0e3048e911d.sketch_text.stroke-88"),sQuery(id+"FHMxAyK4CFUKdhS_1.wireOp",EDGE,"1cb9c079-ea9b-4899-8069-e0e3048e911d.sketch_text.stroke-89"),sQuery(id+"FHMxAyK4CFUKdhS_1.wireOp",EDGE,"1cb9c079-ea9b-4899-8069-e0e3048e911d.sketch_text.stroke-90"),sQuery(id+"FHMxAyK4CFUKdhS_1.wireOp",EDGE,"1cb9c079-ea9b-4899-8069-e0e3048e911d.sketch_text.stroke-91"),sQuery(id+"FHMxAyK4CFUKdhS_1.wireOp",EDGE,"1cb9c079-ea9b-4899-8069-e0e3048e911d.sketch_text.stroke-92"),sQuery(id+"FHMxAyK4CFUKdhS_1.wireOp",EDGE,"1cb9c079-ea9b-4899-8069-e0e3048e911d.sketch_text.stroke-93"),sQuery(id+"FHMxAyK4CFUKdhS_1.wireOp",EDGE,"1cb9c079-ea9b-4899-8069-e0e3048e911d.sketch_text.stroke-94"),sQuery(id+"FHMxAyK4CFUKdhS_1.wireOp",EDGE,"1cb9c079-ea9b-4899-8069-e0e3048e911d.sketch_text.stroke-95"),sQuery(id+"FHMxAyK4CFUKdhS_1.wireOp",EDGE,"1cb9c079-ea9b-4899-8069-e0e3048e911d.sketch_text.stroke-96"),sQuery(id+"FHMxAyK4CFUKdhS_1.wireOp",EDGE,"1cb9c079-ea9b-4899-8069-e0e3048e911d.sketch_text.stroke-97"),sQuery(id+"FHMxAyK4CFUKdhS_1.wireOp",EDGE,"1cb9c079-ea9b-4899-8069-e0e3048e911d.sketch_text.stroke-103"),sQuery(id+"FHMxAyK4CFUKdhS_1.wireOp",EDGE,"1cb9c079-ea9b-4899-8069-e0e3048e911d.sketch_text.stroke-104"),sQuery(id+"FHMxAyK4CFUKdhS_1.wireOp",EDGE,"1cb9c079-ea9b-4899-8069-e0e3048e911d.sketch_text.stroke-105"),sQuery(id+"FHMxAyK4CFUKdhS_1.wireOp",EDGE,"1cb9c079-ea9b-4899-8069-e0e3048e911d.sketch_text.stroke-106"),sQuery(id+"FHMxAyK4CFUKdhS_1.wireOp",EDGE,"1cb9c079-ea9b-4899-8069-e0e3048e911d.sketch_text.stroke-107"),sQuery(id+"FHMxAyK4CFUKdhS_1.wireOp",EDGE,"1cb9c079-ea9b-4899-8069-e0e3048e911d.sketch_text.stroke-108"),sQuery(id+"FHMxAyK4CFUKdhS_1.wireOp",EDGE,"1cb9c079-ea9b-4899-8069-e0e3048e911d.sketch_text.stroke-109"),sQuery(id+"FHMxAyK4CFUKdhS_1.wireOp",EDGE,"1cb9c079-ea9b-4899-8069-e0e3048e911d.sketch_text.stroke-110"),sQuery(id+"FHMxAyK4CFUKdhS_1.wireOp",EDGE,"1cb9c079-ea9b-4899-8069-e0e3048e911d.sketch_text.stroke-111"),sQuery(id+"FHMxAyK4CFUKdhS_1.wireOp",EDGE,"1cb9c079-ea9b-4899-8069-e0e3048e911d.sketch_text.stroke-112"),sQuery(id+"FHMxAyK4CFUKdhS_1.wireOp",EDGE,"1cb9c079-ea9b-4899-8069-e0e3048e911d.sketch_text.stroke-113"),sQuery(id+"FHMxAyK4CFUKdhS_1.wireOp",EDGE,"1cb9c079-ea9b-4899-8069-e0e3048e911d.sketch_text.stroke-114"),sQuery(id+"FHMxAyK4CFUKdhS_1.wireOp",EDGE,"1cb9c079-ea9b-4899-8069-e0e3048e911d.sketch_text.stroke-115"),sQuery(id+"FHMxAyK4CFUKdhS_1.wireOp",EDGE,"1cb9c079-ea9b-4899-8069-e0e3048e911d.sketch_text.stroke-116"),sQuery(id+"FHMxAyK4CFUKdhS_1.wireOp",EDGE,"1cb9c079-ea9b-4899-8069-e0e3048e911d.sketch_text.stroke-117"),sQuery(id+"FHMxAyK4CFUKdhS_1.wireOp",EDGE,"1cb9c079-ea9b-4899-8069-e0e3048e911d.sketch_text.stroke-118"),sQuery(id+"FHMxAyK4CFUKdhS_1.wireOp",EDGE,"1cb9c079-ea9b-4899-8069-e0e3048e911d.sketch_text.stroke-119"),sQuery(id+"FHMxAyK4CFUKdhS_1.wireOp",EDGE,"1cb9c079-ea9b-4899-8069-e0e3048e911d.sketch_text.stroke-120"),sQuery(id+"FHMxAyK4CFUKdhS_1.wireOp",EDGE,"1cb9c079-ea9b-4899-8069-e0e3048e911d.sketch_text.stroke-121"),sQuery(id+"FHMxAyK4CFUKdhS_1.wireOp",EDGE,"1cb9c079-ea9b-4899-8069-e0e3048e911d.sketch_text.stroke-122"),sQuery(id+"FHMxAyK4CFUKdhS_1.wireOp",EDGE,"1cb9c079-ea9b-4899-8069-e0e3048e911d.sketch_text.stroke-123"),sQuery(id+"FHMxAyK4CFUKdhS_1.wireOp",EDGE,"1cb9c079-ea9b-4899-8069-e0e3048e911d.sketch_text.stroke-124"),sQuery(id+"FHMxAyK4CFUKdhS_1.wireOp",EDGE,"1cb9c079-ea9b-4899-8069-e0e3048e911d.sketch_text.stroke-125"),sQuery(id+"FHMxAyK4CFUKdhS_1.wireOp",EDGE,"1cb9c079-ea9b-4899-8069-e0e3048e911d.sketch_text.stroke-126"),sQuery(id+"FHMxAyK4CFUKdhS_1.wireOp",EDGE,"1cb9c079-ea9b-4899-8069-e0e3048e911d.sketch_text.stroke-127"),sQuery(id+"FHMxAyK4CFUKdhS_1.wireOp",EDGE,"1cb9c079-ea9b-4899-8069-e0e3048e911d.sketch_text.stroke-128"),sQuery(id+"FHMxAyK4CFUKdhS_1.wireOp",EDGE,"1cb9c079-ea9b-4899-8069-e0e3048e911d.sketch_text.stroke-129"),sQuery(id+"FHMxAyK4CFUKdhS_1.wireOp",EDGE,"1cb9c079-ea9b-4899-8069-e0e3048e911d.sketch_text.stroke-130"),sQuery(id+"FHMxAyK4CFUKdhS_1.wireOp",EDGE,"1cb9c079-ea9b-4899-8069-e0e3048e911d.sketch_text.stroke-131"),sQuery(id+"FHMxAyK4CFUKdhS_1.wireOp",EDGE,"1cb9c079-ea9b-4899-8069-e0e3048e911d.sketch_text.stroke-132"),sQuery(id+"FHMxAyK4CFUKdhS_1.wireOp",EDGE,"1cb9c079-ea9b-4899-8069-e0e3048e911d.sketch_text.stroke-133"),sQuery(id+"FHMxAyK4CFUKdhS_1.wireOp",EDGE,"1cb9c079-ea9b-4899-8069-e0e3048e911d.sketch_text.stroke-134"),sQuery(id+"FHMxAyK4CFUKdhS_1.wireOp",EDGE,"1cb9c079-ea9b-4899-8069-e0e3048e911d.sketch_text.stroke-135"),sQuery(id+"FHMxAyK4CFUKdhS_1.wireOp",EDGE,"1cb9c079-ea9b-4899-8069-e0e3048e911d.sketch_text.stroke-136"),sQuery(id+"FHMxAyK4CFUKdhS_1.wireOp",EDGE,"1cb9c079-ea9b-4899-8069-e0e3048e911d.sketch_text.stroke-137"),sQuery(id+"FHMxAyK4CFUKdhS_1.wireOp",EDGE,"1cb9c079-ea9b-4899-8069-e0e3048e911d.sketch_text.stroke-138"),sQuery(id+"FHMxAyK4CFUKdhS_1.wireOp",EDGE,"1cb9c079-ea9b-4899-8069-e0e3048e911d.sketch_text.stroke-139"),sQuery(id+"FHMxAyK4CFUKdhS_1.wireOp",EDGE,"1cb9c079-ea9b-4899-8069-e0e3048e911d.sketch_text.stroke-140"),sQuery(id+"FHMxAyK4CFUKdhS_1.wireOp",EDGE,"1cb9c079-ea9b-4899-8069-e0e3048e911d.sketch_text.stroke-141"),sQuery(id+"FHMxAyK4CFUKdhS_1.wireOp",EDGE,"1cb9c079-ea9b-4899-8069-e0e3048e911d.sketch_text.stroke-142"),sQuery(id+"FHMxAyK4CFUKdhS_1.wireOp",EDGE,"1cb9c079-ea9b-4899-8069-e0e3048e911d.sketch_text.stroke-143"),sQuery(id+"FHMxAyK4CFUKdhS_1.wireOp",EDGE,"1cb9c079-ea9b-4899-8069-e0e3048e911d.sketch_text.stroke-144"),sQuery(id+"FHMxAyK4CFUKdhS_1.wireOp",EDGE,"1cb9c079-ea9b-4899-8069-e0e3048e911d.sketch_text.stroke-145"),sQuery(id+"FHMxAyK4CFUKdhS_1.wireOp",EDGE,"1cb9c079-ea9b-4899-8069-e0e3048e911d.sketch_text.stroke-146"),sQuery(id+"FHMxAyK4CFUKdhS_1.wireOp",EDGE,"1cb9c079-ea9b-4899-8069-e0e3048e911d.sketch_text.stroke-147"),sQuery(id+"FHMxAyK4CFUKdhS_1.wireOp",EDGE,"1cb9c079-ea9b-4899-8069-e0e3048e911d.sketch_text.stroke-148"),sQuery(id+"FHMxAyK4CFUKdhS_1.wireOp",EDGE,"1cb9c079-ea9b-4899-8069-e0e3048e911d.sketch_text.stroke-149"),sQuery(id+"FHMxAyK4CFUKdhS_1.wireOp",EDGE,"1cb9c079-ea9b-4899-8069-e0e3048e911d.sketch_text.stroke-150"),sQuery(id+"FHMxAyK4CFUKdhS_1.wireOp",EDGE,"1cb9c079-ea9b-4899-8069-e0e3048e911d.sketch_text.stroke-151"),sQuery(id+"FHMxAyK4CFUKdhS_1.wireOp",EDGE,"1cb9c079-ea9b-4899-8069-e0e3048e911d.sketch_text.stroke-152"),sQuery(id+"FHMxAyK4CFUKdhS_1.wireOp",EDGE,"1cb9c079-ea9b-4899-8069-e0e3048e911d.sketch_text.stroke-153"),sQuery(id+"FHMxAyK4CFUKdhS_1.wireOp",EDGE,"1cb9c079-ea9b-4899-8069-e0e3048e911d.sketch_text.stroke-159"),sQuery(id+"FHMxAyK4CFUKdhS_1.wireOp",EDGE,"1cb9c079-ea9b-4899-8069-e0e3048e911d.sketch_text.stroke-160"),sQuery(id+"FHMxAyK4CFUKdhS_1.wireOp",EDGE,"1cb9c079-ea9b-4899-8069-e0e3048e911d.sketch_text.stroke-161"),sQuery(id+"FHMxAyK4CFUKdhS_1.wireOp",EDGE,"1cb9c079-ea9b-4899-8069-e0e3048e911d.sketch_text.stroke-162"),sQuery(id+"FHMxAyK4CFUKdhS_1.wireOp",EDGE,"1cb9c079-ea9b-4899-8069-e0e3048e911d.sketch_text.stroke-163"),sQuery(id+"FHMxAyK4CFUKdhS_1.wireOp",EDGE,"1cb9c079-ea9b-4899-8069-e0e3048e911d.sketch_text.stroke-164"),sQuery(id+"FHMxAyK4CFUKdhS_1.wireOp",EDGE,"1cb9c079-ea9b-4899-8069-e0e3048e911d.sketch_text.stroke-165"),sQuery(id+"FHMxAyK4CFUKdhS_1.wireOp",EDGE,"1cb9c079-ea9b-4899-8069-e0e3048e911d.sketch_text.stroke-166"),sQuery(id+"FHMxAyK4CFUKdhS_1.wireOp",EDGE,"1cb9c079-ea9b-4899-8069-e0e3048e911d.sketch_text.stroke-167"),sQuery(id+"FHMxAyK4CFUKdhS_1.wireOp",EDGE,"1cb9c079-ea9b-4899-8069-e0e3048e911d.sketch_text.stroke-168"),sQuery(id+"FHMxAyK4CFUKdhS_1.wireOp",EDGE,"1cb9c079-ea9b-4899-8069-e0e3048e911d.sketch_text.stroke-169"),sQuery(id+"FHMxAyK4CFUKdhS_1.wireOp",EDGE,"1cb9c079-ea9b-4899-8069-e0e3048e911d.sketch_text.stroke-170"),sQuery(id+"FHMxAyK4CFUKdhS_1.wireOp",EDGE,"1cb9c079-ea9b-4899-8069-e0e3048e911d.sketch_text.stroke-171"),sQuery(id+"FHMxAyK4CFUKdhS_1.wireOp",EDGE,"1cb9c079-ea9b-4899-8069-e0e3048e911d.sketch_text.stroke-172"),sQuery(id+"FHMxAyK4CFUKdhS_1.wireOp",EDGE,"1cb9c079-ea9b-4899-8069-e0e3048e911d.sketch_text.stroke-173"),sQuery(id+"FHMxAyK4CFUKdhS_1.wireOp",EDGE,"1cb9c079-ea9b-4899-8069-e0e3048e911d.sketch_text.stroke-174"),sQuery(id+"FHMxAyK4CFUKdhS_1.wireOp",EDGE,"1cb9c079-ea9b-4899-8069-e0e3048e911d.sketch_text.stroke-175"),sQuery(id+"FHMxAyK4CFUKdhS_1.wireOp",EDGE,"1cb9c079-ea9b-4899-8069-e0e3048e911d.sketch_text.stroke-176"),sQuery(id+"FHMxAyK4CFUKdhS_1.wireOp",EDGE,"1cb9c079-ea9b-4899-8069-e0e3048e911d.sketch_text.stroke-177"),sQuery(id+"FHMxAyK4CFUKdhS_1.wireOp",EDGE,"1cb9c079-ea9b-4899-8069-e0e3048e911d.sketch_text.stroke-178"),sQuery(id+"FHMxAyK4CFUKdhS_1.wireOp",EDGE,"1cb9c079-ea9b-4899-8069-e0e3048e911d.sketch_text.stroke-179"),sQuery(id+"FHMxAyK4CFUKdhS_1.wireOp",EDGE,"1cb9c079-ea9b-4899-8069-e0e3048e911d.sketch_text.stroke-180"),sQuery(id+"F3.wireOp",EDGE,"727ac2c1-f511-4829-95a7-a443ef16a4cd"),subQ2])],"isStart":true}),makeQuery(id+"F4.opExtrude","SWEPT_FACE",FACE,{"disambiguationData":[OSD([subQ2])]})])],"derivedFrom":makeQuery(id+"F4.opExtrude","CAP_EDGE",EDGE,{"disambiguationData":[OSD([subQ2])],"isStart":true})});}
            var Q18;
            {var subQ0=sQuery(id+"F0.wireOp",EDGE,"E0.top");var subQ1=sQuery(id+"F0.wireOp",EDGE,"E0.bottom");var subQ2=sQuery(id+"F3.wireOp",EDGE,"1a034e28-a7c2-419d-97de-c33d70a47301");Q18=makeQuery(id+"F4.boolean.opBoolean","SPLIT",EDGE,{"disambiguationData":[TD([makeQuery(id+"F1.opExtrude","CAP_FACE",FACE,{"disambiguationData":[OSD([subQ1,subQ0,sQuery(id+"F0.wireOp",EDGE,"E0.left"),sQuery(id+"F0.wireOp",EDGE,"E0.right")])],"isStart":false}),makeQuery(id+"F1.opExtrude","SWEPT_FACE",FACE,{"disambiguationData":[OSD([subQ0])]}),makeQuery(id+"F4.opExtrude","CAP_FACE",FACE,{"disambiguationData":[OSD([subQ1,sQuery(id+"F2.wireOp",EDGE,"fcba4419-a2ee-464f-be9d-58f11bf3418b.sketch_text.stroke-0"),sQuery(id+"F2.wireOp",EDGE,"fcba4419-a2ee-464f-be9d-58f11bf3418b.sketch_text.stroke-1"),sQuery(id+"F2.wireOp",EDGE,"fcba4419-a2ee-464f-be9d-58f11bf3418b.sketch_text.stroke-2"),sQuery(id+"F2.wireOp",EDGE,"fcba4419-a2ee-464f-be9d-58f11bf3418b.sketch_text.stroke-3"),sQuery(id+"F2.wireOp",EDGE,"fcba4419-a2ee-464f-be9d-58f11bf3418b.sketch_text.stroke-4"),sQuery(id+"F2.wireOp",EDGE,"fcba4419-a2ee-464f-be9d-58f11bf3418b.sketch_text.stroke-5"),sQuery(id+"F2.wireOp",EDGE,"fcba4419-a2ee-464f-be9d-58f11bf3418b.sketch_text.stroke-6"),sQuery(id+"F2.wireOp",EDGE,"fcba4419-a2ee-464f-be9d-58f11bf3418b.sketch_text.stroke-7"),sQuery(id+"F2.wireOp",EDGE,"fcba4419-a2ee-464f-be9d-58f11bf3418b.sketch_text.stroke-8"),sQuery(id+"F2.wireOp",EDGE,"fcba4419-a2ee-464f-be9d-58f11bf3418b.sketch_text.stroke-9"),sQuery(id+"F2.wireOp",EDGE,"fcba4419-a2ee-464f-be9d-58f11bf3418b.sketch_text.stroke-10"),sQuery(id+"F2.wireOp",EDGE,"fcba4419-a2ee-464f-be9d-58f11bf3418b.sketch_text.stroke-11"),sQuery(id+"F2.wireOp",EDGE,"fcba4419-a2ee-464f-be9d-58f11bf3418b.sketch_text.stroke-12"),sQuery(id+"F2.wireOp",EDGE,"fcba4419-a2ee-464f-be9d-58f11bf3418b.sketch_text.stroke-13"),sQuery(id+"F2.wireOp",EDGE,"fcba4419-a2ee-464f-be9d-58f11bf3418b.sketch_text.stroke-14"),sQuery(id+"F2.wireOp",EDGE,"fcba4419-a2ee-464f-be9d-58f11bf3418b.sketch_text.stroke-15"),sQuery(id+"F2.wireOp",EDGE,"fcba4419-a2ee-464f-be9d-58f11bf3418b.sketch_text.stroke-16"),sQuery(id+"F2.wireOp",EDGE,"fcba4419-a2ee-464f-be9d-58f11bf3418b.sketch_text.stroke-17"),sQuery(id+"F2.wireOp",EDGE,"fcba4419-a2ee-464f-be9d-58f11bf3418b.sketch_text.stroke-18"),sQuery(id+"F2.wireOp",EDGE,"fcba4419-a2ee-464f-be9d-58f11bf3418b.sketch_text.stroke-19"),sQuery(id+"F2.wireOp",EDGE,"fcba4419-a2ee-464f-be9d-58f11bf3418b.sketch_text.stroke-20"),sQuery(id+"F2.wireOp",EDGE,"fcba4419-a2ee-464f-be9d-58f11bf3418b.sketch_text.stroke-21"),sQuery(id+"F2.wireOp",EDGE,"fcba4419-a2ee-464f-be9d-58f11bf3418b.sketch_text.stroke-22"),sQuery(id+"F2.wireOp",EDGE,"fcba4419-a2ee-464f-be9d-58f11bf3418b.sketch_text.stroke-23"),sQuery(id+"F2.wireOp",EDGE,"fcba4419-a2ee-464f-be9d-58f11bf3418b.sketch_text.stroke-24"),sQuery(id+"F2.wireOp",EDGE,"fcba4419-a2ee-464f-be9d-58f11bf3418b.sketch_text.stroke-25"),sQuery(id+"F2.wireOp",EDGE,"fcba4419-a2ee-464f-be9d-58f11bf3418b.sketch_text.stroke-26"),sQuery(id+"F2.wireOp",EDGE,"fcba4419-a2ee-464f-be9d-58f11bf3418b.sketch_text.stroke-27"),sQuery(id+"F2.wireOp",EDGE,"fcba4419-a2ee-464f-be9d-58f11bf3418b.sketch_text.stroke-28"),sQuery(id+"F2.wireOp",EDGE,"fcba4419-a2ee-464f-be9d-58f11bf3418b.sketch_text.stroke-29"),sQuery(id+"F2.wireOp",EDGE,"fcba4419-a2ee-464f-be9d-58f11bf3418b.sketch_text.stroke-30"),sQuery(id+"F2.wireOp",EDGE,"fcba4419-a2ee-464f-be9d-58f11bf3418b.sketch_text.stroke-31"),sQuery(id+"F2.wireOp",EDGE,"fcba4419-a2ee-464f-be9d-58f11bf3418b.sketch_text.stroke-32"),sQuery(id+"F2.wireOp",EDGE,"fcba4419-a2ee-464f-be9d-58f11bf3418b.sketch_text.stroke-33"),sQuery(id+"F2.wireOp",EDGE,"fcba4419-a2ee-464f-be9d-58f11bf3418b.sketch_text.stroke-34"),sQuery(id+"F2.wireOp",EDGE,"fcba4419-a2ee-464f-be9d-58f11bf3418b.sketch_text.stroke-35"),sQuery(id+"F2.wireOp",EDGE,"fcba4419-a2ee-464f-be9d-58f11bf3418b.sketch_text.stroke-36"),sQuery(id+"F2.wireOp",EDGE,"fcba4419-a2ee-464f-be9d-58f11bf3418b.sketch_text.stroke-37"),sQuery(id+"F2.wireOp",EDGE,"fcba4419-a2ee-464f-be9d-58f11bf3418b.sketch_text.stroke-38"),sQuery(id+"F2.wireOp",EDGE,"fcba4419-a2ee-464f-be9d-58f11bf3418b.sketch_text.stroke-39"),sQuery(id+"F2.wireOp",EDGE,"fcba4419-a2ee-464f-be9d-58f11bf3418b.sketch_text.stroke-40"),sQuery(id+"F2.wireOp",EDGE,"fcba4419-a2ee-464f-be9d-58f11bf3418b.sketch_text.stroke-41"),sQuery(id+"F2.wireOp",EDGE,"fcba4419-a2ee-464f-be9d-58f11bf3418b.sketch_text.stroke-42"),sQuery(id+"F2.wireOp",EDGE,"fcba4419-a2ee-464f-be9d-58f11bf3418b.sketch_text.stroke-43"),sQuery(id+"F2.wireOp",EDGE,"fcba4419-a2ee-464f-be9d-58f11bf3418b.sketch_text.stroke-44"),sQuery(id+"F2.wireOp",EDGE,"fcba4419-a2ee-464f-be9d-58f11bf3418b.sketch_text.stroke-45"),sQuery(id+"F2.wireOp",EDGE,"fcba4419-a2ee-464f-be9d-58f11bf3418b.sketch_text.stroke-46"),sQuery(id+"F2.wireOp",EDGE,"fcba4419-a2ee-464f-be9d-58f11bf3418b.sketch_text.stroke-47"),sQuery(id+"F2.wireOp",EDGE,"fcba4419-a2ee-464f-be9d-58f11bf3418b.sketch_text.stroke-48"),sQuery(id+"F2.wireOp",EDGE,"fcba4419-a2ee-464f-be9d-58f11bf3418b.sketch_text.stroke-49"),sQuery(id+"F2.wireOp",EDGE,"fcba4419-a2ee-464f-be9d-58f11bf3418b.sketch_text.stroke-50"),sQuery(id+"F2.wireOp",EDGE,"fcba4419-a2ee-464f-be9d-58f11bf3418b.sketch_text.stroke-51"),sQuery(id+"F2.wireOp",EDGE,"fcba4419-a2ee-464f-be9d-58f11bf3418b.sketch_text.stroke-52"),sQuery(id+"F2.wireOp",EDGE,"fcba4419-a2ee-464f-be9d-58f11bf3418b.sketch_text.stroke-53"),sQuery(id+"F2.wireOp",EDGE,"fcba4419-a2ee-464f-be9d-58f11bf3418b.sketch_text.stroke-54"),sQuery(id+"F2.wireOp",EDGE,"fcba4419-a2ee-464f-be9d-58f11bf3418b.sketch_text.stroke-55"),sQuery(id+"F2.wireOp",EDGE,"fcba4419-a2ee-464f-be9d-58f11bf3418b.sketch_text.stroke-56"),sQuery(id+"F2.wireOp",EDGE,"fcba4419-a2ee-464f-be9d-58f11bf3418b.sketch_text.stroke-57"),sQuery(id+"F2.wireOp",EDGE,"fcba4419-a2ee-464f-be9d-58f11bf3418b.sketch_text.stroke-58"),sQuery(id+"F2.wireOp",EDGE,"fcba4419-a2ee-464f-be9d-58f11bf3418b.sketch_text.stroke-59"),sQuery(id+"F2.wireOp",EDGE,"fcba4419-a2ee-464f-be9d-58f11bf3418b.sketch_text.stroke-60"),sQuery(id+"F2.wireOp",EDGE,"fcba4419-a2ee-464f-be9d-58f11bf3418b.sketch_text.stroke-61"),sQuery(id+"F2.wireOp",EDGE,"fcba4419-a2ee-464f-be9d-58f11bf3418b.sketch_text.stroke-62"),sQuery(id+"F2.wireOp",EDGE,"fcba4419-a2ee-464f-be9d-58f11bf3418b.sketch_text.stroke-63"),sQuery(id+"F2.wireOp",EDGE,"fcba4419-a2ee-464f-be9d-58f11bf3418b.sketch_text.stroke-64"),sQuery(id+"F2.wireOp",EDGE,"fcba4419-a2ee-464f-be9d-58f11bf3418b.sketch_text.stroke-65"),sQuery(id+"F2.wireOp",EDGE,"fcba4419-a2ee-464f-be9d-58f11bf3418b.sketch_text.stroke-66"),sQuery(id+"F2.wireOp",EDGE,"fcba4419-a2ee-464f-be9d-58f11bf3418b.sketch_text.stroke-67"),sQuery(id+"F2.wireOp",EDGE,"fcba4419-a2ee-464f-be9d-58f11bf3418b.sketch_text.stroke-68"),sQuery(id+"F2.wireOp",EDGE,"fcba4419-a2ee-464f-be9d-58f11bf3418b.sketch_text.stroke-69"),sQuery(id+"F2.wireOp",EDGE,"fcba4419-a2ee-464f-be9d-58f11bf3418b.sketch_text.stroke-70"),sQuery(id+"F2.wireOp",EDGE,"fcba4419-a2ee-464f-be9d-58f11bf3418b.sketch_text.stroke-71"),sQuery(id+"F2.wireOp",EDGE,"fcba4419-a2ee-464f-be9d-58f11bf3418b.sketch_text.stroke-72"),sQuery(id+"F2.wireOp",EDGE,"fcba4419-a2ee-464f-be9d-58f11bf3418b.sketch_text.stroke-73"),sQuery(id+"F2.wireOp",EDGE,"fcba4419-a2ee-464f-be9d-58f11bf3418b.sketch_text.stroke-74"),sQuery(id+"F2.wireOp",EDGE,"fcba4419-a2ee-464f-be9d-58f11bf3418b.sketch_text.stroke-75"),sQuery(id+"F2.wireOp",EDGE,"fcba4419-a2ee-464f-be9d-58f11bf3418b.sketch_text.stroke-76"),sQuery(id+"F2.wireOp",EDGE,"fcba4419-a2ee-464f-be9d-58f11bf3418b.sketch_text.stroke-77"),sQuery(id+"F2.wireOp",EDGE,"fcba4419-a2ee-464f-be9d-58f11bf3418b.sketch_text.stroke-78"),sQuery(id+"F2.wireOp",EDGE,"fcba4419-a2ee-464f-be9d-58f11bf3418b.sketch_text.stroke-79"),sQuery(id+"F2.wireOp",EDGE,"fcba4419-a2ee-464f-be9d-58f11bf3418b.sketch_text.stroke-80"),sQuery(id+"F2.wireOp",EDGE,"fcba4419-a2ee-464f-be9d-58f11bf3418b.sketch_text.stroke-81"),sQuery(id+"F2.wireOp",EDGE,"fcba4419-a2ee-464f-be9d-58f11bf3418b.sketch_text.stroke-82"),sQuery(id+"F2.wireOp",EDGE,"fcba4419-a2ee-464f-be9d-58f11bf3418b.sketch_text.stroke-83"),sQuery(id+"F2.wireOp",EDGE,"fcba4419-a2ee-464f-be9d-58f11bf3418b.sketch_text.stroke-84"),sQuery(id+"F2.wireOp",EDGE,"fcba4419-a2ee-464f-be9d-58f11bf3418b.sketch_text.stroke-85"),sQuery(id+"F2.wireOp",EDGE,"fcba4419-a2ee-464f-be9d-58f11bf3418b.sketch_text.stroke-86"),sQuery(id+"F2.wireOp",EDGE,"fcba4419-a2ee-464f-be9d-58f11bf3418b.sketch_text.stroke-87"),sQuery(id+"F2.wireOp",EDGE,"fcba4419-a2ee-464f-be9d-58f11bf3418b.sketch_text.stroke-88"),sQuery(id+"F2.wireOp",EDGE,"fcba4419-a2ee-464f-be9d-58f11bf3418b.sketch_text.stroke-89"),sQuery(id+"F2.wireOp",EDGE,"fcba4419-a2ee-464f-be9d-58f11bf3418b.sketch_text.stroke-90"),sQuery(id+"F2.wireOp",EDGE,"fcba4419-a2ee-464f-be9d-58f11bf3418b.sketch_text.stroke-91"),sQuery(id+"F2.wireOp",EDGE,"fcba4419-a2ee-464f-be9d-58f11bf3418b.sketch_text.stroke-92"),sQuery(id+"F2.wireOp",EDGE,"fcba4419-a2ee-464f-be9d-58f11bf3418b.sketch_text.stroke-93"),sQuery(id+"F2.wireOp",EDGE,"fcba4419-a2ee-464f-be9d-58f11bf3418b.sketch_text.stroke-94"),sQuery(id+"F2.wireOp",EDGE,"fcba4419-a2ee-464f-be9d-58f11bf3418b.sketch_text.stroke-95"),sQuery(id+"F2.wireOp",EDGE,"fcba4419-a2ee-464f-be9d-58f11bf3418b.sketch_text.stroke-96"),sQuery(id+"F2.wireOp",EDGE,"fcba4419-a2ee-464f-be9d-58f11bf3418b.sketch_text.stroke-97"),sQuery(id+"F2.wireOp",EDGE,"fcba4419-a2ee-464f-be9d-58f11bf3418b.sketch_text.stroke-98"),sQuery(id+"F2.wireOp",EDGE,"fcba4419-a2ee-464f-be9d-58f11bf3418b.sketch_text.stroke-99"),sQuery(id+"F2.wireOp",EDGE,"fcba4419-a2ee-464f-be9d-58f11bf3418b.sketch_text.stroke-100"),sQuery(id+"F2.wireOp",EDGE,"fcba4419-a2ee-464f-be9d-58f11bf3418b.sketch_text.stroke-101"),sQuery(id+"F2.wireOp",EDGE,"fcba4419-a2ee-464f-be9d-58f11bf3418b.sketch_text.stroke-102"),sQuery(id+"F2.wireOp",EDGE,"fcba4419-a2ee-464f-be9d-58f11bf3418b.sketch_text.stroke-103"),sQuery(id+"F2.wireOp",EDGE,"fcba4419-a2ee-464f-be9d-58f11bf3418b.sketch_text.stroke-104"),sQuery(id+"F2.wireOp",EDGE,"fcba4419-a2ee-464f-be9d-58f11bf3418b.sketch_text.stroke-105"),sQuery(id+"F2.wireOp",EDGE,"fcba4419-a2ee-464f-be9d-58f11bf3418b.sketch_text.stroke-106"),sQuery(id+"F2.wireOp",EDGE,"fcba4419-a2ee-464f-be9d-58f11bf3418b.sketch_text.stroke-107"),sQuery(id+"F2.wireOp",EDGE,"fcba4419-a2ee-464f-be9d-58f11bf3418b.sketch_text.stroke-108"),sQuery(id+"F2.wireOp",EDGE,"fcba4419-a2ee-464f-be9d-58f11bf3418b.sketch_text.stroke-109"),sQuery(id+"F2.wireOp",EDGE,"fcba4419-a2ee-464f-be9d-58f11bf3418b.sketch_text.stroke-110"),sQuery(id+"F2.wireOp",EDGE,"fcba4419-a2ee-464f-be9d-58f11bf3418b.sketch_text.stroke-111"),sQuery(id+"F2.wireOp",EDGE,"fcba4419-a2ee-464f-be9d-58f11bf3418b.sketch_text.stroke-112"),sQuery(id+"F2.wireOp",EDGE,"fcba4419-a2ee-464f-be9d-58f11bf3418b.sketch_text.stroke-113"),sQuery(id+"F2.wireOp",EDGE,"fcba4419-a2ee-464f-be9d-58f11bf3418b.sketch_text.stroke-114"),sQuery(id+"F2.wireOp",EDGE,"fcba4419-a2ee-464f-be9d-58f11bf3418b.sketch_text.stroke-115"),sQuery(id+"F2.wireOp",EDGE,"fcba4419-a2ee-464f-be9d-58f11bf3418b.sketch_text.stroke-116"),sQuery(id+"F2.wireOp",EDGE,"fcba4419-a2ee-464f-be9d-58f11bf3418b.sketch_text.stroke-117"),sQuery(id+"F2.wireOp",EDGE,"fcba4419-a2ee-464f-be9d-58f11bf3418b.sketch_text.stroke-118"),sQuery(id+"F2.wireOp",EDGE,"fcba4419-a2ee-464f-be9d-58f11bf3418b.sketch_text.stroke-119"),sQuery(id+"F2.wireOp",EDGE,"fcba4419-a2ee-464f-be9d-58f11bf3418b.sketch_text.stroke-120"),sQuery(id+"F2.wireOp",EDGE,"fcba4419-a2ee-464f-be9d-58f11bf3418b.sketch_text.stroke-121"),sQuery(id+"F2.wireOp",EDGE,"fcba4419-a2ee-464f-be9d-58f11bf3418b.sketch_text.stroke-122"),sQuery(id+"F2.wireOp",EDGE,"fcba4419-a2ee-464f-be9d-58f11bf3418b.sketch_text.stroke-123"),sQuery(id+"F2.wireOp",EDGE,"fcba4419-a2ee-464f-be9d-58f11bf3418b.sketch_text.stroke-124"),sQuery(id+"F2.wireOp",EDGE,"fcba4419-a2ee-464f-be9d-58f11bf3418b.sketch_text.stroke-125"),sQuery(id+"F2.wireOp",EDGE,"fcba4419-a2ee-464f-be9d-58f11bf3418b.sketch_text.stroke-126"),sQuery(id+"F2.wireOp",EDGE,"fcba4419-a2ee-464f-be9d-58f11bf3418b.sketch_text.stroke-127"),sQuery(id+"F2.wireOp",EDGE,"fcba4419-a2ee-464f-be9d-58f11bf3418b.sketch_text.stroke-128"),sQuery(id+"F2.wireOp",EDGE,"fcba4419-a2ee-464f-be9d-58f11bf3418b.sketch_text.stroke-129"),sQuery(id+"F2.wireOp",EDGE,"fcba4419-a2ee-464f-be9d-58f11bf3418b.sketch_text.stroke-130"),sQuery(id+"F2.wireOp",EDGE,"fcba4419-a2ee-464f-be9d-58f11bf3418b.sketch_text.stroke-131"),sQuery(id+"F2.wireOp",EDGE,"fcba4419-a2ee-464f-be9d-58f11bf3418b.sketch_text.stroke-132"),sQuery(id+"F2.wireOp",EDGE,"fcba4419-a2ee-464f-be9d-58f11bf3418b.sketch_text.stroke-133"),sQuery(id+"F2.wireOp",EDGE,"fcba4419-a2ee-464f-be9d-58f11bf3418b.sketch_text.stroke-134"),sQuery(id+"F2.wireOp",EDGE,"fcba4419-a2ee-464f-be9d-58f11bf3418b.sketch_text.stroke-135"),sQuery(id+"F2.wireOp",EDGE,"fcba4419-a2ee-464f-be9d-58f11bf3418b.sketch_text.stroke-136"),sQuery(id+"F2.wireOp",EDGE,"fcba4419-a2ee-464f-be9d-58f11bf3418b.sketch_text.stroke-137"),sQuery(id+"F2.wireOp",EDGE,"fcba4419-a2ee-464f-be9d-58f11bf3418b.sketch_text.stroke-138"),sQuery(id+"F2.wireOp",EDGE,"fcba4419-a2ee-464f-be9d-58f11bf3418b.sketch_text.stroke-139"),sQuery(id+"F2.wireOp",EDGE,"fcba4419-a2ee-464f-be9d-58f11bf3418b.sketch_text.stroke-140"),sQuery(id+"F2.wireOp",EDGE,"fcba4419-a2ee-464f-be9d-58f11bf3418b.sketch_text.stroke-141"),sQuery(id+"F2.wireOp",EDGE,"fcba4419-a2ee-464f-be9d-58f11bf3418b.sketch_text.stroke-142"),sQuery(id+"F2.wireOp",EDGE,"fcba4419-a2ee-464f-be9d-58f11bf3418b.sketch_text.stroke-143"),sQuery(id+"F2.wireOp",EDGE,"fcba4419-a2ee-464f-be9d-58f11bf3418b.sketch_text.stroke-144"),sQuery(id+"F2.wireOp",EDGE,"fcba4419-a2ee-464f-be9d-58f11bf3418b.sketch_text.stroke-145"),sQuery(id+"F2.wireOp",EDGE,"fcba4419-a2ee-464f-be9d-58f11bf3418b.sketch_text.stroke-146"),sQuery(id+"F2.wireOp",EDGE,"fcba4419-a2ee-464f-be9d-58f11bf3418b.sketch_text.stroke-147"),sQuery(id+"F2.wireOp",EDGE,"fcba4419-a2ee-464f-be9d-58f11bf3418b.sketch_text.stroke-148"),sQuery(id+"F2.wireOp",EDGE,"fcba4419-a2ee-464f-be9d-58f11bf3418b.sketch_text.stroke-149"),sQuery(id+"F2.wireOp",EDGE,"fcba4419-a2ee-464f-be9d-58f11bf3418b.sketch_text.stroke-150"),sQuery(id+"F2.wireOp",EDGE,"fcba4419-a2ee-464f-be9d-58f11bf3418b.sketch_text.stroke-151"),sQuery(id+"F2.wireOp",EDGE,"fcba4419-a2ee-464f-be9d-58f11bf3418b.sketch_text.stroke-152"),sQuery(id+"F2.wireOp",EDGE,"fcba4419-a2ee-464f-be9d-58f11bf3418b.sketch_text.stroke-153"),sQuery(id+"F2.wireOp",EDGE,"fcba4419-a2ee-464f-be9d-58f11bf3418b.sketch_text.stroke-154"),sQuery(id+"F2.wireOp",EDGE,"fcba4419-a2ee-464f-be9d-58f11bf3418b.sketch_text.stroke-155"),sQuery(id+"F2.wireOp",EDGE,"fcba4419-a2ee-464f-be9d-58f11bf3418b.sketch_text.stroke-156"),sQuery(id+"F2.wireOp",EDGE,"fcba4419-a2ee-464f-be9d-58f11bf3418b.sketch_text.stroke-157"),sQuery(id+"F2.wireOp",EDGE,"fcba4419-a2ee-464f-be9d-58f11bf3418b.sketch_text.stroke-158"),sQuery(id+"F2.wireOp",EDGE,"fcba4419-a2ee-464f-be9d-58f11bf3418b.sketch_text.stroke-159"),sQuery(id+"F2.wireOp",EDGE,"fcba4419-a2ee-464f-be9d-58f11bf3418b.sketch_text.stroke-160"),sQuery(id+"F2.wireOp",EDGE,"fcba4419-a2ee-464f-be9d-58f11bf3418b.sketch_text.stroke-161"),sQuery(id+"F2.wireOp",EDGE,"fcba4419-a2ee-464f-be9d-58f11bf3418b.sketch_text.stroke-162"),sQuery(id+"F2.wireOp",EDGE,"fcba4419-a2ee-464f-be9d-58f11bf3418b.sketch_text.stroke-163"),sQuery(id+"F2.wireOp",EDGE,"fcba4419-a2ee-464f-be9d-58f11bf3418b.sketch_text.stroke-164"),sQuery(id+"F2.wireOp",EDGE,"fcba4419-a2ee-464f-be9d-58f11bf3418b.sketch_text.stroke-165"),sQuery(id+"F2.wireOp",EDGE,"fcba4419-a2ee-464f-be9d-58f11bf3418b.sketch_text.stroke-166"),sQuery(id+"F2.wireOp",EDGE,"fcba4419-a2ee-464f-be9d-58f11bf3418b.sketch_text.stroke-167"),sQuery(id+"F2.wireOp",EDGE,"fcba4419-a2ee-464f-be9d-58f11bf3418b.sketch_text.stroke-168"),sQuery(id+"F2.wireOp",EDGE,"fcba4419-a2ee-464f-be9d-58f11bf3418b.sketch_text.stroke-169"),sQuery(id+"F2.wireOp",EDGE,"fcba4419-a2ee-464f-be9d-58f11bf3418b.sketch_text.stroke-170"),sQuery(id+"F2.wireOp",EDGE,"fcba4419-a2ee-464f-be9d-58f11bf3418b.sketch_text.stroke-171"),sQuery(id+"F2.wireOp",EDGE,"fcba4419-a2ee-464f-be9d-58f11bf3418b.sketch_text.stroke-172"),sQuery(id+"F2.wireOp",EDGE,"fcba4419-a2ee-464f-be9d-58f11bf3418b.sketch_text.stroke-173"),sQuery(id+"FHMxAyK4CFUKdhS_1.wireOp",EDGE,"1cb9c079-ea9b-4899-8069-e0e3048e911d.sketch_text.stroke-0"),sQuery(id+"FHMxAyK4CFUKdhS_1.wireOp",EDGE,"1cb9c079-ea9b-4899-8069-e0e3048e911d.sketch_text.stroke-1"),sQuery(id+"FHMxAyK4CFUKdhS_1.wireOp",EDGE,"1cb9c079-ea9b-4899-8069-e0e3048e911d.sketch_text.stroke-2"),sQuery(id+"FHMxAyK4CFUKdhS_1.wireOp",EDGE,"1cb9c079-ea9b-4899-8069-e0e3048e911d.sketch_text.stroke-3"),sQuery(id+"FHMxAyK4CFUKdhS_1.wireOp",EDGE,"1cb9c079-ea9b-4899-8069-e0e3048e911d.sketch_text.stroke-4"),sQuery(id+"FHMxAyK4CFUKdhS_1.wireOp",EDGE,"1cb9c079-ea9b-4899-8069-e0e3048e911d.sketch_text.stroke-5"),sQuery(id+"FHMxAyK4CFUKdhS_1.wireOp",EDGE,"1cb9c079-ea9b-4899-8069-e0e3048e911d.sketch_text.stroke-6"),sQuery(id+"FHMxAyK4CFUKdhS_1.wireOp",EDGE,"1cb9c079-ea9b-4899-8069-e0e3048e911d.sketch_text.stroke-7"),sQuery(id+"FHMxAyK4CFUKdhS_1.wireOp",EDGE,"1cb9c079-ea9b-4899-8069-e0e3048e911d.sketch_text.stroke-8"),sQuery(id+"FHMxAyK4CFUKdhS_1.wireOp",EDGE,"1cb9c079-ea9b-4899-8069-e0e3048e911d.sketch_text.stroke-9"),sQuery(id+"FHMxAyK4CFUKdhS_1.wireOp",EDGE,"1cb9c079-ea9b-4899-8069-e0e3048e911d.sketch_text.stroke-10"),sQuery(id+"FHMxAyK4CFUKdhS_1.wireOp",EDGE,"1cb9c079-ea9b-4899-8069-e0e3048e911d.sketch_text.stroke-11"),sQuery(id+"FHMxAyK4CFUKdhS_1.wireOp",EDGE,"1cb9c079-ea9b-4899-8069-e0e3048e911d.sketch_text.stroke-12"),sQuery(id+"FHMxAyK4CFUKdhS_1.wireOp",EDGE,"1cb9c079-ea9b-4899-8069-e0e3048e911d.sketch_text.stroke-13"),sQuery(id+"FHMxAyK4CFUKdhS_1.wireOp",EDGE,"1cb9c079-ea9b-4899-8069-e0e3048e911d.sketch_text.stroke-14"),sQuery(id+"FHMxAyK4CFUKdhS_1.wireOp",EDGE,"1cb9c079-ea9b-4899-8069-e0e3048e911d.sketch_text.stroke-15"),sQuery(id+"FHMxAyK4CFUKdhS_1.wireOp",EDGE,"1cb9c079-ea9b-4899-8069-e0e3048e911d.sketch_text.stroke-16"),sQuery(id+"FHMxAyK4CFUKdhS_1.wireOp",EDGE,"1cb9c079-ea9b-4899-8069-e0e3048e911d.sketch_text.stroke-17"),sQuery(id+"FHMxAyK4CFUKdhS_1.wireOp",EDGE,"1cb9c079-ea9b-4899-8069-e0e3048e911d.sketch_text.stroke-18"),sQuery(id+"FHMxAyK4CFUKdhS_1.wireOp",EDGE,"1cb9c079-ea9b-4899-8069-e0e3048e911d.sketch_text.stroke-19"),sQuery(id+"FHMxAyK4CFUKdhS_1.wireOp",EDGE,"1cb9c079-ea9b-4899-8069-e0e3048e911d.sketch_text.stroke-20"),sQuery(id+"FHMxAyK4CFUKdhS_1.wireOp",EDGE,"1cb9c079-ea9b-4899-8069-e0e3048e911d.sketch_text.stroke-21"),sQuery(id+"FHMxAyK4CFUKdhS_1.wireOp",EDGE,"1cb9c079-ea9b-4899-8069-e0e3048e911d.sketch_text.stroke-22"),sQuery(id+"FHMxAyK4CFUKdhS_1.wireOp",EDGE,"1cb9c079-ea9b-4899-8069-e0e3048e911d.sketch_text.stroke-23"),sQuery(id+"FHMxAyK4CFUKdhS_1.wireOp",EDGE,"1cb9c079-ea9b-4899-8069-e0e3048e911d.sketch_text.stroke-24"),sQuery(id+"FHMxAyK4CFUKdhS_1.wireOp",EDGE,"1cb9c079-ea9b-4899-8069-e0e3048e911d.sketch_text.stroke-25"),sQuery(id+"FHMxAyK4CFUKdhS_1.wireOp",EDGE,"1cb9c079-ea9b-4899-8069-e0e3048e911d.sketch_text.stroke-26"),sQuery(id+"FHMxAyK4CFUKdhS_1.wireOp",EDGE,"1cb9c079-ea9b-4899-8069-e0e3048e911d.sketch_text.stroke-27"),sQuery(id+"FHMxAyK4CFUKdhS_1.wireOp",EDGE,"1cb9c079-ea9b-4899-8069-e0e3048e911d.sketch_text.stroke-28"),sQuery(id+"FHMxAyK4CFUKdhS_1.wireOp",EDGE,"1cb9c079-ea9b-4899-8069-e0e3048e911d.sketch_text.stroke-29"),sQuery(id+"FHMxAyK4CFUKdhS_1.wireOp",EDGE,"1cb9c079-ea9b-4899-8069-e0e3048e911d.sketch_text.stroke-30"),sQuery(id+"FHMxAyK4CFUKdhS_1.wireOp",EDGE,"1cb9c079-ea9b-4899-8069-e0e3048e911d.sketch_text.stroke-31"),sQuery(id+"FHMxAyK4CFUKdhS_1.wireOp",EDGE,"1cb9c079-ea9b-4899-8069-e0e3048e911d.sketch_text.stroke-32"),sQuery(id+"FHMxAyK4CFUKdhS_1.wireOp",EDGE,"1cb9c079-ea9b-4899-8069-e0e3048e911d.sketch_text.stroke-33"),sQuery(id+"FHMxAyK4CFUKdhS_1.wireOp",EDGE,"1cb9c079-ea9b-4899-8069-e0e3048e911d.sketch_text.stroke-34"),sQuery(id+"FHMxAyK4CFUKdhS_1.wireOp",EDGE,"1cb9c079-ea9b-4899-8069-e0e3048e911d.sketch_text.stroke-35"),sQuery(id+"FHMxAyK4CFUKdhS_1.wireOp",EDGE,"1cb9c079-ea9b-4899-8069-e0e3048e911d.sketch_text.stroke-36"),sQuery(id+"FHMxAyK4CFUKdhS_1.wireOp",EDGE,"1cb9c079-ea9b-4899-8069-e0e3048e911d.sketch_text.stroke-37"),sQuery(id+"FHMxAyK4CFUKdhS_1.wireOp",EDGE,"1cb9c079-ea9b-4899-8069-e0e3048e911d.sketch_text.stroke-38"),sQuery(id+"FHMxAyK4CFUKdhS_1.wireOp",EDGE,"1cb9c079-ea9b-4899-8069-e0e3048e911d.sketch_text.stroke-39"),sQuery(id+"FHMxAyK4CFUKdhS_1.wireOp",EDGE,"1cb9c079-ea9b-4899-8069-e0e3048e911d.sketch_text.stroke-40"),sQuery(id+"FHMxAyK4CFUKdhS_1.wireOp",EDGE,"1cb9c079-ea9b-4899-8069-e0e3048e911d.sketch_text.stroke-41"),sQuery(id+"FHMxAyK4CFUKdhS_1.wireOp",EDGE,"1cb9c079-ea9b-4899-8069-e0e3048e911d.sketch_text.stroke-42"),sQuery(id+"FHMxAyK4CFUKdhS_1.wireOp",EDGE,"1cb9c079-ea9b-4899-8069-e0e3048e911d.sketch_text.stroke-43"),sQuery(id+"FHMxAyK4CFUKdhS_1.wireOp",EDGE,"1cb9c079-ea9b-4899-8069-e0e3048e911d.sketch_text.stroke-44"),sQuery(id+"FHMxAyK4CFUKdhS_1.wireOp",EDGE,"1cb9c079-ea9b-4899-8069-e0e3048e911d.sketch_text.stroke-45"),sQuery(id+"FHMxAyK4CFUKdhS_1.wireOp",EDGE,"1cb9c079-ea9b-4899-8069-e0e3048e911d.sketch_text.stroke-46"),sQuery(id+"FHMxAyK4CFUKdhS_1.wireOp",EDGE,"1cb9c079-ea9b-4899-8069-e0e3048e911d.sketch_text.stroke-47"),sQuery(id+"FHMxAyK4CFUKdhS_1.wireOp",EDGE,"1cb9c079-ea9b-4899-8069-e0e3048e911d.sketch_text.stroke-48"),sQuery(id+"FHMxAyK4CFUKdhS_1.wireOp",EDGE,"1cb9c079-ea9b-4899-8069-e0e3048e911d.sketch_text.stroke-49"),sQuery(id+"FHMxAyK4CFUKdhS_1.wireOp",EDGE,"1cb9c079-ea9b-4899-8069-e0e3048e911d.sketch_text.stroke-50"),sQuery(id+"FHMxAyK4CFUKdhS_1.wireOp",EDGE,"1cb9c079-ea9b-4899-8069-e0e3048e911d.sketch_text.stroke-51"),sQuery(id+"FHMxAyK4CFUKdhS_1.wireOp",EDGE,"1cb9c079-ea9b-4899-8069-e0e3048e911d.sketch_text.stroke-52"),sQuery(id+"FHMxAyK4CFUKdhS_1.wireOp",EDGE,"1cb9c079-ea9b-4899-8069-e0e3048e911d.sketch_text.stroke-53"),sQuery(id+"FHMxAyK4CFUKdhS_1.wireOp",EDGE,"1cb9c079-ea9b-4899-8069-e0e3048e911d.sketch_text.stroke-54"),sQuery(id+"FHMxAyK4CFUKdhS_1.wireOp",EDGE,"1cb9c079-ea9b-4899-8069-e0e3048e911d.sketch_text.stroke-55"),sQuery(id+"FHMxAyK4CFUKdhS_1.wireOp",EDGE,"1cb9c079-ea9b-4899-8069-e0e3048e911d.sketch_text.stroke-56"),sQuery(id+"FHMxAyK4CFUKdhS_1.wireOp",EDGE,"1cb9c079-ea9b-4899-8069-e0e3048e911d.sketch_text.stroke-57"),sQuery(id+"FHMxAyK4CFUKdhS_1.wireOp",EDGE,"1cb9c079-ea9b-4899-8069-e0e3048e911d.sketch_text.stroke-58"),sQuery(id+"FHMxAyK4CFUKdhS_1.wireOp",EDGE,"1cb9c079-ea9b-4899-8069-e0e3048e911d.sketch_text.stroke-59"),sQuery(id+"FHMxAyK4CFUKdhS_1.wireOp",EDGE,"1cb9c079-ea9b-4899-8069-e0e3048e911d.sketch_text.stroke-60"),sQuery(id+"FHMxAyK4CFUKdhS_1.wireOp",EDGE,"1cb9c079-ea9b-4899-8069-e0e3048e911d.sketch_text.stroke-61"),sQuery(id+"FHMxAyK4CFUKdhS_1.wireOp",EDGE,"1cb9c079-ea9b-4899-8069-e0e3048e911d.sketch_text.stroke-62"),sQuery(id+"FHMxAyK4CFUKdhS_1.wireOp",EDGE,"1cb9c079-ea9b-4899-8069-e0e3048e911d.sketch_text.stroke-71"),sQuery(id+"FHMxAyK4CFUKdhS_1.wireOp",EDGE,"1cb9c079-ea9b-4899-8069-e0e3048e911d.sketch_text.stroke-72"),sQuery(id+"FHMxAyK4CFUKdhS_1.wireOp",EDGE,"1cb9c079-ea9b-4899-8069-e0e3048e911d.sketch_text.stroke-73"),sQuery(id+"FHMxAyK4CFUKdhS_1.wireOp",EDGE,"1cb9c079-ea9b-4899-8069-e0e3048e911d.sketch_text.stroke-74"),sQuery(id+"FHMxAyK4CFUKdhS_1.wireOp",EDGE,"1cb9c079-ea9b-4899-8069-e0e3048e911d.sketch_text.stroke-75"),sQuery(id+"FHMxAyK4CFUKdhS_1.wireOp",EDGE,"1cb9c079-ea9b-4899-8069-e0e3048e911d.sketch_text.stroke-76"),sQuery(id+"FHMxAyK4CFUKdhS_1.wireOp",EDGE,"1cb9c079-ea9b-4899-8069-e0e3048e911d.sketch_text.stroke-77"),sQuery(id+"FHMxAyK4CFUKdhS_1.wireOp",EDGE,"1cb9c079-ea9b-4899-8069-e0e3048e911d.sketch_text.stroke-78"),sQuery(id+"FHMxAyK4CFUKdhS_1.wireOp",EDGE,"1cb9c079-ea9b-4899-8069-e0e3048e911d.sketch_text.stroke-79"),sQuery(id+"FHMxAyK4CFUKdhS_1.wireOp",EDGE,"1cb9c079-ea9b-4899-8069-e0e3048e911d.sketch_text.stroke-80"),sQuery(id+"FHMxAyK4CFUKdhS_1.wireOp",EDGE,"1cb9c079-ea9b-4899-8069-e0e3048e911d.sketch_text.stroke-81"),sQuery(id+"FHMxAyK4CFUKdhS_1.wireOp",EDGE,"1cb9c079-ea9b-4899-8069-e0e3048e911d.sketch_text.stroke-82"),sQuery(id+"FHMxAyK4CFUKdhS_1.wireOp",EDGE,"1cb9c079-ea9b-4899-8069-e0e3048e911d.sketch_text.stroke-83"),sQuery(id+"FHMxAyK4CFUKdhS_1.wireOp",EDGE,"1cb9c079-ea9b-4899-8069-e0e3048e911d.sketch_text.stroke-84"),sQuery(id+"FHMxAyK4CFUKdhS_1.wireOp",EDGE,"1cb9c079-ea9b-4899-8069-e0e3048e911d.sketch_text.stroke-85"),sQuery(id+"FHMxAyK4CFUKdhS_1.wireOp",EDGE,"1cb9c079-ea9b-4899-8069-e0e3048e911d.sketch_text.stroke-86"),sQuery(id+"FHMxAyK4CFUKdhS_1.wireOp",EDGE,"1cb9c079-ea9b-4899-8069-e0e3048e911d.sketch_text.stroke-87"),sQuery(id+"FHMxAyK4CFUKdhS_1.wireOp",EDGE,"1cb9c079-ea9b-4899-8069-e0e3048e911d.sketch_text.stroke-88"),sQuery(id+"FHMxAyK4CFUKdhS_1.wireOp",EDGE,"1cb9c079-ea9b-4899-8069-e0e3048e911d.sketch_text.stroke-89"),sQuery(id+"FHMxAyK4CFUKdhS_1.wireOp",EDGE,"1cb9c079-ea9b-4899-8069-e0e3048e911d.sketch_text.stroke-90"),sQuery(id+"FHMxAyK4CFUKdhS_1.wireOp",EDGE,"1cb9c079-ea9b-4899-8069-e0e3048e911d.sketch_text.stroke-91"),sQuery(id+"FHMxAyK4CFUKdhS_1.wireOp",EDGE,"1cb9c079-ea9b-4899-8069-e0e3048e911d.sketch_text.stroke-92"),sQuery(id+"FHMxAyK4CFUKdhS_1.wireOp",EDGE,"1cb9c079-ea9b-4899-8069-e0e3048e911d.sketch_text.stroke-93"),sQuery(id+"FHMxAyK4CFUKdhS_1.wireOp",EDGE,"1cb9c079-ea9b-4899-8069-e0e3048e911d.sketch_text.stroke-94"),sQuery(id+"FHMxAyK4CFUKdhS_1.wireOp",EDGE,"1cb9c079-ea9b-4899-8069-e0e3048e911d.sketch_text.stroke-95"),sQuery(id+"FHMxAyK4CFUKdhS_1.wireOp",EDGE,"1cb9c079-ea9b-4899-8069-e0e3048e911d.sketch_text.stroke-96"),sQuery(id+"FHMxAyK4CFUKdhS_1.wireOp",EDGE,"1cb9c079-ea9b-4899-8069-e0e3048e911d.sketch_text.stroke-97"),sQuery(id+"FHMxAyK4CFUKdhS_1.wireOp",EDGE,"1cb9c079-ea9b-4899-8069-e0e3048e911d.sketch_text.stroke-103"),sQuery(id+"FHMxAyK4CFUKdhS_1.wireOp",EDGE,"1cb9c079-ea9b-4899-8069-e0e3048e911d.sketch_text.stroke-104"),sQuery(id+"FHMxAyK4CFUKdhS_1.wireOp",EDGE,"1cb9c079-ea9b-4899-8069-e0e3048e911d.sketch_text.stroke-105"),sQuery(id+"FHMxAyK4CFUKdhS_1.wireOp",EDGE,"1cb9c079-ea9b-4899-8069-e0e3048e911d.sketch_text.stroke-106"),sQuery(id+"FHMxAyK4CFUKdhS_1.wireOp",EDGE,"1cb9c079-ea9b-4899-8069-e0e3048e911d.sketch_text.stroke-107"),sQuery(id+"FHMxAyK4CFUKdhS_1.wireOp",EDGE,"1cb9c079-ea9b-4899-8069-e0e3048e911d.sketch_text.stroke-108"),sQuery(id+"FHMxAyK4CFUKdhS_1.wireOp",EDGE,"1cb9c079-ea9b-4899-8069-e0e3048e911d.sketch_text.stroke-109"),sQuery(id+"FHMxAyK4CFUKdhS_1.wireOp",EDGE,"1cb9c079-ea9b-4899-8069-e0e3048e911d.sketch_text.stroke-110"),sQuery(id+"FHMxAyK4CFUKdhS_1.wireOp",EDGE,"1cb9c079-ea9b-4899-8069-e0e3048e911d.sketch_text.stroke-111"),sQuery(id+"FHMxAyK4CFUKdhS_1.wireOp",EDGE,"1cb9c079-ea9b-4899-8069-e0e3048e911d.sketch_text.stroke-112"),sQuery(id+"FHMxAyK4CFUKdhS_1.wireOp",EDGE,"1cb9c079-ea9b-4899-8069-e0e3048e911d.sketch_text.stroke-113"),sQuery(id+"FHMxAyK4CFUKdhS_1.wireOp",EDGE,"1cb9c079-ea9b-4899-8069-e0e3048e911d.sketch_text.stroke-114"),sQuery(id+"FHMxAyK4CFUKdhS_1.wireOp",EDGE,"1cb9c079-ea9b-4899-8069-e0e3048e911d.sketch_text.stroke-115"),sQuery(id+"FHMxAyK4CFUKdhS_1.wireOp",EDGE,"1cb9c079-ea9b-4899-8069-e0e3048e911d.sketch_text.stroke-116"),sQuery(id+"FHMxAyK4CFUKdhS_1.wireOp",EDGE,"1cb9c079-ea9b-4899-8069-e0e3048e911d.sketch_text.stroke-117"),sQuery(id+"FHMxAyK4CFUKdhS_1.wireOp",EDGE,"1cb9c079-ea9b-4899-8069-e0e3048e911d.sketch_text.stroke-118"),sQuery(id+"FHMxAyK4CFUKdhS_1.wireOp",EDGE,"1cb9c079-ea9b-4899-8069-e0e3048e911d.sketch_text.stroke-119"),sQuery(id+"FHMxAyK4CFUKdhS_1.wireOp",EDGE,"1cb9c079-ea9b-4899-8069-e0e3048e911d.sketch_text.stroke-120"),sQuery(id+"FHMxAyK4CFUKdhS_1.wireOp",EDGE,"1cb9c079-ea9b-4899-8069-e0e3048e911d.sketch_text.stroke-121"),sQuery(id+"FHMxAyK4CFUKdhS_1.wireOp",EDGE,"1cb9c079-ea9b-4899-8069-e0e3048e911d.sketch_text.stroke-122"),sQuery(id+"FHMxAyK4CFUKdhS_1.wireOp",EDGE,"1cb9c079-ea9b-4899-8069-e0e3048e911d.sketch_text.stroke-123"),sQuery(id+"FHMxAyK4CFUKdhS_1.wireOp",EDGE,"1cb9c079-ea9b-4899-8069-e0e3048e911d.sketch_text.stroke-124"),sQuery(id+"FHMxAyK4CFUKdhS_1.wireOp",EDGE,"1cb9c079-ea9b-4899-8069-e0e3048e911d.sketch_text.stroke-125"),sQuery(id+"FHMxAyK4CFUKdhS_1.wireOp",EDGE,"1cb9c079-ea9b-4899-8069-e0e3048e911d.sketch_text.stroke-126"),sQuery(id+"FHMxAyK4CFUKdhS_1.wireOp",EDGE,"1cb9c079-ea9b-4899-8069-e0e3048e911d.sketch_text.stroke-127"),sQuery(id+"FHMxAyK4CFUKdhS_1.wireOp",EDGE,"1cb9c079-ea9b-4899-8069-e0e3048e911d.sketch_text.stroke-128"),sQuery(id+"FHMxAyK4CFUKdhS_1.wireOp",EDGE,"1cb9c079-ea9b-4899-8069-e0e3048e911d.sketch_text.stroke-129"),sQuery(id+"FHMxAyK4CFUKdhS_1.wireOp",EDGE,"1cb9c079-ea9b-4899-8069-e0e3048e911d.sketch_text.stroke-130"),sQuery(id+"FHMxAyK4CFUKdhS_1.wireOp",EDGE,"1cb9c079-ea9b-4899-8069-e0e3048e911d.sketch_text.stroke-131"),sQuery(id+"FHMxAyK4CFUKdhS_1.wireOp",EDGE,"1cb9c079-ea9b-4899-8069-e0e3048e911d.sketch_text.stroke-132"),sQuery(id+"FHMxAyK4CFUKdhS_1.wireOp",EDGE,"1cb9c079-ea9b-4899-8069-e0e3048e911d.sketch_text.stroke-133"),sQuery(id+"FHMxAyK4CFUKdhS_1.wireOp",EDGE,"1cb9c079-ea9b-4899-8069-e0e3048e911d.sketch_text.stroke-134"),sQuery(id+"FHMxAyK4CFUKdhS_1.wireOp",EDGE,"1cb9c079-ea9b-4899-8069-e0e3048e911d.sketch_text.stroke-135"),sQuery(id+"FHMxAyK4CFUKdhS_1.wireOp",EDGE,"1cb9c079-ea9b-4899-8069-e0e3048e911d.sketch_text.stroke-136"),sQuery(id+"FHMxAyK4CFUKdhS_1.wireOp",EDGE,"1cb9c079-ea9b-4899-8069-e0e3048e911d.sketch_text.stroke-137"),sQuery(id+"FHMxAyK4CFUKdhS_1.wireOp",EDGE,"1cb9c079-ea9b-4899-8069-e0e3048e911d.sketch_text.stroke-138"),sQuery(id+"FHMxAyK4CFUKdhS_1.wireOp",EDGE,"1cb9c079-ea9b-4899-8069-e0e3048e911d.sketch_text.stroke-139"),sQuery(id+"FHMxAyK4CFUKdhS_1.wireOp",EDGE,"1cb9c079-ea9b-4899-8069-e0e3048e911d.sketch_text.stroke-140"),sQuery(id+"FHMxAyK4CFUKdhS_1.wireOp",EDGE,"1cb9c079-ea9b-4899-8069-e0e3048e911d.sketch_text.stroke-141"),sQuery(id+"FHMxAyK4CFUKdhS_1.wireOp",EDGE,"1cb9c079-ea9b-4899-8069-e0e3048e911d.sketch_text.stroke-142"),sQuery(id+"FHMxAyK4CFUKdhS_1.wireOp",EDGE,"1cb9c079-ea9b-4899-8069-e0e3048e911d.sketch_text.stroke-143"),sQuery(id+"FHMxAyK4CFUKdhS_1.wireOp",EDGE,"1cb9c079-ea9b-4899-8069-e0e3048e911d.sketch_text.stroke-144"),sQuery(id+"FHMxAyK4CFUKdhS_1.wireOp",EDGE,"1cb9c079-ea9b-4899-8069-e0e3048e911d.sketch_text.stroke-145"),sQuery(id+"FHMxAyK4CFUKdhS_1.wireOp",EDGE,"1cb9c079-ea9b-4899-8069-e0e3048e911d.sketch_text.stroke-146"),sQuery(id+"FHMxAyK4CFUKdhS_1.wireOp",EDGE,"1cb9c079-ea9b-4899-8069-e0e3048e911d.sketch_text.stroke-147"),sQuery(id+"FHMxAyK4CFUKdhS_1.wireOp",EDGE,"1cb9c079-ea9b-4899-8069-e0e3048e911d.sketch_text.stroke-148"),sQuery(id+"FHMxAyK4CFUKdhS_1.wireOp",EDGE,"1cb9c079-ea9b-4899-8069-e0e3048e911d.sketch_text.stroke-149"),sQuery(id+"FHMxAyK4CFUKdhS_1.wireOp",EDGE,"1cb9c079-ea9b-4899-8069-e0e3048e911d.sketch_text.stroke-150"),sQuery(id+"FHMxAyK4CFUKdhS_1.wireOp",EDGE,"1cb9c079-ea9b-4899-8069-e0e3048e911d.sketch_text.stroke-151"),sQuery(id+"FHMxAyK4CFUKdhS_1.wireOp",EDGE,"1cb9c079-ea9b-4899-8069-e0e3048e911d.sketch_text.stroke-152"),sQuery(id+"FHMxAyK4CFUKdhS_1.wireOp",EDGE,"1cb9c079-ea9b-4899-8069-e0e3048e911d.sketch_text.stroke-153"),sQuery(id+"FHMxAyK4CFUKdhS_1.wireOp",EDGE,"1cb9c079-ea9b-4899-8069-e0e3048e911d.sketch_text.stroke-159"),sQuery(id+"FHMxAyK4CFUKdhS_1.wireOp",EDGE,"1cb9c079-ea9b-4899-8069-e0e3048e911d.sketch_text.stroke-160"),sQuery(id+"FHMxAyK4CFUKdhS_1.wireOp",EDGE,"1cb9c079-ea9b-4899-8069-e0e3048e911d.sketch_text.stroke-161"),sQuery(id+"FHMxAyK4CFUKdhS_1.wireOp",EDGE,"1cb9c079-ea9b-4899-8069-e0e3048e911d.sketch_text.stroke-162"),sQuery(id+"FHMxAyK4CFUKdhS_1.wireOp",EDGE,"1cb9c079-ea9b-4899-8069-e0e3048e911d.sketch_text.stroke-163"),sQuery(id+"FHMxAyK4CFUKdhS_1.wireOp",EDGE,"1cb9c079-ea9b-4899-8069-e0e3048e911d.sketch_text.stroke-164"),sQuery(id+"FHMxAyK4CFUKdhS_1.wireOp",EDGE,"1cb9c079-ea9b-4899-8069-e0e3048e911d.sketch_text.stroke-165"),sQuery(id+"FHMxAyK4CFUKdhS_1.wireOp",EDGE,"1cb9c079-ea9b-4899-8069-e0e3048e911d.sketch_text.stroke-166"),sQuery(id+"FHMxAyK4CFUKdhS_1.wireOp",EDGE,"1cb9c079-ea9b-4899-8069-e0e3048e911d.sketch_text.stroke-167"),sQuery(id+"FHMxAyK4CFUKdhS_1.wireOp",EDGE,"1cb9c079-ea9b-4899-8069-e0e3048e911d.sketch_text.stroke-168"),sQuery(id+"FHMxAyK4CFUKdhS_1.wireOp",EDGE,"1cb9c079-ea9b-4899-8069-e0e3048e911d.sketch_text.stroke-169"),sQuery(id+"FHMxAyK4CFUKdhS_1.wireOp",EDGE,"1cb9c079-ea9b-4899-8069-e0e3048e911d.sketch_text.stroke-170"),sQuery(id+"FHMxAyK4CFUKdhS_1.wireOp",EDGE,"1cb9c079-ea9b-4899-8069-e0e3048e911d.sketch_text.stroke-171"),sQuery(id+"FHMxAyK4CFUKdhS_1.wireOp",EDGE,"1cb9c079-ea9b-4899-8069-e0e3048e911d.sketch_text.stroke-172"),sQuery(id+"FHMxAyK4CFUKdhS_1.wireOp",EDGE,"1cb9c079-ea9b-4899-8069-e0e3048e911d.sketch_text.stroke-173"),sQuery(id+"FHMxAyK4CFUKdhS_1.wireOp",EDGE,"1cb9c079-ea9b-4899-8069-e0e3048e911d.sketch_text.stroke-174"),sQuery(id+"FHMxAyK4CFUKdhS_1.wireOp",EDGE,"1cb9c079-ea9b-4899-8069-e0e3048e911d.sketch_text.stroke-175"),sQuery(id+"FHMxAyK4CFUKdhS_1.wireOp",EDGE,"1cb9c079-ea9b-4899-8069-e0e3048e911d.sketch_text.stroke-176"),sQuery(id+"FHMxAyK4CFUKdhS_1.wireOp",EDGE,"1cb9c079-ea9b-4899-8069-e0e3048e911d.sketch_text.stroke-177"),sQuery(id+"FHMxAyK4CFUKdhS_1.wireOp",EDGE,"1cb9c079-ea9b-4899-8069-e0e3048e911d.sketch_text.stroke-178"),sQuery(id+"FHMxAyK4CFUKdhS_1.wireOp",EDGE,"1cb9c079-ea9b-4899-8069-e0e3048e911d.sketch_text.stroke-179"),sQuery(id+"FHMxAyK4CFUKdhS_1.wireOp",EDGE,"1cb9c079-ea9b-4899-8069-e0e3048e911d.sketch_text.stroke-180"),sQuery(id+"F3.wireOp",EDGE,"727ac2c1-f511-4829-95a7-a443ef16a4cd"),subQ2])],"isStart":true}),makeQuery(id+"F4.opExtrude","SWEPT_FACE",FACE,{"disambiguationData":[OSD([subQ2])]})]),OD(0.0)],"derivedFrom":makeQuery(id+"F1.opExtrude","CAP_EDGE",EDGE,{"disambiguationData":[OSD([subQ0])],"isStart":false})});}
            var Q19;
            {var subQ0=sQuery(id+"F0.wireOp",EDGE,"E0.top");var subQ1=sQuery(id+"F0.wireOp",EDGE,"E0.bottom");var subQ2=sQuery(id+"F3.wireOp",EDGE,"1a034e28-a7c2-419d-97de-c33d70a47301");Q19=makeQuery(id+"F4.boolean.opBoolean","SPLIT",EDGE,{"disambiguationData":[TD([makeQuery(id+"F1.opExtrude","CAP_FACE",FACE,{"disambiguationData":[OSD([subQ1,subQ0,sQuery(id+"F0.wireOp",EDGE,"E0.left"),sQuery(id+"F0.wireOp",EDGE,"E0.right")])],"isStart":false}),makeQuery(id+"F1.opExtrude","SWEPT_FACE",FACE,{"disambiguationData":[OSD([subQ0])]}),makeQuery(id+"F4.opExtrude","CAP_FACE",FACE,{"disambiguationData":[OSD([subQ1,sQuery(id+"F2.wireOp",EDGE,"fcba4419-a2ee-464f-be9d-58f11bf3418b.sketch_text.stroke-0"),sQuery(id+"F2.wireOp",EDGE,"fcba4419-a2ee-464f-be9d-58f11bf3418b.sketch_text.stroke-1"),sQuery(id+"F2.wireOp",EDGE,"fcba4419-a2ee-464f-be9d-58f11bf3418b.sketch_text.stroke-2"),sQuery(id+"F2.wireOp",EDGE,"fcba4419-a2ee-464f-be9d-58f11bf3418b.sketch_text.stroke-3"),sQuery(id+"F2.wireOp",EDGE,"fcba4419-a2ee-464f-be9d-58f11bf3418b.sketch_text.stroke-4"),sQuery(id+"F2.wireOp",EDGE,"fcba4419-a2ee-464f-be9d-58f11bf3418b.sketch_text.stroke-5"),sQuery(id+"F2.wireOp",EDGE,"fcba4419-a2ee-464f-be9d-58f11bf3418b.sketch_text.stroke-6"),sQuery(id+"F2.wireOp",EDGE,"fcba4419-a2ee-464f-be9d-58f11bf3418b.sketch_text.stroke-7"),sQuery(id+"F2.wireOp",EDGE,"fcba4419-a2ee-464f-be9d-58f11bf3418b.sketch_text.stroke-8"),sQuery(id+"F2.wireOp",EDGE,"fcba4419-a2ee-464f-be9d-58f11bf3418b.sketch_text.stroke-9"),sQuery(id+"F2.wireOp",EDGE,"fcba4419-a2ee-464f-be9d-58f11bf3418b.sketch_text.stroke-10"),sQuery(id+"F2.wireOp",EDGE,"fcba4419-a2ee-464f-be9d-58f11bf3418b.sketch_text.stroke-11"),sQuery(id+"F2.wireOp",EDGE,"fcba4419-a2ee-464f-be9d-58f11bf3418b.sketch_text.stroke-12"),sQuery(id+"F2.wireOp",EDGE,"fcba4419-a2ee-464f-be9d-58f11bf3418b.sketch_text.stroke-13"),sQuery(id+"F2.wireOp",EDGE,"fcba4419-a2ee-464f-be9d-58f11bf3418b.sketch_text.stroke-14"),sQuery(id+"F2.wireOp",EDGE,"fcba4419-a2ee-464f-be9d-58f11bf3418b.sketch_text.stroke-15"),sQuery(id+"F2.wireOp",EDGE,"fcba4419-a2ee-464f-be9d-58f11bf3418b.sketch_text.stroke-16"),sQuery(id+"F2.wireOp",EDGE,"fcba4419-a2ee-464f-be9d-58f11bf3418b.sketch_text.stroke-17"),sQuery(id+"F2.wireOp",EDGE,"fcba4419-a2ee-464f-be9d-58f11bf3418b.sketch_text.stroke-18"),sQuery(id+"F2.wireOp",EDGE,"fcba4419-a2ee-464f-be9d-58f11bf3418b.sketch_text.stroke-19"),sQuery(id+"F2.wireOp",EDGE,"fcba4419-a2ee-464f-be9d-58f11bf3418b.sketch_text.stroke-20"),sQuery(id+"F2.wireOp",EDGE,"fcba4419-a2ee-464f-be9d-58f11bf3418b.sketch_text.stroke-21"),sQuery(id+"F2.wireOp",EDGE,"fcba4419-a2ee-464f-be9d-58f11bf3418b.sketch_text.stroke-22"),sQuery(id+"F2.wireOp",EDGE,"fcba4419-a2ee-464f-be9d-58f11bf3418b.sketch_text.stroke-23"),sQuery(id+"F2.wireOp",EDGE,"fcba4419-a2ee-464f-be9d-58f11bf3418b.sketch_text.stroke-24"),sQuery(id+"F2.wireOp",EDGE,"fcba4419-a2ee-464f-be9d-58f11bf3418b.sketch_text.stroke-25"),sQuery(id+"F2.wireOp",EDGE,"fcba4419-a2ee-464f-be9d-58f11bf3418b.sketch_text.stroke-26"),sQuery(id+"F2.wireOp",EDGE,"fcba4419-a2ee-464f-be9d-58f11bf3418b.sketch_text.stroke-27"),sQuery(id+"F2.wireOp",EDGE,"fcba4419-a2ee-464f-be9d-58f11bf3418b.sketch_text.stroke-28"),sQuery(id+"F2.wireOp",EDGE,"fcba4419-a2ee-464f-be9d-58f11bf3418b.sketch_text.stroke-29"),sQuery(id+"F2.wireOp",EDGE,"fcba4419-a2ee-464f-be9d-58f11bf3418b.sketch_text.stroke-30"),sQuery(id+"F2.wireOp",EDGE,"fcba4419-a2ee-464f-be9d-58f11bf3418b.sketch_text.stroke-31"),sQuery(id+"F2.wireOp",EDGE,"fcba4419-a2ee-464f-be9d-58f11bf3418b.sketch_text.stroke-32"),sQuery(id+"F2.wireOp",EDGE,"fcba4419-a2ee-464f-be9d-58f11bf3418b.sketch_text.stroke-33"),sQuery(id+"F2.wireOp",EDGE,"fcba4419-a2ee-464f-be9d-58f11bf3418b.sketch_text.stroke-34"),sQuery(id+"F2.wireOp",EDGE,"fcba4419-a2ee-464f-be9d-58f11bf3418b.sketch_text.stroke-35"),sQuery(id+"F2.wireOp",EDGE,"fcba4419-a2ee-464f-be9d-58f11bf3418b.sketch_text.stroke-36"),sQuery(id+"F2.wireOp",EDGE,"fcba4419-a2ee-464f-be9d-58f11bf3418b.sketch_text.stroke-37"),sQuery(id+"F2.wireOp",EDGE,"fcba4419-a2ee-464f-be9d-58f11bf3418b.sketch_text.stroke-38"),sQuery(id+"F2.wireOp",EDGE,"fcba4419-a2ee-464f-be9d-58f11bf3418b.sketch_text.stroke-39"),sQuery(id+"F2.wireOp",EDGE,"fcba4419-a2ee-464f-be9d-58f11bf3418b.sketch_text.stroke-40"),sQuery(id+"F2.wireOp",EDGE,"fcba4419-a2ee-464f-be9d-58f11bf3418b.sketch_text.stroke-41"),sQuery(id+"F2.wireOp",EDGE,"fcba4419-a2ee-464f-be9d-58f11bf3418b.sketch_text.stroke-42"),sQuery(id+"F2.wireOp",EDGE,"fcba4419-a2ee-464f-be9d-58f11bf3418b.sketch_text.stroke-43"),sQuery(id+"F2.wireOp",EDGE,"fcba4419-a2ee-464f-be9d-58f11bf3418b.sketch_text.stroke-44"),sQuery(id+"F2.wireOp",EDGE,"fcba4419-a2ee-464f-be9d-58f11bf3418b.sketch_text.stroke-45"),sQuery(id+"F2.wireOp",EDGE,"fcba4419-a2ee-464f-be9d-58f11bf3418b.sketch_text.stroke-46"),sQuery(id+"F2.wireOp",EDGE,"fcba4419-a2ee-464f-be9d-58f11bf3418b.sketch_text.stroke-47"),sQuery(id+"F2.wireOp",EDGE,"fcba4419-a2ee-464f-be9d-58f11bf3418b.sketch_text.stroke-48"),sQuery(id+"F2.wireOp",EDGE,"fcba4419-a2ee-464f-be9d-58f11bf3418b.sketch_text.stroke-49"),sQuery(id+"F2.wireOp",EDGE,"fcba4419-a2ee-464f-be9d-58f11bf3418b.sketch_text.stroke-50"),sQuery(id+"F2.wireOp",EDGE,"fcba4419-a2ee-464f-be9d-58f11bf3418b.sketch_text.stroke-51"),sQuery(id+"F2.wireOp",EDGE,"fcba4419-a2ee-464f-be9d-58f11bf3418b.sketch_text.stroke-52"),sQuery(id+"F2.wireOp",EDGE,"fcba4419-a2ee-464f-be9d-58f11bf3418b.sketch_text.stroke-53"),sQuery(id+"F2.wireOp",EDGE,"fcba4419-a2ee-464f-be9d-58f11bf3418b.sketch_text.stroke-54"),sQuery(id+"F2.wireOp",EDGE,"fcba4419-a2ee-464f-be9d-58f11bf3418b.sketch_text.stroke-55"),sQuery(id+"F2.wireOp",EDGE,"fcba4419-a2ee-464f-be9d-58f11bf3418b.sketch_text.stroke-56"),sQuery(id+"F2.wireOp",EDGE,"fcba4419-a2ee-464f-be9d-58f11bf3418b.sketch_text.stroke-57"),sQuery(id+"F2.wireOp",EDGE,"fcba4419-a2ee-464f-be9d-58f11bf3418b.sketch_text.stroke-58"),sQuery(id+"F2.wireOp",EDGE,"fcba4419-a2ee-464f-be9d-58f11bf3418b.sketch_text.stroke-59"),sQuery(id+"F2.wireOp",EDGE,"fcba4419-a2ee-464f-be9d-58f11bf3418b.sketch_text.stroke-60"),sQuery(id+"F2.wireOp",EDGE,"fcba4419-a2ee-464f-be9d-58f11bf3418b.sketch_text.stroke-61"),sQuery(id+"F2.wireOp",EDGE,"fcba4419-a2ee-464f-be9d-58f11bf3418b.sketch_text.stroke-62"),sQuery(id+"F2.wireOp",EDGE,"fcba4419-a2ee-464f-be9d-58f11bf3418b.sketch_text.stroke-63"),sQuery(id+"F2.wireOp",EDGE,"fcba4419-a2ee-464f-be9d-58f11bf3418b.sketch_text.stroke-64"),sQuery(id+"F2.wireOp",EDGE,"fcba4419-a2ee-464f-be9d-58f11bf3418b.sketch_text.stroke-65"),sQuery(id+"F2.wireOp",EDGE,"fcba4419-a2ee-464f-be9d-58f11bf3418b.sketch_text.stroke-66"),sQuery(id+"F2.wireOp",EDGE,"fcba4419-a2ee-464f-be9d-58f11bf3418b.sketch_text.stroke-67"),sQuery(id+"F2.wireOp",EDGE,"fcba4419-a2ee-464f-be9d-58f11bf3418b.sketch_text.stroke-68"),sQuery(id+"F2.wireOp",EDGE,"fcba4419-a2ee-464f-be9d-58f11bf3418b.sketch_text.stroke-69"),sQuery(id+"F2.wireOp",EDGE,"fcba4419-a2ee-464f-be9d-58f11bf3418b.sketch_text.stroke-70"),sQuery(id+"F2.wireOp",EDGE,"fcba4419-a2ee-464f-be9d-58f11bf3418b.sketch_text.stroke-71"),sQuery(id+"F2.wireOp",EDGE,"fcba4419-a2ee-464f-be9d-58f11bf3418b.sketch_text.stroke-72"),sQuery(id+"F2.wireOp",EDGE,"fcba4419-a2ee-464f-be9d-58f11bf3418b.sketch_text.stroke-73"),sQuery(id+"F2.wireOp",EDGE,"fcba4419-a2ee-464f-be9d-58f11bf3418b.sketch_text.stroke-74"),sQuery(id+"F2.wireOp",EDGE,"fcba4419-a2ee-464f-be9d-58f11bf3418b.sketch_text.stroke-75"),sQuery(id+"F2.wireOp",EDGE,"fcba4419-a2ee-464f-be9d-58f11bf3418b.sketch_text.stroke-76"),sQuery(id+"F2.wireOp",EDGE,"fcba4419-a2ee-464f-be9d-58f11bf3418b.sketch_text.stroke-77"),sQuery(id+"F2.wireOp",EDGE,"fcba4419-a2ee-464f-be9d-58f11bf3418b.sketch_text.stroke-78"),sQuery(id+"F2.wireOp",EDGE,"fcba4419-a2ee-464f-be9d-58f11bf3418b.sketch_text.stroke-79"),sQuery(id+"F2.wireOp",EDGE,"fcba4419-a2ee-464f-be9d-58f11bf3418b.sketch_text.stroke-80"),sQuery(id+"F2.wireOp",EDGE,"fcba4419-a2ee-464f-be9d-58f11bf3418b.sketch_text.stroke-81"),sQuery(id+"F2.wireOp",EDGE,"fcba4419-a2ee-464f-be9d-58f11bf3418b.sketch_text.stroke-82"),sQuery(id+"F2.wireOp",EDGE,"fcba4419-a2ee-464f-be9d-58f11bf3418b.sketch_text.stroke-83"),sQuery(id+"F2.wireOp",EDGE,"fcba4419-a2ee-464f-be9d-58f11bf3418b.sketch_text.stroke-84"),sQuery(id+"F2.wireOp",EDGE,"fcba4419-a2ee-464f-be9d-58f11bf3418b.sketch_text.stroke-85"),sQuery(id+"F2.wireOp",EDGE,"fcba4419-a2ee-464f-be9d-58f11bf3418b.sketch_text.stroke-86"),sQuery(id+"F2.wireOp",EDGE,"fcba4419-a2ee-464f-be9d-58f11bf3418b.sketch_text.stroke-87"),sQuery(id+"F2.wireOp",EDGE,"fcba4419-a2ee-464f-be9d-58f11bf3418b.sketch_text.stroke-88"),sQuery(id+"F2.wireOp",EDGE,"fcba4419-a2ee-464f-be9d-58f11bf3418b.sketch_text.stroke-89"),sQuery(id+"F2.wireOp",EDGE,"fcba4419-a2ee-464f-be9d-58f11bf3418b.sketch_text.stroke-90"),sQuery(id+"F2.wireOp",EDGE,"fcba4419-a2ee-464f-be9d-58f11bf3418b.sketch_text.stroke-91"),sQuery(id+"F2.wireOp",EDGE,"fcba4419-a2ee-464f-be9d-58f11bf3418b.sketch_text.stroke-92"),sQuery(id+"F2.wireOp",EDGE,"fcba4419-a2ee-464f-be9d-58f11bf3418b.sketch_text.stroke-93"),sQuery(id+"F2.wireOp",EDGE,"fcba4419-a2ee-464f-be9d-58f11bf3418b.sketch_text.stroke-94"),sQuery(id+"F2.wireOp",EDGE,"fcba4419-a2ee-464f-be9d-58f11bf3418b.sketch_text.stroke-95"),sQuery(id+"F2.wireOp",EDGE,"fcba4419-a2ee-464f-be9d-58f11bf3418b.sketch_text.stroke-96"),sQuery(id+"F2.wireOp",EDGE,"fcba4419-a2ee-464f-be9d-58f11bf3418b.sketch_text.stroke-97"),sQuery(id+"F2.wireOp",EDGE,"fcba4419-a2ee-464f-be9d-58f11bf3418b.sketch_text.stroke-98"),sQuery(id+"F2.wireOp",EDGE,"fcba4419-a2ee-464f-be9d-58f11bf3418b.sketch_text.stroke-99"),sQuery(id+"F2.wireOp",EDGE,"fcba4419-a2ee-464f-be9d-58f11bf3418b.sketch_text.stroke-100"),sQuery(id+"F2.wireOp",EDGE,"fcba4419-a2ee-464f-be9d-58f11bf3418b.sketch_text.stroke-101"),sQuery(id+"F2.wireOp",EDGE,"fcba4419-a2ee-464f-be9d-58f11bf3418b.sketch_text.stroke-102"),sQuery(id+"F2.wireOp",EDGE,"fcba4419-a2ee-464f-be9d-58f11bf3418b.sketch_text.stroke-103"),sQuery(id+"F2.wireOp",EDGE,"fcba4419-a2ee-464f-be9d-58f11bf3418b.sketch_text.stroke-104"),sQuery(id+"F2.wireOp",EDGE,"fcba4419-a2ee-464f-be9d-58f11bf3418b.sketch_text.stroke-105"),sQuery(id+"F2.wireOp",EDGE,"fcba4419-a2ee-464f-be9d-58f11bf3418b.sketch_text.stroke-106"),sQuery(id+"F2.wireOp",EDGE,"fcba4419-a2ee-464f-be9d-58f11bf3418b.sketch_text.stroke-107"),sQuery(id+"F2.wireOp",EDGE,"fcba4419-a2ee-464f-be9d-58f11bf3418b.sketch_text.stroke-108"),sQuery(id+"F2.wireOp",EDGE,"fcba4419-a2ee-464f-be9d-58f11bf3418b.sketch_text.stroke-109"),sQuery(id+"F2.wireOp",EDGE,"fcba4419-a2ee-464f-be9d-58f11bf3418b.sketch_text.stroke-110"),sQuery(id+"F2.wireOp",EDGE,"fcba4419-a2ee-464f-be9d-58f11bf3418b.sketch_text.stroke-111"),sQuery(id+"F2.wireOp",EDGE,"fcba4419-a2ee-464f-be9d-58f11bf3418b.sketch_text.stroke-112"),sQuery(id+"F2.wireOp",EDGE,"fcba4419-a2ee-464f-be9d-58f11bf3418b.sketch_text.stroke-113"),sQuery(id+"F2.wireOp",EDGE,"fcba4419-a2ee-464f-be9d-58f11bf3418b.sketch_text.stroke-114"),sQuery(id+"F2.wireOp",EDGE,"fcba4419-a2ee-464f-be9d-58f11bf3418b.sketch_text.stroke-115"),sQuery(id+"F2.wireOp",EDGE,"fcba4419-a2ee-464f-be9d-58f11bf3418b.sketch_text.stroke-116"),sQuery(id+"F2.wireOp",EDGE,"fcba4419-a2ee-464f-be9d-58f11bf3418b.sketch_text.stroke-117"),sQuery(id+"F2.wireOp",EDGE,"fcba4419-a2ee-464f-be9d-58f11bf3418b.sketch_text.stroke-118"),sQuery(id+"F2.wireOp",EDGE,"fcba4419-a2ee-464f-be9d-58f11bf3418b.sketch_text.stroke-119"),sQuery(id+"F2.wireOp",EDGE,"fcba4419-a2ee-464f-be9d-58f11bf3418b.sketch_text.stroke-120"),sQuery(id+"F2.wireOp",EDGE,"fcba4419-a2ee-464f-be9d-58f11bf3418b.sketch_text.stroke-121"),sQuery(id+"F2.wireOp",EDGE,"fcba4419-a2ee-464f-be9d-58f11bf3418b.sketch_text.stroke-122"),sQuery(id+"F2.wireOp",EDGE,"fcba4419-a2ee-464f-be9d-58f11bf3418b.sketch_text.stroke-123"),sQuery(id+"F2.wireOp",EDGE,"fcba4419-a2ee-464f-be9d-58f11bf3418b.sketch_text.stroke-124"),sQuery(id+"F2.wireOp",EDGE,"fcba4419-a2ee-464f-be9d-58f11bf3418b.sketch_text.stroke-125"),sQuery(id+"F2.wireOp",EDGE,"fcba4419-a2ee-464f-be9d-58f11bf3418b.sketch_text.stroke-126"),sQuery(id+"F2.wireOp",EDGE,"fcba4419-a2ee-464f-be9d-58f11bf3418b.sketch_text.stroke-127"),sQuery(id+"F2.wireOp",EDGE,"fcba4419-a2ee-464f-be9d-58f11bf3418b.sketch_text.stroke-128"),sQuery(id+"F2.wireOp",EDGE,"fcba4419-a2ee-464f-be9d-58f11bf3418b.sketch_text.stroke-129"),sQuery(id+"F2.wireOp",EDGE,"fcba4419-a2ee-464f-be9d-58f11bf3418b.sketch_text.stroke-130"),sQuery(id+"F2.wireOp",EDGE,"fcba4419-a2ee-464f-be9d-58f11bf3418b.sketch_text.stroke-131"),sQuery(id+"F2.wireOp",EDGE,"fcba4419-a2ee-464f-be9d-58f11bf3418b.sketch_text.stroke-132"),sQuery(id+"F2.wireOp",EDGE,"fcba4419-a2ee-464f-be9d-58f11bf3418b.sketch_text.stroke-133"),sQuery(id+"F2.wireOp",EDGE,"fcba4419-a2ee-464f-be9d-58f11bf3418b.sketch_text.stroke-134"),sQuery(id+"F2.wireOp",EDGE,"fcba4419-a2ee-464f-be9d-58f11bf3418b.sketch_text.stroke-135"),sQuery(id+"F2.wireOp",EDGE,"fcba4419-a2ee-464f-be9d-58f11bf3418b.sketch_text.stroke-136"),sQuery(id+"F2.wireOp",EDGE,"fcba4419-a2ee-464f-be9d-58f11bf3418b.sketch_text.stroke-137"),sQuery(id+"F2.wireOp",EDGE,"fcba4419-a2ee-464f-be9d-58f11bf3418b.sketch_text.stroke-138"),sQuery(id+"F2.wireOp",EDGE,"fcba4419-a2ee-464f-be9d-58f11bf3418b.sketch_text.stroke-139"),sQuery(id+"F2.wireOp",EDGE,"fcba4419-a2ee-464f-be9d-58f11bf3418b.sketch_text.stroke-140"),sQuery(id+"F2.wireOp",EDGE,"fcba4419-a2ee-464f-be9d-58f11bf3418b.sketch_text.stroke-141"),sQuery(id+"F2.wireOp",EDGE,"fcba4419-a2ee-464f-be9d-58f11bf3418b.sketch_text.stroke-142"),sQuery(id+"F2.wireOp",EDGE,"fcba4419-a2ee-464f-be9d-58f11bf3418b.sketch_text.stroke-143"),sQuery(id+"F2.wireOp",EDGE,"fcba4419-a2ee-464f-be9d-58f11bf3418b.sketch_text.stroke-144"),sQuery(id+"F2.wireOp",EDGE,"fcba4419-a2ee-464f-be9d-58f11bf3418b.sketch_text.stroke-145"),sQuery(id+"F2.wireOp",EDGE,"fcba4419-a2ee-464f-be9d-58f11bf3418b.sketch_text.stroke-146"),sQuery(id+"F2.wireOp",EDGE,"fcba4419-a2ee-464f-be9d-58f11bf3418b.sketch_text.stroke-147"),sQuery(id+"F2.wireOp",EDGE,"fcba4419-a2ee-464f-be9d-58f11bf3418b.sketch_text.stroke-148"),sQuery(id+"F2.wireOp",EDGE,"fcba4419-a2ee-464f-be9d-58f11bf3418b.sketch_text.stroke-149"),sQuery(id+"F2.wireOp",EDGE,"fcba4419-a2ee-464f-be9d-58f11bf3418b.sketch_text.stroke-150"),sQuery(id+"F2.wireOp",EDGE,"fcba4419-a2ee-464f-be9d-58f11bf3418b.sketch_text.stroke-151"),sQuery(id+"F2.wireOp",EDGE,"fcba4419-a2ee-464f-be9d-58f11bf3418b.sketch_text.stroke-152"),sQuery(id+"F2.wireOp",EDGE,"fcba4419-a2ee-464f-be9d-58f11bf3418b.sketch_text.stroke-153"),sQuery(id+"F2.wireOp",EDGE,"fcba4419-a2ee-464f-be9d-58f11bf3418b.sketch_text.stroke-154"),sQuery(id+"F2.wireOp",EDGE,"fcba4419-a2ee-464f-be9d-58f11bf3418b.sketch_text.stroke-155"),sQuery(id+"F2.wireOp",EDGE,"fcba4419-a2ee-464f-be9d-58f11bf3418b.sketch_text.stroke-156"),sQuery(id+"F2.wireOp",EDGE,"fcba4419-a2ee-464f-be9d-58f11bf3418b.sketch_text.stroke-157"),sQuery(id+"F2.wireOp",EDGE,"fcba4419-a2ee-464f-be9d-58f11bf3418b.sketch_text.stroke-158"),sQuery(id+"F2.wireOp",EDGE,"fcba4419-a2ee-464f-be9d-58f11bf3418b.sketch_text.stroke-159"),sQuery(id+"F2.wireOp",EDGE,"fcba4419-a2ee-464f-be9d-58f11bf3418b.sketch_text.stroke-160"),sQuery(id+"F2.wireOp",EDGE,"fcba4419-a2ee-464f-be9d-58f11bf3418b.sketch_text.stroke-161"),sQuery(id+"F2.wireOp",EDGE,"fcba4419-a2ee-464f-be9d-58f11bf3418b.sketch_text.stroke-162"),sQuery(id+"F2.wireOp",EDGE,"fcba4419-a2ee-464f-be9d-58f11bf3418b.sketch_text.stroke-163"),sQuery(id+"F2.wireOp",EDGE,"fcba4419-a2ee-464f-be9d-58f11bf3418b.sketch_text.stroke-164"),sQuery(id+"F2.wireOp",EDGE,"fcba4419-a2ee-464f-be9d-58f11bf3418b.sketch_text.stroke-165"),sQuery(id+"F2.wireOp",EDGE,"fcba4419-a2ee-464f-be9d-58f11bf3418b.sketch_text.stroke-166"),sQuery(id+"F2.wireOp",EDGE,"fcba4419-a2ee-464f-be9d-58f11bf3418b.sketch_text.stroke-167"),sQuery(id+"F2.wireOp",EDGE,"fcba4419-a2ee-464f-be9d-58f11bf3418b.sketch_text.stroke-168"),sQuery(id+"F2.wireOp",EDGE,"fcba4419-a2ee-464f-be9d-58f11bf3418b.sketch_text.stroke-169"),sQuery(id+"F2.wireOp",EDGE,"fcba4419-a2ee-464f-be9d-58f11bf3418b.sketch_text.stroke-170"),sQuery(id+"F2.wireOp",EDGE,"fcba4419-a2ee-464f-be9d-58f11bf3418b.sketch_text.stroke-171"),sQuery(id+"F2.wireOp",EDGE,"fcba4419-a2ee-464f-be9d-58f11bf3418b.sketch_text.stroke-172"),sQuery(id+"F2.wireOp",EDGE,"fcba4419-a2ee-464f-be9d-58f11bf3418b.sketch_text.stroke-173"),sQuery(id+"FHMxAyK4CFUKdhS_1.wireOp",EDGE,"1cb9c079-ea9b-4899-8069-e0e3048e911d.sketch_text.stroke-0"),sQuery(id+"FHMxAyK4CFUKdhS_1.wireOp",EDGE,"1cb9c079-ea9b-4899-8069-e0e3048e911d.sketch_text.stroke-1"),sQuery(id+"FHMxAyK4CFUKdhS_1.wireOp",EDGE,"1cb9c079-ea9b-4899-8069-e0e3048e911d.sketch_text.stroke-2"),sQuery(id+"FHMxAyK4CFUKdhS_1.wireOp",EDGE,"1cb9c079-ea9b-4899-8069-e0e3048e911d.sketch_text.stroke-3"),sQuery(id+"FHMxAyK4CFUKdhS_1.wireOp",EDGE,"1cb9c079-ea9b-4899-8069-e0e3048e911d.sketch_text.stroke-4"),sQuery(id+"FHMxAyK4CFUKdhS_1.wireOp",EDGE,"1cb9c079-ea9b-4899-8069-e0e3048e911d.sketch_text.stroke-5"),sQuery(id+"FHMxAyK4CFUKdhS_1.wireOp",EDGE,"1cb9c079-ea9b-4899-8069-e0e3048e911d.sketch_text.stroke-6"),sQuery(id+"FHMxAyK4CFUKdhS_1.wireOp",EDGE,"1cb9c079-ea9b-4899-8069-e0e3048e911d.sketch_text.stroke-7"),sQuery(id+"FHMxAyK4CFUKdhS_1.wireOp",EDGE,"1cb9c079-ea9b-4899-8069-e0e3048e911d.sketch_text.stroke-8"),sQuery(id+"FHMxAyK4CFUKdhS_1.wireOp",EDGE,"1cb9c079-ea9b-4899-8069-e0e3048e911d.sketch_text.stroke-9"),sQuery(id+"FHMxAyK4CFUKdhS_1.wireOp",EDGE,"1cb9c079-ea9b-4899-8069-e0e3048e911d.sketch_text.stroke-10"),sQuery(id+"FHMxAyK4CFUKdhS_1.wireOp",EDGE,"1cb9c079-ea9b-4899-8069-e0e3048e911d.sketch_text.stroke-11"),sQuery(id+"FHMxAyK4CFUKdhS_1.wireOp",EDGE,"1cb9c079-ea9b-4899-8069-e0e3048e911d.sketch_text.stroke-12"),sQuery(id+"FHMxAyK4CFUKdhS_1.wireOp",EDGE,"1cb9c079-ea9b-4899-8069-e0e3048e911d.sketch_text.stroke-13"),sQuery(id+"FHMxAyK4CFUKdhS_1.wireOp",EDGE,"1cb9c079-ea9b-4899-8069-e0e3048e911d.sketch_text.stroke-14"),sQuery(id+"FHMxAyK4CFUKdhS_1.wireOp",EDGE,"1cb9c079-ea9b-4899-8069-e0e3048e911d.sketch_text.stroke-15"),sQuery(id+"FHMxAyK4CFUKdhS_1.wireOp",EDGE,"1cb9c079-ea9b-4899-8069-e0e3048e911d.sketch_text.stroke-16"),sQuery(id+"FHMxAyK4CFUKdhS_1.wireOp",EDGE,"1cb9c079-ea9b-4899-8069-e0e3048e911d.sketch_text.stroke-17"),sQuery(id+"FHMxAyK4CFUKdhS_1.wireOp",EDGE,"1cb9c079-ea9b-4899-8069-e0e3048e911d.sketch_text.stroke-18"),sQuery(id+"FHMxAyK4CFUKdhS_1.wireOp",EDGE,"1cb9c079-ea9b-4899-8069-e0e3048e911d.sketch_text.stroke-19"),sQuery(id+"FHMxAyK4CFUKdhS_1.wireOp",EDGE,"1cb9c079-ea9b-4899-8069-e0e3048e911d.sketch_text.stroke-20"),sQuery(id+"FHMxAyK4CFUKdhS_1.wireOp",EDGE,"1cb9c079-ea9b-4899-8069-e0e3048e911d.sketch_text.stroke-21"),sQuery(id+"FHMxAyK4CFUKdhS_1.wireOp",EDGE,"1cb9c079-ea9b-4899-8069-e0e3048e911d.sketch_text.stroke-22"),sQuery(id+"FHMxAyK4CFUKdhS_1.wireOp",EDGE,"1cb9c079-ea9b-4899-8069-e0e3048e911d.sketch_text.stroke-23"),sQuery(id+"FHMxAyK4CFUKdhS_1.wireOp",EDGE,"1cb9c079-ea9b-4899-8069-e0e3048e911d.sketch_text.stroke-24"),sQuery(id+"FHMxAyK4CFUKdhS_1.wireOp",EDGE,"1cb9c079-ea9b-4899-8069-e0e3048e911d.sketch_text.stroke-25"),sQuery(id+"FHMxAyK4CFUKdhS_1.wireOp",EDGE,"1cb9c079-ea9b-4899-8069-e0e3048e911d.sketch_text.stroke-26"),sQuery(id+"FHMxAyK4CFUKdhS_1.wireOp",EDGE,"1cb9c079-ea9b-4899-8069-e0e3048e911d.sketch_text.stroke-27"),sQuery(id+"FHMxAyK4CFUKdhS_1.wireOp",EDGE,"1cb9c079-ea9b-4899-8069-e0e3048e911d.sketch_text.stroke-28"),sQuery(id+"FHMxAyK4CFUKdhS_1.wireOp",EDGE,"1cb9c079-ea9b-4899-8069-e0e3048e911d.sketch_text.stroke-29"),sQuery(id+"FHMxAyK4CFUKdhS_1.wireOp",EDGE,"1cb9c079-ea9b-4899-8069-e0e3048e911d.sketch_text.stroke-30"),sQuery(id+"FHMxAyK4CFUKdhS_1.wireOp",EDGE,"1cb9c079-ea9b-4899-8069-e0e3048e911d.sketch_text.stroke-31"),sQuery(id+"FHMxAyK4CFUKdhS_1.wireOp",EDGE,"1cb9c079-ea9b-4899-8069-e0e3048e911d.sketch_text.stroke-32"),sQuery(id+"FHMxAyK4CFUKdhS_1.wireOp",EDGE,"1cb9c079-ea9b-4899-8069-e0e3048e911d.sketch_text.stroke-33"),sQuery(id+"FHMxAyK4CFUKdhS_1.wireOp",EDGE,"1cb9c079-ea9b-4899-8069-e0e3048e911d.sketch_text.stroke-34"),sQuery(id+"FHMxAyK4CFUKdhS_1.wireOp",EDGE,"1cb9c079-ea9b-4899-8069-e0e3048e911d.sketch_text.stroke-35"),sQuery(id+"FHMxAyK4CFUKdhS_1.wireOp",EDGE,"1cb9c079-ea9b-4899-8069-e0e3048e911d.sketch_text.stroke-36"),sQuery(id+"FHMxAyK4CFUKdhS_1.wireOp",EDGE,"1cb9c079-ea9b-4899-8069-e0e3048e911d.sketch_text.stroke-37"),sQuery(id+"FHMxAyK4CFUKdhS_1.wireOp",EDGE,"1cb9c079-ea9b-4899-8069-e0e3048e911d.sketch_text.stroke-38"),sQuery(id+"FHMxAyK4CFUKdhS_1.wireOp",EDGE,"1cb9c079-ea9b-4899-8069-e0e3048e911d.sketch_text.stroke-39"),sQuery(id+"FHMxAyK4CFUKdhS_1.wireOp",EDGE,"1cb9c079-ea9b-4899-8069-e0e3048e911d.sketch_text.stroke-40"),sQuery(id+"FHMxAyK4CFUKdhS_1.wireOp",EDGE,"1cb9c079-ea9b-4899-8069-e0e3048e911d.sketch_text.stroke-41"),sQuery(id+"FHMxAyK4CFUKdhS_1.wireOp",EDGE,"1cb9c079-ea9b-4899-8069-e0e3048e911d.sketch_text.stroke-42"),sQuery(id+"FHMxAyK4CFUKdhS_1.wireOp",EDGE,"1cb9c079-ea9b-4899-8069-e0e3048e911d.sketch_text.stroke-43"),sQuery(id+"FHMxAyK4CFUKdhS_1.wireOp",EDGE,"1cb9c079-ea9b-4899-8069-e0e3048e911d.sketch_text.stroke-44"),sQuery(id+"FHMxAyK4CFUKdhS_1.wireOp",EDGE,"1cb9c079-ea9b-4899-8069-e0e3048e911d.sketch_text.stroke-45"),sQuery(id+"FHMxAyK4CFUKdhS_1.wireOp",EDGE,"1cb9c079-ea9b-4899-8069-e0e3048e911d.sketch_text.stroke-46"),sQuery(id+"FHMxAyK4CFUKdhS_1.wireOp",EDGE,"1cb9c079-ea9b-4899-8069-e0e3048e911d.sketch_text.stroke-47"),sQuery(id+"FHMxAyK4CFUKdhS_1.wireOp",EDGE,"1cb9c079-ea9b-4899-8069-e0e3048e911d.sketch_text.stroke-48"),sQuery(id+"FHMxAyK4CFUKdhS_1.wireOp",EDGE,"1cb9c079-ea9b-4899-8069-e0e3048e911d.sketch_text.stroke-49"),sQuery(id+"FHMxAyK4CFUKdhS_1.wireOp",EDGE,"1cb9c079-ea9b-4899-8069-e0e3048e911d.sketch_text.stroke-50"),sQuery(id+"FHMxAyK4CFUKdhS_1.wireOp",EDGE,"1cb9c079-ea9b-4899-8069-e0e3048e911d.sketch_text.stroke-51"),sQuery(id+"FHMxAyK4CFUKdhS_1.wireOp",EDGE,"1cb9c079-ea9b-4899-8069-e0e3048e911d.sketch_text.stroke-52"),sQuery(id+"FHMxAyK4CFUKdhS_1.wireOp",EDGE,"1cb9c079-ea9b-4899-8069-e0e3048e911d.sketch_text.stroke-53"),sQuery(id+"FHMxAyK4CFUKdhS_1.wireOp",EDGE,"1cb9c079-ea9b-4899-8069-e0e3048e911d.sketch_text.stroke-54"),sQuery(id+"FHMxAyK4CFUKdhS_1.wireOp",EDGE,"1cb9c079-ea9b-4899-8069-e0e3048e911d.sketch_text.stroke-55"),sQuery(id+"FHMxAyK4CFUKdhS_1.wireOp",EDGE,"1cb9c079-ea9b-4899-8069-e0e3048e911d.sketch_text.stroke-56"),sQuery(id+"FHMxAyK4CFUKdhS_1.wireOp",EDGE,"1cb9c079-ea9b-4899-8069-e0e3048e911d.sketch_text.stroke-57"),sQuery(id+"FHMxAyK4CFUKdhS_1.wireOp",EDGE,"1cb9c079-ea9b-4899-8069-e0e3048e911d.sketch_text.stroke-58"),sQuery(id+"FHMxAyK4CFUKdhS_1.wireOp",EDGE,"1cb9c079-ea9b-4899-8069-e0e3048e911d.sketch_text.stroke-59"),sQuery(id+"FHMxAyK4CFUKdhS_1.wireOp",EDGE,"1cb9c079-ea9b-4899-8069-e0e3048e911d.sketch_text.stroke-60"),sQuery(id+"FHMxAyK4CFUKdhS_1.wireOp",EDGE,"1cb9c079-ea9b-4899-8069-e0e3048e911d.sketch_text.stroke-61"),sQuery(id+"FHMxAyK4CFUKdhS_1.wireOp",EDGE,"1cb9c079-ea9b-4899-8069-e0e3048e911d.sketch_text.stroke-62"),sQuery(id+"FHMxAyK4CFUKdhS_1.wireOp",EDGE,"1cb9c079-ea9b-4899-8069-e0e3048e911d.sketch_text.stroke-71"),sQuery(id+"FHMxAyK4CFUKdhS_1.wireOp",EDGE,"1cb9c079-ea9b-4899-8069-e0e3048e911d.sketch_text.stroke-72"),sQuery(id+"FHMxAyK4CFUKdhS_1.wireOp",EDGE,"1cb9c079-ea9b-4899-8069-e0e3048e911d.sketch_text.stroke-73"),sQuery(id+"FHMxAyK4CFUKdhS_1.wireOp",EDGE,"1cb9c079-ea9b-4899-8069-e0e3048e911d.sketch_text.stroke-74"),sQuery(id+"FHMxAyK4CFUKdhS_1.wireOp",EDGE,"1cb9c079-ea9b-4899-8069-e0e3048e911d.sketch_text.stroke-75"),sQuery(id+"FHMxAyK4CFUKdhS_1.wireOp",EDGE,"1cb9c079-ea9b-4899-8069-e0e3048e911d.sketch_text.stroke-76"),sQuery(id+"FHMxAyK4CFUKdhS_1.wireOp",EDGE,"1cb9c079-ea9b-4899-8069-e0e3048e911d.sketch_text.stroke-77"),sQuery(id+"FHMxAyK4CFUKdhS_1.wireOp",EDGE,"1cb9c079-ea9b-4899-8069-e0e3048e911d.sketch_text.stroke-78"),sQuery(id+"FHMxAyK4CFUKdhS_1.wireOp",EDGE,"1cb9c079-ea9b-4899-8069-e0e3048e911d.sketch_text.stroke-79"),sQuery(id+"FHMxAyK4CFUKdhS_1.wireOp",EDGE,"1cb9c079-ea9b-4899-8069-e0e3048e911d.sketch_text.stroke-80"),sQuery(id+"FHMxAyK4CFUKdhS_1.wireOp",EDGE,"1cb9c079-ea9b-4899-8069-e0e3048e911d.sketch_text.stroke-81"),sQuery(id+"FHMxAyK4CFUKdhS_1.wireOp",EDGE,"1cb9c079-ea9b-4899-8069-e0e3048e911d.sketch_text.stroke-82"),sQuery(id+"FHMxAyK4CFUKdhS_1.wireOp",EDGE,"1cb9c079-ea9b-4899-8069-e0e3048e911d.sketch_text.stroke-83"),sQuery(id+"FHMxAyK4CFUKdhS_1.wireOp",EDGE,"1cb9c079-ea9b-4899-8069-e0e3048e911d.sketch_text.stroke-84"),sQuery(id+"FHMxAyK4CFUKdhS_1.wireOp",EDGE,"1cb9c079-ea9b-4899-8069-e0e3048e911d.sketch_text.stroke-85"),sQuery(id+"FHMxAyK4CFUKdhS_1.wireOp",EDGE,"1cb9c079-ea9b-4899-8069-e0e3048e911d.sketch_text.stroke-86"),sQuery(id+"FHMxAyK4CFUKdhS_1.wireOp",EDGE,"1cb9c079-ea9b-4899-8069-e0e3048e911d.sketch_text.stroke-87"),sQuery(id+"FHMxAyK4CFUKdhS_1.wireOp",EDGE,"1cb9c079-ea9b-4899-8069-e0e3048e911d.sketch_text.stroke-88"),sQuery(id+"FHMxAyK4CFUKdhS_1.wireOp",EDGE,"1cb9c079-ea9b-4899-8069-e0e3048e911d.sketch_text.stroke-89"),sQuery(id+"FHMxAyK4CFUKdhS_1.wireOp",EDGE,"1cb9c079-ea9b-4899-8069-e0e3048e911d.sketch_text.stroke-90"),sQuery(id+"FHMxAyK4CFUKdhS_1.wireOp",EDGE,"1cb9c079-ea9b-4899-8069-e0e3048e911d.sketch_text.stroke-91"),sQuery(id+"FHMxAyK4CFUKdhS_1.wireOp",EDGE,"1cb9c079-ea9b-4899-8069-e0e3048e911d.sketch_text.stroke-92"),sQuery(id+"FHMxAyK4CFUKdhS_1.wireOp",EDGE,"1cb9c079-ea9b-4899-8069-e0e3048e911d.sketch_text.stroke-93"),sQuery(id+"FHMxAyK4CFUKdhS_1.wireOp",EDGE,"1cb9c079-ea9b-4899-8069-e0e3048e911d.sketch_text.stroke-94"),sQuery(id+"FHMxAyK4CFUKdhS_1.wireOp",EDGE,"1cb9c079-ea9b-4899-8069-e0e3048e911d.sketch_text.stroke-95"),sQuery(id+"FHMxAyK4CFUKdhS_1.wireOp",EDGE,"1cb9c079-ea9b-4899-8069-e0e3048e911d.sketch_text.stroke-96"),sQuery(id+"FHMxAyK4CFUKdhS_1.wireOp",EDGE,"1cb9c079-ea9b-4899-8069-e0e3048e911d.sketch_text.stroke-97"),sQuery(id+"FHMxAyK4CFUKdhS_1.wireOp",EDGE,"1cb9c079-ea9b-4899-8069-e0e3048e911d.sketch_text.stroke-103"),sQuery(id+"FHMxAyK4CFUKdhS_1.wireOp",EDGE,"1cb9c079-ea9b-4899-8069-e0e3048e911d.sketch_text.stroke-104"),sQuery(id+"FHMxAyK4CFUKdhS_1.wireOp",EDGE,"1cb9c079-ea9b-4899-8069-e0e3048e911d.sketch_text.stroke-105"),sQuery(id+"FHMxAyK4CFUKdhS_1.wireOp",EDGE,"1cb9c079-ea9b-4899-8069-e0e3048e911d.sketch_text.stroke-106"),sQuery(id+"FHMxAyK4CFUKdhS_1.wireOp",EDGE,"1cb9c079-ea9b-4899-8069-e0e3048e911d.sketch_text.stroke-107"),sQuery(id+"FHMxAyK4CFUKdhS_1.wireOp",EDGE,"1cb9c079-ea9b-4899-8069-e0e3048e911d.sketch_text.stroke-108"),sQuery(id+"FHMxAyK4CFUKdhS_1.wireOp",EDGE,"1cb9c079-ea9b-4899-8069-e0e3048e911d.sketch_text.stroke-109"),sQuery(id+"FHMxAyK4CFUKdhS_1.wireOp",EDGE,"1cb9c079-ea9b-4899-8069-e0e3048e911d.sketch_text.stroke-110"),sQuery(id+"FHMxAyK4CFUKdhS_1.wireOp",EDGE,"1cb9c079-ea9b-4899-8069-e0e3048e911d.sketch_text.stroke-111"),sQuery(id+"FHMxAyK4CFUKdhS_1.wireOp",EDGE,"1cb9c079-ea9b-4899-8069-e0e3048e911d.sketch_text.stroke-112"),sQuery(id+"FHMxAyK4CFUKdhS_1.wireOp",EDGE,"1cb9c079-ea9b-4899-8069-e0e3048e911d.sketch_text.stroke-113"),sQuery(id+"FHMxAyK4CFUKdhS_1.wireOp",EDGE,"1cb9c079-ea9b-4899-8069-e0e3048e911d.sketch_text.stroke-114"),sQuery(id+"FHMxAyK4CFUKdhS_1.wireOp",EDGE,"1cb9c079-ea9b-4899-8069-e0e3048e911d.sketch_text.stroke-115"),sQuery(id+"FHMxAyK4CFUKdhS_1.wireOp",EDGE,"1cb9c079-ea9b-4899-8069-e0e3048e911d.sketch_text.stroke-116"),sQuery(id+"FHMxAyK4CFUKdhS_1.wireOp",EDGE,"1cb9c079-ea9b-4899-8069-e0e3048e911d.sketch_text.stroke-117"),sQuery(id+"FHMxAyK4CFUKdhS_1.wireOp",EDGE,"1cb9c079-ea9b-4899-8069-e0e3048e911d.sketch_text.stroke-118"),sQuery(id+"FHMxAyK4CFUKdhS_1.wireOp",EDGE,"1cb9c079-ea9b-4899-8069-e0e3048e911d.sketch_text.stroke-119"),sQuery(id+"FHMxAyK4CFUKdhS_1.wireOp",EDGE,"1cb9c079-ea9b-4899-8069-e0e3048e911d.sketch_text.stroke-120"),sQuery(id+"FHMxAyK4CFUKdhS_1.wireOp",EDGE,"1cb9c079-ea9b-4899-8069-e0e3048e911d.sketch_text.stroke-121"),sQuery(id+"FHMxAyK4CFUKdhS_1.wireOp",EDGE,"1cb9c079-ea9b-4899-8069-e0e3048e911d.sketch_text.stroke-122"),sQuery(id+"FHMxAyK4CFUKdhS_1.wireOp",EDGE,"1cb9c079-ea9b-4899-8069-e0e3048e911d.sketch_text.stroke-123"),sQuery(id+"FHMxAyK4CFUKdhS_1.wireOp",EDGE,"1cb9c079-ea9b-4899-8069-e0e3048e911d.sketch_text.stroke-124"),sQuery(id+"FHMxAyK4CFUKdhS_1.wireOp",EDGE,"1cb9c079-ea9b-4899-8069-e0e3048e911d.sketch_text.stroke-125"),sQuery(id+"FHMxAyK4CFUKdhS_1.wireOp",EDGE,"1cb9c079-ea9b-4899-8069-e0e3048e911d.sketch_text.stroke-126"),sQuery(id+"FHMxAyK4CFUKdhS_1.wireOp",EDGE,"1cb9c079-ea9b-4899-8069-e0e3048e911d.sketch_text.stroke-127"),sQuery(id+"FHMxAyK4CFUKdhS_1.wireOp",EDGE,"1cb9c079-ea9b-4899-8069-e0e3048e911d.sketch_text.stroke-128"),sQuery(id+"FHMxAyK4CFUKdhS_1.wireOp",EDGE,"1cb9c079-ea9b-4899-8069-e0e3048e911d.sketch_text.stroke-129"),sQuery(id+"FHMxAyK4CFUKdhS_1.wireOp",EDGE,"1cb9c079-ea9b-4899-8069-e0e3048e911d.sketch_text.stroke-130"),sQuery(id+"FHMxAyK4CFUKdhS_1.wireOp",EDGE,"1cb9c079-ea9b-4899-8069-e0e3048e911d.sketch_text.stroke-131"),sQuery(id+"FHMxAyK4CFUKdhS_1.wireOp",EDGE,"1cb9c079-ea9b-4899-8069-e0e3048e911d.sketch_text.stroke-132"),sQuery(id+"FHMxAyK4CFUKdhS_1.wireOp",EDGE,"1cb9c079-ea9b-4899-8069-e0e3048e911d.sketch_text.stroke-133"),sQuery(id+"FHMxAyK4CFUKdhS_1.wireOp",EDGE,"1cb9c079-ea9b-4899-8069-e0e3048e911d.sketch_text.stroke-134"),sQuery(id+"FHMxAyK4CFUKdhS_1.wireOp",EDGE,"1cb9c079-ea9b-4899-8069-e0e3048e911d.sketch_text.stroke-135"),sQuery(id+"FHMxAyK4CFUKdhS_1.wireOp",EDGE,"1cb9c079-ea9b-4899-8069-e0e3048e911d.sketch_text.stroke-136"),sQuery(id+"FHMxAyK4CFUKdhS_1.wireOp",EDGE,"1cb9c079-ea9b-4899-8069-e0e3048e911d.sketch_text.stroke-137"),sQuery(id+"FHMxAyK4CFUKdhS_1.wireOp",EDGE,"1cb9c079-ea9b-4899-8069-e0e3048e911d.sketch_text.stroke-138"),sQuery(id+"FHMxAyK4CFUKdhS_1.wireOp",EDGE,"1cb9c079-ea9b-4899-8069-e0e3048e911d.sketch_text.stroke-139"),sQuery(id+"FHMxAyK4CFUKdhS_1.wireOp",EDGE,"1cb9c079-ea9b-4899-8069-e0e3048e911d.sketch_text.stroke-140"),sQuery(id+"FHMxAyK4CFUKdhS_1.wireOp",EDGE,"1cb9c079-ea9b-4899-8069-e0e3048e911d.sketch_text.stroke-141"),sQuery(id+"FHMxAyK4CFUKdhS_1.wireOp",EDGE,"1cb9c079-ea9b-4899-8069-e0e3048e911d.sketch_text.stroke-142"),sQuery(id+"FHMxAyK4CFUKdhS_1.wireOp",EDGE,"1cb9c079-ea9b-4899-8069-e0e3048e911d.sketch_text.stroke-143"),sQuery(id+"FHMxAyK4CFUKdhS_1.wireOp",EDGE,"1cb9c079-ea9b-4899-8069-e0e3048e911d.sketch_text.stroke-144"),sQuery(id+"FHMxAyK4CFUKdhS_1.wireOp",EDGE,"1cb9c079-ea9b-4899-8069-e0e3048e911d.sketch_text.stroke-145"),sQuery(id+"FHMxAyK4CFUKdhS_1.wireOp",EDGE,"1cb9c079-ea9b-4899-8069-e0e3048e911d.sketch_text.stroke-146"),sQuery(id+"FHMxAyK4CFUKdhS_1.wireOp",EDGE,"1cb9c079-ea9b-4899-8069-e0e3048e911d.sketch_text.stroke-147"),sQuery(id+"FHMxAyK4CFUKdhS_1.wireOp",EDGE,"1cb9c079-ea9b-4899-8069-e0e3048e911d.sketch_text.stroke-148"),sQuery(id+"FHMxAyK4CFUKdhS_1.wireOp",EDGE,"1cb9c079-ea9b-4899-8069-e0e3048e911d.sketch_text.stroke-149"),sQuery(id+"FHMxAyK4CFUKdhS_1.wireOp",EDGE,"1cb9c079-ea9b-4899-8069-e0e3048e911d.sketch_text.stroke-150"),sQuery(id+"FHMxAyK4CFUKdhS_1.wireOp",EDGE,"1cb9c079-ea9b-4899-8069-e0e3048e911d.sketch_text.stroke-151"),sQuery(id+"FHMxAyK4CFUKdhS_1.wireOp",EDGE,"1cb9c079-ea9b-4899-8069-e0e3048e911d.sketch_text.stroke-152"),sQuery(id+"FHMxAyK4CFUKdhS_1.wireOp",EDGE,"1cb9c079-ea9b-4899-8069-e0e3048e911d.sketch_text.stroke-153"),sQuery(id+"FHMxAyK4CFUKdhS_1.wireOp",EDGE,"1cb9c079-ea9b-4899-8069-e0e3048e911d.sketch_text.stroke-159"),sQuery(id+"FHMxAyK4CFUKdhS_1.wireOp",EDGE,"1cb9c079-ea9b-4899-8069-e0e3048e911d.sketch_text.stroke-160"),sQuery(id+"FHMxAyK4CFUKdhS_1.wireOp",EDGE,"1cb9c079-ea9b-4899-8069-e0e3048e911d.sketch_text.stroke-161"),sQuery(id+"FHMxAyK4CFUKdhS_1.wireOp",EDGE,"1cb9c079-ea9b-4899-8069-e0e3048e911d.sketch_text.stroke-162"),sQuery(id+"FHMxAyK4CFUKdhS_1.wireOp",EDGE,"1cb9c079-ea9b-4899-8069-e0e3048e911d.sketch_text.stroke-163"),sQuery(id+"FHMxAyK4CFUKdhS_1.wireOp",EDGE,"1cb9c079-ea9b-4899-8069-e0e3048e911d.sketch_text.stroke-164"),sQuery(id+"FHMxAyK4CFUKdhS_1.wireOp",EDGE,"1cb9c079-ea9b-4899-8069-e0e3048e911d.sketch_text.stroke-165"),sQuery(id+"FHMxAyK4CFUKdhS_1.wireOp",EDGE,"1cb9c079-ea9b-4899-8069-e0e3048e911d.sketch_text.stroke-166"),sQuery(id+"FHMxAyK4CFUKdhS_1.wireOp",EDGE,"1cb9c079-ea9b-4899-8069-e0e3048e911d.sketch_text.stroke-167"),sQuery(id+"FHMxAyK4CFUKdhS_1.wireOp",EDGE,"1cb9c079-ea9b-4899-8069-e0e3048e911d.sketch_text.stroke-168"),sQuery(id+"FHMxAyK4CFUKdhS_1.wireOp",EDGE,"1cb9c079-ea9b-4899-8069-e0e3048e911d.sketch_text.stroke-169"),sQuery(id+"FHMxAyK4CFUKdhS_1.wireOp",EDGE,"1cb9c079-ea9b-4899-8069-e0e3048e911d.sketch_text.stroke-170"),sQuery(id+"FHMxAyK4CFUKdhS_1.wireOp",EDGE,"1cb9c079-ea9b-4899-8069-e0e3048e911d.sketch_text.stroke-171"),sQuery(id+"FHMxAyK4CFUKdhS_1.wireOp",EDGE,"1cb9c079-ea9b-4899-8069-e0e3048e911d.sketch_text.stroke-172"),sQuery(id+"FHMxAyK4CFUKdhS_1.wireOp",EDGE,"1cb9c079-ea9b-4899-8069-e0e3048e911d.sketch_text.stroke-173"),sQuery(id+"FHMxAyK4CFUKdhS_1.wireOp",EDGE,"1cb9c079-ea9b-4899-8069-e0e3048e911d.sketch_text.stroke-174"),sQuery(id+"FHMxAyK4CFUKdhS_1.wireOp",EDGE,"1cb9c079-ea9b-4899-8069-e0e3048e911d.sketch_text.stroke-175"),sQuery(id+"FHMxAyK4CFUKdhS_1.wireOp",EDGE,"1cb9c079-ea9b-4899-8069-e0e3048e911d.sketch_text.stroke-176"),sQuery(id+"FHMxAyK4CFUKdhS_1.wireOp",EDGE,"1cb9c079-ea9b-4899-8069-e0e3048e911d.sketch_text.stroke-177"),sQuery(id+"FHMxAyK4CFUKdhS_1.wireOp",EDGE,"1cb9c079-ea9b-4899-8069-e0e3048e911d.sketch_text.stroke-178"),sQuery(id+"FHMxAyK4CFUKdhS_1.wireOp",EDGE,"1cb9c079-ea9b-4899-8069-e0e3048e911d.sketch_text.stroke-179"),sQuery(id+"FHMxAyK4CFUKdhS_1.wireOp",EDGE,"1cb9c079-ea9b-4899-8069-e0e3048e911d.sketch_text.stroke-180"),sQuery(id+"F3.wireOp",EDGE,"727ac2c1-f511-4829-95a7-a443ef16a4cd"),subQ2])],"isStart":true}),makeQuery(id+"F4.opExtrude","SWEPT_FACE",FACE,{"disambiguationData":[OSD([subQ2])]})]),OD(1.0)],"derivedFrom":makeQuery(id+"F1.opExtrude","CAP_EDGE",EDGE,{"disambiguationData":[OSD([subQ0])],"isStart":false})});}
            var Q20;
            {var subQ0=sQuery(id+"F0.wireOp",EDGE,"E0.top");var subQ1=sQuery(id+"F0.wireOp",EDGE,"E0.bottom");var subQ2=sQuery(id+"F3.wireOp",EDGE,"E29");Q20=makeQuery(id+"F4.boolean.opBoolean","SPLIT",EDGE,{"disambiguationData":[TD([makeQuery(id+"F1.opExtrude","CAP_FACE",FACE,{"disambiguationData":[OSD([subQ1,subQ0,sQuery(id+"F0.wireOp",EDGE,"E0.left"),sQuery(id+"F0.wireOp",EDGE,"E0.right")])],"isStart":false}),makeQuery(id+"F1.opExtrude","SWEPT_FACE",FACE,{"disambiguationData":[OSD([subQ0])]}),makeQuery(id+"F4.opExtrude","SWEPT_FACE",FACE,{"disambiguationData":[OSD([subQ2])]}),makeQuery(id+"F4.opExtrude","CAP_FACE",FACE,{"disambiguationData":[OSD([subQ1,sQuery(id+"F2.wireOp",EDGE,"fcba4419-a2ee-464f-be9d-58f11bf3418b.sketch_text.stroke-0"),sQuery(id+"F2.wireOp",EDGE,"fcba4419-a2ee-464f-be9d-58f11bf3418b.sketch_text.stroke-1"),sQuery(id+"F2.wireOp",EDGE,"fcba4419-a2ee-464f-be9d-58f11bf3418b.sketch_text.stroke-2"),sQuery(id+"F2.wireOp",EDGE,"fcba4419-a2ee-464f-be9d-58f11bf3418b.sketch_text.stroke-3"),sQuery(id+"F2.wireOp",EDGE,"fcba4419-a2ee-464f-be9d-58f11bf3418b.sketch_text.stroke-4"),sQuery(id+"F2.wireOp",EDGE,"fcba4419-a2ee-464f-be9d-58f11bf3418b.sketch_text.stroke-5"),sQuery(id+"F2.wireOp",EDGE,"fcba4419-a2ee-464f-be9d-58f11bf3418b.sketch_text.stroke-6"),sQuery(id+"F2.wireOp",EDGE,"fcba4419-a2ee-464f-be9d-58f11bf3418b.sketch_text.stroke-7"),sQuery(id+"F2.wireOp",EDGE,"fcba4419-a2ee-464f-be9d-58f11bf3418b.sketch_text.stroke-8"),sQuery(id+"F2.wireOp",EDGE,"fcba4419-a2ee-464f-be9d-58f11bf3418b.sketch_text.stroke-9"),sQuery(id+"F2.wireOp",EDGE,"fcba4419-a2ee-464f-be9d-58f11bf3418b.sketch_text.stroke-10"),sQuery(id+"F2.wireOp",EDGE,"fcba4419-a2ee-464f-be9d-58f11bf3418b.sketch_text.stroke-11"),sQuery(id+"F2.wireOp",EDGE,"fcba4419-a2ee-464f-be9d-58f11bf3418b.sketch_text.stroke-12"),sQuery(id+"F2.wireOp",EDGE,"fcba4419-a2ee-464f-be9d-58f11bf3418b.sketch_text.stroke-13"),sQuery(id+"F2.wireOp",EDGE,"fcba4419-a2ee-464f-be9d-58f11bf3418b.sketch_text.stroke-14"),sQuery(id+"F2.wireOp",EDGE,"fcba4419-a2ee-464f-be9d-58f11bf3418b.sketch_text.stroke-15"),sQuery(id+"F2.wireOp",EDGE,"fcba4419-a2ee-464f-be9d-58f11bf3418b.sketch_text.stroke-16"),sQuery(id+"F2.wireOp",EDGE,"fcba4419-a2ee-464f-be9d-58f11bf3418b.sketch_text.stroke-17"),sQuery(id+"F2.wireOp",EDGE,"fcba4419-a2ee-464f-be9d-58f11bf3418b.sketch_text.stroke-18"),sQuery(id+"F2.wireOp",EDGE,"fcba4419-a2ee-464f-be9d-58f11bf3418b.sketch_text.stroke-19"),sQuery(id+"F2.wireOp",EDGE,"fcba4419-a2ee-464f-be9d-58f11bf3418b.sketch_text.stroke-20"),sQuery(id+"F2.wireOp",EDGE,"fcba4419-a2ee-464f-be9d-58f11bf3418b.sketch_text.stroke-21"),sQuery(id+"F2.wireOp",EDGE,"fcba4419-a2ee-464f-be9d-58f11bf3418b.sketch_text.stroke-22"),sQuery(id+"F2.wireOp",EDGE,"fcba4419-a2ee-464f-be9d-58f11bf3418b.sketch_text.stroke-23"),sQuery(id+"F2.wireOp",EDGE,"fcba4419-a2ee-464f-be9d-58f11bf3418b.sketch_text.stroke-24"),sQuery(id+"F2.wireOp",EDGE,"fcba4419-a2ee-464f-be9d-58f11bf3418b.sketch_text.stroke-25"),sQuery(id+"F2.wireOp",EDGE,"fcba4419-a2ee-464f-be9d-58f11bf3418b.sketch_text.stroke-26"),sQuery(id+"F2.wireOp",EDGE,"fcba4419-a2ee-464f-be9d-58f11bf3418b.sketch_text.stroke-27"),sQuery(id+"F2.wireOp",EDGE,"fcba4419-a2ee-464f-be9d-58f11bf3418b.sketch_text.stroke-28"),sQuery(id+"F2.wireOp",EDGE,"fcba4419-a2ee-464f-be9d-58f11bf3418b.sketch_text.stroke-29"),sQuery(id+"F2.wireOp",EDGE,"fcba4419-a2ee-464f-be9d-58f11bf3418b.sketch_text.stroke-30"),sQuery(id+"F2.wireOp",EDGE,"fcba4419-a2ee-464f-be9d-58f11bf3418b.sketch_text.stroke-31"),sQuery(id+"F2.wireOp",EDGE,"fcba4419-a2ee-464f-be9d-58f11bf3418b.sketch_text.stroke-32"),sQuery(id+"F2.wireOp",EDGE,"fcba4419-a2ee-464f-be9d-58f11bf3418b.sketch_text.stroke-33"),sQuery(id+"F2.wireOp",EDGE,"fcba4419-a2ee-464f-be9d-58f11bf3418b.sketch_text.stroke-34"),sQuery(id+"F2.wireOp",EDGE,"fcba4419-a2ee-464f-be9d-58f11bf3418b.sketch_text.stroke-35"),sQuery(id+"F2.wireOp",EDGE,"fcba4419-a2ee-464f-be9d-58f11bf3418b.sketch_text.stroke-36"),sQuery(id+"F2.wireOp",EDGE,"fcba4419-a2ee-464f-be9d-58f11bf3418b.sketch_text.stroke-37"),sQuery(id+"F2.wireOp",EDGE,"fcba4419-a2ee-464f-be9d-58f11bf3418b.sketch_text.stroke-38"),sQuery(id+"F2.wireOp",EDGE,"fcba4419-a2ee-464f-be9d-58f11bf3418b.sketch_text.stroke-39"),sQuery(id+"F2.wireOp",EDGE,"fcba4419-a2ee-464f-be9d-58f11bf3418b.sketch_text.stroke-40"),sQuery(id+"F2.wireOp",EDGE,"fcba4419-a2ee-464f-be9d-58f11bf3418b.sketch_text.stroke-41"),sQuery(id+"F2.wireOp",EDGE,"fcba4419-a2ee-464f-be9d-58f11bf3418b.sketch_text.stroke-42"),sQuery(id+"F2.wireOp",EDGE,"fcba4419-a2ee-464f-be9d-58f11bf3418b.sketch_text.stroke-43"),sQuery(id+"F2.wireOp",EDGE,"fcba4419-a2ee-464f-be9d-58f11bf3418b.sketch_text.stroke-44"),sQuery(id+"F2.wireOp",EDGE,"fcba4419-a2ee-464f-be9d-58f11bf3418b.sketch_text.stroke-45"),sQuery(id+"F2.wireOp",EDGE,"fcba4419-a2ee-464f-be9d-58f11bf3418b.sketch_text.stroke-46"),sQuery(id+"F2.wireOp",EDGE,"fcba4419-a2ee-464f-be9d-58f11bf3418b.sketch_text.stroke-47"),sQuery(id+"F2.wireOp",EDGE,"fcba4419-a2ee-464f-be9d-58f11bf3418b.sketch_text.stroke-48"),sQuery(id+"F2.wireOp",EDGE,"fcba4419-a2ee-464f-be9d-58f11bf3418b.sketch_text.stroke-49"),sQuery(id+"F2.wireOp",EDGE,"fcba4419-a2ee-464f-be9d-58f11bf3418b.sketch_text.stroke-50"),sQuery(id+"F2.wireOp",EDGE,"fcba4419-a2ee-464f-be9d-58f11bf3418b.sketch_text.stroke-51"),sQuery(id+"F2.wireOp",EDGE,"fcba4419-a2ee-464f-be9d-58f11bf3418b.sketch_text.stroke-52"),sQuery(id+"F2.wireOp",EDGE,"fcba4419-a2ee-464f-be9d-58f11bf3418b.sketch_text.stroke-53"),sQuery(id+"F2.wireOp",EDGE,"fcba4419-a2ee-464f-be9d-58f11bf3418b.sketch_text.stroke-54"),sQuery(id+"F2.wireOp",EDGE,"fcba4419-a2ee-464f-be9d-58f11bf3418b.sketch_text.stroke-55"),sQuery(id+"F2.wireOp",EDGE,"fcba4419-a2ee-464f-be9d-58f11bf3418b.sketch_text.stroke-56"),sQuery(id+"F2.wireOp",EDGE,"fcba4419-a2ee-464f-be9d-58f11bf3418b.sketch_text.stroke-57"),sQuery(id+"F2.wireOp",EDGE,"fcba4419-a2ee-464f-be9d-58f11bf3418b.sketch_text.stroke-58"),sQuery(id+"F2.wireOp",EDGE,"fcba4419-a2ee-464f-be9d-58f11bf3418b.sketch_text.stroke-59"),sQuery(id+"F2.wireOp",EDGE,"fcba4419-a2ee-464f-be9d-58f11bf3418b.sketch_text.stroke-60"),sQuery(id+"F2.wireOp",EDGE,"fcba4419-a2ee-464f-be9d-58f11bf3418b.sketch_text.stroke-61"),sQuery(id+"F2.wireOp",EDGE,"fcba4419-a2ee-464f-be9d-58f11bf3418b.sketch_text.stroke-62"),sQuery(id+"F2.wireOp",EDGE,"fcba4419-a2ee-464f-be9d-58f11bf3418b.sketch_text.stroke-63"),sQuery(id+"F2.wireOp",EDGE,"fcba4419-a2ee-464f-be9d-58f11bf3418b.sketch_text.stroke-64"),sQuery(id+"F2.wireOp",EDGE,"fcba4419-a2ee-464f-be9d-58f11bf3418b.sketch_text.stroke-65"),sQuery(id+"F2.wireOp",EDGE,"fcba4419-a2ee-464f-be9d-58f11bf3418b.sketch_text.stroke-66"),sQuery(id+"F2.wireOp",EDGE,"fcba4419-a2ee-464f-be9d-58f11bf3418b.sketch_text.stroke-67"),sQuery(id+"F2.wireOp",EDGE,"fcba4419-a2ee-464f-be9d-58f11bf3418b.sketch_text.stroke-68"),sQuery(id+"F2.wireOp",EDGE,"fcba4419-a2ee-464f-be9d-58f11bf3418b.sketch_text.stroke-69"),sQuery(id+"F2.wireOp",EDGE,"fcba4419-a2ee-464f-be9d-58f11bf3418b.sketch_text.stroke-70"),sQuery(id+"F2.wireOp",EDGE,"fcba4419-a2ee-464f-be9d-58f11bf3418b.sketch_text.stroke-71"),sQuery(id+"F2.wireOp",EDGE,"fcba4419-a2ee-464f-be9d-58f11bf3418b.sketch_text.stroke-72"),sQuery(id+"F2.wireOp",EDGE,"fcba4419-a2ee-464f-be9d-58f11bf3418b.sketch_text.stroke-73"),sQuery(id+"F2.wireOp",EDGE,"fcba4419-a2ee-464f-be9d-58f11bf3418b.sketch_text.stroke-74"),sQuery(id+"F2.wireOp",EDGE,"fcba4419-a2ee-464f-be9d-58f11bf3418b.sketch_text.stroke-75"),sQuery(id+"F2.wireOp",EDGE,"fcba4419-a2ee-464f-be9d-58f11bf3418b.sketch_text.stroke-76"),sQuery(id+"F2.wireOp",EDGE,"fcba4419-a2ee-464f-be9d-58f11bf3418b.sketch_text.stroke-77"),sQuery(id+"F2.wireOp",EDGE,"fcba4419-a2ee-464f-be9d-58f11bf3418b.sketch_text.stroke-78"),sQuery(id+"F2.wireOp",EDGE,"fcba4419-a2ee-464f-be9d-58f11bf3418b.sketch_text.stroke-79"),sQuery(id+"F2.wireOp",EDGE,"fcba4419-a2ee-464f-be9d-58f11bf3418b.sketch_text.stroke-80"),sQuery(id+"F2.wireOp",EDGE,"fcba4419-a2ee-464f-be9d-58f11bf3418b.sketch_text.stroke-81"),sQuery(id+"F2.wireOp",EDGE,"fcba4419-a2ee-464f-be9d-58f11bf3418b.sketch_text.stroke-82"),sQuery(id+"F2.wireOp",EDGE,"fcba4419-a2ee-464f-be9d-58f11bf3418b.sketch_text.stroke-83"),sQuery(id+"F2.wireOp",EDGE,"fcba4419-a2ee-464f-be9d-58f11bf3418b.sketch_text.stroke-84"),sQuery(id+"F2.wireOp",EDGE,"fcba4419-a2ee-464f-be9d-58f11bf3418b.sketch_text.stroke-85"),sQuery(id+"F2.wireOp",EDGE,"fcba4419-a2ee-464f-be9d-58f11bf3418b.sketch_text.stroke-86"),sQuery(id+"F2.wireOp",EDGE,"fcba4419-a2ee-464f-be9d-58f11bf3418b.sketch_text.stroke-87"),sQuery(id+"F2.wireOp",EDGE,"fcba4419-a2ee-464f-be9d-58f11bf3418b.sketch_text.stroke-88"),sQuery(id+"F2.wireOp",EDGE,"fcba4419-a2ee-464f-be9d-58f11bf3418b.sketch_text.stroke-89"),sQuery(id+"F2.wireOp",EDGE,"fcba4419-a2ee-464f-be9d-58f11bf3418b.sketch_text.stroke-90"),sQuery(id+"F2.wireOp",EDGE,"fcba4419-a2ee-464f-be9d-58f11bf3418b.sketch_text.stroke-91"),sQuery(id+"F2.wireOp",EDGE,"fcba4419-a2ee-464f-be9d-58f11bf3418b.sketch_text.stroke-92"),sQuery(id+"F2.wireOp",EDGE,"fcba4419-a2ee-464f-be9d-58f11bf3418b.sketch_text.stroke-93"),sQuery(id+"F2.wireOp",EDGE,"fcba4419-a2ee-464f-be9d-58f11bf3418b.sketch_text.stroke-94"),sQuery(id+"F2.wireOp",EDGE,"fcba4419-a2ee-464f-be9d-58f11bf3418b.sketch_text.stroke-95"),sQuery(id+"F2.wireOp",EDGE,"fcba4419-a2ee-464f-be9d-58f11bf3418b.sketch_text.stroke-96"),sQuery(id+"F2.wireOp",EDGE,"fcba4419-a2ee-464f-be9d-58f11bf3418b.sketch_text.stroke-97"),sQuery(id+"F2.wireOp",EDGE,"fcba4419-a2ee-464f-be9d-58f11bf3418b.sketch_text.stroke-98"),sQuery(id+"F2.wireOp",EDGE,"fcba4419-a2ee-464f-be9d-58f11bf3418b.sketch_text.stroke-99"),sQuery(id+"F2.wireOp",EDGE,"fcba4419-a2ee-464f-be9d-58f11bf3418b.sketch_text.stroke-100"),sQuery(id+"F2.wireOp",EDGE,"fcba4419-a2ee-464f-be9d-58f11bf3418b.sketch_text.stroke-101"),sQuery(id+"F2.wireOp",EDGE,"fcba4419-a2ee-464f-be9d-58f11bf3418b.sketch_text.stroke-102"),sQuery(id+"F2.wireOp",EDGE,"fcba4419-a2ee-464f-be9d-58f11bf3418b.sketch_text.stroke-103"),sQuery(id+"F2.wireOp",EDGE,"fcba4419-a2ee-464f-be9d-58f11bf3418b.sketch_text.stroke-104"),sQuery(id+"F2.wireOp",EDGE,"fcba4419-a2ee-464f-be9d-58f11bf3418b.sketch_text.stroke-105"),sQuery(id+"F2.wireOp",EDGE,"fcba4419-a2ee-464f-be9d-58f11bf3418b.sketch_text.stroke-106"),sQuery(id+"F2.wireOp",EDGE,"fcba4419-a2ee-464f-be9d-58f11bf3418b.sketch_text.stroke-107"),sQuery(id+"F2.wireOp",EDGE,"fcba4419-a2ee-464f-be9d-58f11bf3418b.sketch_text.stroke-108"),sQuery(id+"F2.wireOp",EDGE,"fcba4419-a2ee-464f-be9d-58f11bf3418b.sketch_text.stroke-109"),sQuery(id+"F2.wireOp",EDGE,"fcba4419-a2ee-464f-be9d-58f11bf3418b.sketch_text.stroke-110"),sQuery(id+"F2.wireOp",EDGE,"fcba4419-a2ee-464f-be9d-58f11bf3418b.sketch_text.stroke-111"),sQuery(id+"F2.wireOp",EDGE,"fcba4419-a2ee-464f-be9d-58f11bf3418b.sketch_text.stroke-112"),sQuery(id+"F2.wireOp",EDGE,"fcba4419-a2ee-464f-be9d-58f11bf3418b.sketch_text.stroke-113"),sQuery(id+"F2.wireOp",EDGE,"fcba4419-a2ee-464f-be9d-58f11bf3418b.sketch_text.stroke-114"),sQuery(id+"F2.wireOp",EDGE,"fcba4419-a2ee-464f-be9d-58f11bf3418b.sketch_text.stroke-115"),sQuery(id+"F2.wireOp",EDGE,"fcba4419-a2ee-464f-be9d-58f11bf3418b.sketch_text.stroke-116"),sQuery(id+"F2.wireOp",EDGE,"fcba4419-a2ee-464f-be9d-58f11bf3418b.sketch_text.stroke-117"),sQuery(id+"F2.wireOp",EDGE,"fcba4419-a2ee-464f-be9d-58f11bf3418b.sketch_text.stroke-118"),sQuery(id+"F2.wireOp",EDGE,"fcba4419-a2ee-464f-be9d-58f11bf3418b.sketch_text.stroke-119"),sQuery(id+"F2.wireOp",EDGE,"fcba4419-a2ee-464f-be9d-58f11bf3418b.sketch_text.stroke-120"),sQuery(id+"F2.wireOp",EDGE,"fcba4419-a2ee-464f-be9d-58f11bf3418b.sketch_text.stroke-121"),sQuery(id+"F2.wireOp",EDGE,"fcba4419-a2ee-464f-be9d-58f11bf3418b.sketch_text.stroke-122"),sQuery(id+"F2.wireOp",EDGE,"fcba4419-a2ee-464f-be9d-58f11bf3418b.sketch_text.stroke-123"),sQuery(id+"F2.wireOp",EDGE,"fcba4419-a2ee-464f-be9d-58f11bf3418b.sketch_text.stroke-124"),sQuery(id+"F2.wireOp",EDGE,"fcba4419-a2ee-464f-be9d-58f11bf3418b.sketch_text.stroke-125"),sQuery(id+"F2.wireOp",EDGE,"fcba4419-a2ee-464f-be9d-58f11bf3418b.sketch_text.stroke-126"),sQuery(id+"F2.wireOp",EDGE,"fcba4419-a2ee-464f-be9d-58f11bf3418b.sketch_text.stroke-127"),sQuery(id+"F2.wireOp",EDGE,"fcba4419-a2ee-464f-be9d-58f11bf3418b.sketch_text.stroke-128"),sQuery(id+"F2.wireOp",EDGE,"fcba4419-a2ee-464f-be9d-58f11bf3418b.sketch_text.stroke-129"),sQuery(id+"F2.wireOp",EDGE,"fcba4419-a2ee-464f-be9d-58f11bf3418b.sketch_text.stroke-130"),sQuery(id+"F2.wireOp",EDGE,"fcba4419-a2ee-464f-be9d-58f11bf3418b.sketch_text.stroke-131"),sQuery(id+"F2.wireOp",EDGE,"fcba4419-a2ee-464f-be9d-58f11bf3418b.sketch_text.stroke-132"),sQuery(id+"F2.wireOp",EDGE,"fcba4419-a2ee-464f-be9d-58f11bf3418b.sketch_text.stroke-133"),sQuery(id+"F2.wireOp",EDGE,"fcba4419-a2ee-464f-be9d-58f11bf3418b.sketch_text.stroke-134"),sQuery(id+"F2.wireOp",EDGE,"fcba4419-a2ee-464f-be9d-58f11bf3418b.sketch_text.stroke-135"),sQuery(id+"F2.wireOp",EDGE,"fcba4419-a2ee-464f-be9d-58f11bf3418b.sketch_text.stroke-136"),sQuery(id+"F2.wireOp",EDGE,"fcba4419-a2ee-464f-be9d-58f11bf3418b.sketch_text.stroke-137"),sQuery(id+"F2.wireOp",EDGE,"fcba4419-a2ee-464f-be9d-58f11bf3418b.sketch_text.stroke-138"),sQuery(id+"F2.wireOp",EDGE,"fcba4419-a2ee-464f-be9d-58f11bf3418b.sketch_text.stroke-139"),sQuery(id+"F2.wireOp",EDGE,"fcba4419-a2ee-464f-be9d-58f11bf3418b.sketch_text.stroke-140"),sQuery(id+"F2.wireOp",EDGE,"fcba4419-a2ee-464f-be9d-58f11bf3418b.sketch_text.stroke-141"),sQuery(id+"F2.wireOp",EDGE,"fcba4419-a2ee-464f-be9d-58f11bf3418b.sketch_text.stroke-142"),sQuery(id+"F2.wireOp",EDGE,"fcba4419-a2ee-464f-be9d-58f11bf3418b.sketch_text.stroke-143"),sQuery(id+"F2.wireOp",EDGE,"fcba4419-a2ee-464f-be9d-58f11bf3418b.sketch_text.stroke-144"),sQuery(id+"F2.wireOp",EDGE,"fcba4419-a2ee-464f-be9d-58f11bf3418b.sketch_text.stroke-145"),sQuery(id+"F2.wireOp",EDGE,"fcba4419-a2ee-464f-be9d-58f11bf3418b.sketch_text.stroke-146"),sQuery(id+"F2.wireOp",EDGE,"fcba4419-a2ee-464f-be9d-58f11bf3418b.sketch_text.stroke-147"),sQuery(id+"F2.wireOp",EDGE,"fcba4419-a2ee-464f-be9d-58f11bf3418b.sketch_text.stroke-148"),sQuery(id+"F2.wireOp",EDGE,"fcba4419-a2ee-464f-be9d-58f11bf3418b.sketch_text.stroke-149"),sQuery(id+"F2.wireOp",EDGE,"fcba4419-a2ee-464f-be9d-58f11bf3418b.sketch_text.stroke-150"),sQuery(id+"F2.wireOp",EDGE,"fcba4419-a2ee-464f-be9d-58f11bf3418b.sketch_text.stroke-151"),sQuery(id+"F2.wireOp",EDGE,"fcba4419-a2ee-464f-be9d-58f11bf3418b.sketch_text.stroke-152"),sQuery(id+"F2.wireOp",EDGE,"fcba4419-a2ee-464f-be9d-58f11bf3418b.sketch_text.stroke-153"),sQuery(id+"F2.wireOp",EDGE,"fcba4419-a2ee-464f-be9d-58f11bf3418b.sketch_text.stroke-154"),sQuery(id+"F2.wireOp",EDGE,"fcba4419-a2ee-464f-be9d-58f11bf3418b.sketch_text.stroke-155"),sQuery(id+"F2.wireOp",EDGE,"fcba4419-a2ee-464f-be9d-58f11bf3418b.sketch_text.stroke-156"),sQuery(id+"F2.wireOp",EDGE,"fcba4419-a2ee-464f-be9d-58f11bf3418b.sketch_text.stroke-157"),sQuery(id+"F2.wireOp",EDGE,"fcba4419-a2ee-464f-be9d-58f11bf3418b.sketch_text.stroke-158"),sQuery(id+"F2.wireOp",EDGE,"fcba4419-a2ee-464f-be9d-58f11bf3418b.sketch_text.stroke-159"),sQuery(id+"F2.wireOp",EDGE,"fcba4419-a2ee-464f-be9d-58f11bf3418b.sketch_text.stroke-160"),sQuery(id+"F2.wireOp",EDGE,"fcba4419-a2ee-464f-be9d-58f11bf3418b.sketch_text.stroke-161"),sQuery(id+"F2.wireOp",EDGE,"fcba4419-a2ee-464f-be9d-58f11bf3418b.sketch_text.stroke-162"),sQuery(id+"F2.wireOp",EDGE,"fcba4419-a2ee-464f-be9d-58f11bf3418b.sketch_text.stroke-163"),sQuery(id+"F2.wireOp",EDGE,"fcba4419-a2ee-464f-be9d-58f11bf3418b.sketch_text.stroke-164"),sQuery(id+"F2.wireOp",EDGE,"fcba4419-a2ee-464f-be9d-58f11bf3418b.sketch_text.stroke-165"),sQuery(id+"F2.wireOp",EDGE,"fcba4419-a2ee-464f-be9d-58f11bf3418b.sketch_text.stroke-166"),sQuery(id+"F2.wireOp",EDGE,"fcba4419-a2ee-464f-be9d-58f11bf3418b.sketch_text.stroke-167"),sQuery(id+"F2.wireOp",EDGE,"fcba4419-a2ee-464f-be9d-58f11bf3418b.sketch_text.stroke-168"),sQuery(id+"F2.wireOp",EDGE,"fcba4419-a2ee-464f-be9d-58f11bf3418b.sketch_text.stroke-169"),sQuery(id+"F2.wireOp",EDGE,"fcba4419-a2ee-464f-be9d-58f11bf3418b.sketch_text.stroke-170"),sQuery(id+"F2.wireOp",EDGE,"fcba4419-a2ee-464f-be9d-58f11bf3418b.sketch_text.stroke-171"),sQuery(id+"F2.wireOp",EDGE,"fcba4419-a2ee-464f-be9d-58f11bf3418b.sketch_text.stroke-172"),sQuery(id+"F2.wireOp",EDGE,"fcba4419-a2ee-464f-be9d-58f11bf3418b.sketch_text.stroke-173"),sQuery(id+"FHMxAyK4CFUKdhS_1.wireOp",EDGE,"1cb9c079-ea9b-4899-8069-e0e3048e911d.sketch_text.stroke-0"),sQuery(id+"FHMxAyK4CFUKdhS_1.wireOp",EDGE,"1cb9c079-ea9b-4899-8069-e0e3048e911d.sketch_text.stroke-1"),sQuery(id+"FHMxAyK4CFUKdhS_1.wireOp",EDGE,"1cb9c079-ea9b-4899-8069-e0e3048e911d.sketch_text.stroke-2"),sQuery(id+"FHMxAyK4CFUKdhS_1.wireOp",EDGE,"1cb9c079-ea9b-4899-8069-e0e3048e911d.sketch_text.stroke-3"),sQuery(id+"FHMxAyK4CFUKdhS_1.wireOp",EDGE,"1cb9c079-ea9b-4899-8069-e0e3048e911d.sketch_text.stroke-4"),sQuery(id+"FHMxAyK4CFUKdhS_1.wireOp",EDGE,"1cb9c079-ea9b-4899-8069-e0e3048e911d.sketch_text.stroke-5"),sQuery(id+"FHMxAyK4CFUKdhS_1.wireOp",EDGE,"1cb9c079-ea9b-4899-8069-e0e3048e911d.sketch_text.stroke-6"),sQuery(id+"FHMxAyK4CFUKdhS_1.wireOp",EDGE,"1cb9c079-ea9b-4899-8069-e0e3048e911d.sketch_text.stroke-7"),sQuery(id+"FHMxAyK4CFUKdhS_1.wireOp",EDGE,"1cb9c079-ea9b-4899-8069-e0e3048e911d.sketch_text.stroke-8"),sQuery(id+"FHMxAyK4CFUKdhS_1.wireOp",EDGE,"1cb9c079-ea9b-4899-8069-e0e3048e911d.sketch_text.stroke-9"),sQuery(id+"FHMxAyK4CFUKdhS_1.wireOp",EDGE,"1cb9c079-ea9b-4899-8069-e0e3048e911d.sketch_text.stroke-10"),sQuery(id+"FHMxAyK4CFUKdhS_1.wireOp",EDGE,"1cb9c079-ea9b-4899-8069-e0e3048e911d.sketch_text.stroke-11"),sQuery(id+"FHMxAyK4CFUKdhS_1.wireOp",EDGE,"1cb9c079-ea9b-4899-8069-e0e3048e911d.sketch_text.stroke-12"),sQuery(id+"FHMxAyK4CFUKdhS_1.wireOp",EDGE,"1cb9c079-ea9b-4899-8069-e0e3048e911d.sketch_text.stroke-13"),sQuery(id+"FHMxAyK4CFUKdhS_1.wireOp",EDGE,"1cb9c079-ea9b-4899-8069-e0e3048e911d.sketch_text.stroke-14"),sQuery(id+"FHMxAyK4CFUKdhS_1.wireOp",EDGE,"1cb9c079-ea9b-4899-8069-e0e3048e911d.sketch_text.stroke-15"),sQuery(id+"FHMxAyK4CFUKdhS_1.wireOp",EDGE,"1cb9c079-ea9b-4899-8069-e0e3048e911d.sketch_text.stroke-16"),sQuery(id+"FHMxAyK4CFUKdhS_1.wireOp",EDGE,"1cb9c079-ea9b-4899-8069-e0e3048e911d.sketch_text.stroke-17"),sQuery(id+"FHMxAyK4CFUKdhS_1.wireOp",EDGE,"1cb9c079-ea9b-4899-8069-e0e3048e911d.sketch_text.stroke-18"),sQuery(id+"FHMxAyK4CFUKdhS_1.wireOp",EDGE,"1cb9c079-ea9b-4899-8069-e0e3048e911d.sketch_text.stroke-19"),sQuery(id+"FHMxAyK4CFUKdhS_1.wireOp",EDGE,"1cb9c079-ea9b-4899-8069-e0e3048e911d.sketch_text.stroke-20"),sQuery(id+"FHMxAyK4CFUKdhS_1.wireOp",EDGE,"1cb9c079-ea9b-4899-8069-e0e3048e911d.sketch_text.stroke-21"),sQuery(id+"FHMxAyK4CFUKdhS_1.wireOp",EDGE,"1cb9c079-ea9b-4899-8069-e0e3048e911d.sketch_text.stroke-22"),sQuery(id+"FHMxAyK4CFUKdhS_1.wireOp",EDGE,"1cb9c079-ea9b-4899-8069-e0e3048e911d.sketch_text.stroke-23"),sQuery(id+"FHMxAyK4CFUKdhS_1.wireOp",EDGE,"1cb9c079-ea9b-4899-8069-e0e3048e911d.sketch_text.stroke-24"),sQuery(id+"FHMxAyK4CFUKdhS_1.wireOp",EDGE,"1cb9c079-ea9b-4899-8069-e0e3048e911d.sketch_text.stroke-25"),sQuery(id+"FHMxAyK4CFUKdhS_1.wireOp",EDGE,"1cb9c079-ea9b-4899-8069-e0e3048e911d.sketch_text.stroke-26"),sQuery(id+"FHMxAyK4CFUKdhS_1.wireOp",EDGE,"1cb9c079-ea9b-4899-8069-e0e3048e911d.sketch_text.stroke-27"),sQuery(id+"FHMxAyK4CFUKdhS_1.wireOp",EDGE,"1cb9c079-ea9b-4899-8069-e0e3048e911d.sketch_text.stroke-28"),sQuery(id+"FHMxAyK4CFUKdhS_1.wireOp",EDGE,"1cb9c079-ea9b-4899-8069-e0e3048e911d.sketch_text.stroke-29"),sQuery(id+"FHMxAyK4CFUKdhS_1.wireOp",EDGE,"1cb9c079-ea9b-4899-8069-e0e3048e911d.sketch_text.stroke-30"),sQuery(id+"FHMxAyK4CFUKdhS_1.wireOp",EDGE,"1cb9c079-ea9b-4899-8069-e0e3048e911d.sketch_text.stroke-31"),sQuery(id+"FHMxAyK4CFUKdhS_1.wireOp",EDGE,"1cb9c079-ea9b-4899-8069-e0e3048e911d.sketch_text.stroke-32"),sQuery(id+"FHMxAyK4CFUKdhS_1.wireOp",EDGE,"1cb9c079-ea9b-4899-8069-e0e3048e911d.sketch_text.stroke-33"),sQuery(id+"FHMxAyK4CFUKdhS_1.wireOp",EDGE,"1cb9c079-ea9b-4899-8069-e0e3048e911d.sketch_text.stroke-34"),sQuery(id+"FHMxAyK4CFUKdhS_1.wireOp",EDGE,"1cb9c079-ea9b-4899-8069-e0e3048e911d.sketch_text.stroke-35"),sQuery(id+"FHMxAyK4CFUKdhS_1.wireOp",EDGE,"1cb9c079-ea9b-4899-8069-e0e3048e911d.sketch_text.stroke-36"),sQuery(id+"FHMxAyK4CFUKdhS_1.wireOp",EDGE,"1cb9c079-ea9b-4899-8069-e0e3048e911d.sketch_text.stroke-37"),sQuery(id+"FHMxAyK4CFUKdhS_1.wireOp",EDGE,"1cb9c079-ea9b-4899-8069-e0e3048e911d.sketch_text.stroke-38"),sQuery(id+"FHMxAyK4CFUKdhS_1.wireOp",EDGE,"1cb9c079-ea9b-4899-8069-e0e3048e911d.sketch_text.stroke-39"),sQuery(id+"FHMxAyK4CFUKdhS_1.wireOp",EDGE,"1cb9c079-ea9b-4899-8069-e0e3048e911d.sketch_text.stroke-40"),sQuery(id+"FHMxAyK4CFUKdhS_1.wireOp",EDGE,"1cb9c079-ea9b-4899-8069-e0e3048e911d.sketch_text.stroke-41"),sQuery(id+"FHMxAyK4CFUKdhS_1.wireOp",EDGE,"1cb9c079-ea9b-4899-8069-e0e3048e911d.sketch_text.stroke-42"),sQuery(id+"FHMxAyK4CFUKdhS_1.wireOp",EDGE,"1cb9c079-ea9b-4899-8069-e0e3048e911d.sketch_text.stroke-43"),sQuery(id+"FHMxAyK4CFUKdhS_1.wireOp",EDGE,"1cb9c079-ea9b-4899-8069-e0e3048e911d.sketch_text.stroke-44"),sQuery(id+"FHMxAyK4CFUKdhS_1.wireOp",EDGE,"1cb9c079-ea9b-4899-8069-e0e3048e911d.sketch_text.stroke-45"),sQuery(id+"FHMxAyK4CFUKdhS_1.wireOp",EDGE,"1cb9c079-ea9b-4899-8069-e0e3048e911d.sketch_text.stroke-46"),sQuery(id+"FHMxAyK4CFUKdhS_1.wireOp",EDGE,"1cb9c079-ea9b-4899-8069-e0e3048e911d.sketch_text.stroke-47"),sQuery(id+"FHMxAyK4CFUKdhS_1.wireOp",EDGE,"1cb9c079-ea9b-4899-8069-e0e3048e911d.sketch_text.stroke-48"),sQuery(id+"FHMxAyK4CFUKdhS_1.wireOp",EDGE,"1cb9c079-ea9b-4899-8069-e0e3048e911d.sketch_text.stroke-49"),sQuery(id+"FHMxAyK4CFUKdhS_1.wireOp",EDGE,"1cb9c079-ea9b-4899-8069-e0e3048e911d.sketch_text.stroke-50"),sQuery(id+"FHMxAyK4CFUKdhS_1.wireOp",EDGE,"1cb9c079-ea9b-4899-8069-e0e3048e911d.sketch_text.stroke-51"),sQuery(id+"FHMxAyK4CFUKdhS_1.wireOp",EDGE,"1cb9c079-ea9b-4899-8069-e0e3048e911d.sketch_text.stroke-52"),sQuery(id+"FHMxAyK4CFUKdhS_1.wireOp",EDGE,"1cb9c079-ea9b-4899-8069-e0e3048e911d.sketch_text.stroke-53"),sQuery(id+"FHMxAyK4CFUKdhS_1.wireOp",EDGE,"1cb9c079-ea9b-4899-8069-e0e3048e911d.sketch_text.stroke-54"),sQuery(id+"FHMxAyK4CFUKdhS_1.wireOp",EDGE,"1cb9c079-ea9b-4899-8069-e0e3048e911d.sketch_text.stroke-55"),sQuery(id+"FHMxAyK4CFUKdhS_1.wireOp",EDGE,"1cb9c079-ea9b-4899-8069-e0e3048e911d.sketch_text.stroke-56"),sQuery(id+"FHMxAyK4CFUKdhS_1.wireOp",EDGE,"1cb9c079-ea9b-4899-8069-e0e3048e911d.sketch_text.stroke-57"),sQuery(id+"FHMxAyK4CFUKdhS_1.wireOp",EDGE,"1cb9c079-ea9b-4899-8069-e0e3048e911d.sketch_text.stroke-58"),sQuery(id+"FHMxAyK4CFUKdhS_1.wireOp",EDGE,"1cb9c079-ea9b-4899-8069-e0e3048e911d.sketch_text.stroke-59"),sQuery(id+"FHMxAyK4CFUKdhS_1.wireOp",EDGE,"1cb9c079-ea9b-4899-8069-e0e3048e911d.sketch_text.stroke-60"),sQuery(id+"FHMxAyK4CFUKdhS_1.wireOp",EDGE,"1cb9c079-ea9b-4899-8069-e0e3048e911d.sketch_text.stroke-61"),sQuery(id+"FHMxAyK4CFUKdhS_1.wireOp",EDGE,"1cb9c079-ea9b-4899-8069-e0e3048e911d.sketch_text.stroke-62"),sQuery(id+"FHMxAyK4CFUKdhS_1.wireOp",EDGE,"1cb9c079-ea9b-4899-8069-e0e3048e911d.sketch_text.stroke-71"),sQuery(id+"FHMxAyK4CFUKdhS_1.wireOp",EDGE,"1cb9c079-ea9b-4899-8069-e0e3048e911d.sketch_text.stroke-72"),sQuery(id+"FHMxAyK4CFUKdhS_1.wireOp",EDGE,"1cb9c079-ea9b-4899-8069-e0e3048e911d.sketch_text.stroke-73"),sQuery(id+"FHMxAyK4CFUKdhS_1.wireOp",EDGE,"1cb9c079-ea9b-4899-8069-e0e3048e911d.sketch_text.stroke-74"),sQuery(id+"FHMxAyK4CFUKdhS_1.wireOp",EDGE,"1cb9c079-ea9b-4899-8069-e0e3048e911d.sketch_text.stroke-75"),sQuery(id+"FHMxAyK4CFUKdhS_1.wireOp",EDGE,"1cb9c079-ea9b-4899-8069-e0e3048e911d.sketch_text.stroke-76"),sQuery(id+"FHMxAyK4CFUKdhS_1.wireOp",EDGE,"1cb9c079-ea9b-4899-8069-e0e3048e911d.sketch_text.stroke-77"),sQuery(id+"FHMxAyK4CFUKdhS_1.wireOp",EDGE,"1cb9c079-ea9b-4899-8069-e0e3048e911d.sketch_text.stroke-78"),sQuery(id+"FHMxAyK4CFUKdhS_1.wireOp",EDGE,"1cb9c079-ea9b-4899-8069-e0e3048e911d.sketch_text.stroke-79"),sQuery(id+"FHMxAyK4CFUKdhS_1.wireOp",EDGE,"1cb9c079-ea9b-4899-8069-e0e3048e911d.sketch_text.stroke-80"),sQuery(id+"FHMxAyK4CFUKdhS_1.wireOp",EDGE,"1cb9c079-ea9b-4899-8069-e0e3048e911d.sketch_text.stroke-81"),sQuery(id+"FHMxAyK4CFUKdhS_1.wireOp",EDGE,"1cb9c079-ea9b-4899-8069-e0e3048e911d.sketch_text.stroke-82"),sQuery(id+"FHMxAyK4CFUKdhS_1.wireOp",EDGE,"1cb9c079-ea9b-4899-8069-e0e3048e911d.sketch_text.stroke-83"),sQuery(id+"FHMxAyK4CFUKdhS_1.wireOp",EDGE,"1cb9c079-ea9b-4899-8069-e0e3048e911d.sketch_text.stroke-84"),sQuery(id+"FHMxAyK4CFUKdhS_1.wireOp",EDGE,"1cb9c079-ea9b-4899-8069-e0e3048e911d.sketch_text.stroke-85"),sQuery(id+"FHMxAyK4CFUKdhS_1.wireOp",EDGE,"1cb9c079-ea9b-4899-8069-e0e3048e911d.sketch_text.stroke-86"),sQuery(id+"FHMxAyK4CFUKdhS_1.wireOp",EDGE,"1cb9c079-ea9b-4899-8069-e0e3048e911d.sketch_text.stroke-87"),sQuery(id+"FHMxAyK4CFUKdhS_1.wireOp",EDGE,"1cb9c079-ea9b-4899-8069-e0e3048e911d.sketch_text.stroke-88"),sQuery(id+"FHMxAyK4CFUKdhS_1.wireOp",EDGE,"1cb9c079-ea9b-4899-8069-e0e3048e911d.sketch_text.stroke-89"),sQuery(id+"FHMxAyK4CFUKdhS_1.wireOp",EDGE,"1cb9c079-ea9b-4899-8069-e0e3048e911d.sketch_text.stroke-90"),sQuery(id+"FHMxAyK4CFUKdhS_1.wireOp",EDGE,"1cb9c079-ea9b-4899-8069-e0e3048e911d.sketch_text.stroke-91"),sQuery(id+"FHMxAyK4CFUKdhS_1.wireOp",EDGE,"1cb9c079-ea9b-4899-8069-e0e3048e911d.sketch_text.stroke-92"),sQuery(id+"FHMxAyK4CFUKdhS_1.wireOp",EDGE,"1cb9c079-ea9b-4899-8069-e0e3048e911d.sketch_text.stroke-93"),sQuery(id+"FHMxAyK4CFUKdhS_1.wireOp",EDGE,"1cb9c079-ea9b-4899-8069-e0e3048e911d.sketch_text.stroke-94"),sQuery(id+"FHMxAyK4CFUKdhS_1.wireOp",EDGE,"1cb9c079-ea9b-4899-8069-e0e3048e911d.sketch_text.stroke-95"),sQuery(id+"FHMxAyK4CFUKdhS_1.wireOp",EDGE,"1cb9c079-ea9b-4899-8069-e0e3048e911d.sketch_text.stroke-96"),sQuery(id+"FHMxAyK4CFUKdhS_1.wireOp",EDGE,"1cb9c079-ea9b-4899-8069-e0e3048e911d.sketch_text.stroke-97"),sQuery(id+"FHMxAyK4CFUKdhS_1.wireOp",EDGE,"1cb9c079-ea9b-4899-8069-e0e3048e911d.sketch_text.stroke-103"),sQuery(id+"FHMxAyK4CFUKdhS_1.wireOp",EDGE,"1cb9c079-ea9b-4899-8069-e0e3048e911d.sketch_text.stroke-104"),sQuery(id+"FHMxAyK4CFUKdhS_1.wireOp",EDGE,"1cb9c079-ea9b-4899-8069-e0e3048e911d.sketch_text.stroke-105"),sQuery(id+"FHMxAyK4CFUKdhS_1.wireOp",EDGE,"1cb9c079-ea9b-4899-8069-e0e3048e911d.sketch_text.stroke-106"),sQuery(id+"FHMxAyK4CFUKdhS_1.wireOp",EDGE,"1cb9c079-ea9b-4899-8069-e0e3048e911d.sketch_text.stroke-107"),sQuery(id+"FHMxAyK4CFUKdhS_1.wireOp",EDGE,"1cb9c079-ea9b-4899-8069-e0e3048e911d.sketch_text.stroke-108"),sQuery(id+"FHMxAyK4CFUKdhS_1.wireOp",EDGE,"1cb9c079-ea9b-4899-8069-e0e3048e911d.sketch_text.stroke-109"),sQuery(id+"FHMxAyK4CFUKdhS_1.wireOp",EDGE,"1cb9c079-ea9b-4899-8069-e0e3048e911d.sketch_text.stroke-110"),sQuery(id+"FHMxAyK4CFUKdhS_1.wireOp",EDGE,"1cb9c079-ea9b-4899-8069-e0e3048e911d.sketch_text.stroke-111"),sQuery(id+"FHMxAyK4CFUKdhS_1.wireOp",EDGE,"1cb9c079-ea9b-4899-8069-e0e3048e911d.sketch_text.stroke-112"),sQuery(id+"FHMxAyK4CFUKdhS_1.wireOp",EDGE,"1cb9c079-ea9b-4899-8069-e0e3048e911d.sketch_text.stroke-113"),sQuery(id+"FHMxAyK4CFUKdhS_1.wireOp",EDGE,"1cb9c079-ea9b-4899-8069-e0e3048e911d.sketch_text.stroke-114"),sQuery(id+"FHMxAyK4CFUKdhS_1.wireOp",EDGE,"1cb9c079-ea9b-4899-8069-e0e3048e911d.sketch_text.stroke-115"),sQuery(id+"FHMxAyK4CFUKdhS_1.wireOp",EDGE,"1cb9c079-ea9b-4899-8069-e0e3048e911d.sketch_text.stroke-116"),sQuery(id+"FHMxAyK4CFUKdhS_1.wireOp",EDGE,"1cb9c079-ea9b-4899-8069-e0e3048e911d.sketch_text.stroke-117"),sQuery(id+"FHMxAyK4CFUKdhS_1.wireOp",EDGE,"1cb9c079-ea9b-4899-8069-e0e3048e911d.sketch_text.stroke-118"),sQuery(id+"FHMxAyK4CFUKdhS_1.wireOp",EDGE,"1cb9c079-ea9b-4899-8069-e0e3048e911d.sketch_text.stroke-119"),sQuery(id+"FHMxAyK4CFUKdhS_1.wireOp",EDGE,"1cb9c079-ea9b-4899-8069-e0e3048e911d.sketch_text.stroke-120"),sQuery(id+"FHMxAyK4CFUKdhS_1.wireOp",EDGE,"1cb9c079-ea9b-4899-8069-e0e3048e911d.sketch_text.stroke-121"),sQuery(id+"FHMxAyK4CFUKdhS_1.wireOp",EDGE,"1cb9c079-ea9b-4899-8069-e0e3048e911d.sketch_text.stroke-122"),sQuery(id+"FHMxAyK4CFUKdhS_1.wireOp",EDGE,"1cb9c079-ea9b-4899-8069-e0e3048e911d.sketch_text.stroke-123"),sQuery(id+"FHMxAyK4CFUKdhS_1.wireOp",EDGE,"1cb9c079-ea9b-4899-8069-e0e3048e911d.sketch_text.stroke-124"),sQuery(id+"FHMxAyK4CFUKdhS_1.wireOp",EDGE,"1cb9c079-ea9b-4899-8069-e0e3048e911d.sketch_text.stroke-125"),sQuery(id+"FHMxAyK4CFUKdhS_1.wireOp",EDGE,"1cb9c079-ea9b-4899-8069-e0e3048e911d.sketch_text.stroke-126"),sQuery(id+"FHMxAyK4CFUKdhS_1.wireOp",EDGE,"1cb9c079-ea9b-4899-8069-e0e3048e911d.sketch_text.stroke-127"),sQuery(id+"FHMxAyK4CFUKdhS_1.wireOp",EDGE,"1cb9c079-ea9b-4899-8069-e0e3048e911d.sketch_text.stroke-128"),sQuery(id+"FHMxAyK4CFUKdhS_1.wireOp",EDGE,"1cb9c079-ea9b-4899-8069-e0e3048e911d.sketch_text.stroke-129"),sQuery(id+"FHMxAyK4CFUKdhS_1.wireOp",EDGE,"1cb9c079-ea9b-4899-8069-e0e3048e911d.sketch_text.stroke-130"),sQuery(id+"FHMxAyK4CFUKdhS_1.wireOp",EDGE,"1cb9c079-ea9b-4899-8069-e0e3048e911d.sketch_text.stroke-131"),sQuery(id+"FHMxAyK4CFUKdhS_1.wireOp",EDGE,"1cb9c079-ea9b-4899-8069-e0e3048e911d.sketch_text.stroke-132"),sQuery(id+"FHMxAyK4CFUKdhS_1.wireOp",EDGE,"1cb9c079-ea9b-4899-8069-e0e3048e911d.sketch_text.stroke-133"),sQuery(id+"FHMxAyK4CFUKdhS_1.wireOp",EDGE,"1cb9c079-ea9b-4899-8069-e0e3048e911d.sketch_text.stroke-134"),sQuery(id+"FHMxAyK4CFUKdhS_1.wireOp",EDGE,"1cb9c079-ea9b-4899-8069-e0e3048e911d.sketch_text.stroke-135"),sQuery(id+"FHMxAyK4CFUKdhS_1.wireOp",EDGE,"1cb9c079-ea9b-4899-8069-e0e3048e911d.sketch_text.stroke-136"),sQuery(id+"FHMxAyK4CFUKdhS_1.wireOp",EDGE,"1cb9c079-ea9b-4899-8069-e0e3048e911d.sketch_text.stroke-137"),sQuery(id+"FHMxAyK4CFUKdhS_1.wireOp",EDGE,"1cb9c079-ea9b-4899-8069-e0e3048e911d.sketch_text.stroke-138"),sQuery(id+"FHMxAyK4CFUKdhS_1.wireOp",EDGE,"1cb9c079-ea9b-4899-8069-e0e3048e911d.sketch_text.stroke-139"),sQuery(id+"FHMxAyK4CFUKdhS_1.wireOp",EDGE,"1cb9c079-ea9b-4899-8069-e0e3048e911d.sketch_text.stroke-140"),sQuery(id+"FHMxAyK4CFUKdhS_1.wireOp",EDGE,"1cb9c079-ea9b-4899-8069-e0e3048e911d.sketch_text.stroke-141"),sQuery(id+"FHMxAyK4CFUKdhS_1.wireOp",EDGE,"1cb9c079-ea9b-4899-8069-e0e3048e911d.sketch_text.stroke-142"),sQuery(id+"FHMxAyK4CFUKdhS_1.wireOp",EDGE,"1cb9c079-ea9b-4899-8069-e0e3048e911d.sketch_text.stroke-143"),sQuery(id+"FHMxAyK4CFUKdhS_1.wireOp",EDGE,"1cb9c079-ea9b-4899-8069-e0e3048e911d.sketch_text.stroke-144"),sQuery(id+"FHMxAyK4CFUKdhS_1.wireOp",EDGE,"1cb9c079-ea9b-4899-8069-e0e3048e911d.sketch_text.stroke-145"),sQuery(id+"FHMxAyK4CFUKdhS_1.wireOp",EDGE,"1cb9c079-ea9b-4899-8069-e0e3048e911d.sketch_text.stroke-146"),sQuery(id+"FHMxAyK4CFUKdhS_1.wireOp",EDGE,"1cb9c079-ea9b-4899-8069-e0e3048e911d.sketch_text.stroke-147"),sQuery(id+"FHMxAyK4CFUKdhS_1.wireOp",EDGE,"1cb9c079-ea9b-4899-8069-e0e3048e911d.sketch_text.stroke-148"),sQuery(id+"FHMxAyK4CFUKdhS_1.wireOp",EDGE,"1cb9c079-ea9b-4899-8069-e0e3048e911d.sketch_text.stroke-149"),sQuery(id+"FHMxAyK4CFUKdhS_1.wireOp",EDGE,"1cb9c079-ea9b-4899-8069-e0e3048e911d.sketch_text.stroke-150"),sQuery(id+"FHMxAyK4CFUKdhS_1.wireOp",EDGE,"1cb9c079-ea9b-4899-8069-e0e3048e911d.sketch_text.stroke-151"),sQuery(id+"FHMxAyK4CFUKdhS_1.wireOp",EDGE,"1cb9c079-ea9b-4899-8069-e0e3048e911d.sketch_text.stroke-152"),sQuery(id+"FHMxAyK4CFUKdhS_1.wireOp",EDGE,"1cb9c079-ea9b-4899-8069-e0e3048e911d.sketch_text.stroke-153"),sQuery(id+"FHMxAyK4CFUKdhS_1.wireOp",EDGE,"1cb9c079-ea9b-4899-8069-e0e3048e911d.sketch_text.stroke-159"),sQuery(id+"FHMxAyK4CFUKdhS_1.wireOp",EDGE,"1cb9c079-ea9b-4899-8069-e0e3048e911d.sketch_text.stroke-160"),sQuery(id+"FHMxAyK4CFUKdhS_1.wireOp",EDGE,"1cb9c079-ea9b-4899-8069-e0e3048e911d.sketch_text.stroke-161"),sQuery(id+"FHMxAyK4CFUKdhS_1.wireOp",EDGE,"1cb9c079-ea9b-4899-8069-e0e3048e911d.sketch_text.stroke-162"),sQuery(id+"FHMxAyK4CFUKdhS_1.wireOp",EDGE,"1cb9c079-ea9b-4899-8069-e0e3048e911d.sketch_text.stroke-163"),sQuery(id+"FHMxAyK4CFUKdhS_1.wireOp",EDGE,"1cb9c079-ea9b-4899-8069-e0e3048e911d.sketch_text.stroke-164"),sQuery(id+"FHMxAyK4CFUKdhS_1.wireOp",EDGE,"1cb9c079-ea9b-4899-8069-e0e3048e911d.sketch_text.stroke-165"),sQuery(id+"FHMxAyK4CFUKdhS_1.wireOp",EDGE,"1cb9c079-ea9b-4899-8069-e0e3048e911d.sketch_text.stroke-166"),sQuery(id+"FHMxAyK4CFUKdhS_1.wireOp",EDGE,"1cb9c079-ea9b-4899-8069-e0e3048e911d.sketch_text.stroke-167"),sQuery(id+"FHMxAyK4CFUKdhS_1.wireOp",EDGE,"1cb9c079-ea9b-4899-8069-e0e3048e911d.sketch_text.stroke-168"),sQuery(id+"FHMxAyK4CFUKdhS_1.wireOp",EDGE,"1cb9c079-ea9b-4899-8069-e0e3048e911d.sketch_text.stroke-169"),sQuery(id+"FHMxAyK4CFUKdhS_1.wireOp",EDGE,"1cb9c079-ea9b-4899-8069-e0e3048e911d.sketch_text.stroke-170"),sQuery(id+"FHMxAyK4CFUKdhS_1.wireOp",EDGE,"1cb9c079-ea9b-4899-8069-e0e3048e911d.sketch_text.stroke-171"),sQuery(id+"FHMxAyK4CFUKdhS_1.wireOp",EDGE,"1cb9c079-ea9b-4899-8069-e0e3048e911d.sketch_text.stroke-172"),sQuery(id+"FHMxAyK4CFUKdhS_1.wireOp",EDGE,"1cb9c079-ea9b-4899-8069-e0e3048e911d.sketch_text.stroke-173"),sQuery(id+"FHMxAyK4CFUKdhS_1.wireOp",EDGE,"1cb9c079-ea9b-4899-8069-e0e3048e911d.sketch_text.stroke-174"),sQuery(id+"FHMxAyK4CFUKdhS_1.wireOp",EDGE,"1cb9c079-ea9b-4899-8069-e0e3048e911d.sketch_text.stroke-175"),sQuery(id+"FHMxAyK4CFUKdhS_1.wireOp",EDGE,"1cb9c079-ea9b-4899-8069-e0e3048e911d.sketch_text.stroke-176"),sQuery(id+"FHMxAyK4CFUKdhS_1.wireOp",EDGE,"1cb9c079-ea9b-4899-8069-e0e3048e911d.sketch_text.stroke-177"),sQuery(id+"FHMxAyK4CFUKdhS_1.wireOp",EDGE,"1cb9c079-ea9b-4899-8069-e0e3048e911d.sketch_text.stroke-178"),sQuery(id+"FHMxAyK4CFUKdhS_1.wireOp",EDGE,"1cb9c079-ea9b-4899-8069-e0e3048e911d.sketch_text.stroke-179"),sQuery(id+"FHMxAyK4CFUKdhS_1.wireOp",EDGE,"1cb9c079-ea9b-4899-8069-e0e3048e911d.sketch_text.stroke-180"),subQ2,sQuery(id+"F3.wireOp",EDGE,"E30")])],"isStart":true})])],"derivedFrom":makeQuery(id+"F4.opExtrude","CAP_EDGE",EDGE,{"disambiguationData":[OSD([subQ2])],"isStart":true})});}
            var Q21;
            {var subQ0=sQuery(id+"F3.wireOp",EDGE,"E29");var subQ1=sQuery(id+"F0.wireOp",EDGE,"E0.top");var subQ2=sQuery(id+"F3.wireOp",EDGE,"E30");var subQ3=sQuery(id+"F0.wireOp",EDGE,"E0.bottom");Q21=makeQuery(id+"F4.boolean.opBoolean","SPLIT",EDGE,{"disambiguationData":[TD([makeQuery(id+"F1.opExtrude","CAP_FACE",FACE,{"disambiguationData":[OSD([subQ3,subQ1,sQuery(id+"F0.wireOp",EDGE,"E0.left"),sQuery(id+"F0.wireOp",EDGE,"E0.right")])],"isStart":false}),makeQuery(id+"F1.opExtrude","SWEPT_FACE",FACE,{"disambiguationData":[OSD([subQ1])]}),makeQuery(id+"F4.opExtrude","SWEPT_FACE",FACE,{"disambiguationData":[OSD([subQ0])]}),makeQuery(id+"F4.opExtrude","CAP_FACE",FACE,{"disambiguationData":[OSD([subQ3,sQuery(id+"F2.wireOp",EDGE,"fcba4419-a2ee-464f-be9d-58f11bf3418b.sketch_text.stroke-0"),sQuery(id+"F2.wireOp",EDGE,"fcba4419-a2ee-464f-be9d-58f11bf3418b.sketch_text.stroke-1"),sQuery(id+"F2.wireOp",EDGE,"fcba4419-a2ee-464f-be9d-58f11bf3418b.sketch_text.stroke-2"),sQuery(id+"F2.wireOp",EDGE,"fcba4419-a2ee-464f-be9d-58f11bf3418b.sketch_text.stroke-3"),sQuery(id+"F2.wireOp",EDGE,"fcba4419-a2ee-464f-be9d-58f11bf3418b.sketch_text.stroke-4"),sQuery(id+"F2.wireOp",EDGE,"fcba4419-a2ee-464f-be9d-58f11bf3418b.sketch_text.stroke-5"),sQuery(id+"F2.wireOp",EDGE,"fcba4419-a2ee-464f-be9d-58f11bf3418b.sketch_text.stroke-6"),sQuery(id+"F2.wireOp",EDGE,"fcba4419-a2ee-464f-be9d-58f11bf3418b.sketch_text.stroke-7"),sQuery(id+"F2.wireOp",EDGE,"fcba4419-a2ee-464f-be9d-58f11bf3418b.sketch_text.stroke-8"),sQuery(id+"F2.wireOp",EDGE,"fcba4419-a2ee-464f-be9d-58f11bf3418b.sketch_text.stroke-9"),sQuery(id+"F2.wireOp",EDGE,"fcba4419-a2ee-464f-be9d-58f11bf3418b.sketch_text.stroke-10"),sQuery(id+"F2.wireOp",EDGE,"fcba4419-a2ee-464f-be9d-58f11bf3418b.sketch_text.stroke-11"),sQuery(id+"F2.wireOp",EDGE,"fcba4419-a2ee-464f-be9d-58f11bf3418b.sketch_text.stroke-12"),sQuery(id+"F2.wireOp",EDGE,"fcba4419-a2ee-464f-be9d-58f11bf3418b.sketch_text.stroke-13"),sQuery(id+"F2.wireOp",EDGE,"fcba4419-a2ee-464f-be9d-58f11bf3418b.sketch_text.stroke-14"),sQuery(id+"F2.wireOp",EDGE,"fcba4419-a2ee-464f-be9d-58f11bf3418b.sketch_text.stroke-15"),sQuery(id+"F2.wireOp",EDGE,"fcba4419-a2ee-464f-be9d-58f11bf3418b.sketch_text.stroke-16"),sQuery(id+"F2.wireOp",EDGE,"fcba4419-a2ee-464f-be9d-58f11bf3418b.sketch_text.stroke-17"),sQuery(id+"F2.wireOp",EDGE,"fcba4419-a2ee-464f-be9d-58f11bf3418b.sketch_text.stroke-18"),sQuery(id+"F2.wireOp",EDGE,"fcba4419-a2ee-464f-be9d-58f11bf3418b.sketch_text.stroke-19"),sQuery(id+"F2.wireOp",EDGE,"fcba4419-a2ee-464f-be9d-58f11bf3418b.sketch_text.stroke-20"),sQuery(id+"F2.wireOp",EDGE,"fcba4419-a2ee-464f-be9d-58f11bf3418b.sketch_text.stroke-21"),sQuery(id+"F2.wireOp",EDGE,"fcba4419-a2ee-464f-be9d-58f11bf3418b.sketch_text.stroke-22"),sQuery(id+"F2.wireOp",EDGE,"fcba4419-a2ee-464f-be9d-58f11bf3418b.sketch_text.stroke-23"),sQuery(id+"F2.wireOp",EDGE,"fcba4419-a2ee-464f-be9d-58f11bf3418b.sketch_text.stroke-24"),sQuery(id+"F2.wireOp",EDGE,"fcba4419-a2ee-464f-be9d-58f11bf3418b.sketch_text.stroke-25"),sQuery(id+"F2.wireOp",EDGE,"fcba4419-a2ee-464f-be9d-58f11bf3418b.sketch_text.stroke-26"),sQuery(id+"F2.wireOp",EDGE,"fcba4419-a2ee-464f-be9d-58f11bf3418b.sketch_text.stroke-27"),sQuery(id+"F2.wireOp",EDGE,"fcba4419-a2ee-464f-be9d-58f11bf3418b.sketch_text.stroke-28"),sQuery(id+"F2.wireOp",EDGE,"fcba4419-a2ee-464f-be9d-58f11bf3418b.sketch_text.stroke-29"),sQuery(id+"F2.wireOp",EDGE,"fcba4419-a2ee-464f-be9d-58f11bf3418b.sketch_text.stroke-30"),sQuery(id+"F2.wireOp",EDGE,"fcba4419-a2ee-464f-be9d-58f11bf3418b.sketch_text.stroke-31"),sQuery(id+"F2.wireOp",EDGE,"fcba4419-a2ee-464f-be9d-58f11bf3418b.sketch_text.stroke-32"),sQuery(id+"F2.wireOp",EDGE,"fcba4419-a2ee-464f-be9d-58f11bf3418b.sketch_text.stroke-33"),sQuery(id+"F2.wireOp",EDGE,"fcba4419-a2ee-464f-be9d-58f11bf3418b.sketch_text.stroke-34"),sQuery(id+"F2.wireOp",EDGE,"fcba4419-a2ee-464f-be9d-58f11bf3418b.sketch_text.stroke-35"),sQuery(id+"F2.wireOp",EDGE,"fcba4419-a2ee-464f-be9d-58f11bf3418b.sketch_text.stroke-36"),sQuery(id+"F2.wireOp",EDGE,"fcba4419-a2ee-464f-be9d-58f11bf3418b.sketch_text.stroke-37"),sQuery(id+"F2.wireOp",EDGE,"fcba4419-a2ee-464f-be9d-58f11bf3418b.sketch_text.stroke-38"),sQuery(id+"F2.wireOp",EDGE,"fcba4419-a2ee-464f-be9d-58f11bf3418b.sketch_text.stroke-39"),sQuery(id+"F2.wireOp",EDGE,"fcba4419-a2ee-464f-be9d-58f11bf3418b.sketch_text.stroke-40"),sQuery(id+"F2.wireOp",EDGE,"fcba4419-a2ee-464f-be9d-58f11bf3418b.sketch_text.stroke-41"),sQuery(id+"F2.wireOp",EDGE,"fcba4419-a2ee-464f-be9d-58f11bf3418b.sketch_text.stroke-42"),sQuery(id+"F2.wireOp",EDGE,"fcba4419-a2ee-464f-be9d-58f11bf3418b.sketch_text.stroke-43"),sQuery(id+"F2.wireOp",EDGE,"fcba4419-a2ee-464f-be9d-58f11bf3418b.sketch_text.stroke-44"),sQuery(id+"F2.wireOp",EDGE,"fcba4419-a2ee-464f-be9d-58f11bf3418b.sketch_text.stroke-45"),sQuery(id+"F2.wireOp",EDGE,"fcba4419-a2ee-464f-be9d-58f11bf3418b.sketch_text.stroke-46"),sQuery(id+"F2.wireOp",EDGE,"fcba4419-a2ee-464f-be9d-58f11bf3418b.sketch_text.stroke-47"),sQuery(id+"F2.wireOp",EDGE,"fcba4419-a2ee-464f-be9d-58f11bf3418b.sketch_text.stroke-48"),sQuery(id+"F2.wireOp",EDGE,"fcba4419-a2ee-464f-be9d-58f11bf3418b.sketch_text.stroke-49"),sQuery(id+"F2.wireOp",EDGE,"fcba4419-a2ee-464f-be9d-58f11bf3418b.sketch_text.stroke-50"),sQuery(id+"F2.wireOp",EDGE,"fcba4419-a2ee-464f-be9d-58f11bf3418b.sketch_text.stroke-51"),sQuery(id+"F2.wireOp",EDGE,"fcba4419-a2ee-464f-be9d-58f11bf3418b.sketch_text.stroke-52"),sQuery(id+"F2.wireOp",EDGE,"fcba4419-a2ee-464f-be9d-58f11bf3418b.sketch_text.stroke-53"),sQuery(id+"F2.wireOp",EDGE,"fcba4419-a2ee-464f-be9d-58f11bf3418b.sketch_text.stroke-54"),sQuery(id+"F2.wireOp",EDGE,"fcba4419-a2ee-464f-be9d-58f11bf3418b.sketch_text.stroke-55"),sQuery(id+"F2.wireOp",EDGE,"fcba4419-a2ee-464f-be9d-58f11bf3418b.sketch_text.stroke-56"),sQuery(id+"F2.wireOp",EDGE,"fcba4419-a2ee-464f-be9d-58f11bf3418b.sketch_text.stroke-57"),sQuery(id+"F2.wireOp",EDGE,"fcba4419-a2ee-464f-be9d-58f11bf3418b.sketch_text.stroke-58"),sQuery(id+"F2.wireOp",EDGE,"fcba4419-a2ee-464f-be9d-58f11bf3418b.sketch_text.stroke-59"),sQuery(id+"F2.wireOp",EDGE,"fcba4419-a2ee-464f-be9d-58f11bf3418b.sketch_text.stroke-60"),sQuery(id+"F2.wireOp",EDGE,"fcba4419-a2ee-464f-be9d-58f11bf3418b.sketch_text.stroke-61"),sQuery(id+"F2.wireOp",EDGE,"fcba4419-a2ee-464f-be9d-58f11bf3418b.sketch_text.stroke-62"),sQuery(id+"F2.wireOp",EDGE,"fcba4419-a2ee-464f-be9d-58f11bf3418b.sketch_text.stroke-63"),sQuery(id+"F2.wireOp",EDGE,"fcba4419-a2ee-464f-be9d-58f11bf3418b.sketch_text.stroke-64"),sQuery(id+"F2.wireOp",EDGE,"fcba4419-a2ee-464f-be9d-58f11bf3418b.sketch_text.stroke-65"),sQuery(id+"F2.wireOp",EDGE,"fcba4419-a2ee-464f-be9d-58f11bf3418b.sketch_text.stroke-66"),sQuery(id+"F2.wireOp",EDGE,"fcba4419-a2ee-464f-be9d-58f11bf3418b.sketch_text.stroke-67"),sQuery(id+"F2.wireOp",EDGE,"fcba4419-a2ee-464f-be9d-58f11bf3418b.sketch_text.stroke-68"),sQuery(id+"F2.wireOp",EDGE,"fcba4419-a2ee-464f-be9d-58f11bf3418b.sketch_text.stroke-69"),sQuery(id+"F2.wireOp",EDGE,"fcba4419-a2ee-464f-be9d-58f11bf3418b.sketch_text.stroke-70"),sQuery(id+"F2.wireOp",EDGE,"fcba4419-a2ee-464f-be9d-58f11bf3418b.sketch_text.stroke-71"),sQuery(id+"F2.wireOp",EDGE,"fcba4419-a2ee-464f-be9d-58f11bf3418b.sketch_text.stroke-72"),sQuery(id+"F2.wireOp",EDGE,"fcba4419-a2ee-464f-be9d-58f11bf3418b.sketch_text.stroke-73"),sQuery(id+"F2.wireOp",EDGE,"fcba4419-a2ee-464f-be9d-58f11bf3418b.sketch_text.stroke-74"),sQuery(id+"F2.wireOp",EDGE,"fcba4419-a2ee-464f-be9d-58f11bf3418b.sketch_text.stroke-75"),sQuery(id+"F2.wireOp",EDGE,"fcba4419-a2ee-464f-be9d-58f11bf3418b.sketch_text.stroke-76"),sQuery(id+"F2.wireOp",EDGE,"fcba4419-a2ee-464f-be9d-58f11bf3418b.sketch_text.stroke-77"),sQuery(id+"F2.wireOp",EDGE,"fcba4419-a2ee-464f-be9d-58f11bf3418b.sketch_text.stroke-78"),sQuery(id+"F2.wireOp",EDGE,"fcba4419-a2ee-464f-be9d-58f11bf3418b.sketch_text.stroke-79"),sQuery(id+"F2.wireOp",EDGE,"fcba4419-a2ee-464f-be9d-58f11bf3418b.sketch_text.stroke-80"),sQuery(id+"F2.wireOp",EDGE,"fcba4419-a2ee-464f-be9d-58f11bf3418b.sketch_text.stroke-81"),sQuery(id+"F2.wireOp",EDGE,"fcba4419-a2ee-464f-be9d-58f11bf3418b.sketch_text.stroke-82"),sQuery(id+"F2.wireOp",EDGE,"fcba4419-a2ee-464f-be9d-58f11bf3418b.sketch_text.stroke-83"),sQuery(id+"F2.wireOp",EDGE,"fcba4419-a2ee-464f-be9d-58f11bf3418b.sketch_text.stroke-84"),sQuery(id+"F2.wireOp",EDGE,"fcba4419-a2ee-464f-be9d-58f11bf3418b.sketch_text.stroke-85"),sQuery(id+"F2.wireOp",EDGE,"fcba4419-a2ee-464f-be9d-58f11bf3418b.sketch_text.stroke-86"),sQuery(id+"F2.wireOp",EDGE,"fcba4419-a2ee-464f-be9d-58f11bf3418b.sketch_text.stroke-87"),sQuery(id+"F2.wireOp",EDGE,"fcba4419-a2ee-464f-be9d-58f11bf3418b.sketch_text.stroke-88"),sQuery(id+"F2.wireOp",EDGE,"fcba4419-a2ee-464f-be9d-58f11bf3418b.sketch_text.stroke-89"),sQuery(id+"F2.wireOp",EDGE,"fcba4419-a2ee-464f-be9d-58f11bf3418b.sketch_text.stroke-90"),sQuery(id+"F2.wireOp",EDGE,"fcba4419-a2ee-464f-be9d-58f11bf3418b.sketch_text.stroke-91"),sQuery(id+"F2.wireOp",EDGE,"fcba4419-a2ee-464f-be9d-58f11bf3418b.sketch_text.stroke-92"),sQuery(id+"F2.wireOp",EDGE,"fcba4419-a2ee-464f-be9d-58f11bf3418b.sketch_text.stroke-93"),sQuery(id+"F2.wireOp",EDGE,"fcba4419-a2ee-464f-be9d-58f11bf3418b.sketch_text.stroke-94"),sQuery(id+"F2.wireOp",EDGE,"fcba4419-a2ee-464f-be9d-58f11bf3418b.sketch_text.stroke-95"),sQuery(id+"F2.wireOp",EDGE,"fcba4419-a2ee-464f-be9d-58f11bf3418b.sketch_text.stroke-96"),sQuery(id+"F2.wireOp",EDGE,"fcba4419-a2ee-464f-be9d-58f11bf3418b.sketch_text.stroke-97"),sQuery(id+"F2.wireOp",EDGE,"fcba4419-a2ee-464f-be9d-58f11bf3418b.sketch_text.stroke-98"),sQuery(id+"F2.wireOp",EDGE,"fcba4419-a2ee-464f-be9d-58f11bf3418b.sketch_text.stroke-99"),sQuery(id+"F2.wireOp",EDGE,"fcba4419-a2ee-464f-be9d-58f11bf3418b.sketch_text.stroke-100"),sQuery(id+"F2.wireOp",EDGE,"fcba4419-a2ee-464f-be9d-58f11bf3418b.sketch_text.stroke-101"),sQuery(id+"F2.wireOp",EDGE,"fcba4419-a2ee-464f-be9d-58f11bf3418b.sketch_text.stroke-102"),sQuery(id+"F2.wireOp",EDGE,"fcba4419-a2ee-464f-be9d-58f11bf3418b.sketch_text.stroke-103"),sQuery(id+"F2.wireOp",EDGE,"fcba4419-a2ee-464f-be9d-58f11bf3418b.sketch_text.stroke-104"),sQuery(id+"F2.wireOp",EDGE,"fcba4419-a2ee-464f-be9d-58f11bf3418b.sketch_text.stroke-105"),sQuery(id+"F2.wireOp",EDGE,"fcba4419-a2ee-464f-be9d-58f11bf3418b.sketch_text.stroke-106"),sQuery(id+"F2.wireOp",EDGE,"fcba4419-a2ee-464f-be9d-58f11bf3418b.sketch_text.stroke-107"),sQuery(id+"F2.wireOp",EDGE,"fcba4419-a2ee-464f-be9d-58f11bf3418b.sketch_text.stroke-108"),sQuery(id+"F2.wireOp",EDGE,"fcba4419-a2ee-464f-be9d-58f11bf3418b.sketch_text.stroke-109"),sQuery(id+"F2.wireOp",EDGE,"fcba4419-a2ee-464f-be9d-58f11bf3418b.sketch_text.stroke-110"),sQuery(id+"F2.wireOp",EDGE,"fcba4419-a2ee-464f-be9d-58f11bf3418b.sketch_text.stroke-111"),sQuery(id+"F2.wireOp",EDGE,"fcba4419-a2ee-464f-be9d-58f11bf3418b.sketch_text.stroke-112"),sQuery(id+"F2.wireOp",EDGE,"fcba4419-a2ee-464f-be9d-58f11bf3418b.sketch_text.stroke-113"),sQuery(id+"F2.wireOp",EDGE,"fcba4419-a2ee-464f-be9d-58f11bf3418b.sketch_text.stroke-114"),sQuery(id+"F2.wireOp",EDGE,"fcba4419-a2ee-464f-be9d-58f11bf3418b.sketch_text.stroke-115"),sQuery(id+"F2.wireOp",EDGE,"fcba4419-a2ee-464f-be9d-58f11bf3418b.sketch_text.stroke-116"),sQuery(id+"F2.wireOp",EDGE,"fcba4419-a2ee-464f-be9d-58f11bf3418b.sketch_text.stroke-117"),sQuery(id+"F2.wireOp",EDGE,"fcba4419-a2ee-464f-be9d-58f11bf3418b.sketch_text.stroke-118"),sQuery(id+"F2.wireOp",EDGE,"fcba4419-a2ee-464f-be9d-58f11bf3418b.sketch_text.stroke-119"),sQuery(id+"F2.wireOp",EDGE,"fcba4419-a2ee-464f-be9d-58f11bf3418b.sketch_text.stroke-120"),sQuery(id+"F2.wireOp",EDGE,"fcba4419-a2ee-464f-be9d-58f11bf3418b.sketch_text.stroke-121"),sQuery(id+"F2.wireOp",EDGE,"fcba4419-a2ee-464f-be9d-58f11bf3418b.sketch_text.stroke-122"),sQuery(id+"F2.wireOp",EDGE,"fcba4419-a2ee-464f-be9d-58f11bf3418b.sketch_text.stroke-123"),sQuery(id+"F2.wireOp",EDGE,"fcba4419-a2ee-464f-be9d-58f11bf3418b.sketch_text.stroke-124"),sQuery(id+"F2.wireOp",EDGE,"fcba4419-a2ee-464f-be9d-58f11bf3418b.sketch_text.stroke-125"),sQuery(id+"F2.wireOp",EDGE,"fcba4419-a2ee-464f-be9d-58f11bf3418b.sketch_text.stroke-126"),sQuery(id+"F2.wireOp",EDGE,"fcba4419-a2ee-464f-be9d-58f11bf3418b.sketch_text.stroke-127"),sQuery(id+"F2.wireOp",EDGE,"fcba4419-a2ee-464f-be9d-58f11bf3418b.sketch_text.stroke-128"),sQuery(id+"F2.wireOp",EDGE,"fcba4419-a2ee-464f-be9d-58f11bf3418b.sketch_text.stroke-129"),sQuery(id+"F2.wireOp",EDGE,"fcba4419-a2ee-464f-be9d-58f11bf3418b.sketch_text.stroke-130"),sQuery(id+"F2.wireOp",EDGE,"fcba4419-a2ee-464f-be9d-58f11bf3418b.sketch_text.stroke-131"),sQuery(id+"F2.wireOp",EDGE,"fcba4419-a2ee-464f-be9d-58f11bf3418b.sketch_text.stroke-132"),sQuery(id+"F2.wireOp",EDGE,"fcba4419-a2ee-464f-be9d-58f11bf3418b.sketch_text.stroke-133"),sQuery(id+"F2.wireOp",EDGE,"fcba4419-a2ee-464f-be9d-58f11bf3418b.sketch_text.stroke-134"),sQuery(id+"F2.wireOp",EDGE,"fcba4419-a2ee-464f-be9d-58f11bf3418b.sketch_text.stroke-135"),sQuery(id+"F2.wireOp",EDGE,"fcba4419-a2ee-464f-be9d-58f11bf3418b.sketch_text.stroke-136"),sQuery(id+"F2.wireOp",EDGE,"fcba4419-a2ee-464f-be9d-58f11bf3418b.sketch_text.stroke-137"),sQuery(id+"F2.wireOp",EDGE,"fcba4419-a2ee-464f-be9d-58f11bf3418b.sketch_text.stroke-138"),sQuery(id+"F2.wireOp",EDGE,"fcba4419-a2ee-464f-be9d-58f11bf3418b.sketch_text.stroke-139"),sQuery(id+"F2.wireOp",EDGE,"fcba4419-a2ee-464f-be9d-58f11bf3418b.sketch_text.stroke-140"),sQuery(id+"F2.wireOp",EDGE,"fcba4419-a2ee-464f-be9d-58f11bf3418b.sketch_text.stroke-141"),sQuery(id+"F2.wireOp",EDGE,"fcba4419-a2ee-464f-be9d-58f11bf3418b.sketch_text.stroke-142"),sQuery(id+"F2.wireOp",EDGE,"fcba4419-a2ee-464f-be9d-58f11bf3418b.sketch_text.stroke-143"),sQuery(id+"F2.wireOp",EDGE,"fcba4419-a2ee-464f-be9d-58f11bf3418b.sketch_text.stroke-144"),sQuery(id+"F2.wireOp",EDGE,"fcba4419-a2ee-464f-be9d-58f11bf3418b.sketch_text.stroke-145"),sQuery(id+"F2.wireOp",EDGE,"fcba4419-a2ee-464f-be9d-58f11bf3418b.sketch_text.stroke-146"),sQuery(id+"F2.wireOp",EDGE,"fcba4419-a2ee-464f-be9d-58f11bf3418b.sketch_text.stroke-147"),sQuery(id+"F2.wireOp",EDGE,"fcba4419-a2ee-464f-be9d-58f11bf3418b.sketch_text.stroke-148"),sQuery(id+"F2.wireOp",EDGE,"fcba4419-a2ee-464f-be9d-58f11bf3418b.sketch_text.stroke-149"),sQuery(id+"F2.wireOp",EDGE,"fcba4419-a2ee-464f-be9d-58f11bf3418b.sketch_text.stroke-150"),sQuery(id+"F2.wireOp",EDGE,"fcba4419-a2ee-464f-be9d-58f11bf3418b.sketch_text.stroke-151"),sQuery(id+"F2.wireOp",EDGE,"fcba4419-a2ee-464f-be9d-58f11bf3418b.sketch_text.stroke-152"),sQuery(id+"F2.wireOp",EDGE,"fcba4419-a2ee-464f-be9d-58f11bf3418b.sketch_text.stroke-153"),sQuery(id+"F2.wireOp",EDGE,"fcba4419-a2ee-464f-be9d-58f11bf3418b.sketch_text.stroke-154"),sQuery(id+"F2.wireOp",EDGE,"fcba4419-a2ee-464f-be9d-58f11bf3418b.sketch_text.stroke-155"),sQuery(id+"F2.wireOp",EDGE,"fcba4419-a2ee-464f-be9d-58f11bf3418b.sketch_text.stroke-156"),sQuery(id+"F2.wireOp",EDGE,"fcba4419-a2ee-464f-be9d-58f11bf3418b.sketch_text.stroke-157"),sQuery(id+"F2.wireOp",EDGE,"fcba4419-a2ee-464f-be9d-58f11bf3418b.sketch_text.stroke-158"),sQuery(id+"F2.wireOp",EDGE,"fcba4419-a2ee-464f-be9d-58f11bf3418b.sketch_text.stroke-159"),sQuery(id+"F2.wireOp",EDGE,"fcba4419-a2ee-464f-be9d-58f11bf3418b.sketch_text.stroke-160"),sQuery(id+"F2.wireOp",EDGE,"fcba4419-a2ee-464f-be9d-58f11bf3418b.sketch_text.stroke-161"),sQuery(id+"F2.wireOp",EDGE,"fcba4419-a2ee-464f-be9d-58f11bf3418b.sketch_text.stroke-162"),sQuery(id+"F2.wireOp",EDGE,"fcba4419-a2ee-464f-be9d-58f11bf3418b.sketch_text.stroke-163"),sQuery(id+"F2.wireOp",EDGE,"fcba4419-a2ee-464f-be9d-58f11bf3418b.sketch_text.stroke-164"),sQuery(id+"F2.wireOp",EDGE,"fcba4419-a2ee-464f-be9d-58f11bf3418b.sketch_text.stroke-165"),sQuery(id+"F2.wireOp",EDGE,"fcba4419-a2ee-464f-be9d-58f11bf3418b.sketch_text.stroke-166"),sQuery(id+"F2.wireOp",EDGE,"fcba4419-a2ee-464f-be9d-58f11bf3418b.sketch_text.stroke-167"),sQuery(id+"F2.wireOp",EDGE,"fcba4419-a2ee-464f-be9d-58f11bf3418b.sketch_text.stroke-168"),sQuery(id+"F2.wireOp",EDGE,"fcba4419-a2ee-464f-be9d-58f11bf3418b.sketch_text.stroke-169"),sQuery(id+"F2.wireOp",EDGE,"fcba4419-a2ee-464f-be9d-58f11bf3418b.sketch_text.stroke-170"),sQuery(id+"F2.wireOp",EDGE,"fcba4419-a2ee-464f-be9d-58f11bf3418b.sketch_text.stroke-171"),sQuery(id+"F2.wireOp",EDGE,"fcba4419-a2ee-464f-be9d-58f11bf3418b.sketch_text.stroke-172"),sQuery(id+"F2.wireOp",EDGE,"fcba4419-a2ee-464f-be9d-58f11bf3418b.sketch_text.stroke-173"),sQuery(id+"FHMxAyK4CFUKdhS_1.wireOp",EDGE,"1cb9c079-ea9b-4899-8069-e0e3048e911d.sketch_text.stroke-0"),sQuery(id+"FHMxAyK4CFUKdhS_1.wireOp",EDGE,"1cb9c079-ea9b-4899-8069-e0e3048e911d.sketch_text.stroke-1"),sQuery(id+"FHMxAyK4CFUKdhS_1.wireOp",EDGE,"1cb9c079-ea9b-4899-8069-e0e3048e911d.sketch_text.stroke-2"),sQuery(id+"FHMxAyK4CFUKdhS_1.wireOp",EDGE,"1cb9c079-ea9b-4899-8069-e0e3048e911d.sketch_text.stroke-3"),sQuery(id+"FHMxAyK4CFUKdhS_1.wireOp",EDGE,"1cb9c079-ea9b-4899-8069-e0e3048e911d.sketch_text.stroke-4"),sQuery(id+"FHMxAyK4CFUKdhS_1.wireOp",EDGE,"1cb9c079-ea9b-4899-8069-e0e3048e911d.sketch_text.stroke-5"),sQuery(id+"FHMxAyK4CFUKdhS_1.wireOp",EDGE,"1cb9c079-ea9b-4899-8069-e0e3048e911d.sketch_text.stroke-6"),sQuery(id+"FHMxAyK4CFUKdhS_1.wireOp",EDGE,"1cb9c079-ea9b-4899-8069-e0e3048e911d.sketch_text.stroke-7"),sQuery(id+"FHMxAyK4CFUKdhS_1.wireOp",EDGE,"1cb9c079-ea9b-4899-8069-e0e3048e911d.sketch_text.stroke-8"),sQuery(id+"FHMxAyK4CFUKdhS_1.wireOp",EDGE,"1cb9c079-ea9b-4899-8069-e0e3048e911d.sketch_text.stroke-9"),sQuery(id+"FHMxAyK4CFUKdhS_1.wireOp",EDGE,"1cb9c079-ea9b-4899-8069-e0e3048e911d.sketch_text.stroke-10"),sQuery(id+"FHMxAyK4CFUKdhS_1.wireOp",EDGE,"1cb9c079-ea9b-4899-8069-e0e3048e911d.sketch_text.stroke-11"),sQuery(id+"FHMxAyK4CFUKdhS_1.wireOp",EDGE,"1cb9c079-ea9b-4899-8069-e0e3048e911d.sketch_text.stroke-12"),sQuery(id+"FHMxAyK4CFUKdhS_1.wireOp",EDGE,"1cb9c079-ea9b-4899-8069-e0e3048e911d.sketch_text.stroke-13"),sQuery(id+"FHMxAyK4CFUKdhS_1.wireOp",EDGE,"1cb9c079-ea9b-4899-8069-e0e3048e911d.sketch_text.stroke-14"),sQuery(id+"FHMxAyK4CFUKdhS_1.wireOp",EDGE,"1cb9c079-ea9b-4899-8069-e0e3048e911d.sketch_text.stroke-15"),sQuery(id+"FHMxAyK4CFUKdhS_1.wireOp",EDGE,"1cb9c079-ea9b-4899-8069-e0e3048e911d.sketch_text.stroke-16"),sQuery(id+"FHMxAyK4CFUKdhS_1.wireOp",EDGE,"1cb9c079-ea9b-4899-8069-e0e3048e911d.sketch_text.stroke-17"),sQuery(id+"FHMxAyK4CFUKdhS_1.wireOp",EDGE,"1cb9c079-ea9b-4899-8069-e0e3048e911d.sketch_text.stroke-18"),sQuery(id+"FHMxAyK4CFUKdhS_1.wireOp",EDGE,"1cb9c079-ea9b-4899-8069-e0e3048e911d.sketch_text.stroke-19"),sQuery(id+"FHMxAyK4CFUKdhS_1.wireOp",EDGE,"1cb9c079-ea9b-4899-8069-e0e3048e911d.sketch_text.stroke-20"),sQuery(id+"FHMxAyK4CFUKdhS_1.wireOp",EDGE,"1cb9c079-ea9b-4899-8069-e0e3048e911d.sketch_text.stroke-21"),sQuery(id+"FHMxAyK4CFUKdhS_1.wireOp",EDGE,"1cb9c079-ea9b-4899-8069-e0e3048e911d.sketch_text.stroke-22"),sQuery(id+"FHMxAyK4CFUKdhS_1.wireOp",EDGE,"1cb9c079-ea9b-4899-8069-e0e3048e911d.sketch_text.stroke-23"),sQuery(id+"FHMxAyK4CFUKdhS_1.wireOp",EDGE,"1cb9c079-ea9b-4899-8069-e0e3048e911d.sketch_text.stroke-24"),sQuery(id+"FHMxAyK4CFUKdhS_1.wireOp",EDGE,"1cb9c079-ea9b-4899-8069-e0e3048e911d.sketch_text.stroke-25"),sQuery(id+"FHMxAyK4CFUKdhS_1.wireOp",EDGE,"1cb9c079-ea9b-4899-8069-e0e3048e911d.sketch_text.stroke-26"),sQuery(id+"FHMxAyK4CFUKdhS_1.wireOp",EDGE,"1cb9c079-ea9b-4899-8069-e0e3048e911d.sketch_text.stroke-27"),sQuery(id+"FHMxAyK4CFUKdhS_1.wireOp",EDGE,"1cb9c079-ea9b-4899-8069-e0e3048e911d.sketch_text.stroke-28"),sQuery(id+"FHMxAyK4CFUKdhS_1.wireOp",EDGE,"1cb9c079-ea9b-4899-8069-e0e3048e911d.sketch_text.stroke-29"),sQuery(id+"FHMxAyK4CFUKdhS_1.wireOp",EDGE,"1cb9c079-ea9b-4899-8069-e0e3048e911d.sketch_text.stroke-30"),sQuery(id+"FHMxAyK4CFUKdhS_1.wireOp",EDGE,"1cb9c079-ea9b-4899-8069-e0e3048e911d.sketch_text.stroke-31"),sQuery(id+"FHMxAyK4CFUKdhS_1.wireOp",EDGE,"1cb9c079-ea9b-4899-8069-e0e3048e911d.sketch_text.stroke-32"),sQuery(id+"FHMxAyK4CFUKdhS_1.wireOp",EDGE,"1cb9c079-ea9b-4899-8069-e0e3048e911d.sketch_text.stroke-33"),sQuery(id+"FHMxAyK4CFUKdhS_1.wireOp",EDGE,"1cb9c079-ea9b-4899-8069-e0e3048e911d.sketch_text.stroke-34"),sQuery(id+"FHMxAyK4CFUKdhS_1.wireOp",EDGE,"1cb9c079-ea9b-4899-8069-e0e3048e911d.sketch_text.stroke-35"),sQuery(id+"FHMxAyK4CFUKdhS_1.wireOp",EDGE,"1cb9c079-ea9b-4899-8069-e0e3048e911d.sketch_text.stroke-36"),sQuery(id+"FHMxAyK4CFUKdhS_1.wireOp",EDGE,"1cb9c079-ea9b-4899-8069-e0e3048e911d.sketch_text.stroke-37"),sQuery(id+"FHMxAyK4CFUKdhS_1.wireOp",EDGE,"1cb9c079-ea9b-4899-8069-e0e3048e911d.sketch_text.stroke-38"),sQuery(id+"FHMxAyK4CFUKdhS_1.wireOp",EDGE,"1cb9c079-ea9b-4899-8069-e0e3048e911d.sketch_text.stroke-39"),sQuery(id+"FHMxAyK4CFUKdhS_1.wireOp",EDGE,"1cb9c079-ea9b-4899-8069-e0e3048e911d.sketch_text.stroke-40"),sQuery(id+"FHMxAyK4CFUKdhS_1.wireOp",EDGE,"1cb9c079-ea9b-4899-8069-e0e3048e911d.sketch_text.stroke-41"),sQuery(id+"FHMxAyK4CFUKdhS_1.wireOp",EDGE,"1cb9c079-ea9b-4899-8069-e0e3048e911d.sketch_text.stroke-42"),sQuery(id+"FHMxAyK4CFUKdhS_1.wireOp",EDGE,"1cb9c079-ea9b-4899-8069-e0e3048e911d.sketch_text.stroke-43"),sQuery(id+"FHMxAyK4CFUKdhS_1.wireOp",EDGE,"1cb9c079-ea9b-4899-8069-e0e3048e911d.sketch_text.stroke-44"),sQuery(id+"FHMxAyK4CFUKdhS_1.wireOp",EDGE,"1cb9c079-ea9b-4899-8069-e0e3048e911d.sketch_text.stroke-45"),sQuery(id+"FHMxAyK4CFUKdhS_1.wireOp",EDGE,"1cb9c079-ea9b-4899-8069-e0e3048e911d.sketch_text.stroke-46"),sQuery(id+"FHMxAyK4CFUKdhS_1.wireOp",EDGE,"1cb9c079-ea9b-4899-8069-e0e3048e911d.sketch_text.stroke-47"),sQuery(id+"FHMxAyK4CFUKdhS_1.wireOp",EDGE,"1cb9c079-ea9b-4899-8069-e0e3048e911d.sketch_text.stroke-48"),sQuery(id+"FHMxAyK4CFUKdhS_1.wireOp",EDGE,"1cb9c079-ea9b-4899-8069-e0e3048e911d.sketch_text.stroke-49"),sQuery(id+"FHMxAyK4CFUKdhS_1.wireOp",EDGE,"1cb9c079-ea9b-4899-8069-e0e3048e911d.sketch_text.stroke-50"),sQuery(id+"FHMxAyK4CFUKdhS_1.wireOp",EDGE,"1cb9c079-ea9b-4899-8069-e0e3048e911d.sketch_text.stroke-51"),sQuery(id+"FHMxAyK4CFUKdhS_1.wireOp",EDGE,"1cb9c079-ea9b-4899-8069-e0e3048e911d.sketch_text.stroke-52"),sQuery(id+"FHMxAyK4CFUKdhS_1.wireOp",EDGE,"1cb9c079-ea9b-4899-8069-e0e3048e911d.sketch_text.stroke-53"),sQuery(id+"FHMxAyK4CFUKdhS_1.wireOp",EDGE,"1cb9c079-ea9b-4899-8069-e0e3048e911d.sketch_text.stroke-54"),sQuery(id+"FHMxAyK4CFUKdhS_1.wireOp",EDGE,"1cb9c079-ea9b-4899-8069-e0e3048e911d.sketch_text.stroke-55"),sQuery(id+"FHMxAyK4CFUKdhS_1.wireOp",EDGE,"1cb9c079-ea9b-4899-8069-e0e3048e911d.sketch_text.stroke-56"),sQuery(id+"FHMxAyK4CFUKdhS_1.wireOp",EDGE,"1cb9c079-ea9b-4899-8069-e0e3048e911d.sketch_text.stroke-57"),sQuery(id+"FHMxAyK4CFUKdhS_1.wireOp",EDGE,"1cb9c079-ea9b-4899-8069-e0e3048e911d.sketch_text.stroke-58"),sQuery(id+"FHMxAyK4CFUKdhS_1.wireOp",EDGE,"1cb9c079-ea9b-4899-8069-e0e3048e911d.sketch_text.stroke-59"),sQuery(id+"FHMxAyK4CFUKdhS_1.wireOp",EDGE,"1cb9c079-ea9b-4899-8069-e0e3048e911d.sketch_text.stroke-60"),sQuery(id+"FHMxAyK4CFUKdhS_1.wireOp",EDGE,"1cb9c079-ea9b-4899-8069-e0e3048e911d.sketch_text.stroke-61"),sQuery(id+"FHMxAyK4CFUKdhS_1.wireOp",EDGE,"1cb9c079-ea9b-4899-8069-e0e3048e911d.sketch_text.stroke-62"),sQuery(id+"FHMxAyK4CFUKdhS_1.wireOp",EDGE,"1cb9c079-ea9b-4899-8069-e0e3048e911d.sketch_text.stroke-71"),sQuery(id+"FHMxAyK4CFUKdhS_1.wireOp",EDGE,"1cb9c079-ea9b-4899-8069-e0e3048e911d.sketch_text.stroke-72"),sQuery(id+"FHMxAyK4CFUKdhS_1.wireOp",EDGE,"1cb9c079-ea9b-4899-8069-e0e3048e911d.sketch_text.stroke-73"),sQuery(id+"FHMxAyK4CFUKdhS_1.wireOp",EDGE,"1cb9c079-ea9b-4899-8069-e0e3048e911d.sketch_text.stroke-74"),sQuery(id+"FHMxAyK4CFUKdhS_1.wireOp",EDGE,"1cb9c079-ea9b-4899-8069-e0e3048e911d.sketch_text.stroke-75"),sQuery(id+"FHMxAyK4CFUKdhS_1.wireOp",EDGE,"1cb9c079-ea9b-4899-8069-e0e3048e911d.sketch_text.stroke-76"),sQuery(id+"FHMxAyK4CFUKdhS_1.wireOp",EDGE,"1cb9c079-ea9b-4899-8069-e0e3048e911d.sketch_text.stroke-77"),sQuery(id+"FHMxAyK4CFUKdhS_1.wireOp",EDGE,"1cb9c079-ea9b-4899-8069-e0e3048e911d.sketch_text.stroke-78"),sQuery(id+"FHMxAyK4CFUKdhS_1.wireOp",EDGE,"1cb9c079-ea9b-4899-8069-e0e3048e911d.sketch_text.stroke-79"),sQuery(id+"FHMxAyK4CFUKdhS_1.wireOp",EDGE,"1cb9c079-ea9b-4899-8069-e0e3048e911d.sketch_text.stroke-80"),sQuery(id+"FHMxAyK4CFUKdhS_1.wireOp",EDGE,"1cb9c079-ea9b-4899-8069-e0e3048e911d.sketch_text.stroke-81"),sQuery(id+"FHMxAyK4CFUKdhS_1.wireOp",EDGE,"1cb9c079-ea9b-4899-8069-e0e3048e911d.sketch_text.stroke-82"),sQuery(id+"FHMxAyK4CFUKdhS_1.wireOp",EDGE,"1cb9c079-ea9b-4899-8069-e0e3048e911d.sketch_text.stroke-83"),sQuery(id+"FHMxAyK4CFUKdhS_1.wireOp",EDGE,"1cb9c079-ea9b-4899-8069-e0e3048e911d.sketch_text.stroke-84"),sQuery(id+"FHMxAyK4CFUKdhS_1.wireOp",EDGE,"1cb9c079-ea9b-4899-8069-e0e3048e911d.sketch_text.stroke-85"),sQuery(id+"FHMxAyK4CFUKdhS_1.wireOp",EDGE,"1cb9c079-ea9b-4899-8069-e0e3048e911d.sketch_text.stroke-86"),sQuery(id+"FHMxAyK4CFUKdhS_1.wireOp",EDGE,"1cb9c079-ea9b-4899-8069-e0e3048e911d.sketch_text.stroke-87"),sQuery(id+"FHMxAyK4CFUKdhS_1.wireOp",EDGE,"1cb9c079-ea9b-4899-8069-e0e3048e911d.sketch_text.stroke-88"),sQuery(id+"FHMxAyK4CFUKdhS_1.wireOp",EDGE,"1cb9c079-ea9b-4899-8069-e0e3048e911d.sketch_text.stroke-89"),sQuery(id+"FHMxAyK4CFUKdhS_1.wireOp",EDGE,"1cb9c079-ea9b-4899-8069-e0e3048e911d.sketch_text.stroke-90"),sQuery(id+"FHMxAyK4CFUKdhS_1.wireOp",EDGE,"1cb9c079-ea9b-4899-8069-e0e3048e911d.sketch_text.stroke-91"),sQuery(id+"FHMxAyK4CFUKdhS_1.wireOp",EDGE,"1cb9c079-ea9b-4899-8069-e0e3048e911d.sketch_text.stroke-92"),sQuery(id+"FHMxAyK4CFUKdhS_1.wireOp",EDGE,"1cb9c079-ea9b-4899-8069-e0e3048e911d.sketch_text.stroke-93"),sQuery(id+"FHMxAyK4CFUKdhS_1.wireOp",EDGE,"1cb9c079-ea9b-4899-8069-e0e3048e911d.sketch_text.stroke-94"),sQuery(id+"FHMxAyK4CFUKdhS_1.wireOp",EDGE,"1cb9c079-ea9b-4899-8069-e0e3048e911d.sketch_text.stroke-95"),sQuery(id+"FHMxAyK4CFUKdhS_1.wireOp",EDGE,"1cb9c079-ea9b-4899-8069-e0e3048e911d.sketch_text.stroke-96"),sQuery(id+"FHMxAyK4CFUKdhS_1.wireOp",EDGE,"1cb9c079-ea9b-4899-8069-e0e3048e911d.sketch_text.stroke-97"),sQuery(id+"FHMxAyK4CFUKdhS_1.wireOp",EDGE,"1cb9c079-ea9b-4899-8069-e0e3048e911d.sketch_text.stroke-103"),sQuery(id+"FHMxAyK4CFUKdhS_1.wireOp",EDGE,"1cb9c079-ea9b-4899-8069-e0e3048e911d.sketch_text.stroke-104"),sQuery(id+"FHMxAyK4CFUKdhS_1.wireOp",EDGE,"1cb9c079-ea9b-4899-8069-e0e3048e911d.sketch_text.stroke-105"),sQuery(id+"FHMxAyK4CFUKdhS_1.wireOp",EDGE,"1cb9c079-ea9b-4899-8069-e0e3048e911d.sketch_text.stroke-106"),sQuery(id+"FHMxAyK4CFUKdhS_1.wireOp",EDGE,"1cb9c079-ea9b-4899-8069-e0e3048e911d.sketch_text.stroke-107"),sQuery(id+"FHMxAyK4CFUKdhS_1.wireOp",EDGE,"1cb9c079-ea9b-4899-8069-e0e3048e911d.sketch_text.stroke-108"),sQuery(id+"FHMxAyK4CFUKdhS_1.wireOp",EDGE,"1cb9c079-ea9b-4899-8069-e0e3048e911d.sketch_text.stroke-109"),sQuery(id+"FHMxAyK4CFUKdhS_1.wireOp",EDGE,"1cb9c079-ea9b-4899-8069-e0e3048e911d.sketch_text.stroke-110"),sQuery(id+"FHMxAyK4CFUKdhS_1.wireOp",EDGE,"1cb9c079-ea9b-4899-8069-e0e3048e911d.sketch_text.stroke-111"),sQuery(id+"FHMxAyK4CFUKdhS_1.wireOp",EDGE,"1cb9c079-ea9b-4899-8069-e0e3048e911d.sketch_text.stroke-112"),sQuery(id+"FHMxAyK4CFUKdhS_1.wireOp",EDGE,"1cb9c079-ea9b-4899-8069-e0e3048e911d.sketch_text.stroke-113"),sQuery(id+"FHMxAyK4CFUKdhS_1.wireOp",EDGE,"1cb9c079-ea9b-4899-8069-e0e3048e911d.sketch_text.stroke-114"),sQuery(id+"FHMxAyK4CFUKdhS_1.wireOp",EDGE,"1cb9c079-ea9b-4899-8069-e0e3048e911d.sketch_text.stroke-115"),sQuery(id+"FHMxAyK4CFUKdhS_1.wireOp",EDGE,"1cb9c079-ea9b-4899-8069-e0e3048e911d.sketch_text.stroke-116"),sQuery(id+"FHMxAyK4CFUKdhS_1.wireOp",EDGE,"1cb9c079-ea9b-4899-8069-e0e3048e911d.sketch_text.stroke-117"),sQuery(id+"FHMxAyK4CFUKdhS_1.wireOp",EDGE,"1cb9c079-ea9b-4899-8069-e0e3048e911d.sketch_text.stroke-118"),sQuery(id+"FHMxAyK4CFUKdhS_1.wireOp",EDGE,"1cb9c079-ea9b-4899-8069-e0e3048e911d.sketch_text.stroke-119"),sQuery(id+"FHMxAyK4CFUKdhS_1.wireOp",EDGE,"1cb9c079-ea9b-4899-8069-e0e3048e911d.sketch_text.stroke-120"),sQuery(id+"FHMxAyK4CFUKdhS_1.wireOp",EDGE,"1cb9c079-ea9b-4899-8069-e0e3048e911d.sketch_text.stroke-121"),sQuery(id+"FHMxAyK4CFUKdhS_1.wireOp",EDGE,"1cb9c079-ea9b-4899-8069-e0e3048e911d.sketch_text.stroke-122"),sQuery(id+"FHMxAyK4CFUKdhS_1.wireOp",EDGE,"1cb9c079-ea9b-4899-8069-e0e3048e911d.sketch_text.stroke-123"),sQuery(id+"FHMxAyK4CFUKdhS_1.wireOp",EDGE,"1cb9c079-ea9b-4899-8069-e0e3048e911d.sketch_text.stroke-124"),sQuery(id+"FHMxAyK4CFUKdhS_1.wireOp",EDGE,"1cb9c079-ea9b-4899-8069-e0e3048e911d.sketch_text.stroke-125"),sQuery(id+"FHMxAyK4CFUKdhS_1.wireOp",EDGE,"1cb9c079-ea9b-4899-8069-e0e3048e911d.sketch_text.stroke-126"),sQuery(id+"FHMxAyK4CFUKdhS_1.wireOp",EDGE,"1cb9c079-ea9b-4899-8069-e0e3048e911d.sketch_text.stroke-127"),sQuery(id+"FHMxAyK4CFUKdhS_1.wireOp",EDGE,"1cb9c079-ea9b-4899-8069-e0e3048e911d.sketch_text.stroke-128"),sQuery(id+"FHMxAyK4CFUKdhS_1.wireOp",EDGE,"1cb9c079-ea9b-4899-8069-e0e3048e911d.sketch_text.stroke-129"),sQuery(id+"FHMxAyK4CFUKdhS_1.wireOp",EDGE,"1cb9c079-ea9b-4899-8069-e0e3048e911d.sketch_text.stroke-130"),sQuery(id+"FHMxAyK4CFUKdhS_1.wireOp",EDGE,"1cb9c079-ea9b-4899-8069-e0e3048e911d.sketch_text.stroke-131"),sQuery(id+"FHMxAyK4CFUKdhS_1.wireOp",EDGE,"1cb9c079-ea9b-4899-8069-e0e3048e911d.sketch_text.stroke-132"),sQuery(id+"FHMxAyK4CFUKdhS_1.wireOp",EDGE,"1cb9c079-ea9b-4899-8069-e0e3048e911d.sketch_text.stroke-133"),sQuery(id+"FHMxAyK4CFUKdhS_1.wireOp",EDGE,"1cb9c079-ea9b-4899-8069-e0e3048e911d.sketch_text.stroke-134"),sQuery(id+"FHMxAyK4CFUKdhS_1.wireOp",EDGE,"1cb9c079-ea9b-4899-8069-e0e3048e911d.sketch_text.stroke-135"),sQuery(id+"FHMxAyK4CFUKdhS_1.wireOp",EDGE,"1cb9c079-ea9b-4899-8069-e0e3048e911d.sketch_text.stroke-136"),sQuery(id+"FHMxAyK4CFUKdhS_1.wireOp",EDGE,"1cb9c079-ea9b-4899-8069-e0e3048e911d.sketch_text.stroke-137"),sQuery(id+"FHMxAyK4CFUKdhS_1.wireOp",EDGE,"1cb9c079-ea9b-4899-8069-e0e3048e911d.sketch_text.stroke-138"),sQuery(id+"FHMxAyK4CFUKdhS_1.wireOp",EDGE,"1cb9c079-ea9b-4899-8069-e0e3048e911d.sketch_text.stroke-139"),sQuery(id+"FHMxAyK4CFUKdhS_1.wireOp",EDGE,"1cb9c079-ea9b-4899-8069-e0e3048e911d.sketch_text.stroke-140"),sQuery(id+"FHMxAyK4CFUKdhS_1.wireOp",EDGE,"1cb9c079-ea9b-4899-8069-e0e3048e911d.sketch_text.stroke-141"),sQuery(id+"FHMxAyK4CFUKdhS_1.wireOp",EDGE,"1cb9c079-ea9b-4899-8069-e0e3048e911d.sketch_text.stroke-142"),sQuery(id+"FHMxAyK4CFUKdhS_1.wireOp",EDGE,"1cb9c079-ea9b-4899-8069-e0e3048e911d.sketch_text.stroke-143"),sQuery(id+"FHMxAyK4CFUKdhS_1.wireOp",EDGE,"1cb9c079-ea9b-4899-8069-e0e3048e911d.sketch_text.stroke-144"),sQuery(id+"FHMxAyK4CFUKdhS_1.wireOp",EDGE,"1cb9c079-ea9b-4899-8069-e0e3048e911d.sketch_text.stroke-145"),sQuery(id+"FHMxAyK4CFUKdhS_1.wireOp",EDGE,"1cb9c079-ea9b-4899-8069-e0e3048e911d.sketch_text.stroke-146"),sQuery(id+"FHMxAyK4CFUKdhS_1.wireOp",EDGE,"1cb9c079-ea9b-4899-8069-e0e3048e911d.sketch_text.stroke-147"),sQuery(id+"FHMxAyK4CFUKdhS_1.wireOp",EDGE,"1cb9c079-ea9b-4899-8069-e0e3048e911d.sketch_text.stroke-148"),sQuery(id+"FHMxAyK4CFUKdhS_1.wireOp",EDGE,"1cb9c079-ea9b-4899-8069-e0e3048e911d.sketch_text.stroke-149"),sQuery(id+"FHMxAyK4CFUKdhS_1.wireOp",EDGE,"1cb9c079-ea9b-4899-8069-e0e3048e911d.sketch_text.stroke-150"),sQuery(id+"FHMxAyK4CFUKdhS_1.wireOp",EDGE,"1cb9c079-ea9b-4899-8069-e0e3048e911d.sketch_text.stroke-151"),sQuery(id+"FHMxAyK4CFUKdhS_1.wireOp",EDGE,"1cb9c079-ea9b-4899-8069-e0e3048e911d.sketch_text.stroke-152"),sQuery(id+"FHMxAyK4CFUKdhS_1.wireOp",EDGE,"1cb9c079-ea9b-4899-8069-e0e3048e911d.sketch_text.stroke-153"),sQuery(id+"FHMxAyK4CFUKdhS_1.wireOp",EDGE,"1cb9c079-ea9b-4899-8069-e0e3048e911d.sketch_text.stroke-159"),sQuery(id+"FHMxAyK4CFUKdhS_1.wireOp",EDGE,"1cb9c079-ea9b-4899-8069-e0e3048e911d.sketch_text.stroke-160"),sQuery(id+"FHMxAyK4CFUKdhS_1.wireOp",EDGE,"1cb9c079-ea9b-4899-8069-e0e3048e911d.sketch_text.stroke-161"),sQuery(id+"FHMxAyK4CFUKdhS_1.wireOp",EDGE,"1cb9c079-ea9b-4899-8069-e0e3048e911d.sketch_text.stroke-162"),sQuery(id+"FHMxAyK4CFUKdhS_1.wireOp",EDGE,"1cb9c079-ea9b-4899-8069-e0e3048e911d.sketch_text.stroke-163"),sQuery(id+"FHMxAyK4CFUKdhS_1.wireOp",EDGE,"1cb9c079-ea9b-4899-8069-e0e3048e911d.sketch_text.stroke-164"),sQuery(id+"FHMxAyK4CFUKdhS_1.wireOp",EDGE,"1cb9c079-ea9b-4899-8069-e0e3048e911d.sketch_text.stroke-165"),sQuery(id+"FHMxAyK4CFUKdhS_1.wireOp",EDGE,"1cb9c079-ea9b-4899-8069-e0e3048e911d.sketch_text.stroke-166"),sQuery(id+"FHMxAyK4CFUKdhS_1.wireOp",EDGE,"1cb9c079-ea9b-4899-8069-e0e3048e911d.sketch_text.stroke-167"),sQuery(id+"FHMxAyK4CFUKdhS_1.wireOp",EDGE,"1cb9c079-ea9b-4899-8069-e0e3048e911d.sketch_text.stroke-168"),sQuery(id+"FHMxAyK4CFUKdhS_1.wireOp",EDGE,"1cb9c079-ea9b-4899-8069-e0e3048e911d.sketch_text.stroke-169"),sQuery(id+"FHMxAyK4CFUKdhS_1.wireOp",EDGE,"1cb9c079-ea9b-4899-8069-e0e3048e911d.sketch_text.stroke-170"),sQuery(id+"FHMxAyK4CFUKdhS_1.wireOp",EDGE,"1cb9c079-ea9b-4899-8069-e0e3048e911d.sketch_text.stroke-171"),sQuery(id+"FHMxAyK4CFUKdhS_1.wireOp",EDGE,"1cb9c079-ea9b-4899-8069-e0e3048e911d.sketch_text.stroke-172"),sQuery(id+"FHMxAyK4CFUKdhS_1.wireOp",EDGE,"1cb9c079-ea9b-4899-8069-e0e3048e911d.sketch_text.stroke-173"),sQuery(id+"FHMxAyK4CFUKdhS_1.wireOp",EDGE,"1cb9c079-ea9b-4899-8069-e0e3048e911d.sketch_text.stroke-174"),sQuery(id+"FHMxAyK4CFUKdhS_1.wireOp",EDGE,"1cb9c079-ea9b-4899-8069-e0e3048e911d.sketch_text.stroke-175"),sQuery(id+"FHMxAyK4CFUKdhS_1.wireOp",EDGE,"1cb9c079-ea9b-4899-8069-e0e3048e911d.sketch_text.stroke-176"),sQuery(id+"FHMxAyK4CFUKdhS_1.wireOp",EDGE,"1cb9c079-ea9b-4899-8069-e0e3048e911d.sketch_text.stroke-177"),sQuery(id+"FHMxAyK4CFUKdhS_1.wireOp",EDGE,"1cb9c079-ea9b-4899-8069-e0e3048e911d.sketch_text.stroke-178"),sQuery(id+"FHMxAyK4CFUKdhS_1.wireOp",EDGE,"1cb9c079-ea9b-4899-8069-e0e3048e911d.sketch_text.stroke-179"),sQuery(id+"FHMxAyK4CFUKdhS_1.wireOp",EDGE,"1cb9c079-ea9b-4899-8069-e0e3048e911d.sketch_text.stroke-180"),subQ0,subQ2])],"isStart":true}),makeQuery(id+"F4.opExtrude","SWEPT_FACE",FACE,{"disambiguationData":[OSD([subQ2])]})])],"derivedFrom":makeQuery(id+"F4.opExtrude","CAP_EDGE",EDGE,{"disambiguationData":[OSD([subQ0])],"isStart":true})});}
            var Q22;
            {var subQ0=sQuery(id+"F3.wireOp",EDGE,"E29");var subQ1=sQuery(id+"F0.wireOp",EDGE,"E0.top");var subQ2=sQuery(id+"F3.wireOp",EDGE,"E30");var subQ3=sQuery(id+"F0.wireOp",EDGE,"E0.bottom");Q22=makeQuery(id+"F4.boolean.opBoolean","SPLIT",EDGE,{"disambiguationData":[TD([makeQuery(id+"F1.opExtrude","CAP_FACE",FACE,{"disambiguationData":[OSD([subQ3,subQ1,sQuery(id+"F0.wireOp",EDGE,"E0.left"),sQuery(id+"F0.wireOp",EDGE,"E0.right")])],"isStart":false}),makeQuery(id+"F1.opExtrude","SWEPT_FACE",FACE,{"disambiguationData":[OSD([subQ1])]}),makeQuery(id+"F4.opExtrude","SWEPT_FACE",FACE,{"disambiguationData":[OSD([subQ0])]}),makeQuery(id+"F4.opExtrude","CAP_FACE",FACE,{"disambiguationData":[OSD([subQ3,sQuery(id+"F2.wireOp",EDGE,"fcba4419-a2ee-464f-be9d-58f11bf3418b.sketch_text.stroke-0"),sQuery(id+"F2.wireOp",EDGE,"fcba4419-a2ee-464f-be9d-58f11bf3418b.sketch_text.stroke-1"),sQuery(id+"F2.wireOp",EDGE,"fcba4419-a2ee-464f-be9d-58f11bf3418b.sketch_text.stroke-2"),sQuery(id+"F2.wireOp",EDGE,"fcba4419-a2ee-464f-be9d-58f11bf3418b.sketch_text.stroke-3"),sQuery(id+"F2.wireOp",EDGE,"fcba4419-a2ee-464f-be9d-58f11bf3418b.sketch_text.stroke-4"),sQuery(id+"F2.wireOp",EDGE,"fcba4419-a2ee-464f-be9d-58f11bf3418b.sketch_text.stroke-5"),sQuery(id+"F2.wireOp",EDGE,"fcba4419-a2ee-464f-be9d-58f11bf3418b.sketch_text.stroke-6"),sQuery(id+"F2.wireOp",EDGE,"fcba4419-a2ee-464f-be9d-58f11bf3418b.sketch_text.stroke-7"),sQuery(id+"F2.wireOp",EDGE,"fcba4419-a2ee-464f-be9d-58f11bf3418b.sketch_text.stroke-8"),sQuery(id+"F2.wireOp",EDGE,"fcba4419-a2ee-464f-be9d-58f11bf3418b.sketch_text.stroke-9"),sQuery(id+"F2.wireOp",EDGE,"fcba4419-a2ee-464f-be9d-58f11bf3418b.sketch_text.stroke-10"),sQuery(id+"F2.wireOp",EDGE,"fcba4419-a2ee-464f-be9d-58f11bf3418b.sketch_text.stroke-11"),sQuery(id+"F2.wireOp",EDGE,"fcba4419-a2ee-464f-be9d-58f11bf3418b.sketch_text.stroke-12"),sQuery(id+"F2.wireOp",EDGE,"fcba4419-a2ee-464f-be9d-58f11bf3418b.sketch_text.stroke-13"),sQuery(id+"F2.wireOp",EDGE,"fcba4419-a2ee-464f-be9d-58f11bf3418b.sketch_text.stroke-14"),sQuery(id+"F2.wireOp",EDGE,"fcba4419-a2ee-464f-be9d-58f11bf3418b.sketch_text.stroke-15"),sQuery(id+"F2.wireOp",EDGE,"fcba4419-a2ee-464f-be9d-58f11bf3418b.sketch_text.stroke-16"),sQuery(id+"F2.wireOp",EDGE,"fcba4419-a2ee-464f-be9d-58f11bf3418b.sketch_text.stroke-17"),sQuery(id+"F2.wireOp",EDGE,"fcba4419-a2ee-464f-be9d-58f11bf3418b.sketch_text.stroke-18"),sQuery(id+"F2.wireOp",EDGE,"fcba4419-a2ee-464f-be9d-58f11bf3418b.sketch_text.stroke-19"),sQuery(id+"F2.wireOp",EDGE,"fcba4419-a2ee-464f-be9d-58f11bf3418b.sketch_text.stroke-20"),sQuery(id+"F2.wireOp",EDGE,"fcba4419-a2ee-464f-be9d-58f11bf3418b.sketch_text.stroke-21"),sQuery(id+"F2.wireOp",EDGE,"fcba4419-a2ee-464f-be9d-58f11bf3418b.sketch_text.stroke-22"),sQuery(id+"F2.wireOp",EDGE,"fcba4419-a2ee-464f-be9d-58f11bf3418b.sketch_text.stroke-23"),sQuery(id+"F2.wireOp",EDGE,"fcba4419-a2ee-464f-be9d-58f11bf3418b.sketch_text.stroke-24"),sQuery(id+"F2.wireOp",EDGE,"fcba4419-a2ee-464f-be9d-58f11bf3418b.sketch_text.stroke-25"),sQuery(id+"F2.wireOp",EDGE,"fcba4419-a2ee-464f-be9d-58f11bf3418b.sketch_text.stroke-26"),sQuery(id+"F2.wireOp",EDGE,"fcba4419-a2ee-464f-be9d-58f11bf3418b.sketch_text.stroke-27"),sQuery(id+"F2.wireOp",EDGE,"fcba4419-a2ee-464f-be9d-58f11bf3418b.sketch_text.stroke-28"),sQuery(id+"F2.wireOp",EDGE,"fcba4419-a2ee-464f-be9d-58f11bf3418b.sketch_text.stroke-29"),sQuery(id+"F2.wireOp",EDGE,"fcba4419-a2ee-464f-be9d-58f11bf3418b.sketch_text.stroke-30"),sQuery(id+"F2.wireOp",EDGE,"fcba4419-a2ee-464f-be9d-58f11bf3418b.sketch_text.stroke-31"),sQuery(id+"F2.wireOp",EDGE,"fcba4419-a2ee-464f-be9d-58f11bf3418b.sketch_text.stroke-32"),sQuery(id+"F2.wireOp",EDGE,"fcba4419-a2ee-464f-be9d-58f11bf3418b.sketch_text.stroke-33"),sQuery(id+"F2.wireOp",EDGE,"fcba4419-a2ee-464f-be9d-58f11bf3418b.sketch_text.stroke-34"),sQuery(id+"F2.wireOp",EDGE,"fcba4419-a2ee-464f-be9d-58f11bf3418b.sketch_text.stroke-35"),sQuery(id+"F2.wireOp",EDGE,"fcba4419-a2ee-464f-be9d-58f11bf3418b.sketch_text.stroke-36"),sQuery(id+"F2.wireOp",EDGE,"fcba4419-a2ee-464f-be9d-58f11bf3418b.sketch_text.stroke-37"),sQuery(id+"F2.wireOp",EDGE,"fcba4419-a2ee-464f-be9d-58f11bf3418b.sketch_text.stroke-38"),sQuery(id+"F2.wireOp",EDGE,"fcba4419-a2ee-464f-be9d-58f11bf3418b.sketch_text.stroke-39"),sQuery(id+"F2.wireOp",EDGE,"fcba4419-a2ee-464f-be9d-58f11bf3418b.sketch_text.stroke-40"),sQuery(id+"F2.wireOp",EDGE,"fcba4419-a2ee-464f-be9d-58f11bf3418b.sketch_text.stroke-41"),sQuery(id+"F2.wireOp",EDGE,"fcba4419-a2ee-464f-be9d-58f11bf3418b.sketch_text.stroke-42"),sQuery(id+"F2.wireOp",EDGE,"fcba4419-a2ee-464f-be9d-58f11bf3418b.sketch_text.stroke-43"),sQuery(id+"F2.wireOp",EDGE,"fcba4419-a2ee-464f-be9d-58f11bf3418b.sketch_text.stroke-44"),sQuery(id+"F2.wireOp",EDGE,"fcba4419-a2ee-464f-be9d-58f11bf3418b.sketch_text.stroke-45"),sQuery(id+"F2.wireOp",EDGE,"fcba4419-a2ee-464f-be9d-58f11bf3418b.sketch_text.stroke-46"),sQuery(id+"F2.wireOp",EDGE,"fcba4419-a2ee-464f-be9d-58f11bf3418b.sketch_text.stroke-47"),sQuery(id+"F2.wireOp",EDGE,"fcba4419-a2ee-464f-be9d-58f11bf3418b.sketch_text.stroke-48"),sQuery(id+"F2.wireOp",EDGE,"fcba4419-a2ee-464f-be9d-58f11bf3418b.sketch_text.stroke-49"),sQuery(id+"F2.wireOp",EDGE,"fcba4419-a2ee-464f-be9d-58f11bf3418b.sketch_text.stroke-50"),sQuery(id+"F2.wireOp",EDGE,"fcba4419-a2ee-464f-be9d-58f11bf3418b.sketch_text.stroke-51"),sQuery(id+"F2.wireOp",EDGE,"fcba4419-a2ee-464f-be9d-58f11bf3418b.sketch_text.stroke-52"),sQuery(id+"F2.wireOp",EDGE,"fcba4419-a2ee-464f-be9d-58f11bf3418b.sketch_text.stroke-53"),sQuery(id+"F2.wireOp",EDGE,"fcba4419-a2ee-464f-be9d-58f11bf3418b.sketch_text.stroke-54"),sQuery(id+"F2.wireOp",EDGE,"fcba4419-a2ee-464f-be9d-58f11bf3418b.sketch_text.stroke-55"),sQuery(id+"F2.wireOp",EDGE,"fcba4419-a2ee-464f-be9d-58f11bf3418b.sketch_text.stroke-56"),sQuery(id+"F2.wireOp",EDGE,"fcba4419-a2ee-464f-be9d-58f11bf3418b.sketch_text.stroke-57"),sQuery(id+"F2.wireOp",EDGE,"fcba4419-a2ee-464f-be9d-58f11bf3418b.sketch_text.stroke-58"),sQuery(id+"F2.wireOp",EDGE,"fcba4419-a2ee-464f-be9d-58f11bf3418b.sketch_text.stroke-59"),sQuery(id+"F2.wireOp",EDGE,"fcba4419-a2ee-464f-be9d-58f11bf3418b.sketch_text.stroke-60"),sQuery(id+"F2.wireOp",EDGE,"fcba4419-a2ee-464f-be9d-58f11bf3418b.sketch_text.stroke-61"),sQuery(id+"F2.wireOp",EDGE,"fcba4419-a2ee-464f-be9d-58f11bf3418b.sketch_text.stroke-62"),sQuery(id+"F2.wireOp",EDGE,"fcba4419-a2ee-464f-be9d-58f11bf3418b.sketch_text.stroke-63"),sQuery(id+"F2.wireOp",EDGE,"fcba4419-a2ee-464f-be9d-58f11bf3418b.sketch_text.stroke-64"),sQuery(id+"F2.wireOp",EDGE,"fcba4419-a2ee-464f-be9d-58f11bf3418b.sketch_text.stroke-65"),sQuery(id+"F2.wireOp",EDGE,"fcba4419-a2ee-464f-be9d-58f11bf3418b.sketch_text.stroke-66"),sQuery(id+"F2.wireOp",EDGE,"fcba4419-a2ee-464f-be9d-58f11bf3418b.sketch_text.stroke-67"),sQuery(id+"F2.wireOp",EDGE,"fcba4419-a2ee-464f-be9d-58f11bf3418b.sketch_text.stroke-68"),sQuery(id+"F2.wireOp",EDGE,"fcba4419-a2ee-464f-be9d-58f11bf3418b.sketch_text.stroke-69"),sQuery(id+"F2.wireOp",EDGE,"fcba4419-a2ee-464f-be9d-58f11bf3418b.sketch_text.stroke-70"),sQuery(id+"F2.wireOp",EDGE,"fcba4419-a2ee-464f-be9d-58f11bf3418b.sketch_text.stroke-71"),sQuery(id+"F2.wireOp",EDGE,"fcba4419-a2ee-464f-be9d-58f11bf3418b.sketch_text.stroke-72"),sQuery(id+"F2.wireOp",EDGE,"fcba4419-a2ee-464f-be9d-58f11bf3418b.sketch_text.stroke-73"),sQuery(id+"F2.wireOp",EDGE,"fcba4419-a2ee-464f-be9d-58f11bf3418b.sketch_text.stroke-74"),sQuery(id+"F2.wireOp",EDGE,"fcba4419-a2ee-464f-be9d-58f11bf3418b.sketch_text.stroke-75"),sQuery(id+"F2.wireOp",EDGE,"fcba4419-a2ee-464f-be9d-58f11bf3418b.sketch_text.stroke-76"),sQuery(id+"F2.wireOp",EDGE,"fcba4419-a2ee-464f-be9d-58f11bf3418b.sketch_text.stroke-77"),sQuery(id+"F2.wireOp",EDGE,"fcba4419-a2ee-464f-be9d-58f11bf3418b.sketch_text.stroke-78"),sQuery(id+"F2.wireOp",EDGE,"fcba4419-a2ee-464f-be9d-58f11bf3418b.sketch_text.stroke-79"),sQuery(id+"F2.wireOp",EDGE,"fcba4419-a2ee-464f-be9d-58f11bf3418b.sketch_text.stroke-80"),sQuery(id+"F2.wireOp",EDGE,"fcba4419-a2ee-464f-be9d-58f11bf3418b.sketch_text.stroke-81"),sQuery(id+"F2.wireOp",EDGE,"fcba4419-a2ee-464f-be9d-58f11bf3418b.sketch_text.stroke-82"),sQuery(id+"F2.wireOp",EDGE,"fcba4419-a2ee-464f-be9d-58f11bf3418b.sketch_text.stroke-83"),sQuery(id+"F2.wireOp",EDGE,"fcba4419-a2ee-464f-be9d-58f11bf3418b.sketch_text.stroke-84"),sQuery(id+"F2.wireOp",EDGE,"fcba4419-a2ee-464f-be9d-58f11bf3418b.sketch_text.stroke-85"),sQuery(id+"F2.wireOp",EDGE,"fcba4419-a2ee-464f-be9d-58f11bf3418b.sketch_text.stroke-86"),sQuery(id+"F2.wireOp",EDGE,"fcba4419-a2ee-464f-be9d-58f11bf3418b.sketch_text.stroke-87"),sQuery(id+"F2.wireOp",EDGE,"fcba4419-a2ee-464f-be9d-58f11bf3418b.sketch_text.stroke-88"),sQuery(id+"F2.wireOp",EDGE,"fcba4419-a2ee-464f-be9d-58f11bf3418b.sketch_text.stroke-89"),sQuery(id+"F2.wireOp",EDGE,"fcba4419-a2ee-464f-be9d-58f11bf3418b.sketch_text.stroke-90"),sQuery(id+"F2.wireOp",EDGE,"fcba4419-a2ee-464f-be9d-58f11bf3418b.sketch_text.stroke-91"),sQuery(id+"F2.wireOp",EDGE,"fcba4419-a2ee-464f-be9d-58f11bf3418b.sketch_text.stroke-92"),sQuery(id+"F2.wireOp",EDGE,"fcba4419-a2ee-464f-be9d-58f11bf3418b.sketch_text.stroke-93"),sQuery(id+"F2.wireOp",EDGE,"fcba4419-a2ee-464f-be9d-58f11bf3418b.sketch_text.stroke-94"),sQuery(id+"F2.wireOp",EDGE,"fcba4419-a2ee-464f-be9d-58f11bf3418b.sketch_text.stroke-95"),sQuery(id+"F2.wireOp",EDGE,"fcba4419-a2ee-464f-be9d-58f11bf3418b.sketch_text.stroke-96"),sQuery(id+"F2.wireOp",EDGE,"fcba4419-a2ee-464f-be9d-58f11bf3418b.sketch_text.stroke-97"),sQuery(id+"F2.wireOp",EDGE,"fcba4419-a2ee-464f-be9d-58f11bf3418b.sketch_text.stroke-98"),sQuery(id+"F2.wireOp",EDGE,"fcba4419-a2ee-464f-be9d-58f11bf3418b.sketch_text.stroke-99"),sQuery(id+"F2.wireOp",EDGE,"fcba4419-a2ee-464f-be9d-58f11bf3418b.sketch_text.stroke-100"),sQuery(id+"F2.wireOp",EDGE,"fcba4419-a2ee-464f-be9d-58f11bf3418b.sketch_text.stroke-101"),sQuery(id+"F2.wireOp",EDGE,"fcba4419-a2ee-464f-be9d-58f11bf3418b.sketch_text.stroke-102"),sQuery(id+"F2.wireOp",EDGE,"fcba4419-a2ee-464f-be9d-58f11bf3418b.sketch_text.stroke-103"),sQuery(id+"F2.wireOp",EDGE,"fcba4419-a2ee-464f-be9d-58f11bf3418b.sketch_text.stroke-104"),sQuery(id+"F2.wireOp",EDGE,"fcba4419-a2ee-464f-be9d-58f11bf3418b.sketch_text.stroke-105"),sQuery(id+"F2.wireOp",EDGE,"fcba4419-a2ee-464f-be9d-58f11bf3418b.sketch_text.stroke-106"),sQuery(id+"F2.wireOp",EDGE,"fcba4419-a2ee-464f-be9d-58f11bf3418b.sketch_text.stroke-107"),sQuery(id+"F2.wireOp",EDGE,"fcba4419-a2ee-464f-be9d-58f11bf3418b.sketch_text.stroke-108"),sQuery(id+"F2.wireOp",EDGE,"fcba4419-a2ee-464f-be9d-58f11bf3418b.sketch_text.stroke-109"),sQuery(id+"F2.wireOp",EDGE,"fcba4419-a2ee-464f-be9d-58f11bf3418b.sketch_text.stroke-110"),sQuery(id+"F2.wireOp",EDGE,"fcba4419-a2ee-464f-be9d-58f11bf3418b.sketch_text.stroke-111"),sQuery(id+"F2.wireOp",EDGE,"fcba4419-a2ee-464f-be9d-58f11bf3418b.sketch_text.stroke-112"),sQuery(id+"F2.wireOp",EDGE,"fcba4419-a2ee-464f-be9d-58f11bf3418b.sketch_text.stroke-113"),sQuery(id+"F2.wireOp",EDGE,"fcba4419-a2ee-464f-be9d-58f11bf3418b.sketch_text.stroke-114"),sQuery(id+"F2.wireOp",EDGE,"fcba4419-a2ee-464f-be9d-58f11bf3418b.sketch_text.stroke-115"),sQuery(id+"F2.wireOp",EDGE,"fcba4419-a2ee-464f-be9d-58f11bf3418b.sketch_text.stroke-116"),sQuery(id+"F2.wireOp",EDGE,"fcba4419-a2ee-464f-be9d-58f11bf3418b.sketch_text.stroke-117"),sQuery(id+"F2.wireOp",EDGE,"fcba4419-a2ee-464f-be9d-58f11bf3418b.sketch_text.stroke-118"),sQuery(id+"F2.wireOp",EDGE,"fcba4419-a2ee-464f-be9d-58f11bf3418b.sketch_text.stroke-119"),sQuery(id+"F2.wireOp",EDGE,"fcba4419-a2ee-464f-be9d-58f11bf3418b.sketch_text.stroke-120"),sQuery(id+"F2.wireOp",EDGE,"fcba4419-a2ee-464f-be9d-58f11bf3418b.sketch_text.stroke-121"),sQuery(id+"F2.wireOp",EDGE,"fcba4419-a2ee-464f-be9d-58f11bf3418b.sketch_text.stroke-122"),sQuery(id+"F2.wireOp",EDGE,"fcba4419-a2ee-464f-be9d-58f11bf3418b.sketch_text.stroke-123"),sQuery(id+"F2.wireOp",EDGE,"fcba4419-a2ee-464f-be9d-58f11bf3418b.sketch_text.stroke-124"),sQuery(id+"F2.wireOp",EDGE,"fcba4419-a2ee-464f-be9d-58f11bf3418b.sketch_text.stroke-125"),sQuery(id+"F2.wireOp",EDGE,"fcba4419-a2ee-464f-be9d-58f11bf3418b.sketch_text.stroke-126"),sQuery(id+"F2.wireOp",EDGE,"fcba4419-a2ee-464f-be9d-58f11bf3418b.sketch_text.stroke-127"),sQuery(id+"F2.wireOp",EDGE,"fcba4419-a2ee-464f-be9d-58f11bf3418b.sketch_text.stroke-128"),sQuery(id+"F2.wireOp",EDGE,"fcba4419-a2ee-464f-be9d-58f11bf3418b.sketch_text.stroke-129"),sQuery(id+"F2.wireOp",EDGE,"fcba4419-a2ee-464f-be9d-58f11bf3418b.sketch_text.stroke-130"),sQuery(id+"F2.wireOp",EDGE,"fcba4419-a2ee-464f-be9d-58f11bf3418b.sketch_text.stroke-131"),sQuery(id+"F2.wireOp",EDGE,"fcba4419-a2ee-464f-be9d-58f11bf3418b.sketch_text.stroke-132"),sQuery(id+"F2.wireOp",EDGE,"fcba4419-a2ee-464f-be9d-58f11bf3418b.sketch_text.stroke-133"),sQuery(id+"F2.wireOp",EDGE,"fcba4419-a2ee-464f-be9d-58f11bf3418b.sketch_text.stroke-134"),sQuery(id+"F2.wireOp",EDGE,"fcba4419-a2ee-464f-be9d-58f11bf3418b.sketch_text.stroke-135"),sQuery(id+"F2.wireOp",EDGE,"fcba4419-a2ee-464f-be9d-58f11bf3418b.sketch_text.stroke-136"),sQuery(id+"F2.wireOp",EDGE,"fcba4419-a2ee-464f-be9d-58f11bf3418b.sketch_text.stroke-137"),sQuery(id+"F2.wireOp",EDGE,"fcba4419-a2ee-464f-be9d-58f11bf3418b.sketch_text.stroke-138"),sQuery(id+"F2.wireOp",EDGE,"fcba4419-a2ee-464f-be9d-58f11bf3418b.sketch_text.stroke-139"),sQuery(id+"F2.wireOp",EDGE,"fcba4419-a2ee-464f-be9d-58f11bf3418b.sketch_text.stroke-140"),sQuery(id+"F2.wireOp",EDGE,"fcba4419-a2ee-464f-be9d-58f11bf3418b.sketch_text.stroke-141"),sQuery(id+"F2.wireOp",EDGE,"fcba4419-a2ee-464f-be9d-58f11bf3418b.sketch_text.stroke-142"),sQuery(id+"F2.wireOp",EDGE,"fcba4419-a2ee-464f-be9d-58f11bf3418b.sketch_text.stroke-143"),sQuery(id+"F2.wireOp",EDGE,"fcba4419-a2ee-464f-be9d-58f11bf3418b.sketch_text.stroke-144"),sQuery(id+"F2.wireOp",EDGE,"fcba4419-a2ee-464f-be9d-58f11bf3418b.sketch_text.stroke-145"),sQuery(id+"F2.wireOp",EDGE,"fcba4419-a2ee-464f-be9d-58f11bf3418b.sketch_text.stroke-146"),sQuery(id+"F2.wireOp",EDGE,"fcba4419-a2ee-464f-be9d-58f11bf3418b.sketch_text.stroke-147"),sQuery(id+"F2.wireOp",EDGE,"fcba4419-a2ee-464f-be9d-58f11bf3418b.sketch_text.stroke-148"),sQuery(id+"F2.wireOp",EDGE,"fcba4419-a2ee-464f-be9d-58f11bf3418b.sketch_text.stroke-149"),sQuery(id+"F2.wireOp",EDGE,"fcba4419-a2ee-464f-be9d-58f11bf3418b.sketch_text.stroke-150"),sQuery(id+"F2.wireOp",EDGE,"fcba4419-a2ee-464f-be9d-58f11bf3418b.sketch_text.stroke-151"),sQuery(id+"F2.wireOp",EDGE,"fcba4419-a2ee-464f-be9d-58f11bf3418b.sketch_text.stroke-152"),sQuery(id+"F2.wireOp",EDGE,"fcba4419-a2ee-464f-be9d-58f11bf3418b.sketch_text.stroke-153"),sQuery(id+"F2.wireOp",EDGE,"fcba4419-a2ee-464f-be9d-58f11bf3418b.sketch_text.stroke-154"),sQuery(id+"F2.wireOp",EDGE,"fcba4419-a2ee-464f-be9d-58f11bf3418b.sketch_text.stroke-155"),sQuery(id+"F2.wireOp",EDGE,"fcba4419-a2ee-464f-be9d-58f11bf3418b.sketch_text.stroke-156"),sQuery(id+"F2.wireOp",EDGE,"fcba4419-a2ee-464f-be9d-58f11bf3418b.sketch_text.stroke-157"),sQuery(id+"F2.wireOp",EDGE,"fcba4419-a2ee-464f-be9d-58f11bf3418b.sketch_text.stroke-158"),sQuery(id+"F2.wireOp",EDGE,"fcba4419-a2ee-464f-be9d-58f11bf3418b.sketch_text.stroke-159"),sQuery(id+"F2.wireOp",EDGE,"fcba4419-a2ee-464f-be9d-58f11bf3418b.sketch_text.stroke-160"),sQuery(id+"F2.wireOp",EDGE,"fcba4419-a2ee-464f-be9d-58f11bf3418b.sketch_text.stroke-161"),sQuery(id+"F2.wireOp",EDGE,"fcba4419-a2ee-464f-be9d-58f11bf3418b.sketch_text.stroke-162"),sQuery(id+"F2.wireOp",EDGE,"fcba4419-a2ee-464f-be9d-58f11bf3418b.sketch_text.stroke-163"),sQuery(id+"F2.wireOp",EDGE,"fcba4419-a2ee-464f-be9d-58f11bf3418b.sketch_text.stroke-164"),sQuery(id+"F2.wireOp",EDGE,"fcba4419-a2ee-464f-be9d-58f11bf3418b.sketch_text.stroke-165"),sQuery(id+"F2.wireOp",EDGE,"fcba4419-a2ee-464f-be9d-58f11bf3418b.sketch_text.stroke-166"),sQuery(id+"F2.wireOp",EDGE,"fcba4419-a2ee-464f-be9d-58f11bf3418b.sketch_text.stroke-167"),sQuery(id+"F2.wireOp",EDGE,"fcba4419-a2ee-464f-be9d-58f11bf3418b.sketch_text.stroke-168"),sQuery(id+"F2.wireOp",EDGE,"fcba4419-a2ee-464f-be9d-58f11bf3418b.sketch_text.stroke-169"),sQuery(id+"F2.wireOp",EDGE,"fcba4419-a2ee-464f-be9d-58f11bf3418b.sketch_text.stroke-170"),sQuery(id+"F2.wireOp",EDGE,"fcba4419-a2ee-464f-be9d-58f11bf3418b.sketch_text.stroke-171"),sQuery(id+"F2.wireOp",EDGE,"fcba4419-a2ee-464f-be9d-58f11bf3418b.sketch_text.stroke-172"),sQuery(id+"F2.wireOp",EDGE,"fcba4419-a2ee-464f-be9d-58f11bf3418b.sketch_text.stroke-173"),sQuery(id+"FHMxAyK4CFUKdhS_1.wireOp",EDGE,"1cb9c079-ea9b-4899-8069-e0e3048e911d.sketch_text.stroke-0"),sQuery(id+"FHMxAyK4CFUKdhS_1.wireOp",EDGE,"1cb9c079-ea9b-4899-8069-e0e3048e911d.sketch_text.stroke-1"),sQuery(id+"FHMxAyK4CFUKdhS_1.wireOp",EDGE,"1cb9c079-ea9b-4899-8069-e0e3048e911d.sketch_text.stroke-2"),sQuery(id+"FHMxAyK4CFUKdhS_1.wireOp",EDGE,"1cb9c079-ea9b-4899-8069-e0e3048e911d.sketch_text.stroke-3"),sQuery(id+"FHMxAyK4CFUKdhS_1.wireOp",EDGE,"1cb9c079-ea9b-4899-8069-e0e3048e911d.sketch_text.stroke-4"),sQuery(id+"FHMxAyK4CFUKdhS_1.wireOp",EDGE,"1cb9c079-ea9b-4899-8069-e0e3048e911d.sketch_text.stroke-5"),sQuery(id+"FHMxAyK4CFUKdhS_1.wireOp",EDGE,"1cb9c079-ea9b-4899-8069-e0e3048e911d.sketch_text.stroke-6"),sQuery(id+"FHMxAyK4CFUKdhS_1.wireOp",EDGE,"1cb9c079-ea9b-4899-8069-e0e3048e911d.sketch_text.stroke-7"),sQuery(id+"FHMxAyK4CFUKdhS_1.wireOp",EDGE,"1cb9c079-ea9b-4899-8069-e0e3048e911d.sketch_text.stroke-8"),sQuery(id+"FHMxAyK4CFUKdhS_1.wireOp",EDGE,"1cb9c079-ea9b-4899-8069-e0e3048e911d.sketch_text.stroke-9"),sQuery(id+"FHMxAyK4CFUKdhS_1.wireOp",EDGE,"1cb9c079-ea9b-4899-8069-e0e3048e911d.sketch_text.stroke-10"),sQuery(id+"FHMxAyK4CFUKdhS_1.wireOp",EDGE,"1cb9c079-ea9b-4899-8069-e0e3048e911d.sketch_text.stroke-11"),sQuery(id+"FHMxAyK4CFUKdhS_1.wireOp",EDGE,"1cb9c079-ea9b-4899-8069-e0e3048e911d.sketch_text.stroke-12"),sQuery(id+"FHMxAyK4CFUKdhS_1.wireOp",EDGE,"1cb9c079-ea9b-4899-8069-e0e3048e911d.sketch_text.stroke-13"),sQuery(id+"FHMxAyK4CFUKdhS_1.wireOp",EDGE,"1cb9c079-ea9b-4899-8069-e0e3048e911d.sketch_text.stroke-14"),sQuery(id+"FHMxAyK4CFUKdhS_1.wireOp",EDGE,"1cb9c079-ea9b-4899-8069-e0e3048e911d.sketch_text.stroke-15"),sQuery(id+"FHMxAyK4CFUKdhS_1.wireOp",EDGE,"1cb9c079-ea9b-4899-8069-e0e3048e911d.sketch_text.stroke-16"),sQuery(id+"FHMxAyK4CFUKdhS_1.wireOp",EDGE,"1cb9c079-ea9b-4899-8069-e0e3048e911d.sketch_text.stroke-17"),sQuery(id+"FHMxAyK4CFUKdhS_1.wireOp",EDGE,"1cb9c079-ea9b-4899-8069-e0e3048e911d.sketch_text.stroke-18"),sQuery(id+"FHMxAyK4CFUKdhS_1.wireOp",EDGE,"1cb9c079-ea9b-4899-8069-e0e3048e911d.sketch_text.stroke-19"),sQuery(id+"FHMxAyK4CFUKdhS_1.wireOp",EDGE,"1cb9c079-ea9b-4899-8069-e0e3048e911d.sketch_text.stroke-20"),sQuery(id+"FHMxAyK4CFUKdhS_1.wireOp",EDGE,"1cb9c079-ea9b-4899-8069-e0e3048e911d.sketch_text.stroke-21"),sQuery(id+"FHMxAyK4CFUKdhS_1.wireOp",EDGE,"1cb9c079-ea9b-4899-8069-e0e3048e911d.sketch_text.stroke-22"),sQuery(id+"FHMxAyK4CFUKdhS_1.wireOp",EDGE,"1cb9c079-ea9b-4899-8069-e0e3048e911d.sketch_text.stroke-23"),sQuery(id+"FHMxAyK4CFUKdhS_1.wireOp",EDGE,"1cb9c079-ea9b-4899-8069-e0e3048e911d.sketch_text.stroke-24"),sQuery(id+"FHMxAyK4CFUKdhS_1.wireOp",EDGE,"1cb9c079-ea9b-4899-8069-e0e3048e911d.sketch_text.stroke-25"),sQuery(id+"FHMxAyK4CFUKdhS_1.wireOp",EDGE,"1cb9c079-ea9b-4899-8069-e0e3048e911d.sketch_text.stroke-26"),sQuery(id+"FHMxAyK4CFUKdhS_1.wireOp",EDGE,"1cb9c079-ea9b-4899-8069-e0e3048e911d.sketch_text.stroke-27"),sQuery(id+"FHMxAyK4CFUKdhS_1.wireOp",EDGE,"1cb9c079-ea9b-4899-8069-e0e3048e911d.sketch_text.stroke-28"),sQuery(id+"FHMxAyK4CFUKdhS_1.wireOp",EDGE,"1cb9c079-ea9b-4899-8069-e0e3048e911d.sketch_text.stroke-29"),sQuery(id+"FHMxAyK4CFUKdhS_1.wireOp",EDGE,"1cb9c079-ea9b-4899-8069-e0e3048e911d.sketch_text.stroke-30"),sQuery(id+"FHMxAyK4CFUKdhS_1.wireOp",EDGE,"1cb9c079-ea9b-4899-8069-e0e3048e911d.sketch_text.stroke-31"),sQuery(id+"FHMxAyK4CFUKdhS_1.wireOp",EDGE,"1cb9c079-ea9b-4899-8069-e0e3048e911d.sketch_text.stroke-32"),sQuery(id+"FHMxAyK4CFUKdhS_1.wireOp",EDGE,"1cb9c079-ea9b-4899-8069-e0e3048e911d.sketch_text.stroke-33"),sQuery(id+"FHMxAyK4CFUKdhS_1.wireOp",EDGE,"1cb9c079-ea9b-4899-8069-e0e3048e911d.sketch_text.stroke-34"),sQuery(id+"FHMxAyK4CFUKdhS_1.wireOp",EDGE,"1cb9c079-ea9b-4899-8069-e0e3048e911d.sketch_text.stroke-35"),sQuery(id+"FHMxAyK4CFUKdhS_1.wireOp",EDGE,"1cb9c079-ea9b-4899-8069-e0e3048e911d.sketch_text.stroke-36"),sQuery(id+"FHMxAyK4CFUKdhS_1.wireOp",EDGE,"1cb9c079-ea9b-4899-8069-e0e3048e911d.sketch_text.stroke-37"),sQuery(id+"FHMxAyK4CFUKdhS_1.wireOp",EDGE,"1cb9c079-ea9b-4899-8069-e0e3048e911d.sketch_text.stroke-38"),sQuery(id+"FHMxAyK4CFUKdhS_1.wireOp",EDGE,"1cb9c079-ea9b-4899-8069-e0e3048e911d.sketch_text.stroke-39"),sQuery(id+"FHMxAyK4CFUKdhS_1.wireOp",EDGE,"1cb9c079-ea9b-4899-8069-e0e3048e911d.sketch_text.stroke-40"),sQuery(id+"FHMxAyK4CFUKdhS_1.wireOp",EDGE,"1cb9c079-ea9b-4899-8069-e0e3048e911d.sketch_text.stroke-41"),sQuery(id+"FHMxAyK4CFUKdhS_1.wireOp",EDGE,"1cb9c079-ea9b-4899-8069-e0e3048e911d.sketch_text.stroke-42"),sQuery(id+"FHMxAyK4CFUKdhS_1.wireOp",EDGE,"1cb9c079-ea9b-4899-8069-e0e3048e911d.sketch_text.stroke-43"),sQuery(id+"FHMxAyK4CFUKdhS_1.wireOp",EDGE,"1cb9c079-ea9b-4899-8069-e0e3048e911d.sketch_text.stroke-44"),sQuery(id+"FHMxAyK4CFUKdhS_1.wireOp",EDGE,"1cb9c079-ea9b-4899-8069-e0e3048e911d.sketch_text.stroke-45"),sQuery(id+"FHMxAyK4CFUKdhS_1.wireOp",EDGE,"1cb9c079-ea9b-4899-8069-e0e3048e911d.sketch_text.stroke-46"),sQuery(id+"FHMxAyK4CFUKdhS_1.wireOp",EDGE,"1cb9c079-ea9b-4899-8069-e0e3048e911d.sketch_text.stroke-47"),sQuery(id+"FHMxAyK4CFUKdhS_1.wireOp",EDGE,"1cb9c079-ea9b-4899-8069-e0e3048e911d.sketch_text.stroke-48"),sQuery(id+"FHMxAyK4CFUKdhS_1.wireOp",EDGE,"1cb9c079-ea9b-4899-8069-e0e3048e911d.sketch_text.stroke-49"),sQuery(id+"FHMxAyK4CFUKdhS_1.wireOp",EDGE,"1cb9c079-ea9b-4899-8069-e0e3048e911d.sketch_text.stroke-50"),sQuery(id+"FHMxAyK4CFUKdhS_1.wireOp",EDGE,"1cb9c079-ea9b-4899-8069-e0e3048e911d.sketch_text.stroke-51"),sQuery(id+"FHMxAyK4CFUKdhS_1.wireOp",EDGE,"1cb9c079-ea9b-4899-8069-e0e3048e911d.sketch_text.stroke-52"),sQuery(id+"FHMxAyK4CFUKdhS_1.wireOp",EDGE,"1cb9c079-ea9b-4899-8069-e0e3048e911d.sketch_text.stroke-53"),sQuery(id+"FHMxAyK4CFUKdhS_1.wireOp",EDGE,"1cb9c079-ea9b-4899-8069-e0e3048e911d.sketch_text.stroke-54"),sQuery(id+"FHMxAyK4CFUKdhS_1.wireOp",EDGE,"1cb9c079-ea9b-4899-8069-e0e3048e911d.sketch_text.stroke-55"),sQuery(id+"FHMxAyK4CFUKdhS_1.wireOp",EDGE,"1cb9c079-ea9b-4899-8069-e0e3048e911d.sketch_text.stroke-56"),sQuery(id+"FHMxAyK4CFUKdhS_1.wireOp",EDGE,"1cb9c079-ea9b-4899-8069-e0e3048e911d.sketch_text.stroke-57"),sQuery(id+"FHMxAyK4CFUKdhS_1.wireOp",EDGE,"1cb9c079-ea9b-4899-8069-e0e3048e911d.sketch_text.stroke-58"),sQuery(id+"FHMxAyK4CFUKdhS_1.wireOp",EDGE,"1cb9c079-ea9b-4899-8069-e0e3048e911d.sketch_text.stroke-59"),sQuery(id+"FHMxAyK4CFUKdhS_1.wireOp",EDGE,"1cb9c079-ea9b-4899-8069-e0e3048e911d.sketch_text.stroke-60"),sQuery(id+"FHMxAyK4CFUKdhS_1.wireOp",EDGE,"1cb9c079-ea9b-4899-8069-e0e3048e911d.sketch_text.stroke-61"),sQuery(id+"FHMxAyK4CFUKdhS_1.wireOp",EDGE,"1cb9c079-ea9b-4899-8069-e0e3048e911d.sketch_text.stroke-62"),sQuery(id+"FHMxAyK4CFUKdhS_1.wireOp",EDGE,"1cb9c079-ea9b-4899-8069-e0e3048e911d.sketch_text.stroke-71"),sQuery(id+"FHMxAyK4CFUKdhS_1.wireOp",EDGE,"1cb9c079-ea9b-4899-8069-e0e3048e911d.sketch_text.stroke-72"),sQuery(id+"FHMxAyK4CFUKdhS_1.wireOp",EDGE,"1cb9c079-ea9b-4899-8069-e0e3048e911d.sketch_text.stroke-73"),sQuery(id+"FHMxAyK4CFUKdhS_1.wireOp",EDGE,"1cb9c079-ea9b-4899-8069-e0e3048e911d.sketch_text.stroke-74"),sQuery(id+"FHMxAyK4CFUKdhS_1.wireOp",EDGE,"1cb9c079-ea9b-4899-8069-e0e3048e911d.sketch_text.stroke-75"),sQuery(id+"FHMxAyK4CFUKdhS_1.wireOp",EDGE,"1cb9c079-ea9b-4899-8069-e0e3048e911d.sketch_text.stroke-76"),sQuery(id+"FHMxAyK4CFUKdhS_1.wireOp",EDGE,"1cb9c079-ea9b-4899-8069-e0e3048e911d.sketch_text.stroke-77"),sQuery(id+"FHMxAyK4CFUKdhS_1.wireOp",EDGE,"1cb9c079-ea9b-4899-8069-e0e3048e911d.sketch_text.stroke-78"),sQuery(id+"FHMxAyK4CFUKdhS_1.wireOp",EDGE,"1cb9c079-ea9b-4899-8069-e0e3048e911d.sketch_text.stroke-79"),sQuery(id+"FHMxAyK4CFUKdhS_1.wireOp",EDGE,"1cb9c079-ea9b-4899-8069-e0e3048e911d.sketch_text.stroke-80"),sQuery(id+"FHMxAyK4CFUKdhS_1.wireOp",EDGE,"1cb9c079-ea9b-4899-8069-e0e3048e911d.sketch_text.stroke-81"),sQuery(id+"FHMxAyK4CFUKdhS_1.wireOp",EDGE,"1cb9c079-ea9b-4899-8069-e0e3048e911d.sketch_text.stroke-82"),sQuery(id+"FHMxAyK4CFUKdhS_1.wireOp",EDGE,"1cb9c079-ea9b-4899-8069-e0e3048e911d.sketch_text.stroke-83"),sQuery(id+"FHMxAyK4CFUKdhS_1.wireOp",EDGE,"1cb9c079-ea9b-4899-8069-e0e3048e911d.sketch_text.stroke-84"),sQuery(id+"FHMxAyK4CFUKdhS_1.wireOp",EDGE,"1cb9c079-ea9b-4899-8069-e0e3048e911d.sketch_text.stroke-85"),sQuery(id+"FHMxAyK4CFUKdhS_1.wireOp",EDGE,"1cb9c079-ea9b-4899-8069-e0e3048e911d.sketch_text.stroke-86"),sQuery(id+"FHMxAyK4CFUKdhS_1.wireOp",EDGE,"1cb9c079-ea9b-4899-8069-e0e3048e911d.sketch_text.stroke-87"),sQuery(id+"FHMxAyK4CFUKdhS_1.wireOp",EDGE,"1cb9c079-ea9b-4899-8069-e0e3048e911d.sketch_text.stroke-88"),sQuery(id+"FHMxAyK4CFUKdhS_1.wireOp",EDGE,"1cb9c079-ea9b-4899-8069-e0e3048e911d.sketch_text.stroke-89"),sQuery(id+"FHMxAyK4CFUKdhS_1.wireOp",EDGE,"1cb9c079-ea9b-4899-8069-e0e3048e911d.sketch_text.stroke-90"),sQuery(id+"FHMxAyK4CFUKdhS_1.wireOp",EDGE,"1cb9c079-ea9b-4899-8069-e0e3048e911d.sketch_text.stroke-91"),sQuery(id+"FHMxAyK4CFUKdhS_1.wireOp",EDGE,"1cb9c079-ea9b-4899-8069-e0e3048e911d.sketch_text.stroke-92"),sQuery(id+"FHMxAyK4CFUKdhS_1.wireOp",EDGE,"1cb9c079-ea9b-4899-8069-e0e3048e911d.sketch_text.stroke-93"),sQuery(id+"FHMxAyK4CFUKdhS_1.wireOp",EDGE,"1cb9c079-ea9b-4899-8069-e0e3048e911d.sketch_text.stroke-94"),sQuery(id+"FHMxAyK4CFUKdhS_1.wireOp",EDGE,"1cb9c079-ea9b-4899-8069-e0e3048e911d.sketch_text.stroke-95"),sQuery(id+"FHMxAyK4CFUKdhS_1.wireOp",EDGE,"1cb9c079-ea9b-4899-8069-e0e3048e911d.sketch_text.stroke-96"),sQuery(id+"FHMxAyK4CFUKdhS_1.wireOp",EDGE,"1cb9c079-ea9b-4899-8069-e0e3048e911d.sketch_text.stroke-97"),sQuery(id+"FHMxAyK4CFUKdhS_1.wireOp",EDGE,"1cb9c079-ea9b-4899-8069-e0e3048e911d.sketch_text.stroke-103"),sQuery(id+"FHMxAyK4CFUKdhS_1.wireOp",EDGE,"1cb9c079-ea9b-4899-8069-e0e3048e911d.sketch_text.stroke-104"),sQuery(id+"FHMxAyK4CFUKdhS_1.wireOp",EDGE,"1cb9c079-ea9b-4899-8069-e0e3048e911d.sketch_text.stroke-105"),sQuery(id+"FHMxAyK4CFUKdhS_1.wireOp",EDGE,"1cb9c079-ea9b-4899-8069-e0e3048e911d.sketch_text.stroke-106"),sQuery(id+"FHMxAyK4CFUKdhS_1.wireOp",EDGE,"1cb9c079-ea9b-4899-8069-e0e3048e911d.sketch_text.stroke-107"),sQuery(id+"FHMxAyK4CFUKdhS_1.wireOp",EDGE,"1cb9c079-ea9b-4899-8069-e0e3048e911d.sketch_text.stroke-108"),sQuery(id+"FHMxAyK4CFUKdhS_1.wireOp",EDGE,"1cb9c079-ea9b-4899-8069-e0e3048e911d.sketch_text.stroke-109"),sQuery(id+"FHMxAyK4CFUKdhS_1.wireOp",EDGE,"1cb9c079-ea9b-4899-8069-e0e3048e911d.sketch_text.stroke-110"),sQuery(id+"FHMxAyK4CFUKdhS_1.wireOp",EDGE,"1cb9c079-ea9b-4899-8069-e0e3048e911d.sketch_text.stroke-111"),sQuery(id+"FHMxAyK4CFUKdhS_1.wireOp",EDGE,"1cb9c079-ea9b-4899-8069-e0e3048e911d.sketch_text.stroke-112"),sQuery(id+"FHMxAyK4CFUKdhS_1.wireOp",EDGE,"1cb9c079-ea9b-4899-8069-e0e3048e911d.sketch_text.stroke-113"),sQuery(id+"FHMxAyK4CFUKdhS_1.wireOp",EDGE,"1cb9c079-ea9b-4899-8069-e0e3048e911d.sketch_text.stroke-114"),sQuery(id+"FHMxAyK4CFUKdhS_1.wireOp",EDGE,"1cb9c079-ea9b-4899-8069-e0e3048e911d.sketch_text.stroke-115"),sQuery(id+"FHMxAyK4CFUKdhS_1.wireOp",EDGE,"1cb9c079-ea9b-4899-8069-e0e3048e911d.sketch_text.stroke-116"),sQuery(id+"FHMxAyK4CFUKdhS_1.wireOp",EDGE,"1cb9c079-ea9b-4899-8069-e0e3048e911d.sketch_text.stroke-117"),sQuery(id+"FHMxAyK4CFUKdhS_1.wireOp",EDGE,"1cb9c079-ea9b-4899-8069-e0e3048e911d.sketch_text.stroke-118"),sQuery(id+"FHMxAyK4CFUKdhS_1.wireOp",EDGE,"1cb9c079-ea9b-4899-8069-e0e3048e911d.sketch_text.stroke-119"),sQuery(id+"FHMxAyK4CFUKdhS_1.wireOp",EDGE,"1cb9c079-ea9b-4899-8069-e0e3048e911d.sketch_text.stroke-120"),sQuery(id+"FHMxAyK4CFUKdhS_1.wireOp",EDGE,"1cb9c079-ea9b-4899-8069-e0e3048e911d.sketch_text.stroke-121"),sQuery(id+"FHMxAyK4CFUKdhS_1.wireOp",EDGE,"1cb9c079-ea9b-4899-8069-e0e3048e911d.sketch_text.stroke-122"),sQuery(id+"FHMxAyK4CFUKdhS_1.wireOp",EDGE,"1cb9c079-ea9b-4899-8069-e0e3048e911d.sketch_text.stroke-123"),sQuery(id+"FHMxAyK4CFUKdhS_1.wireOp",EDGE,"1cb9c079-ea9b-4899-8069-e0e3048e911d.sketch_text.stroke-124"),sQuery(id+"FHMxAyK4CFUKdhS_1.wireOp",EDGE,"1cb9c079-ea9b-4899-8069-e0e3048e911d.sketch_text.stroke-125"),sQuery(id+"FHMxAyK4CFUKdhS_1.wireOp",EDGE,"1cb9c079-ea9b-4899-8069-e0e3048e911d.sketch_text.stroke-126"),sQuery(id+"FHMxAyK4CFUKdhS_1.wireOp",EDGE,"1cb9c079-ea9b-4899-8069-e0e3048e911d.sketch_text.stroke-127"),sQuery(id+"FHMxAyK4CFUKdhS_1.wireOp",EDGE,"1cb9c079-ea9b-4899-8069-e0e3048e911d.sketch_text.stroke-128"),sQuery(id+"FHMxAyK4CFUKdhS_1.wireOp",EDGE,"1cb9c079-ea9b-4899-8069-e0e3048e911d.sketch_text.stroke-129"),sQuery(id+"FHMxAyK4CFUKdhS_1.wireOp",EDGE,"1cb9c079-ea9b-4899-8069-e0e3048e911d.sketch_text.stroke-130"),sQuery(id+"FHMxAyK4CFUKdhS_1.wireOp",EDGE,"1cb9c079-ea9b-4899-8069-e0e3048e911d.sketch_text.stroke-131"),sQuery(id+"FHMxAyK4CFUKdhS_1.wireOp",EDGE,"1cb9c079-ea9b-4899-8069-e0e3048e911d.sketch_text.stroke-132"),sQuery(id+"FHMxAyK4CFUKdhS_1.wireOp",EDGE,"1cb9c079-ea9b-4899-8069-e0e3048e911d.sketch_text.stroke-133"),sQuery(id+"FHMxAyK4CFUKdhS_1.wireOp",EDGE,"1cb9c079-ea9b-4899-8069-e0e3048e911d.sketch_text.stroke-134"),sQuery(id+"FHMxAyK4CFUKdhS_1.wireOp",EDGE,"1cb9c079-ea9b-4899-8069-e0e3048e911d.sketch_text.stroke-135"),sQuery(id+"FHMxAyK4CFUKdhS_1.wireOp",EDGE,"1cb9c079-ea9b-4899-8069-e0e3048e911d.sketch_text.stroke-136"),sQuery(id+"FHMxAyK4CFUKdhS_1.wireOp",EDGE,"1cb9c079-ea9b-4899-8069-e0e3048e911d.sketch_text.stroke-137"),sQuery(id+"FHMxAyK4CFUKdhS_1.wireOp",EDGE,"1cb9c079-ea9b-4899-8069-e0e3048e911d.sketch_text.stroke-138"),sQuery(id+"FHMxAyK4CFUKdhS_1.wireOp",EDGE,"1cb9c079-ea9b-4899-8069-e0e3048e911d.sketch_text.stroke-139"),sQuery(id+"FHMxAyK4CFUKdhS_1.wireOp",EDGE,"1cb9c079-ea9b-4899-8069-e0e3048e911d.sketch_text.stroke-140"),sQuery(id+"FHMxAyK4CFUKdhS_1.wireOp",EDGE,"1cb9c079-ea9b-4899-8069-e0e3048e911d.sketch_text.stroke-141"),sQuery(id+"FHMxAyK4CFUKdhS_1.wireOp",EDGE,"1cb9c079-ea9b-4899-8069-e0e3048e911d.sketch_text.stroke-142"),sQuery(id+"FHMxAyK4CFUKdhS_1.wireOp",EDGE,"1cb9c079-ea9b-4899-8069-e0e3048e911d.sketch_text.stroke-143"),sQuery(id+"FHMxAyK4CFUKdhS_1.wireOp",EDGE,"1cb9c079-ea9b-4899-8069-e0e3048e911d.sketch_text.stroke-144"),sQuery(id+"FHMxAyK4CFUKdhS_1.wireOp",EDGE,"1cb9c079-ea9b-4899-8069-e0e3048e911d.sketch_text.stroke-145"),sQuery(id+"FHMxAyK4CFUKdhS_1.wireOp",EDGE,"1cb9c079-ea9b-4899-8069-e0e3048e911d.sketch_text.stroke-146"),sQuery(id+"FHMxAyK4CFUKdhS_1.wireOp",EDGE,"1cb9c079-ea9b-4899-8069-e0e3048e911d.sketch_text.stroke-147"),sQuery(id+"FHMxAyK4CFUKdhS_1.wireOp",EDGE,"1cb9c079-ea9b-4899-8069-e0e3048e911d.sketch_text.stroke-148"),sQuery(id+"FHMxAyK4CFUKdhS_1.wireOp",EDGE,"1cb9c079-ea9b-4899-8069-e0e3048e911d.sketch_text.stroke-149"),sQuery(id+"FHMxAyK4CFUKdhS_1.wireOp",EDGE,"1cb9c079-ea9b-4899-8069-e0e3048e911d.sketch_text.stroke-150"),sQuery(id+"FHMxAyK4CFUKdhS_1.wireOp",EDGE,"1cb9c079-ea9b-4899-8069-e0e3048e911d.sketch_text.stroke-151"),sQuery(id+"FHMxAyK4CFUKdhS_1.wireOp",EDGE,"1cb9c079-ea9b-4899-8069-e0e3048e911d.sketch_text.stroke-152"),sQuery(id+"FHMxAyK4CFUKdhS_1.wireOp",EDGE,"1cb9c079-ea9b-4899-8069-e0e3048e911d.sketch_text.stroke-153"),sQuery(id+"FHMxAyK4CFUKdhS_1.wireOp",EDGE,"1cb9c079-ea9b-4899-8069-e0e3048e911d.sketch_text.stroke-159"),sQuery(id+"FHMxAyK4CFUKdhS_1.wireOp",EDGE,"1cb9c079-ea9b-4899-8069-e0e3048e911d.sketch_text.stroke-160"),sQuery(id+"FHMxAyK4CFUKdhS_1.wireOp",EDGE,"1cb9c079-ea9b-4899-8069-e0e3048e911d.sketch_text.stroke-161"),sQuery(id+"FHMxAyK4CFUKdhS_1.wireOp",EDGE,"1cb9c079-ea9b-4899-8069-e0e3048e911d.sketch_text.stroke-162"),sQuery(id+"FHMxAyK4CFUKdhS_1.wireOp",EDGE,"1cb9c079-ea9b-4899-8069-e0e3048e911d.sketch_text.stroke-163"),sQuery(id+"FHMxAyK4CFUKdhS_1.wireOp",EDGE,"1cb9c079-ea9b-4899-8069-e0e3048e911d.sketch_text.stroke-164"),sQuery(id+"FHMxAyK4CFUKdhS_1.wireOp",EDGE,"1cb9c079-ea9b-4899-8069-e0e3048e911d.sketch_text.stroke-165"),sQuery(id+"FHMxAyK4CFUKdhS_1.wireOp",EDGE,"1cb9c079-ea9b-4899-8069-e0e3048e911d.sketch_text.stroke-166"),sQuery(id+"FHMxAyK4CFUKdhS_1.wireOp",EDGE,"1cb9c079-ea9b-4899-8069-e0e3048e911d.sketch_text.stroke-167"),sQuery(id+"FHMxAyK4CFUKdhS_1.wireOp",EDGE,"1cb9c079-ea9b-4899-8069-e0e3048e911d.sketch_text.stroke-168"),sQuery(id+"FHMxAyK4CFUKdhS_1.wireOp",EDGE,"1cb9c079-ea9b-4899-8069-e0e3048e911d.sketch_text.stroke-169"),sQuery(id+"FHMxAyK4CFUKdhS_1.wireOp",EDGE,"1cb9c079-ea9b-4899-8069-e0e3048e911d.sketch_text.stroke-170"),sQuery(id+"FHMxAyK4CFUKdhS_1.wireOp",EDGE,"1cb9c079-ea9b-4899-8069-e0e3048e911d.sketch_text.stroke-171"),sQuery(id+"FHMxAyK4CFUKdhS_1.wireOp",EDGE,"1cb9c079-ea9b-4899-8069-e0e3048e911d.sketch_text.stroke-172"),sQuery(id+"FHMxAyK4CFUKdhS_1.wireOp",EDGE,"1cb9c079-ea9b-4899-8069-e0e3048e911d.sketch_text.stroke-173"),sQuery(id+"FHMxAyK4CFUKdhS_1.wireOp",EDGE,"1cb9c079-ea9b-4899-8069-e0e3048e911d.sketch_text.stroke-174"),sQuery(id+"FHMxAyK4CFUKdhS_1.wireOp",EDGE,"1cb9c079-ea9b-4899-8069-e0e3048e911d.sketch_text.stroke-175"),sQuery(id+"FHMxAyK4CFUKdhS_1.wireOp",EDGE,"1cb9c079-ea9b-4899-8069-e0e3048e911d.sketch_text.stroke-176"),sQuery(id+"FHMxAyK4CFUKdhS_1.wireOp",EDGE,"1cb9c079-ea9b-4899-8069-e0e3048e911d.sketch_text.stroke-177"),sQuery(id+"FHMxAyK4CFUKdhS_1.wireOp",EDGE,"1cb9c079-ea9b-4899-8069-e0e3048e911d.sketch_text.stroke-178"),sQuery(id+"FHMxAyK4CFUKdhS_1.wireOp",EDGE,"1cb9c079-ea9b-4899-8069-e0e3048e911d.sketch_text.stroke-179"),sQuery(id+"FHMxAyK4CFUKdhS_1.wireOp",EDGE,"1cb9c079-ea9b-4899-8069-e0e3048e911d.sketch_text.stroke-180"),subQ0,subQ2])],"isStart":true}),makeQuery(id+"F4.opExtrude","SWEPT_FACE",FACE,{"disambiguationData":[OSD([subQ2])]})])],"derivedFrom":makeQuery(id+"F4.opExtrude","CAP_EDGE",EDGE,{"disambiguationData":[OSD([subQ2])],"isStart":true})});}
            var Q23;
            {var subQ0=sQuery(id+"F0.wireOp",EDGE,"E0.top");var subQ1=sQuery(id+"F0.wireOp",EDGE,"E0.bottom");var subQ2=sQuery(id+"F3.wireOp",EDGE,"E30");Q23=makeQuery(id+"F4.boolean.opBoolean","SPLIT",EDGE,{"disambiguationData":[TD([makeQuery(id+"F1.opExtrude","CAP_FACE",FACE,{"disambiguationData":[OSD([subQ1,subQ0,sQuery(id+"F0.wireOp",EDGE,"E0.left"),sQuery(id+"F0.wireOp",EDGE,"E0.right")])],"isStart":false}),makeQuery(id+"F1.opExtrude","SWEPT_FACE",FACE,{"disambiguationData":[OSD([subQ0])]}),makeQuery(id+"F4.opExtrude","CAP_FACE",FACE,{"disambiguationData":[OSD([subQ1,sQuery(id+"F2.wireOp",EDGE,"fcba4419-a2ee-464f-be9d-58f11bf3418b.sketch_text.stroke-0"),sQuery(id+"F2.wireOp",EDGE,"fcba4419-a2ee-464f-be9d-58f11bf3418b.sketch_text.stroke-1"),sQuery(id+"F2.wireOp",EDGE,"fcba4419-a2ee-464f-be9d-58f11bf3418b.sketch_text.stroke-2"),sQuery(id+"F2.wireOp",EDGE,"fcba4419-a2ee-464f-be9d-58f11bf3418b.sketch_text.stroke-3"),sQuery(id+"F2.wireOp",EDGE,"fcba4419-a2ee-464f-be9d-58f11bf3418b.sketch_text.stroke-4"),sQuery(id+"F2.wireOp",EDGE,"fcba4419-a2ee-464f-be9d-58f11bf3418b.sketch_text.stroke-5"),sQuery(id+"F2.wireOp",EDGE,"fcba4419-a2ee-464f-be9d-58f11bf3418b.sketch_text.stroke-6"),sQuery(id+"F2.wireOp",EDGE,"fcba4419-a2ee-464f-be9d-58f11bf3418b.sketch_text.stroke-7"),sQuery(id+"F2.wireOp",EDGE,"fcba4419-a2ee-464f-be9d-58f11bf3418b.sketch_text.stroke-8"),sQuery(id+"F2.wireOp",EDGE,"fcba4419-a2ee-464f-be9d-58f11bf3418b.sketch_text.stroke-9"),sQuery(id+"F2.wireOp",EDGE,"fcba4419-a2ee-464f-be9d-58f11bf3418b.sketch_text.stroke-10"),sQuery(id+"F2.wireOp",EDGE,"fcba4419-a2ee-464f-be9d-58f11bf3418b.sketch_text.stroke-11"),sQuery(id+"F2.wireOp",EDGE,"fcba4419-a2ee-464f-be9d-58f11bf3418b.sketch_text.stroke-12"),sQuery(id+"F2.wireOp",EDGE,"fcba4419-a2ee-464f-be9d-58f11bf3418b.sketch_text.stroke-13"),sQuery(id+"F2.wireOp",EDGE,"fcba4419-a2ee-464f-be9d-58f11bf3418b.sketch_text.stroke-14"),sQuery(id+"F2.wireOp",EDGE,"fcba4419-a2ee-464f-be9d-58f11bf3418b.sketch_text.stroke-15"),sQuery(id+"F2.wireOp",EDGE,"fcba4419-a2ee-464f-be9d-58f11bf3418b.sketch_text.stroke-16"),sQuery(id+"F2.wireOp",EDGE,"fcba4419-a2ee-464f-be9d-58f11bf3418b.sketch_text.stroke-17"),sQuery(id+"F2.wireOp",EDGE,"fcba4419-a2ee-464f-be9d-58f11bf3418b.sketch_text.stroke-18"),sQuery(id+"F2.wireOp",EDGE,"fcba4419-a2ee-464f-be9d-58f11bf3418b.sketch_text.stroke-19"),sQuery(id+"F2.wireOp",EDGE,"fcba4419-a2ee-464f-be9d-58f11bf3418b.sketch_text.stroke-20"),sQuery(id+"F2.wireOp",EDGE,"fcba4419-a2ee-464f-be9d-58f11bf3418b.sketch_text.stroke-21"),sQuery(id+"F2.wireOp",EDGE,"fcba4419-a2ee-464f-be9d-58f11bf3418b.sketch_text.stroke-22"),sQuery(id+"F2.wireOp",EDGE,"fcba4419-a2ee-464f-be9d-58f11bf3418b.sketch_text.stroke-23"),sQuery(id+"F2.wireOp",EDGE,"fcba4419-a2ee-464f-be9d-58f11bf3418b.sketch_text.stroke-24"),sQuery(id+"F2.wireOp",EDGE,"fcba4419-a2ee-464f-be9d-58f11bf3418b.sketch_text.stroke-25"),sQuery(id+"F2.wireOp",EDGE,"fcba4419-a2ee-464f-be9d-58f11bf3418b.sketch_text.stroke-26"),sQuery(id+"F2.wireOp",EDGE,"fcba4419-a2ee-464f-be9d-58f11bf3418b.sketch_text.stroke-27"),sQuery(id+"F2.wireOp",EDGE,"fcba4419-a2ee-464f-be9d-58f11bf3418b.sketch_text.stroke-28"),sQuery(id+"F2.wireOp",EDGE,"fcba4419-a2ee-464f-be9d-58f11bf3418b.sketch_text.stroke-29"),sQuery(id+"F2.wireOp",EDGE,"fcba4419-a2ee-464f-be9d-58f11bf3418b.sketch_text.stroke-30"),sQuery(id+"F2.wireOp",EDGE,"fcba4419-a2ee-464f-be9d-58f11bf3418b.sketch_text.stroke-31"),sQuery(id+"F2.wireOp",EDGE,"fcba4419-a2ee-464f-be9d-58f11bf3418b.sketch_text.stroke-32"),sQuery(id+"F2.wireOp",EDGE,"fcba4419-a2ee-464f-be9d-58f11bf3418b.sketch_text.stroke-33"),sQuery(id+"F2.wireOp",EDGE,"fcba4419-a2ee-464f-be9d-58f11bf3418b.sketch_text.stroke-34"),sQuery(id+"F2.wireOp",EDGE,"fcba4419-a2ee-464f-be9d-58f11bf3418b.sketch_text.stroke-35"),sQuery(id+"F2.wireOp",EDGE,"fcba4419-a2ee-464f-be9d-58f11bf3418b.sketch_text.stroke-36"),sQuery(id+"F2.wireOp",EDGE,"fcba4419-a2ee-464f-be9d-58f11bf3418b.sketch_text.stroke-37"),sQuery(id+"F2.wireOp",EDGE,"fcba4419-a2ee-464f-be9d-58f11bf3418b.sketch_text.stroke-38"),sQuery(id+"F2.wireOp",EDGE,"fcba4419-a2ee-464f-be9d-58f11bf3418b.sketch_text.stroke-39"),sQuery(id+"F2.wireOp",EDGE,"fcba4419-a2ee-464f-be9d-58f11bf3418b.sketch_text.stroke-40"),sQuery(id+"F2.wireOp",EDGE,"fcba4419-a2ee-464f-be9d-58f11bf3418b.sketch_text.stroke-41"),sQuery(id+"F2.wireOp",EDGE,"fcba4419-a2ee-464f-be9d-58f11bf3418b.sketch_text.stroke-42"),sQuery(id+"F2.wireOp",EDGE,"fcba4419-a2ee-464f-be9d-58f11bf3418b.sketch_text.stroke-43"),sQuery(id+"F2.wireOp",EDGE,"fcba4419-a2ee-464f-be9d-58f11bf3418b.sketch_text.stroke-44"),sQuery(id+"F2.wireOp",EDGE,"fcba4419-a2ee-464f-be9d-58f11bf3418b.sketch_text.stroke-45"),sQuery(id+"F2.wireOp",EDGE,"fcba4419-a2ee-464f-be9d-58f11bf3418b.sketch_text.stroke-46"),sQuery(id+"F2.wireOp",EDGE,"fcba4419-a2ee-464f-be9d-58f11bf3418b.sketch_text.stroke-47"),sQuery(id+"F2.wireOp",EDGE,"fcba4419-a2ee-464f-be9d-58f11bf3418b.sketch_text.stroke-48"),sQuery(id+"F2.wireOp",EDGE,"fcba4419-a2ee-464f-be9d-58f11bf3418b.sketch_text.stroke-49"),sQuery(id+"F2.wireOp",EDGE,"fcba4419-a2ee-464f-be9d-58f11bf3418b.sketch_text.stroke-50"),sQuery(id+"F2.wireOp",EDGE,"fcba4419-a2ee-464f-be9d-58f11bf3418b.sketch_text.stroke-51"),sQuery(id+"F2.wireOp",EDGE,"fcba4419-a2ee-464f-be9d-58f11bf3418b.sketch_text.stroke-52"),sQuery(id+"F2.wireOp",EDGE,"fcba4419-a2ee-464f-be9d-58f11bf3418b.sketch_text.stroke-53"),sQuery(id+"F2.wireOp",EDGE,"fcba4419-a2ee-464f-be9d-58f11bf3418b.sketch_text.stroke-54"),sQuery(id+"F2.wireOp",EDGE,"fcba4419-a2ee-464f-be9d-58f11bf3418b.sketch_text.stroke-55"),sQuery(id+"F2.wireOp",EDGE,"fcba4419-a2ee-464f-be9d-58f11bf3418b.sketch_text.stroke-56"),sQuery(id+"F2.wireOp",EDGE,"fcba4419-a2ee-464f-be9d-58f11bf3418b.sketch_text.stroke-57"),sQuery(id+"F2.wireOp",EDGE,"fcba4419-a2ee-464f-be9d-58f11bf3418b.sketch_text.stroke-58"),sQuery(id+"F2.wireOp",EDGE,"fcba4419-a2ee-464f-be9d-58f11bf3418b.sketch_text.stroke-59"),sQuery(id+"F2.wireOp",EDGE,"fcba4419-a2ee-464f-be9d-58f11bf3418b.sketch_text.stroke-60"),sQuery(id+"F2.wireOp",EDGE,"fcba4419-a2ee-464f-be9d-58f11bf3418b.sketch_text.stroke-61"),sQuery(id+"F2.wireOp",EDGE,"fcba4419-a2ee-464f-be9d-58f11bf3418b.sketch_text.stroke-62"),sQuery(id+"F2.wireOp",EDGE,"fcba4419-a2ee-464f-be9d-58f11bf3418b.sketch_text.stroke-63"),sQuery(id+"F2.wireOp",EDGE,"fcba4419-a2ee-464f-be9d-58f11bf3418b.sketch_text.stroke-64"),sQuery(id+"F2.wireOp",EDGE,"fcba4419-a2ee-464f-be9d-58f11bf3418b.sketch_text.stroke-65"),sQuery(id+"F2.wireOp",EDGE,"fcba4419-a2ee-464f-be9d-58f11bf3418b.sketch_text.stroke-66"),sQuery(id+"F2.wireOp",EDGE,"fcba4419-a2ee-464f-be9d-58f11bf3418b.sketch_text.stroke-67"),sQuery(id+"F2.wireOp",EDGE,"fcba4419-a2ee-464f-be9d-58f11bf3418b.sketch_text.stroke-68"),sQuery(id+"F2.wireOp",EDGE,"fcba4419-a2ee-464f-be9d-58f11bf3418b.sketch_text.stroke-69"),sQuery(id+"F2.wireOp",EDGE,"fcba4419-a2ee-464f-be9d-58f11bf3418b.sketch_text.stroke-70"),sQuery(id+"F2.wireOp",EDGE,"fcba4419-a2ee-464f-be9d-58f11bf3418b.sketch_text.stroke-71"),sQuery(id+"F2.wireOp",EDGE,"fcba4419-a2ee-464f-be9d-58f11bf3418b.sketch_text.stroke-72"),sQuery(id+"F2.wireOp",EDGE,"fcba4419-a2ee-464f-be9d-58f11bf3418b.sketch_text.stroke-73"),sQuery(id+"F2.wireOp",EDGE,"fcba4419-a2ee-464f-be9d-58f11bf3418b.sketch_text.stroke-74"),sQuery(id+"F2.wireOp",EDGE,"fcba4419-a2ee-464f-be9d-58f11bf3418b.sketch_text.stroke-75"),sQuery(id+"F2.wireOp",EDGE,"fcba4419-a2ee-464f-be9d-58f11bf3418b.sketch_text.stroke-76"),sQuery(id+"F2.wireOp",EDGE,"fcba4419-a2ee-464f-be9d-58f11bf3418b.sketch_text.stroke-77"),sQuery(id+"F2.wireOp",EDGE,"fcba4419-a2ee-464f-be9d-58f11bf3418b.sketch_text.stroke-78"),sQuery(id+"F2.wireOp",EDGE,"fcba4419-a2ee-464f-be9d-58f11bf3418b.sketch_text.stroke-79"),sQuery(id+"F2.wireOp",EDGE,"fcba4419-a2ee-464f-be9d-58f11bf3418b.sketch_text.stroke-80"),sQuery(id+"F2.wireOp",EDGE,"fcba4419-a2ee-464f-be9d-58f11bf3418b.sketch_text.stroke-81"),sQuery(id+"F2.wireOp",EDGE,"fcba4419-a2ee-464f-be9d-58f11bf3418b.sketch_text.stroke-82"),sQuery(id+"F2.wireOp",EDGE,"fcba4419-a2ee-464f-be9d-58f11bf3418b.sketch_text.stroke-83"),sQuery(id+"F2.wireOp",EDGE,"fcba4419-a2ee-464f-be9d-58f11bf3418b.sketch_text.stroke-84"),sQuery(id+"F2.wireOp",EDGE,"fcba4419-a2ee-464f-be9d-58f11bf3418b.sketch_text.stroke-85"),sQuery(id+"F2.wireOp",EDGE,"fcba4419-a2ee-464f-be9d-58f11bf3418b.sketch_text.stroke-86"),sQuery(id+"F2.wireOp",EDGE,"fcba4419-a2ee-464f-be9d-58f11bf3418b.sketch_text.stroke-87"),sQuery(id+"F2.wireOp",EDGE,"fcba4419-a2ee-464f-be9d-58f11bf3418b.sketch_text.stroke-88"),sQuery(id+"F2.wireOp",EDGE,"fcba4419-a2ee-464f-be9d-58f11bf3418b.sketch_text.stroke-89"),sQuery(id+"F2.wireOp",EDGE,"fcba4419-a2ee-464f-be9d-58f11bf3418b.sketch_text.stroke-90"),sQuery(id+"F2.wireOp",EDGE,"fcba4419-a2ee-464f-be9d-58f11bf3418b.sketch_text.stroke-91"),sQuery(id+"F2.wireOp",EDGE,"fcba4419-a2ee-464f-be9d-58f11bf3418b.sketch_text.stroke-92"),sQuery(id+"F2.wireOp",EDGE,"fcba4419-a2ee-464f-be9d-58f11bf3418b.sketch_text.stroke-93"),sQuery(id+"F2.wireOp",EDGE,"fcba4419-a2ee-464f-be9d-58f11bf3418b.sketch_text.stroke-94"),sQuery(id+"F2.wireOp",EDGE,"fcba4419-a2ee-464f-be9d-58f11bf3418b.sketch_text.stroke-95"),sQuery(id+"F2.wireOp",EDGE,"fcba4419-a2ee-464f-be9d-58f11bf3418b.sketch_text.stroke-96"),sQuery(id+"F2.wireOp",EDGE,"fcba4419-a2ee-464f-be9d-58f11bf3418b.sketch_text.stroke-97"),sQuery(id+"F2.wireOp",EDGE,"fcba4419-a2ee-464f-be9d-58f11bf3418b.sketch_text.stroke-98"),sQuery(id+"F2.wireOp",EDGE,"fcba4419-a2ee-464f-be9d-58f11bf3418b.sketch_text.stroke-99"),sQuery(id+"F2.wireOp",EDGE,"fcba4419-a2ee-464f-be9d-58f11bf3418b.sketch_text.stroke-100"),sQuery(id+"F2.wireOp",EDGE,"fcba4419-a2ee-464f-be9d-58f11bf3418b.sketch_text.stroke-101"),sQuery(id+"F2.wireOp",EDGE,"fcba4419-a2ee-464f-be9d-58f11bf3418b.sketch_text.stroke-102"),sQuery(id+"F2.wireOp",EDGE,"fcba4419-a2ee-464f-be9d-58f11bf3418b.sketch_text.stroke-103"),sQuery(id+"F2.wireOp",EDGE,"fcba4419-a2ee-464f-be9d-58f11bf3418b.sketch_text.stroke-104"),sQuery(id+"F2.wireOp",EDGE,"fcba4419-a2ee-464f-be9d-58f11bf3418b.sketch_text.stroke-105"),sQuery(id+"F2.wireOp",EDGE,"fcba4419-a2ee-464f-be9d-58f11bf3418b.sketch_text.stroke-106"),sQuery(id+"F2.wireOp",EDGE,"fcba4419-a2ee-464f-be9d-58f11bf3418b.sketch_text.stroke-107"),sQuery(id+"F2.wireOp",EDGE,"fcba4419-a2ee-464f-be9d-58f11bf3418b.sketch_text.stroke-108"),sQuery(id+"F2.wireOp",EDGE,"fcba4419-a2ee-464f-be9d-58f11bf3418b.sketch_text.stroke-109"),sQuery(id+"F2.wireOp",EDGE,"fcba4419-a2ee-464f-be9d-58f11bf3418b.sketch_text.stroke-110"),sQuery(id+"F2.wireOp",EDGE,"fcba4419-a2ee-464f-be9d-58f11bf3418b.sketch_text.stroke-111"),sQuery(id+"F2.wireOp",EDGE,"fcba4419-a2ee-464f-be9d-58f11bf3418b.sketch_text.stroke-112"),sQuery(id+"F2.wireOp",EDGE,"fcba4419-a2ee-464f-be9d-58f11bf3418b.sketch_text.stroke-113"),sQuery(id+"F2.wireOp",EDGE,"fcba4419-a2ee-464f-be9d-58f11bf3418b.sketch_text.stroke-114"),sQuery(id+"F2.wireOp",EDGE,"fcba4419-a2ee-464f-be9d-58f11bf3418b.sketch_text.stroke-115"),sQuery(id+"F2.wireOp",EDGE,"fcba4419-a2ee-464f-be9d-58f11bf3418b.sketch_text.stroke-116"),sQuery(id+"F2.wireOp",EDGE,"fcba4419-a2ee-464f-be9d-58f11bf3418b.sketch_text.stroke-117"),sQuery(id+"F2.wireOp",EDGE,"fcba4419-a2ee-464f-be9d-58f11bf3418b.sketch_text.stroke-118"),sQuery(id+"F2.wireOp",EDGE,"fcba4419-a2ee-464f-be9d-58f11bf3418b.sketch_text.stroke-119"),sQuery(id+"F2.wireOp",EDGE,"fcba4419-a2ee-464f-be9d-58f11bf3418b.sketch_text.stroke-120"),sQuery(id+"F2.wireOp",EDGE,"fcba4419-a2ee-464f-be9d-58f11bf3418b.sketch_text.stroke-121"),sQuery(id+"F2.wireOp",EDGE,"fcba4419-a2ee-464f-be9d-58f11bf3418b.sketch_text.stroke-122"),sQuery(id+"F2.wireOp",EDGE,"fcba4419-a2ee-464f-be9d-58f11bf3418b.sketch_text.stroke-123"),sQuery(id+"F2.wireOp",EDGE,"fcba4419-a2ee-464f-be9d-58f11bf3418b.sketch_text.stroke-124"),sQuery(id+"F2.wireOp",EDGE,"fcba4419-a2ee-464f-be9d-58f11bf3418b.sketch_text.stroke-125"),sQuery(id+"F2.wireOp",EDGE,"fcba4419-a2ee-464f-be9d-58f11bf3418b.sketch_text.stroke-126"),sQuery(id+"F2.wireOp",EDGE,"fcba4419-a2ee-464f-be9d-58f11bf3418b.sketch_text.stroke-127"),sQuery(id+"F2.wireOp",EDGE,"fcba4419-a2ee-464f-be9d-58f11bf3418b.sketch_text.stroke-128"),sQuery(id+"F2.wireOp",EDGE,"fcba4419-a2ee-464f-be9d-58f11bf3418b.sketch_text.stroke-129"),sQuery(id+"F2.wireOp",EDGE,"fcba4419-a2ee-464f-be9d-58f11bf3418b.sketch_text.stroke-130"),sQuery(id+"F2.wireOp",EDGE,"fcba4419-a2ee-464f-be9d-58f11bf3418b.sketch_text.stroke-131"),sQuery(id+"F2.wireOp",EDGE,"fcba4419-a2ee-464f-be9d-58f11bf3418b.sketch_text.stroke-132"),sQuery(id+"F2.wireOp",EDGE,"fcba4419-a2ee-464f-be9d-58f11bf3418b.sketch_text.stroke-133"),sQuery(id+"F2.wireOp",EDGE,"fcba4419-a2ee-464f-be9d-58f11bf3418b.sketch_text.stroke-134"),sQuery(id+"F2.wireOp",EDGE,"fcba4419-a2ee-464f-be9d-58f11bf3418b.sketch_text.stroke-135"),sQuery(id+"F2.wireOp",EDGE,"fcba4419-a2ee-464f-be9d-58f11bf3418b.sketch_text.stroke-136"),sQuery(id+"F2.wireOp",EDGE,"fcba4419-a2ee-464f-be9d-58f11bf3418b.sketch_text.stroke-137"),sQuery(id+"F2.wireOp",EDGE,"fcba4419-a2ee-464f-be9d-58f11bf3418b.sketch_text.stroke-138"),sQuery(id+"F2.wireOp",EDGE,"fcba4419-a2ee-464f-be9d-58f11bf3418b.sketch_text.stroke-139"),sQuery(id+"F2.wireOp",EDGE,"fcba4419-a2ee-464f-be9d-58f11bf3418b.sketch_text.stroke-140"),sQuery(id+"F2.wireOp",EDGE,"fcba4419-a2ee-464f-be9d-58f11bf3418b.sketch_text.stroke-141"),sQuery(id+"F2.wireOp",EDGE,"fcba4419-a2ee-464f-be9d-58f11bf3418b.sketch_text.stroke-142"),sQuery(id+"F2.wireOp",EDGE,"fcba4419-a2ee-464f-be9d-58f11bf3418b.sketch_text.stroke-143"),sQuery(id+"F2.wireOp",EDGE,"fcba4419-a2ee-464f-be9d-58f11bf3418b.sketch_text.stroke-144"),sQuery(id+"F2.wireOp",EDGE,"fcba4419-a2ee-464f-be9d-58f11bf3418b.sketch_text.stroke-145"),sQuery(id+"F2.wireOp",EDGE,"fcba4419-a2ee-464f-be9d-58f11bf3418b.sketch_text.stroke-146"),sQuery(id+"F2.wireOp",EDGE,"fcba4419-a2ee-464f-be9d-58f11bf3418b.sketch_text.stroke-147"),sQuery(id+"F2.wireOp",EDGE,"fcba4419-a2ee-464f-be9d-58f11bf3418b.sketch_text.stroke-148"),sQuery(id+"F2.wireOp",EDGE,"fcba4419-a2ee-464f-be9d-58f11bf3418b.sketch_text.stroke-149"),sQuery(id+"F2.wireOp",EDGE,"fcba4419-a2ee-464f-be9d-58f11bf3418b.sketch_text.stroke-150"),sQuery(id+"F2.wireOp",EDGE,"fcba4419-a2ee-464f-be9d-58f11bf3418b.sketch_text.stroke-151"),sQuery(id+"F2.wireOp",EDGE,"fcba4419-a2ee-464f-be9d-58f11bf3418b.sketch_text.stroke-152"),sQuery(id+"F2.wireOp",EDGE,"fcba4419-a2ee-464f-be9d-58f11bf3418b.sketch_text.stroke-153"),sQuery(id+"F2.wireOp",EDGE,"fcba4419-a2ee-464f-be9d-58f11bf3418b.sketch_text.stroke-154"),sQuery(id+"F2.wireOp",EDGE,"fcba4419-a2ee-464f-be9d-58f11bf3418b.sketch_text.stroke-155"),sQuery(id+"F2.wireOp",EDGE,"fcba4419-a2ee-464f-be9d-58f11bf3418b.sketch_text.stroke-156"),sQuery(id+"F2.wireOp",EDGE,"fcba4419-a2ee-464f-be9d-58f11bf3418b.sketch_text.stroke-157"),sQuery(id+"F2.wireOp",EDGE,"fcba4419-a2ee-464f-be9d-58f11bf3418b.sketch_text.stroke-158"),sQuery(id+"F2.wireOp",EDGE,"fcba4419-a2ee-464f-be9d-58f11bf3418b.sketch_text.stroke-159"),sQuery(id+"F2.wireOp",EDGE,"fcba4419-a2ee-464f-be9d-58f11bf3418b.sketch_text.stroke-160"),sQuery(id+"F2.wireOp",EDGE,"fcba4419-a2ee-464f-be9d-58f11bf3418b.sketch_text.stroke-161"),sQuery(id+"F2.wireOp",EDGE,"fcba4419-a2ee-464f-be9d-58f11bf3418b.sketch_text.stroke-162"),sQuery(id+"F2.wireOp",EDGE,"fcba4419-a2ee-464f-be9d-58f11bf3418b.sketch_text.stroke-163"),sQuery(id+"F2.wireOp",EDGE,"fcba4419-a2ee-464f-be9d-58f11bf3418b.sketch_text.stroke-164"),sQuery(id+"F2.wireOp",EDGE,"fcba4419-a2ee-464f-be9d-58f11bf3418b.sketch_text.stroke-165"),sQuery(id+"F2.wireOp",EDGE,"fcba4419-a2ee-464f-be9d-58f11bf3418b.sketch_text.stroke-166"),sQuery(id+"F2.wireOp",EDGE,"fcba4419-a2ee-464f-be9d-58f11bf3418b.sketch_text.stroke-167"),sQuery(id+"F2.wireOp",EDGE,"fcba4419-a2ee-464f-be9d-58f11bf3418b.sketch_text.stroke-168"),sQuery(id+"F2.wireOp",EDGE,"fcba4419-a2ee-464f-be9d-58f11bf3418b.sketch_text.stroke-169"),sQuery(id+"F2.wireOp",EDGE,"fcba4419-a2ee-464f-be9d-58f11bf3418b.sketch_text.stroke-170"),sQuery(id+"F2.wireOp",EDGE,"fcba4419-a2ee-464f-be9d-58f11bf3418b.sketch_text.stroke-171"),sQuery(id+"F2.wireOp",EDGE,"fcba4419-a2ee-464f-be9d-58f11bf3418b.sketch_text.stroke-172"),sQuery(id+"F2.wireOp",EDGE,"fcba4419-a2ee-464f-be9d-58f11bf3418b.sketch_text.stroke-173"),sQuery(id+"FHMxAyK4CFUKdhS_1.wireOp",EDGE,"1cb9c079-ea9b-4899-8069-e0e3048e911d.sketch_text.stroke-0"),sQuery(id+"FHMxAyK4CFUKdhS_1.wireOp",EDGE,"1cb9c079-ea9b-4899-8069-e0e3048e911d.sketch_text.stroke-1"),sQuery(id+"FHMxAyK4CFUKdhS_1.wireOp",EDGE,"1cb9c079-ea9b-4899-8069-e0e3048e911d.sketch_text.stroke-2"),sQuery(id+"FHMxAyK4CFUKdhS_1.wireOp",EDGE,"1cb9c079-ea9b-4899-8069-e0e3048e911d.sketch_text.stroke-3"),sQuery(id+"FHMxAyK4CFUKdhS_1.wireOp",EDGE,"1cb9c079-ea9b-4899-8069-e0e3048e911d.sketch_text.stroke-4"),sQuery(id+"FHMxAyK4CFUKdhS_1.wireOp",EDGE,"1cb9c079-ea9b-4899-8069-e0e3048e911d.sketch_text.stroke-5"),sQuery(id+"FHMxAyK4CFUKdhS_1.wireOp",EDGE,"1cb9c079-ea9b-4899-8069-e0e3048e911d.sketch_text.stroke-6"),sQuery(id+"FHMxAyK4CFUKdhS_1.wireOp",EDGE,"1cb9c079-ea9b-4899-8069-e0e3048e911d.sketch_text.stroke-7"),sQuery(id+"FHMxAyK4CFUKdhS_1.wireOp",EDGE,"1cb9c079-ea9b-4899-8069-e0e3048e911d.sketch_text.stroke-8"),sQuery(id+"FHMxAyK4CFUKdhS_1.wireOp",EDGE,"1cb9c079-ea9b-4899-8069-e0e3048e911d.sketch_text.stroke-9"),sQuery(id+"FHMxAyK4CFUKdhS_1.wireOp",EDGE,"1cb9c079-ea9b-4899-8069-e0e3048e911d.sketch_text.stroke-10"),sQuery(id+"FHMxAyK4CFUKdhS_1.wireOp",EDGE,"1cb9c079-ea9b-4899-8069-e0e3048e911d.sketch_text.stroke-11"),sQuery(id+"FHMxAyK4CFUKdhS_1.wireOp",EDGE,"1cb9c079-ea9b-4899-8069-e0e3048e911d.sketch_text.stroke-12"),sQuery(id+"FHMxAyK4CFUKdhS_1.wireOp",EDGE,"1cb9c079-ea9b-4899-8069-e0e3048e911d.sketch_text.stroke-13"),sQuery(id+"FHMxAyK4CFUKdhS_1.wireOp",EDGE,"1cb9c079-ea9b-4899-8069-e0e3048e911d.sketch_text.stroke-14"),sQuery(id+"FHMxAyK4CFUKdhS_1.wireOp",EDGE,"1cb9c079-ea9b-4899-8069-e0e3048e911d.sketch_text.stroke-15"),sQuery(id+"FHMxAyK4CFUKdhS_1.wireOp",EDGE,"1cb9c079-ea9b-4899-8069-e0e3048e911d.sketch_text.stroke-16"),sQuery(id+"FHMxAyK4CFUKdhS_1.wireOp",EDGE,"1cb9c079-ea9b-4899-8069-e0e3048e911d.sketch_text.stroke-17"),sQuery(id+"FHMxAyK4CFUKdhS_1.wireOp",EDGE,"1cb9c079-ea9b-4899-8069-e0e3048e911d.sketch_text.stroke-18"),sQuery(id+"FHMxAyK4CFUKdhS_1.wireOp",EDGE,"1cb9c079-ea9b-4899-8069-e0e3048e911d.sketch_text.stroke-19"),sQuery(id+"FHMxAyK4CFUKdhS_1.wireOp",EDGE,"1cb9c079-ea9b-4899-8069-e0e3048e911d.sketch_text.stroke-20"),sQuery(id+"FHMxAyK4CFUKdhS_1.wireOp",EDGE,"1cb9c079-ea9b-4899-8069-e0e3048e911d.sketch_text.stroke-21"),sQuery(id+"FHMxAyK4CFUKdhS_1.wireOp",EDGE,"1cb9c079-ea9b-4899-8069-e0e3048e911d.sketch_text.stroke-22"),sQuery(id+"FHMxAyK4CFUKdhS_1.wireOp",EDGE,"1cb9c079-ea9b-4899-8069-e0e3048e911d.sketch_text.stroke-23"),sQuery(id+"FHMxAyK4CFUKdhS_1.wireOp",EDGE,"1cb9c079-ea9b-4899-8069-e0e3048e911d.sketch_text.stroke-24"),sQuery(id+"FHMxAyK4CFUKdhS_1.wireOp",EDGE,"1cb9c079-ea9b-4899-8069-e0e3048e911d.sketch_text.stroke-25"),sQuery(id+"FHMxAyK4CFUKdhS_1.wireOp",EDGE,"1cb9c079-ea9b-4899-8069-e0e3048e911d.sketch_text.stroke-26"),sQuery(id+"FHMxAyK4CFUKdhS_1.wireOp",EDGE,"1cb9c079-ea9b-4899-8069-e0e3048e911d.sketch_text.stroke-27"),sQuery(id+"FHMxAyK4CFUKdhS_1.wireOp",EDGE,"1cb9c079-ea9b-4899-8069-e0e3048e911d.sketch_text.stroke-28"),sQuery(id+"FHMxAyK4CFUKdhS_1.wireOp",EDGE,"1cb9c079-ea9b-4899-8069-e0e3048e911d.sketch_text.stroke-29"),sQuery(id+"FHMxAyK4CFUKdhS_1.wireOp",EDGE,"1cb9c079-ea9b-4899-8069-e0e3048e911d.sketch_text.stroke-30"),sQuery(id+"FHMxAyK4CFUKdhS_1.wireOp",EDGE,"1cb9c079-ea9b-4899-8069-e0e3048e911d.sketch_text.stroke-31"),sQuery(id+"FHMxAyK4CFUKdhS_1.wireOp",EDGE,"1cb9c079-ea9b-4899-8069-e0e3048e911d.sketch_text.stroke-32"),sQuery(id+"FHMxAyK4CFUKdhS_1.wireOp",EDGE,"1cb9c079-ea9b-4899-8069-e0e3048e911d.sketch_text.stroke-33"),sQuery(id+"FHMxAyK4CFUKdhS_1.wireOp",EDGE,"1cb9c079-ea9b-4899-8069-e0e3048e911d.sketch_text.stroke-34"),sQuery(id+"FHMxAyK4CFUKdhS_1.wireOp",EDGE,"1cb9c079-ea9b-4899-8069-e0e3048e911d.sketch_text.stroke-35"),sQuery(id+"FHMxAyK4CFUKdhS_1.wireOp",EDGE,"1cb9c079-ea9b-4899-8069-e0e3048e911d.sketch_text.stroke-36"),sQuery(id+"FHMxAyK4CFUKdhS_1.wireOp",EDGE,"1cb9c079-ea9b-4899-8069-e0e3048e911d.sketch_text.stroke-37"),sQuery(id+"FHMxAyK4CFUKdhS_1.wireOp",EDGE,"1cb9c079-ea9b-4899-8069-e0e3048e911d.sketch_text.stroke-38"),sQuery(id+"FHMxAyK4CFUKdhS_1.wireOp",EDGE,"1cb9c079-ea9b-4899-8069-e0e3048e911d.sketch_text.stroke-39"),sQuery(id+"FHMxAyK4CFUKdhS_1.wireOp",EDGE,"1cb9c079-ea9b-4899-8069-e0e3048e911d.sketch_text.stroke-40"),sQuery(id+"FHMxAyK4CFUKdhS_1.wireOp",EDGE,"1cb9c079-ea9b-4899-8069-e0e3048e911d.sketch_text.stroke-41"),sQuery(id+"FHMxAyK4CFUKdhS_1.wireOp",EDGE,"1cb9c079-ea9b-4899-8069-e0e3048e911d.sketch_text.stroke-42"),sQuery(id+"FHMxAyK4CFUKdhS_1.wireOp",EDGE,"1cb9c079-ea9b-4899-8069-e0e3048e911d.sketch_text.stroke-43"),sQuery(id+"FHMxAyK4CFUKdhS_1.wireOp",EDGE,"1cb9c079-ea9b-4899-8069-e0e3048e911d.sketch_text.stroke-44"),sQuery(id+"FHMxAyK4CFUKdhS_1.wireOp",EDGE,"1cb9c079-ea9b-4899-8069-e0e3048e911d.sketch_text.stroke-45"),sQuery(id+"FHMxAyK4CFUKdhS_1.wireOp",EDGE,"1cb9c079-ea9b-4899-8069-e0e3048e911d.sketch_text.stroke-46"),sQuery(id+"FHMxAyK4CFUKdhS_1.wireOp",EDGE,"1cb9c079-ea9b-4899-8069-e0e3048e911d.sketch_text.stroke-47"),sQuery(id+"FHMxAyK4CFUKdhS_1.wireOp",EDGE,"1cb9c079-ea9b-4899-8069-e0e3048e911d.sketch_text.stroke-48"),sQuery(id+"FHMxAyK4CFUKdhS_1.wireOp",EDGE,"1cb9c079-ea9b-4899-8069-e0e3048e911d.sketch_text.stroke-49"),sQuery(id+"FHMxAyK4CFUKdhS_1.wireOp",EDGE,"1cb9c079-ea9b-4899-8069-e0e3048e911d.sketch_text.stroke-50"),sQuery(id+"FHMxAyK4CFUKdhS_1.wireOp",EDGE,"1cb9c079-ea9b-4899-8069-e0e3048e911d.sketch_text.stroke-51"),sQuery(id+"FHMxAyK4CFUKdhS_1.wireOp",EDGE,"1cb9c079-ea9b-4899-8069-e0e3048e911d.sketch_text.stroke-52"),sQuery(id+"FHMxAyK4CFUKdhS_1.wireOp",EDGE,"1cb9c079-ea9b-4899-8069-e0e3048e911d.sketch_text.stroke-53"),sQuery(id+"FHMxAyK4CFUKdhS_1.wireOp",EDGE,"1cb9c079-ea9b-4899-8069-e0e3048e911d.sketch_text.stroke-54"),sQuery(id+"FHMxAyK4CFUKdhS_1.wireOp",EDGE,"1cb9c079-ea9b-4899-8069-e0e3048e911d.sketch_text.stroke-55"),sQuery(id+"FHMxAyK4CFUKdhS_1.wireOp",EDGE,"1cb9c079-ea9b-4899-8069-e0e3048e911d.sketch_text.stroke-56"),sQuery(id+"FHMxAyK4CFUKdhS_1.wireOp",EDGE,"1cb9c079-ea9b-4899-8069-e0e3048e911d.sketch_text.stroke-57"),sQuery(id+"FHMxAyK4CFUKdhS_1.wireOp",EDGE,"1cb9c079-ea9b-4899-8069-e0e3048e911d.sketch_text.stroke-58"),sQuery(id+"FHMxAyK4CFUKdhS_1.wireOp",EDGE,"1cb9c079-ea9b-4899-8069-e0e3048e911d.sketch_text.stroke-59"),sQuery(id+"FHMxAyK4CFUKdhS_1.wireOp",EDGE,"1cb9c079-ea9b-4899-8069-e0e3048e911d.sketch_text.stroke-60"),sQuery(id+"FHMxAyK4CFUKdhS_1.wireOp",EDGE,"1cb9c079-ea9b-4899-8069-e0e3048e911d.sketch_text.stroke-61"),sQuery(id+"FHMxAyK4CFUKdhS_1.wireOp",EDGE,"1cb9c079-ea9b-4899-8069-e0e3048e911d.sketch_text.stroke-62"),sQuery(id+"FHMxAyK4CFUKdhS_1.wireOp",EDGE,"1cb9c079-ea9b-4899-8069-e0e3048e911d.sketch_text.stroke-71"),sQuery(id+"FHMxAyK4CFUKdhS_1.wireOp",EDGE,"1cb9c079-ea9b-4899-8069-e0e3048e911d.sketch_text.stroke-72"),sQuery(id+"FHMxAyK4CFUKdhS_1.wireOp",EDGE,"1cb9c079-ea9b-4899-8069-e0e3048e911d.sketch_text.stroke-73"),sQuery(id+"FHMxAyK4CFUKdhS_1.wireOp",EDGE,"1cb9c079-ea9b-4899-8069-e0e3048e911d.sketch_text.stroke-74"),sQuery(id+"FHMxAyK4CFUKdhS_1.wireOp",EDGE,"1cb9c079-ea9b-4899-8069-e0e3048e911d.sketch_text.stroke-75"),sQuery(id+"FHMxAyK4CFUKdhS_1.wireOp",EDGE,"1cb9c079-ea9b-4899-8069-e0e3048e911d.sketch_text.stroke-76"),sQuery(id+"FHMxAyK4CFUKdhS_1.wireOp",EDGE,"1cb9c079-ea9b-4899-8069-e0e3048e911d.sketch_text.stroke-77"),sQuery(id+"FHMxAyK4CFUKdhS_1.wireOp",EDGE,"1cb9c079-ea9b-4899-8069-e0e3048e911d.sketch_text.stroke-78"),sQuery(id+"FHMxAyK4CFUKdhS_1.wireOp",EDGE,"1cb9c079-ea9b-4899-8069-e0e3048e911d.sketch_text.stroke-79"),sQuery(id+"FHMxAyK4CFUKdhS_1.wireOp",EDGE,"1cb9c079-ea9b-4899-8069-e0e3048e911d.sketch_text.stroke-80"),sQuery(id+"FHMxAyK4CFUKdhS_1.wireOp",EDGE,"1cb9c079-ea9b-4899-8069-e0e3048e911d.sketch_text.stroke-81"),sQuery(id+"FHMxAyK4CFUKdhS_1.wireOp",EDGE,"1cb9c079-ea9b-4899-8069-e0e3048e911d.sketch_text.stroke-82"),sQuery(id+"FHMxAyK4CFUKdhS_1.wireOp",EDGE,"1cb9c079-ea9b-4899-8069-e0e3048e911d.sketch_text.stroke-83"),sQuery(id+"FHMxAyK4CFUKdhS_1.wireOp",EDGE,"1cb9c079-ea9b-4899-8069-e0e3048e911d.sketch_text.stroke-84"),sQuery(id+"FHMxAyK4CFUKdhS_1.wireOp",EDGE,"1cb9c079-ea9b-4899-8069-e0e3048e911d.sketch_text.stroke-85"),sQuery(id+"FHMxAyK4CFUKdhS_1.wireOp",EDGE,"1cb9c079-ea9b-4899-8069-e0e3048e911d.sketch_text.stroke-86"),sQuery(id+"FHMxAyK4CFUKdhS_1.wireOp",EDGE,"1cb9c079-ea9b-4899-8069-e0e3048e911d.sketch_text.stroke-87"),sQuery(id+"FHMxAyK4CFUKdhS_1.wireOp",EDGE,"1cb9c079-ea9b-4899-8069-e0e3048e911d.sketch_text.stroke-88"),sQuery(id+"FHMxAyK4CFUKdhS_1.wireOp",EDGE,"1cb9c079-ea9b-4899-8069-e0e3048e911d.sketch_text.stroke-89"),sQuery(id+"FHMxAyK4CFUKdhS_1.wireOp",EDGE,"1cb9c079-ea9b-4899-8069-e0e3048e911d.sketch_text.stroke-90"),sQuery(id+"FHMxAyK4CFUKdhS_1.wireOp",EDGE,"1cb9c079-ea9b-4899-8069-e0e3048e911d.sketch_text.stroke-91"),sQuery(id+"FHMxAyK4CFUKdhS_1.wireOp",EDGE,"1cb9c079-ea9b-4899-8069-e0e3048e911d.sketch_text.stroke-92"),sQuery(id+"FHMxAyK4CFUKdhS_1.wireOp",EDGE,"1cb9c079-ea9b-4899-8069-e0e3048e911d.sketch_text.stroke-93"),sQuery(id+"FHMxAyK4CFUKdhS_1.wireOp",EDGE,"1cb9c079-ea9b-4899-8069-e0e3048e911d.sketch_text.stroke-94"),sQuery(id+"FHMxAyK4CFUKdhS_1.wireOp",EDGE,"1cb9c079-ea9b-4899-8069-e0e3048e911d.sketch_text.stroke-95"),sQuery(id+"FHMxAyK4CFUKdhS_1.wireOp",EDGE,"1cb9c079-ea9b-4899-8069-e0e3048e911d.sketch_text.stroke-96"),sQuery(id+"FHMxAyK4CFUKdhS_1.wireOp",EDGE,"1cb9c079-ea9b-4899-8069-e0e3048e911d.sketch_text.stroke-97"),sQuery(id+"FHMxAyK4CFUKdhS_1.wireOp",EDGE,"1cb9c079-ea9b-4899-8069-e0e3048e911d.sketch_text.stroke-103"),sQuery(id+"FHMxAyK4CFUKdhS_1.wireOp",EDGE,"1cb9c079-ea9b-4899-8069-e0e3048e911d.sketch_text.stroke-104"),sQuery(id+"FHMxAyK4CFUKdhS_1.wireOp",EDGE,"1cb9c079-ea9b-4899-8069-e0e3048e911d.sketch_text.stroke-105"),sQuery(id+"FHMxAyK4CFUKdhS_1.wireOp",EDGE,"1cb9c079-ea9b-4899-8069-e0e3048e911d.sketch_text.stroke-106"),sQuery(id+"FHMxAyK4CFUKdhS_1.wireOp",EDGE,"1cb9c079-ea9b-4899-8069-e0e3048e911d.sketch_text.stroke-107"),sQuery(id+"FHMxAyK4CFUKdhS_1.wireOp",EDGE,"1cb9c079-ea9b-4899-8069-e0e3048e911d.sketch_text.stroke-108"),sQuery(id+"FHMxAyK4CFUKdhS_1.wireOp",EDGE,"1cb9c079-ea9b-4899-8069-e0e3048e911d.sketch_text.stroke-109"),sQuery(id+"FHMxAyK4CFUKdhS_1.wireOp",EDGE,"1cb9c079-ea9b-4899-8069-e0e3048e911d.sketch_text.stroke-110"),sQuery(id+"FHMxAyK4CFUKdhS_1.wireOp",EDGE,"1cb9c079-ea9b-4899-8069-e0e3048e911d.sketch_text.stroke-111"),sQuery(id+"FHMxAyK4CFUKdhS_1.wireOp",EDGE,"1cb9c079-ea9b-4899-8069-e0e3048e911d.sketch_text.stroke-112"),sQuery(id+"FHMxAyK4CFUKdhS_1.wireOp",EDGE,"1cb9c079-ea9b-4899-8069-e0e3048e911d.sketch_text.stroke-113"),sQuery(id+"FHMxAyK4CFUKdhS_1.wireOp",EDGE,"1cb9c079-ea9b-4899-8069-e0e3048e911d.sketch_text.stroke-114"),sQuery(id+"FHMxAyK4CFUKdhS_1.wireOp",EDGE,"1cb9c079-ea9b-4899-8069-e0e3048e911d.sketch_text.stroke-115"),sQuery(id+"FHMxAyK4CFUKdhS_1.wireOp",EDGE,"1cb9c079-ea9b-4899-8069-e0e3048e911d.sketch_text.stroke-116"),sQuery(id+"FHMxAyK4CFUKdhS_1.wireOp",EDGE,"1cb9c079-ea9b-4899-8069-e0e3048e911d.sketch_text.stroke-117"),sQuery(id+"FHMxAyK4CFUKdhS_1.wireOp",EDGE,"1cb9c079-ea9b-4899-8069-e0e3048e911d.sketch_text.stroke-118"),sQuery(id+"FHMxAyK4CFUKdhS_1.wireOp",EDGE,"1cb9c079-ea9b-4899-8069-e0e3048e911d.sketch_text.stroke-119"),sQuery(id+"FHMxAyK4CFUKdhS_1.wireOp",EDGE,"1cb9c079-ea9b-4899-8069-e0e3048e911d.sketch_text.stroke-120"),sQuery(id+"FHMxAyK4CFUKdhS_1.wireOp",EDGE,"1cb9c079-ea9b-4899-8069-e0e3048e911d.sketch_text.stroke-121"),sQuery(id+"FHMxAyK4CFUKdhS_1.wireOp",EDGE,"1cb9c079-ea9b-4899-8069-e0e3048e911d.sketch_text.stroke-122"),sQuery(id+"FHMxAyK4CFUKdhS_1.wireOp",EDGE,"1cb9c079-ea9b-4899-8069-e0e3048e911d.sketch_text.stroke-123"),sQuery(id+"FHMxAyK4CFUKdhS_1.wireOp",EDGE,"1cb9c079-ea9b-4899-8069-e0e3048e911d.sketch_text.stroke-124"),sQuery(id+"FHMxAyK4CFUKdhS_1.wireOp",EDGE,"1cb9c079-ea9b-4899-8069-e0e3048e911d.sketch_text.stroke-125"),sQuery(id+"FHMxAyK4CFUKdhS_1.wireOp",EDGE,"1cb9c079-ea9b-4899-8069-e0e3048e911d.sketch_text.stroke-126"),sQuery(id+"FHMxAyK4CFUKdhS_1.wireOp",EDGE,"1cb9c079-ea9b-4899-8069-e0e3048e911d.sketch_text.stroke-127"),sQuery(id+"FHMxAyK4CFUKdhS_1.wireOp",EDGE,"1cb9c079-ea9b-4899-8069-e0e3048e911d.sketch_text.stroke-128"),sQuery(id+"FHMxAyK4CFUKdhS_1.wireOp",EDGE,"1cb9c079-ea9b-4899-8069-e0e3048e911d.sketch_text.stroke-129"),sQuery(id+"FHMxAyK4CFUKdhS_1.wireOp",EDGE,"1cb9c079-ea9b-4899-8069-e0e3048e911d.sketch_text.stroke-130"),sQuery(id+"FHMxAyK4CFUKdhS_1.wireOp",EDGE,"1cb9c079-ea9b-4899-8069-e0e3048e911d.sketch_text.stroke-131"),sQuery(id+"FHMxAyK4CFUKdhS_1.wireOp",EDGE,"1cb9c079-ea9b-4899-8069-e0e3048e911d.sketch_text.stroke-132"),sQuery(id+"FHMxAyK4CFUKdhS_1.wireOp",EDGE,"1cb9c079-ea9b-4899-8069-e0e3048e911d.sketch_text.stroke-133"),sQuery(id+"FHMxAyK4CFUKdhS_1.wireOp",EDGE,"1cb9c079-ea9b-4899-8069-e0e3048e911d.sketch_text.stroke-134"),sQuery(id+"FHMxAyK4CFUKdhS_1.wireOp",EDGE,"1cb9c079-ea9b-4899-8069-e0e3048e911d.sketch_text.stroke-135"),sQuery(id+"FHMxAyK4CFUKdhS_1.wireOp",EDGE,"1cb9c079-ea9b-4899-8069-e0e3048e911d.sketch_text.stroke-136"),sQuery(id+"FHMxAyK4CFUKdhS_1.wireOp",EDGE,"1cb9c079-ea9b-4899-8069-e0e3048e911d.sketch_text.stroke-137"),sQuery(id+"FHMxAyK4CFUKdhS_1.wireOp",EDGE,"1cb9c079-ea9b-4899-8069-e0e3048e911d.sketch_text.stroke-138"),sQuery(id+"FHMxAyK4CFUKdhS_1.wireOp",EDGE,"1cb9c079-ea9b-4899-8069-e0e3048e911d.sketch_text.stroke-139"),sQuery(id+"FHMxAyK4CFUKdhS_1.wireOp",EDGE,"1cb9c079-ea9b-4899-8069-e0e3048e911d.sketch_text.stroke-140"),sQuery(id+"FHMxAyK4CFUKdhS_1.wireOp",EDGE,"1cb9c079-ea9b-4899-8069-e0e3048e911d.sketch_text.stroke-141"),sQuery(id+"FHMxAyK4CFUKdhS_1.wireOp",EDGE,"1cb9c079-ea9b-4899-8069-e0e3048e911d.sketch_text.stroke-142"),sQuery(id+"FHMxAyK4CFUKdhS_1.wireOp",EDGE,"1cb9c079-ea9b-4899-8069-e0e3048e911d.sketch_text.stroke-143"),sQuery(id+"FHMxAyK4CFUKdhS_1.wireOp",EDGE,"1cb9c079-ea9b-4899-8069-e0e3048e911d.sketch_text.stroke-144"),sQuery(id+"FHMxAyK4CFUKdhS_1.wireOp",EDGE,"1cb9c079-ea9b-4899-8069-e0e3048e911d.sketch_text.stroke-145"),sQuery(id+"FHMxAyK4CFUKdhS_1.wireOp",EDGE,"1cb9c079-ea9b-4899-8069-e0e3048e911d.sketch_text.stroke-146"),sQuery(id+"FHMxAyK4CFUKdhS_1.wireOp",EDGE,"1cb9c079-ea9b-4899-8069-e0e3048e911d.sketch_text.stroke-147"),sQuery(id+"FHMxAyK4CFUKdhS_1.wireOp",EDGE,"1cb9c079-ea9b-4899-8069-e0e3048e911d.sketch_text.stroke-148"),sQuery(id+"FHMxAyK4CFUKdhS_1.wireOp",EDGE,"1cb9c079-ea9b-4899-8069-e0e3048e911d.sketch_text.stroke-149"),sQuery(id+"FHMxAyK4CFUKdhS_1.wireOp",EDGE,"1cb9c079-ea9b-4899-8069-e0e3048e911d.sketch_text.stroke-150"),sQuery(id+"FHMxAyK4CFUKdhS_1.wireOp",EDGE,"1cb9c079-ea9b-4899-8069-e0e3048e911d.sketch_text.stroke-151"),sQuery(id+"FHMxAyK4CFUKdhS_1.wireOp",EDGE,"1cb9c079-ea9b-4899-8069-e0e3048e911d.sketch_text.stroke-152"),sQuery(id+"FHMxAyK4CFUKdhS_1.wireOp",EDGE,"1cb9c079-ea9b-4899-8069-e0e3048e911d.sketch_text.stroke-153"),sQuery(id+"FHMxAyK4CFUKdhS_1.wireOp",EDGE,"1cb9c079-ea9b-4899-8069-e0e3048e911d.sketch_text.stroke-159"),sQuery(id+"FHMxAyK4CFUKdhS_1.wireOp",EDGE,"1cb9c079-ea9b-4899-8069-e0e3048e911d.sketch_text.stroke-160"),sQuery(id+"FHMxAyK4CFUKdhS_1.wireOp",EDGE,"1cb9c079-ea9b-4899-8069-e0e3048e911d.sketch_text.stroke-161"),sQuery(id+"FHMxAyK4CFUKdhS_1.wireOp",EDGE,"1cb9c079-ea9b-4899-8069-e0e3048e911d.sketch_text.stroke-162"),sQuery(id+"FHMxAyK4CFUKdhS_1.wireOp",EDGE,"1cb9c079-ea9b-4899-8069-e0e3048e911d.sketch_text.stroke-163"),sQuery(id+"FHMxAyK4CFUKdhS_1.wireOp",EDGE,"1cb9c079-ea9b-4899-8069-e0e3048e911d.sketch_text.stroke-164"),sQuery(id+"FHMxAyK4CFUKdhS_1.wireOp",EDGE,"1cb9c079-ea9b-4899-8069-e0e3048e911d.sketch_text.stroke-165"),sQuery(id+"FHMxAyK4CFUKdhS_1.wireOp",EDGE,"1cb9c079-ea9b-4899-8069-e0e3048e911d.sketch_text.stroke-166"),sQuery(id+"FHMxAyK4CFUKdhS_1.wireOp",EDGE,"1cb9c079-ea9b-4899-8069-e0e3048e911d.sketch_text.stroke-167"),sQuery(id+"FHMxAyK4CFUKdhS_1.wireOp",EDGE,"1cb9c079-ea9b-4899-8069-e0e3048e911d.sketch_text.stroke-168"),sQuery(id+"FHMxAyK4CFUKdhS_1.wireOp",EDGE,"1cb9c079-ea9b-4899-8069-e0e3048e911d.sketch_text.stroke-169"),sQuery(id+"FHMxAyK4CFUKdhS_1.wireOp",EDGE,"1cb9c079-ea9b-4899-8069-e0e3048e911d.sketch_text.stroke-170"),sQuery(id+"FHMxAyK4CFUKdhS_1.wireOp",EDGE,"1cb9c079-ea9b-4899-8069-e0e3048e911d.sketch_text.stroke-171"),sQuery(id+"FHMxAyK4CFUKdhS_1.wireOp",EDGE,"1cb9c079-ea9b-4899-8069-e0e3048e911d.sketch_text.stroke-172"),sQuery(id+"FHMxAyK4CFUKdhS_1.wireOp",EDGE,"1cb9c079-ea9b-4899-8069-e0e3048e911d.sketch_text.stroke-173"),sQuery(id+"FHMxAyK4CFUKdhS_1.wireOp",EDGE,"1cb9c079-ea9b-4899-8069-e0e3048e911d.sketch_text.stroke-174"),sQuery(id+"FHMxAyK4CFUKdhS_1.wireOp",EDGE,"1cb9c079-ea9b-4899-8069-e0e3048e911d.sketch_text.stroke-175"),sQuery(id+"FHMxAyK4CFUKdhS_1.wireOp",EDGE,"1cb9c079-ea9b-4899-8069-e0e3048e911d.sketch_text.stroke-176"),sQuery(id+"FHMxAyK4CFUKdhS_1.wireOp",EDGE,"1cb9c079-ea9b-4899-8069-e0e3048e911d.sketch_text.stroke-177"),sQuery(id+"FHMxAyK4CFUKdhS_1.wireOp",EDGE,"1cb9c079-ea9b-4899-8069-e0e3048e911d.sketch_text.stroke-178"),sQuery(id+"FHMxAyK4CFUKdhS_1.wireOp",EDGE,"1cb9c079-ea9b-4899-8069-e0e3048e911d.sketch_text.stroke-179"),sQuery(id+"FHMxAyK4CFUKdhS_1.wireOp",EDGE,"1cb9c079-ea9b-4899-8069-e0e3048e911d.sketch_text.stroke-180"),sQuery(id+"F3.wireOp",EDGE,"E29"),subQ2])],"isStart":true}),makeQuery(id+"F4.opExtrude","SWEPT_FACE",FACE,{"disambiguationData":[OSD([subQ2])]})])],"derivedFrom":makeQuery(id+"F4.opExtrude","CAP_EDGE",EDGE,{"disambiguationData":[OSD([subQ2])],"isStart":true})});}
            var Q24;
            {var subQ0=sQuery(id+"F0.wireOp",EDGE,"E0.top");var subQ1=sQuery(id+"F0.wireOp",EDGE,"E0.bottom");var subQ2=sQuery(id+"F3.wireOp",EDGE,"E29");Q24=makeQuery(id+"F4.boolean.opBoolean","SPLIT",EDGE,{"disambiguationData":[TD([makeQuery(id+"F1.opExtrude","CAP_FACE",FACE,{"disambiguationData":[OSD([subQ1,subQ0,sQuery(id+"F0.wireOp",EDGE,"E0.left"),sQuery(id+"F0.wireOp",EDGE,"E0.right")])],"isStart":false}),makeQuery(id+"F1.opExtrude","SWEPT_FACE",FACE,{"disambiguationData":[OSD([subQ0])]}),makeQuery(id+"F4.opExtrude","SWEPT_FACE",FACE,{"disambiguationData":[OSD([subQ2])]}),makeQuery(id+"F4.opExtrude","CAP_FACE",FACE,{"disambiguationData":[OSD([subQ1,sQuery(id+"F2.wireOp",EDGE,"fcba4419-a2ee-464f-be9d-58f11bf3418b.sketch_text.stroke-0"),sQuery(id+"F2.wireOp",EDGE,"fcba4419-a2ee-464f-be9d-58f11bf3418b.sketch_text.stroke-1"),sQuery(id+"F2.wireOp",EDGE,"fcba4419-a2ee-464f-be9d-58f11bf3418b.sketch_text.stroke-2"),sQuery(id+"F2.wireOp",EDGE,"fcba4419-a2ee-464f-be9d-58f11bf3418b.sketch_text.stroke-3"),sQuery(id+"F2.wireOp",EDGE,"fcba4419-a2ee-464f-be9d-58f11bf3418b.sketch_text.stroke-4"),sQuery(id+"F2.wireOp",EDGE,"fcba4419-a2ee-464f-be9d-58f11bf3418b.sketch_text.stroke-5"),sQuery(id+"F2.wireOp",EDGE,"fcba4419-a2ee-464f-be9d-58f11bf3418b.sketch_text.stroke-6"),sQuery(id+"F2.wireOp",EDGE,"fcba4419-a2ee-464f-be9d-58f11bf3418b.sketch_text.stroke-7"),sQuery(id+"F2.wireOp",EDGE,"fcba4419-a2ee-464f-be9d-58f11bf3418b.sketch_text.stroke-8"),sQuery(id+"F2.wireOp",EDGE,"fcba4419-a2ee-464f-be9d-58f11bf3418b.sketch_text.stroke-9"),sQuery(id+"F2.wireOp",EDGE,"fcba4419-a2ee-464f-be9d-58f11bf3418b.sketch_text.stroke-10"),sQuery(id+"F2.wireOp",EDGE,"fcba4419-a2ee-464f-be9d-58f11bf3418b.sketch_text.stroke-11"),sQuery(id+"F2.wireOp",EDGE,"fcba4419-a2ee-464f-be9d-58f11bf3418b.sketch_text.stroke-12"),sQuery(id+"F2.wireOp",EDGE,"fcba4419-a2ee-464f-be9d-58f11bf3418b.sketch_text.stroke-13"),sQuery(id+"F2.wireOp",EDGE,"fcba4419-a2ee-464f-be9d-58f11bf3418b.sketch_text.stroke-14"),sQuery(id+"F2.wireOp",EDGE,"fcba4419-a2ee-464f-be9d-58f11bf3418b.sketch_text.stroke-15"),sQuery(id+"F2.wireOp",EDGE,"fcba4419-a2ee-464f-be9d-58f11bf3418b.sketch_text.stroke-16"),sQuery(id+"F2.wireOp",EDGE,"fcba4419-a2ee-464f-be9d-58f11bf3418b.sketch_text.stroke-17"),sQuery(id+"F2.wireOp",EDGE,"fcba4419-a2ee-464f-be9d-58f11bf3418b.sketch_text.stroke-18"),sQuery(id+"F2.wireOp",EDGE,"fcba4419-a2ee-464f-be9d-58f11bf3418b.sketch_text.stroke-19"),sQuery(id+"F2.wireOp",EDGE,"fcba4419-a2ee-464f-be9d-58f11bf3418b.sketch_text.stroke-20"),sQuery(id+"F2.wireOp",EDGE,"fcba4419-a2ee-464f-be9d-58f11bf3418b.sketch_text.stroke-21"),sQuery(id+"F2.wireOp",EDGE,"fcba4419-a2ee-464f-be9d-58f11bf3418b.sketch_text.stroke-22"),sQuery(id+"F2.wireOp",EDGE,"fcba4419-a2ee-464f-be9d-58f11bf3418b.sketch_text.stroke-23"),sQuery(id+"F2.wireOp",EDGE,"fcba4419-a2ee-464f-be9d-58f11bf3418b.sketch_text.stroke-24"),sQuery(id+"F2.wireOp",EDGE,"fcba4419-a2ee-464f-be9d-58f11bf3418b.sketch_text.stroke-25"),sQuery(id+"F2.wireOp",EDGE,"fcba4419-a2ee-464f-be9d-58f11bf3418b.sketch_text.stroke-26"),sQuery(id+"F2.wireOp",EDGE,"fcba4419-a2ee-464f-be9d-58f11bf3418b.sketch_text.stroke-27"),sQuery(id+"F2.wireOp",EDGE,"fcba4419-a2ee-464f-be9d-58f11bf3418b.sketch_text.stroke-28"),sQuery(id+"F2.wireOp",EDGE,"fcba4419-a2ee-464f-be9d-58f11bf3418b.sketch_text.stroke-29"),sQuery(id+"F2.wireOp",EDGE,"fcba4419-a2ee-464f-be9d-58f11bf3418b.sketch_text.stroke-30"),sQuery(id+"F2.wireOp",EDGE,"fcba4419-a2ee-464f-be9d-58f11bf3418b.sketch_text.stroke-31"),sQuery(id+"F2.wireOp",EDGE,"fcba4419-a2ee-464f-be9d-58f11bf3418b.sketch_text.stroke-32"),sQuery(id+"F2.wireOp",EDGE,"fcba4419-a2ee-464f-be9d-58f11bf3418b.sketch_text.stroke-33"),sQuery(id+"F2.wireOp",EDGE,"fcba4419-a2ee-464f-be9d-58f11bf3418b.sketch_text.stroke-34"),sQuery(id+"F2.wireOp",EDGE,"fcba4419-a2ee-464f-be9d-58f11bf3418b.sketch_text.stroke-35"),sQuery(id+"F2.wireOp",EDGE,"fcba4419-a2ee-464f-be9d-58f11bf3418b.sketch_text.stroke-36"),sQuery(id+"F2.wireOp",EDGE,"fcba4419-a2ee-464f-be9d-58f11bf3418b.sketch_text.stroke-37"),sQuery(id+"F2.wireOp",EDGE,"fcba4419-a2ee-464f-be9d-58f11bf3418b.sketch_text.stroke-38"),sQuery(id+"F2.wireOp",EDGE,"fcba4419-a2ee-464f-be9d-58f11bf3418b.sketch_text.stroke-39"),sQuery(id+"F2.wireOp",EDGE,"fcba4419-a2ee-464f-be9d-58f11bf3418b.sketch_text.stroke-40"),sQuery(id+"F2.wireOp",EDGE,"fcba4419-a2ee-464f-be9d-58f11bf3418b.sketch_text.stroke-41"),sQuery(id+"F2.wireOp",EDGE,"fcba4419-a2ee-464f-be9d-58f11bf3418b.sketch_text.stroke-42"),sQuery(id+"F2.wireOp",EDGE,"fcba4419-a2ee-464f-be9d-58f11bf3418b.sketch_text.stroke-43"),sQuery(id+"F2.wireOp",EDGE,"fcba4419-a2ee-464f-be9d-58f11bf3418b.sketch_text.stroke-44"),sQuery(id+"F2.wireOp",EDGE,"fcba4419-a2ee-464f-be9d-58f11bf3418b.sketch_text.stroke-45"),sQuery(id+"F2.wireOp",EDGE,"fcba4419-a2ee-464f-be9d-58f11bf3418b.sketch_text.stroke-46"),sQuery(id+"F2.wireOp",EDGE,"fcba4419-a2ee-464f-be9d-58f11bf3418b.sketch_text.stroke-47"),sQuery(id+"F2.wireOp",EDGE,"fcba4419-a2ee-464f-be9d-58f11bf3418b.sketch_text.stroke-48"),sQuery(id+"F2.wireOp",EDGE,"fcba4419-a2ee-464f-be9d-58f11bf3418b.sketch_text.stroke-49"),sQuery(id+"F2.wireOp",EDGE,"fcba4419-a2ee-464f-be9d-58f11bf3418b.sketch_text.stroke-50"),sQuery(id+"F2.wireOp",EDGE,"fcba4419-a2ee-464f-be9d-58f11bf3418b.sketch_text.stroke-51"),sQuery(id+"F2.wireOp",EDGE,"fcba4419-a2ee-464f-be9d-58f11bf3418b.sketch_text.stroke-52"),sQuery(id+"F2.wireOp",EDGE,"fcba4419-a2ee-464f-be9d-58f11bf3418b.sketch_text.stroke-53"),sQuery(id+"F2.wireOp",EDGE,"fcba4419-a2ee-464f-be9d-58f11bf3418b.sketch_text.stroke-54"),sQuery(id+"F2.wireOp",EDGE,"fcba4419-a2ee-464f-be9d-58f11bf3418b.sketch_text.stroke-55"),sQuery(id+"F2.wireOp",EDGE,"fcba4419-a2ee-464f-be9d-58f11bf3418b.sketch_text.stroke-56"),sQuery(id+"F2.wireOp",EDGE,"fcba4419-a2ee-464f-be9d-58f11bf3418b.sketch_text.stroke-57"),sQuery(id+"F2.wireOp",EDGE,"fcba4419-a2ee-464f-be9d-58f11bf3418b.sketch_text.stroke-58"),sQuery(id+"F2.wireOp",EDGE,"fcba4419-a2ee-464f-be9d-58f11bf3418b.sketch_text.stroke-59"),sQuery(id+"F2.wireOp",EDGE,"fcba4419-a2ee-464f-be9d-58f11bf3418b.sketch_text.stroke-60"),sQuery(id+"F2.wireOp",EDGE,"fcba4419-a2ee-464f-be9d-58f11bf3418b.sketch_text.stroke-61"),sQuery(id+"F2.wireOp",EDGE,"fcba4419-a2ee-464f-be9d-58f11bf3418b.sketch_text.stroke-62"),sQuery(id+"F2.wireOp",EDGE,"fcba4419-a2ee-464f-be9d-58f11bf3418b.sketch_text.stroke-63"),sQuery(id+"F2.wireOp",EDGE,"fcba4419-a2ee-464f-be9d-58f11bf3418b.sketch_text.stroke-64"),sQuery(id+"F2.wireOp",EDGE,"fcba4419-a2ee-464f-be9d-58f11bf3418b.sketch_text.stroke-65"),sQuery(id+"F2.wireOp",EDGE,"fcba4419-a2ee-464f-be9d-58f11bf3418b.sketch_text.stroke-66"),sQuery(id+"F2.wireOp",EDGE,"fcba4419-a2ee-464f-be9d-58f11bf3418b.sketch_text.stroke-67"),sQuery(id+"F2.wireOp",EDGE,"fcba4419-a2ee-464f-be9d-58f11bf3418b.sketch_text.stroke-68"),sQuery(id+"F2.wireOp",EDGE,"fcba4419-a2ee-464f-be9d-58f11bf3418b.sketch_text.stroke-69"),sQuery(id+"F2.wireOp",EDGE,"fcba4419-a2ee-464f-be9d-58f11bf3418b.sketch_text.stroke-70"),sQuery(id+"F2.wireOp",EDGE,"fcba4419-a2ee-464f-be9d-58f11bf3418b.sketch_text.stroke-71"),sQuery(id+"F2.wireOp",EDGE,"fcba4419-a2ee-464f-be9d-58f11bf3418b.sketch_text.stroke-72"),sQuery(id+"F2.wireOp",EDGE,"fcba4419-a2ee-464f-be9d-58f11bf3418b.sketch_text.stroke-73"),sQuery(id+"F2.wireOp",EDGE,"fcba4419-a2ee-464f-be9d-58f11bf3418b.sketch_text.stroke-74"),sQuery(id+"F2.wireOp",EDGE,"fcba4419-a2ee-464f-be9d-58f11bf3418b.sketch_text.stroke-75"),sQuery(id+"F2.wireOp",EDGE,"fcba4419-a2ee-464f-be9d-58f11bf3418b.sketch_text.stroke-76"),sQuery(id+"F2.wireOp",EDGE,"fcba4419-a2ee-464f-be9d-58f11bf3418b.sketch_text.stroke-77"),sQuery(id+"F2.wireOp",EDGE,"fcba4419-a2ee-464f-be9d-58f11bf3418b.sketch_text.stroke-78"),sQuery(id+"F2.wireOp",EDGE,"fcba4419-a2ee-464f-be9d-58f11bf3418b.sketch_text.stroke-79"),sQuery(id+"F2.wireOp",EDGE,"fcba4419-a2ee-464f-be9d-58f11bf3418b.sketch_text.stroke-80"),sQuery(id+"F2.wireOp",EDGE,"fcba4419-a2ee-464f-be9d-58f11bf3418b.sketch_text.stroke-81"),sQuery(id+"F2.wireOp",EDGE,"fcba4419-a2ee-464f-be9d-58f11bf3418b.sketch_text.stroke-82"),sQuery(id+"F2.wireOp",EDGE,"fcba4419-a2ee-464f-be9d-58f11bf3418b.sketch_text.stroke-83"),sQuery(id+"F2.wireOp",EDGE,"fcba4419-a2ee-464f-be9d-58f11bf3418b.sketch_text.stroke-84"),sQuery(id+"F2.wireOp",EDGE,"fcba4419-a2ee-464f-be9d-58f11bf3418b.sketch_text.stroke-85"),sQuery(id+"F2.wireOp",EDGE,"fcba4419-a2ee-464f-be9d-58f11bf3418b.sketch_text.stroke-86"),sQuery(id+"F2.wireOp",EDGE,"fcba4419-a2ee-464f-be9d-58f11bf3418b.sketch_text.stroke-87"),sQuery(id+"F2.wireOp",EDGE,"fcba4419-a2ee-464f-be9d-58f11bf3418b.sketch_text.stroke-88"),sQuery(id+"F2.wireOp",EDGE,"fcba4419-a2ee-464f-be9d-58f11bf3418b.sketch_text.stroke-89"),sQuery(id+"F2.wireOp",EDGE,"fcba4419-a2ee-464f-be9d-58f11bf3418b.sketch_text.stroke-90"),sQuery(id+"F2.wireOp",EDGE,"fcba4419-a2ee-464f-be9d-58f11bf3418b.sketch_text.stroke-91"),sQuery(id+"F2.wireOp",EDGE,"fcba4419-a2ee-464f-be9d-58f11bf3418b.sketch_text.stroke-92"),sQuery(id+"F2.wireOp",EDGE,"fcba4419-a2ee-464f-be9d-58f11bf3418b.sketch_text.stroke-93"),sQuery(id+"F2.wireOp",EDGE,"fcba4419-a2ee-464f-be9d-58f11bf3418b.sketch_text.stroke-94"),sQuery(id+"F2.wireOp",EDGE,"fcba4419-a2ee-464f-be9d-58f11bf3418b.sketch_text.stroke-95"),sQuery(id+"F2.wireOp",EDGE,"fcba4419-a2ee-464f-be9d-58f11bf3418b.sketch_text.stroke-96"),sQuery(id+"F2.wireOp",EDGE,"fcba4419-a2ee-464f-be9d-58f11bf3418b.sketch_text.stroke-97"),sQuery(id+"F2.wireOp",EDGE,"fcba4419-a2ee-464f-be9d-58f11bf3418b.sketch_text.stroke-98"),sQuery(id+"F2.wireOp",EDGE,"fcba4419-a2ee-464f-be9d-58f11bf3418b.sketch_text.stroke-99"),sQuery(id+"F2.wireOp",EDGE,"fcba4419-a2ee-464f-be9d-58f11bf3418b.sketch_text.stroke-100"),sQuery(id+"F2.wireOp",EDGE,"fcba4419-a2ee-464f-be9d-58f11bf3418b.sketch_text.stroke-101"),sQuery(id+"F2.wireOp",EDGE,"fcba4419-a2ee-464f-be9d-58f11bf3418b.sketch_text.stroke-102"),sQuery(id+"F2.wireOp",EDGE,"fcba4419-a2ee-464f-be9d-58f11bf3418b.sketch_text.stroke-103"),sQuery(id+"F2.wireOp",EDGE,"fcba4419-a2ee-464f-be9d-58f11bf3418b.sketch_text.stroke-104"),sQuery(id+"F2.wireOp",EDGE,"fcba4419-a2ee-464f-be9d-58f11bf3418b.sketch_text.stroke-105"),sQuery(id+"F2.wireOp",EDGE,"fcba4419-a2ee-464f-be9d-58f11bf3418b.sketch_text.stroke-106"),sQuery(id+"F2.wireOp",EDGE,"fcba4419-a2ee-464f-be9d-58f11bf3418b.sketch_text.stroke-107"),sQuery(id+"F2.wireOp",EDGE,"fcba4419-a2ee-464f-be9d-58f11bf3418b.sketch_text.stroke-108"),sQuery(id+"F2.wireOp",EDGE,"fcba4419-a2ee-464f-be9d-58f11bf3418b.sketch_text.stroke-109"),sQuery(id+"F2.wireOp",EDGE,"fcba4419-a2ee-464f-be9d-58f11bf3418b.sketch_text.stroke-110"),sQuery(id+"F2.wireOp",EDGE,"fcba4419-a2ee-464f-be9d-58f11bf3418b.sketch_text.stroke-111"),sQuery(id+"F2.wireOp",EDGE,"fcba4419-a2ee-464f-be9d-58f11bf3418b.sketch_text.stroke-112"),sQuery(id+"F2.wireOp",EDGE,"fcba4419-a2ee-464f-be9d-58f11bf3418b.sketch_text.stroke-113"),sQuery(id+"F2.wireOp",EDGE,"fcba4419-a2ee-464f-be9d-58f11bf3418b.sketch_text.stroke-114"),sQuery(id+"F2.wireOp",EDGE,"fcba4419-a2ee-464f-be9d-58f11bf3418b.sketch_text.stroke-115"),sQuery(id+"F2.wireOp",EDGE,"fcba4419-a2ee-464f-be9d-58f11bf3418b.sketch_text.stroke-116"),sQuery(id+"F2.wireOp",EDGE,"fcba4419-a2ee-464f-be9d-58f11bf3418b.sketch_text.stroke-117"),sQuery(id+"F2.wireOp",EDGE,"fcba4419-a2ee-464f-be9d-58f11bf3418b.sketch_text.stroke-118"),sQuery(id+"F2.wireOp",EDGE,"fcba4419-a2ee-464f-be9d-58f11bf3418b.sketch_text.stroke-119"),sQuery(id+"F2.wireOp",EDGE,"fcba4419-a2ee-464f-be9d-58f11bf3418b.sketch_text.stroke-120"),sQuery(id+"F2.wireOp",EDGE,"fcba4419-a2ee-464f-be9d-58f11bf3418b.sketch_text.stroke-121"),sQuery(id+"F2.wireOp",EDGE,"fcba4419-a2ee-464f-be9d-58f11bf3418b.sketch_text.stroke-122"),sQuery(id+"F2.wireOp",EDGE,"fcba4419-a2ee-464f-be9d-58f11bf3418b.sketch_text.stroke-123"),sQuery(id+"F2.wireOp",EDGE,"fcba4419-a2ee-464f-be9d-58f11bf3418b.sketch_text.stroke-124"),sQuery(id+"F2.wireOp",EDGE,"fcba4419-a2ee-464f-be9d-58f11bf3418b.sketch_text.stroke-125"),sQuery(id+"F2.wireOp",EDGE,"fcba4419-a2ee-464f-be9d-58f11bf3418b.sketch_text.stroke-126"),sQuery(id+"F2.wireOp",EDGE,"fcba4419-a2ee-464f-be9d-58f11bf3418b.sketch_text.stroke-127"),sQuery(id+"F2.wireOp",EDGE,"fcba4419-a2ee-464f-be9d-58f11bf3418b.sketch_text.stroke-128"),sQuery(id+"F2.wireOp",EDGE,"fcba4419-a2ee-464f-be9d-58f11bf3418b.sketch_text.stroke-129"),sQuery(id+"F2.wireOp",EDGE,"fcba4419-a2ee-464f-be9d-58f11bf3418b.sketch_text.stroke-130"),sQuery(id+"F2.wireOp",EDGE,"fcba4419-a2ee-464f-be9d-58f11bf3418b.sketch_text.stroke-131"),sQuery(id+"F2.wireOp",EDGE,"fcba4419-a2ee-464f-be9d-58f11bf3418b.sketch_text.stroke-132"),sQuery(id+"F2.wireOp",EDGE,"fcba4419-a2ee-464f-be9d-58f11bf3418b.sketch_text.stroke-133"),sQuery(id+"F2.wireOp",EDGE,"fcba4419-a2ee-464f-be9d-58f11bf3418b.sketch_text.stroke-134"),sQuery(id+"F2.wireOp",EDGE,"fcba4419-a2ee-464f-be9d-58f11bf3418b.sketch_text.stroke-135"),sQuery(id+"F2.wireOp",EDGE,"fcba4419-a2ee-464f-be9d-58f11bf3418b.sketch_text.stroke-136"),sQuery(id+"F2.wireOp",EDGE,"fcba4419-a2ee-464f-be9d-58f11bf3418b.sketch_text.stroke-137"),sQuery(id+"F2.wireOp",EDGE,"fcba4419-a2ee-464f-be9d-58f11bf3418b.sketch_text.stroke-138"),sQuery(id+"F2.wireOp",EDGE,"fcba4419-a2ee-464f-be9d-58f11bf3418b.sketch_text.stroke-139"),sQuery(id+"F2.wireOp",EDGE,"fcba4419-a2ee-464f-be9d-58f11bf3418b.sketch_text.stroke-140"),sQuery(id+"F2.wireOp",EDGE,"fcba4419-a2ee-464f-be9d-58f11bf3418b.sketch_text.stroke-141"),sQuery(id+"F2.wireOp",EDGE,"fcba4419-a2ee-464f-be9d-58f11bf3418b.sketch_text.stroke-142"),sQuery(id+"F2.wireOp",EDGE,"fcba4419-a2ee-464f-be9d-58f11bf3418b.sketch_text.stroke-143"),sQuery(id+"F2.wireOp",EDGE,"fcba4419-a2ee-464f-be9d-58f11bf3418b.sketch_text.stroke-144"),sQuery(id+"F2.wireOp",EDGE,"fcba4419-a2ee-464f-be9d-58f11bf3418b.sketch_text.stroke-145"),sQuery(id+"F2.wireOp",EDGE,"fcba4419-a2ee-464f-be9d-58f11bf3418b.sketch_text.stroke-146"),sQuery(id+"F2.wireOp",EDGE,"fcba4419-a2ee-464f-be9d-58f11bf3418b.sketch_text.stroke-147"),sQuery(id+"F2.wireOp",EDGE,"fcba4419-a2ee-464f-be9d-58f11bf3418b.sketch_text.stroke-148"),sQuery(id+"F2.wireOp",EDGE,"fcba4419-a2ee-464f-be9d-58f11bf3418b.sketch_text.stroke-149"),sQuery(id+"F2.wireOp",EDGE,"fcba4419-a2ee-464f-be9d-58f11bf3418b.sketch_text.stroke-150"),sQuery(id+"F2.wireOp",EDGE,"fcba4419-a2ee-464f-be9d-58f11bf3418b.sketch_text.stroke-151"),sQuery(id+"F2.wireOp",EDGE,"fcba4419-a2ee-464f-be9d-58f11bf3418b.sketch_text.stroke-152"),sQuery(id+"F2.wireOp",EDGE,"fcba4419-a2ee-464f-be9d-58f11bf3418b.sketch_text.stroke-153"),sQuery(id+"F2.wireOp",EDGE,"fcba4419-a2ee-464f-be9d-58f11bf3418b.sketch_text.stroke-154"),sQuery(id+"F2.wireOp",EDGE,"fcba4419-a2ee-464f-be9d-58f11bf3418b.sketch_text.stroke-155"),sQuery(id+"F2.wireOp",EDGE,"fcba4419-a2ee-464f-be9d-58f11bf3418b.sketch_text.stroke-156"),sQuery(id+"F2.wireOp",EDGE,"fcba4419-a2ee-464f-be9d-58f11bf3418b.sketch_text.stroke-157"),sQuery(id+"F2.wireOp",EDGE,"fcba4419-a2ee-464f-be9d-58f11bf3418b.sketch_text.stroke-158"),sQuery(id+"F2.wireOp",EDGE,"fcba4419-a2ee-464f-be9d-58f11bf3418b.sketch_text.stroke-159"),sQuery(id+"F2.wireOp",EDGE,"fcba4419-a2ee-464f-be9d-58f11bf3418b.sketch_text.stroke-160"),sQuery(id+"F2.wireOp",EDGE,"fcba4419-a2ee-464f-be9d-58f11bf3418b.sketch_text.stroke-161"),sQuery(id+"F2.wireOp",EDGE,"fcba4419-a2ee-464f-be9d-58f11bf3418b.sketch_text.stroke-162"),sQuery(id+"F2.wireOp",EDGE,"fcba4419-a2ee-464f-be9d-58f11bf3418b.sketch_text.stroke-163"),sQuery(id+"F2.wireOp",EDGE,"fcba4419-a2ee-464f-be9d-58f11bf3418b.sketch_text.stroke-164"),sQuery(id+"F2.wireOp",EDGE,"fcba4419-a2ee-464f-be9d-58f11bf3418b.sketch_text.stroke-165"),sQuery(id+"F2.wireOp",EDGE,"fcba4419-a2ee-464f-be9d-58f11bf3418b.sketch_text.stroke-166"),sQuery(id+"F2.wireOp",EDGE,"fcba4419-a2ee-464f-be9d-58f11bf3418b.sketch_text.stroke-167"),sQuery(id+"F2.wireOp",EDGE,"fcba4419-a2ee-464f-be9d-58f11bf3418b.sketch_text.stroke-168"),sQuery(id+"F2.wireOp",EDGE,"fcba4419-a2ee-464f-be9d-58f11bf3418b.sketch_text.stroke-169"),sQuery(id+"F2.wireOp",EDGE,"fcba4419-a2ee-464f-be9d-58f11bf3418b.sketch_text.stroke-170"),sQuery(id+"F2.wireOp",EDGE,"fcba4419-a2ee-464f-be9d-58f11bf3418b.sketch_text.stroke-171"),sQuery(id+"F2.wireOp",EDGE,"fcba4419-a2ee-464f-be9d-58f11bf3418b.sketch_text.stroke-172"),sQuery(id+"F2.wireOp",EDGE,"fcba4419-a2ee-464f-be9d-58f11bf3418b.sketch_text.stroke-173"),sQuery(id+"FHMxAyK4CFUKdhS_1.wireOp",EDGE,"1cb9c079-ea9b-4899-8069-e0e3048e911d.sketch_text.stroke-0"),sQuery(id+"FHMxAyK4CFUKdhS_1.wireOp",EDGE,"1cb9c079-ea9b-4899-8069-e0e3048e911d.sketch_text.stroke-1"),sQuery(id+"FHMxAyK4CFUKdhS_1.wireOp",EDGE,"1cb9c079-ea9b-4899-8069-e0e3048e911d.sketch_text.stroke-2"),sQuery(id+"FHMxAyK4CFUKdhS_1.wireOp",EDGE,"1cb9c079-ea9b-4899-8069-e0e3048e911d.sketch_text.stroke-3"),sQuery(id+"FHMxAyK4CFUKdhS_1.wireOp",EDGE,"1cb9c079-ea9b-4899-8069-e0e3048e911d.sketch_text.stroke-4"),sQuery(id+"FHMxAyK4CFUKdhS_1.wireOp",EDGE,"1cb9c079-ea9b-4899-8069-e0e3048e911d.sketch_text.stroke-5"),sQuery(id+"FHMxAyK4CFUKdhS_1.wireOp",EDGE,"1cb9c079-ea9b-4899-8069-e0e3048e911d.sketch_text.stroke-6"),sQuery(id+"FHMxAyK4CFUKdhS_1.wireOp",EDGE,"1cb9c079-ea9b-4899-8069-e0e3048e911d.sketch_text.stroke-7"),sQuery(id+"FHMxAyK4CFUKdhS_1.wireOp",EDGE,"1cb9c079-ea9b-4899-8069-e0e3048e911d.sketch_text.stroke-8"),sQuery(id+"FHMxAyK4CFUKdhS_1.wireOp",EDGE,"1cb9c079-ea9b-4899-8069-e0e3048e911d.sketch_text.stroke-9"),sQuery(id+"FHMxAyK4CFUKdhS_1.wireOp",EDGE,"1cb9c079-ea9b-4899-8069-e0e3048e911d.sketch_text.stroke-10"),sQuery(id+"FHMxAyK4CFUKdhS_1.wireOp",EDGE,"1cb9c079-ea9b-4899-8069-e0e3048e911d.sketch_text.stroke-11"),sQuery(id+"FHMxAyK4CFUKdhS_1.wireOp",EDGE,"1cb9c079-ea9b-4899-8069-e0e3048e911d.sketch_text.stroke-12"),sQuery(id+"FHMxAyK4CFUKdhS_1.wireOp",EDGE,"1cb9c079-ea9b-4899-8069-e0e3048e911d.sketch_text.stroke-13"),sQuery(id+"FHMxAyK4CFUKdhS_1.wireOp",EDGE,"1cb9c079-ea9b-4899-8069-e0e3048e911d.sketch_text.stroke-14"),sQuery(id+"FHMxAyK4CFUKdhS_1.wireOp",EDGE,"1cb9c079-ea9b-4899-8069-e0e3048e911d.sketch_text.stroke-15"),sQuery(id+"FHMxAyK4CFUKdhS_1.wireOp",EDGE,"1cb9c079-ea9b-4899-8069-e0e3048e911d.sketch_text.stroke-16"),sQuery(id+"FHMxAyK4CFUKdhS_1.wireOp",EDGE,"1cb9c079-ea9b-4899-8069-e0e3048e911d.sketch_text.stroke-17"),sQuery(id+"FHMxAyK4CFUKdhS_1.wireOp",EDGE,"1cb9c079-ea9b-4899-8069-e0e3048e911d.sketch_text.stroke-18"),sQuery(id+"FHMxAyK4CFUKdhS_1.wireOp",EDGE,"1cb9c079-ea9b-4899-8069-e0e3048e911d.sketch_text.stroke-19"),sQuery(id+"FHMxAyK4CFUKdhS_1.wireOp",EDGE,"1cb9c079-ea9b-4899-8069-e0e3048e911d.sketch_text.stroke-20"),sQuery(id+"FHMxAyK4CFUKdhS_1.wireOp",EDGE,"1cb9c079-ea9b-4899-8069-e0e3048e911d.sketch_text.stroke-21"),sQuery(id+"FHMxAyK4CFUKdhS_1.wireOp",EDGE,"1cb9c079-ea9b-4899-8069-e0e3048e911d.sketch_text.stroke-22"),sQuery(id+"FHMxAyK4CFUKdhS_1.wireOp",EDGE,"1cb9c079-ea9b-4899-8069-e0e3048e911d.sketch_text.stroke-23"),sQuery(id+"FHMxAyK4CFUKdhS_1.wireOp",EDGE,"1cb9c079-ea9b-4899-8069-e0e3048e911d.sketch_text.stroke-24"),sQuery(id+"FHMxAyK4CFUKdhS_1.wireOp",EDGE,"1cb9c079-ea9b-4899-8069-e0e3048e911d.sketch_text.stroke-25"),sQuery(id+"FHMxAyK4CFUKdhS_1.wireOp",EDGE,"1cb9c079-ea9b-4899-8069-e0e3048e911d.sketch_text.stroke-26"),sQuery(id+"FHMxAyK4CFUKdhS_1.wireOp",EDGE,"1cb9c079-ea9b-4899-8069-e0e3048e911d.sketch_text.stroke-27"),sQuery(id+"FHMxAyK4CFUKdhS_1.wireOp",EDGE,"1cb9c079-ea9b-4899-8069-e0e3048e911d.sketch_text.stroke-28"),sQuery(id+"FHMxAyK4CFUKdhS_1.wireOp",EDGE,"1cb9c079-ea9b-4899-8069-e0e3048e911d.sketch_text.stroke-29"),sQuery(id+"FHMxAyK4CFUKdhS_1.wireOp",EDGE,"1cb9c079-ea9b-4899-8069-e0e3048e911d.sketch_text.stroke-30"),sQuery(id+"FHMxAyK4CFUKdhS_1.wireOp",EDGE,"1cb9c079-ea9b-4899-8069-e0e3048e911d.sketch_text.stroke-31"),sQuery(id+"FHMxAyK4CFUKdhS_1.wireOp",EDGE,"1cb9c079-ea9b-4899-8069-e0e3048e911d.sketch_text.stroke-32"),sQuery(id+"FHMxAyK4CFUKdhS_1.wireOp",EDGE,"1cb9c079-ea9b-4899-8069-e0e3048e911d.sketch_text.stroke-33"),sQuery(id+"FHMxAyK4CFUKdhS_1.wireOp",EDGE,"1cb9c079-ea9b-4899-8069-e0e3048e911d.sketch_text.stroke-34"),sQuery(id+"FHMxAyK4CFUKdhS_1.wireOp",EDGE,"1cb9c079-ea9b-4899-8069-e0e3048e911d.sketch_text.stroke-35"),sQuery(id+"FHMxAyK4CFUKdhS_1.wireOp",EDGE,"1cb9c079-ea9b-4899-8069-e0e3048e911d.sketch_text.stroke-36"),sQuery(id+"FHMxAyK4CFUKdhS_1.wireOp",EDGE,"1cb9c079-ea9b-4899-8069-e0e3048e911d.sketch_text.stroke-37"),sQuery(id+"FHMxAyK4CFUKdhS_1.wireOp",EDGE,"1cb9c079-ea9b-4899-8069-e0e3048e911d.sketch_text.stroke-38"),sQuery(id+"FHMxAyK4CFUKdhS_1.wireOp",EDGE,"1cb9c079-ea9b-4899-8069-e0e3048e911d.sketch_text.stroke-39"),sQuery(id+"FHMxAyK4CFUKdhS_1.wireOp",EDGE,"1cb9c079-ea9b-4899-8069-e0e3048e911d.sketch_text.stroke-40"),sQuery(id+"FHMxAyK4CFUKdhS_1.wireOp",EDGE,"1cb9c079-ea9b-4899-8069-e0e3048e911d.sketch_text.stroke-41"),sQuery(id+"FHMxAyK4CFUKdhS_1.wireOp",EDGE,"1cb9c079-ea9b-4899-8069-e0e3048e911d.sketch_text.stroke-42"),sQuery(id+"FHMxAyK4CFUKdhS_1.wireOp",EDGE,"1cb9c079-ea9b-4899-8069-e0e3048e911d.sketch_text.stroke-43"),sQuery(id+"FHMxAyK4CFUKdhS_1.wireOp",EDGE,"1cb9c079-ea9b-4899-8069-e0e3048e911d.sketch_text.stroke-44"),sQuery(id+"FHMxAyK4CFUKdhS_1.wireOp",EDGE,"1cb9c079-ea9b-4899-8069-e0e3048e911d.sketch_text.stroke-45"),sQuery(id+"FHMxAyK4CFUKdhS_1.wireOp",EDGE,"1cb9c079-ea9b-4899-8069-e0e3048e911d.sketch_text.stroke-46"),sQuery(id+"FHMxAyK4CFUKdhS_1.wireOp",EDGE,"1cb9c079-ea9b-4899-8069-e0e3048e911d.sketch_text.stroke-47"),sQuery(id+"FHMxAyK4CFUKdhS_1.wireOp",EDGE,"1cb9c079-ea9b-4899-8069-e0e3048e911d.sketch_text.stroke-48"),sQuery(id+"FHMxAyK4CFUKdhS_1.wireOp",EDGE,"1cb9c079-ea9b-4899-8069-e0e3048e911d.sketch_text.stroke-49"),sQuery(id+"FHMxAyK4CFUKdhS_1.wireOp",EDGE,"1cb9c079-ea9b-4899-8069-e0e3048e911d.sketch_text.stroke-50"),sQuery(id+"FHMxAyK4CFUKdhS_1.wireOp",EDGE,"1cb9c079-ea9b-4899-8069-e0e3048e911d.sketch_text.stroke-51"),sQuery(id+"FHMxAyK4CFUKdhS_1.wireOp",EDGE,"1cb9c079-ea9b-4899-8069-e0e3048e911d.sketch_text.stroke-52"),sQuery(id+"FHMxAyK4CFUKdhS_1.wireOp",EDGE,"1cb9c079-ea9b-4899-8069-e0e3048e911d.sketch_text.stroke-53"),sQuery(id+"FHMxAyK4CFUKdhS_1.wireOp",EDGE,"1cb9c079-ea9b-4899-8069-e0e3048e911d.sketch_text.stroke-54"),sQuery(id+"FHMxAyK4CFUKdhS_1.wireOp",EDGE,"1cb9c079-ea9b-4899-8069-e0e3048e911d.sketch_text.stroke-55"),sQuery(id+"FHMxAyK4CFUKdhS_1.wireOp",EDGE,"1cb9c079-ea9b-4899-8069-e0e3048e911d.sketch_text.stroke-56"),sQuery(id+"FHMxAyK4CFUKdhS_1.wireOp",EDGE,"1cb9c079-ea9b-4899-8069-e0e3048e911d.sketch_text.stroke-57"),sQuery(id+"FHMxAyK4CFUKdhS_1.wireOp",EDGE,"1cb9c079-ea9b-4899-8069-e0e3048e911d.sketch_text.stroke-58"),sQuery(id+"FHMxAyK4CFUKdhS_1.wireOp",EDGE,"1cb9c079-ea9b-4899-8069-e0e3048e911d.sketch_text.stroke-59"),sQuery(id+"FHMxAyK4CFUKdhS_1.wireOp",EDGE,"1cb9c079-ea9b-4899-8069-e0e3048e911d.sketch_text.stroke-60"),sQuery(id+"FHMxAyK4CFUKdhS_1.wireOp",EDGE,"1cb9c079-ea9b-4899-8069-e0e3048e911d.sketch_text.stroke-61"),sQuery(id+"FHMxAyK4CFUKdhS_1.wireOp",EDGE,"1cb9c079-ea9b-4899-8069-e0e3048e911d.sketch_text.stroke-62"),sQuery(id+"FHMxAyK4CFUKdhS_1.wireOp",EDGE,"1cb9c079-ea9b-4899-8069-e0e3048e911d.sketch_text.stroke-71"),sQuery(id+"FHMxAyK4CFUKdhS_1.wireOp",EDGE,"1cb9c079-ea9b-4899-8069-e0e3048e911d.sketch_text.stroke-72"),sQuery(id+"FHMxAyK4CFUKdhS_1.wireOp",EDGE,"1cb9c079-ea9b-4899-8069-e0e3048e911d.sketch_text.stroke-73"),sQuery(id+"FHMxAyK4CFUKdhS_1.wireOp",EDGE,"1cb9c079-ea9b-4899-8069-e0e3048e911d.sketch_text.stroke-74"),sQuery(id+"FHMxAyK4CFUKdhS_1.wireOp",EDGE,"1cb9c079-ea9b-4899-8069-e0e3048e911d.sketch_text.stroke-75"),sQuery(id+"FHMxAyK4CFUKdhS_1.wireOp",EDGE,"1cb9c079-ea9b-4899-8069-e0e3048e911d.sketch_text.stroke-76"),sQuery(id+"FHMxAyK4CFUKdhS_1.wireOp",EDGE,"1cb9c079-ea9b-4899-8069-e0e3048e911d.sketch_text.stroke-77"),sQuery(id+"FHMxAyK4CFUKdhS_1.wireOp",EDGE,"1cb9c079-ea9b-4899-8069-e0e3048e911d.sketch_text.stroke-78"),sQuery(id+"FHMxAyK4CFUKdhS_1.wireOp",EDGE,"1cb9c079-ea9b-4899-8069-e0e3048e911d.sketch_text.stroke-79"),sQuery(id+"FHMxAyK4CFUKdhS_1.wireOp",EDGE,"1cb9c079-ea9b-4899-8069-e0e3048e911d.sketch_text.stroke-80"),sQuery(id+"FHMxAyK4CFUKdhS_1.wireOp",EDGE,"1cb9c079-ea9b-4899-8069-e0e3048e911d.sketch_text.stroke-81"),sQuery(id+"FHMxAyK4CFUKdhS_1.wireOp",EDGE,"1cb9c079-ea9b-4899-8069-e0e3048e911d.sketch_text.stroke-82"),sQuery(id+"FHMxAyK4CFUKdhS_1.wireOp",EDGE,"1cb9c079-ea9b-4899-8069-e0e3048e911d.sketch_text.stroke-83"),sQuery(id+"FHMxAyK4CFUKdhS_1.wireOp",EDGE,"1cb9c079-ea9b-4899-8069-e0e3048e911d.sketch_text.stroke-84"),sQuery(id+"FHMxAyK4CFUKdhS_1.wireOp",EDGE,"1cb9c079-ea9b-4899-8069-e0e3048e911d.sketch_text.stroke-85"),sQuery(id+"FHMxAyK4CFUKdhS_1.wireOp",EDGE,"1cb9c079-ea9b-4899-8069-e0e3048e911d.sketch_text.stroke-86"),sQuery(id+"FHMxAyK4CFUKdhS_1.wireOp",EDGE,"1cb9c079-ea9b-4899-8069-e0e3048e911d.sketch_text.stroke-87"),sQuery(id+"FHMxAyK4CFUKdhS_1.wireOp",EDGE,"1cb9c079-ea9b-4899-8069-e0e3048e911d.sketch_text.stroke-88"),sQuery(id+"FHMxAyK4CFUKdhS_1.wireOp",EDGE,"1cb9c079-ea9b-4899-8069-e0e3048e911d.sketch_text.stroke-89"),sQuery(id+"FHMxAyK4CFUKdhS_1.wireOp",EDGE,"1cb9c079-ea9b-4899-8069-e0e3048e911d.sketch_text.stroke-90"),sQuery(id+"FHMxAyK4CFUKdhS_1.wireOp",EDGE,"1cb9c079-ea9b-4899-8069-e0e3048e911d.sketch_text.stroke-91"),sQuery(id+"FHMxAyK4CFUKdhS_1.wireOp",EDGE,"1cb9c079-ea9b-4899-8069-e0e3048e911d.sketch_text.stroke-92"),sQuery(id+"FHMxAyK4CFUKdhS_1.wireOp",EDGE,"1cb9c079-ea9b-4899-8069-e0e3048e911d.sketch_text.stroke-93"),sQuery(id+"FHMxAyK4CFUKdhS_1.wireOp",EDGE,"1cb9c079-ea9b-4899-8069-e0e3048e911d.sketch_text.stroke-94"),sQuery(id+"FHMxAyK4CFUKdhS_1.wireOp",EDGE,"1cb9c079-ea9b-4899-8069-e0e3048e911d.sketch_text.stroke-95"),sQuery(id+"FHMxAyK4CFUKdhS_1.wireOp",EDGE,"1cb9c079-ea9b-4899-8069-e0e3048e911d.sketch_text.stroke-96"),sQuery(id+"FHMxAyK4CFUKdhS_1.wireOp",EDGE,"1cb9c079-ea9b-4899-8069-e0e3048e911d.sketch_text.stroke-97"),sQuery(id+"FHMxAyK4CFUKdhS_1.wireOp",EDGE,"1cb9c079-ea9b-4899-8069-e0e3048e911d.sketch_text.stroke-103"),sQuery(id+"FHMxAyK4CFUKdhS_1.wireOp",EDGE,"1cb9c079-ea9b-4899-8069-e0e3048e911d.sketch_text.stroke-104"),sQuery(id+"FHMxAyK4CFUKdhS_1.wireOp",EDGE,"1cb9c079-ea9b-4899-8069-e0e3048e911d.sketch_text.stroke-105"),sQuery(id+"FHMxAyK4CFUKdhS_1.wireOp",EDGE,"1cb9c079-ea9b-4899-8069-e0e3048e911d.sketch_text.stroke-106"),sQuery(id+"FHMxAyK4CFUKdhS_1.wireOp",EDGE,"1cb9c079-ea9b-4899-8069-e0e3048e911d.sketch_text.stroke-107"),sQuery(id+"FHMxAyK4CFUKdhS_1.wireOp",EDGE,"1cb9c079-ea9b-4899-8069-e0e3048e911d.sketch_text.stroke-108"),sQuery(id+"FHMxAyK4CFUKdhS_1.wireOp",EDGE,"1cb9c079-ea9b-4899-8069-e0e3048e911d.sketch_text.stroke-109"),sQuery(id+"FHMxAyK4CFUKdhS_1.wireOp",EDGE,"1cb9c079-ea9b-4899-8069-e0e3048e911d.sketch_text.stroke-110"),sQuery(id+"FHMxAyK4CFUKdhS_1.wireOp",EDGE,"1cb9c079-ea9b-4899-8069-e0e3048e911d.sketch_text.stroke-111"),sQuery(id+"FHMxAyK4CFUKdhS_1.wireOp",EDGE,"1cb9c079-ea9b-4899-8069-e0e3048e911d.sketch_text.stroke-112"),sQuery(id+"FHMxAyK4CFUKdhS_1.wireOp",EDGE,"1cb9c079-ea9b-4899-8069-e0e3048e911d.sketch_text.stroke-113"),sQuery(id+"FHMxAyK4CFUKdhS_1.wireOp",EDGE,"1cb9c079-ea9b-4899-8069-e0e3048e911d.sketch_text.stroke-114"),sQuery(id+"FHMxAyK4CFUKdhS_1.wireOp",EDGE,"1cb9c079-ea9b-4899-8069-e0e3048e911d.sketch_text.stroke-115"),sQuery(id+"FHMxAyK4CFUKdhS_1.wireOp",EDGE,"1cb9c079-ea9b-4899-8069-e0e3048e911d.sketch_text.stroke-116"),sQuery(id+"FHMxAyK4CFUKdhS_1.wireOp",EDGE,"1cb9c079-ea9b-4899-8069-e0e3048e911d.sketch_text.stroke-117"),sQuery(id+"FHMxAyK4CFUKdhS_1.wireOp",EDGE,"1cb9c079-ea9b-4899-8069-e0e3048e911d.sketch_text.stroke-118"),sQuery(id+"FHMxAyK4CFUKdhS_1.wireOp",EDGE,"1cb9c079-ea9b-4899-8069-e0e3048e911d.sketch_text.stroke-119"),sQuery(id+"FHMxAyK4CFUKdhS_1.wireOp",EDGE,"1cb9c079-ea9b-4899-8069-e0e3048e911d.sketch_text.stroke-120"),sQuery(id+"FHMxAyK4CFUKdhS_1.wireOp",EDGE,"1cb9c079-ea9b-4899-8069-e0e3048e911d.sketch_text.stroke-121"),sQuery(id+"FHMxAyK4CFUKdhS_1.wireOp",EDGE,"1cb9c079-ea9b-4899-8069-e0e3048e911d.sketch_text.stroke-122"),sQuery(id+"FHMxAyK4CFUKdhS_1.wireOp",EDGE,"1cb9c079-ea9b-4899-8069-e0e3048e911d.sketch_text.stroke-123"),sQuery(id+"FHMxAyK4CFUKdhS_1.wireOp",EDGE,"1cb9c079-ea9b-4899-8069-e0e3048e911d.sketch_text.stroke-124"),sQuery(id+"FHMxAyK4CFUKdhS_1.wireOp",EDGE,"1cb9c079-ea9b-4899-8069-e0e3048e911d.sketch_text.stroke-125"),sQuery(id+"FHMxAyK4CFUKdhS_1.wireOp",EDGE,"1cb9c079-ea9b-4899-8069-e0e3048e911d.sketch_text.stroke-126"),sQuery(id+"FHMxAyK4CFUKdhS_1.wireOp",EDGE,"1cb9c079-ea9b-4899-8069-e0e3048e911d.sketch_text.stroke-127"),sQuery(id+"FHMxAyK4CFUKdhS_1.wireOp",EDGE,"1cb9c079-ea9b-4899-8069-e0e3048e911d.sketch_text.stroke-128"),sQuery(id+"FHMxAyK4CFUKdhS_1.wireOp",EDGE,"1cb9c079-ea9b-4899-8069-e0e3048e911d.sketch_text.stroke-129"),sQuery(id+"FHMxAyK4CFUKdhS_1.wireOp",EDGE,"1cb9c079-ea9b-4899-8069-e0e3048e911d.sketch_text.stroke-130"),sQuery(id+"FHMxAyK4CFUKdhS_1.wireOp",EDGE,"1cb9c079-ea9b-4899-8069-e0e3048e911d.sketch_text.stroke-131"),sQuery(id+"FHMxAyK4CFUKdhS_1.wireOp",EDGE,"1cb9c079-ea9b-4899-8069-e0e3048e911d.sketch_text.stroke-132"),sQuery(id+"FHMxAyK4CFUKdhS_1.wireOp",EDGE,"1cb9c079-ea9b-4899-8069-e0e3048e911d.sketch_text.stroke-133"),sQuery(id+"FHMxAyK4CFUKdhS_1.wireOp",EDGE,"1cb9c079-ea9b-4899-8069-e0e3048e911d.sketch_text.stroke-134"),sQuery(id+"FHMxAyK4CFUKdhS_1.wireOp",EDGE,"1cb9c079-ea9b-4899-8069-e0e3048e911d.sketch_text.stroke-135"),sQuery(id+"FHMxAyK4CFUKdhS_1.wireOp",EDGE,"1cb9c079-ea9b-4899-8069-e0e3048e911d.sketch_text.stroke-136"),sQuery(id+"FHMxAyK4CFUKdhS_1.wireOp",EDGE,"1cb9c079-ea9b-4899-8069-e0e3048e911d.sketch_text.stroke-137"),sQuery(id+"FHMxAyK4CFUKdhS_1.wireOp",EDGE,"1cb9c079-ea9b-4899-8069-e0e3048e911d.sketch_text.stroke-138"),sQuery(id+"FHMxAyK4CFUKdhS_1.wireOp",EDGE,"1cb9c079-ea9b-4899-8069-e0e3048e911d.sketch_text.stroke-139"),sQuery(id+"FHMxAyK4CFUKdhS_1.wireOp",EDGE,"1cb9c079-ea9b-4899-8069-e0e3048e911d.sketch_text.stroke-140"),sQuery(id+"FHMxAyK4CFUKdhS_1.wireOp",EDGE,"1cb9c079-ea9b-4899-8069-e0e3048e911d.sketch_text.stroke-141"),sQuery(id+"FHMxAyK4CFUKdhS_1.wireOp",EDGE,"1cb9c079-ea9b-4899-8069-e0e3048e911d.sketch_text.stroke-142"),sQuery(id+"FHMxAyK4CFUKdhS_1.wireOp",EDGE,"1cb9c079-ea9b-4899-8069-e0e3048e911d.sketch_text.stroke-143"),sQuery(id+"FHMxAyK4CFUKdhS_1.wireOp",EDGE,"1cb9c079-ea9b-4899-8069-e0e3048e911d.sketch_text.stroke-144"),sQuery(id+"FHMxAyK4CFUKdhS_1.wireOp",EDGE,"1cb9c079-ea9b-4899-8069-e0e3048e911d.sketch_text.stroke-145"),sQuery(id+"FHMxAyK4CFUKdhS_1.wireOp",EDGE,"1cb9c079-ea9b-4899-8069-e0e3048e911d.sketch_text.stroke-146"),sQuery(id+"FHMxAyK4CFUKdhS_1.wireOp",EDGE,"1cb9c079-ea9b-4899-8069-e0e3048e911d.sketch_text.stroke-147"),sQuery(id+"FHMxAyK4CFUKdhS_1.wireOp",EDGE,"1cb9c079-ea9b-4899-8069-e0e3048e911d.sketch_text.stroke-148"),sQuery(id+"FHMxAyK4CFUKdhS_1.wireOp",EDGE,"1cb9c079-ea9b-4899-8069-e0e3048e911d.sketch_text.stroke-149"),sQuery(id+"FHMxAyK4CFUKdhS_1.wireOp",EDGE,"1cb9c079-ea9b-4899-8069-e0e3048e911d.sketch_text.stroke-150"),sQuery(id+"FHMxAyK4CFUKdhS_1.wireOp",EDGE,"1cb9c079-ea9b-4899-8069-e0e3048e911d.sketch_text.stroke-151"),sQuery(id+"FHMxAyK4CFUKdhS_1.wireOp",EDGE,"1cb9c079-ea9b-4899-8069-e0e3048e911d.sketch_text.stroke-152"),sQuery(id+"FHMxAyK4CFUKdhS_1.wireOp",EDGE,"1cb9c079-ea9b-4899-8069-e0e3048e911d.sketch_text.stroke-153"),sQuery(id+"FHMxAyK4CFUKdhS_1.wireOp",EDGE,"1cb9c079-ea9b-4899-8069-e0e3048e911d.sketch_text.stroke-159"),sQuery(id+"FHMxAyK4CFUKdhS_1.wireOp",EDGE,"1cb9c079-ea9b-4899-8069-e0e3048e911d.sketch_text.stroke-160"),sQuery(id+"FHMxAyK4CFUKdhS_1.wireOp",EDGE,"1cb9c079-ea9b-4899-8069-e0e3048e911d.sketch_text.stroke-161"),sQuery(id+"FHMxAyK4CFUKdhS_1.wireOp",EDGE,"1cb9c079-ea9b-4899-8069-e0e3048e911d.sketch_text.stroke-162"),sQuery(id+"FHMxAyK4CFUKdhS_1.wireOp",EDGE,"1cb9c079-ea9b-4899-8069-e0e3048e911d.sketch_text.stroke-163"),sQuery(id+"FHMxAyK4CFUKdhS_1.wireOp",EDGE,"1cb9c079-ea9b-4899-8069-e0e3048e911d.sketch_text.stroke-164"),sQuery(id+"FHMxAyK4CFUKdhS_1.wireOp",EDGE,"1cb9c079-ea9b-4899-8069-e0e3048e911d.sketch_text.stroke-165"),sQuery(id+"FHMxAyK4CFUKdhS_1.wireOp",EDGE,"1cb9c079-ea9b-4899-8069-e0e3048e911d.sketch_text.stroke-166"),sQuery(id+"FHMxAyK4CFUKdhS_1.wireOp",EDGE,"1cb9c079-ea9b-4899-8069-e0e3048e911d.sketch_text.stroke-167"),sQuery(id+"FHMxAyK4CFUKdhS_1.wireOp",EDGE,"1cb9c079-ea9b-4899-8069-e0e3048e911d.sketch_text.stroke-168"),sQuery(id+"FHMxAyK4CFUKdhS_1.wireOp",EDGE,"1cb9c079-ea9b-4899-8069-e0e3048e911d.sketch_text.stroke-169"),sQuery(id+"FHMxAyK4CFUKdhS_1.wireOp",EDGE,"1cb9c079-ea9b-4899-8069-e0e3048e911d.sketch_text.stroke-170"),sQuery(id+"FHMxAyK4CFUKdhS_1.wireOp",EDGE,"1cb9c079-ea9b-4899-8069-e0e3048e911d.sketch_text.stroke-171"),sQuery(id+"FHMxAyK4CFUKdhS_1.wireOp",EDGE,"1cb9c079-ea9b-4899-8069-e0e3048e911d.sketch_text.stroke-172"),sQuery(id+"FHMxAyK4CFUKdhS_1.wireOp",EDGE,"1cb9c079-ea9b-4899-8069-e0e3048e911d.sketch_text.stroke-173"),sQuery(id+"FHMxAyK4CFUKdhS_1.wireOp",EDGE,"1cb9c079-ea9b-4899-8069-e0e3048e911d.sketch_text.stroke-174"),sQuery(id+"FHMxAyK4CFUKdhS_1.wireOp",EDGE,"1cb9c079-ea9b-4899-8069-e0e3048e911d.sketch_text.stroke-175"),sQuery(id+"FHMxAyK4CFUKdhS_1.wireOp",EDGE,"1cb9c079-ea9b-4899-8069-e0e3048e911d.sketch_text.stroke-176"),sQuery(id+"FHMxAyK4CFUKdhS_1.wireOp",EDGE,"1cb9c079-ea9b-4899-8069-e0e3048e911d.sketch_text.stroke-177"),sQuery(id+"FHMxAyK4CFUKdhS_1.wireOp",EDGE,"1cb9c079-ea9b-4899-8069-e0e3048e911d.sketch_text.stroke-178"),sQuery(id+"FHMxAyK4CFUKdhS_1.wireOp",EDGE,"1cb9c079-ea9b-4899-8069-e0e3048e911d.sketch_text.stroke-179"),sQuery(id+"FHMxAyK4CFUKdhS_1.wireOp",EDGE,"1cb9c079-ea9b-4899-8069-e0e3048e911d.sketch_text.stroke-180"),subQ2,sQuery(id+"F3.wireOp",EDGE,"E30")])],"isStart":true})]),OD(1.0)],"derivedFrom":makeQuery(id+"F1.opExtrude","CAP_EDGE",EDGE,{"disambiguationData":[OSD([subQ0])],"isStart":false})});}
            var Q25;
            {var subQ0=sQuery(id+"F0.wireOp",EDGE,"E0.top");var subQ1=sQuery(id+"F0.wireOp",EDGE,"E0.bottom");var subQ2=sQuery(id+"F3.wireOp",EDGE,"E29");Q25=makeQuery(id+"F4.boolean.opBoolean","SPLIT",EDGE,{"disambiguationData":[TD([makeQuery(id+"F1.opExtrude","CAP_FACE",FACE,{"disambiguationData":[OSD([subQ1,subQ0,sQuery(id+"F0.wireOp",EDGE,"E0.left"),sQuery(id+"F0.wireOp",EDGE,"E0.right")])],"isStart":false}),makeQuery(id+"F1.opExtrude","SWEPT_FACE",FACE,{"disambiguationData":[OSD([subQ0])]}),makeQuery(id+"F4.opExtrude","SWEPT_FACE",FACE,{"disambiguationData":[OSD([subQ2])]}),makeQuery(id+"F4.opExtrude","CAP_FACE",FACE,{"disambiguationData":[OSD([subQ1,sQuery(id+"F2.wireOp",EDGE,"fcba4419-a2ee-464f-be9d-58f11bf3418b.sketch_text.stroke-0"),sQuery(id+"F2.wireOp",EDGE,"fcba4419-a2ee-464f-be9d-58f11bf3418b.sketch_text.stroke-1"),sQuery(id+"F2.wireOp",EDGE,"fcba4419-a2ee-464f-be9d-58f11bf3418b.sketch_text.stroke-2"),sQuery(id+"F2.wireOp",EDGE,"fcba4419-a2ee-464f-be9d-58f11bf3418b.sketch_text.stroke-3"),sQuery(id+"F2.wireOp",EDGE,"fcba4419-a2ee-464f-be9d-58f11bf3418b.sketch_text.stroke-4"),sQuery(id+"F2.wireOp",EDGE,"fcba4419-a2ee-464f-be9d-58f11bf3418b.sketch_text.stroke-5"),sQuery(id+"F2.wireOp",EDGE,"fcba4419-a2ee-464f-be9d-58f11bf3418b.sketch_text.stroke-6"),sQuery(id+"F2.wireOp",EDGE,"fcba4419-a2ee-464f-be9d-58f11bf3418b.sketch_text.stroke-7"),sQuery(id+"F2.wireOp",EDGE,"fcba4419-a2ee-464f-be9d-58f11bf3418b.sketch_text.stroke-8"),sQuery(id+"F2.wireOp",EDGE,"fcba4419-a2ee-464f-be9d-58f11bf3418b.sketch_text.stroke-9"),sQuery(id+"F2.wireOp",EDGE,"fcba4419-a2ee-464f-be9d-58f11bf3418b.sketch_text.stroke-10"),sQuery(id+"F2.wireOp",EDGE,"fcba4419-a2ee-464f-be9d-58f11bf3418b.sketch_text.stroke-11"),sQuery(id+"F2.wireOp",EDGE,"fcba4419-a2ee-464f-be9d-58f11bf3418b.sketch_text.stroke-12"),sQuery(id+"F2.wireOp",EDGE,"fcba4419-a2ee-464f-be9d-58f11bf3418b.sketch_text.stroke-13"),sQuery(id+"F2.wireOp",EDGE,"fcba4419-a2ee-464f-be9d-58f11bf3418b.sketch_text.stroke-14"),sQuery(id+"F2.wireOp",EDGE,"fcba4419-a2ee-464f-be9d-58f11bf3418b.sketch_text.stroke-15"),sQuery(id+"F2.wireOp",EDGE,"fcba4419-a2ee-464f-be9d-58f11bf3418b.sketch_text.stroke-16"),sQuery(id+"F2.wireOp",EDGE,"fcba4419-a2ee-464f-be9d-58f11bf3418b.sketch_text.stroke-17"),sQuery(id+"F2.wireOp",EDGE,"fcba4419-a2ee-464f-be9d-58f11bf3418b.sketch_text.stroke-18"),sQuery(id+"F2.wireOp",EDGE,"fcba4419-a2ee-464f-be9d-58f11bf3418b.sketch_text.stroke-19"),sQuery(id+"F2.wireOp",EDGE,"fcba4419-a2ee-464f-be9d-58f11bf3418b.sketch_text.stroke-20"),sQuery(id+"F2.wireOp",EDGE,"fcba4419-a2ee-464f-be9d-58f11bf3418b.sketch_text.stroke-21"),sQuery(id+"F2.wireOp",EDGE,"fcba4419-a2ee-464f-be9d-58f11bf3418b.sketch_text.stroke-22"),sQuery(id+"F2.wireOp",EDGE,"fcba4419-a2ee-464f-be9d-58f11bf3418b.sketch_text.stroke-23"),sQuery(id+"F2.wireOp",EDGE,"fcba4419-a2ee-464f-be9d-58f11bf3418b.sketch_text.stroke-24"),sQuery(id+"F2.wireOp",EDGE,"fcba4419-a2ee-464f-be9d-58f11bf3418b.sketch_text.stroke-25"),sQuery(id+"F2.wireOp",EDGE,"fcba4419-a2ee-464f-be9d-58f11bf3418b.sketch_text.stroke-26"),sQuery(id+"F2.wireOp",EDGE,"fcba4419-a2ee-464f-be9d-58f11bf3418b.sketch_text.stroke-27"),sQuery(id+"F2.wireOp",EDGE,"fcba4419-a2ee-464f-be9d-58f11bf3418b.sketch_text.stroke-28"),sQuery(id+"F2.wireOp",EDGE,"fcba4419-a2ee-464f-be9d-58f11bf3418b.sketch_text.stroke-29"),sQuery(id+"F2.wireOp",EDGE,"fcba4419-a2ee-464f-be9d-58f11bf3418b.sketch_text.stroke-30"),sQuery(id+"F2.wireOp",EDGE,"fcba4419-a2ee-464f-be9d-58f11bf3418b.sketch_text.stroke-31"),sQuery(id+"F2.wireOp",EDGE,"fcba4419-a2ee-464f-be9d-58f11bf3418b.sketch_text.stroke-32"),sQuery(id+"F2.wireOp",EDGE,"fcba4419-a2ee-464f-be9d-58f11bf3418b.sketch_text.stroke-33"),sQuery(id+"F2.wireOp",EDGE,"fcba4419-a2ee-464f-be9d-58f11bf3418b.sketch_text.stroke-34"),sQuery(id+"F2.wireOp",EDGE,"fcba4419-a2ee-464f-be9d-58f11bf3418b.sketch_text.stroke-35"),sQuery(id+"F2.wireOp",EDGE,"fcba4419-a2ee-464f-be9d-58f11bf3418b.sketch_text.stroke-36"),sQuery(id+"F2.wireOp",EDGE,"fcba4419-a2ee-464f-be9d-58f11bf3418b.sketch_text.stroke-37"),sQuery(id+"F2.wireOp",EDGE,"fcba4419-a2ee-464f-be9d-58f11bf3418b.sketch_text.stroke-38"),sQuery(id+"F2.wireOp",EDGE,"fcba4419-a2ee-464f-be9d-58f11bf3418b.sketch_text.stroke-39"),sQuery(id+"F2.wireOp",EDGE,"fcba4419-a2ee-464f-be9d-58f11bf3418b.sketch_text.stroke-40"),sQuery(id+"F2.wireOp",EDGE,"fcba4419-a2ee-464f-be9d-58f11bf3418b.sketch_text.stroke-41"),sQuery(id+"F2.wireOp",EDGE,"fcba4419-a2ee-464f-be9d-58f11bf3418b.sketch_text.stroke-42"),sQuery(id+"F2.wireOp",EDGE,"fcba4419-a2ee-464f-be9d-58f11bf3418b.sketch_text.stroke-43"),sQuery(id+"F2.wireOp",EDGE,"fcba4419-a2ee-464f-be9d-58f11bf3418b.sketch_text.stroke-44"),sQuery(id+"F2.wireOp",EDGE,"fcba4419-a2ee-464f-be9d-58f11bf3418b.sketch_text.stroke-45"),sQuery(id+"F2.wireOp",EDGE,"fcba4419-a2ee-464f-be9d-58f11bf3418b.sketch_text.stroke-46"),sQuery(id+"F2.wireOp",EDGE,"fcba4419-a2ee-464f-be9d-58f11bf3418b.sketch_text.stroke-47"),sQuery(id+"F2.wireOp",EDGE,"fcba4419-a2ee-464f-be9d-58f11bf3418b.sketch_text.stroke-48"),sQuery(id+"F2.wireOp",EDGE,"fcba4419-a2ee-464f-be9d-58f11bf3418b.sketch_text.stroke-49"),sQuery(id+"F2.wireOp",EDGE,"fcba4419-a2ee-464f-be9d-58f11bf3418b.sketch_text.stroke-50"),sQuery(id+"F2.wireOp",EDGE,"fcba4419-a2ee-464f-be9d-58f11bf3418b.sketch_text.stroke-51"),sQuery(id+"F2.wireOp",EDGE,"fcba4419-a2ee-464f-be9d-58f11bf3418b.sketch_text.stroke-52"),sQuery(id+"F2.wireOp",EDGE,"fcba4419-a2ee-464f-be9d-58f11bf3418b.sketch_text.stroke-53"),sQuery(id+"F2.wireOp",EDGE,"fcba4419-a2ee-464f-be9d-58f11bf3418b.sketch_text.stroke-54"),sQuery(id+"F2.wireOp",EDGE,"fcba4419-a2ee-464f-be9d-58f11bf3418b.sketch_text.stroke-55"),sQuery(id+"F2.wireOp",EDGE,"fcba4419-a2ee-464f-be9d-58f11bf3418b.sketch_text.stroke-56"),sQuery(id+"F2.wireOp",EDGE,"fcba4419-a2ee-464f-be9d-58f11bf3418b.sketch_text.stroke-57"),sQuery(id+"F2.wireOp",EDGE,"fcba4419-a2ee-464f-be9d-58f11bf3418b.sketch_text.stroke-58"),sQuery(id+"F2.wireOp",EDGE,"fcba4419-a2ee-464f-be9d-58f11bf3418b.sketch_text.stroke-59"),sQuery(id+"F2.wireOp",EDGE,"fcba4419-a2ee-464f-be9d-58f11bf3418b.sketch_text.stroke-60"),sQuery(id+"F2.wireOp",EDGE,"fcba4419-a2ee-464f-be9d-58f11bf3418b.sketch_text.stroke-61"),sQuery(id+"F2.wireOp",EDGE,"fcba4419-a2ee-464f-be9d-58f11bf3418b.sketch_text.stroke-62"),sQuery(id+"F2.wireOp",EDGE,"fcba4419-a2ee-464f-be9d-58f11bf3418b.sketch_text.stroke-63"),sQuery(id+"F2.wireOp",EDGE,"fcba4419-a2ee-464f-be9d-58f11bf3418b.sketch_text.stroke-64"),sQuery(id+"F2.wireOp",EDGE,"fcba4419-a2ee-464f-be9d-58f11bf3418b.sketch_text.stroke-65"),sQuery(id+"F2.wireOp",EDGE,"fcba4419-a2ee-464f-be9d-58f11bf3418b.sketch_text.stroke-66"),sQuery(id+"F2.wireOp",EDGE,"fcba4419-a2ee-464f-be9d-58f11bf3418b.sketch_text.stroke-67"),sQuery(id+"F2.wireOp",EDGE,"fcba4419-a2ee-464f-be9d-58f11bf3418b.sketch_text.stroke-68"),sQuery(id+"F2.wireOp",EDGE,"fcba4419-a2ee-464f-be9d-58f11bf3418b.sketch_text.stroke-69"),sQuery(id+"F2.wireOp",EDGE,"fcba4419-a2ee-464f-be9d-58f11bf3418b.sketch_text.stroke-70"),sQuery(id+"F2.wireOp",EDGE,"fcba4419-a2ee-464f-be9d-58f11bf3418b.sketch_text.stroke-71"),sQuery(id+"F2.wireOp",EDGE,"fcba4419-a2ee-464f-be9d-58f11bf3418b.sketch_text.stroke-72"),sQuery(id+"F2.wireOp",EDGE,"fcba4419-a2ee-464f-be9d-58f11bf3418b.sketch_text.stroke-73"),sQuery(id+"F2.wireOp",EDGE,"fcba4419-a2ee-464f-be9d-58f11bf3418b.sketch_text.stroke-74"),sQuery(id+"F2.wireOp",EDGE,"fcba4419-a2ee-464f-be9d-58f11bf3418b.sketch_text.stroke-75"),sQuery(id+"F2.wireOp",EDGE,"fcba4419-a2ee-464f-be9d-58f11bf3418b.sketch_text.stroke-76"),sQuery(id+"F2.wireOp",EDGE,"fcba4419-a2ee-464f-be9d-58f11bf3418b.sketch_text.stroke-77"),sQuery(id+"F2.wireOp",EDGE,"fcba4419-a2ee-464f-be9d-58f11bf3418b.sketch_text.stroke-78"),sQuery(id+"F2.wireOp",EDGE,"fcba4419-a2ee-464f-be9d-58f11bf3418b.sketch_text.stroke-79"),sQuery(id+"F2.wireOp",EDGE,"fcba4419-a2ee-464f-be9d-58f11bf3418b.sketch_text.stroke-80"),sQuery(id+"F2.wireOp",EDGE,"fcba4419-a2ee-464f-be9d-58f11bf3418b.sketch_text.stroke-81"),sQuery(id+"F2.wireOp",EDGE,"fcba4419-a2ee-464f-be9d-58f11bf3418b.sketch_text.stroke-82"),sQuery(id+"F2.wireOp",EDGE,"fcba4419-a2ee-464f-be9d-58f11bf3418b.sketch_text.stroke-83"),sQuery(id+"F2.wireOp",EDGE,"fcba4419-a2ee-464f-be9d-58f11bf3418b.sketch_text.stroke-84"),sQuery(id+"F2.wireOp",EDGE,"fcba4419-a2ee-464f-be9d-58f11bf3418b.sketch_text.stroke-85"),sQuery(id+"F2.wireOp",EDGE,"fcba4419-a2ee-464f-be9d-58f11bf3418b.sketch_text.stroke-86"),sQuery(id+"F2.wireOp",EDGE,"fcba4419-a2ee-464f-be9d-58f11bf3418b.sketch_text.stroke-87"),sQuery(id+"F2.wireOp",EDGE,"fcba4419-a2ee-464f-be9d-58f11bf3418b.sketch_text.stroke-88"),sQuery(id+"F2.wireOp",EDGE,"fcba4419-a2ee-464f-be9d-58f11bf3418b.sketch_text.stroke-89"),sQuery(id+"F2.wireOp",EDGE,"fcba4419-a2ee-464f-be9d-58f11bf3418b.sketch_text.stroke-90"),sQuery(id+"F2.wireOp",EDGE,"fcba4419-a2ee-464f-be9d-58f11bf3418b.sketch_text.stroke-91"),sQuery(id+"F2.wireOp",EDGE,"fcba4419-a2ee-464f-be9d-58f11bf3418b.sketch_text.stroke-92"),sQuery(id+"F2.wireOp",EDGE,"fcba4419-a2ee-464f-be9d-58f11bf3418b.sketch_text.stroke-93"),sQuery(id+"F2.wireOp",EDGE,"fcba4419-a2ee-464f-be9d-58f11bf3418b.sketch_text.stroke-94"),sQuery(id+"F2.wireOp",EDGE,"fcba4419-a2ee-464f-be9d-58f11bf3418b.sketch_text.stroke-95"),sQuery(id+"F2.wireOp",EDGE,"fcba4419-a2ee-464f-be9d-58f11bf3418b.sketch_text.stroke-96"),sQuery(id+"F2.wireOp",EDGE,"fcba4419-a2ee-464f-be9d-58f11bf3418b.sketch_text.stroke-97"),sQuery(id+"F2.wireOp",EDGE,"fcba4419-a2ee-464f-be9d-58f11bf3418b.sketch_text.stroke-98"),sQuery(id+"F2.wireOp",EDGE,"fcba4419-a2ee-464f-be9d-58f11bf3418b.sketch_text.stroke-99"),sQuery(id+"F2.wireOp",EDGE,"fcba4419-a2ee-464f-be9d-58f11bf3418b.sketch_text.stroke-100"),sQuery(id+"F2.wireOp",EDGE,"fcba4419-a2ee-464f-be9d-58f11bf3418b.sketch_text.stroke-101"),sQuery(id+"F2.wireOp",EDGE,"fcba4419-a2ee-464f-be9d-58f11bf3418b.sketch_text.stroke-102"),sQuery(id+"F2.wireOp",EDGE,"fcba4419-a2ee-464f-be9d-58f11bf3418b.sketch_text.stroke-103"),sQuery(id+"F2.wireOp",EDGE,"fcba4419-a2ee-464f-be9d-58f11bf3418b.sketch_text.stroke-104"),sQuery(id+"F2.wireOp",EDGE,"fcba4419-a2ee-464f-be9d-58f11bf3418b.sketch_text.stroke-105"),sQuery(id+"F2.wireOp",EDGE,"fcba4419-a2ee-464f-be9d-58f11bf3418b.sketch_text.stroke-106"),sQuery(id+"F2.wireOp",EDGE,"fcba4419-a2ee-464f-be9d-58f11bf3418b.sketch_text.stroke-107"),sQuery(id+"F2.wireOp",EDGE,"fcba4419-a2ee-464f-be9d-58f11bf3418b.sketch_text.stroke-108"),sQuery(id+"F2.wireOp",EDGE,"fcba4419-a2ee-464f-be9d-58f11bf3418b.sketch_text.stroke-109"),sQuery(id+"F2.wireOp",EDGE,"fcba4419-a2ee-464f-be9d-58f11bf3418b.sketch_text.stroke-110"),sQuery(id+"F2.wireOp",EDGE,"fcba4419-a2ee-464f-be9d-58f11bf3418b.sketch_text.stroke-111"),sQuery(id+"F2.wireOp",EDGE,"fcba4419-a2ee-464f-be9d-58f11bf3418b.sketch_text.stroke-112"),sQuery(id+"F2.wireOp",EDGE,"fcba4419-a2ee-464f-be9d-58f11bf3418b.sketch_text.stroke-113"),sQuery(id+"F2.wireOp",EDGE,"fcba4419-a2ee-464f-be9d-58f11bf3418b.sketch_text.stroke-114"),sQuery(id+"F2.wireOp",EDGE,"fcba4419-a2ee-464f-be9d-58f11bf3418b.sketch_text.stroke-115"),sQuery(id+"F2.wireOp",EDGE,"fcba4419-a2ee-464f-be9d-58f11bf3418b.sketch_text.stroke-116"),sQuery(id+"F2.wireOp",EDGE,"fcba4419-a2ee-464f-be9d-58f11bf3418b.sketch_text.stroke-117"),sQuery(id+"F2.wireOp",EDGE,"fcba4419-a2ee-464f-be9d-58f11bf3418b.sketch_text.stroke-118"),sQuery(id+"F2.wireOp",EDGE,"fcba4419-a2ee-464f-be9d-58f11bf3418b.sketch_text.stroke-119"),sQuery(id+"F2.wireOp",EDGE,"fcba4419-a2ee-464f-be9d-58f11bf3418b.sketch_text.stroke-120"),sQuery(id+"F2.wireOp",EDGE,"fcba4419-a2ee-464f-be9d-58f11bf3418b.sketch_text.stroke-121"),sQuery(id+"F2.wireOp",EDGE,"fcba4419-a2ee-464f-be9d-58f11bf3418b.sketch_text.stroke-122"),sQuery(id+"F2.wireOp",EDGE,"fcba4419-a2ee-464f-be9d-58f11bf3418b.sketch_text.stroke-123"),sQuery(id+"F2.wireOp",EDGE,"fcba4419-a2ee-464f-be9d-58f11bf3418b.sketch_text.stroke-124"),sQuery(id+"F2.wireOp",EDGE,"fcba4419-a2ee-464f-be9d-58f11bf3418b.sketch_text.stroke-125"),sQuery(id+"F2.wireOp",EDGE,"fcba4419-a2ee-464f-be9d-58f11bf3418b.sketch_text.stroke-126"),sQuery(id+"F2.wireOp",EDGE,"fcba4419-a2ee-464f-be9d-58f11bf3418b.sketch_text.stroke-127"),sQuery(id+"F2.wireOp",EDGE,"fcba4419-a2ee-464f-be9d-58f11bf3418b.sketch_text.stroke-128"),sQuery(id+"F2.wireOp",EDGE,"fcba4419-a2ee-464f-be9d-58f11bf3418b.sketch_text.stroke-129"),sQuery(id+"F2.wireOp",EDGE,"fcba4419-a2ee-464f-be9d-58f11bf3418b.sketch_text.stroke-130"),sQuery(id+"F2.wireOp",EDGE,"fcba4419-a2ee-464f-be9d-58f11bf3418b.sketch_text.stroke-131"),sQuery(id+"F2.wireOp",EDGE,"fcba4419-a2ee-464f-be9d-58f11bf3418b.sketch_text.stroke-132"),sQuery(id+"F2.wireOp",EDGE,"fcba4419-a2ee-464f-be9d-58f11bf3418b.sketch_text.stroke-133"),sQuery(id+"F2.wireOp",EDGE,"fcba4419-a2ee-464f-be9d-58f11bf3418b.sketch_text.stroke-134"),sQuery(id+"F2.wireOp",EDGE,"fcba4419-a2ee-464f-be9d-58f11bf3418b.sketch_text.stroke-135"),sQuery(id+"F2.wireOp",EDGE,"fcba4419-a2ee-464f-be9d-58f11bf3418b.sketch_text.stroke-136"),sQuery(id+"F2.wireOp",EDGE,"fcba4419-a2ee-464f-be9d-58f11bf3418b.sketch_text.stroke-137"),sQuery(id+"F2.wireOp",EDGE,"fcba4419-a2ee-464f-be9d-58f11bf3418b.sketch_text.stroke-138"),sQuery(id+"F2.wireOp",EDGE,"fcba4419-a2ee-464f-be9d-58f11bf3418b.sketch_text.stroke-139"),sQuery(id+"F2.wireOp",EDGE,"fcba4419-a2ee-464f-be9d-58f11bf3418b.sketch_text.stroke-140"),sQuery(id+"F2.wireOp",EDGE,"fcba4419-a2ee-464f-be9d-58f11bf3418b.sketch_text.stroke-141"),sQuery(id+"F2.wireOp",EDGE,"fcba4419-a2ee-464f-be9d-58f11bf3418b.sketch_text.stroke-142"),sQuery(id+"F2.wireOp",EDGE,"fcba4419-a2ee-464f-be9d-58f11bf3418b.sketch_text.stroke-143"),sQuery(id+"F2.wireOp",EDGE,"fcba4419-a2ee-464f-be9d-58f11bf3418b.sketch_text.stroke-144"),sQuery(id+"F2.wireOp",EDGE,"fcba4419-a2ee-464f-be9d-58f11bf3418b.sketch_text.stroke-145"),sQuery(id+"F2.wireOp",EDGE,"fcba4419-a2ee-464f-be9d-58f11bf3418b.sketch_text.stroke-146"),sQuery(id+"F2.wireOp",EDGE,"fcba4419-a2ee-464f-be9d-58f11bf3418b.sketch_text.stroke-147"),sQuery(id+"F2.wireOp",EDGE,"fcba4419-a2ee-464f-be9d-58f11bf3418b.sketch_text.stroke-148"),sQuery(id+"F2.wireOp",EDGE,"fcba4419-a2ee-464f-be9d-58f11bf3418b.sketch_text.stroke-149"),sQuery(id+"F2.wireOp",EDGE,"fcba4419-a2ee-464f-be9d-58f11bf3418b.sketch_text.stroke-150"),sQuery(id+"F2.wireOp",EDGE,"fcba4419-a2ee-464f-be9d-58f11bf3418b.sketch_text.stroke-151"),sQuery(id+"F2.wireOp",EDGE,"fcba4419-a2ee-464f-be9d-58f11bf3418b.sketch_text.stroke-152"),sQuery(id+"F2.wireOp",EDGE,"fcba4419-a2ee-464f-be9d-58f11bf3418b.sketch_text.stroke-153"),sQuery(id+"F2.wireOp",EDGE,"fcba4419-a2ee-464f-be9d-58f11bf3418b.sketch_text.stroke-154"),sQuery(id+"F2.wireOp",EDGE,"fcba4419-a2ee-464f-be9d-58f11bf3418b.sketch_text.stroke-155"),sQuery(id+"F2.wireOp",EDGE,"fcba4419-a2ee-464f-be9d-58f11bf3418b.sketch_text.stroke-156"),sQuery(id+"F2.wireOp",EDGE,"fcba4419-a2ee-464f-be9d-58f11bf3418b.sketch_text.stroke-157"),sQuery(id+"F2.wireOp",EDGE,"fcba4419-a2ee-464f-be9d-58f11bf3418b.sketch_text.stroke-158"),sQuery(id+"F2.wireOp",EDGE,"fcba4419-a2ee-464f-be9d-58f11bf3418b.sketch_text.stroke-159"),sQuery(id+"F2.wireOp",EDGE,"fcba4419-a2ee-464f-be9d-58f11bf3418b.sketch_text.stroke-160"),sQuery(id+"F2.wireOp",EDGE,"fcba4419-a2ee-464f-be9d-58f11bf3418b.sketch_text.stroke-161"),sQuery(id+"F2.wireOp",EDGE,"fcba4419-a2ee-464f-be9d-58f11bf3418b.sketch_text.stroke-162"),sQuery(id+"F2.wireOp",EDGE,"fcba4419-a2ee-464f-be9d-58f11bf3418b.sketch_text.stroke-163"),sQuery(id+"F2.wireOp",EDGE,"fcba4419-a2ee-464f-be9d-58f11bf3418b.sketch_text.stroke-164"),sQuery(id+"F2.wireOp",EDGE,"fcba4419-a2ee-464f-be9d-58f11bf3418b.sketch_text.stroke-165"),sQuery(id+"F2.wireOp",EDGE,"fcba4419-a2ee-464f-be9d-58f11bf3418b.sketch_text.stroke-166"),sQuery(id+"F2.wireOp",EDGE,"fcba4419-a2ee-464f-be9d-58f11bf3418b.sketch_text.stroke-167"),sQuery(id+"F2.wireOp",EDGE,"fcba4419-a2ee-464f-be9d-58f11bf3418b.sketch_text.stroke-168"),sQuery(id+"F2.wireOp",EDGE,"fcba4419-a2ee-464f-be9d-58f11bf3418b.sketch_text.stroke-169"),sQuery(id+"F2.wireOp",EDGE,"fcba4419-a2ee-464f-be9d-58f11bf3418b.sketch_text.stroke-170"),sQuery(id+"F2.wireOp",EDGE,"fcba4419-a2ee-464f-be9d-58f11bf3418b.sketch_text.stroke-171"),sQuery(id+"F2.wireOp",EDGE,"fcba4419-a2ee-464f-be9d-58f11bf3418b.sketch_text.stroke-172"),sQuery(id+"F2.wireOp",EDGE,"fcba4419-a2ee-464f-be9d-58f11bf3418b.sketch_text.stroke-173"),sQuery(id+"FHMxAyK4CFUKdhS_1.wireOp",EDGE,"1cb9c079-ea9b-4899-8069-e0e3048e911d.sketch_text.stroke-0"),sQuery(id+"FHMxAyK4CFUKdhS_1.wireOp",EDGE,"1cb9c079-ea9b-4899-8069-e0e3048e911d.sketch_text.stroke-1"),sQuery(id+"FHMxAyK4CFUKdhS_1.wireOp",EDGE,"1cb9c079-ea9b-4899-8069-e0e3048e911d.sketch_text.stroke-2"),sQuery(id+"FHMxAyK4CFUKdhS_1.wireOp",EDGE,"1cb9c079-ea9b-4899-8069-e0e3048e911d.sketch_text.stroke-3"),sQuery(id+"FHMxAyK4CFUKdhS_1.wireOp",EDGE,"1cb9c079-ea9b-4899-8069-e0e3048e911d.sketch_text.stroke-4"),sQuery(id+"FHMxAyK4CFUKdhS_1.wireOp",EDGE,"1cb9c079-ea9b-4899-8069-e0e3048e911d.sketch_text.stroke-5"),sQuery(id+"FHMxAyK4CFUKdhS_1.wireOp",EDGE,"1cb9c079-ea9b-4899-8069-e0e3048e911d.sketch_text.stroke-6"),sQuery(id+"FHMxAyK4CFUKdhS_1.wireOp",EDGE,"1cb9c079-ea9b-4899-8069-e0e3048e911d.sketch_text.stroke-7"),sQuery(id+"FHMxAyK4CFUKdhS_1.wireOp",EDGE,"1cb9c079-ea9b-4899-8069-e0e3048e911d.sketch_text.stroke-8"),sQuery(id+"FHMxAyK4CFUKdhS_1.wireOp",EDGE,"1cb9c079-ea9b-4899-8069-e0e3048e911d.sketch_text.stroke-9"),sQuery(id+"FHMxAyK4CFUKdhS_1.wireOp",EDGE,"1cb9c079-ea9b-4899-8069-e0e3048e911d.sketch_text.stroke-10"),sQuery(id+"FHMxAyK4CFUKdhS_1.wireOp",EDGE,"1cb9c079-ea9b-4899-8069-e0e3048e911d.sketch_text.stroke-11"),sQuery(id+"FHMxAyK4CFUKdhS_1.wireOp",EDGE,"1cb9c079-ea9b-4899-8069-e0e3048e911d.sketch_text.stroke-12"),sQuery(id+"FHMxAyK4CFUKdhS_1.wireOp",EDGE,"1cb9c079-ea9b-4899-8069-e0e3048e911d.sketch_text.stroke-13"),sQuery(id+"FHMxAyK4CFUKdhS_1.wireOp",EDGE,"1cb9c079-ea9b-4899-8069-e0e3048e911d.sketch_text.stroke-14"),sQuery(id+"FHMxAyK4CFUKdhS_1.wireOp",EDGE,"1cb9c079-ea9b-4899-8069-e0e3048e911d.sketch_text.stroke-15"),sQuery(id+"FHMxAyK4CFUKdhS_1.wireOp",EDGE,"1cb9c079-ea9b-4899-8069-e0e3048e911d.sketch_text.stroke-16"),sQuery(id+"FHMxAyK4CFUKdhS_1.wireOp",EDGE,"1cb9c079-ea9b-4899-8069-e0e3048e911d.sketch_text.stroke-17"),sQuery(id+"FHMxAyK4CFUKdhS_1.wireOp",EDGE,"1cb9c079-ea9b-4899-8069-e0e3048e911d.sketch_text.stroke-18"),sQuery(id+"FHMxAyK4CFUKdhS_1.wireOp",EDGE,"1cb9c079-ea9b-4899-8069-e0e3048e911d.sketch_text.stroke-19"),sQuery(id+"FHMxAyK4CFUKdhS_1.wireOp",EDGE,"1cb9c079-ea9b-4899-8069-e0e3048e911d.sketch_text.stroke-20"),sQuery(id+"FHMxAyK4CFUKdhS_1.wireOp",EDGE,"1cb9c079-ea9b-4899-8069-e0e3048e911d.sketch_text.stroke-21"),sQuery(id+"FHMxAyK4CFUKdhS_1.wireOp",EDGE,"1cb9c079-ea9b-4899-8069-e0e3048e911d.sketch_text.stroke-22"),sQuery(id+"FHMxAyK4CFUKdhS_1.wireOp",EDGE,"1cb9c079-ea9b-4899-8069-e0e3048e911d.sketch_text.stroke-23"),sQuery(id+"FHMxAyK4CFUKdhS_1.wireOp",EDGE,"1cb9c079-ea9b-4899-8069-e0e3048e911d.sketch_text.stroke-24"),sQuery(id+"FHMxAyK4CFUKdhS_1.wireOp",EDGE,"1cb9c079-ea9b-4899-8069-e0e3048e911d.sketch_text.stroke-25"),sQuery(id+"FHMxAyK4CFUKdhS_1.wireOp",EDGE,"1cb9c079-ea9b-4899-8069-e0e3048e911d.sketch_text.stroke-26"),sQuery(id+"FHMxAyK4CFUKdhS_1.wireOp",EDGE,"1cb9c079-ea9b-4899-8069-e0e3048e911d.sketch_text.stroke-27"),sQuery(id+"FHMxAyK4CFUKdhS_1.wireOp",EDGE,"1cb9c079-ea9b-4899-8069-e0e3048e911d.sketch_text.stroke-28"),sQuery(id+"FHMxAyK4CFUKdhS_1.wireOp",EDGE,"1cb9c079-ea9b-4899-8069-e0e3048e911d.sketch_text.stroke-29"),sQuery(id+"FHMxAyK4CFUKdhS_1.wireOp",EDGE,"1cb9c079-ea9b-4899-8069-e0e3048e911d.sketch_text.stroke-30"),sQuery(id+"FHMxAyK4CFUKdhS_1.wireOp",EDGE,"1cb9c079-ea9b-4899-8069-e0e3048e911d.sketch_text.stroke-31"),sQuery(id+"FHMxAyK4CFUKdhS_1.wireOp",EDGE,"1cb9c079-ea9b-4899-8069-e0e3048e911d.sketch_text.stroke-32"),sQuery(id+"FHMxAyK4CFUKdhS_1.wireOp",EDGE,"1cb9c079-ea9b-4899-8069-e0e3048e911d.sketch_text.stroke-33"),sQuery(id+"FHMxAyK4CFUKdhS_1.wireOp",EDGE,"1cb9c079-ea9b-4899-8069-e0e3048e911d.sketch_text.stroke-34"),sQuery(id+"FHMxAyK4CFUKdhS_1.wireOp",EDGE,"1cb9c079-ea9b-4899-8069-e0e3048e911d.sketch_text.stroke-35"),sQuery(id+"FHMxAyK4CFUKdhS_1.wireOp",EDGE,"1cb9c079-ea9b-4899-8069-e0e3048e911d.sketch_text.stroke-36"),sQuery(id+"FHMxAyK4CFUKdhS_1.wireOp",EDGE,"1cb9c079-ea9b-4899-8069-e0e3048e911d.sketch_text.stroke-37"),sQuery(id+"FHMxAyK4CFUKdhS_1.wireOp",EDGE,"1cb9c079-ea9b-4899-8069-e0e3048e911d.sketch_text.stroke-38"),sQuery(id+"FHMxAyK4CFUKdhS_1.wireOp",EDGE,"1cb9c079-ea9b-4899-8069-e0e3048e911d.sketch_text.stroke-39"),sQuery(id+"FHMxAyK4CFUKdhS_1.wireOp",EDGE,"1cb9c079-ea9b-4899-8069-e0e3048e911d.sketch_text.stroke-40"),sQuery(id+"FHMxAyK4CFUKdhS_1.wireOp",EDGE,"1cb9c079-ea9b-4899-8069-e0e3048e911d.sketch_text.stroke-41"),sQuery(id+"FHMxAyK4CFUKdhS_1.wireOp",EDGE,"1cb9c079-ea9b-4899-8069-e0e3048e911d.sketch_text.stroke-42"),sQuery(id+"FHMxAyK4CFUKdhS_1.wireOp",EDGE,"1cb9c079-ea9b-4899-8069-e0e3048e911d.sketch_text.stroke-43"),sQuery(id+"FHMxAyK4CFUKdhS_1.wireOp",EDGE,"1cb9c079-ea9b-4899-8069-e0e3048e911d.sketch_text.stroke-44"),sQuery(id+"FHMxAyK4CFUKdhS_1.wireOp",EDGE,"1cb9c079-ea9b-4899-8069-e0e3048e911d.sketch_text.stroke-45"),sQuery(id+"FHMxAyK4CFUKdhS_1.wireOp",EDGE,"1cb9c079-ea9b-4899-8069-e0e3048e911d.sketch_text.stroke-46"),sQuery(id+"FHMxAyK4CFUKdhS_1.wireOp",EDGE,"1cb9c079-ea9b-4899-8069-e0e3048e911d.sketch_text.stroke-47"),sQuery(id+"FHMxAyK4CFUKdhS_1.wireOp",EDGE,"1cb9c079-ea9b-4899-8069-e0e3048e911d.sketch_text.stroke-48"),sQuery(id+"FHMxAyK4CFUKdhS_1.wireOp",EDGE,"1cb9c079-ea9b-4899-8069-e0e3048e911d.sketch_text.stroke-49"),sQuery(id+"FHMxAyK4CFUKdhS_1.wireOp",EDGE,"1cb9c079-ea9b-4899-8069-e0e3048e911d.sketch_text.stroke-50"),sQuery(id+"FHMxAyK4CFUKdhS_1.wireOp",EDGE,"1cb9c079-ea9b-4899-8069-e0e3048e911d.sketch_text.stroke-51"),sQuery(id+"FHMxAyK4CFUKdhS_1.wireOp",EDGE,"1cb9c079-ea9b-4899-8069-e0e3048e911d.sketch_text.stroke-52"),sQuery(id+"FHMxAyK4CFUKdhS_1.wireOp",EDGE,"1cb9c079-ea9b-4899-8069-e0e3048e911d.sketch_text.stroke-53"),sQuery(id+"FHMxAyK4CFUKdhS_1.wireOp",EDGE,"1cb9c079-ea9b-4899-8069-e0e3048e911d.sketch_text.stroke-54"),sQuery(id+"FHMxAyK4CFUKdhS_1.wireOp",EDGE,"1cb9c079-ea9b-4899-8069-e0e3048e911d.sketch_text.stroke-55"),sQuery(id+"FHMxAyK4CFUKdhS_1.wireOp",EDGE,"1cb9c079-ea9b-4899-8069-e0e3048e911d.sketch_text.stroke-56"),sQuery(id+"FHMxAyK4CFUKdhS_1.wireOp",EDGE,"1cb9c079-ea9b-4899-8069-e0e3048e911d.sketch_text.stroke-57"),sQuery(id+"FHMxAyK4CFUKdhS_1.wireOp",EDGE,"1cb9c079-ea9b-4899-8069-e0e3048e911d.sketch_text.stroke-58"),sQuery(id+"FHMxAyK4CFUKdhS_1.wireOp",EDGE,"1cb9c079-ea9b-4899-8069-e0e3048e911d.sketch_text.stroke-59"),sQuery(id+"FHMxAyK4CFUKdhS_1.wireOp",EDGE,"1cb9c079-ea9b-4899-8069-e0e3048e911d.sketch_text.stroke-60"),sQuery(id+"FHMxAyK4CFUKdhS_1.wireOp",EDGE,"1cb9c079-ea9b-4899-8069-e0e3048e911d.sketch_text.stroke-61"),sQuery(id+"FHMxAyK4CFUKdhS_1.wireOp",EDGE,"1cb9c079-ea9b-4899-8069-e0e3048e911d.sketch_text.stroke-62"),sQuery(id+"FHMxAyK4CFUKdhS_1.wireOp",EDGE,"1cb9c079-ea9b-4899-8069-e0e3048e911d.sketch_text.stroke-71"),sQuery(id+"FHMxAyK4CFUKdhS_1.wireOp",EDGE,"1cb9c079-ea9b-4899-8069-e0e3048e911d.sketch_text.stroke-72"),sQuery(id+"FHMxAyK4CFUKdhS_1.wireOp",EDGE,"1cb9c079-ea9b-4899-8069-e0e3048e911d.sketch_text.stroke-73"),sQuery(id+"FHMxAyK4CFUKdhS_1.wireOp",EDGE,"1cb9c079-ea9b-4899-8069-e0e3048e911d.sketch_text.stroke-74"),sQuery(id+"FHMxAyK4CFUKdhS_1.wireOp",EDGE,"1cb9c079-ea9b-4899-8069-e0e3048e911d.sketch_text.stroke-75"),sQuery(id+"FHMxAyK4CFUKdhS_1.wireOp",EDGE,"1cb9c079-ea9b-4899-8069-e0e3048e911d.sketch_text.stroke-76"),sQuery(id+"FHMxAyK4CFUKdhS_1.wireOp",EDGE,"1cb9c079-ea9b-4899-8069-e0e3048e911d.sketch_text.stroke-77"),sQuery(id+"FHMxAyK4CFUKdhS_1.wireOp",EDGE,"1cb9c079-ea9b-4899-8069-e0e3048e911d.sketch_text.stroke-78"),sQuery(id+"FHMxAyK4CFUKdhS_1.wireOp",EDGE,"1cb9c079-ea9b-4899-8069-e0e3048e911d.sketch_text.stroke-79"),sQuery(id+"FHMxAyK4CFUKdhS_1.wireOp",EDGE,"1cb9c079-ea9b-4899-8069-e0e3048e911d.sketch_text.stroke-80"),sQuery(id+"FHMxAyK4CFUKdhS_1.wireOp",EDGE,"1cb9c079-ea9b-4899-8069-e0e3048e911d.sketch_text.stroke-81"),sQuery(id+"FHMxAyK4CFUKdhS_1.wireOp",EDGE,"1cb9c079-ea9b-4899-8069-e0e3048e911d.sketch_text.stroke-82"),sQuery(id+"FHMxAyK4CFUKdhS_1.wireOp",EDGE,"1cb9c079-ea9b-4899-8069-e0e3048e911d.sketch_text.stroke-83"),sQuery(id+"FHMxAyK4CFUKdhS_1.wireOp",EDGE,"1cb9c079-ea9b-4899-8069-e0e3048e911d.sketch_text.stroke-84"),sQuery(id+"FHMxAyK4CFUKdhS_1.wireOp",EDGE,"1cb9c079-ea9b-4899-8069-e0e3048e911d.sketch_text.stroke-85"),sQuery(id+"FHMxAyK4CFUKdhS_1.wireOp",EDGE,"1cb9c079-ea9b-4899-8069-e0e3048e911d.sketch_text.stroke-86"),sQuery(id+"FHMxAyK4CFUKdhS_1.wireOp",EDGE,"1cb9c079-ea9b-4899-8069-e0e3048e911d.sketch_text.stroke-87"),sQuery(id+"FHMxAyK4CFUKdhS_1.wireOp",EDGE,"1cb9c079-ea9b-4899-8069-e0e3048e911d.sketch_text.stroke-88"),sQuery(id+"FHMxAyK4CFUKdhS_1.wireOp",EDGE,"1cb9c079-ea9b-4899-8069-e0e3048e911d.sketch_text.stroke-89"),sQuery(id+"FHMxAyK4CFUKdhS_1.wireOp",EDGE,"1cb9c079-ea9b-4899-8069-e0e3048e911d.sketch_text.stroke-90"),sQuery(id+"FHMxAyK4CFUKdhS_1.wireOp",EDGE,"1cb9c079-ea9b-4899-8069-e0e3048e911d.sketch_text.stroke-91"),sQuery(id+"FHMxAyK4CFUKdhS_1.wireOp",EDGE,"1cb9c079-ea9b-4899-8069-e0e3048e911d.sketch_text.stroke-92"),sQuery(id+"FHMxAyK4CFUKdhS_1.wireOp",EDGE,"1cb9c079-ea9b-4899-8069-e0e3048e911d.sketch_text.stroke-93"),sQuery(id+"FHMxAyK4CFUKdhS_1.wireOp",EDGE,"1cb9c079-ea9b-4899-8069-e0e3048e911d.sketch_text.stroke-94"),sQuery(id+"FHMxAyK4CFUKdhS_1.wireOp",EDGE,"1cb9c079-ea9b-4899-8069-e0e3048e911d.sketch_text.stroke-95"),sQuery(id+"FHMxAyK4CFUKdhS_1.wireOp",EDGE,"1cb9c079-ea9b-4899-8069-e0e3048e911d.sketch_text.stroke-96"),sQuery(id+"FHMxAyK4CFUKdhS_1.wireOp",EDGE,"1cb9c079-ea9b-4899-8069-e0e3048e911d.sketch_text.stroke-97"),sQuery(id+"FHMxAyK4CFUKdhS_1.wireOp",EDGE,"1cb9c079-ea9b-4899-8069-e0e3048e911d.sketch_text.stroke-103"),sQuery(id+"FHMxAyK4CFUKdhS_1.wireOp",EDGE,"1cb9c079-ea9b-4899-8069-e0e3048e911d.sketch_text.stroke-104"),sQuery(id+"FHMxAyK4CFUKdhS_1.wireOp",EDGE,"1cb9c079-ea9b-4899-8069-e0e3048e911d.sketch_text.stroke-105"),sQuery(id+"FHMxAyK4CFUKdhS_1.wireOp",EDGE,"1cb9c079-ea9b-4899-8069-e0e3048e911d.sketch_text.stroke-106"),sQuery(id+"FHMxAyK4CFUKdhS_1.wireOp",EDGE,"1cb9c079-ea9b-4899-8069-e0e3048e911d.sketch_text.stroke-107"),sQuery(id+"FHMxAyK4CFUKdhS_1.wireOp",EDGE,"1cb9c079-ea9b-4899-8069-e0e3048e911d.sketch_text.stroke-108"),sQuery(id+"FHMxAyK4CFUKdhS_1.wireOp",EDGE,"1cb9c079-ea9b-4899-8069-e0e3048e911d.sketch_text.stroke-109"),sQuery(id+"FHMxAyK4CFUKdhS_1.wireOp",EDGE,"1cb9c079-ea9b-4899-8069-e0e3048e911d.sketch_text.stroke-110"),sQuery(id+"FHMxAyK4CFUKdhS_1.wireOp",EDGE,"1cb9c079-ea9b-4899-8069-e0e3048e911d.sketch_text.stroke-111"),sQuery(id+"FHMxAyK4CFUKdhS_1.wireOp",EDGE,"1cb9c079-ea9b-4899-8069-e0e3048e911d.sketch_text.stroke-112"),sQuery(id+"FHMxAyK4CFUKdhS_1.wireOp",EDGE,"1cb9c079-ea9b-4899-8069-e0e3048e911d.sketch_text.stroke-113"),sQuery(id+"FHMxAyK4CFUKdhS_1.wireOp",EDGE,"1cb9c079-ea9b-4899-8069-e0e3048e911d.sketch_text.stroke-114"),sQuery(id+"FHMxAyK4CFUKdhS_1.wireOp",EDGE,"1cb9c079-ea9b-4899-8069-e0e3048e911d.sketch_text.stroke-115"),sQuery(id+"FHMxAyK4CFUKdhS_1.wireOp",EDGE,"1cb9c079-ea9b-4899-8069-e0e3048e911d.sketch_text.stroke-116"),sQuery(id+"FHMxAyK4CFUKdhS_1.wireOp",EDGE,"1cb9c079-ea9b-4899-8069-e0e3048e911d.sketch_text.stroke-117"),sQuery(id+"FHMxAyK4CFUKdhS_1.wireOp",EDGE,"1cb9c079-ea9b-4899-8069-e0e3048e911d.sketch_text.stroke-118"),sQuery(id+"FHMxAyK4CFUKdhS_1.wireOp",EDGE,"1cb9c079-ea9b-4899-8069-e0e3048e911d.sketch_text.stroke-119"),sQuery(id+"FHMxAyK4CFUKdhS_1.wireOp",EDGE,"1cb9c079-ea9b-4899-8069-e0e3048e911d.sketch_text.stroke-120"),sQuery(id+"FHMxAyK4CFUKdhS_1.wireOp",EDGE,"1cb9c079-ea9b-4899-8069-e0e3048e911d.sketch_text.stroke-121"),sQuery(id+"FHMxAyK4CFUKdhS_1.wireOp",EDGE,"1cb9c079-ea9b-4899-8069-e0e3048e911d.sketch_text.stroke-122"),sQuery(id+"FHMxAyK4CFUKdhS_1.wireOp",EDGE,"1cb9c079-ea9b-4899-8069-e0e3048e911d.sketch_text.stroke-123"),sQuery(id+"FHMxAyK4CFUKdhS_1.wireOp",EDGE,"1cb9c079-ea9b-4899-8069-e0e3048e911d.sketch_text.stroke-124"),sQuery(id+"FHMxAyK4CFUKdhS_1.wireOp",EDGE,"1cb9c079-ea9b-4899-8069-e0e3048e911d.sketch_text.stroke-125"),sQuery(id+"FHMxAyK4CFUKdhS_1.wireOp",EDGE,"1cb9c079-ea9b-4899-8069-e0e3048e911d.sketch_text.stroke-126"),sQuery(id+"FHMxAyK4CFUKdhS_1.wireOp",EDGE,"1cb9c079-ea9b-4899-8069-e0e3048e911d.sketch_text.stroke-127"),sQuery(id+"FHMxAyK4CFUKdhS_1.wireOp",EDGE,"1cb9c079-ea9b-4899-8069-e0e3048e911d.sketch_text.stroke-128"),sQuery(id+"FHMxAyK4CFUKdhS_1.wireOp",EDGE,"1cb9c079-ea9b-4899-8069-e0e3048e911d.sketch_text.stroke-129"),sQuery(id+"FHMxAyK4CFUKdhS_1.wireOp",EDGE,"1cb9c079-ea9b-4899-8069-e0e3048e911d.sketch_text.stroke-130"),sQuery(id+"FHMxAyK4CFUKdhS_1.wireOp",EDGE,"1cb9c079-ea9b-4899-8069-e0e3048e911d.sketch_text.stroke-131"),sQuery(id+"FHMxAyK4CFUKdhS_1.wireOp",EDGE,"1cb9c079-ea9b-4899-8069-e0e3048e911d.sketch_text.stroke-132"),sQuery(id+"FHMxAyK4CFUKdhS_1.wireOp",EDGE,"1cb9c079-ea9b-4899-8069-e0e3048e911d.sketch_text.stroke-133"),sQuery(id+"FHMxAyK4CFUKdhS_1.wireOp",EDGE,"1cb9c079-ea9b-4899-8069-e0e3048e911d.sketch_text.stroke-134"),sQuery(id+"FHMxAyK4CFUKdhS_1.wireOp",EDGE,"1cb9c079-ea9b-4899-8069-e0e3048e911d.sketch_text.stroke-135"),sQuery(id+"FHMxAyK4CFUKdhS_1.wireOp",EDGE,"1cb9c079-ea9b-4899-8069-e0e3048e911d.sketch_text.stroke-136"),sQuery(id+"FHMxAyK4CFUKdhS_1.wireOp",EDGE,"1cb9c079-ea9b-4899-8069-e0e3048e911d.sketch_text.stroke-137"),sQuery(id+"FHMxAyK4CFUKdhS_1.wireOp",EDGE,"1cb9c079-ea9b-4899-8069-e0e3048e911d.sketch_text.stroke-138"),sQuery(id+"FHMxAyK4CFUKdhS_1.wireOp",EDGE,"1cb9c079-ea9b-4899-8069-e0e3048e911d.sketch_text.stroke-139"),sQuery(id+"FHMxAyK4CFUKdhS_1.wireOp",EDGE,"1cb9c079-ea9b-4899-8069-e0e3048e911d.sketch_text.stroke-140"),sQuery(id+"FHMxAyK4CFUKdhS_1.wireOp",EDGE,"1cb9c079-ea9b-4899-8069-e0e3048e911d.sketch_text.stroke-141"),sQuery(id+"FHMxAyK4CFUKdhS_1.wireOp",EDGE,"1cb9c079-ea9b-4899-8069-e0e3048e911d.sketch_text.stroke-142"),sQuery(id+"FHMxAyK4CFUKdhS_1.wireOp",EDGE,"1cb9c079-ea9b-4899-8069-e0e3048e911d.sketch_text.stroke-143"),sQuery(id+"FHMxAyK4CFUKdhS_1.wireOp",EDGE,"1cb9c079-ea9b-4899-8069-e0e3048e911d.sketch_text.stroke-144"),sQuery(id+"FHMxAyK4CFUKdhS_1.wireOp",EDGE,"1cb9c079-ea9b-4899-8069-e0e3048e911d.sketch_text.stroke-145"),sQuery(id+"FHMxAyK4CFUKdhS_1.wireOp",EDGE,"1cb9c079-ea9b-4899-8069-e0e3048e911d.sketch_text.stroke-146"),sQuery(id+"FHMxAyK4CFUKdhS_1.wireOp",EDGE,"1cb9c079-ea9b-4899-8069-e0e3048e911d.sketch_text.stroke-147"),sQuery(id+"FHMxAyK4CFUKdhS_1.wireOp",EDGE,"1cb9c079-ea9b-4899-8069-e0e3048e911d.sketch_text.stroke-148"),sQuery(id+"FHMxAyK4CFUKdhS_1.wireOp",EDGE,"1cb9c079-ea9b-4899-8069-e0e3048e911d.sketch_text.stroke-149"),sQuery(id+"FHMxAyK4CFUKdhS_1.wireOp",EDGE,"1cb9c079-ea9b-4899-8069-e0e3048e911d.sketch_text.stroke-150"),sQuery(id+"FHMxAyK4CFUKdhS_1.wireOp",EDGE,"1cb9c079-ea9b-4899-8069-e0e3048e911d.sketch_text.stroke-151"),sQuery(id+"FHMxAyK4CFUKdhS_1.wireOp",EDGE,"1cb9c079-ea9b-4899-8069-e0e3048e911d.sketch_text.stroke-152"),sQuery(id+"FHMxAyK4CFUKdhS_1.wireOp",EDGE,"1cb9c079-ea9b-4899-8069-e0e3048e911d.sketch_text.stroke-153"),sQuery(id+"FHMxAyK4CFUKdhS_1.wireOp",EDGE,"1cb9c079-ea9b-4899-8069-e0e3048e911d.sketch_text.stroke-159"),sQuery(id+"FHMxAyK4CFUKdhS_1.wireOp",EDGE,"1cb9c079-ea9b-4899-8069-e0e3048e911d.sketch_text.stroke-160"),sQuery(id+"FHMxAyK4CFUKdhS_1.wireOp",EDGE,"1cb9c079-ea9b-4899-8069-e0e3048e911d.sketch_text.stroke-161"),sQuery(id+"FHMxAyK4CFUKdhS_1.wireOp",EDGE,"1cb9c079-ea9b-4899-8069-e0e3048e911d.sketch_text.stroke-162"),sQuery(id+"FHMxAyK4CFUKdhS_1.wireOp",EDGE,"1cb9c079-ea9b-4899-8069-e0e3048e911d.sketch_text.stroke-163"),sQuery(id+"FHMxAyK4CFUKdhS_1.wireOp",EDGE,"1cb9c079-ea9b-4899-8069-e0e3048e911d.sketch_text.stroke-164"),sQuery(id+"FHMxAyK4CFUKdhS_1.wireOp",EDGE,"1cb9c079-ea9b-4899-8069-e0e3048e911d.sketch_text.stroke-165"),sQuery(id+"FHMxAyK4CFUKdhS_1.wireOp",EDGE,"1cb9c079-ea9b-4899-8069-e0e3048e911d.sketch_text.stroke-166"),sQuery(id+"FHMxAyK4CFUKdhS_1.wireOp",EDGE,"1cb9c079-ea9b-4899-8069-e0e3048e911d.sketch_text.stroke-167"),sQuery(id+"FHMxAyK4CFUKdhS_1.wireOp",EDGE,"1cb9c079-ea9b-4899-8069-e0e3048e911d.sketch_text.stroke-168"),sQuery(id+"FHMxAyK4CFUKdhS_1.wireOp",EDGE,"1cb9c079-ea9b-4899-8069-e0e3048e911d.sketch_text.stroke-169"),sQuery(id+"FHMxAyK4CFUKdhS_1.wireOp",EDGE,"1cb9c079-ea9b-4899-8069-e0e3048e911d.sketch_text.stroke-170"),sQuery(id+"FHMxAyK4CFUKdhS_1.wireOp",EDGE,"1cb9c079-ea9b-4899-8069-e0e3048e911d.sketch_text.stroke-171"),sQuery(id+"FHMxAyK4CFUKdhS_1.wireOp",EDGE,"1cb9c079-ea9b-4899-8069-e0e3048e911d.sketch_text.stroke-172"),sQuery(id+"FHMxAyK4CFUKdhS_1.wireOp",EDGE,"1cb9c079-ea9b-4899-8069-e0e3048e911d.sketch_text.stroke-173"),sQuery(id+"FHMxAyK4CFUKdhS_1.wireOp",EDGE,"1cb9c079-ea9b-4899-8069-e0e3048e911d.sketch_text.stroke-174"),sQuery(id+"FHMxAyK4CFUKdhS_1.wireOp",EDGE,"1cb9c079-ea9b-4899-8069-e0e3048e911d.sketch_text.stroke-175"),sQuery(id+"FHMxAyK4CFUKdhS_1.wireOp",EDGE,"1cb9c079-ea9b-4899-8069-e0e3048e911d.sketch_text.stroke-176"),sQuery(id+"FHMxAyK4CFUKdhS_1.wireOp",EDGE,"1cb9c079-ea9b-4899-8069-e0e3048e911d.sketch_text.stroke-177"),sQuery(id+"FHMxAyK4CFUKdhS_1.wireOp",EDGE,"1cb9c079-ea9b-4899-8069-e0e3048e911d.sketch_text.stroke-178"),sQuery(id+"FHMxAyK4CFUKdhS_1.wireOp",EDGE,"1cb9c079-ea9b-4899-8069-e0e3048e911d.sketch_text.stroke-179"),sQuery(id+"FHMxAyK4CFUKdhS_1.wireOp",EDGE,"1cb9c079-ea9b-4899-8069-e0e3048e911d.sketch_text.stroke-180"),subQ2,sQuery(id+"F3.wireOp",EDGE,"E30")])],"isStart":true})]),OD(0.0)],"derivedFrom":makeQuery(id+"F1.opExtrude","CAP_EDGE",EDGE,{"disambiguationData":[OSD([subQ0])],"isStart":false})});}
            var Q26;
            {var subQ0=sQuery(id+"F0.wireOp",EDGE,"E0.top");var subQ1=sQuery(id+"F0.wireOp",EDGE,"E0.bottom");var subQ2=sQuery(id+"F3.wireOp",EDGE,"E30");Q26=makeQuery(id+"F4.boolean.opBoolean","SPLIT",EDGE,{"disambiguationData":[TD([makeQuery(id+"F1.opExtrude","CAP_FACE",FACE,{"disambiguationData":[OSD([subQ1,subQ0,sQuery(id+"F0.wireOp",EDGE,"E0.left"),sQuery(id+"F0.wireOp",EDGE,"E0.right")])],"isStart":false}),makeQuery(id+"F1.opExtrude","SWEPT_FACE",FACE,{"disambiguationData":[OSD([subQ0])]}),makeQuery(id+"F4.opExtrude","CAP_FACE",FACE,{"disambiguationData":[OSD([subQ1,sQuery(id+"F2.wireOp",EDGE,"fcba4419-a2ee-464f-be9d-58f11bf3418b.sketch_text.stroke-0"),sQuery(id+"F2.wireOp",EDGE,"fcba4419-a2ee-464f-be9d-58f11bf3418b.sketch_text.stroke-1"),sQuery(id+"F2.wireOp",EDGE,"fcba4419-a2ee-464f-be9d-58f11bf3418b.sketch_text.stroke-2"),sQuery(id+"F2.wireOp",EDGE,"fcba4419-a2ee-464f-be9d-58f11bf3418b.sketch_text.stroke-3"),sQuery(id+"F2.wireOp",EDGE,"fcba4419-a2ee-464f-be9d-58f11bf3418b.sketch_text.stroke-4"),sQuery(id+"F2.wireOp",EDGE,"fcba4419-a2ee-464f-be9d-58f11bf3418b.sketch_text.stroke-5"),sQuery(id+"F2.wireOp",EDGE,"fcba4419-a2ee-464f-be9d-58f11bf3418b.sketch_text.stroke-6"),sQuery(id+"F2.wireOp",EDGE,"fcba4419-a2ee-464f-be9d-58f11bf3418b.sketch_text.stroke-7"),sQuery(id+"F2.wireOp",EDGE,"fcba4419-a2ee-464f-be9d-58f11bf3418b.sketch_text.stroke-8"),sQuery(id+"F2.wireOp",EDGE,"fcba4419-a2ee-464f-be9d-58f11bf3418b.sketch_text.stroke-9"),sQuery(id+"F2.wireOp",EDGE,"fcba4419-a2ee-464f-be9d-58f11bf3418b.sketch_text.stroke-10"),sQuery(id+"F2.wireOp",EDGE,"fcba4419-a2ee-464f-be9d-58f11bf3418b.sketch_text.stroke-11"),sQuery(id+"F2.wireOp",EDGE,"fcba4419-a2ee-464f-be9d-58f11bf3418b.sketch_text.stroke-12"),sQuery(id+"F2.wireOp",EDGE,"fcba4419-a2ee-464f-be9d-58f11bf3418b.sketch_text.stroke-13"),sQuery(id+"F2.wireOp",EDGE,"fcba4419-a2ee-464f-be9d-58f11bf3418b.sketch_text.stroke-14"),sQuery(id+"F2.wireOp",EDGE,"fcba4419-a2ee-464f-be9d-58f11bf3418b.sketch_text.stroke-15"),sQuery(id+"F2.wireOp",EDGE,"fcba4419-a2ee-464f-be9d-58f11bf3418b.sketch_text.stroke-16"),sQuery(id+"F2.wireOp",EDGE,"fcba4419-a2ee-464f-be9d-58f11bf3418b.sketch_text.stroke-17"),sQuery(id+"F2.wireOp",EDGE,"fcba4419-a2ee-464f-be9d-58f11bf3418b.sketch_text.stroke-18"),sQuery(id+"F2.wireOp",EDGE,"fcba4419-a2ee-464f-be9d-58f11bf3418b.sketch_text.stroke-19"),sQuery(id+"F2.wireOp",EDGE,"fcba4419-a2ee-464f-be9d-58f11bf3418b.sketch_text.stroke-20"),sQuery(id+"F2.wireOp",EDGE,"fcba4419-a2ee-464f-be9d-58f11bf3418b.sketch_text.stroke-21"),sQuery(id+"F2.wireOp",EDGE,"fcba4419-a2ee-464f-be9d-58f11bf3418b.sketch_text.stroke-22"),sQuery(id+"F2.wireOp",EDGE,"fcba4419-a2ee-464f-be9d-58f11bf3418b.sketch_text.stroke-23"),sQuery(id+"F2.wireOp",EDGE,"fcba4419-a2ee-464f-be9d-58f11bf3418b.sketch_text.stroke-24"),sQuery(id+"F2.wireOp",EDGE,"fcba4419-a2ee-464f-be9d-58f11bf3418b.sketch_text.stroke-25"),sQuery(id+"F2.wireOp",EDGE,"fcba4419-a2ee-464f-be9d-58f11bf3418b.sketch_text.stroke-26"),sQuery(id+"F2.wireOp",EDGE,"fcba4419-a2ee-464f-be9d-58f11bf3418b.sketch_text.stroke-27"),sQuery(id+"F2.wireOp",EDGE,"fcba4419-a2ee-464f-be9d-58f11bf3418b.sketch_text.stroke-28"),sQuery(id+"F2.wireOp",EDGE,"fcba4419-a2ee-464f-be9d-58f11bf3418b.sketch_text.stroke-29"),sQuery(id+"F2.wireOp",EDGE,"fcba4419-a2ee-464f-be9d-58f11bf3418b.sketch_text.stroke-30"),sQuery(id+"F2.wireOp",EDGE,"fcba4419-a2ee-464f-be9d-58f11bf3418b.sketch_text.stroke-31"),sQuery(id+"F2.wireOp",EDGE,"fcba4419-a2ee-464f-be9d-58f11bf3418b.sketch_text.stroke-32"),sQuery(id+"F2.wireOp",EDGE,"fcba4419-a2ee-464f-be9d-58f11bf3418b.sketch_text.stroke-33"),sQuery(id+"F2.wireOp",EDGE,"fcba4419-a2ee-464f-be9d-58f11bf3418b.sketch_text.stroke-34"),sQuery(id+"F2.wireOp",EDGE,"fcba4419-a2ee-464f-be9d-58f11bf3418b.sketch_text.stroke-35"),sQuery(id+"F2.wireOp",EDGE,"fcba4419-a2ee-464f-be9d-58f11bf3418b.sketch_text.stroke-36"),sQuery(id+"F2.wireOp",EDGE,"fcba4419-a2ee-464f-be9d-58f11bf3418b.sketch_text.stroke-37"),sQuery(id+"F2.wireOp",EDGE,"fcba4419-a2ee-464f-be9d-58f11bf3418b.sketch_text.stroke-38"),sQuery(id+"F2.wireOp",EDGE,"fcba4419-a2ee-464f-be9d-58f11bf3418b.sketch_text.stroke-39"),sQuery(id+"F2.wireOp",EDGE,"fcba4419-a2ee-464f-be9d-58f11bf3418b.sketch_text.stroke-40"),sQuery(id+"F2.wireOp",EDGE,"fcba4419-a2ee-464f-be9d-58f11bf3418b.sketch_text.stroke-41"),sQuery(id+"F2.wireOp",EDGE,"fcba4419-a2ee-464f-be9d-58f11bf3418b.sketch_text.stroke-42"),sQuery(id+"F2.wireOp",EDGE,"fcba4419-a2ee-464f-be9d-58f11bf3418b.sketch_text.stroke-43"),sQuery(id+"F2.wireOp",EDGE,"fcba4419-a2ee-464f-be9d-58f11bf3418b.sketch_text.stroke-44"),sQuery(id+"F2.wireOp",EDGE,"fcba4419-a2ee-464f-be9d-58f11bf3418b.sketch_text.stroke-45"),sQuery(id+"F2.wireOp",EDGE,"fcba4419-a2ee-464f-be9d-58f11bf3418b.sketch_text.stroke-46"),sQuery(id+"F2.wireOp",EDGE,"fcba4419-a2ee-464f-be9d-58f11bf3418b.sketch_text.stroke-47"),sQuery(id+"F2.wireOp",EDGE,"fcba4419-a2ee-464f-be9d-58f11bf3418b.sketch_text.stroke-48"),sQuery(id+"F2.wireOp",EDGE,"fcba4419-a2ee-464f-be9d-58f11bf3418b.sketch_text.stroke-49"),sQuery(id+"F2.wireOp",EDGE,"fcba4419-a2ee-464f-be9d-58f11bf3418b.sketch_text.stroke-50"),sQuery(id+"F2.wireOp",EDGE,"fcba4419-a2ee-464f-be9d-58f11bf3418b.sketch_text.stroke-51"),sQuery(id+"F2.wireOp",EDGE,"fcba4419-a2ee-464f-be9d-58f11bf3418b.sketch_text.stroke-52"),sQuery(id+"F2.wireOp",EDGE,"fcba4419-a2ee-464f-be9d-58f11bf3418b.sketch_text.stroke-53"),sQuery(id+"F2.wireOp",EDGE,"fcba4419-a2ee-464f-be9d-58f11bf3418b.sketch_text.stroke-54"),sQuery(id+"F2.wireOp",EDGE,"fcba4419-a2ee-464f-be9d-58f11bf3418b.sketch_text.stroke-55"),sQuery(id+"F2.wireOp",EDGE,"fcba4419-a2ee-464f-be9d-58f11bf3418b.sketch_text.stroke-56"),sQuery(id+"F2.wireOp",EDGE,"fcba4419-a2ee-464f-be9d-58f11bf3418b.sketch_text.stroke-57"),sQuery(id+"F2.wireOp",EDGE,"fcba4419-a2ee-464f-be9d-58f11bf3418b.sketch_text.stroke-58"),sQuery(id+"F2.wireOp",EDGE,"fcba4419-a2ee-464f-be9d-58f11bf3418b.sketch_text.stroke-59"),sQuery(id+"F2.wireOp",EDGE,"fcba4419-a2ee-464f-be9d-58f11bf3418b.sketch_text.stroke-60"),sQuery(id+"F2.wireOp",EDGE,"fcba4419-a2ee-464f-be9d-58f11bf3418b.sketch_text.stroke-61"),sQuery(id+"F2.wireOp",EDGE,"fcba4419-a2ee-464f-be9d-58f11bf3418b.sketch_text.stroke-62"),sQuery(id+"F2.wireOp",EDGE,"fcba4419-a2ee-464f-be9d-58f11bf3418b.sketch_text.stroke-63"),sQuery(id+"F2.wireOp",EDGE,"fcba4419-a2ee-464f-be9d-58f11bf3418b.sketch_text.stroke-64"),sQuery(id+"F2.wireOp",EDGE,"fcba4419-a2ee-464f-be9d-58f11bf3418b.sketch_text.stroke-65"),sQuery(id+"F2.wireOp",EDGE,"fcba4419-a2ee-464f-be9d-58f11bf3418b.sketch_text.stroke-66"),sQuery(id+"F2.wireOp",EDGE,"fcba4419-a2ee-464f-be9d-58f11bf3418b.sketch_text.stroke-67"),sQuery(id+"F2.wireOp",EDGE,"fcba4419-a2ee-464f-be9d-58f11bf3418b.sketch_text.stroke-68"),sQuery(id+"F2.wireOp",EDGE,"fcba4419-a2ee-464f-be9d-58f11bf3418b.sketch_text.stroke-69"),sQuery(id+"F2.wireOp",EDGE,"fcba4419-a2ee-464f-be9d-58f11bf3418b.sketch_text.stroke-70"),sQuery(id+"F2.wireOp",EDGE,"fcba4419-a2ee-464f-be9d-58f11bf3418b.sketch_text.stroke-71"),sQuery(id+"F2.wireOp",EDGE,"fcba4419-a2ee-464f-be9d-58f11bf3418b.sketch_text.stroke-72"),sQuery(id+"F2.wireOp",EDGE,"fcba4419-a2ee-464f-be9d-58f11bf3418b.sketch_text.stroke-73"),sQuery(id+"F2.wireOp",EDGE,"fcba4419-a2ee-464f-be9d-58f11bf3418b.sketch_text.stroke-74"),sQuery(id+"F2.wireOp",EDGE,"fcba4419-a2ee-464f-be9d-58f11bf3418b.sketch_text.stroke-75"),sQuery(id+"F2.wireOp",EDGE,"fcba4419-a2ee-464f-be9d-58f11bf3418b.sketch_text.stroke-76"),sQuery(id+"F2.wireOp",EDGE,"fcba4419-a2ee-464f-be9d-58f11bf3418b.sketch_text.stroke-77"),sQuery(id+"F2.wireOp",EDGE,"fcba4419-a2ee-464f-be9d-58f11bf3418b.sketch_text.stroke-78"),sQuery(id+"F2.wireOp",EDGE,"fcba4419-a2ee-464f-be9d-58f11bf3418b.sketch_text.stroke-79"),sQuery(id+"F2.wireOp",EDGE,"fcba4419-a2ee-464f-be9d-58f11bf3418b.sketch_text.stroke-80"),sQuery(id+"F2.wireOp",EDGE,"fcba4419-a2ee-464f-be9d-58f11bf3418b.sketch_text.stroke-81"),sQuery(id+"F2.wireOp",EDGE,"fcba4419-a2ee-464f-be9d-58f11bf3418b.sketch_text.stroke-82"),sQuery(id+"F2.wireOp",EDGE,"fcba4419-a2ee-464f-be9d-58f11bf3418b.sketch_text.stroke-83"),sQuery(id+"F2.wireOp",EDGE,"fcba4419-a2ee-464f-be9d-58f11bf3418b.sketch_text.stroke-84"),sQuery(id+"F2.wireOp",EDGE,"fcba4419-a2ee-464f-be9d-58f11bf3418b.sketch_text.stroke-85"),sQuery(id+"F2.wireOp",EDGE,"fcba4419-a2ee-464f-be9d-58f11bf3418b.sketch_text.stroke-86"),sQuery(id+"F2.wireOp",EDGE,"fcba4419-a2ee-464f-be9d-58f11bf3418b.sketch_text.stroke-87"),sQuery(id+"F2.wireOp",EDGE,"fcba4419-a2ee-464f-be9d-58f11bf3418b.sketch_text.stroke-88"),sQuery(id+"F2.wireOp",EDGE,"fcba4419-a2ee-464f-be9d-58f11bf3418b.sketch_text.stroke-89"),sQuery(id+"F2.wireOp",EDGE,"fcba4419-a2ee-464f-be9d-58f11bf3418b.sketch_text.stroke-90"),sQuery(id+"F2.wireOp",EDGE,"fcba4419-a2ee-464f-be9d-58f11bf3418b.sketch_text.stroke-91"),sQuery(id+"F2.wireOp",EDGE,"fcba4419-a2ee-464f-be9d-58f11bf3418b.sketch_text.stroke-92"),sQuery(id+"F2.wireOp",EDGE,"fcba4419-a2ee-464f-be9d-58f11bf3418b.sketch_text.stroke-93"),sQuery(id+"F2.wireOp",EDGE,"fcba4419-a2ee-464f-be9d-58f11bf3418b.sketch_text.stroke-94"),sQuery(id+"F2.wireOp",EDGE,"fcba4419-a2ee-464f-be9d-58f11bf3418b.sketch_text.stroke-95"),sQuery(id+"F2.wireOp",EDGE,"fcba4419-a2ee-464f-be9d-58f11bf3418b.sketch_text.stroke-96"),sQuery(id+"F2.wireOp",EDGE,"fcba4419-a2ee-464f-be9d-58f11bf3418b.sketch_text.stroke-97"),sQuery(id+"F2.wireOp",EDGE,"fcba4419-a2ee-464f-be9d-58f11bf3418b.sketch_text.stroke-98"),sQuery(id+"F2.wireOp",EDGE,"fcba4419-a2ee-464f-be9d-58f11bf3418b.sketch_text.stroke-99"),sQuery(id+"F2.wireOp",EDGE,"fcba4419-a2ee-464f-be9d-58f11bf3418b.sketch_text.stroke-100"),sQuery(id+"F2.wireOp",EDGE,"fcba4419-a2ee-464f-be9d-58f11bf3418b.sketch_text.stroke-101"),sQuery(id+"F2.wireOp",EDGE,"fcba4419-a2ee-464f-be9d-58f11bf3418b.sketch_text.stroke-102"),sQuery(id+"F2.wireOp",EDGE,"fcba4419-a2ee-464f-be9d-58f11bf3418b.sketch_text.stroke-103"),sQuery(id+"F2.wireOp",EDGE,"fcba4419-a2ee-464f-be9d-58f11bf3418b.sketch_text.stroke-104"),sQuery(id+"F2.wireOp",EDGE,"fcba4419-a2ee-464f-be9d-58f11bf3418b.sketch_text.stroke-105"),sQuery(id+"F2.wireOp",EDGE,"fcba4419-a2ee-464f-be9d-58f11bf3418b.sketch_text.stroke-106"),sQuery(id+"F2.wireOp",EDGE,"fcba4419-a2ee-464f-be9d-58f11bf3418b.sketch_text.stroke-107"),sQuery(id+"F2.wireOp",EDGE,"fcba4419-a2ee-464f-be9d-58f11bf3418b.sketch_text.stroke-108"),sQuery(id+"F2.wireOp",EDGE,"fcba4419-a2ee-464f-be9d-58f11bf3418b.sketch_text.stroke-109"),sQuery(id+"F2.wireOp",EDGE,"fcba4419-a2ee-464f-be9d-58f11bf3418b.sketch_text.stroke-110"),sQuery(id+"F2.wireOp",EDGE,"fcba4419-a2ee-464f-be9d-58f11bf3418b.sketch_text.stroke-111"),sQuery(id+"F2.wireOp",EDGE,"fcba4419-a2ee-464f-be9d-58f11bf3418b.sketch_text.stroke-112"),sQuery(id+"F2.wireOp",EDGE,"fcba4419-a2ee-464f-be9d-58f11bf3418b.sketch_text.stroke-113"),sQuery(id+"F2.wireOp",EDGE,"fcba4419-a2ee-464f-be9d-58f11bf3418b.sketch_text.stroke-114"),sQuery(id+"F2.wireOp",EDGE,"fcba4419-a2ee-464f-be9d-58f11bf3418b.sketch_text.stroke-115"),sQuery(id+"F2.wireOp",EDGE,"fcba4419-a2ee-464f-be9d-58f11bf3418b.sketch_text.stroke-116"),sQuery(id+"F2.wireOp",EDGE,"fcba4419-a2ee-464f-be9d-58f11bf3418b.sketch_text.stroke-117"),sQuery(id+"F2.wireOp",EDGE,"fcba4419-a2ee-464f-be9d-58f11bf3418b.sketch_text.stroke-118"),sQuery(id+"F2.wireOp",EDGE,"fcba4419-a2ee-464f-be9d-58f11bf3418b.sketch_text.stroke-119"),sQuery(id+"F2.wireOp",EDGE,"fcba4419-a2ee-464f-be9d-58f11bf3418b.sketch_text.stroke-120"),sQuery(id+"F2.wireOp",EDGE,"fcba4419-a2ee-464f-be9d-58f11bf3418b.sketch_text.stroke-121"),sQuery(id+"F2.wireOp",EDGE,"fcba4419-a2ee-464f-be9d-58f11bf3418b.sketch_text.stroke-122"),sQuery(id+"F2.wireOp",EDGE,"fcba4419-a2ee-464f-be9d-58f11bf3418b.sketch_text.stroke-123"),sQuery(id+"F2.wireOp",EDGE,"fcba4419-a2ee-464f-be9d-58f11bf3418b.sketch_text.stroke-124"),sQuery(id+"F2.wireOp",EDGE,"fcba4419-a2ee-464f-be9d-58f11bf3418b.sketch_text.stroke-125"),sQuery(id+"F2.wireOp",EDGE,"fcba4419-a2ee-464f-be9d-58f11bf3418b.sketch_text.stroke-126"),sQuery(id+"F2.wireOp",EDGE,"fcba4419-a2ee-464f-be9d-58f11bf3418b.sketch_text.stroke-127"),sQuery(id+"F2.wireOp",EDGE,"fcba4419-a2ee-464f-be9d-58f11bf3418b.sketch_text.stroke-128"),sQuery(id+"F2.wireOp",EDGE,"fcba4419-a2ee-464f-be9d-58f11bf3418b.sketch_text.stroke-129"),sQuery(id+"F2.wireOp",EDGE,"fcba4419-a2ee-464f-be9d-58f11bf3418b.sketch_text.stroke-130"),sQuery(id+"F2.wireOp",EDGE,"fcba4419-a2ee-464f-be9d-58f11bf3418b.sketch_text.stroke-131"),sQuery(id+"F2.wireOp",EDGE,"fcba4419-a2ee-464f-be9d-58f11bf3418b.sketch_text.stroke-132"),sQuery(id+"F2.wireOp",EDGE,"fcba4419-a2ee-464f-be9d-58f11bf3418b.sketch_text.stroke-133"),sQuery(id+"F2.wireOp",EDGE,"fcba4419-a2ee-464f-be9d-58f11bf3418b.sketch_text.stroke-134"),sQuery(id+"F2.wireOp",EDGE,"fcba4419-a2ee-464f-be9d-58f11bf3418b.sketch_text.stroke-135"),sQuery(id+"F2.wireOp",EDGE,"fcba4419-a2ee-464f-be9d-58f11bf3418b.sketch_text.stroke-136"),sQuery(id+"F2.wireOp",EDGE,"fcba4419-a2ee-464f-be9d-58f11bf3418b.sketch_text.stroke-137"),sQuery(id+"F2.wireOp",EDGE,"fcba4419-a2ee-464f-be9d-58f11bf3418b.sketch_text.stroke-138"),sQuery(id+"F2.wireOp",EDGE,"fcba4419-a2ee-464f-be9d-58f11bf3418b.sketch_text.stroke-139"),sQuery(id+"F2.wireOp",EDGE,"fcba4419-a2ee-464f-be9d-58f11bf3418b.sketch_text.stroke-140"),sQuery(id+"F2.wireOp",EDGE,"fcba4419-a2ee-464f-be9d-58f11bf3418b.sketch_text.stroke-141"),sQuery(id+"F2.wireOp",EDGE,"fcba4419-a2ee-464f-be9d-58f11bf3418b.sketch_text.stroke-142"),sQuery(id+"F2.wireOp",EDGE,"fcba4419-a2ee-464f-be9d-58f11bf3418b.sketch_text.stroke-143"),sQuery(id+"F2.wireOp",EDGE,"fcba4419-a2ee-464f-be9d-58f11bf3418b.sketch_text.stroke-144"),sQuery(id+"F2.wireOp",EDGE,"fcba4419-a2ee-464f-be9d-58f11bf3418b.sketch_text.stroke-145"),sQuery(id+"F2.wireOp",EDGE,"fcba4419-a2ee-464f-be9d-58f11bf3418b.sketch_text.stroke-146"),sQuery(id+"F2.wireOp",EDGE,"fcba4419-a2ee-464f-be9d-58f11bf3418b.sketch_text.stroke-147"),sQuery(id+"F2.wireOp",EDGE,"fcba4419-a2ee-464f-be9d-58f11bf3418b.sketch_text.stroke-148"),sQuery(id+"F2.wireOp",EDGE,"fcba4419-a2ee-464f-be9d-58f11bf3418b.sketch_text.stroke-149"),sQuery(id+"F2.wireOp",EDGE,"fcba4419-a2ee-464f-be9d-58f11bf3418b.sketch_text.stroke-150"),sQuery(id+"F2.wireOp",EDGE,"fcba4419-a2ee-464f-be9d-58f11bf3418b.sketch_text.stroke-151"),sQuery(id+"F2.wireOp",EDGE,"fcba4419-a2ee-464f-be9d-58f11bf3418b.sketch_text.stroke-152"),sQuery(id+"F2.wireOp",EDGE,"fcba4419-a2ee-464f-be9d-58f11bf3418b.sketch_text.stroke-153"),sQuery(id+"F2.wireOp",EDGE,"fcba4419-a2ee-464f-be9d-58f11bf3418b.sketch_text.stroke-154"),sQuery(id+"F2.wireOp",EDGE,"fcba4419-a2ee-464f-be9d-58f11bf3418b.sketch_text.stroke-155"),sQuery(id+"F2.wireOp",EDGE,"fcba4419-a2ee-464f-be9d-58f11bf3418b.sketch_text.stroke-156"),sQuery(id+"F2.wireOp",EDGE,"fcba4419-a2ee-464f-be9d-58f11bf3418b.sketch_text.stroke-157"),sQuery(id+"F2.wireOp",EDGE,"fcba4419-a2ee-464f-be9d-58f11bf3418b.sketch_text.stroke-158"),sQuery(id+"F2.wireOp",EDGE,"fcba4419-a2ee-464f-be9d-58f11bf3418b.sketch_text.stroke-159"),sQuery(id+"F2.wireOp",EDGE,"fcba4419-a2ee-464f-be9d-58f11bf3418b.sketch_text.stroke-160"),sQuery(id+"F2.wireOp",EDGE,"fcba4419-a2ee-464f-be9d-58f11bf3418b.sketch_text.stroke-161"),sQuery(id+"F2.wireOp",EDGE,"fcba4419-a2ee-464f-be9d-58f11bf3418b.sketch_text.stroke-162"),sQuery(id+"F2.wireOp",EDGE,"fcba4419-a2ee-464f-be9d-58f11bf3418b.sketch_text.stroke-163"),sQuery(id+"F2.wireOp",EDGE,"fcba4419-a2ee-464f-be9d-58f11bf3418b.sketch_text.stroke-164"),sQuery(id+"F2.wireOp",EDGE,"fcba4419-a2ee-464f-be9d-58f11bf3418b.sketch_text.stroke-165"),sQuery(id+"F2.wireOp",EDGE,"fcba4419-a2ee-464f-be9d-58f11bf3418b.sketch_text.stroke-166"),sQuery(id+"F2.wireOp",EDGE,"fcba4419-a2ee-464f-be9d-58f11bf3418b.sketch_text.stroke-167"),sQuery(id+"F2.wireOp",EDGE,"fcba4419-a2ee-464f-be9d-58f11bf3418b.sketch_text.stroke-168"),sQuery(id+"F2.wireOp",EDGE,"fcba4419-a2ee-464f-be9d-58f11bf3418b.sketch_text.stroke-169"),sQuery(id+"F2.wireOp",EDGE,"fcba4419-a2ee-464f-be9d-58f11bf3418b.sketch_text.stroke-170"),sQuery(id+"F2.wireOp",EDGE,"fcba4419-a2ee-464f-be9d-58f11bf3418b.sketch_text.stroke-171"),sQuery(id+"F2.wireOp",EDGE,"fcba4419-a2ee-464f-be9d-58f11bf3418b.sketch_text.stroke-172"),sQuery(id+"F2.wireOp",EDGE,"fcba4419-a2ee-464f-be9d-58f11bf3418b.sketch_text.stroke-173"),sQuery(id+"FHMxAyK4CFUKdhS_1.wireOp",EDGE,"1cb9c079-ea9b-4899-8069-e0e3048e911d.sketch_text.stroke-0"),sQuery(id+"FHMxAyK4CFUKdhS_1.wireOp",EDGE,"1cb9c079-ea9b-4899-8069-e0e3048e911d.sketch_text.stroke-1"),sQuery(id+"FHMxAyK4CFUKdhS_1.wireOp",EDGE,"1cb9c079-ea9b-4899-8069-e0e3048e911d.sketch_text.stroke-2"),sQuery(id+"FHMxAyK4CFUKdhS_1.wireOp",EDGE,"1cb9c079-ea9b-4899-8069-e0e3048e911d.sketch_text.stroke-3"),sQuery(id+"FHMxAyK4CFUKdhS_1.wireOp",EDGE,"1cb9c079-ea9b-4899-8069-e0e3048e911d.sketch_text.stroke-4"),sQuery(id+"FHMxAyK4CFUKdhS_1.wireOp",EDGE,"1cb9c079-ea9b-4899-8069-e0e3048e911d.sketch_text.stroke-5"),sQuery(id+"FHMxAyK4CFUKdhS_1.wireOp",EDGE,"1cb9c079-ea9b-4899-8069-e0e3048e911d.sketch_text.stroke-6"),sQuery(id+"FHMxAyK4CFUKdhS_1.wireOp",EDGE,"1cb9c079-ea9b-4899-8069-e0e3048e911d.sketch_text.stroke-7"),sQuery(id+"FHMxAyK4CFUKdhS_1.wireOp",EDGE,"1cb9c079-ea9b-4899-8069-e0e3048e911d.sketch_text.stroke-8"),sQuery(id+"FHMxAyK4CFUKdhS_1.wireOp",EDGE,"1cb9c079-ea9b-4899-8069-e0e3048e911d.sketch_text.stroke-9"),sQuery(id+"FHMxAyK4CFUKdhS_1.wireOp",EDGE,"1cb9c079-ea9b-4899-8069-e0e3048e911d.sketch_text.stroke-10"),sQuery(id+"FHMxAyK4CFUKdhS_1.wireOp",EDGE,"1cb9c079-ea9b-4899-8069-e0e3048e911d.sketch_text.stroke-11"),sQuery(id+"FHMxAyK4CFUKdhS_1.wireOp",EDGE,"1cb9c079-ea9b-4899-8069-e0e3048e911d.sketch_text.stroke-12"),sQuery(id+"FHMxAyK4CFUKdhS_1.wireOp",EDGE,"1cb9c079-ea9b-4899-8069-e0e3048e911d.sketch_text.stroke-13"),sQuery(id+"FHMxAyK4CFUKdhS_1.wireOp",EDGE,"1cb9c079-ea9b-4899-8069-e0e3048e911d.sketch_text.stroke-14"),sQuery(id+"FHMxAyK4CFUKdhS_1.wireOp",EDGE,"1cb9c079-ea9b-4899-8069-e0e3048e911d.sketch_text.stroke-15"),sQuery(id+"FHMxAyK4CFUKdhS_1.wireOp",EDGE,"1cb9c079-ea9b-4899-8069-e0e3048e911d.sketch_text.stroke-16"),sQuery(id+"FHMxAyK4CFUKdhS_1.wireOp",EDGE,"1cb9c079-ea9b-4899-8069-e0e3048e911d.sketch_text.stroke-17"),sQuery(id+"FHMxAyK4CFUKdhS_1.wireOp",EDGE,"1cb9c079-ea9b-4899-8069-e0e3048e911d.sketch_text.stroke-18"),sQuery(id+"FHMxAyK4CFUKdhS_1.wireOp",EDGE,"1cb9c079-ea9b-4899-8069-e0e3048e911d.sketch_text.stroke-19"),sQuery(id+"FHMxAyK4CFUKdhS_1.wireOp",EDGE,"1cb9c079-ea9b-4899-8069-e0e3048e911d.sketch_text.stroke-20"),sQuery(id+"FHMxAyK4CFUKdhS_1.wireOp",EDGE,"1cb9c079-ea9b-4899-8069-e0e3048e911d.sketch_text.stroke-21"),sQuery(id+"FHMxAyK4CFUKdhS_1.wireOp",EDGE,"1cb9c079-ea9b-4899-8069-e0e3048e911d.sketch_text.stroke-22"),sQuery(id+"FHMxAyK4CFUKdhS_1.wireOp",EDGE,"1cb9c079-ea9b-4899-8069-e0e3048e911d.sketch_text.stroke-23"),sQuery(id+"FHMxAyK4CFUKdhS_1.wireOp",EDGE,"1cb9c079-ea9b-4899-8069-e0e3048e911d.sketch_text.stroke-24"),sQuery(id+"FHMxAyK4CFUKdhS_1.wireOp",EDGE,"1cb9c079-ea9b-4899-8069-e0e3048e911d.sketch_text.stroke-25"),sQuery(id+"FHMxAyK4CFUKdhS_1.wireOp",EDGE,"1cb9c079-ea9b-4899-8069-e0e3048e911d.sketch_text.stroke-26"),sQuery(id+"FHMxAyK4CFUKdhS_1.wireOp",EDGE,"1cb9c079-ea9b-4899-8069-e0e3048e911d.sketch_text.stroke-27"),sQuery(id+"FHMxAyK4CFUKdhS_1.wireOp",EDGE,"1cb9c079-ea9b-4899-8069-e0e3048e911d.sketch_text.stroke-28"),sQuery(id+"FHMxAyK4CFUKdhS_1.wireOp",EDGE,"1cb9c079-ea9b-4899-8069-e0e3048e911d.sketch_text.stroke-29"),sQuery(id+"FHMxAyK4CFUKdhS_1.wireOp",EDGE,"1cb9c079-ea9b-4899-8069-e0e3048e911d.sketch_text.stroke-30"),sQuery(id+"FHMxAyK4CFUKdhS_1.wireOp",EDGE,"1cb9c079-ea9b-4899-8069-e0e3048e911d.sketch_text.stroke-31"),sQuery(id+"FHMxAyK4CFUKdhS_1.wireOp",EDGE,"1cb9c079-ea9b-4899-8069-e0e3048e911d.sketch_text.stroke-32"),sQuery(id+"FHMxAyK4CFUKdhS_1.wireOp",EDGE,"1cb9c079-ea9b-4899-8069-e0e3048e911d.sketch_text.stroke-33"),sQuery(id+"FHMxAyK4CFUKdhS_1.wireOp",EDGE,"1cb9c079-ea9b-4899-8069-e0e3048e911d.sketch_text.stroke-34"),sQuery(id+"FHMxAyK4CFUKdhS_1.wireOp",EDGE,"1cb9c079-ea9b-4899-8069-e0e3048e911d.sketch_text.stroke-35"),sQuery(id+"FHMxAyK4CFUKdhS_1.wireOp",EDGE,"1cb9c079-ea9b-4899-8069-e0e3048e911d.sketch_text.stroke-36"),sQuery(id+"FHMxAyK4CFUKdhS_1.wireOp",EDGE,"1cb9c079-ea9b-4899-8069-e0e3048e911d.sketch_text.stroke-37"),sQuery(id+"FHMxAyK4CFUKdhS_1.wireOp",EDGE,"1cb9c079-ea9b-4899-8069-e0e3048e911d.sketch_text.stroke-38"),sQuery(id+"FHMxAyK4CFUKdhS_1.wireOp",EDGE,"1cb9c079-ea9b-4899-8069-e0e3048e911d.sketch_text.stroke-39"),sQuery(id+"FHMxAyK4CFUKdhS_1.wireOp",EDGE,"1cb9c079-ea9b-4899-8069-e0e3048e911d.sketch_text.stroke-40"),sQuery(id+"FHMxAyK4CFUKdhS_1.wireOp",EDGE,"1cb9c079-ea9b-4899-8069-e0e3048e911d.sketch_text.stroke-41"),sQuery(id+"FHMxAyK4CFUKdhS_1.wireOp",EDGE,"1cb9c079-ea9b-4899-8069-e0e3048e911d.sketch_text.stroke-42"),sQuery(id+"FHMxAyK4CFUKdhS_1.wireOp",EDGE,"1cb9c079-ea9b-4899-8069-e0e3048e911d.sketch_text.stroke-43"),sQuery(id+"FHMxAyK4CFUKdhS_1.wireOp",EDGE,"1cb9c079-ea9b-4899-8069-e0e3048e911d.sketch_text.stroke-44"),sQuery(id+"FHMxAyK4CFUKdhS_1.wireOp",EDGE,"1cb9c079-ea9b-4899-8069-e0e3048e911d.sketch_text.stroke-45"),sQuery(id+"FHMxAyK4CFUKdhS_1.wireOp",EDGE,"1cb9c079-ea9b-4899-8069-e0e3048e911d.sketch_text.stroke-46"),sQuery(id+"FHMxAyK4CFUKdhS_1.wireOp",EDGE,"1cb9c079-ea9b-4899-8069-e0e3048e911d.sketch_text.stroke-47"),sQuery(id+"FHMxAyK4CFUKdhS_1.wireOp",EDGE,"1cb9c079-ea9b-4899-8069-e0e3048e911d.sketch_text.stroke-48"),sQuery(id+"FHMxAyK4CFUKdhS_1.wireOp",EDGE,"1cb9c079-ea9b-4899-8069-e0e3048e911d.sketch_text.stroke-49"),sQuery(id+"FHMxAyK4CFUKdhS_1.wireOp",EDGE,"1cb9c079-ea9b-4899-8069-e0e3048e911d.sketch_text.stroke-50"),sQuery(id+"FHMxAyK4CFUKdhS_1.wireOp",EDGE,"1cb9c079-ea9b-4899-8069-e0e3048e911d.sketch_text.stroke-51"),sQuery(id+"FHMxAyK4CFUKdhS_1.wireOp",EDGE,"1cb9c079-ea9b-4899-8069-e0e3048e911d.sketch_text.stroke-52"),sQuery(id+"FHMxAyK4CFUKdhS_1.wireOp",EDGE,"1cb9c079-ea9b-4899-8069-e0e3048e911d.sketch_text.stroke-53"),sQuery(id+"FHMxAyK4CFUKdhS_1.wireOp",EDGE,"1cb9c079-ea9b-4899-8069-e0e3048e911d.sketch_text.stroke-54"),sQuery(id+"FHMxAyK4CFUKdhS_1.wireOp",EDGE,"1cb9c079-ea9b-4899-8069-e0e3048e911d.sketch_text.stroke-55"),sQuery(id+"FHMxAyK4CFUKdhS_1.wireOp",EDGE,"1cb9c079-ea9b-4899-8069-e0e3048e911d.sketch_text.stroke-56"),sQuery(id+"FHMxAyK4CFUKdhS_1.wireOp",EDGE,"1cb9c079-ea9b-4899-8069-e0e3048e911d.sketch_text.stroke-57"),sQuery(id+"FHMxAyK4CFUKdhS_1.wireOp",EDGE,"1cb9c079-ea9b-4899-8069-e0e3048e911d.sketch_text.stroke-58"),sQuery(id+"FHMxAyK4CFUKdhS_1.wireOp",EDGE,"1cb9c079-ea9b-4899-8069-e0e3048e911d.sketch_text.stroke-59"),sQuery(id+"FHMxAyK4CFUKdhS_1.wireOp",EDGE,"1cb9c079-ea9b-4899-8069-e0e3048e911d.sketch_text.stroke-60"),sQuery(id+"FHMxAyK4CFUKdhS_1.wireOp",EDGE,"1cb9c079-ea9b-4899-8069-e0e3048e911d.sketch_text.stroke-61"),sQuery(id+"FHMxAyK4CFUKdhS_1.wireOp",EDGE,"1cb9c079-ea9b-4899-8069-e0e3048e911d.sketch_text.stroke-62"),sQuery(id+"FHMxAyK4CFUKdhS_1.wireOp",EDGE,"1cb9c079-ea9b-4899-8069-e0e3048e911d.sketch_text.stroke-71"),sQuery(id+"FHMxAyK4CFUKdhS_1.wireOp",EDGE,"1cb9c079-ea9b-4899-8069-e0e3048e911d.sketch_text.stroke-72"),sQuery(id+"FHMxAyK4CFUKdhS_1.wireOp",EDGE,"1cb9c079-ea9b-4899-8069-e0e3048e911d.sketch_text.stroke-73"),sQuery(id+"FHMxAyK4CFUKdhS_1.wireOp",EDGE,"1cb9c079-ea9b-4899-8069-e0e3048e911d.sketch_text.stroke-74"),sQuery(id+"FHMxAyK4CFUKdhS_1.wireOp",EDGE,"1cb9c079-ea9b-4899-8069-e0e3048e911d.sketch_text.stroke-75"),sQuery(id+"FHMxAyK4CFUKdhS_1.wireOp",EDGE,"1cb9c079-ea9b-4899-8069-e0e3048e911d.sketch_text.stroke-76"),sQuery(id+"FHMxAyK4CFUKdhS_1.wireOp",EDGE,"1cb9c079-ea9b-4899-8069-e0e3048e911d.sketch_text.stroke-77"),sQuery(id+"FHMxAyK4CFUKdhS_1.wireOp",EDGE,"1cb9c079-ea9b-4899-8069-e0e3048e911d.sketch_text.stroke-78"),sQuery(id+"FHMxAyK4CFUKdhS_1.wireOp",EDGE,"1cb9c079-ea9b-4899-8069-e0e3048e911d.sketch_text.stroke-79"),sQuery(id+"FHMxAyK4CFUKdhS_1.wireOp",EDGE,"1cb9c079-ea9b-4899-8069-e0e3048e911d.sketch_text.stroke-80"),sQuery(id+"FHMxAyK4CFUKdhS_1.wireOp",EDGE,"1cb9c079-ea9b-4899-8069-e0e3048e911d.sketch_text.stroke-81"),sQuery(id+"FHMxAyK4CFUKdhS_1.wireOp",EDGE,"1cb9c079-ea9b-4899-8069-e0e3048e911d.sketch_text.stroke-82"),sQuery(id+"FHMxAyK4CFUKdhS_1.wireOp",EDGE,"1cb9c079-ea9b-4899-8069-e0e3048e911d.sketch_text.stroke-83"),sQuery(id+"FHMxAyK4CFUKdhS_1.wireOp",EDGE,"1cb9c079-ea9b-4899-8069-e0e3048e911d.sketch_text.stroke-84"),sQuery(id+"FHMxAyK4CFUKdhS_1.wireOp",EDGE,"1cb9c079-ea9b-4899-8069-e0e3048e911d.sketch_text.stroke-85"),sQuery(id+"FHMxAyK4CFUKdhS_1.wireOp",EDGE,"1cb9c079-ea9b-4899-8069-e0e3048e911d.sketch_text.stroke-86"),sQuery(id+"FHMxAyK4CFUKdhS_1.wireOp",EDGE,"1cb9c079-ea9b-4899-8069-e0e3048e911d.sketch_text.stroke-87"),sQuery(id+"FHMxAyK4CFUKdhS_1.wireOp",EDGE,"1cb9c079-ea9b-4899-8069-e0e3048e911d.sketch_text.stroke-88"),sQuery(id+"FHMxAyK4CFUKdhS_1.wireOp",EDGE,"1cb9c079-ea9b-4899-8069-e0e3048e911d.sketch_text.stroke-89"),sQuery(id+"FHMxAyK4CFUKdhS_1.wireOp",EDGE,"1cb9c079-ea9b-4899-8069-e0e3048e911d.sketch_text.stroke-90"),sQuery(id+"FHMxAyK4CFUKdhS_1.wireOp",EDGE,"1cb9c079-ea9b-4899-8069-e0e3048e911d.sketch_text.stroke-91"),sQuery(id+"FHMxAyK4CFUKdhS_1.wireOp",EDGE,"1cb9c079-ea9b-4899-8069-e0e3048e911d.sketch_text.stroke-92"),sQuery(id+"FHMxAyK4CFUKdhS_1.wireOp",EDGE,"1cb9c079-ea9b-4899-8069-e0e3048e911d.sketch_text.stroke-93"),sQuery(id+"FHMxAyK4CFUKdhS_1.wireOp",EDGE,"1cb9c079-ea9b-4899-8069-e0e3048e911d.sketch_text.stroke-94"),sQuery(id+"FHMxAyK4CFUKdhS_1.wireOp",EDGE,"1cb9c079-ea9b-4899-8069-e0e3048e911d.sketch_text.stroke-95"),sQuery(id+"FHMxAyK4CFUKdhS_1.wireOp",EDGE,"1cb9c079-ea9b-4899-8069-e0e3048e911d.sketch_text.stroke-96"),sQuery(id+"FHMxAyK4CFUKdhS_1.wireOp",EDGE,"1cb9c079-ea9b-4899-8069-e0e3048e911d.sketch_text.stroke-97"),sQuery(id+"FHMxAyK4CFUKdhS_1.wireOp",EDGE,"1cb9c079-ea9b-4899-8069-e0e3048e911d.sketch_text.stroke-103"),sQuery(id+"FHMxAyK4CFUKdhS_1.wireOp",EDGE,"1cb9c079-ea9b-4899-8069-e0e3048e911d.sketch_text.stroke-104"),sQuery(id+"FHMxAyK4CFUKdhS_1.wireOp",EDGE,"1cb9c079-ea9b-4899-8069-e0e3048e911d.sketch_text.stroke-105"),sQuery(id+"FHMxAyK4CFUKdhS_1.wireOp",EDGE,"1cb9c079-ea9b-4899-8069-e0e3048e911d.sketch_text.stroke-106"),sQuery(id+"FHMxAyK4CFUKdhS_1.wireOp",EDGE,"1cb9c079-ea9b-4899-8069-e0e3048e911d.sketch_text.stroke-107"),sQuery(id+"FHMxAyK4CFUKdhS_1.wireOp",EDGE,"1cb9c079-ea9b-4899-8069-e0e3048e911d.sketch_text.stroke-108"),sQuery(id+"FHMxAyK4CFUKdhS_1.wireOp",EDGE,"1cb9c079-ea9b-4899-8069-e0e3048e911d.sketch_text.stroke-109"),sQuery(id+"FHMxAyK4CFUKdhS_1.wireOp",EDGE,"1cb9c079-ea9b-4899-8069-e0e3048e911d.sketch_text.stroke-110"),sQuery(id+"FHMxAyK4CFUKdhS_1.wireOp",EDGE,"1cb9c079-ea9b-4899-8069-e0e3048e911d.sketch_text.stroke-111"),sQuery(id+"FHMxAyK4CFUKdhS_1.wireOp",EDGE,"1cb9c079-ea9b-4899-8069-e0e3048e911d.sketch_text.stroke-112"),sQuery(id+"FHMxAyK4CFUKdhS_1.wireOp",EDGE,"1cb9c079-ea9b-4899-8069-e0e3048e911d.sketch_text.stroke-113"),sQuery(id+"FHMxAyK4CFUKdhS_1.wireOp",EDGE,"1cb9c079-ea9b-4899-8069-e0e3048e911d.sketch_text.stroke-114"),sQuery(id+"FHMxAyK4CFUKdhS_1.wireOp",EDGE,"1cb9c079-ea9b-4899-8069-e0e3048e911d.sketch_text.stroke-115"),sQuery(id+"FHMxAyK4CFUKdhS_1.wireOp",EDGE,"1cb9c079-ea9b-4899-8069-e0e3048e911d.sketch_text.stroke-116"),sQuery(id+"FHMxAyK4CFUKdhS_1.wireOp",EDGE,"1cb9c079-ea9b-4899-8069-e0e3048e911d.sketch_text.stroke-117"),sQuery(id+"FHMxAyK4CFUKdhS_1.wireOp",EDGE,"1cb9c079-ea9b-4899-8069-e0e3048e911d.sketch_text.stroke-118"),sQuery(id+"FHMxAyK4CFUKdhS_1.wireOp",EDGE,"1cb9c079-ea9b-4899-8069-e0e3048e911d.sketch_text.stroke-119"),sQuery(id+"FHMxAyK4CFUKdhS_1.wireOp",EDGE,"1cb9c079-ea9b-4899-8069-e0e3048e911d.sketch_text.stroke-120"),sQuery(id+"FHMxAyK4CFUKdhS_1.wireOp",EDGE,"1cb9c079-ea9b-4899-8069-e0e3048e911d.sketch_text.stroke-121"),sQuery(id+"FHMxAyK4CFUKdhS_1.wireOp",EDGE,"1cb9c079-ea9b-4899-8069-e0e3048e911d.sketch_text.stroke-122"),sQuery(id+"FHMxAyK4CFUKdhS_1.wireOp",EDGE,"1cb9c079-ea9b-4899-8069-e0e3048e911d.sketch_text.stroke-123"),sQuery(id+"FHMxAyK4CFUKdhS_1.wireOp",EDGE,"1cb9c079-ea9b-4899-8069-e0e3048e911d.sketch_text.stroke-124"),sQuery(id+"FHMxAyK4CFUKdhS_1.wireOp",EDGE,"1cb9c079-ea9b-4899-8069-e0e3048e911d.sketch_text.stroke-125"),sQuery(id+"FHMxAyK4CFUKdhS_1.wireOp",EDGE,"1cb9c079-ea9b-4899-8069-e0e3048e911d.sketch_text.stroke-126"),sQuery(id+"FHMxAyK4CFUKdhS_1.wireOp",EDGE,"1cb9c079-ea9b-4899-8069-e0e3048e911d.sketch_text.stroke-127"),sQuery(id+"FHMxAyK4CFUKdhS_1.wireOp",EDGE,"1cb9c079-ea9b-4899-8069-e0e3048e911d.sketch_text.stroke-128"),sQuery(id+"FHMxAyK4CFUKdhS_1.wireOp",EDGE,"1cb9c079-ea9b-4899-8069-e0e3048e911d.sketch_text.stroke-129"),sQuery(id+"FHMxAyK4CFUKdhS_1.wireOp",EDGE,"1cb9c079-ea9b-4899-8069-e0e3048e911d.sketch_text.stroke-130"),sQuery(id+"FHMxAyK4CFUKdhS_1.wireOp",EDGE,"1cb9c079-ea9b-4899-8069-e0e3048e911d.sketch_text.stroke-131"),sQuery(id+"FHMxAyK4CFUKdhS_1.wireOp",EDGE,"1cb9c079-ea9b-4899-8069-e0e3048e911d.sketch_text.stroke-132"),sQuery(id+"FHMxAyK4CFUKdhS_1.wireOp",EDGE,"1cb9c079-ea9b-4899-8069-e0e3048e911d.sketch_text.stroke-133"),sQuery(id+"FHMxAyK4CFUKdhS_1.wireOp",EDGE,"1cb9c079-ea9b-4899-8069-e0e3048e911d.sketch_text.stroke-134"),sQuery(id+"FHMxAyK4CFUKdhS_1.wireOp",EDGE,"1cb9c079-ea9b-4899-8069-e0e3048e911d.sketch_text.stroke-135"),sQuery(id+"FHMxAyK4CFUKdhS_1.wireOp",EDGE,"1cb9c079-ea9b-4899-8069-e0e3048e911d.sketch_text.stroke-136"),sQuery(id+"FHMxAyK4CFUKdhS_1.wireOp",EDGE,"1cb9c079-ea9b-4899-8069-e0e3048e911d.sketch_text.stroke-137"),sQuery(id+"FHMxAyK4CFUKdhS_1.wireOp",EDGE,"1cb9c079-ea9b-4899-8069-e0e3048e911d.sketch_text.stroke-138"),sQuery(id+"FHMxAyK4CFUKdhS_1.wireOp",EDGE,"1cb9c079-ea9b-4899-8069-e0e3048e911d.sketch_text.stroke-139"),sQuery(id+"FHMxAyK4CFUKdhS_1.wireOp",EDGE,"1cb9c079-ea9b-4899-8069-e0e3048e911d.sketch_text.stroke-140"),sQuery(id+"FHMxAyK4CFUKdhS_1.wireOp",EDGE,"1cb9c079-ea9b-4899-8069-e0e3048e911d.sketch_text.stroke-141"),sQuery(id+"FHMxAyK4CFUKdhS_1.wireOp",EDGE,"1cb9c079-ea9b-4899-8069-e0e3048e911d.sketch_text.stroke-142"),sQuery(id+"FHMxAyK4CFUKdhS_1.wireOp",EDGE,"1cb9c079-ea9b-4899-8069-e0e3048e911d.sketch_text.stroke-143"),sQuery(id+"FHMxAyK4CFUKdhS_1.wireOp",EDGE,"1cb9c079-ea9b-4899-8069-e0e3048e911d.sketch_text.stroke-144"),sQuery(id+"FHMxAyK4CFUKdhS_1.wireOp",EDGE,"1cb9c079-ea9b-4899-8069-e0e3048e911d.sketch_text.stroke-145"),sQuery(id+"FHMxAyK4CFUKdhS_1.wireOp",EDGE,"1cb9c079-ea9b-4899-8069-e0e3048e911d.sketch_text.stroke-146"),sQuery(id+"FHMxAyK4CFUKdhS_1.wireOp",EDGE,"1cb9c079-ea9b-4899-8069-e0e3048e911d.sketch_text.stroke-147"),sQuery(id+"FHMxAyK4CFUKdhS_1.wireOp",EDGE,"1cb9c079-ea9b-4899-8069-e0e3048e911d.sketch_text.stroke-148"),sQuery(id+"FHMxAyK4CFUKdhS_1.wireOp",EDGE,"1cb9c079-ea9b-4899-8069-e0e3048e911d.sketch_text.stroke-149"),sQuery(id+"FHMxAyK4CFUKdhS_1.wireOp",EDGE,"1cb9c079-ea9b-4899-8069-e0e3048e911d.sketch_text.stroke-150"),sQuery(id+"FHMxAyK4CFUKdhS_1.wireOp",EDGE,"1cb9c079-ea9b-4899-8069-e0e3048e911d.sketch_text.stroke-151"),sQuery(id+"FHMxAyK4CFUKdhS_1.wireOp",EDGE,"1cb9c079-ea9b-4899-8069-e0e3048e911d.sketch_text.stroke-152"),sQuery(id+"FHMxAyK4CFUKdhS_1.wireOp",EDGE,"1cb9c079-ea9b-4899-8069-e0e3048e911d.sketch_text.stroke-153"),sQuery(id+"FHMxAyK4CFUKdhS_1.wireOp",EDGE,"1cb9c079-ea9b-4899-8069-e0e3048e911d.sketch_text.stroke-159"),sQuery(id+"FHMxAyK4CFUKdhS_1.wireOp",EDGE,"1cb9c079-ea9b-4899-8069-e0e3048e911d.sketch_text.stroke-160"),sQuery(id+"FHMxAyK4CFUKdhS_1.wireOp",EDGE,"1cb9c079-ea9b-4899-8069-e0e3048e911d.sketch_text.stroke-161"),sQuery(id+"FHMxAyK4CFUKdhS_1.wireOp",EDGE,"1cb9c079-ea9b-4899-8069-e0e3048e911d.sketch_text.stroke-162"),sQuery(id+"FHMxAyK4CFUKdhS_1.wireOp",EDGE,"1cb9c079-ea9b-4899-8069-e0e3048e911d.sketch_text.stroke-163"),sQuery(id+"FHMxAyK4CFUKdhS_1.wireOp",EDGE,"1cb9c079-ea9b-4899-8069-e0e3048e911d.sketch_text.stroke-164"),sQuery(id+"FHMxAyK4CFUKdhS_1.wireOp",EDGE,"1cb9c079-ea9b-4899-8069-e0e3048e911d.sketch_text.stroke-165"),sQuery(id+"FHMxAyK4CFUKdhS_1.wireOp",EDGE,"1cb9c079-ea9b-4899-8069-e0e3048e911d.sketch_text.stroke-166"),sQuery(id+"FHMxAyK4CFUKdhS_1.wireOp",EDGE,"1cb9c079-ea9b-4899-8069-e0e3048e911d.sketch_text.stroke-167"),sQuery(id+"FHMxAyK4CFUKdhS_1.wireOp",EDGE,"1cb9c079-ea9b-4899-8069-e0e3048e911d.sketch_text.stroke-168"),sQuery(id+"FHMxAyK4CFUKdhS_1.wireOp",EDGE,"1cb9c079-ea9b-4899-8069-e0e3048e911d.sketch_text.stroke-169"),sQuery(id+"FHMxAyK4CFUKdhS_1.wireOp",EDGE,"1cb9c079-ea9b-4899-8069-e0e3048e911d.sketch_text.stroke-170"),sQuery(id+"FHMxAyK4CFUKdhS_1.wireOp",EDGE,"1cb9c079-ea9b-4899-8069-e0e3048e911d.sketch_text.stroke-171"),sQuery(id+"FHMxAyK4CFUKdhS_1.wireOp",EDGE,"1cb9c079-ea9b-4899-8069-e0e3048e911d.sketch_text.stroke-172"),sQuery(id+"FHMxAyK4CFUKdhS_1.wireOp",EDGE,"1cb9c079-ea9b-4899-8069-e0e3048e911d.sketch_text.stroke-173"),sQuery(id+"FHMxAyK4CFUKdhS_1.wireOp",EDGE,"1cb9c079-ea9b-4899-8069-e0e3048e911d.sketch_text.stroke-174"),sQuery(id+"FHMxAyK4CFUKdhS_1.wireOp",EDGE,"1cb9c079-ea9b-4899-8069-e0e3048e911d.sketch_text.stroke-175"),sQuery(id+"FHMxAyK4CFUKdhS_1.wireOp",EDGE,"1cb9c079-ea9b-4899-8069-e0e3048e911d.sketch_text.stroke-176"),sQuery(id+"FHMxAyK4CFUKdhS_1.wireOp",EDGE,"1cb9c079-ea9b-4899-8069-e0e3048e911d.sketch_text.stroke-177"),sQuery(id+"FHMxAyK4CFUKdhS_1.wireOp",EDGE,"1cb9c079-ea9b-4899-8069-e0e3048e911d.sketch_text.stroke-178"),sQuery(id+"FHMxAyK4CFUKdhS_1.wireOp",EDGE,"1cb9c079-ea9b-4899-8069-e0e3048e911d.sketch_text.stroke-179"),sQuery(id+"FHMxAyK4CFUKdhS_1.wireOp",EDGE,"1cb9c079-ea9b-4899-8069-e0e3048e911d.sketch_text.stroke-180"),sQuery(id+"F3.wireOp",EDGE,"E29"),subQ2])],"isStart":true}),makeQuery(id+"F4.opExtrude","SWEPT_FACE",FACE,{"disambiguationData":[OSD([subQ2])]})]),OD(0.0)],"derivedFrom":makeQuery(id+"F1.opExtrude","CAP_EDGE",EDGE,{"disambiguationData":[OSD([subQ0])],"isStart":false})});}
            var Q27;
            {var subQ0=sQuery(id+"F0.wireOp",EDGE,"E0.top");var subQ1=sQuery(id+"F0.wireOp",EDGE,"E0.bottom");var subQ2=sQuery(id+"F3.wireOp",EDGE,"E30");Q27=makeQuery(id+"F4.boolean.opBoolean","SPLIT",EDGE,{"disambiguationData":[TD([makeQuery(id+"F1.opExtrude","CAP_FACE",FACE,{"disambiguationData":[OSD([subQ1,subQ0,sQuery(id+"F0.wireOp",EDGE,"E0.left"),sQuery(id+"F0.wireOp",EDGE,"E0.right")])],"isStart":false}),makeQuery(id+"F1.opExtrude","SWEPT_FACE",FACE,{"disambiguationData":[OSD([subQ0])]}),makeQuery(id+"F4.opExtrude","CAP_FACE",FACE,{"disambiguationData":[OSD([subQ1,sQuery(id+"F2.wireOp",EDGE,"fcba4419-a2ee-464f-be9d-58f11bf3418b.sketch_text.stroke-0"),sQuery(id+"F2.wireOp",EDGE,"fcba4419-a2ee-464f-be9d-58f11bf3418b.sketch_text.stroke-1"),sQuery(id+"F2.wireOp",EDGE,"fcba4419-a2ee-464f-be9d-58f11bf3418b.sketch_text.stroke-2"),sQuery(id+"F2.wireOp",EDGE,"fcba4419-a2ee-464f-be9d-58f11bf3418b.sketch_text.stroke-3"),sQuery(id+"F2.wireOp",EDGE,"fcba4419-a2ee-464f-be9d-58f11bf3418b.sketch_text.stroke-4"),sQuery(id+"F2.wireOp",EDGE,"fcba4419-a2ee-464f-be9d-58f11bf3418b.sketch_text.stroke-5"),sQuery(id+"F2.wireOp",EDGE,"fcba4419-a2ee-464f-be9d-58f11bf3418b.sketch_text.stroke-6"),sQuery(id+"F2.wireOp",EDGE,"fcba4419-a2ee-464f-be9d-58f11bf3418b.sketch_text.stroke-7"),sQuery(id+"F2.wireOp",EDGE,"fcba4419-a2ee-464f-be9d-58f11bf3418b.sketch_text.stroke-8"),sQuery(id+"F2.wireOp",EDGE,"fcba4419-a2ee-464f-be9d-58f11bf3418b.sketch_text.stroke-9"),sQuery(id+"F2.wireOp",EDGE,"fcba4419-a2ee-464f-be9d-58f11bf3418b.sketch_text.stroke-10"),sQuery(id+"F2.wireOp",EDGE,"fcba4419-a2ee-464f-be9d-58f11bf3418b.sketch_text.stroke-11"),sQuery(id+"F2.wireOp",EDGE,"fcba4419-a2ee-464f-be9d-58f11bf3418b.sketch_text.stroke-12"),sQuery(id+"F2.wireOp",EDGE,"fcba4419-a2ee-464f-be9d-58f11bf3418b.sketch_text.stroke-13"),sQuery(id+"F2.wireOp",EDGE,"fcba4419-a2ee-464f-be9d-58f11bf3418b.sketch_text.stroke-14"),sQuery(id+"F2.wireOp",EDGE,"fcba4419-a2ee-464f-be9d-58f11bf3418b.sketch_text.stroke-15"),sQuery(id+"F2.wireOp",EDGE,"fcba4419-a2ee-464f-be9d-58f11bf3418b.sketch_text.stroke-16"),sQuery(id+"F2.wireOp",EDGE,"fcba4419-a2ee-464f-be9d-58f11bf3418b.sketch_text.stroke-17"),sQuery(id+"F2.wireOp",EDGE,"fcba4419-a2ee-464f-be9d-58f11bf3418b.sketch_text.stroke-18"),sQuery(id+"F2.wireOp",EDGE,"fcba4419-a2ee-464f-be9d-58f11bf3418b.sketch_text.stroke-19"),sQuery(id+"F2.wireOp",EDGE,"fcba4419-a2ee-464f-be9d-58f11bf3418b.sketch_text.stroke-20"),sQuery(id+"F2.wireOp",EDGE,"fcba4419-a2ee-464f-be9d-58f11bf3418b.sketch_text.stroke-21"),sQuery(id+"F2.wireOp",EDGE,"fcba4419-a2ee-464f-be9d-58f11bf3418b.sketch_text.stroke-22"),sQuery(id+"F2.wireOp",EDGE,"fcba4419-a2ee-464f-be9d-58f11bf3418b.sketch_text.stroke-23"),sQuery(id+"F2.wireOp",EDGE,"fcba4419-a2ee-464f-be9d-58f11bf3418b.sketch_text.stroke-24"),sQuery(id+"F2.wireOp",EDGE,"fcba4419-a2ee-464f-be9d-58f11bf3418b.sketch_text.stroke-25"),sQuery(id+"F2.wireOp",EDGE,"fcba4419-a2ee-464f-be9d-58f11bf3418b.sketch_text.stroke-26"),sQuery(id+"F2.wireOp",EDGE,"fcba4419-a2ee-464f-be9d-58f11bf3418b.sketch_text.stroke-27"),sQuery(id+"F2.wireOp",EDGE,"fcba4419-a2ee-464f-be9d-58f11bf3418b.sketch_text.stroke-28"),sQuery(id+"F2.wireOp",EDGE,"fcba4419-a2ee-464f-be9d-58f11bf3418b.sketch_text.stroke-29"),sQuery(id+"F2.wireOp",EDGE,"fcba4419-a2ee-464f-be9d-58f11bf3418b.sketch_text.stroke-30"),sQuery(id+"F2.wireOp",EDGE,"fcba4419-a2ee-464f-be9d-58f11bf3418b.sketch_text.stroke-31"),sQuery(id+"F2.wireOp",EDGE,"fcba4419-a2ee-464f-be9d-58f11bf3418b.sketch_text.stroke-32"),sQuery(id+"F2.wireOp",EDGE,"fcba4419-a2ee-464f-be9d-58f11bf3418b.sketch_text.stroke-33"),sQuery(id+"F2.wireOp",EDGE,"fcba4419-a2ee-464f-be9d-58f11bf3418b.sketch_text.stroke-34"),sQuery(id+"F2.wireOp",EDGE,"fcba4419-a2ee-464f-be9d-58f11bf3418b.sketch_text.stroke-35"),sQuery(id+"F2.wireOp",EDGE,"fcba4419-a2ee-464f-be9d-58f11bf3418b.sketch_text.stroke-36"),sQuery(id+"F2.wireOp",EDGE,"fcba4419-a2ee-464f-be9d-58f11bf3418b.sketch_text.stroke-37"),sQuery(id+"F2.wireOp",EDGE,"fcba4419-a2ee-464f-be9d-58f11bf3418b.sketch_text.stroke-38"),sQuery(id+"F2.wireOp",EDGE,"fcba4419-a2ee-464f-be9d-58f11bf3418b.sketch_text.stroke-39"),sQuery(id+"F2.wireOp",EDGE,"fcba4419-a2ee-464f-be9d-58f11bf3418b.sketch_text.stroke-40"),sQuery(id+"F2.wireOp",EDGE,"fcba4419-a2ee-464f-be9d-58f11bf3418b.sketch_text.stroke-41"),sQuery(id+"F2.wireOp",EDGE,"fcba4419-a2ee-464f-be9d-58f11bf3418b.sketch_text.stroke-42"),sQuery(id+"F2.wireOp",EDGE,"fcba4419-a2ee-464f-be9d-58f11bf3418b.sketch_text.stroke-43"),sQuery(id+"F2.wireOp",EDGE,"fcba4419-a2ee-464f-be9d-58f11bf3418b.sketch_text.stroke-44"),sQuery(id+"F2.wireOp",EDGE,"fcba4419-a2ee-464f-be9d-58f11bf3418b.sketch_text.stroke-45"),sQuery(id+"F2.wireOp",EDGE,"fcba4419-a2ee-464f-be9d-58f11bf3418b.sketch_text.stroke-46"),sQuery(id+"F2.wireOp",EDGE,"fcba4419-a2ee-464f-be9d-58f11bf3418b.sketch_text.stroke-47"),sQuery(id+"F2.wireOp",EDGE,"fcba4419-a2ee-464f-be9d-58f11bf3418b.sketch_text.stroke-48"),sQuery(id+"F2.wireOp",EDGE,"fcba4419-a2ee-464f-be9d-58f11bf3418b.sketch_text.stroke-49"),sQuery(id+"F2.wireOp",EDGE,"fcba4419-a2ee-464f-be9d-58f11bf3418b.sketch_text.stroke-50"),sQuery(id+"F2.wireOp",EDGE,"fcba4419-a2ee-464f-be9d-58f11bf3418b.sketch_text.stroke-51"),sQuery(id+"F2.wireOp",EDGE,"fcba4419-a2ee-464f-be9d-58f11bf3418b.sketch_text.stroke-52"),sQuery(id+"F2.wireOp",EDGE,"fcba4419-a2ee-464f-be9d-58f11bf3418b.sketch_text.stroke-53"),sQuery(id+"F2.wireOp",EDGE,"fcba4419-a2ee-464f-be9d-58f11bf3418b.sketch_text.stroke-54"),sQuery(id+"F2.wireOp",EDGE,"fcba4419-a2ee-464f-be9d-58f11bf3418b.sketch_text.stroke-55"),sQuery(id+"F2.wireOp",EDGE,"fcba4419-a2ee-464f-be9d-58f11bf3418b.sketch_text.stroke-56"),sQuery(id+"F2.wireOp",EDGE,"fcba4419-a2ee-464f-be9d-58f11bf3418b.sketch_text.stroke-57"),sQuery(id+"F2.wireOp",EDGE,"fcba4419-a2ee-464f-be9d-58f11bf3418b.sketch_text.stroke-58"),sQuery(id+"F2.wireOp",EDGE,"fcba4419-a2ee-464f-be9d-58f11bf3418b.sketch_text.stroke-59"),sQuery(id+"F2.wireOp",EDGE,"fcba4419-a2ee-464f-be9d-58f11bf3418b.sketch_text.stroke-60"),sQuery(id+"F2.wireOp",EDGE,"fcba4419-a2ee-464f-be9d-58f11bf3418b.sketch_text.stroke-61"),sQuery(id+"F2.wireOp",EDGE,"fcba4419-a2ee-464f-be9d-58f11bf3418b.sketch_text.stroke-62"),sQuery(id+"F2.wireOp",EDGE,"fcba4419-a2ee-464f-be9d-58f11bf3418b.sketch_text.stroke-63"),sQuery(id+"F2.wireOp",EDGE,"fcba4419-a2ee-464f-be9d-58f11bf3418b.sketch_text.stroke-64"),sQuery(id+"F2.wireOp",EDGE,"fcba4419-a2ee-464f-be9d-58f11bf3418b.sketch_text.stroke-65"),sQuery(id+"F2.wireOp",EDGE,"fcba4419-a2ee-464f-be9d-58f11bf3418b.sketch_text.stroke-66"),sQuery(id+"F2.wireOp",EDGE,"fcba4419-a2ee-464f-be9d-58f11bf3418b.sketch_text.stroke-67"),sQuery(id+"F2.wireOp",EDGE,"fcba4419-a2ee-464f-be9d-58f11bf3418b.sketch_text.stroke-68"),sQuery(id+"F2.wireOp",EDGE,"fcba4419-a2ee-464f-be9d-58f11bf3418b.sketch_text.stroke-69"),sQuery(id+"F2.wireOp",EDGE,"fcba4419-a2ee-464f-be9d-58f11bf3418b.sketch_text.stroke-70"),sQuery(id+"F2.wireOp",EDGE,"fcba4419-a2ee-464f-be9d-58f11bf3418b.sketch_text.stroke-71"),sQuery(id+"F2.wireOp",EDGE,"fcba4419-a2ee-464f-be9d-58f11bf3418b.sketch_text.stroke-72"),sQuery(id+"F2.wireOp",EDGE,"fcba4419-a2ee-464f-be9d-58f11bf3418b.sketch_text.stroke-73"),sQuery(id+"F2.wireOp",EDGE,"fcba4419-a2ee-464f-be9d-58f11bf3418b.sketch_text.stroke-74"),sQuery(id+"F2.wireOp",EDGE,"fcba4419-a2ee-464f-be9d-58f11bf3418b.sketch_text.stroke-75"),sQuery(id+"F2.wireOp",EDGE,"fcba4419-a2ee-464f-be9d-58f11bf3418b.sketch_text.stroke-76"),sQuery(id+"F2.wireOp",EDGE,"fcba4419-a2ee-464f-be9d-58f11bf3418b.sketch_text.stroke-77"),sQuery(id+"F2.wireOp",EDGE,"fcba4419-a2ee-464f-be9d-58f11bf3418b.sketch_text.stroke-78"),sQuery(id+"F2.wireOp",EDGE,"fcba4419-a2ee-464f-be9d-58f11bf3418b.sketch_text.stroke-79"),sQuery(id+"F2.wireOp",EDGE,"fcba4419-a2ee-464f-be9d-58f11bf3418b.sketch_text.stroke-80"),sQuery(id+"F2.wireOp",EDGE,"fcba4419-a2ee-464f-be9d-58f11bf3418b.sketch_text.stroke-81"),sQuery(id+"F2.wireOp",EDGE,"fcba4419-a2ee-464f-be9d-58f11bf3418b.sketch_text.stroke-82"),sQuery(id+"F2.wireOp",EDGE,"fcba4419-a2ee-464f-be9d-58f11bf3418b.sketch_text.stroke-83"),sQuery(id+"F2.wireOp",EDGE,"fcba4419-a2ee-464f-be9d-58f11bf3418b.sketch_text.stroke-84"),sQuery(id+"F2.wireOp",EDGE,"fcba4419-a2ee-464f-be9d-58f11bf3418b.sketch_text.stroke-85"),sQuery(id+"F2.wireOp",EDGE,"fcba4419-a2ee-464f-be9d-58f11bf3418b.sketch_text.stroke-86"),sQuery(id+"F2.wireOp",EDGE,"fcba4419-a2ee-464f-be9d-58f11bf3418b.sketch_text.stroke-87"),sQuery(id+"F2.wireOp",EDGE,"fcba4419-a2ee-464f-be9d-58f11bf3418b.sketch_text.stroke-88"),sQuery(id+"F2.wireOp",EDGE,"fcba4419-a2ee-464f-be9d-58f11bf3418b.sketch_text.stroke-89"),sQuery(id+"F2.wireOp",EDGE,"fcba4419-a2ee-464f-be9d-58f11bf3418b.sketch_text.stroke-90"),sQuery(id+"F2.wireOp",EDGE,"fcba4419-a2ee-464f-be9d-58f11bf3418b.sketch_text.stroke-91"),sQuery(id+"F2.wireOp",EDGE,"fcba4419-a2ee-464f-be9d-58f11bf3418b.sketch_text.stroke-92"),sQuery(id+"F2.wireOp",EDGE,"fcba4419-a2ee-464f-be9d-58f11bf3418b.sketch_text.stroke-93"),sQuery(id+"F2.wireOp",EDGE,"fcba4419-a2ee-464f-be9d-58f11bf3418b.sketch_text.stroke-94"),sQuery(id+"F2.wireOp",EDGE,"fcba4419-a2ee-464f-be9d-58f11bf3418b.sketch_text.stroke-95"),sQuery(id+"F2.wireOp",EDGE,"fcba4419-a2ee-464f-be9d-58f11bf3418b.sketch_text.stroke-96"),sQuery(id+"F2.wireOp",EDGE,"fcba4419-a2ee-464f-be9d-58f11bf3418b.sketch_text.stroke-97"),sQuery(id+"F2.wireOp",EDGE,"fcba4419-a2ee-464f-be9d-58f11bf3418b.sketch_text.stroke-98"),sQuery(id+"F2.wireOp",EDGE,"fcba4419-a2ee-464f-be9d-58f11bf3418b.sketch_text.stroke-99"),sQuery(id+"F2.wireOp",EDGE,"fcba4419-a2ee-464f-be9d-58f11bf3418b.sketch_text.stroke-100"),sQuery(id+"F2.wireOp",EDGE,"fcba4419-a2ee-464f-be9d-58f11bf3418b.sketch_text.stroke-101"),sQuery(id+"F2.wireOp",EDGE,"fcba4419-a2ee-464f-be9d-58f11bf3418b.sketch_text.stroke-102"),sQuery(id+"F2.wireOp",EDGE,"fcba4419-a2ee-464f-be9d-58f11bf3418b.sketch_text.stroke-103"),sQuery(id+"F2.wireOp",EDGE,"fcba4419-a2ee-464f-be9d-58f11bf3418b.sketch_text.stroke-104"),sQuery(id+"F2.wireOp",EDGE,"fcba4419-a2ee-464f-be9d-58f11bf3418b.sketch_text.stroke-105"),sQuery(id+"F2.wireOp",EDGE,"fcba4419-a2ee-464f-be9d-58f11bf3418b.sketch_text.stroke-106"),sQuery(id+"F2.wireOp",EDGE,"fcba4419-a2ee-464f-be9d-58f11bf3418b.sketch_text.stroke-107"),sQuery(id+"F2.wireOp",EDGE,"fcba4419-a2ee-464f-be9d-58f11bf3418b.sketch_text.stroke-108"),sQuery(id+"F2.wireOp",EDGE,"fcba4419-a2ee-464f-be9d-58f11bf3418b.sketch_text.stroke-109"),sQuery(id+"F2.wireOp",EDGE,"fcba4419-a2ee-464f-be9d-58f11bf3418b.sketch_text.stroke-110"),sQuery(id+"F2.wireOp",EDGE,"fcba4419-a2ee-464f-be9d-58f11bf3418b.sketch_text.stroke-111"),sQuery(id+"F2.wireOp",EDGE,"fcba4419-a2ee-464f-be9d-58f11bf3418b.sketch_text.stroke-112"),sQuery(id+"F2.wireOp",EDGE,"fcba4419-a2ee-464f-be9d-58f11bf3418b.sketch_text.stroke-113"),sQuery(id+"F2.wireOp",EDGE,"fcba4419-a2ee-464f-be9d-58f11bf3418b.sketch_text.stroke-114"),sQuery(id+"F2.wireOp",EDGE,"fcba4419-a2ee-464f-be9d-58f11bf3418b.sketch_text.stroke-115"),sQuery(id+"F2.wireOp",EDGE,"fcba4419-a2ee-464f-be9d-58f11bf3418b.sketch_text.stroke-116"),sQuery(id+"F2.wireOp",EDGE,"fcba4419-a2ee-464f-be9d-58f11bf3418b.sketch_text.stroke-117"),sQuery(id+"F2.wireOp",EDGE,"fcba4419-a2ee-464f-be9d-58f11bf3418b.sketch_text.stroke-118"),sQuery(id+"F2.wireOp",EDGE,"fcba4419-a2ee-464f-be9d-58f11bf3418b.sketch_text.stroke-119"),sQuery(id+"F2.wireOp",EDGE,"fcba4419-a2ee-464f-be9d-58f11bf3418b.sketch_text.stroke-120"),sQuery(id+"F2.wireOp",EDGE,"fcba4419-a2ee-464f-be9d-58f11bf3418b.sketch_text.stroke-121"),sQuery(id+"F2.wireOp",EDGE,"fcba4419-a2ee-464f-be9d-58f11bf3418b.sketch_text.stroke-122"),sQuery(id+"F2.wireOp",EDGE,"fcba4419-a2ee-464f-be9d-58f11bf3418b.sketch_text.stroke-123"),sQuery(id+"F2.wireOp",EDGE,"fcba4419-a2ee-464f-be9d-58f11bf3418b.sketch_text.stroke-124"),sQuery(id+"F2.wireOp",EDGE,"fcba4419-a2ee-464f-be9d-58f11bf3418b.sketch_text.stroke-125"),sQuery(id+"F2.wireOp",EDGE,"fcba4419-a2ee-464f-be9d-58f11bf3418b.sketch_text.stroke-126"),sQuery(id+"F2.wireOp",EDGE,"fcba4419-a2ee-464f-be9d-58f11bf3418b.sketch_text.stroke-127"),sQuery(id+"F2.wireOp",EDGE,"fcba4419-a2ee-464f-be9d-58f11bf3418b.sketch_text.stroke-128"),sQuery(id+"F2.wireOp",EDGE,"fcba4419-a2ee-464f-be9d-58f11bf3418b.sketch_text.stroke-129"),sQuery(id+"F2.wireOp",EDGE,"fcba4419-a2ee-464f-be9d-58f11bf3418b.sketch_text.stroke-130"),sQuery(id+"F2.wireOp",EDGE,"fcba4419-a2ee-464f-be9d-58f11bf3418b.sketch_text.stroke-131"),sQuery(id+"F2.wireOp",EDGE,"fcba4419-a2ee-464f-be9d-58f11bf3418b.sketch_text.stroke-132"),sQuery(id+"F2.wireOp",EDGE,"fcba4419-a2ee-464f-be9d-58f11bf3418b.sketch_text.stroke-133"),sQuery(id+"F2.wireOp",EDGE,"fcba4419-a2ee-464f-be9d-58f11bf3418b.sketch_text.stroke-134"),sQuery(id+"F2.wireOp",EDGE,"fcba4419-a2ee-464f-be9d-58f11bf3418b.sketch_text.stroke-135"),sQuery(id+"F2.wireOp",EDGE,"fcba4419-a2ee-464f-be9d-58f11bf3418b.sketch_text.stroke-136"),sQuery(id+"F2.wireOp",EDGE,"fcba4419-a2ee-464f-be9d-58f11bf3418b.sketch_text.stroke-137"),sQuery(id+"F2.wireOp",EDGE,"fcba4419-a2ee-464f-be9d-58f11bf3418b.sketch_text.stroke-138"),sQuery(id+"F2.wireOp",EDGE,"fcba4419-a2ee-464f-be9d-58f11bf3418b.sketch_text.stroke-139"),sQuery(id+"F2.wireOp",EDGE,"fcba4419-a2ee-464f-be9d-58f11bf3418b.sketch_text.stroke-140"),sQuery(id+"F2.wireOp",EDGE,"fcba4419-a2ee-464f-be9d-58f11bf3418b.sketch_text.stroke-141"),sQuery(id+"F2.wireOp",EDGE,"fcba4419-a2ee-464f-be9d-58f11bf3418b.sketch_text.stroke-142"),sQuery(id+"F2.wireOp",EDGE,"fcba4419-a2ee-464f-be9d-58f11bf3418b.sketch_text.stroke-143"),sQuery(id+"F2.wireOp",EDGE,"fcba4419-a2ee-464f-be9d-58f11bf3418b.sketch_text.stroke-144"),sQuery(id+"F2.wireOp",EDGE,"fcba4419-a2ee-464f-be9d-58f11bf3418b.sketch_text.stroke-145"),sQuery(id+"F2.wireOp",EDGE,"fcba4419-a2ee-464f-be9d-58f11bf3418b.sketch_text.stroke-146"),sQuery(id+"F2.wireOp",EDGE,"fcba4419-a2ee-464f-be9d-58f11bf3418b.sketch_text.stroke-147"),sQuery(id+"F2.wireOp",EDGE,"fcba4419-a2ee-464f-be9d-58f11bf3418b.sketch_text.stroke-148"),sQuery(id+"F2.wireOp",EDGE,"fcba4419-a2ee-464f-be9d-58f11bf3418b.sketch_text.stroke-149"),sQuery(id+"F2.wireOp",EDGE,"fcba4419-a2ee-464f-be9d-58f11bf3418b.sketch_text.stroke-150"),sQuery(id+"F2.wireOp",EDGE,"fcba4419-a2ee-464f-be9d-58f11bf3418b.sketch_text.stroke-151"),sQuery(id+"F2.wireOp",EDGE,"fcba4419-a2ee-464f-be9d-58f11bf3418b.sketch_text.stroke-152"),sQuery(id+"F2.wireOp",EDGE,"fcba4419-a2ee-464f-be9d-58f11bf3418b.sketch_text.stroke-153"),sQuery(id+"F2.wireOp",EDGE,"fcba4419-a2ee-464f-be9d-58f11bf3418b.sketch_text.stroke-154"),sQuery(id+"F2.wireOp",EDGE,"fcba4419-a2ee-464f-be9d-58f11bf3418b.sketch_text.stroke-155"),sQuery(id+"F2.wireOp",EDGE,"fcba4419-a2ee-464f-be9d-58f11bf3418b.sketch_text.stroke-156"),sQuery(id+"F2.wireOp",EDGE,"fcba4419-a2ee-464f-be9d-58f11bf3418b.sketch_text.stroke-157"),sQuery(id+"F2.wireOp",EDGE,"fcba4419-a2ee-464f-be9d-58f11bf3418b.sketch_text.stroke-158"),sQuery(id+"F2.wireOp",EDGE,"fcba4419-a2ee-464f-be9d-58f11bf3418b.sketch_text.stroke-159"),sQuery(id+"F2.wireOp",EDGE,"fcba4419-a2ee-464f-be9d-58f11bf3418b.sketch_text.stroke-160"),sQuery(id+"F2.wireOp",EDGE,"fcba4419-a2ee-464f-be9d-58f11bf3418b.sketch_text.stroke-161"),sQuery(id+"F2.wireOp",EDGE,"fcba4419-a2ee-464f-be9d-58f11bf3418b.sketch_text.stroke-162"),sQuery(id+"F2.wireOp",EDGE,"fcba4419-a2ee-464f-be9d-58f11bf3418b.sketch_text.stroke-163"),sQuery(id+"F2.wireOp",EDGE,"fcba4419-a2ee-464f-be9d-58f11bf3418b.sketch_text.stroke-164"),sQuery(id+"F2.wireOp",EDGE,"fcba4419-a2ee-464f-be9d-58f11bf3418b.sketch_text.stroke-165"),sQuery(id+"F2.wireOp",EDGE,"fcba4419-a2ee-464f-be9d-58f11bf3418b.sketch_text.stroke-166"),sQuery(id+"F2.wireOp",EDGE,"fcba4419-a2ee-464f-be9d-58f11bf3418b.sketch_text.stroke-167"),sQuery(id+"F2.wireOp",EDGE,"fcba4419-a2ee-464f-be9d-58f11bf3418b.sketch_text.stroke-168"),sQuery(id+"F2.wireOp",EDGE,"fcba4419-a2ee-464f-be9d-58f11bf3418b.sketch_text.stroke-169"),sQuery(id+"F2.wireOp",EDGE,"fcba4419-a2ee-464f-be9d-58f11bf3418b.sketch_text.stroke-170"),sQuery(id+"F2.wireOp",EDGE,"fcba4419-a2ee-464f-be9d-58f11bf3418b.sketch_text.stroke-171"),sQuery(id+"F2.wireOp",EDGE,"fcba4419-a2ee-464f-be9d-58f11bf3418b.sketch_text.stroke-172"),sQuery(id+"F2.wireOp",EDGE,"fcba4419-a2ee-464f-be9d-58f11bf3418b.sketch_text.stroke-173"),sQuery(id+"FHMxAyK4CFUKdhS_1.wireOp",EDGE,"1cb9c079-ea9b-4899-8069-e0e3048e911d.sketch_text.stroke-0"),sQuery(id+"FHMxAyK4CFUKdhS_1.wireOp",EDGE,"1cb9c079-ea9b-4899-8069-e0e3048e911d.sketch_text.stroke-1"),sQuery(id+"FHMxAyK4CFUKdhS_1.wireOp",EDGE,"1cb9c079-ea9b-4899-8069-e0e3048e911d.sketch_text.stroke-2"),sQuery(id+"FHMxAyK4CFUKdhS_1.wireOp",EDGE,"1cb9c079-ea9b-4899-8069-e0e3048e911d.sketch_text.stroke-3"),sQuery(id+"FHMxAyK4CFUKdhS_1.wireOp",EDGE,"1cb9c079-ea9b-4899-8069-e0e3048e911d.sketch_text.stroke-4"),sQuery(id+"FHMxAyK4CFUKdhS_1.wireOp",EDGE,"1cb9c079-ea9b-4899-8069-e0e3048e911d.sketch_text.stroke-5"),sQuery(id+"FHMxAyK4CFUKdhS_1.wireOp",EDGE,"1cb9c079-ea9b-4899-8069-e0e3048e911d.sketch_text.stroke-6"),sQuery(id+"FHMxAyK4CFUKdhS_1.wireOp",EDGE,"1cb9c079-ea9b-4899-8069-e0e3048e911d.sketch_text.stroke-7"),sQuery(id+"FHMxAyK4CFUKdhS_1.wireOp",EDGE,"1cb9c079-ea9b-4899-8069-e0e3048e911d.sketch_text.stroke-8"),sQuery(id+"FHMxAyK4CFUKdhS_1.wireOp",EDGE,"1cb9c079-ea9b-4899-8069-e0e3048e911d.sketch_text.stroke-9"),sQuery(id+"FHMxAyK4CFUKdhS_1.wireOp",EDGE,"1cb9c079-ea9b-4899-8069-e0e3048e911d.sketch_text.stroke-10"),sQuery(id+"FHMxAyK4CFUKdhS_1.wireOp",EDGE,"1cb9c079-ea9b-4899-8069-e0e3048e911d.sketch_text.stroke-11"),sQuery(id+"FHMxAyK4CFUKdhS_1.wireOp",EDGE,"1cb9c079-ea9b-4899-8069-e0e3048e911d.sketch_text.stroke-12"),sQuery(id+"FHMxAyK4CFUKdhS_1.wireOp",EDGE,"1cb9c079-ea9b-4899-8069-e0e3048e911d.sketch_text.stroke-13"),sQuery(id+"FHMxAyK4CFUKdhS_1.wireOp",EDGE,"1cb9c079-ea9b-4899-8069-e0e3048e911d.sketch_text.stroke-14"),sQuery(id+"FHMxAyK4CFUKdhS_1.wireOp",EDGE,"1cb9c079-ea9b-4899-8069-e0e3048e911d.sketch_text.stroke-15"),sQuery(id+"FHMxAyK4CFUKdhS_1.wireOp",EDGE,"1cb9c079-ea9b-4899-8069-e0e3048e911d.sketch_text.stroke-16"),sQuery(id+"FHMxAyK4CFUKdhS_1.wireOp",EDGE,"1cb9c079-ea9b-4899-8069-e0e3048e911d.sketch_text.stroke-17"),sQuery(id+"FHMxAyK4CFUKdhS_1.wireOp",EDGE,"1cb9c079-ea9b-4899-8069-e0e3048e911d.sketch_text.stroke-18"),sQuery(id+"FHMxAyK4CFUKdhS_1.wireOp",EDGE,"1cb9c079-ea9b-4899-8069-e0e3048e911d.sketch_text.stroke-19"),sQuery(id+"FHMxAyK4CFUKdhS_1.wireOp",EDGE,"1cb9c079-ea9b-4899-8069-e0e3048e911d.sketch_text.stroke-20"),sQuery(id+"FHMxAyK4CFUKdhS_1.wireOp",EDGE,"1cb9c079-ea9b-4899-8069-e0e3048e911d.sketch_text.stroke-21"),sQuery(id+"FHMxAyK4CFUKdhS_1.wireOp",EDGE,"1cb9c079-ea9b-4899-8069-e0e3048e911d.sketch_text.stroke-22"),sQuery(id+"FHMxAyK4CFUKdhS_1.wireOp",EDGE,"1cb9c079-ea9b-4899-8069-e0e3048e911d.sketch_text.stroke-23"),sQuery(id+"FHMxAyK4CFUKdhS_1.wireOp",EDGE,"1cb9c079-ea9b-4899-8069-e0e3048e911d.sketch_text.stroke-24"),sQuery(id+"FHMxAyK4CFUKdhS_1.wireOp",EDGE,"1cb9c079-ea9b-4899-8069-e0e3048e911d.sketch_text.stroke-25"),sQuery(id+"FHMxAyK4CFUKdhS_1.wireOp",EDGE,"1cb9c079-ea9b-4899-8069-e0e3048e911d.sketch_text.stroke-26"),sQuery(id+"FHMxAyK4CFUKdhS_1.wireOp",EDGE,"1cb9c079-ea9b-4899-8069-e0e3048e911d.sketch_text.stroke-27"),sQuery(id+"FHMxAyK4CFUKdhS_1.wireOp",EDGE,"1cb9c079-ea9b-4899-8069-e0e3048e911d.sketch_text.stroke-28"),sQuery(id+"FHMxAyK4CFUKdhS_1.wireOp",EDGE,"1cb9c079-ea9b-4899-8069-e0e3048e911d.sketch_text.stroke-29"),sQuery(id+"FHMxAyK4CFUKdhS_1.wireOp",EDGE,"1cb9c079-ea9b-4899-8069-e0e3048e911d.sketch_text.stroke-30"),sQuery(id+"FHMxAyK4CFUKdhS_1.wireOp",EDGE,"1cb9c079-ea9b-4899-8069-e0e3048e911d.sketch_text.stroke-31"),sQuery(id+"FHMxAyK4CFUKdhS_1.wireOp",EDGE,"1cb9c079-ea9b-4899-8069-e0e3048e911d.sketch_text.stroke-32"),sQuery(id+"FHMxAyK4CFUKdhS_1.wireOp",EDGE,"1cb9c079-ea9b-4899-8069-e0e3048e911d.sketch_text.stroke-33"),sQuery(id+"FHMxAyK4CFUKdhS_1.wireOp",EDGE,"1cb9c079-ea9b-4899-8069-e0e3048e911d.sketch_text.stroke-34"),sQuery(id+"FHMxAyK4CFUKdhS_1.wireOp",EDGE,"1cb9c079-ea9b-4899-8069-e0e3048e911d.sketch_text.stroke-35"),sQuery(id+"FHMxAyK4CFUKdhS_1.wireOp",EDGE,"1cb9c079-ea9b-4899-8069-e0e3048e911d.sketch_text.stroke-36"),sQuery(id+"FHMxAyK4CFUKdhS_1.wireOp",EDGE,"1cb9c079-ea9b-4899-8069-e0e3048e911d.sketch_text.stroke-37"),sQuery(id+"FHMxAyK4CFUKdhS_1.wireOp",EDGE,"1cb9c079-ea9b-4899-8069-e0e3048e911d.sketch_text.stroke-38"),sQuery(id+"FHMxAyK4CFUKdhS_1.wireOp",EDGE,"1cb9c079-ea9b-4899-8069-e0e3048e911d.sketch_text.stroke-39"),sQuery(id+"FHMxAyK4CFUKdhS_1.wireOp",EDGE,"1cb9c079-ea9b-4899-8069-e0e3048e911d.sketch_text.stroke-40"),sQuery(id+"FHMxAyK4CFUKdhS_1.wireOp",EDGE,"1cb9c079-ea9b-4899-8069-e0e3048e911d.sketch_text.stroke-41"),sQuery(id+"FHMxAyK4CFUKdhS_1.wireOp",EDGE,"1cb9c079-ea9b-4899-8069-e0e3048e911d.sketch_text.stroke-42"),sQuery(id+"FHMxAyK4CFUKdhS_1.wireOp",EDGE,"1cb9c079-ea9b-4899-8069-e0e3048e911d.sketch_text.stroke-43"),sQuery(id+"FHMxAyK4CFUKdhS_1.wireOp",EDGE,"1cb9c079-ea9b-4899-8069-e0e3048e911d.sketch_text.stroke-44"),sQuery(id+"FHMxAyK4CFUKdhS_1.wireOp",EDGE,"1cb9c079-ea9b-4899-8069-e0e3048e911d.sketch_text.stroke-45"),sQuery(id+"FHMxAyK4CFUKdhS_1.wireOp",EDGE,"1cb9c079-ea9b-4899-8069-e0e3048e911d.sketch_text.stroke-46"),sQuery(id+"FHMxAyK4CFUKdhS_1.wireOp",EDGE,"1cb9c079-ea9b-4899-8069-e0e3048e911d.sketch_text.stroke-47"),sQuery(id+"FHMxAyK4CFUKdhS_1.wireOp",EDGE,"1cb9c079-ea9b-4899-8069-e0e3048e911d.sketch_text.stroke-48"),sQuery(id+"FHMxAyK4CFUKdhS_1.wireOp",EDGE,"1cb9c079-ea9b-4899-8069-e0e3048e911d.sketch_text.stroke-49"),sQuery(id+"FHMxAyK4CFUKdhS_1.wireOp",EDGE,"1cb9c079-ea9b-4899-8069-e0e3048e911d.sketch_text.stroke-50"),sQuery(id+"FHMxAyK4CFUKdhS_1.wireOp",EDGE,"1cb9c079-ea9b-4899-8069-e0e3048e911d.sketch_text.stroke-51"),sQuery(id+"FHMxAyK4CFUKdhS_1.wireOp",EDGE,"1cb9c079-ea9b-4899-8069-e0e3048e911d.sketch_text.stroke-52"),sQuery(id+"FHMxAyK4CFUKdhS_1.wireOp",EDGE,"1cb9c079-ea9b-4899-8069-e0e3048e911d.sketch_text.stroke-53"),sQuery(id+"FHMxAyK4CFUKdhS_1.wireOp",EDGE,"1cb9c079-ea9b-4899-8069-e0e3048e911d.sketch_text.stroke-54"),sQuery(id+"FHMxAyK4CFUKdhS_1.wireOp",EDGE,"1cb9c079-ea9b-4899-8069-e0e3048e911d.sketch_text.stroke-55"),sQuery(id+"FHMxAyK4CFUKdhS_1.wireOp",EDGE,"1cb9c079-ea9b-4899-8069-e0e3048e911d.sketch_text.stroke-56"),sQuery(id+"FHMxAyK4CFUKdhS_1.wireOp",EDGE,"1cb9c079-ea9b-4899-8069-e0e3048e911d.sketch_text.stroke-57"),sQuery(id+"FHMxAyK4CFUKdhS_1.wireOp",EDGE,"1cb9c079-ea9b-4899-8069-e0e3048e911d.sketch_text.stroke-58"),sQuery(id+"FHMxAyK4CFUKdhS_1.wireOp",EDGE,"1cb9c079-ea9b-4899-8069-e0e3048e911d.sketch_text.stroke-59"),sQuery(id+"FHMxAyK4CFUKdhS_1.wireOp",EDGE,"1cb9c079-ea9b-4899-8069-e0e3048e911d.sketch_text.stroke-60"),sQuery(id+"FHMxAyK4CFUKdhS_1.wireOp",EDGE,"1cb9c079-ea9b-4899-8069-e0e3048e911d.sketch_text.stroke-61"),sQuery(id+"FHMxAyK4CFUKdhS_1.wireOp",EDGE,"1cb9c079-ea9b-4899-8069-e0e3048e911d.sketch_text.stroke-62"),sQuery(id+"FHMxAyK4CFUKdhS_1.wireOp",EDGE,"1cb9c079-ea9b-4899-8069-e0e3048e911d.sketch_text.stroke-71"),sQuery(id+"FHMxAyK4CFUKdhS_1.wireOp",EDGE,"1cb9c079-ea9b-4899-8069-e0e3048e911d.sketch_text.stroke-72"),sQuery(id+"FHMxAyK4CFUKdhS_1.wireOp",EDGE,"1cb9c079-ea9b-4899-8069-e0e3048e911d.sketch_text.stroke-73"),sQuery(id+"FHMxAyK4CFUKdhS_1.wireOp",EDGE,"1cb9c079-ea9b-4899-8069-e0e3048e911d.sketch_text.stroke-74"),sQuery(id+"FHMxAyK4CFUKdhS_1.wireOp",EDGE,"1cb9c079-ea9b-4899-8069-e0e3048e911d.sketch_text.stroke-75"),sQuery(id+"FHMxAyK4CFUKdhS_1.wireOp",EDGE,"1cb9c079-ea9b-4899-8069-e0e3048e911d.sketch_text.stroke-76"),sQuery(id+"FHMxAyK4CFUKdhS_1.wireOp",EDGE,"1cb9c079-ea9b-4899-8069-e0e3048e911d.sketch_text.stroke-77"),sQuery(id+"FHMxAyK4CFUKdhS_1.wireOp",EDGE,"1cb9c079-ea9b-4899-8069-e0e3048e911d.sketch_text.stroke-78"),sQuery(id+"FHMxAyK4CFUKdhS_1.wireOp",EDGE,"1cb9c079-ea9b-4899-8069-e0e3048e911d.sketch_text.stroke-79"),sQuery(id+"FHMxAyK4CFUKdhS_1.wireOp",EDGE,"1cb9c079-ea9b-4899-8069-e0e3048e911d.sketch_text.stroke-80"),sQuery(id+"FHMxAyK4CFUKdhS_1.wireOp",EDGE,"1cb9c079-ea9b-4899-8069-e0e3048e911d.sketch_text.stroke-81"),sQuery(id+"FHMxAyK4CFUKdhS_1.wireOp",EDGE,"1cb9c079-ea9b-4899-8069-e0e3048e911d.sketch_text.stroke-82"),sQuery(id+"FHMxAyK4CFUKdhS_1.wireOp",EDGE,"1cb9c079-ea9b-4899-8069-e0e3048e911d.sketch_text.stroke-83"),sQuery(id+"FHMxAyK4CFUKdhS_1.wireOp",EDGE,"1cb9c079-ea9b-4899-8069-e0e3048e911d.sketch_text.stroke-84"),sQuery(id+"FHMxAyK4CFUKdhS_1.wireOp",EDGE,"1cb9c079-ea9b-4899-8069-e0e3048e911d.sketch_text.stroke-85"),sQuery(id+"FHMxAyK4CFUKdhS_1.wireOp",EDGE,"1cb9c079-ea9b-4899-8069-e0e3048e911d.sketch_text.stroke-86"),sQuery(id+"FHMxAyK4CFUKdhS_1.wireOp",EDGE,"1cb9c079-ea9b-4899-8069-e0e3048e911d.sketch_text.stroke-87"),sQuery(id+"FHMxAyK4CFUKdhS_1.wireOp",EDGE,"1cb9c079-ea9b-4899-8069-e0e3048e911d.sketch_text.stroke-88"),sQuery(id+"FHMxAyK4CFUKdhS_1.wireOp",EDGE,"1cb9c079-ea9b-4899-8069-e0e3048e911d.sketch_text.stroke-89"),sQuery(id+"FHMxAyK4CFUKdhS_1.wireOp",EDGE,"1cb9c079-ea9b-4899-8069-e0e3048e911d.sketch_text.stroke-90"),sQuery(id+"FHMxAyK4CFUKdhS_1.wireOp",EDGE,"1cb9c079-ea9b-4899-8069-e0e3048e911d.sketch_text.stroke-91"),sQuery(id+"FHMxAyK4CFUKdhS_1.wireOp",EDGE,"1cb9c079-ea9b-4899-8069-e0e3048e911d.sketch_text.stroke-92"),sQuery(id+"FHMxAyK4CFUKdhS_1.wireOp",EDGE,"1cb9c079-ea9b-4899-8069-e0e3048e911d.sketch_text.stroke-93"),sQuery(id+"FHMxAyK4CFUKdhS_1.wireOp",EDGE,"1cb9c079-ea9b-4899-8069-e0e3048e911d.sketch_text.stroke-94"),sQuery(id+"FHMxAyK4CFUKdhS_1.wireOp",EDGE,"1cb9c079-ea9b-4899-8069-e0e3048e911d.sketch_text.stroke-95"),sQuery(id+"FHMxAyK4CFUKdhS_1.wireOp",EDGE,"1cb9c079-ea9b-4899-8069-e0e3048e911d.sketch_text.stroke-96"),sQuery(id+"FHMxAyK4CFUKdhS_1.wireOp",EDGE,"1cb9c079-ea9b-4899-8069-e0e3048e911d.sketch_text.stroke-97"),sQuery(id+"FHMxAyK4CFUKdhS_1.wireOp",EDGE,"1cb9c079-ea9b-4899-8069-e0e3048e911d.sketch_text.stroke-103"),sQuery(id+"FHMxAyK4CFUKdhS_1.wireOp",EDGE,"1cb9c079-ea9b-4899-8069-e0e3048e911d.sketch_text.stroke-104"),sQuery(id+"FHMxAyK4CFUKdhS_1.wireOp",EDGE,"1cb9c079-ea9b-4899-8069-e0e3048e911d.sketch_text.stroke-105"),sQuery(id+"FHMxAyK4CFUKdhS_1.wireOp",EDGE,"1cb9c079-ea9b-4899-8069-e0e3048e911d.sketch_text.stroke-106"),sQuery(id+"FHMxAyK4CFUKdhS_1.wireOp",EDGE,"1cb9c079-ea9b-4899-8069-e0e3048e911d.sketch_text.stroke-107"),sQuery(id+"FHMxAyK4CFUKdhS_1.wireOp",EDGE,"1cb9c079-ea9b-4899-8069-e0e3048e911d.sketch_text.stroke-108"),sQuery(id+"FHMxAyK4CFUKdhS_1.wireOp",EDGE,"1cb9c079-ea9b-4899-8069-e0e3048e911d.sketch_text.stroke-109"),sQuery(id+"FHMxAyK4CFUKdhS_1.wireOp",EDGE,"1cb9c079-ea9b-4899-8069-e0e3048e911d.sketch_text.stroke-110"),sQuery(id+"FHMxAyK4CFUKdhS_1.wireOp",EDGE,"1cb9c079-ea9b-4899-8069-e0e3048e911d.sketch_text.stroke-111"),sQuery(id+"FHMxAyK4CFUKdhS_1.wireOp",EDGE,"1cb9c079-ea9b-4899-8069-e0e3048e911d.sketch_text.stroke-112"),sQuery(id+"FHMxAyK4CFUKdhS_1.wireOp",EDGE,"1cb9c079-ea9b-4899-8069-e0e3048e911d.sketch_text.stroke-113"),sQuery(id+"FHMxAyK4CFUKdhS_1.wireOp",EDGE,"1cb9c079-ea9b-4899-8069-e0e3048e911d.sketch_text.stroke-114"),sQuery(id+"FHMxAyK4CFUKdhS_1.wireOp",EDGE,"1cb9c079-ea9b-4899-8069-e0e3048e911d.sketch_text.stroke-115"),sQuery(id+"FHMxAyK4CFUKdhS_1.wireOp",EDGE,"1cb9c079-ea9b-4899-8069-e0e3048e911d.sketch_text.stroke-116"),sQuery(id+"FHMxAyK4CFUKdhS_1.wireOp",EDGE,"1cb9c079-ea9b-4899-8069-e0e3048e911d.sketch_text.stroke-117"),sQuery(id+"FHMxAyK4CFUKdhS_1.wireOp",EDGE,"1cb9c079-ea9b-4899-8069-e0e3048e911d.sketch_text.stroke-118"),sQuery(id+"FHMxAyK4CFUKdhS_1.wireOp",EDGE,"1cb9c079-ea9b-4899-8069-e0e3048e911d.sketch_text.stroke-119"),sQuery(id+"FHMxAyK4CFUKdhS_1.wireOp",EDGE,"1cb9c079-ea9b-4899-8069-e0e3048e911d.sketch_text.stroke-120"),sQuery(id+"FHMxAyK4CFUKdhS_1.wireOp",EDGE,"1cb9c079-ea9b-4899-8069-e0e3048e911d.sketch_text.stroke-121"),sQuery(id+"FHMxAyK4CFUKdhS_1.wireOp",EDGE,"1cb9c079-ea9b-4899-8069-e0e3048e911d.sketch_text.stroke-122"),sQuery(id+"FHMxAyK4CFUKdhS_1.wireOp",EDGE,"1cb9c079-ea9b-4899-8069-e0e3048e911d.sketch_text.stroke-123"),sQuery(id+"FHMxAyK4CFUKdhS_1.wireOp",EDGE,"1cb9c079-ea9b-4899-8069-e0e3048e911d.sketch_text.stroke-124"),sQuery(id+"FHMxAyK4CFUKdhS_1.wireOp",EDGE,"1cb9c079-ea9b-4899-8069-e0e3048e911d.sketch_text.stroke-125"),sQuery(id+"FHMxAyK4CFUKdhS_1.wireOp",EDGE,"1cb9c079-ea9b-4899-8069-e0e3048e911d.sketch_text.stroke-126"),sQuery(id+"FHMxAyK4CFUKdhS_1.wireOp",EDGE,"1cb9c079-ea9b-4899-8069-e0e3048e911d.sketch_text.stroke-127"),sQuery(id+"FHMxAyK4CFUKdhS_1.wireOp",EDGE,"1cb9c079-ea9b-4899-8069-e0e3048e911d.sketch_text.stroke-128"),sQuery(id+"FHMxAyK4CFUKdhS_1.wireOp",EDGE,"1cb9c079-ea9b-4899-8069-e0e3048e911d.sketch_text.stroke-129"),sQuery(id+"FHMxAyK4CFUKdhS_1.wireOp",EDGE,"1cb9c079-ea9b-4899-8069-e0e3048e911d.sketch_text.stroke-130"),sQuery(id+"FHMxAyK4CFUKdhS_1.wireOp",EDGE,"1cb9c079-ea9b-4899-8069-e0e3048e911d.sketch_text.stroke-131"),sQuery(id+"FHMxAyK4CFUKdhS_1.wireOp",EDGE,"1cb9c079-ea9b-4899-8069-e0e3048e911d.sketch_text.stroke-132"),sQuery(id+"FHMxAyK4CFUKdhS_1.wireOp",EDGE,"1cb9c079-ea9b-4899-8069-e0e3048e911d.sketch_text.stroke-133"),sQuery(id+"FHMxAyK4CFUKdhS_1.wireOp",EDGE,"1cb9c079-ea9b-4899-8069-e0e3048e911d.sketch_text.stroke-134"),sQuery(id+"FHMxAyK4CFUKdhS_1.wireOp",EDGE,"1cb9c079-ea9b-4899-8069-e0e3048e911d.sketch_text.stroke-135"),sQuery(id+"FHMxAyK4CFUKdhS_1.wireOp",EDGE,"1cb9c079-ea9b-4899-8069-e0e3048e911d.sketch_text.stroke-136"),sQuery(id+"FHMxAyK4CFUKdhS_1.wireOp",EDGE,"1cb9c079-ea9b-4899-8069-e0e3048e911d.sketch_text.stroke-137"),sQuery(id+"FHMxAyK4CFUKdhS_1.wireOp",EDGE,"1cb9c079-ea9b-4899-8069-e0e3048e911d.sketch_text.stroke-138"),sQuery(id+"FHMxAyK4CFUKdhS_1.wireOp",EDGE,"1cb9c079-ea9b-4899-8069-e0e3048e911d.sketch_text.stroke-139"),sQuery(id+"FHMxAyK4CFUKdhS_1.wireOp",EDGE,"1cb9c079-ea9b-4899-8069-e0e3048e911d.sketch_text.stroke-140"),sQuery(id+"FHMxAyK4CFUKdhS_1.wireOp",EDGE,"1cb9c079-ea9b-4899-8069-e0e3048e911d.sketch_text.stroke-141"),sQuery(id+"FHMxAyK4CFUKdhS_1.wireOp",EDGE,"1cb9c079-ea9b-4899-8069-e0e3048e911d.sketch_text.stroke-142"),sQuery(id+"FHMxAyK4CFUKdhS_1.wireOp",EDGE,"1cb9c079-ea9b-4899-8069-e0e3048e911d.sketch_text.stroke-143"),sQuery(id+"FHMxAyK4CFUKdhS_1.wireOp",EDGE,"1cb9c079-ea9b-4899-8069-e0e3048e911d.sketch_text.stroke-144"),sQuery(id+"FHMxAyK4CFUKdhS_1.wireOp",EDGE,"1cb9c079-ea9b-4899-8069-e0e3048e911d.sketch_text.stroke-145"),sQuery(id+"FHMxAyK4CFUKdhS_1.wireOp",EDGE,"1cb9c079-ea9b-4899-8069-e0e3048e911d.sketch_text.stroke-146"),sQuery(id+"FHMxAyK4CFUKdhS_1.wireOp",EDGE,"1cb9c079-ea9b-4899-8069-e0e3048e911d.sketch_text.stroke-147"),sQuery(id+"FHMxAyK4CFUKdhS_1.wireOp",EDGE,"1cb9c079-ea9b-4899-8069-e0e3048e911d.sketch_text.stroke-148"),sQuery(id+"FHMxAyK4CFUKdhS_1.wireOp",EDGE,"1cb9c079-ea9b-4899-8069-e0e3048e911d.sketch_text.stroke-149"),sQuery(id+"FHMxAyK4CFUKdhS_1.wireOp",EDGE,"1cb9c079-ea9b-4899-8069-e0e3048e911d.sketch_text.stroke-150"),sQuery(id+"FHMxAyK4CFUKdhS_1.wireOp",EDGE,"1cb9c079-ea9b-4899-8069-e0e3048e911d.sketch_text.stroke-151"),sQuery(id+"FHMxAyK4CFUKdhS_1.wireOp",EDGE,"1cb9c079-ea9b-4899-8069-e0e3048e911d.sketch_text.stroke-152"),sQuery(id+"FHMxAyK4CFUKdhS_1.wireOp",EDGE,"1cb9c079-ea9b-4899-8069-e0e3048e911d.sketch_text.stroke-153"),sQuery(id+"FHMxAyK4CFUKdhS_1.wireOp",EDGE,"1cb9c079-ea9b-4899-8069-e0e3048e911d.sketch_text.stroke-159"),sQuery(id+"FHMxAyK4CFUKdhS_1.wireOp",EDGE,"1cb9c079-ea9b-4899-8069-e0e3048e911d.sketch_text.stroke-160"),sQuery(id+"FHMxAyK4CFUKdhS_1.wireOp",EDGE,"1cb9c079-ea9b-4899-8069-e0e3048e911d.sketch_text.stroke-161"),sQuery(id+"FHMxAyK4CFUKdhS_1.wireOp",EDGE,"1cb9c079-ea9b-4899-8069-e0e3048e911d.sketch_text.stroke-162"),sQuery(id+"FHMxAyK4CFUKdhS_1.wireOp",EDGE,"1cb9c079-ea9b-4899-8069-e0e3048e911d.sketch_text.stroke-163"),sQuery(id+"FHMxAyK4CFUKdhS_1.wireOp",EDGE,"1cb9c079-ea9b-4899-8069-e0e3048e911d.sketch_text.stroke-164"),sQuery(id+"FHMxAyK4CFUKdhS_1.wireOp",EDGE,"1cb9c079-ea9b-4899-8069-e0e3048e911d.sketch_text.stroke-165"),sQuery(id+"FHMxAyK4CFUKdhS_1.wireOp",EDGE,"1cb9c079-ea9b-4899-8069-e0e3048e911d.sketch_text.stroke-166"),sQuery(id+"FHMxAyK4CFUKdhS_1.wireOp",EDGE,"1cb9c079-ea9b-4899-8069-e0e3048e911d.sketch_text.stroke-167"),sQuery(id+"FHMxAyK4CFUKdhS_1.wireOp",EDGE,"1cb9c079-ea9b-4899-8069-e0e3048e911d.sketch_text.stroke-168"),sQuery(id+"FHMxAyK4CFUKdhS_1.wireOp",EDGE,"1cb9c079-ea9b-4899-8069-e0e3048e911d.sketch_text.stroke-169"),sQuery(id+"FHMxAyK4CFUKdhS_1.wireOp",EDGE,"1cb9c079-ea9b-4899-8069-e0e3048e911d.sketch_text.stroke-170"),sQuery(id+"FHMxAyK4CFUKdhS_1.wireOp",EDGE,"1cb9c079-ea9b-4899-8069-e0e3048e911d.sketch_text.stroke-171"),sQuery(id+"FHMxAyK4CFUKdhS_1.wireOp",EDGE,"1cb9c079-ea9b-4899-8069-e0e3048e911d.sketch_text.stroke-172"),sQuery(id+"FHMxAyK4CFUKdhS_1.wireOp",EDGE,"1cb9c079-ea9b-4899-8069-e0e3048e911d.sketch_text.stroke-173"),sQuery(id+"FHMxAyK4CFUKdhS_1.wireOp",EDGE,"1cb9c079-ea9b-4899-8069-e0e3048e911d.sketch_text.stroke-174"),sQuery(id+"FHMxAyK4CFUKdhS_1.wireOp",EDGE,"1cb9c079-ea9b-4899-8069-e0e3048e911d.sketch_text.stroke-175"),sQuery(id+"FHMxAyK4CFUKdhS_1.wireOp",EDGE,"1cb9c079-ea9b-4899-8069-e0e3048e911d.sketch_text.stroke-176"),sQuery(id+"FHMxAyK4CFUKdhS_1.wireOp",EDGE,"1cb9c079-ea9b-4899-8069-e0e3048e911d.sketch_text.stroke-177"),sQuery(id+"FHMxAyK4CFUKdhS_1.wireOp",EDGE,"1cb9c079-ea9b-4899-8069-e0e3048e911d.sketch_text.stroke-178"),sQuery(id+"FHMxAyK4CFUKdhS_1.wireOp",EDGE,"1cb9c079-ea9b-4899-8069-e0e3048e911d.sketch_text.stroke-179"),sQuery(id+"FHMxAyK4CFUKdhS_1.wireOp",EDGE,"1cb9c079-ea9b-4899-8069-e0e3048e911d.sketch_text.stroke-180"),sQuery(id+"F3.wireOp",EDGE,"E29"),subQ2])],"isStart":true}),makeQuery(id+"F4.opExtrude","SWEPT_FACE",FACE,{"disambiguationData":[OSD([subQ2])]})]),OD(1.0)],"derivedFrom":makeQuery(id+"F1.opExtrude","CAP_EDGE",EDGE,{"disambiguationData":[OSD([subQ0])],"isStart":false})});}
            fillet(context, id + "F5", {"entities" : qUnion([Q0, Q1, Q2, Q3, Q4, Q5, Q6, Q7, Q8, Q9, Q10, Q11, Q12, Q13, Q14, Q15, Q16, Q17, Q18, Q19, Q20, Q21, Q22, Q23, Q24, Q25, Q26, Q27]), "radius" : 5.08 * mm, "tangentPropagation" : true, "allowEdgeOverflow" : false});
        }
        {
            var Q0;
            Q0=makeQuery(id+"F2.imprint","IMPRINT",FACE,{"disambiguationData":[TD([[makeQuery(id+"F2.imprint","IMPRINT",EDGE,{"derivedFrom":makeQuery(id+"F1.opExtrude","CAP_EDGE",EDGE,{"disambiguationData":[OSD([sQuery(id+"F0.wireOp",EDGE,"E0.bottom")])],"isStart":false})}),-1.0]])]});
            var sketch = newSketch(context, id + "F6", { "sketchPlane" : qUnion([Q0])});
            skLineSegment(sketch, "E31.bottom", {"start": v(-277.87, 108.48) * mm, "end": v(319.03, 108.48) * mm});
            skLineSegment(sketch, "E31.top", {"start": v(-277.87, -94.72) * mm, "end": v(319.03, -94.72) * mm});
            skLineSegment(sketch, "E31.left", {"start": v(-277.87, 108.48) * mm, "end": v(-277.87, -94.72) * mm});
            skLineSegment(sketch, "E31.right", {"start": v(319.03, 108.48) * mm, "end": v(319.03, -94.72) * mm});
            skSolve(sketch);
        }
        {
            var Q0;
            Q0=makeQuery(id+"F6.imprint","IMPRINT",FACE,{"disambiguationData":[TD([[makeQuery(id+"F6.imprint","IMPRINT",EDGE,{"derivedFrom":sQuery(id+"F6.wireOp",EDGE,"E31.bottom")}),-1.0]])]});
            extrude(context, id + "F7", {"entities" : qUnion([Q0]), "operationType" : NewBodyOperationType.REMOVE, "oppositeDirection" : true, "depth" : 5.08 * mm, "offsetDistance" : 25.4 * mm});
        }
    });
